FCSTD DOCUMENT  (FreeCAD 1.0R39285 (Git))
Label: SectsAndVioletsCharacterIcons
License: All rights reserved
LicenseURL: https://en.wikipedia.org/wiki/All_rights_reserved
objects: Sketcher::SketchObject×25, Part::Extrusion×25, Part::Scale×25, Spreadsheet::Sheet×1
note: 100 computed .brp shape members not serialized (recipe doc carries the construction recipe); baked Part::Feature solids carry a one-line shape summary decoded from their .brp

FEATURE [Sketcher::SketchObject] Sketch026  label="Artist-Sketch"
  ArcFitTolerance = 1e-06
  FullyConstrained = false
  MakeInternals = false
  Placement = pos=(-10.0713,14.6686,0) rot=(0,0,1;0rad)
  expr: .Placement.Base.x = -(.Shape.BoundBox.XLength / 2)
  expr: .Placement.Base.y = .Shape.BoundBox.YLength / 2
  sketch-geometry (304):
    g0: BSplineCurve PolesCount=4 KnotsCount=2 Degree=3 IsPeriodic=0
    g1: BSplineCurve PolesCount=4 KnotsCount=2 Degree=3 IsPeriodic=0
    g2: BSplineCurve PolesCount=4 KnotsCount=2 Degree=3 IsPeriodic=0
    g3: BSplineCurve PolesCount=4 KnotsCount=2 Degree=3 IsPeriodic=0
    g4: BSplineCurve PolesCount=4 KnotsCount=2 Degree=3 IsPeriodic=0
    g5: BSplineCurve PolesCount=4 KnotsCount=2 Degree=3 IsPeriodic=0
    g6: BSplineCurve PolesCount=4 KnotsCount=2 Degree=3 IsPeriodic=0
    g7: BSplineCurve PolesCount=4 KnotsCount=2 Degree=3 IsPeriodic=0
    g8: BSplineCurve PolesCount=4 KnotsCount=2 Degree=3 IsPeriodic=0
    g9: BSplineCurve PolesCount=4 KnotsCount=2 Degree=3 IsPeriodic=0
    g10: BSplineCurve PolesCount=4 KnotsCount=2 Degree=3 IsPeriodic=0
    g11: BSplineCurve PolesCount=4 KnotsCount=2 Degree=3 IsPeriodic=0
    g12: BSplineCurve PolesCount=4 KnotsCount=2 Degree=3 IsPeriodic=0
    g13: BSplineCurve PolesCount=4 KnotsCount=2 Degree=3 IsPeriodic=0
    g14: BSplineCurve PolesCount=4 KnotsCount=2 Degree=3 IsPeriodic=0
    g15: BSplineCurve PolesCount=4 KnotsCount=2 Degree=3 IsPeriodic=0
    g16: BSplineCurve PolesCount=4 KnotsCount=2 Degree=3 IsPeriodic=0
    g17: BSplineCurve PolesCount=4 KnotsCount=2 Degree=3 IsPeriodic=0
    g18: BSplineCurve PolesCount=4 KnotsCount=2 Degree=3 IsPeriodic=0
    g19: BSplineCurve PolesCount=4 KnotsCount=2 Degree=3 IsPeriodic=0
    g20: BSplineCurve PolesCount=4 KnotsCount=2 Degree=3 IsPeriodic=0
    g21: BSplineCurve PolesCount=4 KnotsCount=2 Degree=3 IsPeriodic=0
    g22: BSplineCurve PolesCount=4 KnotsCount=2 Degree=3 IsPeriodic=0
    g23: BSplineCurve PolesCount=4 KnotsCount=2 Degree=3 IsPeriodic=0
    g24: BSplineCurve PolesCount=4 KnotsCount=2 Degree=3 IsPeriodic=0
    g25: BSplineCurve PolesCount=4 KnotsCount=2 Degree=3 IsPeriodic=0
    g26: BSplineCurve PolesCount=4 KnotsCount=2 Degree=3 IsPeriodic=0
    g27: BSplineCurve PolesCount=4 KnotsCount=2 Degree=3 IsPeriodic=0
    g28: BSplineCurve PolesCount=4 KnotsCount=2 Degree=3 IsPeriodic=0
    g29: BSplineCurve PolesCount=4 KnotsCount=2 Degree=3 IsPeriodic=0
    g30: BSplineCurve PolesCount=4 KnotsCount=2 Degree=3 IsPeriodic=0
    g31: BSplineCurve PolesCount=4 KnotsCount=2 Degree=3 IsPeriodic=0
    g32: BSplineCurve PolesCount=4 KnotsCount=2 Degree=3 IsPeriodic=0
    g33: BSplineCurve PolesCount=4 KnotsCount=2 Degree=3 IsPeriodic=0
    g34: BSplineCurve PolesCount=4 KnotsCount=2 Degree=3 IsPeriodic=0
    g35: BSplineCurve PolesCount=4 KnotsCount=2 Degree=3 IsPeriodic=0
    g36: BSplineCurve PolesCount=4 KnotsCount=2 Degree=3 IsPeriodic=0
    g37: BSplineCurve PolesCount=4 KnotsCount=2 Degree=3 IsPeriodic=0
    g38: BSplineCurve PolesCount=4 KnotsCount=2 Degree=3 IsPeriodic=0
    g39: BSplineCurve PolesCount=4 KnotsCount=2 Degree=3 IsPeriodic=0
    g40: BSplineCurve PolesCount=4 KnotsCount=2 Degree=3 IsPeriodic=0
    g41: BSplineCurve PolesCount=4 KnotsCount=2 Degree=3 IsPeriodic=0
    g42: BSplineCurve PolesCount=4 KnotsCount=2 Degree=3 IsPeriodic=0
    g43: BSplineCurve PolesCount=4 KnotsCount=2 Degree=3 IsPeriodic=0
    g44: BSplineCurve PolesCount=4 KnotsCount=2 Degree=3 IsPeriodic=0
    g45: BSplineCurve PolesCount=4 KnotsCount=2 Degree=3 IsPeriodic=0
    g46: BSplineCurve PolesCount=4 KnotsCount=2 Degree=3 IsPeriodic=0
    g47: BSplineCurve PolesCount=4 KnotsCount=2 Degree=3 IsPeriodic=0
    g48: BSplineCurve PolesCount=4 KnotsCount=2 Degree=3 IsPeriodic=0
    g49: BSplineCurve PolesCount=2 KnotsCount=2 Degree=1 IsPeriodic=0
    g50: BSplineCurve PolesCount=2 KnotsCount=2 Degree=1 IsPeriodic=0
    g51: BSplineCurve PolesCount=4 KnotsCount=2 Degree=3 IsPeriodic=0
    g52: BSplineCurve PolesCount=4 KnotsCount=2 Degree=3 IsPeriodic=0
    g53: BSplineCurve PolesCount=4 KnotsCount=2 Degree=3 IsPeriodic=0
    g54: BSplineCurve PolesCount=4 KnotsCount=2 Degree=3 IsPeriodic=0
    g55: BSplineCurve PolesCount=4 KnotsCount=2 Degree=3 IsPeriodic=0
    g56: BSplineCurve PolesCount=4 KnotsCount=2 Degree=3 IsPeriodic=0
    g57: BSplineCurve PolesCount=4 KnotsCount=2 Degree=3 IsPeriodic=0
    g58: BSplineCurve PolesCount=4 KnotsCount=2 Degree=3 IsPeriodic=0
    g59: BSplineCurve PolesCount=4 KnotsCount=2 Degree=3 IsPeriodic=0
    g60: BSplineCurve PolesCount=4 KnotsCount=2 Degree=3 IsPeriodic=0
    g61: BSplineCurve PolesCount=4 KnotsCount=2 Degree=3 IsPeriodic=0
    g62: BSplineCurve PolesCount=4 KnotsCount=2 Degree=3 IsPeriodic=0
    g63: BSplineCurve PolesCount=4 KnotsCount=2 Degree=3 IsPeriodic=0
    g64: BSplineCurve PolesCount=4 KnotsCount=2 Degree=3 IsPeriodic=0
    g65: BSplineCurve PolesCount=4 KnotsCount=2 Degree=3 IsPeriodic=0
    g66: BSplineCurve PolesCount=4 KnotsCount=2 Degree=3 IsPeriodic=0
    g67: BSplineCurve PolesCount=4 KnotsCount=2 Degree=3 IsPeriodic=0
    g68: BSplineCurve PolesCount=2 KnotsCount=2 Degree=1 IsPeriodic=0
    g69: BSplineCurve PolesCount=2 KnotsCount=2 Degree=1 IsPeriodic=0
    g70: BSplineCurve PolesCount=4 KnotsCount=2 Degree=3 IsPeriodic=0
    g71: BSplineCurve PolesCount=4 KnotsCount=2 Degree=3 IsPeriodic=0
    g72: BSplineCurve PolesCount=4 KnotsCount=2 Degree=3 IsPeriodic=0
    g73: BSplineCurve PolesCount=4 KnotsCount=2 Degree=3 IsPeriodic=0
    g74: BSplineCurve PolesCount=4 KnotsCount=2 Degree=3 IsPeriodic=0
    g75: BSplineCurve PolesCount=4 KnotsCount=2 Degree=3 IsPeriodic=0
    g76: BSplineCurve PolesCount=4 KnotsCount=2 Degree=3 IsPeriodic=0
    g77: BSplineCurve PolesCount=4 KnotsCount=2 Degree=3 IsPeriodic=0
    g78: BSplineCurve PolesCount=4 KnotsCount=2 Degree=3 IsPeriodic=0
    g79: BSplineCurve PolesCount=4 KnotsCount=2 Degree=3 IsPeriodic=0
    g80: BSplineCurve PolesCount=4 KnotsCount=2 Degree=3 IsPeriodic=0
    g81: BSplineCurve PolesCount=4 KnotsCount=2 Degree=3 IsPeriodic=0
    g82: BSplineCurve PolesCount=4 KnotsCount=2 Degree=3 IsPeriodic=0
    g83: BSplineCurve PolesCount=4 KnotsCount=2 Degree=3 IsPeriodic=0
    g84: BSplineCurve PolesCount=4 KnotsCount=2 Degree=3 IsPeriodic=0
    g85: BSplineCurve PolesCount=2 KnotsCount=2 Degree=1 IsPeriodic=0
    g86: BSplineCurve PolesCount=2 KnotsCount=2 Degree=1 IsPeriodic=0
    g87: BSplineCurve PolesCount=4 KnotsCount=2 Degree=3 IsPeriodic=0
    g88: BSplineCurve PolesCount=4 KnotsCount=2 Degree=3 IsPeriodic=0
    g89: BSplineCurve PolesCount=4 KnotsCount=2 Degree=3 IsPeriodic=0
    g90: BSplineCurve PolesCount=4 KnotsCount=2 Degree=3 IsPeriodic=0
    g91: BSplineCurve PolesCount=4 KnotsCount=2 Degree=3 IsPeriodic=0
    g92: BSplineCurve PolesCount=4 KnotsCount=2 Degree=3 IsPeriodic=0
    g93: BSplineCurve PolesCount=4 KnotsCount=2 Degree=3 IsPeriodic=0
    g94: BSplineCurve PolesCount=4 KnotsCount=2 Degree=3 IsPeriodic=0
    g95: BSplineCurve PolesCount=2 KnotsCount=2 Degree=1 IsPeriodic=0
    g96: BSplineCurve PolesCount=2 KnotsCount=2 Degree=1 IsPeriodic=0
    g97: BSplineCurve PolesCount=4 KnotsCount=2 Degree=3 IsPeriodic=0
    g98: BSplineCurve PolesCount=4 KnotsCount=2 Degree=3 IsPeriodic=0
    g99: BSplineCurve PolesCount=4 KnotsCount=2 Degree=3 IsPeriodic=0
    g100: BSplineCurve PolesCount=4 KnotsCount=2 Degree=3 IsPeriodic=0
    g101: BSplineCurve PolesCount=4 KnotsCount=2 Degree=3 IsPeriodic=0
    g102: BSplineCurve PolesCount=4 KnotsCount=2 Degree=3 IsPeriodic=0
    g103: BSplineCurve PolesCount=4 KnotsCount=2 Degree=3 IsPeriodic=0
    g104: BSplineCurve PolesCount=4 KnotsCount=2 Degree=3 IsPeriodic=0
    g105: BSplineCurve PolesCount=4 KnotsCount=2 Degree=3 IsPeriodic=0
    g106: BSplineCurve PolesCount=4 KnotsCount=2 Degree=3 IsPeriodic=0
    g107: BSplineCurve PolesCount=4 KnotsCount=2 Degree=3 IsPeriodic=0
    g108: BSplineCurve PolesCount=4 KnotsCount=2 Degree=3 IsPeriodic=0
    g109: BSplineCurve PolesCount=4 KnotsCount=2 Degree=3 IsPeriodic=0
    g110: BSplineCurve PolesCount=4 KnotsCount=2 Degree=3 IsPeriodic=0
    g111: BSplineCurve PolesCount=4 KnotsCount=2 Degree=3 IsPeriodic=0
    g112: BSplineCurve PolesCount=4 KnotsCount=2 Degree=3 IsPeriodic=0
    g113: BSplineCurve PolesCount=4 KnotsCount=2 Degree=3 IsPeriodic=0
    g114: BSplineCurve PolesCount=4 KnotsCount=2 Degree=3 IsPeriodic=0
    g115: BSplineCurve PolesCount=4 KnotsCount=2 Degree=3 IsPeriodic=0
    g116: BSplineCurve PolesCount=4 KnotsCount=2 Degree=3 IsPeriodic=0
    g117: BSplineCurve PolesCount=4 KnotsCount=2 Degree=3 IsPeriodic=0
    g118: BSplineCurve PolesCount=4 KnotsCount=2 Degree=3 IsPeriodic=0
    g119: BSplineCurve PolesCount=4 KnotsCount=2 Degree=3 IsPeriodic=0
    g120: BSplineCurve PolesCount=4 KnotsCount=2 Degree=3 IsPeriodic=0
    g121: BSplineCurve PolesCount=4 KnotsCount=2 Degree=3 IsPeriodic=0
    g122: BSplineCurve PolesCount=4 KnotsCount=2 Degree=3 IsPeriodic=0
    g123: BSplineCurve PolesCount=4 KnotsCount=2 Degree=3 IsPeriodic=0
    g124: BSplineCurve PolesCount=4 KnotsCount=2 Degree=3 IsPeriodic=0
    g125: BSplineCurve PolesCount=4 KnotsCount=2 Degree=3 IsPeriodic=0
    g126: BSplineCurve PolesCount=4 KnotsCount=2 Degree=3 IsPeriodic=0
    g127: BSplineCurve PolesCount=4 KnotsCount=2 Degree=3 IsPeriodic=0
    g128: BSplineCurve PolesCount=4 KnotsCount=2 Degree=3 IsPeriodic=0
    g129: BSplineCurve PolesCount=4 KnotsCount=2 Degree=3 IsPeriodic=0
    g130: BSplineCurve PolesCount=4 KnotsCount=2 Degree=3 IsPeriodic=0
    g131: BSplineCurve PolesCount=4 KnotsCount=2 Degree=3 IsPeriodic=0
    g132: BSplineCurve PolesCount=4 KnotsCount=2 Degree=3 IsPeriodic=0
    g133: BSplineCurve PolesCount=4 KnotsCount=2 Degree=3 IsPeriodic=0
    g134: BSplineCurve PolesCount=2 KnotsCount=2 Degree=1 IsPeriodic=0
    g135: BSplineCurve PolesCount=2 KnotsCount=2 Degree=1 IsPeriodic=0
    g136: BSplineCurve PolesCount=4 KnotsCount=2 Degree=3 IsPeriodic=0
    g137: BSplineCurve PolesCount=4 KnotsCount=2 Degree=3 IsPeriodic=0
    g138: BSplineCurve PolesCount=4 KnotsCount=2 Degree=3 IsPeriodic=0
    g139: BSplineCurve PolesCount=4 KnotsCount=2 Degree=3 IsPeriodic=0
    g140: BSplineCurve PolesCount=4 KnotsCount=2 Degree=3 IsPeriodic=0
    g141: BSplineCurve PolesCount=4 KnotsCount=2 Degree=3 IsPeriodic=0
    g142: BSplineCurve PolesCount=4 KnotsCount=2 Degree=3 IsPeriodic=0
    g143: BSplineCurve PolesCount=4 KnotsCount=2 Degree=3 IsPeriodic=0
    g144: BSplineCurve PolesCount=2 KnotsCount=2 Degree=1 IsPeriodic=0
    g145: BSplineCurve PolesCount=2 KnotsCount=2 Degree=1 IsPeriodic=0
    g146: BSplineCurve PolesCount=4 KnotsCount=2 Degree=3 IsPeriodic=0
    g147: BSplineCurve PolesCount=4 KnotsCount=2 Degree=3 IsPeriodic=0
    g148: BSplineCurve PolesCount=4 KnotsCount=2 Degree=3 IsPeriodic=0
    g149: BSplineCurve PolesCount=4 KnotsCount=2 Degree=3 IsPeriodic=0
    g150: BSplineCurve PolesCount=4 KnotsCount=2 Degree=3 IsPeriodic=0
    g151: BSplineCurve PolesCount=4 KnotsCount=2 Degree=3 IsPeriodic=0
    g152: BSplineCurve PolesCount=4 KnotsCount=2 Degree=3 IsPeriodic=0
    g153: BSplineCurve PolesCount=4 KnotsCount=2 Degree=3 IsPeriodic=0
    g154: BSplineCurve PolesCount=4 KnotsCount=2 Degree=3 IsPeriodic=0
    g155: BSplineCurve PolesCount=4 KnotsCount=2 Degree=3 IsPeriodic=0
    g156: BSplineCurve PolesCount=4 KnotsCount=2 Degree=3 IsPeriodic=0
    g157: BSplineCurve PolesCount=4 KnotsCount=2 Degree=3 IsPeriodic=0
    g158: BSplineCurve PolesCount=4 KnotsCount=2 Degree=3 IsPeriodic=0
    g159: BSplineCurve PolesCount=4 KnotsCount=2 Degree=3 IsPeriodic=0
    g160: BSplineCurve PolesCount=4 KnotsCount=2 Degree=3 IsPeriodic=0
    g161: BSplineCurve PolesCount=4 KnotsCount=2 Degree=3 IsPeriodic=0
    g162: BSplineCurve PolesCount=4 KnotsCount=2 Degree=3 IsPeriodic=0
    g163: BSplineCurve PolesCount=4 KnotsCount=2 Degree=3 IsPeriodic=0
    g164: BSplineCurve PolesCount=4 KnotsCount=2 Degree=3 IsPeriodic=0
    g165: BSplineCurve PolesCount=4 KnotsCount=2 Degree=3 IsPeriodic=0
    g166: BSplineCurve PolesCount=4 KnotsCount=2 Degree=3 IsPeriodic=0
    g167: BSplineCurve PolesCount=4 KnotsCount=2 Degree=3 IsPeriodic=0
    g168: BSplineCurve PolesCount=4 KnotsCount=2 Degree=3 IsPeriodic=0
    g169: BSplineCurve PolesCount=4 KnotsCount=2 Degree=3 IsPeriodic=0
    g170: BSplineCurve PolesCount=4 KnotsCount=2 Degree=3 IsPeriodic=0
    g171: BSplineCurve PolesCount=4 KnotsCount=2 Degree=3 IsPeriodic=0
    g172: BSplineCurve PolesCount=4 KnotsCount=2 Degree=3 IsPeriodic=0
    g173: BSplineCurve PolesCount=4 KnotsCount=2 Degree=3 IsPeriodic=0
    g174: BSplineCurve PolesCount=4 KnotsCount=2 Degree=3 IsPeriodic=0
    g175: BSplineCurve PolesCount=4 KnotsCount=2 Degree=3 IsPeriodic=0
    g176: BSplineCurve PolesCount=4 KnotsCount=2 Degree=3 IsPeriodic=0
    g177: BSplineCurve PolesCount=4 KnotsCount=2 Degree=3 IsPeriodic=0
    g178: BSplineCurve PolesCount=4 KnotsCount=2 Degree=3 IsPeriodic=0
    g179: BSplineCurve PolesCount=4 KnotsCount=2 Degree=3 IsPeriodic=0
    g180: BSplineCurve PolesCount=4 KnotsCount=2 Degree=3 IsPeriodic=0
    g181: BSplineCurve PolesCount=4 KnotsCount=2 Degree=3 IsPeriodic=0
    g182: BSplineCurve PolesCount=4 KnotsCount=2 Degree=3 IsPeriodic=0
    g183: BSplineCurve PolesCount=4 KnotsCount=2 Degree=3 IsPeriodic=0
    g184: BSplineCurve PolesCount=4 KnotsCount=2 Degree=3 IsPeriodic=0
    g185: BSplineCurve PolesCount=4 KnotsCount=2 Degree=3 IsPeriodic=0
    g186: BSplineCurve PolesCount=4 KnotsCount=2 Degree=3 IsPeriodic=0
    g187: BSplineCurve PolesCount=4 KnotsCount=2 Degree=3 IsPeriodic=0
    g188: BSplineCurve PolesCount=4 KnotsCount=2 Degree=3 IsPeriodic=0
    g189: BSplineCurve PolesCount=4 KnotsCount=2 Degree=3 IsPeriodic=0
    g190: BSplineCurve PolesCount=4 KnotsCount=2 Degree=3 IsPeriodic=0
    g191: BSplineCurve PolesCount=4 KnotsCount=2 Degree=3 IsPeriodic=0
    g192: BSplineCurve PolesCount=4 KnotsCount=2 Degree=3 IsPeriodic=0
    g193: BSplineCurve PolesCount=4 KnotsCount=2 Degree=3 IsPeriodic=0
    g194: BSplineCurve PolesCount=4 KnotsCount=2 Degree=3 IsPeriodic=0
    g195: BSplineCurve PolesCount=4 KnotsCount=2 Degree=3 IsPeriodic=0
    g196: BSplineCurve PolesCount=4 KnotsCount=2 Degree=3 IsPeriodic=0
    g197: BSplineCurve PolesCount=4 KnotsCount=2 Degree=3 IsPeriodic=0
    g198: BSplineCurve PolesCount=4 KnotsCount=2 Degree=3 IsPeriodic=0
    g199: BSplineCurve PolesCount=4 KnotsCount=2 Degree=3 IsPeriodic=0
    g200: BSplineCurve PolesCount=4 KnotsCount=2 Degree=3 IsPeriodic=0
    g201: BSplineCurve PolesCount=4 KnotsCount=2 Degree=3 IsPeriodic=0
    g202: BSplineCurve PolesCount=2 KnotsCount=2 Degree=1 IsPeriodic=0
    g203: BSplineCurve PolesCount=2 KnotsCount=2 Degree=1 IsPeriodic=0
    g204: BSplineCurve PolesCount=4 KnotsCount=2 Degree=3 IsPeriodic=0
    g205: BSplineCurve PolesCount=4 KnotsCount=2 Degree=3 IsPeriodic=0
    g206: BSplineCurve PolesCount=4 KnotsCount=2 Degree=3 IsPeriodic=0
    g207: BSplineCurve PolesCount=4 KnotsCount=2 Degree=3 IsPeriodic=0
    g208: BSplineCurve PolesCount=4 KnotsCount=2 Degree=3 IsPeriodic=0
    g209: BSplineCurve PolesCount=4 KnotsCount=2 Degree=3 IsPeriodic=0
    g210: BSplineCurve PolesCount=4 KnotsCount=2 Degree=3 IsPeriodic=0
    g211: BSplineCurve PolesCount=2 KnotsCount=2 Degree=1 IsPeriodic=0
    g212: BSplineCurve PolesCount=2 KnotsCount=2 Degree=1 IsPeriodic=0
    g213: BSplineCurve PolesCount=4 KnotsCount=2 Degree=3 IsPeriodic=0
    g214: BSplineCurve PolesCount=4 KnotsCount=2 Degree=3 IsPeriodic=0
    g215: BSplineCurve PolesCount=4 KnotsCount=2 Degree=3 IsPeriodic=0
    g216: BSplineCurve PolesCount=4 KnotsCount=2 Degree=3 IsPeriodic=0
    g217: BSplineCurve PolesCount=4 KnotsCount=2 Degree=3 IsPeriodic=0
    g218: BSplineCurve PolesCount=4 KnotsCount=2 Degree=3 IsPeriodic=0
    g219: BSplineCurve PolesCount=4 KnotsCount=2 Degree=3 IsPeriodic=0
    g220: BSplineCurve PolesCount=4 KnotsCount=2 Degree=3 IsPeriodic=0
    g221: BSplineCurve PolesCount=4 KnotsCount=2 Degree=3 IsPeriodic=0
    g222: BSplineCurve PolesCount=4 KnotsCount=2 Degree=3 IsPeriodic=0
    g223: BSplineCurve PolesCount=4 KnotsCount=2 Degree=3 IsPeriodic=0
    g224: BSplineCurve PolesCount=4 KnotsCount=2 Degree=3 IsPeriodic=0
    g225: BSplineCurve PolesCount=4 KnotsCount=2 Degree=3 IsPeriodic=0
    g226: BSplineCurve PolesCount=4 KnotsCount=2 Degree=3 IsPeriodic=0
    g227: BSplineCurve PolesCount=4 KnotsCount=2 Degree=3 IsPeriodic=0
    g228: BSplineCurve PolesCount=4 KnotsCount=2 Degree=3 IsPeriodic=0
    g229: BSplineCurve PolesCount=4 KnotsCount=2 Degree=3 IsPeriodic=0
    g230: BSplineCurve PolesCount=4 KnotsCount=2 Degree=3 IsPeriodic=0
    g231: BSplineCurve PolesCount=4 KnotsCount=2 Degree=3 IsPeriodic=0
    g232: BSplineCurve PolesCount=4 KnotsCount=2 Degree=3 IsPeriodic=0
    g233: BSplineCurve PolesCount=4 KnotsCount=2 Degree=3 IsPeriodic=0
    g234: BSplineCurve PolesCount=4 KnotsCount=2 Degree=3 IsPeriodic=0
    g235: BSplineCurve PolesCount=4 KnotsCount=2 Degree=3 IsPeriodic=0
    g236: BSplineCurve PolesCount=4 KnotsCount=2 Degree=3 IsPeriodic=0
    g237: BSplineCurve PolesCount=4 KnotsCount=2 Degree=3 IsPeriodic=0
    g238: BSplineCurve PolesCount=4 KnotsCount=2 Degree=3 IsPeriodic=0
    g239: BSplineCurve PolesCount=4 KnotsCount=2 Degree=3 IsPeriodic=0
    g240: BSplineCurve PolesCount=4 KnotsCount=2 Degree=3 IsPeriodic=0
    g241: BSplineCurve PolesCount=4 KnotsCount=2 Degree=3 IsPeriodic=0
    g242: BSplineCurve PolesCount=4 KnotsCount=2 Degree=3 IsPeriodic=0
    g243: BSplineCurve PolesCount=4 KnotsCount=2 Degree=3 IsPeriodic=0
    g244: BSplineCurve PolesCount=4 KnotsCount=2 Degree=3 IsPeriodic=0
    g245: BSplineCurve PolesCount=4 KnotsCount=2 Degree=3 IsPeriodic=0
    g246: BSplineCurve PolesCount=4 KnotsCount=2 Degree=3 IsPeriodic=0
    g247: BSplineCurve PolesCount=4 KnotsCount=2 Degree=3 IsPeriodic=0
    g248: BSplineCurve PolesCount=4 KnotsCount=2 Degree=3 IsPeriodic=0
    g249: BSplineCurve PolesCount=4 KnotsCount=2 Degree=3 IsPeriodic=0
    g250: BSplineCurve PolesCount=4 KnotsCount=2 Degree=3 IsPeriodic=0
    g251: BSplineCurve PolesCount=4 KnotsCount=2 Degree=3 IsPeriodic=0
    g252: BSplineCurve PolesCount=4 KnotsCount=2 Degree=3 IsPeriodic=0
    g253: BSplineCurve PolesCount=4 KnotsCount=2 Degree=3 IsPeriodic=0
    g254: BSplineCurve PolesCount=4 KnotsCount=2 Degree=3 IsPeriodic=0
    g255: BSplineCurve PolesCount=4 KnotsCount=2 Degree=3 IsPeriodic=0
    g256: BSplineCurve PolesCount=4 KnotsCount=2 Degree=3 IsPeriodic=0
    g257: BSplineCurve PolesCount=4 KnotsCount=2 Degree=3 IsPeriodic=0
    g258: BSplineCurve PolesCount=4 KnotsCount=2 Degree=3 IsPeriodic=0
    g259: BSplineCurve PolesCount=4 KnotsCount=2 Degree=3 IsPeriodic=0
    g260: BSplineCurve PolesCount=4 KnotsCount=2 Degree=3 IsPeriodic=0
    g261: BSplineCurve PolesCount=4 KnotsCount=2 Degree=3 IsPeriodic=0
    g262: BSplineCurve PolesCount=4 KnotsCount=2 Degree=3 IsPeriodic=0
    g263: BSplineCurve PolesCount=4 KnotsCount=2 Degree=3 IsPeriodic=0
    g264: BSplineCurve PolesCount=4 KnotsCount=2 Degree=3 IsPeriodic=0
    g265: BSplineCurve PolesCount=4 KnotsCount=2 Degree=3 IsPeriodic=0
    g266: BSplineCurve PolesCount=4 KnotsCount=2 Degree=3 IsPeriodic=0
    g267: BSplineCurve PolesCount=4 KnotsCount=2 Degree=3 IsPeriodic=0
    g268: BSplineCurve PolesCount=4 KnotsCount=2 Degree=3 IsPeriodic=0
    g269: BSplineCurve PolesCount=4 KnotsCount=2 Degree=3 IsPeriodic=0
    g270: BSplineCurve PolesCount=4 KnotsCount=2 Degree=3 IsPeriodic=0
    g271: BSplineCurve PolesCount=4 KnotsCount=2 Degree=3 IsPeriodic=0
    g272: BSplineCurve PolesCount=4 KnotsCount=2 Degree=3 IsPeriodic=0
    g273: BSplineCurve PolesCount=4 KnotsCount=2 Degree=3 IsPeriodic=0
    g274: BSplineCurve PolesCount=4 KnotsCount=2 Degree=3 IsPeriodic=0
    g275: BSplineCurve PolesCount=4 KnotsCount=2 Degree=3 IsPeriodic=0
    g276: BSplineCurve PolesCount=4 KnotsCount=2 Degree=3 IsPeriodic=0
    g277: BSplineCurve PolesCount=4 KnotsCount=2 Degree=3 IsPeriodic=0
    g278: BSplineCurve PolesCount=4 KnotsCount=2 Degree=3 IsPeriodic=0
    g279: BSplineCurve PolesCount=2 KnotsCount=2 Degree=1 IsPeriodic=0
    g280: BSplineCurve PolesCount=2 KnotsCount=2 Degree=1 IsPeriodic=0
    g281: BSplineCurve PolesCount=4 KnotsCount=2 Degree=3 IsPeriodic=0
    g282: BSplineCurve PolesCount=4 KnotsCount=2 Degree=3 IsPeriodic=0
    g283: BSplineCurve PolesCount=4 KnotsCount=2 Degree=3 IsPeriodic=0
    g284: BSplineCurve PolesCount=4 KnotsCount=2 Degree=3 IsPeriodic=0
    g285: BSplineCurve PolesCount=4 KnotsCount=2 Degree=3 IsPeriodic=0
    g286: BSplineCurve PolesCount=4 KnotsCount=2 Degree=3 IsPeriodic=0
    g287: BSplineCurve PolesCount=4 KnotsCount=2 Degree=3 IsPeriodic=0
    g288: BSplineCurve PolesCount=4 KnotsCount=2 Degree=3 IsPeriodic=0
    g289: BSplineCurve PolesCount=4 KnotsCount=2 Degree=3 IsPeriodic=0
    g290: BSplineCurve PolesCount=4 KnotsCount=2 Degree=3 IsPeriodic=0
    g291: BSplineCurve PolesCount=4 KnotsCount=2 Degree=3 IsPeriodic=0
    g292: BSplineCurve PolesCount=4 KnotsCount=2 Degree=3 IsPeriodic=0
    g293: BSplineCurve PolesCount=4 KnotsCount=2 Degree=3 IsPeriodic=0
    g294: BSplineCurve PolesCount=4 KnotsCount=2 Degree=3 IsPeriodic=0
    g295: BSplineCurve PolesCount=4 KnotsCount=2 Degree=3 IsPeriodic=0
    g296: BSplineCurve PolesCount=4 KnotsCount=2 Degree=3 IsPeriodic=0
    g297: BSplineCurve PolesCount=2 KnotsCount=2 Degree=1 IsPeriodic=0
    g298: BSplineCurve PolesCount=4 KnotsCount=2 Degree=3 IsPeriodic=0
    g299: BSplineCurve PolesCount=4 KnotsCount=2 Degree=3 IsPeriodic=0
    g300: BSplineCurve PolesCount=4 KnotsCount=2 Degree=3 IsPeriodic=0
    g301: BSplineCurve PolesCount=4 KnotsCount=2 Degree=3 IsPeriodic=0
    g302: BSplineCurve PolesCount=4 KnotsCount=2 Degree=3 IsPeriodic=0
    g303: BSplineCurve PolesCount=2 KnotsCount=2 Degree=1 IsPeriodic=0
  constraints (304):
    c: Coincident(g0,g1)
    c: Coincident(g1,g2)
    c: Coincident(g2,g3)
    c: Coincident(g3,g4)
    c: Coincident(g4,g5)
    c: Coincident(g5,g6)
    c: Coincident(g6,g7)
    c: Coincident(g7,g8)
    c: Coincident(g8,g9)
    c: Coincident(g9,g10)
    c: Coincident(g10,g11)
    c: Coincident(g11,g12)
    c: Coincident(g12,g0)
    c: Coincident(g13,g14)
    c: Coincident(g14,g15)
    c: Coincident(g15,g16)
    c: Coincident(g16,g13)
    c: Coincident(g17,g18)
    c: Coincident(g18,g19)
    c: Coincident(g19,g17)
    c: Coincident(g20,g21)
    c: Coincident(g21,g22)
    c: Coincident(g22,g23)
    c: Coincident(g23,g24)
    c: Coincident(g24,g25)
    c: Coincident(g25,g26)
    c: Coincident(g26,g27)
    c: Coincident(g27,g28)
    c: Coincident(g28,g29)
    c: Coincident(g29,g30)
    c: Coincident(g30,g31)
    c: Coincident(g31,g32)
    c: Coincident(g32,g20)
    c: Coincident(g33,g34)
    c: Coincident(g34,g35)
    c: Coincident(g35,g36)
    c: Coincident(g36,g37)
    c: Coincident(g37,g38)
    c: Coincident(g38,g39)
    c: Coincident(g39,g40)
    c: Coincident(g40,g41)
    c: Coincident(g41,g42)
    c: Coincident(g42,g43)
    c: Coincident(g43,g44)
    c: Coincident(g44,g45)
    c: Coincident(g45,g46)
    c: Coincident(g46,g47)
    c: Coincident(g47,g48)
    c: Coincident(g48,g49)
    c: Coincident(g49,g50)
    c: Coincident(g50,g51)
    c: Coincident(g51,g52)
    c: Coincident(g52,g53)
    c: Coincident(g53,g54)
    c: Coincident(g54,g55)
    c: Coincident(g55,g56)
    c: Coincident(g56,g57)
    c: Coincident(g57,g58)
    c: Coincident(g58,g59)
    c: Coincident(g59,g60)
    c: Coincident(g60,g61)
    c: Coincident(g61,g62)
    c: Coincident(g62,g63)
    c: Coincident(g63,g64)
    c: Coincident(g64,g65)
    c: Coincident(g65,g66)
    c: Coincident(g66,g67)
    c: Coincident(g67,g68)
    c: Coincident(g68,g69)
    c: Coincident(g69,g70)
    c: Coincident(g70,g71)
    c: Coincident(g71,g72)
    c: Coincident(g72,g73)
    c: Coincident(g73,g74)
    c: Coincident(g74,g75)
    c: Coincident(g75,g76)
    c: Coincident(g76,g77)
    c: Coincident(g77,g78)
    c: Coincident(g78,g79)
    c: Coincident(g79,g80)
    c: Coincident(g80,g81)
    c: Coincident(g81,g82)
    c: Coincident(g82,g83)
    c: Coincident(g83,g84)
    c: Coincident(g84,g85)
    c: Coincident(g85,g86)
    c: Coincident(g86,g87)
    c: Coincident(g87,g88)
    c: Coincident(g88,g89)
    c: Coincident(g89,g90)
    c: Coincident(g90,g91)
    c: Coincident(g91,g92)
    c: Coincident(g92,g93)
    c: Coincident(g93,g94)
    c: Coincident(g94,g95)
    c: Coincident(g95,g96)
    c: Coincident(g96,g97)
    c: Coincident(g97,g98)
    c: Coincident(g98,g99)
    c: Coincident(g99,g100)
    c: Coincident(g101,g102)
    c: Coincident(g102,g103)
    c: Coincident(g104,g105)
    c: Coincident(g105,g106)
    c: Coincident(g106,g104)
    c: Coincident(g107,g108)
    c: Coincident(g108,g109)
    c: Coincident(g109,g107)
    c: Coincident(g110,g111)
    c: Coincident(g111,g112)
    c: Coincident(g112,g113)
    c: Coincident(g113,g114)
    c: Coincident(g114,g115)
    c: Coincident(g115,g116)
    c: Coincident(g116,g110)
    c: Coincident(g117,g118)
    c: Coincident(g118,g119)
    c: Coincident(g119,g120)
    c: Coincident(g120,g121)
    c: Coincident(g121,g122)
    c: Coincident(g122,g123)
    c: Coincident(g124,g125)
    c: Coincident(g125,g126)
    c: Coincident(g126,g127)
    c: Coincident(g127,g128)
    c: Coincident(g128,g129)
    c: Coincident(g129,g130)
    c: Coincident(g130,g124)
    c: Coincident(g131,g132)
    c: Coincident(g132,g133)
    c: Coincident(g133,g134)
    c: Coincident(g134,g135)
    c: Coincident(g135,g136)
    c: Coincident(g136,g137)
    c: Coincident(g137,g138)
    c: Coincident(g138,g139)
    c: Coincident(g139,g140)
    c: Coincident(g140,g141)
    c: Coincident(g141,g142)
    c: Coincident(g142,g143)
    c: Coincident(g143,g144)
    c: Coincident(g144,g145)
    c: Coincident(g145,g146)
    c: Coincident(g146,g147)
    c: Coincident(g147,g148)
    c: Coincident(g148,g149)
    c: Coincident(g149,g150)
    c: Coincident(g150,g151)
    c: Coincident(g151,g152)
    c: Coincident(g152,g153)
    c: Coincident(g153,g154)
    c: Coincident(g154,g155)
    c: Coincident(g155,g156)
    c: Coincident(g156,g157)
    c: Coincident(g157,g158)
    c: Coincident(g158,g159)
    c: Coincident(g159,g160)
    c: Coincident(g160,g161)
    c: Coincident(g161,g162)
    c: Coincident(g162,g163)
    c: Coincident(g163,g164)
    c: Coincident(g165,g166)
    c: Coincident(g166,g167)
    c: Coincident(g167,g168)
    c: Coincident(g168,g165)
    c: Coincident(g169,g170)
    c: Coincident(g170,g171)
    c: Coincident(g172,g173)
    c: Coincident(g173,g174)
    c: Coincident(g174,g172)
    c: Coincident(g175,g176)
    c: Coincident(g176,g177)
    c: Coincident(g178,g179)
    c: Coincident(g179,g180)
    c: Coincident(g180,g181)
    c: Coincident(g181,g182)
    c: Coincident(g182,g183)
    c: Coincident(g183,g184)
    c: Coincident(g184,g178)
    c: Coincident(g185,g186)
    c: Coincident(g186,g187)
    c: Coincident(g187,g188)
    c: Coincident(g188,g189)
    c: Coincident(g189,g190)
    c: Coincident(g190,g191)
    c: Coincident(g192,g193)
    c: Coincident(g193,g194)
    c: Coincident(g194,g192)
    c: Coincident(g195,g196)
    c: Coincident(g196,g197)
    c: Coincident(g197,g198)
    c: Coincident(g198,g195)
    c: Coincident(g199,g200)
    c: Coincident(g200,g201)
    c: Coincident(g201,g202)
    c: Coincident(g202,g203)
    c: Coincident(g203,g204)
    c: Coincident(g204,g205)
    c: Coincident(g205,g199)
    c: Coincident(g206,g207)
    c: Coincident(g207,g208)
    c: Coincident(g208,g209)
    c: Coincident(g209,g206)
    c: Coincident(g210,g211)
    c: Coincident(g211,g212)
    c: Coincident(g212,g213)
    c: Coincident(g213,g214)
    c: Coincident(g215,g216)
    c: Coincident(g216,g217)
    c: Coincident(g217,g218)
    c: Coincident(g218,g215)
    c: Coincident(g219,g220)
    c: Coincident(g220,g221)
    c: Coincident(g221,g219)
    c: Coincident(g222,g223)
    c: Coincident(g223,g224)
    c: Coincident(g224,g222)
    c: Coincident(g225,g226)
    c: Coincident(g226,g227)
    c: Coincident(g227,g228)
    c: Coincident(g228,g229)
    c: Coincident(g229,g230)
    c: Coincident(g230,g231)
    c: Coincident(g231,g232)
    c: Coincident(g232,g233)
    c: Coincident(g233,g234)
    c: Coincident(g234,g235)
    c: Coincident(g235,g236)
    c: Coincident(g236,g237)
    c: Coincident(g237,g238)
    c: Coincident(g238,g239)
    c: Coincident(g239,g240)
    c: Coincident(g240,g241)
    c: Coincident(g241,g242)
    c: Coincident(g242,g243)
    c: Coincident(g243,g244)
    c: Coincident(g245,g246)
    c: Coincident(g246,g247)
    c: Coincident(g247,g248)
    c: Coincident(g248,g249)
    c: Coincident(g249,g250)
    c: Coincident(g250,g245)
    c: Coincident(g251,g252)
    c: Coincident(g252,g253)
    c: Coincident(g253,g254)
    c: Coincident(g254,g255)
    c: Coincident(g255,g251)
    c: Coincident(g256,g257)
    c: Coincident(g257,g258)
    c: Coincident(g258,g259)
    c: Coincident(g259,g256)
    c: Coincident(g260,g261)
    c: Coincident(g261,g262)
    c: Coincident(g262,g263)
    c: Coincident(g263,g264)
    c: Coincident(g264,g265)
    c: Coincident(g265,g266)
    c: Coincident(g266,g267)
    c: Coincident(g267,g268)
    c: Coincident(g268,g269)
    c: Coincident(g269,g270)
    c: Coincident(g270,g271)
    c: Coincident(g271,g272)
    c: Coincident(g272,g273)
    c: Coincident(g273,g274)
    c: Coincident(g275,g276)
    c: Coincident(g276,g277)
    c: Coincident(g277,g275)
    c: Coincident(g278,g279)
    c: Coincident(g279,g280)
    c: Coincident(g280,g281)
    c: Coincident(g281,g282)
    c: Coincident(g283,g284)
    c: Coincident(g284,g285)
    c: Coincident(g285,g286)
    c: Coincident(g286,g283)
    c: Coincident(g287,g288)
    c: Coincident(g288,g289)
    c: Coincident(g290,g291)
    c: Coincident(g291,g292)
    c: Coincident(g292,g293)
    c: Coincident(g293,g294)
    c: Coincident(g294,g295)
    c: Coincident(g295,g296)
    c: Coincident(g296,g290)
    c: Coincident(g297,g298)
    c: Coincident(g298,g299)
    c: Coincident(g299,g300)
    c: Coincident(g300,g301)
    c: Coincident(g301,g302)
    c: Coincident(g302,g303)
    c: Coincident(g303,g297)
    c: Coincident(g100,g33)
    c: Coincident(g287,g289)
    c: Coincident(g260,g274)
    c: Coincident(g169,g171)
    c: Coincident(g131,g164)
    c: Coincident(g210,g214)
    c: Coincident(g225,g244)
    c: Coincident(g101,g103)
    c: Coincident(g117,g123)
    c: Coincident(g185,g191)
    c: Coincident(g278,g282)
    c: Coincident(g175,g177)
FEATURE [Sketcher::SketchObject] Sketch028  label="Barber-Sketch"
  ArcFitTolerance = 1e-06
  FullyConstrained = false
  MakeInternals = false
  Placement = pos=(-6.26557,17.2877,0) rot=(0,0,1;0rad)
  expr: .Placement.Base.x = -(.Shape.BoundBox.XLength / 2)
  expr: .Placement.Base.y = .Shape.BoundBox.YLength / 2
  sketch-geometry (177):
    g0: BSplineCurve PolesCount=4 KnotsCount=2 Degree=3 IsPeriodic=0
    g1: BSplineCurve PolesCount=4 KnotsCount=2 Degree=3 IsPeriodic=0
    g2: BSplineCurve PolesCount=4 KnotsCount=2 Degree=3 IsPeriodic=0
    g3: BSplineCurve PolesCount=4 KnotsCount=2 Degree=3 IsPeriodic=0
    g4: BSplineCurve PolesCount=2 KnotsCount=2 Degree=1 IsPeriodic=0
    g5: BSplineCurve PolesCount=2 KnotsCount=2 Degree=1 IsPeriodic=0
    g6: BSplineCurve PolesCount=4 KnotsCount=2 Degree=3 IsPeriodic=0
    g7: BSplineCurve PolesCount=4 KnotsCount=2 Degree=3 IsPeriodic=0
    g8: BSplineCurve PolesCount=4 KnotsCount=2 Degree=3 IsPeriodic=0
    g9: BSplineCurve PolesCount=4 KnotsCount=2 Degree=3 IsPeriodic=0
    g10: BSplineCurve PolesCount=4 KnotsCount=2 Degree=3 IsPeriodic=0
    g11: BSplineCurve PolesCount=4 KnotsCount=2 Degree=3 IsPeriodic=0
    g12: BSplineCurve PolesCount=2 KnotsCount=2 Degree=1 IsPeriodic=0
    g13: BSplineCurve PolesCount=2 KnotsCount=2 Degree=1 IsPeriodic=0
    g14: BSplineCurve PolesCount=4 KnotsCount=2 Degree=3 IsPeriodic=0
    g15: BSplineCurve PolesCount=4 KnotsCount=2 Degree=3 IsPeriodic=0
    g16: BSplineCurve PolesCount=4 KnotsCount=2 Degree=3 IsPeriodic=0
    g17: BSplineCurve PolesCount=4 KnotsCount=2 Degree=3 IsPeriodic=0
    g18: BSplineCurve PolesCount=4 KnotsCount=2 Degree=3 IsPeriodic=0
    g19: BSplineCurve PolesCount=4 KnotsCount=2 Degree=3 IsPeriodic=0
    g20: BSplineCurve PolesCount=4 KnotsCount=2 Degree=3 IsPeriodic=0
    g21: BSplineCurve PolesCount=4 KnotsCount=2 Degree=3 IsPeriodic=0
    g22: BSplineCurve PolesCount=4 KnotsCount=2 Degree=3 IsPeriodic=0
    g23: BSplineCurve PolesCount=4 KnotsCount=2 Degree=3 IsPeriodic=0
    g24: BSplineCurve PolesCount=4 KnotsCount=2 Degree=3 IsPeriodic=0
    g25: BSplineCurve PolesCount=4 KnotsCount=2 Degree=3 IsPeriodic=0
    g26: BSplineCurve PolesCount=4 KnotsCount=2 Degree=3 IsPeriodic=0
    g27: BSplineCurve PolesCount=4 KnotsCount=2 Degree=3 IsPeriodic=0
    g28: BSplineCurve PolesCount=4 KnotsCount=2 Degree=3 IsPeriodic=0
    g29: BSplineCurve PolesCount=4 KnotsCount=2 Degree=3 IsPeriodic=0
    g30: BSplineCurve PolesCount=4 KnotsCount=2 Degree=3 IsPeriodic=0
    g31: BSplineCurve PolesCount=4 KnotsCount=2 Degree=3 IsPeriodic=0
    g32: BSplineCurve PolesCount=4 KnotsCount=2 Degree=3 IsPeriodic=0
    g33: BSplineCurve PolesCount=4 KnotsCount=2 Degree=3 IsPeriodic=0
    g34: BSplineCurve PolesCount=2 KnotsCount=2 Degree=1 IsPeriodic=0
    g35: BSplineCurve PolesCount=2 KnotsCount=2 Degree=1 IsPeriodic=0
    g36: BSplineCurve PolesCount=4 KnotsCount=2 Degree=3 IsPeriodic=0
    g37: BSplineCurve PolesCount=4 KnotsCount=2 Degree=3 IsPeriodic=0
    g38: BSplineCurve PolesCount=4 KnotsCount=2 Degree=3 IsPeriodic=0
    g39: BSplineCurve PolesCount=4 KnotsCount=2 Degree=3 IsPeriodic=0
    g40: BSplineCurve PolesCount=4 KnotsCount=2 Degree=3 IsPeriodic=0
    g41: BSplineCurve PolesCount=4 KnotsCount=2 Degree=3 IsPeriodic=0
    g42: BSplineCurve PolesCount=4 KnotsCount=2 Degree=3 IsPeriodic=0
    g43: BSplineCurve PolesCount=4 KnotsCount=2 Degree=3 IsPeriodic=0
    g44: BSplineCurve PolesCount=2 KnotsCount=2 Degree=1 IsPeriodic=0
    g45: BSplineCurve PolesCount=2 KnotsCount=2 Degree=1 IsPeriodic=0
    g46: BSplineCurve PolesCount=4 KnotsCount=2 Degree=3 IsPeriodic=0
    g47: BSplineCurve PolesCount=4 KnotsCount=2 Degree=3 IsPeriodic=0
    g48: BSplineCurve PolesCount=4 KnotsCount=2 Degree=3 IsPeriodic=0
    g49: BSplineCurve PolesCount=4 KnotsCount=2 Degree=3 IsPeriodic=0
    g50: BSplineCurve PolesCount=4 KnotsCount=2 Degree=3 IsPeriodic=0
    g51: BSplineCurve PolesCount=4 KnotsCount=2 Degree=3 IsPeriodic=0
    g52: BSplineCurve PolesCount=4 KnotsCount=2 Degree=3 IsPeriodic=0
    g53: BSplineCurve PolesCount=4 KnotsCount=2 Degree=3 IsPeriodic=0
    g54: BSplineCurve PolesCount=4 KnotsCount=2 Degree=3 IsPeriodic=0
    g55: BSplineCurve PolesCount=4 KnotsCount=2 Degree=3 IsPeriodic=0
    g56: BSplineCurve PolesCount=4 KnotsCount=2 Degree=3 IsPeriodic=0
    g57: BSplineCurve PolesCount=4 KnotsCount=2 Degree=3 IsPeriodic=0
    g58: BSplineCurve PolesCount=4 KnotsCount=2 Degree=3 IsPeriodic=0
    g59: BSplineCurve PolesCount=4 KnotsCount=2 Degree=3 IsPeriodic=0
    g60: BSplineCurve PolesCount=4 KnotsCount=2 Degree=3 IsPeriodic=0
    g61: BSplineCurve PolesCount=4 KnotsCount=2 Degree=3 IsPeriodic=0
    g62: BSplineCurve PolesCount=2 KnotsCount=2 Degree=1 IsPeriodic=0
    g63: BSplineCurve PolesCount=2 KnotsCount=2 Degree=1 IsPeriodic=0
    g64: BSplineCurve PolesCount=4 KnotsCount=2 Degree=3 IsPeriodic=0
    g65: BSplineCurve PolesCount=4 KnotsCount=2 Degree=3 IsPeriodic=0
    g66: BSplineCurve PolesCount=4 KnotsCount=2 Degree=3 IsPeriodic=0
    g67: BSplineCurve PolesCount=2 KnotsCount=2 Degree=1 IsPeriodic=0
    g68: BSplineCurve PolesCount=2 KnotsCount=2 Degree=1 IsPeriodic=0
    g69: BSplineCurve PolesCount=4 KnotsCount=2 Degree=3 IsPeriodic=0
    g70: BSplineCurve PolesCount=4 KnotsCount=2 Degree=3 IsPeriodic=0
    g71: BSplineCurve PolesCount=4 KnotsCount=2 Degree=3 IsPeriodic=0
    g72: BSplineCurve PolesCount=2 KnotsCount=2 Degree=1 IsPeriodic=0
    g73: BSplineCurve PolesCount=2 KnotsCount=2 Degree=1 IsPeriodic=0
    g74: BSplineCurve PolesCount=4 KnotsCount=2 Degree=3 IsPeriodic=0
    g75: BSplineCurve PolesCount=4 KnotsCount=2 Degree=3 IsPeriodic=0
    g76: BSplineCurve PolesCount=4 KnotsCount=2 Degree=3 IsPeriodic=0
    g77: BSplineCurve PolesCount=2 KnotsCount=2 Degree=1 IsPeriodic=0
    g78: BSplineCurve PolesCount=2 KnotsCount=2 Degree=1 IsPeriodic=0
    g79: BSplineCurve PolesCount=4 KnotsCount=2 Degree=3 IsPeriodic=0
    g80: BSplineCurve PolesCount=4 KnotsCount=2 Degree=3 IsPeriodic=0
    g81: BSplineCurve PolesCount=2 KnotsCount=2 Degree=1 IsPeriodic=0
    g82: BSplineCurve PolesCount=2 KnotsCount=2 Degree=1 IsPeriodic=0
    g83: BSplineCurve PolesCount=2 KnotsCount=2 Degree=1 IsPeriodic=0
    g84: BSplineCurve PolesCount=2 KnotsCount=2 Degree=1 IsPeriodic=0
    g85: BSplineCurve PolesCount=4 KnotsCount=2 Degree=3 IsPeriodic=0
    g86: BSplineCurve PolesCount=4 KnotsCount=2 Degree=3 IsPeriodic=0
    g87: BSplineCurve PolesCount=4 KnotsCount=2 Degree=3 IsPeriodic=0
    g88: BSplineCurve PolesCount=4 KnotsCount=2 Degree=3 IsPeriodic=0
    g89: BSplineCurve PolesCount=4 KnotsCount=2 Degree=3 IsPeriodic=0
    g90: BSplineCurve PolesCount=4 KnotsCount=2 Degree=3 IsPeriodic=0
    g91: BSplineCurve PolesCount=4 KnotsCount=2 Degree=3 IsPeriodic=0
    g92: BSplineCurve PolesCount=4 KnotsCount=2 Degree=3 IsPeriodic=0
    g93: BSplineCurve PolesCount=4 KnotsCount=2 Degree=3 IsPeriodic=0
    g94: BSplineCurve PolesCount=4 KnotsCount=2 Degree=3 IsPeriodic=0
    g95: BSplineCurve PolesCount=4 KnotsCount=2 Degree=3 IsPeriodic=0
    g96: BSplineCurve PolesCount=4 KnotsCount=2 Degree=3 IsPeriodic=0
    g97: BSplineCurve PolesCount=4 KnotsCount=2 Degree=3 IsPeriodic=0
    g98: BSplineCurve PolesCount=4 KnotsCount=2 Degree=3 IsPeriodic=0
    g99: BSplineCurve PolesCount=4 KnotsCount=2 Degree=3 IsPeriodic=0
    g100: BSplineCurve PolesCount=4 KnotsCount=2 Degree=3 IsPeriodic=0
    g101: BSplineCurve PolesCount=4 KnotsCount=2 Degree=3 IsPeriodic=0
    g102: BSplineCurve PolesCount=4 KnotsCount=2 Degree=3 IsPeriodic=0
    g103: BSplineCurve PolesCount=4 KnotsCount=2 Degree=3 IsPeriodic=0
    g104: BSplineCurve PolesCount=4 KnotsCount=2 Degree=3 IsPeriodic=0
    g105: BSplineCurve PolesCount=4 KnotsCount=2 Degree=3 IsPeriodic=0
    g106: BSplineCurve PolesCount=4 KnotsCount=2 Degree=3 IsPeriodic=0
    g107: BSplineCurve PolesCount=4 KnotsCount=2 Degree=3 IsPeriodic=0
    g108: BSplineCurve PolesCount=4 KnotsCount=2 Degree=3 IsPeriodic=0
    g109: BSplineCurve PolesCount=4 KnotsCount=2 Degree=3 IsPeriodic=0
    g110: BSplineCurve PolesCount=4 KnotsCount=2 Degree=3 IsPeriodic=0
    g111: BSplineCurve PolesCount=4 KnotsCount=2 Degree=3 IsPeriodic=0
    g112: BSplineCurve PolesCount=4 KnotsCount=2 Degree=3 IsPeriodic=0
    g113: BSplineCurve PolesCount=4 KnotsCount=2 Degree=3 IsPeriodic=0
    g114: BSplineCurve PolesCount=4 KnotsCount=2 Degree=3 IsPeriodic=0
    g115: BSplineCurve PolesCount=4 KnotsCount=2 Degree=3 IsPeriodic=0
    g116: BSplineCurve PolesCount=4 KnotsCount=2 Degree=3 IsPeriodic=0
    g117: BSplineCurve PolesCount=4 KnotsCount=2 Degree=3 IsPeriodic=0
    g118: BSplineCurve PolesCount=4 KnotsCount=2 Degree=3 IsPeriodic=0
    g119: BSplineCurve PolesCount=4 KnotsCount=2 Degree=3 IsPeriodic=0
    g120: BSplineCurve PolesCount=4 KnotsCount=2 Degree=3 IsPeriodic=0
    g121: BSplineCurve PolesCount=4 KnotsCount=2 Degree=3 IsPeriodic=0
    g122: BSplineCurve PolesCount=4 KnotsCount=2 Degree=3 IsPeriodic=0
    g123: BSplineCurve PolesCount=4 KnotsCount=2 Degree=3 IsPeriodic=0
    g124: BSplineCurve PolesCount=4 KnotsCount=2 Degree=3 IsPeriodic=0
    g125: BSplineCurve PolesCount=4 KnotsCount=2 Degree=3 IsPeriodic=0
    g126: BSplineCurve PolesCount=4 KnotsCount=2 Degree=3 IsPeriodic=0
    g127: BSplineCurve PolesCount=4 KnotsCount=2 Degree=3 IsPeriodic=0
    g128: BSplineCurve PolesCount=4 KnotsCount=2 Degree=3 IsPeriodic=0
    g129: BSplineCurve PolesCount=4 KnotsCount=2 Degree=3 IsPeriodic=0
    g130: BSplineCurve PolesCount=4 KnotsCount=2 Degree=3 IsPeriodic=0
    g131: BSplineCurve PolesCount=4 KnotsCount=2 Degree=3 IsPeriodic=0
    g132: BSplineCurve PolesCount=4 KnotsCount=2 Degree=3 IsPeriodic=0
    g133: BSplineCurve PolesCount=4 KnotsCount=2 Degree=3 IsPeriodic=0
    g134: BSplineCurve PolesCount=2 KnotsCount=2 Degree=1 IsPeriodic=0
    g135: BSplineCurve PolesCount=2 KnotsCount=2 Degree=1 IsPeriodic=0
    g136: BSplineCurve PolesCount=4 KnotsCount=2 Degree=3 IsPeriodic=0
    g137: BSplineCurve PolesCount=4 KnotsCount=2 Degree=3 IsPeriodic=0
    g138: BSplineCurve PolesCount=4 KnotsCount=2 Degree=3 IsPeriodic=0
    g139: BSplineCurve PolesCount=4 KnotsCount=2 Degree=3 IsPeriodic=0
    g140: BSplineCurve PolesCount=4 KnotsCount=2 Degree=3 IsPeriodic=0
    g141: BSplineCurve PolesCount=4 KnotsCount=2 Degree=3 IsPeriodic=0
    g142: BSplineCurve PolesCount=4 KnotsCount=2 Degree=3 IsPeriodic=0
    g143: BSplineCurve PolesCount=4 KnotsCount=2 Degree=3 IsPeriodic=0
    g144: BSplineCurve PolesCount=4 KnotsCount=2 Degree=3 IsPeriodic=0
    g145: BSplineCurve PolesCount=4 KnotsCount=2 Degree=3 IsPeriodic=0
    g146: BSplineCurve PolesCount=4 KnotsCount=2 Degree=3 IsPeriodic=0
    g147: BSplineCurve PolesCount=4 KnotsCount=2 Degree=3 IsPeriodic=0
    g148: BSplineCurve PolesCount=4 KnotsCount=2 Degree=3 IsPeriodic=0
    g149: BSplineCurve PolesCount=4 KnotsCount=2 Degree=3 IsPeriodic=0
    g150: BSplineCurve PolesCount=4 KnotsCount=2 Degree=3 IsPeriodic=0
    g151: BSplineCurve PolesCount=4 KnotsCount=2 Degree=3 IsPeriodic=0
    g152: BSplineCurve PolesCount=4 KnotsCount=2 Degree=3 IsPeriodic=0
    g153: BSplineCurve PolesCount=4 KnotsCount=2 Degree=3 IsPeriodic=0
    g154: BSplineCurve PolesCount=4 KnotsCount=2 Degree=3 IsPeriodic=0
    g155: BSplineCurve PolesCount=4 KnotsCount=2 Degree=3 IsPeriodic=0
    g156: BSplineCurve PolesCount=4 KnotsCount=2 Degree=3 IsPeriodic=0
    g157: BSplineCurve PolesCount=4 KnotsCount=2 Degree=3 IsPeriodic=0
    g158: BSplineCurve PolesCount=4 KnotsCount=2 Degree=3 IsPeriodic=0
    g159: BSplineCurve PolesCount=4 KnotsCount=2 Degree=3 IsPeriodic=0
    g160: BSplineCurve PolesCount=2 KnotsCount=2 Degree=1 IsPeriodic=0
    g161: BSplineCurve PolesCount=2 KnotsCount=2 Degree=1 IsPeriodic=0
    g162: BSplineCurve PolesCount=4 KnotsCount=2 Degree=3 IsPeriodic=0
    g163: BSplineCurve PolesCount=4 KnotsCount=2 Degree=3 IsPeriodic=0
    g164: BSplineCurve PolesCount=4 KnotsCount=2 Degree=3 IsPeriodic=0
    g165: BSplineCurve PolesCount=4 KnotsCount=2 Degree=3 IsPeriodic=0
    g166: BSplineCurve PolesCount=4 KnotsCount=2 Degree=3 IsPeriodic=0
    g167: BSplineCurve PolesCount=4 KnotsCount=2 Degree=3 IsPeriodic=0
    g168: BSplineCurve PolesCount=4 KnotsCount=2 Degree=3 IsPeriodic=0
    g169: BSplineCurve PolesCount=4 KnotsCount=2 Degree=3 IsPeriodic=0
    g170: BSplineCurve PolesCount=2 KnotsCount=2 Degree=1 IsPeriodic=0
    g171: BSplineCurve PolesCount=4 KnotsCount=2 Degree=3 IsPeriodic=0
    g172: BSplineCurve PolesCount=4 KnotsCount=2 Degree=3 IsPeriodic=0
    g173: BSplineCurve PolesCount=4 KnotsCount=2 Degree=3 IsPeriodic=0
    g174: BSplineCurve PolesCount=2 KnotsCount=2 Degree=1 IsPeriodic=0
    g175: BSplineCurve PolesCount=2 KnotsCount=2 Degree=1 IsPeriodic=0
    g176: BSplineCurve PolesCount=2 KnotsCount=2 Degree=1 IsPeriodic=0
  constraints (177):
    c: Coincident(g0,g1)
    c: Coincident(g1,g2)
    c: Coincident(g2,g3)
    c: Coincident(g3,g4)
    c: Coincident(g4,g5)
    c: Coincident(g5,g6)
    c: Coincident(g6,g7)
    c: Coincident(g7,g8)
    c: Coincident(g8,g9)
    c: Coincident(g9,g10)
    c: Coincident(g10,g11)
    c: Coincident(g11,g12)
    c: Coincident(g12,g13)
    c: Coincident(g13,g14)
    c: Coincident(g14,g15)
    c: Coincident(g15,g16)
    c: Coincident(g16,g17)
    c: Coincident(g17,g18)
    c: Coincident(g18,g19)
    c: Coincident(g19,g20)
    c: Coincident(g20,g21)
    c: Coincident(g21,g22)
    c: Coincident(g22,g23)
    c: Coincident(g23,g24)
    c: Coincident(g24,g25)
    c: Coincident(g25,g26)
    c: Coincident(g26,g27)
    c: Coincident(g27,g28)
    c: Coincident(g28,g29)
    c: Coincident(g29,g30)
    c: Coincident(g30,g0)
    c: Coincident(g31,g32)
    c: Coincident(g32,g33)
    c: Coincident(g33,g34)
    c: Coincident(g34,g35)
    c: Coincident(g35,g36)
    c: Coincident(g37,g38)
    c: Coincident(g38,g39)
    c: Coincident(g39,g37)
    c: Coincident(g40,g41)
    c: Coincident(g41,g42)
    c: Coincident(g42,g40)
    c: Coincident(g43,g44)
    c: Coincident(g44,g45)
    c: Coincident(g45,g46)
    c: Coincident(g46,g47)
    c: Coincident(g47,g48)
    c: Coincident(g48,g49)
    c: Coincident(g49,g50)
    c: Coincident(g50,g51)
    c: Coincident(g52,g53)
    c: Coincident(g53,g54)
    c: Coincident(g54,g55)
    c: Coincident(g55,g56)
    c: Coincident(g56,g57)
    c: Coincident(g57,g58)
    c: Coincident(g58,g52)
    c: Coincident(g59,g60)
    c: Coincident(g60,g61)
    c: Coincident(g61,g62)
    c: Coincident(g62,g63)
    c: Coincident(g63,g64)
    c: Coincident(g64,g65)
    c: Coincident(g65,g59)
    c: Coincident(g66,g67)
    c: Coincident(g67,g68)
    c: Coincident(g68,g69)
    c: Coincident(g69,g70)
    c: Coincident(g70,g71)
    c: Coincident(g71,g72)
    c: Coincident(g72,g73)
    c: Coincident(g73,g74)
    c: Coincident(g74,g75)
    c: Coincident(g75,g76)
    c: Coincident(g77,g78)
    c: Coincident(g78,g79)
    c: Coincident(g79,g80)
    c: Coincident(g80,g81)
    c: Coincident(g81,g82)
    c: Coincident(g82,g83)
    c: Coincident(g83,g84)
    c: Coincident(g84,g85)
    c: Coincident(g85,g86)
    c: Coincident(g86,g87)
    c: Coincident(g87,g88)
    c: Coincident(g89,g90)
    c: Coincident(g90,g91)
    c: Coincident(g92,g93)
    c: Coincident(g93,g94)
    c: Coincident(g94,g95)
    c: Coincident(g95,g92)
    c: Coincident(g96,g97)
    c: Coincident(g97,g98)
    c: Coincident(g98,g99)
    c: Coincident(g99,g100)
    c: Coincident(g100,g101)
    c: Coincident(g101,g102)
    c: Coincident(g102,g103)
    c: Coincident(g103,g104)
    c: Coincident(g104,g105)
    c: Coincident(g105,g106)
    c: Coincident(g107,g108)
    c: Coincident(g108,g109)
    c: Coincident(g109,g110)
    c: Coincident(g110,g111)
    c: Coincident(g111,g112)
    c: Coincident(g112,g113)
    c: Coincident(g113,g114)
    c: Coincident(g114,g115)
    c: Coincident(g115,g116)
    c: Coincident(g116,g117)
    c: Coincident(g117,g118)
    c: Coincident(g118,g119)
    c: Coincident(g119,g120)
    c: Coincident(g120,g121)
    c: Coincident(g121,g122)
    c: Coincident(g122,g123)
    c: Coincident(g123,g124)
    c: Coincident(g125,g126)
    c: Coincident(g126,g127)
    c: Coincident(g127,g128)
    c: Coincident(g128,g129)
    c: Coincident(g129,g130)
    c: Coincident(g130,g131)
    c: Coincident(g131,g132)
    c: Coincident(g132,g133)
    c: Coincident(g133,g134)
    c: Coincident(g134,g135)
    c: Coincident(g135,g136)
    c: Coincident(g136,g137)
    c: Coincident(g137,g138)
    c: Coincident(g138,g139)
    c: Coincident(g139,g140)
    c: Coincident(g140,g141)
    c: Coincident(g141,g142)
    c: Coincident(g142,g143)
    c: Coincident(g143,g144)
    c: Coincident(g144,g145)
    c: Coincident(g145,g146)
    c: Coincident(g146,g147)
    c: Coincident(g147,g148)
    c: Coincident(g149,g150)
    c: Coincident(g150,g151)
    c: Coincident(g151,g152)
    c: Coincident(g152,g153)
    c: Coincident(g153,g154)
    c: Coincident(g154,g155)
    c: Coincident(g155,g156)
    c: Coincident(g156,g157)
    c: Coincident(g157,g158)
    c: Coincident(g158,g159)
    c: Coincident(g159,g160)
    c: Coincident(g160,g161)
    c: Coincident(g161,g162)
    c: Coincident(g162,g163)
    c: Coincident(g163,g149)
    c: Coincident(g164,g165)
    c: Coincident(g165,g166)
    c: Coincident(g166,g164)
    c: Coincident(g167,g168)
    c: Coincident(g168,g169)
    c: Coincident(g170,g171)
    c: Coincident(g171,g172)
    c: Coincident(g172,g173)
    c: Coincident(g173,g174)
    c: Coincident(g174,g175)
    c: Coincident(g175,g176)
    c: Coincident(g176,g170)
    c: Coincident(g167,g169)
    c: Coincident(g125,g148)
    c: Coincident(g31,g36)
    c: Coincident(g89,g91)
    c: Coincident(g107,g124)
    c: Coincident(g77,g88)
    c: Coincident(g66,g76)
    c: Coincident(g43,g51)
    c: Coincident(g96,g106)
FEATURE [Sketcher::SketchObject] Sketch029  label="Cerenovus-Sketch"
  ArcFitTolerance = 1e-06
  FullyConstrained = false
  MakeInternals = false
  Placement = pos=(-12.6291,14.3334,0) rot=(0,0,1;0rad)
  expr: .Placement.Base.x = -(.Shape.BoundBox.XLength / 2)
  expr: .Placement.Base.y = .Shape.BoundBox.YLength / 2
  sketch-geometry (455):
    g0: BSplineCurve PolesCount=4 KnotsCount=2 Degree=3 IsPeriodic=0
    g1: BSplineCurve PolesCount=4 KnotsCount=2 Degree=3 IsPeriodic=0
    g2: BSplineCurve PolesCount=4 KnotsCount=2 Degree=3 IsPeriodic=0
    g3: BSplineCurve PolesCount=4 KnotsCount=2 Degree=3 IsPeriodic=0
    g4: BSplineCurve PolesCount=4 KnotsCount=2 Degree=3 IsPeriodic=0
    g5: BSplineCurve PolesCount=2 KnotsCount=2 Degree=1 IsPeriodic=0
    g6: BSplineCurve PolesCount=2 KnotsCount=2 Degree=1 IsPeriodic=0
    g7: BSplineCurve PolesCount=4 KnotsCount=2 Degree=3 IsPeriodic=0
    g8: BSplineCurve PolesCount=4 KnotsCount=2 Degree=3 IsPeriodic=0
    g9: BSplineCurve PolesCount=2 KnotsCount=2 Degree=1 IsPeriodic=0
    g10: BSplineCurve PolesCount=2 KnotsCount=2 Degree=1 IsPeriodic=0
    g11: BSplineCurve PolesCount=4 KnotsCount=2 Degree=3 IsPeriodic=0
    g12: BSplineCurve PolesCount=4 KnotsCount=2 Degree=3 IsPeriodic=0
    g13: BSplineCurve PolesCount=4 KnotsCount=2 Degree=3 IsPeriodic=0
    g14: BSplineCurve PolesCount=4 KnotsCount=2 Degree=3 IsPeriodic=0
    g15: BSplineCurve PolesCount=4 KnotsCount=2 Degree=3 IsPeriodic=0
    g16: BSplineCurve PolesCount=4 KnotsCount=2 Degree=3 IsPeriodic=0
    g17: BSplineCurve PolesCount=4 KnotsCount=2 Degree=3 IsPeriodic=0
    g18: BSplineCurve PolesCount=4 KnotsCount=2 Degree=3 IsPeriodic=0
    g19: BSplineCurve PolesCount=4 KnotsCount=2 Degree=3 IsPeriodic=0
    g20: BSplineCurve PolesCount=4 KnotsCount=2 Degree=3 IsPeriodic=0
    g21: BSplineCurve PolesCount=4 KnotsCount=2 Degree=3 IsPeriodic=0
    g22: BSplineCurve PolesCount=4 KnotsCount=2 Degree=3 IsPeriodic=0
    g23: BSplineCurve PolesCount=4 KnotsCount=2 Degree=3 IsPeriodic=0
    g24: BSplineCurve PolesCount=4 KnotsCount=2 Degree=3 IsPeriodic=0
    g25: BSplineCurve PolesCount=4 KnotsCount=2 Degree=3 IsPeriodic=0
    g26: BSplineCurve PolesCount=4 KnotsCount=2 Degree=3 IsPeriodic=0
    g27: BSplineCurve PolesCount=4 KnotsCount=2 Degree=3 IsPeriodic=0
    g28: BSplineCurve PolesCount=4 KnotsCount=2 Degree=3 IsPeriodic=0
    g29: BSplineCurve PolesCount=4 KnotsCount=2 Degree=3 IsPeriodic=0
    g30: BSplineCurve PolesCount=4 KnotsCount=2 Degree=3 IsPeriodic=0
    g31: BSplineCurve PolesCount=2 KnotsCount=2 Degree=1 IsPeriodic=0
    g32: BSplineCurve PolesCount=2 KnotsCount=2 Degree=1 IsPeriodic=0
    g33: BSplineCurve PolesCount=4 KnotsCount=2 Degree=3 IsPeriodic=0
    g34: BSplineCurve PolesCount=4 KnotsCount=2 Degree=3 IsPeriodic=0
    g35: BSplineCurve PolesCount=2 KnotsCount=2 Degree=1 IsPeriodic=0
    g36: BSplineCurve PolesCount=2 KnotsCount=2 Degree=1 IsPeriodic=0
    g37: BSplineCurve PolesCount=4 KnotsCount=2 Degree=3 IsPeriodic=0
    g38: BSplineCurve PolesCount=4 KnotsCount=2 Degree=3 IsPeriodic=0
    g39: BSplineCurve PolesCount=4 KnotsCount=2 Degree=3 IsPeriodic=0
    g40: BSplineCurve PolesCount=4 KnotsCount=2 Degree=3 IsPeriodic=0
    g41: BSplineCurve PolesCount=4 KnotsCount=2 Degree=3 IsPeriodic=0
    g42: BSplineCurve PolesCount=4 KnotsCount=2 Degree=3 IsPeriodic=0
    g43: BSplineCurve PolesCount=4 KnotsCount=2 Degree=3 IsPeriodic=0
    g44: BSplineCurve PolesCount=4 KnotsCount=2 Degree=3 IsPeriodic=0
    g45: BSplineCurve PolesCount=4 KnotsCount=2 Degree=3 IsPeriodic=0
    g46: BSplineCurve PolesCount=4 KnotsCount=2 Degree=3 IsPeriodic=0
    g47: BSplineCurve PolesCount=4 KnotsCount=2 Degree=3 IsPeriodic=0
    g48: BSplineCurve PolesCount=4 KnotsCount=2 Degree=3 IsPeriodic=0
    g49: BSplineCurve PolesCount=4 KnotsCount=2 Degree=3 IsPeriodic=0
    g50: BSplineCurve PolesCount=4 KnotsCount=2 Degree=3 IsPeriodic=0
    g51: BSplineCurve PolesCount=4 KnotsCount=2 Degree=3 IsPeriodic=0
    g52: BSplineCurve PolesCount=4 KnotsCount=2 Degree=3 IsPeriodic=0
    g53: BSplineCurve PolesCount=4 KnotsCount=2 Degree=3 IsPeriodic=0
    g54: BSplineCurve PolesCount=2 KnotsCount=2 Degree=1 IsPeriodic=0
    g55: BSplineCurve PolesCount=2 KnotsCount=2 Degree=1 IsPeriodic=0
    g56: BSplineCurve PolesCount=4 KnotsCount=2 Degree=3 IsPeriodic=0
    g57: BSplineCurve PolesCount=4 KnotsCount=2 Degree=3 IsPeriodic=0
    g58: BSplineCurve PolesCount=4 KnotsCount=2 Degree=3 IsPeriodic=0
    g59: BSplineCurve PolesCount=4 KnotsCount=2 Degree=3 IsPeriodic=0
    g60: BSplineCurve PolesCount=4 KnotsCount=2 Degree=3 IsPeriodic=0
    g61: BSplineCurve PolesCount=4 KnotsCount=2 Degree=3 IsPeriodic=0
    g62: BSplineCurve PolesCount=4 KnotsCount=2 Degree=3 IsPeriodic=0
    g63: BSplineCurve PolesCount=2 KnotsCount=2 Degree=1 IsPeriodic=0
    g64: BSplineCurve PolesCount=2 KnotsCount=2 Degree=1 IsPeriodic=0
    g65: BSplineCurve PolesCount=4 KnotsCount=2 Degree=3 IsPeriodic=0
    g66: BSplineCurve PolesCount=4 KnotsCount=2 Degree=3 IsPeriodic=0
    g67: BSplineCurve PolesCount=4 KnotsCount=2 Degree=3 IsPeriodic=0
    g68: BSplineCurve PolesCount=4 KnotsCount=2 Degree=3 IsPeriodic=0
    g69: BSplineCurve PolesCount=4 KnotsCount=2 Degree=3 IsPeriodic=0
    g70: BSplineCurve PolesCount=4 KnotsCount=2 Degree=3 IsPeriodic=0
    g71: BSplineCurve PolesCount=4 KnotsCount=2 Degree=3 IsPeriodic=0
    g72: BSplineCurve PolesCount=4 KnotsCount=2 Degree=3 IsPeriodic=0
    g73: BSplineCurve PolesCount=4 KnotsCount=2 Degree=3 IsPeriodic=0
    g74: BSplineCurve PolesCount=4 KnotsCount=2 Degree=3 IsPeriodic=0
    g75: BSplineCurve PolesCount=4 KnotsCount=2 Degree=3 IsPeriodic=0
    g76: BSplineCurve PolesCount=4 KnotsCount=2 Degree=3 IsPeriodic=0
    g77: BSplineCurve PolesCount=4 KnotsCount=2 Degree=3 IsPeriodic=0
    g78: BSplineCurve PolesCount=4 KnotsCount=2 Degree=3 IsPeriodic=0
    g79: BSplineCurve PolesCount=4 KnotsCount=2 Degree=3 IsPeriodic=0
    g80: BSplineCurve PolesCount=4 KnotsCount=2 Degree=3 IsPeriodic=0
    g81: BSplineCurve PolesCount=4 KnotsCount=2 Degree=3 IsPeriodic=0
    g82: BSplineCurve PolesCount=4 KnotsCount=2 Degree=3 IsPeriodic=0
    g83: BSplineCurve PolesCount=4 KnotsCount=2 Degree=3 IsPeriodic=0
    g84: BSplineCurve PolesCount=4 KnotsCount=2 Degree=3 IsPeriodic=0
    g85: BSplineCurve PolesCount=4 KnotsCount=2 Degree=3 IsPeriodic=0
    g86: BSplineCurve PolesCount=4 KnotsCount=2 Degree=3 IsPeriodic=0
    g87: BSplineCurve PolesCount=4 KnotsCount=2 Degree=3 IsPeriodic=0
    g88: BSplineCurve PolesCount=4 KnotsCount=2 Degree=3 IsPeriodic=0
    g89: BSplineCurve PolesCount=4 KnotsCount=2 Degree=3 IsPeriodic=0
    g90: BSplineCurve PolesCount=4 KnotsCount=2 Degree=3 IsPeriodic=0
    g91: BSplineCurve PolesCount=4 KnotsCount=2 Degree=3 IsPeriodic=0
    g92: BSplineCurve PolesCount=4 KnotsCount=2 Degree=3 IsPeriodic=0
    g93: BSplineCurve PolesCount=4 KnotsCount=2 Degree=3 IsPeriodic=0
    g94: BSplineCurve PolesCount=4 KnotsCount=2 Degree=3 IsPeriodic=0
    g95: BSplineCurve PolesCount=4 KnotsCount=2 Degree=3 IsPeriodic=0
    g96: BSplineCurve PolesCount=4 KnotsCount=2 Degree=3 IsPeriodic=0
    g97: BSplineCurve PolesCount=4 KnotsCount=2 Degree=3 IsPeriodic=0
    g98: BSplineCurve PolesCount=4 KnotsCount=2 Degree=3 IsPeriodic=0
    g99: BSplineCurve PolesCount=4 KnotsCount=2 Degree=3 IsPeriodic=0
    g100: BSplineCurve PolesCount=4 KnotsCount=2 Degree=3 IsPeriodic=0
    g101: BSplineCurve PolesCount=4 KnotsCount=2 Degree=3 IsPeriodic=0
    g102: BSplineCurve PolesCount=4 KnotsCount=2 Degree=3 IsPeriodic=0
    g103: BSplineCurve PolesCount=4 KnotsCount=2 Degree=3 IsPeriodic=0
    g104: BSplineCurve PolesCount=4 KnotsCount=2 Degree=3 IsPeriodic=0
    g105: BSplineCurve PolesCount=4 KnotsCount=2 Degree=3 IsPeriodic=0
    g106: BSplineCurve PolesCount=2 KnotsCount=2 Degree=1 IsPeriodic=0
    g107: BSplineCurve PolesCount=2 KnotsCount=2 Degree=1 IsPeriodic=0
    g108: BSplineCurve PolesCount=4 KnotsCount=2 Degree=3 IsPeriodic=0
    g109: BSplineCurve PolesCount=2 KnotsCount=2 Degree=1 IsPeriodic=0
    g110: BSplineCurve PolesCount=2 KnotsCount=2 Degree=1 IsPeriodic=0
    g111: BSplineCurve PolesCount=4 KnotsCount=2 Degree=3 IsPeriodic=0
    g112: BSplineCurve PolesCount=2 KnotsCount=2 Degree=1 IsPeriodic=0
    g113: BSplineCurve PolesCount=2 KnotsCount=2 Degree=1 IsPeriodic=0
    g114: BSplineCurve PolesCount=4 KnotsCount=2 Degree=3 IsPeriodic=0
    g115: BSplineCurve PolesCount=4 KnotsCount=2 Degree=3 IsPeriodic=0
    g116: BSplineCurve PolesCount=4 KnotsCount=2 Degree=3 IsPeriodic=0
    g117: BSplineCurve PolesCount=4 KnotsCount=2 Degree=3 IsPeriodic=0
    g118: BSplineCurve PolesCount=2 KnotsCount=2 Degree=1 IsPeriodic=0
    g119: BSplineCurve PolesCount=2 KnotsCount=2 Degree=1 IsPeriodic=0
    g120: BSplineCurve PolesCount=4 KnotsCount=2 Degree=3 IsPeriodic=0
    g121: BSplineCurve PolesCount=4 KnotsCount=2 Degree=3 IsPeriodic=0
    g122: BSplineCurve PolesCount=4 KnotsCount=2 Degree=3 IsPeriodic=0
    g123: BSplineCurve PolesCount=4 KnotsCount=2 Degree=3 IsPeriodic=0
    g124: BSplineCurve PolesCount=4 KnotsCount=2 Degree=3 IsPeriodic=0
    g125: BSplineCurve PolesCount=4 KnotsCount=2 Degree=3 IsPeriodic=0
    g126: BSplineCurve PolesCount=2 KnotsCount=2 Degree=1 IsPeriodic=0
    g127: BSplineCurve PolesCount=2 KnotsCount=2 Degree=1 IsPeriodic=0
    g128: BSplineCurve PolesCount=4 KnotsCount=2 Degree=3 IsPeriodic=0
    g129: BSplineCurve PolesCount=4 KnotsCount=2 Degree=3 IsPeriodic=0
    g130: BSplineCurve PolesCount=4 KnotsCount=2 Degree=3 IsPeriodic=0
    g131: BSplineCurve PolesCount=4 KnotsCount=2 Degree=3 IsPeriodic=0
    g132: BSplineCurve PolesCount=2 KnotsCount=2 Degree=1 IsPeriodic=0
    g133: BSplineCurve PolesCount=2 KnotsCount=2 Degree=1 IsPeriodic=0
    g134: BSplineCurve PolesCount=4 KnotsCount=2 Degree=3 IsPeriodic=0
    g135: BSplineCurve PolesCount=4 KnotsCount=2 Degree=3 IsPeriodic=0
    g136: BSplineCurve PolesCount=4 KnotsCount=2 Degree=3 IsPeriodic=0
    g137: BSplineCurve PolesCount=4 KnotsCount=2 Degree=3 IsPeriodic=0
    g138: BSplineCurve PolesCount=2 KnotsCount=2 Degree=1 IsPeriodic=0
    g139: BSplineCurve PolesCount=2 KnotsCount=2 Degree=1 IsPeriodic=0
    g140: BSplineCurve PolesCount=4 KnotsCount=2 Degree=3 IsPeriodic=0
    g141: BSplineCurve PolesCount=4 KnotsCount=2 Degree=3 IsPeriodic=0
    g142: BSplineCurve PolesCount=2 KnotsCount=2 Degree=1 IsPeriodic=0
    g143: BSplineCurve PolesCount=2 KnotsCount=2 Degree=1 IsPeriodic=0
    g144: BSplineCurve PolesCount=4 KnotsCount=2 Degree=3 IsPeriodic=0
    g145: BSplineCurve PolesCount=4 KnotsCount=2 Degree=3 IsPeriodic=0
    g146: BSplineCurve PolesCount=4 KnotsCount=2 Degree=3 IsPeriodic=0
    g147: BSplineCurve PolesCount=4 KnotsCount=2 Degree=3 IsPeriodic=0
    g148: BSplineCurve PolesCount=4 KnotsCount=2 Degree=3 IsPeriodic=0
    g149: BSplineCurve PolesCount=4 KnotsCount=2 Degree=3 IsPeriodic=0
    g150: BSplineCurve PolesCount=4 KnotsCount=2 Degree=3 IsPeriodic=0
    g151: BSplineCurve PolesCount=2 KnotsCount=2 Degree=1 IsPeriodic=0
    g152: BSplineCurve PolesCount=2 KnotsCount=2 Degree=1 IsPeriodic=0
    g153: BSplineCurve PolesCount=2 KnotsCount=2 Degree=1 IsPeriodic=0
    g154: BSplineCurve PolesCount=2 KnotsCount=2 Degree=1 IsPeriodic=0
    g155: BSplineCurve PolesCount=4 KnotsCount=2 Degree=3 IsPeriodic=0
    g156: BSplineCurve PolesCount=4 KnotsCount=2 Degree=3 IsPeriodic=0
    g157: BSplineCurve PolesCount=4 KnotsCount=2 Degree=3 IsPeriodic=0
    g158: BSplineCurve PolesCount=4 KnotsCount=2 Degree=3 IsPeriodic=0
    g159: BSplineCurve PolesCount=4 KnotsCount=2 Degree=3 IsPeriodic=0
    g160: BSplineCurve PolesCount=4 KnotsCount=2 Degree=3 IsPeriodic=0
    g161: BSplineCurve PolesCount=4 KnotsCount=2 Degree=3 IsPeriodic=0
    g162: BSplineCurve PolesCount=4 KnotsCount=2 Degree=3 IsPeriodic=0
    g163: BSplineCurve PolesCount=4 KnotsCount=2 Degree=3 IsPeriodic=0
    g164: BSplineCurve PolesCount=4 KnotsCount=2 Degree=3 IsPeriodic=0
    g165: BSplineCurve PolesCount=4 KnotsCount=2 Degree=3 IsPeriodic=0
    g166: BSplineCurve PolesCount=4 KnotsCount=2 Degree=3 IsPeriodic=0
    g167: BSplineCurve PolesCount=4 KnotsCount=2 Degree=3 IsPeriodic=0
    g168: BSplineCurve PolesCount=4 KnotsCount=2 Degree=3 IsPeriodic=0
    g169: BSplineCurve PolesCount=4 KnotsCount=2 Degree=3 IsPeriodic=0
    g170: BSplineCurve PolesCount=4 KnotsCount=2 Degree=3 IsPeriodic=0
    g171: BSplineCurve PolesCount=4 KnotsCount=2 Degree=3 IsPeriodic=0
    g172: BSplineCurve PolesCount=4 KnotsCount=2 Degree=3 IsPeriodic=0
    g173: BSplineCurve PolesCount=4 KnotsCount=2 Degree=3 IsPeriodic=0
    g174: BSplineCurve PolesCount=4 KnotsCount=2 Degree=3 IsPeriodic=0
    g175: BSplineCurve PolesCount=4 KnotsCount=2 Degree=3 IsPeriodic=0
    g176: BSplineCurve PolesCount=4 KnotsCount=2 Degree=3 IsPeriodic=0
    g177: BSplineCurve PolesCount=4 KnotsCount=2 Degree=3 IsPeriodic=0
    g178: BSplineCurve PolesCount=4 KnotsCount=2 Degree=3 IsPeriodic=0
    g179: BSplineCurve PolesCount=4 KnotsCount=2 Degree=3 IsPeriodic=0
    g180: BSplineCurve PolesCount=2 KnotsCount=2 Degree=1 IsPeriodic=0
    g181: BSplineCurve PolesCount=4 KnotsCount=2 Degree=3 IsPeriodic=0
    g182: BSplineCurve PolesCount=4 KnotsCount=2 Degree=3 IsPeriodic=0
    g183: BSplineCurve PolesCount=4 KnotsCount=2 Degree=3 IsPeriodic=0
    g184: BSplineCurve PolesCount=4 KnotsCount=2 Degree=3 IsPeriodic=0
    g185: BSplineCurve PolesCount=4 KnotsCount=2 Degree=3 IsPeriodic=0
    g186: BSplineCurve PolesCount=4 KnotsCount=2 Degree=3 IsPeriodic=0
    g187: BSplineCurve PolesCount=4 KnotsCount=2 Degree=3 IsPeriodic=0
    g188: BSplineCurve PolesCount=4 KnotsCount=2 Degree=3 IsPeriodic=0
    g189: BSplineCurve PolesCount=4 KnotsCount=2 Degree=3 IsPeriodic=0
    g190: BSplineCurve PolesCount=2 KnotsCount=2 Degree=1 IsPeriodic=0
    g191: BSplineCurve PolesCount=4 KnotsCount=2 Degree=3 IsPeriodic=0
    g192: BSplineCurve PolesCount=4 KnotsCount=2 Degree=3 IsPeriodic=0
    g193: BSplineCurve PolesCount=4 KnotsCount=2 Degree=3 IsPeriodic=0
    g194: BSplineCurve PolesCount=2 KnotsCount=2 Degree=1 IsPeriodic=0
    g195: BSplineCurve PolesCount=4 KnotsCount=2 Degree=3 IsPeriodic=0
    g196: BSplineCurve PolesCount=4 KnotsCount=2 Degree=3 IsPeriodic=0
    g197: BSplineCurve PolesCount=2 KnotsCount=2 Degree=1 IsPeriodic=0
    g198: BSplineCurve PolesCount=2 KnotsCount=2 Degree=1 IsPeriodic=0
    g199: BSplineCurve PolesCount=4 KnotsCount=2 Degree=3 IsPeriodic=0
    g200: BSplineCurve PolesCount=4 KnotsCount=2 Degree=3 IsPeriodic=0
    g201: BSplineCurve PolesCount=2 KnotsCount=2 Degree=1 IsPeriodic=0
    g202: BSplineCurve PolesCount=2 KnotsCount=2 Degree=1 IsPeriodic=0
    g203: BSplineCurve PolesCount=4 KnotsCount=2 Degree=3 IsPeriodic=0
    g204: BSplineCurve PolesCount=4 KnotsCount=2 Degree=3 IsPeriodic=0
    g205: BSplineCurve PolesCount=4 KnotsCount=2 Degree=3 IsPeriodic=0
    g206: BSplineCurve PolesCount=4 KnotsCount=2 Degree=3 IsPeriodic=0
    g207: BSplineCurve PolesCount=4 KnotsCount=2 Degree=3 IsPeriodic=0
    g208: BSplineCurve PolesCount=4 KnotsCount=2 Degree=3 IsPeriodic=0
    g209: BSplineCurve PolesCount=4 KnotsCount=2 Degree=3 IsPeriodic=0
    g210: BSplineCurve PolesCount=4 KnotsCount=2 Degree=3 IsPeriodic=0
    g211: BSplineCurve PolesCount=4 KnotsCount=2 Degree=3 IsPeriodic=0
    g212: BSplineCurve PolesCount=2 KnotsCount=2 Degree=1 IsPeriodic=0
    g213: BSplineCurve PolesCount=2 KnotsCount=2 Degree=1 IsPeriodic=0
    g214: BSplineCurve PolesCount=4 KnotsCount=2 Degree=3 IsPeriodic=0
    g215: BSplineCurve PolesCount=4 KnotsCount=2 Degree=3 IsPeriodic=0
    g216: BSplineCurve PolesCount=4 KnotsCount=2 Degree=3 IsPeriodic=0
    g217: BSplineCurve PolesCount=4 KnotsCount=2 Degree=3 IsPeriodic=0
    g218: BSplineCurve PolesCount=4 KnotsCount=2 Degree=3 IsPeriodic=0
    g219: BSplineCurve PolesCount=2 KnotsCount=2 Degree=1 IsPeriodic=0
    g220: BSplineCurve PolesCount=2 KnotsCount=2 Degree=1 IsPeriodic=0
    g221: BSplineCurve PolesCount=4 KnotsCount=2 Degree=3 IsPeriodic=0
    g222: BSplineCurve PolesCount=4 KnotsCount=2 Degree=3 IsPeriodic=0
    g223: BSplineCurve PolesCount=4 KnotsCount=2 Degree=3 IsPeriodic=0
    g224: BSplineCurve PolesCount=4 KnotsCount=2 Degree=3 IsPeriodic=0
    g225: BSplineCurve PolesCount=4 KnotsCount=2 Degree=3 IsPeriodic=0
    g226: BSplineCurve PolesCount=4 KnotsCount=2 Degree=3 IsPeriodic=0
    g227: BSplineCurve PolesCount=4 KnotsCount=2 Degree=3 IsPeriodic=0
    g228: BSplineCurve PolesCount=4 KnotsCount=2 Degree=3 IsPeriodic=0
    g229: BSplineCurve PolesCount=4 KnotsCount=2 Degree=3 IsPeriodic=0
    g230: BSplineCurve PolesCount=2 KnotsCount=2 Degree=1 IsPeriodic=0
    g231: BSplineCurve PolesCount=2 KnotsCount=2 Degree=1 IsPeriodic=0
    g232: BSplineCurve PolesCount=4 KnotsCount=2 Degree=3 IsPeriodic=0
    g233: BSplineCurve PolesCount=4 KnotsCount=2 Degree=3 IsPeriodic=0
    g234: BSplineCurve PolesCount=4 KnotsCount=2 Degree=3 IsPeriodic=0
    g235: BSplineCurve PolesCount=4 KnotsCount=2 Degree=3 IsPeriodic=0
    g236: BSplineCurve PolesCount=4 KnotsCount=2 Degree=3 IsPeriodic=0
    g237: BSplineCurve PolesCount=4 KnotsCount=2 Degree=3 IsPeriodic=0
    g238: BSplineCurve PolesCount=4 KnotsCount=2 Degree=3 IsPeriodic=0
    g239: BSplineCurve PolesCount=4 KnotsCount=2 Degree=3 IsPeriodic=0
    g240: BSplineCurve PolesCount=4 KnotsCount=2 Degree=3 IsPeriodic=0
    g241: BSplineCurve PolesCount=4 KnotsCount=2 Degree=3 IsPeriodic=0
    g242: BSplineCurve PolesCount=4 KnotsCount=2 Degree=3 IsPeriodic=0
    g243: BSplineCurve PolesCount=4 KnotsCount=2 Degree=3 IsPeriodic=0
    g244: BSplineCurve PolesCount=4 KnotsCount=2 Degree=3 IsPeriodic=0
    g245: BSplineCurve PolesCount=4 KnotsCount=2 Degree=3 IsPeriodic=0
    g246: BSplineCurve PolesCount=2 KnotsCount=2 Degree=1 IsPeriodic=0
    g247: BSplineCurve PolesCount=2 KnotsCount=2 Degree=1 IsPeriodic=0
    g248: BSplineCurve PolesCount=4 KnotsCount=2 Degree=3 IsPeriodic=0
    g249: BSplineCurve PolesCount=4 KnotsCount=2 Degree=3 IsPeriodic=0
    g250: BSplineCurve PolesCount=4 KnotsCount=2 Degree=3 IsPeriodic=0
    g251: BSplineCurve PolesCount=4 KnotsCount=2 Degree=3 IsPeriodic=0
    g252: BSplineCurve PolesCount=4 KnotsCount=2 Degree=3 IsPeriodic=0
    g253: BSplineCurve PolesCount=4 KnotsCount=2 Degree=3 IsPeriodic=0
    g254: BSplineCurve PolesCount=4 KnotsCount=2 Degree=3 IsPeriodic=0
    g255: BSplineCurve PolesCount=4 KnotsCount=2 Degree=3 IsPeriodic=0
    g256: BSplineCurve PolesCount=4 KnotsCount=2 Degree=3 IsPeriodic=0
    g257: BSplineCurve PolesCount=4 KnotsCount=2 Degree=3 IsPeriodic=0
    g258: BSplineCurve PolesCount=4 KnotsCount=2 Degree=3 IsPeriodic=0
    g259: BSplineCurve PolesCount=4 KnotsCount=2 Degree=3 IsPeriodic=0
    g260: BSplineCurve PolesCount=4 KnotsCount=2 Degree=3 IsPeriodic=0
    g261: BSplineCurve PolesCount=2 KnotsCount=2 Degree=1 IsPeriodic=0
    g262: BSplineCurve PolesCount=2 KnotsCount=2 Degree=1 IsPeriodic=0
    g263: BSplineCurve PolesCount=2 KnotsCount=2 Degree=1 IsPeriodic=0
    g264: BSplineCurve PolesCount=2 KnotsCount=2 Degree=1 IsPeriodic=0
    g265: BSplineCurve PolesCount=4 KnotsCount=2 Degree=3 IsPeriodic=0
    g266: BSplineCurve PolesCount=4 KnotsCount=2 Degree=3 IsPeriodic=0
    g267: BSplineCurve PolesCount=4 KnotsCount=2 Degree=3 IsPeriodic=0
    g268: BSplineCurve PolesCount=4 KnotsCount=2 Degree=3 IsPeriodic=0
    g269: BSplineCurve PolesCount=2 KnotsCount=2 Degree=1 IsPeriodic=0
    g270: BSplineCurve PolesCount=2 KnotsCount=2 Degree=1 IsPeriodic=0
    g271: BSplineCurve PolesCount=2 KnotsCount=2 Degree=1 IsPeriodic=0
    g272: BSplineCurve PolesCount=2 KnotsCount=2 Degree=1 IsPeriodic=0
    g273: BSplineCurve PolesCount=2 KnotsCount=2 Degree=1 IsPeriodic=0
    g274: BSplineCurve PolesCount=2 KnotsCount=2 Degree=1 IsPeriodic=0
    g275: BSplineCurve PolesCount=4 KnotsCount=2 Degree=3 IsPeriodic=0
    g276: BSplineCurve PolesCount=4 KnotsCount=2 Degree=3 IsPeriodic=0
    g277: BSplineCurve PolesCount=4 KnotsCount=2 Degree=3 IsPeriodic=0
    g278: BSplineCurve PolesCount=4 KnotsCount=2 Degree=3 IsPeriodic=0
    g279: BSplineCurve PolesCount=4 KnotsCount=2 Degree=3 IsPeriodic=0
    g280: BSplineCurve PolesCount=4 KnotsCount=2 Degree=3 IsPeriodic=0
    g281: BSplineCurve PolesCount=2 KnotsCount=2 Degree=1 IsPeriodic=0
    g282: BSplineCurve PolesCount=2 KnotsCount=2 Degree=1 IsPeriodic=0
    g283: BSplineCurve PolesCount=4 KnotsCount=2 Degree=3 IsPeriodic=0
    g284: BSplineCurve PolesCount=4 KnotsCount=2 Degree=3 IsPeriodic=0
    g285: BSplineCurve PolesCount=4 KnotsCount=2 Degree=3 IsPeriodic=0
    g286: BSplineCurve PolesCount=4 KnotsCount=2 Degree=3 IsPeriodic=0
    g287: BSplineCurve PolesCount=4 KnotsCount=2 Degree=3 IsPeriodic=0
    g288: BSplineCurve PolesCount=4 KnotsCount=2 Degree=3 IsPeriodic=0
    g289: BSplineCurve PolesCount=4 KnotsCount=2 Degree=3 IsPeriodic=0
    g290: BSplineCurve PolesCount=4 KnotsCount=2 Degree=3 IsPeriodic=0
    g291: BSplineCurve PolesCount=4 KnotsCount=2 Degree=3 IsPeriodic=0
    g292: BSplineCurve PolesCount=4 KnotsCount=2 Degree=3 IsPeriodic=0
    g293: BSplineCurve PolesCount=4 KnotsCount=2 Degree=3 IsPeriodic=0
    g294: BSplineCurve PolesCount=4 KnotsCount=2 Degree=3 IsPeriodic=0
    g295: BSplineCurve PolesCount=2 KnotsCount=2 Degree=1 IsPeriodic=0
    g296: BSplineCurve PolesCount=2 KnotsCount=2 Degree=1 IsPeriodic=0
    g297: BSplineCurve PolesCount=4 KnotsCount=2 Degree=3 IsPeriodic=0
    g298: BSplineCurve PolesCount=4 KnotsCount=2 Degree=3 IsPeriodic=0
    g299: BSplineCurve PolesCount=4 KnotsCount=2 Degree=3 IsPeriodic=0
    g300: BSplineCurve PolesCount=4 KnotsCount=2 Degree=3 IsPeriodic=0
    g301: BSplineCurve PolesCount=4 KnotsCount=2 Degree=3 IsPeriodic=0
    g302: BSplineCurve PolesCount=4 KnotsCount=2 Degree=3 IsPeriodic=0
    g303: BSplineCurve PolesCount=4 KnotsCount=2 Degree=3 IsPeriodic=0
    g304: BSplineCurve PolesCount=2 KnotsCount=2 Degree=1 IsPeriodic=0
    g305: BSplineCurve PolesCount=2 KnotsCount=2 Degree=1 IsPeriodic=0
    g306: BSplineCurve PolesCount=2 KnotsCount=2 Degree=1 IsPeriodic=0
    g307: BSplineCurve PolesCount=2 KnotsCount=2 Degree=1 IsPeriodic=0
    g308: BSplineCurve PolesCount=4 KnotsCount=2 Degree=3 IsPeriodic=0
    g309: BSplineCurve PolesCount=4 KnotsCount=2 Degree=3 IsPeriodic=0
    g310: BSplineCurve PolesCount=4 KnotsCount=2 Degree=3 IsPeriodic=0
    g311: BSplineCurve PolesCount=4 KnotsCount=2 Degree=3 IsPeriodic=0
    g312: BSplineCurve PolesCount=4 KnotsCount=2 Degree=3 IsPeriodic=0
    g313: BSplineCurve PolesCount=4 KnotsCount=2 Degree=3 IsPeriodic=0
    g314: BSplineCurve PolesCount=2 KnotsCount=2 Degree=1 IsPeriodic=0
    g315: BSplineCurve PolesCount=2 KnotsCount=2 Degree=1 IsPeriodic=0
    g316: BSplineCurve PolesCount=4 KnotsCount=2 Degree=3 IsPeriodic=0
    g317: BSplineCurve PolesCount=4 KnotsCount=2 Degree=3 IsPeriodic=0
    g318: BSplineCurve PolesCount=4 KnotsCount=2 Degree=3 IsPeriodic=0
    g319: BSplineCurve PolesCount=4 KnotsCount=2 Degree=3 IsPeriodic=0
    g320: BSplineCurve PolesCount=4 KnotsCount=2 Degree=3 IsPeriodic=0
    g321: BSplineCurve PolesCount=2 KnotsCount=2 Degree=1 IsPeriodic=0
    g322: BSplineCurve PolesCount=2 KnotsCount=2 Degree=1 IsPeriodic=0
    g323: BSplineCurve PolesCount=2 KnotsCount=2 Degree=1 IsPeriodic=0
    g324: BSplineCurve PolesCount=2 KnotsCount=2 Degree=1 IsPeriodic=0
    g325: BSplineCurve PolesCount=4 KnotsCount=2 Degree=3 IsPeriodic=0
    g326: BSplineCurve PolesCount=2 KnotsCount=2 Degree=1 IsPeriodic=0
    g327: BSplineCurve PolesCount=2 KnotsCount=2 Degree=1 IsPeriodic=0
    g328: BSplineCurve PolesCount=2 KnotsCount=2 Degree=1 IsPeriodic=0
    g329: BSplineCurve PolesCount=2 KnotsCount=2 Degree=1 IsPeriodic=0
    g330: BSplineCurve PolesCount=4 KnotsCount=2 Degree=3 IsPeriodic=0
    g331: BSplineCurve PolesCount=4 KnotsCount=2 Degree=3 IsPeriodic=0
    g332: BSplineCurve PolesCount=2 KnotsCount=2 Degree=1 IsPeriodic=0
    g333: BSplineCurve PolesCount=2 KnotsCount=2 Degree=1 IsPeriodic=0
    g334: BSplineCurve PolesCount=4 KnotsCount=2 Degree=3 IsPeriodic=0
    g335: BSplineCurve PolesCount=4 KnotsCount=2 Degree=3 IsPeriodic=0
    g336: BSplineCurve PolesCount=4 KnotsCount=2 Degree=3 IsPeriodic=0
    g337: BSplineCurve PolesCount=4 KnotsCount=2 Degree=3 IsPeriodic=0
    g338: BSplineCurve PolesCount=4 KnotsCount=2 Degree=3 IsPeriodic=0
    g339: BSplineCurve PolesCount=4 KnotsCount=2 Degree=3 IsPeriodic=0
    g340: BSplineCurve PolesCount=2 KnotsCount=2 Degree=1 IsPeriodic=0
    g341: BSplineCurve PolesCount=2 KnotsCount=2 Degree=1 IsPeriodic=0
    g342: BSplineCurve PolesCount=2 KnotsCount=2 Degree=1 IsPeriodic=0
    g343: BSplineCurve PolesCount=2 KnotsCount=2 Degree=1 IsPeriodic=0
    g344: BSplineCurve PolesCount=2 KnotsCount=2 Degree=1 IsPeriodic=0
    g345: BSplineCurve PolesCount=2 KnotsCount=2 Degree=1 IsPeriodic=0
    g346: BSplineCurve PolesCount=4 KnotsCount=2 Degree=3 IsPeriodic=0
    g347: BSplineCurve PolesCount=4 KnotsCount=2 Degree=3 IsPeriodic=0
    g348: BSplineCurve PolesCount=4 KnotsCount=2 Degree=3 IsPeriodic=0
    g349: BSplineCurve PolesCount=4 KnotsCount=2 Degree=3 IsPeriodic=0
    g350: BSplineCurve PolesCount=4 KnotsCount=2 Degree=3 IsPeriodic=0
    g351: BSplineCurve PolesCount=4 KnotsCount=2 Degree=3 IsPeriodic=0
    g352: BSplineCurve PolesCount=4 KnotsCount=2 Degree=3 IsPeriodic=0
    g353: BSplineCurve PolesCount=4 KnotsCount=2 Degree=3 IsPeriodic=0
    g354: BSplineCurve PolesCount=4 KnotsCount=2 Degree=3 IsPeriodic=0
    g355: BSplineCurve PolesCount=4 KnotsCount=2 Degree=3 IsPeriodic=0
    g356: BSplineCurve PolesCount=4 KnotsCount=2 Degree=3 IsPeriodic=0
    g357: BSplineCurve PolesCount=4 KnotsCount=2 Degree=3 IsPeriodic=0
    g358: BSplineCurve PolesCount=2 KnotsCount=2 Degree=1 IsPeriodic=0
    g359: BSplineCurve PolesCount=2 KnotsCount=2 Degree=1 IsPeriodic=0
    g360: BSplineCurve PolesCount=4 KnotsCount=2 Degree=3 IsPeriodic=0
    g361: BSplineCurve PolesCount=4 KnotsCount=2 Degree=3 IsPeriodic=0
    g362: BSplineCurve PolesCount=4 KnotsCount=2 Degree=3 IsPeriodic=0
    g363: BSplineCurve PolesCount=4 KnotsCount=2 Degree=3 IsPeriodic=0
    g364: BSplineCurve PolesCount=4 KnotsCount=2 Degree=3 IsPeriodic=0
    g365: BSplineCurve PolesCount=4 KnotsCount=2 Degree=3 IsPeriodic=0
    g366: BSplineCurve PolesCount=4 KnotsCount=2 Degree=3 IsPeriodic=0
    g367: BSplineCurve PolesCount=4 KnotsCount=2 Degree=3 IsPeriodic=0
    g368: BSplineCurve PolesCount=2 KnotsCount=2 Degree=1 IsPeriodic=0
    g369: BSplineCurve PolesCount=2 KnotsCount=2 Degree=1 IsPeriodic=0
    g370: BSplineCurve PolesCount=4 KnotsCount=2 Degree=3 IsPeriodic=0
    g371: BSplineCurve PolesCount=4 KnotsCount=2 Degree=3 IsPeriodic=0
    g372: BSplineCurve PolesCount=4 KnotsCount=2 Degree=3 IsPeriodic=0
    g373: BSplineCurve PolesCount=4 KnotsCount=2 Degree=3 IsPeriodic=0
    g374: BSplineCurve PolesCount=4 KnotsCount=2 Degree=3 IsPeriodic=0
    g375: BSplineCurve PolesCount=4 KnotsCount=2 Degree=3 IsPeriodic=0
    g376: BSplineCurve PolesCount=4 KnotsCount=2 Degree=3 IsPeriodic=0
    g377: BSplineCurve PolesCount=4 KnotsCount=2 Degree=3 IsPeriodic=0
    g378: BSplineCurve PolesCount=4 KnotsCount=2 Degree=3 IsPeriodic=0
    g379: BSplineCurve PolesCount=4 KnotsCount=2 Degree=3 IsPeriodic=0
    g380: BSplineCurve PolesCount=4 KnotsCount=2 Degree=3 IsPeriodic=0
    g381: BSplineCurve PolesCount=4 KnotsCount=2 Degree=3 IsPeriodic=0
    g382: BSplineCurve PolesCount=4 KnotsCount=2 Degree=3 IsPeriodic=0
    g383: BSplineCurve PolesCount=4 KnotsCount=2 Degree=3 IsPeriodic=0
    g384: BSplineCurve PolesCount=4 KnotsCount=2 Degree=3 IsPeriodic=0
    g385: BSplineCurve PolesCount=4 KnotsCount=2 Degree=3 IsPeriodic=0
    g386: BSplineCurve PolesCount=4 KnotsCount=2 Degree=3 IsPeriodic=0
    g387: BSplineCurve PolesCount=4 KnotsCount=2 Degree=3 IsPeriodic=0
    g388: BSplineCurve PolesCount=4 KnotsCount=2 Degree=3 IsPeriodic=0
    g389: BSplineCurve PolesCount=4 KnotsCount=2 Degree=3 IsPeriodic=0
    g390: BSplineCurve PolesCount=4 KnotsCount=2 Degree=3 IsPeriodic=0
    g391: BSplineCurve PolesCount=4 KnotsCount=2 Degree=3 IsPeriodic=0
    g392: BSplineCurve PolesCount=4 KnotsCount=2 Degree=3 IsPeriodic=0
    g393: BSplineCurve PolesCount=4 KnotsCount=2 Degree=3 IsPeriodic=0
    g394: BSplineCurve PolesCount=4 KnotsCount=2 Degree=3 IsPeriodic=0
    g395: BSplineCurve PolesCount=4 KnotsCount=2 Degree=3 IsPeriodic=0
    g396: BSplineCurve PolesCount=4 KnotsCount=2 Degree=3 IsPeriodic=0
    g397: BSplineCurve PolesCount=4 KnotsCount=2 Degree=3 IsPeriodic=0
    g398: BSplineCurve PolesCount=4 KnotsCount=2 Degree=3 IsPeriodic=0
    g399: BSplineCurve PolesCount=4 KnotsCount=2 Degree=3 IsPeriodic=0
    ... +55 more geometry lines
  constraints (455):
    c: Coincident(g0,g1)
    c: Coincident(g1,g2)
    c: Coincident(g2,g3)
    c: Coincident(g3,g4)
    c: Coincident(g4,g5)
    c: Coincident(g5,g6)
    c: Coincident(g6,g7)
    c: Coincident(g7,g8)
    c: Coincident(g8,g9)
    c: Coincident(g9,g10)
    c: Coincident(g10,g11)
    c: Coincident(g11,g12)
    c: Coincident(g12,g13)
    c: Coincident(g13,g14)
    c: Coincident(g14,g15)
    c: Coincident(g15,g16)
    c: Coincident(g16,g17)
    c: Coincident(g17,g18)
    c: Coincident(g18,g19)
    c: Coincident(g19,g20)
    c: Coincident(g20,g21)
    c: Coincident(g21,g22)
    c: Coincident(g22,g23)
    c: Coincident(g23,g24)
    c: Coincident(g24,g25)
    c: Coincident(g25,g26)
    c: Coincident(g26,g27)
    c: Coincident(g27,g28)
    c: Coincident(g28,g29)
    c: Coincident(g29,g30)
    c: Coincident(g30,g31)
    c: Coincident(g31,g32)
    c: Coincident(g32,g33)
    c: Coincident(g33,g34)
    c: Coincident(g34,g35)
    c: Coincident(g35,g36)
    c: Coincident(g36,g37)
    c: Coincident(g37,g38)
    c: Coincident(g38,g39)
    c: Coincident(g39,g40)
    c: Coincident(g40,g41)
    c: Coincident(g41,g42)
    c: Coincident(g42,g43)
    c: Coincident(g43,g44)
    c: Coincident(g44,g45)
    c: Coincident(g45,g46)
    c: Coincident(g46,g47)
    c: Coincident(g47,g48)
    c: Coincident(g48,g49)
    c: Coincident(g49,g50)
    c: Coincident(g50,g51)
    c: Coincident(g52,g53)
    c: Coincident(g53,g54)
    c: Coincident(g54,g55)
    c: Coincident(g55,g56)
    c: Coincident(g56,g57)
    c: Coincident(g57,g58)
    c: Coincident(g58,g59)
    c: Coincident(g59,g60)
    c: Coincident(g60,g61)
    c: Coincident(g61,g62)
    c: Coincident(g62,g63)
    c: Coincident(g63,g64)
    c: Coincident(g64,g65)
    c: Coincident(g65,g66)
    c: Coincident(g66,g67)
    c: Coincident(g67,g68)
    c: Coincident(g68,g69)
    c: Coincident(g69,g70)
    c: Coincident(g70,g71)
    c: Coincident(g71,g72)
    c: Coincident(g72,g73)
    c: Coincident(g73,g74)
    c: Coincident(g74,g75)
    c: Coincident(g76,g77)
    c: Coincident(g77,g78)
    c: Coincident(g78,g79)
    c: Coincident(g79,g80)
    c: Coincident(g80,g81)
    c: Coincident(g81,g82)
    c: Coincident(g82,g83)
    c: Coincident(g83,g84)
    c: Coincident(g84,g85)
    c: Coincident(g85,g76)
    c: Coincident(g86,g87)
    c: Coincident(g87,g88)
    c: Coincident(g88,g89)
    c: Coincident(g89,g90)
    c: Coincident(g90,g91)
    c: Coincident(g91,g92)
    c: Coincident(g92,g93)
    c: Coincident(g93,g94)
    c: Coincident(g94,g95)
    c: Coincident(g95,g96)
    c: Coincident(g96,g97)
    c: Coincident(g97,g98)
    c: Coincident(g98,g99)
    c: Coincident(g99,g100)
    c: Coincident(g100,g101)
    c: Coincident(g101,g102)
    c: Coincident(g103,g104)
    c: Coincident(g104,g105)
    c: Coincident(g105,g106)
    c: Coincident(g106,g107)
    c: Coincident(g107,g108)
    c: Coincident(g108,g109)
    c: Coincident(g109,g110)
    c: Coincident(g110,g111)
    c: Coincident(g111,g112)
    c: Coincident(g112,g113)
    c: Coincident(g113,g114)
    c: Coincident(g114,g115)
    c: Coincident(g115,g116)
    c: Coincident(g116,g117)
    c: Coincident(g117,g118)
    c: Coincident(g118,g119)
    c: Coincident(g119,g120)
    c: Coincident(g120,g121)
    c: Coincident(g121,g122)
    c: Coincident(g122,g123)
    c: Coincident(g123,g124)
    c: Coincident(g124,g125)
    c: Coincident(g125,g126)
    c: Coincident(g126,g127)
    c: Coincident(g127,g128)
    c: Coincident(g128,g129)
    c: Coincident(g129,g130)
    c: Coincident(g130,g131)
    c: Coincident(g131,g132)
    c: Coincident(g132,g133)
    c: Coincident(g133,g134)
    c: Coincident(g134,g135)
    c: Coincident(g135,g136)
    c: Coincident(g136,g137)
    c: Coincident(g137,g138)
    c: Coincident(g138,g139)
    c: Coincident(g139,g140)
    c: Coincident(g140,g141)
    c: Coincident(g141,g142)
    c: Coincident(g142,g143)
    c: Coincident(g143,g144)
    c: Coincident(g144,g145)
    c: Coincident(g145,g146)
    c: Coincident(g146,g147)
    c: Coincident(g147,g148)
    c: Coincident(g149,g150)
    c: Coincident(g150,g151)
    c: Coincident(g151,g152)
    c: Coincident(g152,g153)
    c: Coincident(g153,g154)
    c: Coincident(g154,g149)
    c: Coincident(g155,g156)
    c: Coincident(g156,g157)
    c: Coincident(g157,g155)
    c: Coincident(g158,g159)
    c: Coincident(g159,g160)
    c: Coincident(g160,g158)
    c: Coincident(g161,g162)
    c: Coincident(g162,g163)
    c: Coincident(g163,g164)
    c: Coincident(g164,g161)
    c: Coincident(g165,g166)
    c: Coincident(g166,g167)
    c: Coincident(g168,g169)
    c: Coincident(g169,g170)
    c: Coincident(g170,g168)
    c: Coincident(g171,g172)
    c: Coincident(g172,g173)
    c: Coincident(g174,g175)
    c: Coincident(g175,g176)
    c: Coincident(g176,g174)
    c: Coincident(g177,g178)
    c: Coincident(g178,g179)
    c: Coincident(g179,g177)
    c: Coincident(g180,g181)
    c: Coincident(g181,g182)
    c: Coincident(g182,g183)
    c: Coincident(g183,g180)
    c: Coincident(g184,g185)
    c: Coincident(g185,g186)
    c: Coincident(g186,g184)
    c: Coincident(g187,g188)
    c: Coincident(g188,g189)
    c: Coincident(g189,g187)
    c: Coincident(g190,g191)
    c: Coincident(g191,g192)
    c: Coincident(g192,g193)
    c: Coincident(g193,g194)
    c: Coincident(g194,g190)
    c: Coincident(g195,g196)
    c: Coincident(g196,g197)
    c: Coincident(g197,g198)
    c: Coincident(g198,g199)
    c: Coincident(g199,g200)
    c: Coincident(g200,g201)
    c: Coincident(g201,g202)
    c: Coincident(g202,g195)
    c: Coincident(g203,g204)
    c: Coincident(g204,g205)
    c: Coincident(g205,g206)
    c: Coincident(g206,g207)
    c: Coincident(g207,g208)
    c: Coincident(g209,g210)
    c: Coincident(g210,g211)
    c: Coincident(g211,g212)
    c: Coincident(g212,g213)
    c: Coincident(g213,g214)
    c: Coincident(g214,g215)
    c: Coincident(g215,g216)
    c: Coincident(g216,g217)
    c: Coincident(g217,g218)
    c: Coincident(g218,g219)
    c: Coincident(g219,g220)
    c: Coincident(g220,g221)
    c: Coincident(g221,g222)
    c: Coincident(g222,g223)
    c: Coincident(g223,g224)
    c: Coincident(g224,g225)
    c: Coincident(g225,g226)
    c: Coincident(g226,g227)
    c: Coincident(g227,g228)
    c: Coincident(g228,g229)
    c: Coincident(g229,g230)
    c: Coincident(g230,g231)
    c: Coincident(g231,g232)
    c: Coincident(g232,g233)
    c: Coincident(g233,g234)
    c: Coincident(g234,g235)
    c: Coincident(g235,g236)
    c: Coincident(g236,g237)
    c: Coincident(g237,g238)
    c: Coincident(g238,g239)
    c: Coincident(g239,g240)
    c: Coincident(g240,g241)
    c: Coincident(g241,g242)
    c: Coincident(g242,g243)
    c: Coincident(g243,g244)
    c: Coincident(g244,g245)
    c: Coincident(g245,g246)
    c: Coincident(g246,g247)
    c: Coincident(g247,g248)
    c: Coincident(g248,g249)
    c: Coincident(g249,g250)
    c: Coincident(g250,g251)
    c: Coincident(g251,g252)
    c: Coincident(g252,g253)
    c: Coincident(g253,g254)
    c: Coincident(g254,g209)
    c: Coincident(g255,g256)
    c: Coincident(g256,g257)
    c: Coincident(g257,g255)
    c: Coincident(g258,g259)
    c: Coincident(g259,g260)
    c: Coincident(g260,g261)
    c: Coincident(g261,g262)
    c: Coincident(g262,g263)
    c: Coincident(g263,g264)
    c: Coincident(g264,g265)
    c: Coincident(g265,g266)
    c: Coincident(g267,g268)
    c: Coincident(g268,g269)
    c: Coincident(g269,g270)
    c: Coincident(g270,g271)
    c: Coincident(g271,g272)
    c: Coincident(g272,g273)
    c: Coincident(g273,g274)
    c: Coincident(g274,g275)
    c: Coincident(g276,g277)
    c: Coincident(g277,g278)
    c: Coincident(g278,g279)
    c: Coincident(g279,g280)
    c: Coincident(g280,g281)
    c: Coincident(g281,g282)
    c: Coincident(g282,g276)
    c: Coincident(g283,g284)
    c: Coincident(g284,g285)
    c: Coincident(g285,g286)
    c: Coincident(g286,g287)
    c: Coincident(g287,g288)
    c: Coincident(g288,g289)
    c: Coincident(g289,g283)
    c: Coincident(g290,g291)
    c: Coincident(g291,g292)
    c: Coincident(g292,g293)
    c: Coincident(g293,g294)
    c: Coincident(g294,g295)
    c: Coincident(g295,g296)
    c: Coincident(g296,g290)
    c: Coincident(g297,g298)
    c: Coincident(g298,g299)
    c: Coincident(g299,g297)
    c: Coincident(g300,g301)
    c: Coincident(g301,g302)
    c: Coincident(g302,g300)
    c: Coincident(g303,g304)
    c: Coincident(g304,g305)
    c: Coincident(g305,g306)
    c: Coincident(g306,g307)
    c: Coincident(g307,g308)
    c: Coincident(g308,g303)
    c: Coincident(g309,g310)
    c: Coincident(g310,g311)
    c: Coincident(g311,g312)
    c: Coincident(g312,g313)
    c: Coincident(g313,g314)
    c: Coincident(g314,g315)
    c: Coincident(g315,g316)
    c: Coincident(g316,g317)
    c: Coincident(g317,g318)
    c: Coincident(g318,g319)
    c: Coincident(g319,g320)
    c: Coincident(g320,g321)
    c: Coincident(g321,g322)
    c: Coincident(g322,g323)
    c: Coincident(g323,g324)
    c: Coincident(g324,g309)
    c: Coincident(g325,g326)
    c: Coincident(g326,g327)
    c: Coincident(g327,g328)
    c: Coincident(g328,g329)
    c: Coincident(g329,g330)
    c: Coincident(g330,g331)
    c: Coincident(g331,g332)
    c: Coincident(g332,g333)
    c: Coincident(g333,g334)
    c: Coincident(g335,g336)
    c: Coincident(g336,g337)
    c: Coincident(g337,g338)
    c: Coincident(g338,g335)
    c: Coincident(g339,g340)
    c: Coincident(g340,g341)
    c: Coincident(g341,g342)
    c: Coincident(g342,g343)
    c: Coincident(g343,g344)
    c: Coincident(g344,g345)
    c: Coincident(g345,g339)
    c: Coincident(g346,g347)
    c: Coincident(g347,g348)
    c: Coincident(g348,g349)
    c: Coincident(g349,g350)
    c: Coincident(g350,g351)
    c: Coincident(g351,g346)
    c: Coincident(g352,g353)
    c: Coincident(g353,g354)
    c: Coincident(g354,g352)
    c: Coincident(g355,g356)
    c: Coincident(g356,g357)
    c: Coincident(g357,g358)
    c: Coincident(g358,g359)
    c: Coincident(g359,g355)
    c: Coincident(g360,g361)
    c: Coincident(g361,g362)
    c: Coincident(g362,g360)
    c: Coincident(g363,g364)
    c: Coincident(g364,g365)
    c: Coincident(g365,g363)
    c: Coincident(g366,g367)
    c: Coincident(g367,g368)
    c: Coincident(g368,g369)
    c: Coincident(g369,g370)
    c: Coincident(g370,g371)
    c: Coincident(g371,g366)
    c: Coincident(g372,g373)
    c: Coincident(g373,g374)
    c: Coincident(g374,g375)
    c: Coincident(g375,g376)
    c: Coincident(g376,g377)
    c: Coincident(g377,g372)
    c: Coincident(g378,g379)
    c: Coincident(g379,g380)
    c: Coincident(g380,g381)
    c: Coincident(g381,g382)
    c: Coincident(g382,g378)
    c: Coincident(g383,g384)
    c: Coincident(g384,g385)
    c: Coincident(g385,g386)
    c: Coincident(g386,g383)
    c: Coincident(g387,g388)
    c: Coincident(g388,g389)
    c: Coincident(g389,g387)
    c: Coincident(g390,g391)
    c: Coincident(g391,g392)
    c: Coincident(g392,g393)
    c: Coincident(g393,g394)
    c: Coincident(g394,g395)
    c: Coincident(g395,g390)
    c: Coincident(g396,g397)
    c: Coincident(g397,g398)
    c: Coincident(g398,g396)
    c: Coincident(g400,g401)
    c: Coincident(g401,g399)
    c: Coincident(g403,g404)
    c: Coincident(g404,g402)
    c: Coincident(g406,g407)
    c: Coincident(g407,g408)
    c: Coincident(g408,g409)
    c: Coincident(g409,g410)
    c: Coincident(g410,g411)
    c: Coincident(g411,g412)
    c: Coincident(g412,g413)
    c: Coincident(g413,g414)
    c: Coincident(g414,g415)
    c: Coincident(g415,g416)
    c: Coincident(g416,g417)
    c: Coincident(g417,g418)
    c: Coincident(g418,g419)
    c: Coincident(g419,g420)
    c: Coincident(g420,g421)
    c: Coincident(g421,g422)
    c: Coincident(g422,g423)
    c: Coincident(g423,g424)
    c: Coincident(g424,g425)
    c: Coincident(g425,g426)
    c: Coincident(g426,g427)
    c: Coincident(g427,g428)
    c: Coincident(g428,g429)
    c: Coincident(g429,g430)
    c: Coincident(g430,g405)
    c: Coincident(g431,g432)
    c: Coincident(g432,g433)
    c: Coincident(g433,g434)
    c: Coincident(g434,g431)
    c: Coincident(g435,g436)
    c: Coincident(g436,g437)
    c: Coincident(g437,g435)
    c: Coincident(g438,g439)
    c: Coincident(g439,g440)
    c: Coincident(g440,g441)
    c: Coincident(g441,g442)
    c: Coincident(g442,g443)
    c: Coincident(g443,g444)
    c: Coincident(g444,g445)
    c: Coincident(g445,g438)
    c: Coincident(g447,g448)
    c: Coincident(g448,g446)
    c: Coincident(g450,g451)
    c: Coincident(g451,g449)
    c: Coincident(g452,g453)
    c: Coincident(g453,g454)
    c: Coincident(g454,g452)
    c: Coincident(g51,g0)
    c: Coincident(g148,g103)
    c: Coincident(g52,g75)
    c: Coincident(g86,g102)
    c: Coincident(g325,g334)
    c: Coincident(g267,g275)
    c: Coincident(g402,g403)
    c: Coincident(g399,g400)
    c: Coincident(g258,g266)
    c: Coincident(g203,g208)
    c: Coincident(g405,g406)
    c: Coincident(g449,g450)
    c: Coincident(g165,g167)
    c: Coincident(g446,g447)
    c: Coincident(g171,g173)
FEATURE [Sketcher::SketchObject] Sketch030  label="Clockmaker-Sketch"
  ArcFitTolerance = 1e-06
  FullyConstrained = false
  MakeInternals = false
  Placement = pos=(-14.3759,14.6472,0) rot=(0,0,1;0rad)
  expr: .Placement.Base.x = -(.Shape.BoundBox.XLength / 2)
  expr: .Placement.Base.y = .Shape.BoundBox.YLength / 2
  sketch-geometry (419):
    g0: BSplineCurve PolesCount=14 KnotsCount=2 Degree=13 IsPeriodic=0
    g1: BSplineCurve PolesCount=14 KnotsCount=2 Degree=13 IsPeriodic=0
    g2: BSplineCurve PolesCount=4 KnotsCount=2 Degree=3 IsPeriodic=0
    g3: BSplineCurve PolesCount=4 KnotsCount=2 Degree=3 IsPeriodic=0
    g4: BSplineCurve PolesCount=4 KnotsCount=2 Degree=3 IsPeriodic=0
    g5: BSplineCurve PolesCount=4 KnotsCount=2 Degree=3 IsPeriodic=0
    g6: BSplineCurve PolesCount=4 KnotsCount=2 Degree=3 IsPeriodic=0
    g7: BSplineCurve PolesCount=2 KnotsCount=2 Degree=1 IsPeriodic=0
    g8: BSplineCurve PolesCount=2 KnotsCount=2 Degree=1 IsPeriodic=0
    g9: BSplineCurve PolesCount=4 KnotsCount=2 Degree=3 IsPeriodic=0
    g10: BSplineCurve PolesCount=4 KnotsCount=2 Degree=3 IsPeriodic=0
    g11: BSplineCurve PolesCount=4 KnotsCount=2 Degree=3 IsPeriodic=0
    g12: BSplineCurve PolesCount=4 KnotsCount=2 Degree=3 IsPeriodic=0
    g13: BSplineCurve PolesCount=4 KnotsCount=2 Degree=3 IsPeriodic=0
    g14: BSplineCurve PolesCount=4 KnotsCount=2 Degree=3 IsPeriodic=0
    g15: BSplineCurve PolesCount=4 KnotsCount=2 Degree=3 IsPeriodic=0
    g16: BSplineCurve PolesCount=4 KnotsCount=2 Degree=3 IsPeriodic=0
    g17: BSplineCurve PolesCount=4 KnotsCount=2 Degree=3 IsPeriodic=0
    g18: BSplineCurve PolesCount=4 KnotsCount=2 Degree=3 IsPeriodic=0
    g19: BSplineCurve PolesCount=2 KnotsCount=2 Degree=1 IsPeriodic=0
    g20: BSplineCurve PolesCount=2 KnotsCount=2 Degree=1 IsPeriodic=0
    g21: BSplineCurve PolesCount=4 KnotsCount=2 Degree=3 IsPeriodic=0
    g22: BSplineCurve PolesCount=4 KnotsCount=2 Degree=3 IsPeriodic=0
    g23: BSplineCurve PolesCount=4 KnotsCount=2 Degree=3 IsPeriodic=0
    g24: BSplineCurve PolesCount=4 KnotsCount=2 Degree=3 IsPeriodic=0
    g25: BSplineCurve PolesCount=4 KnotsCount=2 Degree=3 IsPeriodic=0
    g26: BSplineCurve PolesCount=4 KnotsCount=2 Degree=3 IsPeriodic=0
    g27: BSplineCurve PolesCount=4 KnotsCount=2 Degree=3 IsPeriodic=0
    g28: BSplineCurve PolesCount=4 KnotsCount=2 Degree=3 IsPeriodic=0
    g29: BSplineCurve PolesCount=4 KnotsCount=2 Degree=3 IsPeriodic=0
    g30: BSplineCurve PolesCount=4 KnotsCount=2 Degree=3 IsPeriodic=0
    g31: BSplineCurve PolesCount=4 KnotsCount=2 Degree=3 IsPeriodic=0
    g32: BSplineCurve PolesCount=4 KnotsCount=2 Degree=3 IsPeriodic=0
    g33: BSplineCurve PolesCount=4 KnotsCount=2 Degree=3 IsPeriodic=0
    g34: BSplineCurve PolesCount=4 KnotsCount=2 Degree=3 IsPeriodic=0
    g35: BSplineCurve PolesCount=4 KnotsCount=2 Degree=3 IsPeriodic=0
    g36: BSplineCurve PolesCount=4 KnotsCount=2 Degree=3 IsPeriodic=0
    g37: BSplineCurve PolesCount=4 KnotsCount=2 Degree=3 IsPeriodic=0
    g38: BSplineCurve PolesCount=4 KnotsCount=2 Degree=3 IsPeriodic=0
    g39: BSplineCurve PolesCount=4 KnotsCount=2 Degree=3 IsPeriodic=0
    g40: BSplineCurve PolesCount=2 KnotsCount=2 Degree=1 IsPeriodic=0
    g41: BSplineCurve PolesCount=2 KnotsCount=2 Degree=1 IsPeriodic=0
    g42: BSplineCurve PolesCount=4 KnotsCount=2 Degree=3 IsPeriodic=0
    g43: BSplineCurve PolesCount=4 KnotsCount=2 Degree=3 IsPeriodic=0
    g44: BSplineCurve PolesCount=4 KnotsCount=2 Degree=3 IsPeriodic=0
    g45: BSplineCurve PolesCount=4 KnotsCount=2 Degree=3 IsPeriodic=0
    g46: BSplineCurve PolesCount=4 KnotsCount=2 Degree=3 IsPeriodic=0
    g47: BSplineCurve PolesCount=4 KnotsCount=2 Degree=3 IsPeriodic=0
    g48: BSplineCurve PolesCount=2 KnotsCount=2 Degree=1 IsPeriodic=0
    g49: BSplineCurve PolesCount=2 KnotsCount=2 Degree=1 IsPeriodic=0
    g50: BSplineCurve PolesCount=4 KnotsCount=2 Degree=3 IsPeriodic=0
    g51: BSplineCurve PolesCount=4 KnotsCount=2 Degree=3 IsPeriodic=0
    g52: BSplineCurve PolesCount=4 KnotsCount=2 Degree=3 IsPeriodic=0
    g53: BSplineCurve PolesCount=4 KnotsCount=2 Degree=3 IsPeriodic=0
    g54: BSplineCurve PolesCount=2 KnotsCount=2 Degree=1 IsPeriodic=0
    g55: BSplineCurve PolesCount=2 KnotsCount=2 Degree=1 IsPeriodic=0
    g56: BSplineCurve PolesCount=4 KnotsCount=2 Degree=3 IsPeriodic=0
    g57: BSplineCurve PolesCount=4 KnotsCount=2 Degree=3 IsPeriodic=0
    g58: BSplineCurve PolesCount=4 KnotsCount=2 Degree=3 IsPeriodic=0
    g59: BSplineCurve PolesCount=4 KnotsCount=2 Degree=3 IsPeriodic=0
    g60: BSplineCurve PolesCount=4 KnotsCount=2 Degree=3 IsPeriodic=0
    g61: BSplineCurve PolesCount=4 KnotsCount=2 Degree=3 IsPeriodic=0
    g62: BSplineCurve PolesCount=4 KnotsCount=2 Degree=3 IsPeriodic=0
    g63: BSplineCurve PolesCount=4 KnotsCount=2 Degree=3 IsPeriodic=0
    g64: BSplineCurve PolesCount=4 KnotsCount=2 Degree=3 IsPeriodic=0
    g65: BSplineCurve PolesCount=4 KnotsCount=2 Degree=3 IsPeriodic=0
    g66: BSplineCurve PolesCount=2 KnotsCount=2 Degree=1 IsPeriodic=0
    g67: BSplineCurve PolesCount=2 KnotsCount=2 Degree=1 IsPeriodic=0
    g68: BSplineCurve PolesCount=4 KnotsCount=2 Degree=3 IsPeriodic=0
    g69: BSplineCurve PolesCount=4 KnotsCount=2 Degree=3 IsPeriodic=0
    g70: BSplineCurve PolesCount=4 KnotsCount=2 Degree=3 IsPeriodic=0
    g71: BSplineCurve PolesCount=4 KnotsCount=2 Degree=3 IsPeriodic=0
    g72: BSplineCurve PolesCount=4 KnotsCount=2 Degree=3 IsPeriodic=0
    g73: BSplineCurve PolesCount=4 KnotsCount=2 Degree=3 IsPeriodic=0
    g74: BSplineCurve PolesCount=4 KnotsCount=2 Degree=3 IsPeriodic=0
    g75: BSplineCurve PolesCount=4 KnotsCount=2 Degree=3 IsPeriodic=0
    g76: BSplineCurve PolesCount=4 KnotsCount=2 Degree=3 IsPeriodic=0
    g77: BSplineCurve PolesCount=4 KnotsCount=2 Degree=3 IsPeriodic=0
    g78: BSplineCurve PolesCount=4 KnotsCount=2 Degree=3 IsPeriodic=0
    g79: BSplineCurve PolesCount=4 KnotsCount=2 Degree=3 IsPeriodic=0
    g80: BSplineCurve PolesCount=4 KnotsCount=2 Degree=3 IsPeriodic=0
    g81: BSplineCurve PolesCount=4 KnotsCount=2 Degree=3 IsPeriodic=0
    g82: BSplineCurve PolesCount=4 KnotsCount=2 Degree=3 IsPeriodic=0
    g83: BSplineCurve PolesCount=4 KnotsCount=2 Degree=3 IsPeriodic=0
    g84: BSplineCurve PolesCount=4 KnotsCount=2 Degree=3 IsPeriodic=0
    g85: BSplineCurve PolesCount=4 KnotsCount=2 Degree=3 IsPeriodic=0
    g86: BSplineCurve PolesCount=4 KnotsCount=2 Degree=3 IsPeriodic=0
    g87: BSplineCurve PolesCount=4 KnotsCount=2 Degree=3 IsPeriodic=0
    g88: BSplineCurve PolesCount=4 KnotsCount=2 Degree=3 IsPeriodic=0
    g89: BSplineCurve PolesCount=4 KnotsCount=2 Degree=3 IsPeriodic=0
    g90: BSplineCurve PolesCount=4 KnotsCount=2 Degree=3 IsPeriodic=0
    g91: BSplineCurve PolesCount=4 KnotsCount=2 Degree=3 IsPeriodic=0
    g92: BSplineCurve PolesCount=4 KnotsCount=2 Degree=3 IsPeriodic=0
    g93: BSplineCurve PolesCount=4 KnotsCount=2 Degree=3 IsPeriodic=0
    g94: BSplineCurve PolesCount=4 KnotsCount=2 Degree=3 IsPeriodic=0
    g95: BSplineCurve PolesCount=4 KnotsCount=2 Degree=3 IsPeriodic=0
    g96: BSplineCurve PolesCount=4 KnotsCount=2 Degree=3 IsPeriodic=0
    g97: BSplineCurve PolesCount=4 KnotsCount=2 Degree=3 IsPeriodic=0
    g98: BSplineCurve PolesCount=4 KnotsCount=2 Degree=3 IsPeriodic=0
    g99: BSplineCurve PolesCount=4 KnotsCount=2 Degree=3 IsPeriodic=0
    g100: BSplineCurve PolesCount=4 KnotsCount=2 Degree=3 IsPeriodic=0
    g101: BSplineCurve PolesCount=4 KnotsCount=2 Degree=3 IsPeriodic=0
    g102: BSplineCurve PolesCount=4 KnotsCount=2 Degree=3 IsPeriodic=0
    g103: BSplineCurve PolesCount=4 KnotsCount=2 Degree=3 IsPeriodic=0
    g104: BSplineCurve PolesCount=4 KnotsCount=2 Degree=3 IsPeriodic=0
    g105: BSplineCurve PolesCount=4 KnotsCount=2 Degree=3 IsPeriodic=0
    g106: BSplineCurve PolesCount=4 KnotsCount=2 Degree=3 IsPeriodic=0
    g107: BSplineCurve PolesCount=4 KnotsCount=2 Degree=3 IsPeriodic=0
    g108: BSplineCurve PolesCount=4 KnotsCount=2 Degree=3 IsPeriodic=0
    g109: BSplineCurve PolesCount=4 KnotsCount=2 Degree=3 IsPeriodic=0
    g110: BSplineCurve PolesCount=4 KnotsCount=2 Degree=3 IsPeriodic=0
    g111: BSplineCurve PolesCount=2 KnotsCount=2 Degree=1 IsPeriodic=0
    g112: BSplineCurve PolesCount=2 KnotsCount=2 Degree=1 IsPeriodic=0
    g113: BSplineCurve PolesCount=2 KnotsCount=2 Degree=1 IsPeriodic=0
    g114: BSplineCurve PolesCount=2 KnotsCount=2 Degree=1 IsPeriodic=0
    g115: BSplineCurve PolesCount=4 KnotsCount=2 Degree=3 IsPeriodic=0
    g116: BSplineCurve PolesCount=4 KnotsCount=2 Degree=3 IsPeriodic=0
    g117: BSplineCurve PolesCount=4 KnotsCount=2 Degree=3 IsPeriodic=0
    g118: BSplineCurve PolesCount=4 KnotsCount=2 Degree=3 IsPeriodic=0
    g119: BSplineCurve PolesCount=4 KnotsCount=2 Degree=3 IsPeriodic=0
    g120: BSplineCurve PolesCount=4 KnotsCount=2 Degree=3 IsPeriodic=0
    g121: BSplineCurve PolesCount=4 KnotsCount=2 Degree=3 IsPeriodic=0
    g122: BSplineCurve PolesCount=4 KnotsCount=2 Degree=3 IsPeriodic=0
    g123: BSplineCurve PolesCount=4 KnotsCount=2 Degree=3 IsPeriodic=0
    g124: BSplineCurve PolesCount=4 KnotsCount=2 Degree=3 IsPeriodic=0
    g125: BSplineCurve PolesCount=4 KnotsCount=2 Degree=3 IsPeriodic=0
    g126: BSplineCurve PolesCount=4 KnotsCount=2 Degree=3 IsPeriodic=0
    g127: BSplineCurve PolesCount=4 KnotsCount=2 Degree=3 IsPeriodic=0
    g128: BSplineCurve PolesCount=4 KnotsCount=2 Degree=3 IsPeriodic=0
    g129: BSplineCurve PolesCount=2 KnotsCount=2 Degree=1 IsPeriodic=0
    g130: BSplineCurve PolesCount=2 KnotsCount=2 Degree=1 IsPeriodic=0
    g131: BSplineCurve PolesCount=4 KnotsCount=2 Degree=3 IsPeriodic=0
    g132: BSplineCurve PolesCount=4 KnotsCount=2 Degree=3 IsPeriodic=0
    g133: BSplineCurve PolesCount=4 KnotsCount=2 Degree=3 IsPeriodic=0
    g134: BSplineCurve PolesCount=4 KnotsCount=2 Degree=3 IsPeriodic=0
    g135: BSplineCurve PolesCount=4 KnotsCount=2 Degree=3 IsPeriodic=0
    g136: BSplineCurve PolesCount=4 KnotsCount=2 Degree=3 IsPeriodic=0
    g137: BSplineCurve PolesCount=2 KnotsCount=2 Degree=1 IsPeriodic=0
    g138: BSplineCurve PolesCount=2 KnotsCount=2 Degree=1 IsPeriodic=0
    g139: BSplineCurve PolesCount=4 KnotsCount=2 Degree=3 IsPeriodic=0
    g140: BSplineCurve PolesCount=4 KnotsCount=2 Degree=3 IsPeriodic=0
    g141: BSplineCurve PolesCount=4 KnotsCount=2 Degree=3 IsPeriodic=0
    g142: BSplineCurve PolesCount=4 KnotsCount=2 Degree=3 IsPeriodic=0
    g143: BSplineCurve PolesCount=4 KnotsCount=2 Degree=3 IsPeriodic=0
    g144: BSplineCurve PolesCount=4 KnotsCount=2 Degree=3 IsPeriodic=0
    g145: BSplineCurve PolesCount=4 KnotsCount=2 Degree=3 IsPeriodic=0
    g146: BSplineCurve PolesCount=4 KnotsCount=2 Degree=3 IsPeriodic=0
    g147: BSplineCurve PolesCount=4 KnotsCount=2 Degree=3 IsPeriodic=0
    g148: BSplineCurve PolesCount=4 KnotsCount=2 Degree=3 IsPeriodic=0
    g149: BSplineCurve PolesCount=2 KnotsCount=2 Degree=1 IsPeriodic=0
    g150: BSplineCurve PolesCount=2 KnotsCount=2 Degree=1 IsPeriodic=0
    g151: BSplineCurve PolesCount=4 KnotsCount=2 Degree=3 IsPeriodic=0
    g152: BSplineCurve PolesCount=4 KnotsCount=2 Degree=3 IsPeriodic=0
    g153: BSplineCurve PolesCount=4 KnotsCount=2 Degree=3 IsPeriodic=0
    g154: BSplineCurve PolesCount=4 KnotsCount=2 Degree=3 IsPeriodic=0
    g155: BSplineCurve PolesCount=4 KnotsCount=2 Degree=3 IsPeriodic=0
    g156: BSplineCurve PolesCount=4 KnotsCount=2 Degree=3 IsPeriodic=0
    g157: BSplineCurve PolesCount=4 KnotsCount=2 Degree=3 IsPeriodic=0
    g158: BSplineCurve PolesCount=4 KnotsCount=2 Degree=3 IsPeriodic=0
    g159: BSplineCurve PolesCount=4 KnotsCount=2 Degree=3 IsPeriodic=0
    g160: BSplineCurve PolesCount=4 KnotsCount=2 Degree=3 IsPeriodic=0
    g161: BSplineCurve PolesCount=4 KnotsCount=2 Degree=3 IsPeriodic=0
    g162: BSplineCurve PolesCount=4 KnotsCount=2 Degree=3 IsPeriodic=0
    g163: BSplineCurve PolesCount=4 KnotsCount=2 Degree=3 IsPeriodic=0
    g164: BSplineCurve PolesCount=4 KnotsCount=2 Degree=3 IsPeriodic=0
    g165: BSplineCurve PolesCount=4 KnotsCount=2 Degree=3 IsPeriodic=0
    g166: BSplineCurve PolesCount=4 KnotsCount=2 Degree=3 IsPeriodic=0
    g167: BSplineCurve PolesCount=4 KnotsCount=2 Degree=3 IsPeriodic=0
    g168: BSplineCurve PolesCount=4 KnotsCount=2 Degree=3 IsPeriodic=0
    g169: BSplineCurve PolesCount=4 KnotsCount=2 Degree=3 IsPeriodic=0
    g170: BSplineCurve PolesCount=4 KnotsCount=2 Degree=3 IsPeriodic=0
    g171: BSplineCurve PolesCount=4 KnotsCount=2 Degree=3 IsPeriodic=0
    g172: BSplineCurve PolesCount=4 KnotsCount=2 Degree=3 IsPeriodic=0
    g173: BSplineCurve PolesCount=4 KnotsCount=2 Degree=3 IsPeriodic=0
    g174: BSplineCurve PolesCount=4 KnotsCount=2 Degree=3 IsPeriodic=0
    g175: BSplineCurve PolesCount=4 KnotsCount=2 Degree=3 IsPeriodic=0
    g176: BSplineCurve PolesCount=4 KnotsCount=2 Degree=3 IsPeriodic=0
    g177: BSplineCurve PolesCount=4 KnotsCount=2 Degree=3 IsPeriodic=0
    g178: BSplineCurve PolesCount=4 KnotsCount=2 Degree=3 IsPeriodic=0
    g179: BSplineCurve PolesCount=2 KnotsCount=2 Degree=1 IsPeriodic=0
    g180: BSplineCurve PolesCount=2 KnotsCount=2 Degree=1 IsPeriodic=0
    g181: BSplineCurve PolesCount=4 KnotsCount=2 Degree=3 IsPeriodic=0
    g182: BSplineCurve PolesCount=4 KnotsCount=2 Degree=3 IsPeriodic=0
    g183: BSplineCurve PolesCount=4 KnotsCount=2 Degree=3 IsPeriodic=0
    g184: BSplineCurve PolesCount=4 KnotsCount=2 Degree=3 IsPeriodic=0
    g185: BSplineCurve PolesCount=4 KnotsCount=2 Degree=3 IsPeriodic=0
    g186: BSplineCurve PolesCount=4 KnotsCount=2 Degree=3 IsPeriodic=0
    g187: BSplineCurve PolesCount=4 KnotsCount=2 Degree=3 IsPeriodic=0
    g188: BSplineCurve PolesCount=2 KnotsCount=2 Degree=1 IsPeriodic=0
    g189: BSplineCurve PolesCount=2 KnotsCount=2 Degree=1 IsPeriodic=0
    g190: BSplineCurve PolesCount=4 KnotsCount=2 Degree=3 IsPeriodic=0
    g191: BSplineCurve PolesCount=4 KnotsCount=2 Degree=3 IsPeriodic=0
    g192: BSplineCurve PolesCount=4 KnotsCount=2 Degree=3 IsPeriodic=0
    g193: BSplineCurve PolesCount=4 KnotsCount=2 Degree=3 IsPeriodic=0
    g194: BSplineCurve PolesCount=4 KnotsCount=2 Degree=3 IsPeriodic=0
    g195: BSplineCurve PolesCount=4 KnotsCount=2 Degree=3 IsPeriodic=0
    g196: BSplineCurve PolesCount=4 KnotsCount=2 Degree=3 IsPeriodic=0
    g197: BSplineCurve PolesCount=4 KnotsCount=2 Degree=3 IsPeriodic=0
    g198: BSplineCurve PolesCount=4 KnotsCount=2 Degree=3 IsPeriodic=0
    g199: BSplineCurve PolesCount=4 KnotsCount=2 Degree=3 IsPeriodic=0
    g200: BSplineCurve PolesCount=4 KnotsCount=2 Degree=3 IsPeriodic=0
    g201: BSplineCurve PolesCount=4 KnotsCount=2 Degree=3 IsPeriodic=0
    g202: BSplineCurve PolesCount=4 KnotsCount=2 Degree=3 IsPeriodic=0
    g203: BSplineCurve PolesCount=4 KnotsCount=2 Degree=3 IsPeriodic=0
    g204: BSplineCurve PolesCount=4 KnotsCount=2 Degree=3 IsPeriodic=0
    g205: BSplineCurve PolesCount=4 KnotsCount=2 Degree=3 IsPeriodic=0
    g206: BSplineCurve PolesCount=4 KnotsCount=2 Degree=3 IsPeriodic=0
    g207: BSplineCurve PolesCount=4 KnotsCount=2 Degree=3 IsPeriodic=0
    g208: BSplineCurve PolesCount=2 KnotsCount=2 Degree=1 IsPeriodic=0
    g209: BSplineCurve PolesCount=2 KnotsCount=2 Degree=1 IsPeriodic=0
    g210: BSplineCurve PolesCount=2 KnotsCount=2 Degree=1 IsPeriodic=0
    g211: BSplineCurve PolesCount=2 KnotsCount=2 Degree=1 IsPeriodic=0
    g212: BSplineCurve PolesCount=4 KnotsCount=2 Degree=3 IsPeriodic=0
    g213: BSplineCurve PolesCount=4 KnotsCount=2 Degree=3 IsPeriodic=0
    g214: BSplineCurve PolesCount=4 KnotsCount=2 Degree=3 IsPeriodic=0
    g215: BSplineCurve PolesCount=2 KnotsCount=2 Degree=1 IsPeriodic=0
    g216: BSplineCurve PolesCount=2 KnotsCount=2 Degree=1 IsPeriodic=0
    g217: BSplineCurve PolesCount=4 KnotsCount=2 Degree=3 IsPeriodic=0
    g218: BSplineCurve PolesCount=4 KnotsCount=2 Degree=3 IsPeriodic=0
    g219: BSplineCurve PolesCount=4 KnotsCount=2 Degree=3 IsPeriodic=0
    g220: BSplineCurve PolesCount=4 KnotsCount=2 Degree=3 IsPeriodic=0
    g221: BSplineCurve PolesCount=4 KnotsCount=2 Degree=3 IsPeriodic=0
    g222: BSplineCurve PolesCount=4 KnotsCount=2 Degree=3 IsPeriodic=0
    g223: BSplineCurve PolesCount=2 KnotsCount=2 Degree=1 IsPeriodic=0
    g224: BSplineCurve PolesCount=2 KnotsCount=2 Degree=1 IsPeriodic=0
    g225: BSplineCurve PolesCount=4 KnotsCount=2 Degree=3 IsPeriodic=0
    g226: BSplineCurve PolesCount=2 KnotsCount=2 Degree=1 IsPeriodic=0
    g227: BSplineCurve PolesCount=2 KnotsCount=2 Degree=1 IsPeriodic=0
    g228: BSplineCurve PolesCount=4 KnotsCount=2 Degree=3 IsPeriodic=0
    g229: BSplineCurve PolesCount=4 KnotsCount=2 Degree=3 IsPeriodic=0
    g230: BSplineCurve PolesCount=4 KnotsCount=2 Degree=3 IsPeriodic=0
    g231: BSplineCurve PolesCount=4 KnotsCount=2 Degree=3 IsPeriodic=0
    g232: BSplineCurve PolesCount=4 KnotsCount=2 Degree=3 IsPeriodic=0
    g233: BSplineCurve PolesCount=4 KnotsCount=2 Degree=3 IsPeriodic=0
    g234: BSplineCurve PolesCount=4 KnotsCount=2 Degree=3 IsPeriodic=0
    g235: BSplineCurve PolesCount=4 KnotsCount=2 Degree=3 IsPeriodic=0
    g236: BSplineCurve PolesCount=4 KnotsCount=2 Degree=3 IsPeriodic=0
    g237: BSplineCurve PolesCount=4 KnotsCount=2 Degree=3 IsPeriodic=0
    g238: BSplineCurve PolesCount=4 KnotsCount=2 Degree=3 IsPeriodic=0
    g239: BSplineCurve PolesCount=4 KnotsCount=2 Degree=3 IsPeriodic=0
    g240: BSplineCurve PolesCount=4 KnotsCount=2 Degree=3 IsPeriodic=0
    g241: BSplineCurve PolesCount=4 KnotsCount=2 Degree=3 IsPeriodic=0
    g242: BSplineCurve PolesCount=4 KnotsCount=2 Degree=3 IsPeriodic=0
    g243: BSplineCurve PolesCount=4 KnotsCount=2 Degree=3 IsPeriodic=0
    g244: BSplineCurve PolesCount=4 KnotsCount=2 Degree=3 IsPeriodic=0
    g245: BSplineCurve PolesCount=4 KnotsCount=2 Degree=3 IsPeriodic=0
    g246: BSplineCurve PolesCount=4 KnotsCount=2 Degree=3 IsPeriodic=0
    g247: BSplineCurve PolesCount=4 KnotsCount=2 Degree=3 IsPeriodic=0
    g248: BSplineCurve PolesCount=4 KnotsCount=2 Degree=3 IsPeriodic=0
    g249: BSplineCurve PolesCount=4 KnotsCount=2 Degree=3 IsPeriodic=0
    g250: BSplineCurve PolesCount=4 KnotsCount=2 Degree=3 IsPeriodic=0
    g251: BSplineCurve PolesCount=4 KnotsCount=2 Degree=3 IsPeriodic=0
    g252: BSplineCurve PolesCount=4 KnotsCount=2 Degree=3 IsPeriodic=0
    g253: BSplineCurve PolesCount=4 KnotsCount=2 Degree=3 IsPeriodic=0
    g254: BSplineCurve PolesCount=4 KnotsCount=2 Degree=3 IsPeriodic=0
    g255: BSplineCurve PolesCount=4 KnotsCount=2 Degree=3 IsPeriodic=0
    g256: BSplineCurve PolesCount=4 KnotsCount=2 Degree=3 IsPeriodic=0
    g257: BSplineCurve PolesCount=4 KnotsCount=2 Degree=3 IsPeriodic=0
    g258: BSplineCurve PolesCount=4 KnotsCount=2 Degree=3 IsPeriodic=0
    g259: BSplineCurve PolesCount=4 KnotsCount=2 Degree=3 IsPeriodic=0
    g260: BSplineCurve PolesCount=4 KnotsCount=2 Degree=3 IsPeriodic=0
    g261: BSplineCurve PolesCount=4 KnotsCount=2 Degree=3 IsPeriodic=0
    g262: BSplineCurve PolesCount=4 KnotsCount=2 Degree=3 IsPeriodic=0
    g263: BSplineCurve PolesCount=4 KnotsCount=2 Degree=3 IsPeriodic=0
    g264: BSplineCurve PolesCount=4 KnotsCount=2 Degree=3 IsPeriodic=0
    g265: BSplineCurve PolesCount=4 KnotsCount=2 Degree=3 IsPeriodic=0
    g266: BSplineCurve PolesCount=2 KnotsCount=2 Degree=1 IsPeriodic=0
    g267: BSplineCurve PolesCount=2 KnotsCount=2 Degree=1 IsPeriodic=0
    g268: BSplineCurve PolesCount=4 KnotsCount=2 Degree=3 IsPeriodic=0
    g269: BSplineCurve PolesCount=4 KnotsCount=2 Degree=3 IsPeriodic=0
    g270: BSplineCurve PolesCount=4 KnotsCount=2 Degree=3 IsPeriodic=0
    g271: BSplineCurve PolesCount=4 KnotsCount=2 Degree=3 IsPeriodic=0
    g272: BSplineCurve PolesCount=4 KnotsCount=2 Degree=3 IsPeriodic=0
    g273: BSplineCurve PolesCount=4 KnotsCount=2 Degree=3 IsPeriodic=0
    g274: BSplineCurve PolesCount=4 KnotsCount=2 Degree=3 IsPeriodic=0
    g275: BSplineCurve PolesCount=4 KnotsCount=2 Degree=3 IsPeriodic=0
    g276: BSplineCurve PolesCount=4 KnotsCount=2 Degree=3 IsPeriodic=0
    g277: BSplineCurve PolesCount=2 KnotsCount=2 Degree=1 IsPeriodic=0
    g278: BSplineCurve PolesCount=2 KnotsCount=2 Degree=1 IsPeriodic=0
    g279: BSplineCurve PolesCount=4 KnotsCount=2 Degree=3 IsPeriodic=0
    g280: BSplineCurve PolesCount=4 KnotsCount=2 Degree=3 IsPeriodic=0
    g281: BSplineCurve PolesCount=2 KnotsCount=2 Degree=1 IsPeriodic=0
    g282: BSplineCurve PolesCount=2 KnotsCount=2 Degree=1 IsPeriodic=0
    g283: BSplineCurve PolesCount=4 KnotsCount=2 Degree=3 IsPeriodic=0
    g284: BSplineCurve PolesCount=4 KnotsCount=2 Degree=3 IsPeriodic=0
    g285: BSplineCurve PolesCount=4 KnotsCount=2 Degree=3 IsPeriodic=0
    g286: BSplineCurve PolesCount=2 KnotsCount=2 Degree=1 IsPeriodic=0
    g287: BSplineCurve PolesCount=2 KnotsCount=2 Degree=1 IsPeriodic=0
    g288: BSplineCurve PolesCount=4 KnotsCount=2 Degree=3 IsPeriodic=0
    g289: BSplineCurve PolesCount=4 KnotsCount=2 Degree=3 IsPeriodic=0
    g290: BSplineCurve PolesCount=4 KnotsCount=2 Degree=3 IsPeriodic=0
    g291: BSplineCurve PolesCount=4 KnotsCount=2 Degree=3 IsPeriodic=0
    g292: BSplineCurve PolesCount=4 KnotsCount=2 Degree=3 IsPeriodic=0
    g293: BSplineCurve PolesCount=4 KnotsCount=2 Degree=3 IsPeriodic=0
    g294: BSplineCurve PolesCount=4 KnotsCount=2 Degree=3 IsPeriodic=0
    g295: BSplineCurve PolesCount=2 KnotsCount=2 Degree=1 IsPeriodic=0
    g296: BSplineCurve PolesCount=2 KnotsCount=2 Degree=1 IsPeriodic=0
    g297: BSplineCurve PolesCount=4 KnotsCount=2 Degree=3 IsPeriodic=0
    g298: BSplineCurve PolesCount=4 KnotsCount=2 Degree=3 IsPeriodic=0
    g299: BSplineCurve PolesCount=4 KnotsCount=2 Degree=3 IsPeriodic=0
    g300: BSplineCurve PolesCount=4 KnotsCount=2 Degree=3 IsPeriodic=0
    g301: BSplineCurve PolesCount=4 KnotsCount=2 Degree=3 IsPeriodic=0
    g302: BSplineCurve PolesCount=5 KnotsCount=2 Degree=4 IsPeriodic=0
    g303: BSplineCurve PolesCount=4 KnotsCount=2 Degree=3 IsPeriodic=0
    g304: BSplineCurve PolesCount=4 KnotsCount=2 Degree=3 IsPeriodic=0
    g305: BSplineCurve PolesCount=4 KnotsCount=2 Degree=3 IsPeriodic=0
    g306: BSplineCurve PolesCount=4 KnotsCount=2 Degree=3 IsPeriodic=0
    g307: BSplineCurve PolesCount=4 KnotsCount=2 Degree=3 IsPeriodic=0
    g308: BSplineCurve PolesCount=4 KnotsCount=2 Degree=3 IsPeriodic=0
    g309: BSplineCurve PolesCount=4 KnotsCount=2 Degree=3 IsPeriodic=0
    g310: BSplineCurve PolesCount=4 KnotsCount=2 Degree=3 IsPeriodic=0
    g311: BSplineCurve PolesCount=4 KnotsCount=2 Degree=3 IsPeriodic=0
    g312: BSplineCurve PolesCount=4 KnotsCount=2 Degree=3 IsPeriodic=0
    g313: BSplineCurve PolesCount=4 KnotsCount=2 Degree=3 IsPeriodic=0
    g314: BSplineCurve PolesCount=8 KnotsCount=2 Degree=7 IsPeriodic=0
    g315: BSplineCurve PolesCount=4 KnotsCount=2 Degree=3 IsPeriodic=0
    g316: BSplineCurve PolesCount=4 KnotsCount=2 Degree=3 IsPeriodic=0
    g317: BSplineCurve PolesCount=4 KnotsCount=2 Degree=3 IsPeriodic=0
    g318: BSplineCurve PolesCount=4 KnotsCount=2 Degree=3 IsPeriodic=0
    g319: BSplineCurve PolesCount=4 KnotsCount=2 Degree=3 IsPeriodic=0
    g320: BSplineCurve PolesCount=4 KnotsCount=2 Degree=3 IsPeriodic=0
    g321: BSplineCurve PolesCount=4 KnotsCount=2 Degree=3 IsPeriodic=0
    g322: BSplineCurve PolesCount=4 KnotsCount=2 Degree=3 IsPeriodic=0
    g323: BSplineCurve PolesCount=4 KnotsCount=2 Degree=3 IsPeriodic=0
    g324: BSplineCurve PolesCount=4 KnotsCount=2 Degree=3 IsPeriodic=0
    g325: BSplineCurve PolesCount=2 KnotsCount=2 Degree=1 IsPeriodic=0
    g326: BSplineCurve PolesCount=2 KnotsCount=2 Degree=1 IsPeriodic=0
    g327: BSplineCurve PolesCount=4 KnotsCount=2 Degree=3 IsPeriodic=0
    g328: BSplineCurve PolesCount=4 KnotsCount=2 Degree=3 IsPeriodic=0
    g329: BSplineCurve PolesCount=4 KnotsCount=2 Degree=3 IsPeriodic=0
    g330: BSplineCurve PolesCount=4 KnotsCount=2 Degree=3 IsPeriodic=0
    g331: BSplineCurve PolesCount=4 KnotsCount=2 Degree=3 IsPeriodic=0
    g332: BSplineCurve PolesCount=4 KnotsCount=2 Degree=3 IsPeriodic=0
    g333: BSplineCurve PolesCount=4 KnotsCount=2 Degree=3 IsPeriodic=0
    g334: BSplineCurve PolesCount=4 KnotsCount=2 Degree=3 IsPeriodic=0
    g335: BSplineCurve PolesCount=2 KnotsCount=2 Degree=1 IsPeriodic=0
    g336: BSplineCurve PolesCount=2 KnotsCount=2 Degree=1 IsPeriodic=0
    g337: BSplineCurve PolesCount=2 KnotsCount=2 Degree=1 IsPeriodic=0
    g338: BSplineCurve PolesCount=2 KnotsCount=2 Degree=1 IsPeriodic=0
    g339: BSplineCurve PolesCount=4 KnotsCount=2 Degree=3 IsPeriodic=0
    g340: BSplineCurve PolesCount=4 KnotsCount=2 Degree=3 IsPeriodic=0
    g341: BSplineCurve PolesCount=4 KnotsCount=2 Degree=3 IsPeriodic=0
    g342: BSplineCurve PolesCount=2 KnotsCount=2 Degree=1 IsPeriodic=0
    g343: BSplineCurve PolesCount=2 KnotsCount=2 Degree=1 IsPeriodic=0
    g344: BSplineCurve PolesCount=4 KnotsCount=2 Degree=3 IsPeriodic=0
    g345: BSplineCurve PolesCount=4 KnotsCount=2 Degree=3 IsPeriodic=0
    g346: BSplineCurve PolesCount=2 KnotsCount=2 Degree=1 IsPeriodic=0
    g347: BSplineCurve PolesCount=2 KnotsCount=2 Degree=1 IsPeriodic=0
    g348: BSplineCurve PolesCount=4 KnotsCount=2 Degree=3 IsPeriodic=0
    g349: BSplineCurve PolesCount=4 KnotsCount=2 Degree=3 IsPeriodic=0
    g350: BSplineCurve PolesCount=4 KnotsCount=2 Degree=3 IsPeriodic=0
    g351: BSplineCurve PolesCount=4 KnotsCount=2 Degree=3 IsPeriodic=0
    g352: BSplineCurve PolesCount=4 KnotsCount=2 Degree=3 IsPeriodic=0
    g353: BSplineCurve PolesCount=4 KnotsCount=2 Degree=3 IsPeriodic=0
    g354: BSplineCurve PolesCount=4 KnotsCount=2 Degree=3 IsPeriodic=0
    g355: BSplineCurve PolesCount=4 KnotsCount=2 Degree=3 IsPeriodic=0
    g356: BSplineCurve PolesCount=2 KnotsCount=2 Degree=1 IsPeriodic=0
    g357: BSplineCurve PolesCount=4 KnotsCount=2 Degree=3 IsPeriodic=0
    g358: BSplineCurve PolesCount=4 KnotsCount=2 Degree=3 IsPeriodic=0
    g359: BSplineCurve PolesCount=2 KnotsCount=2 Degree=1 IsPeriodic=0
    g360: BSplineCurve PolesCount=2 KnotsCount=2 Degree=1 IsPeriodic=0
    g361: BSplineCurve PolesCount=4 KnotsCount=2 Degree=3 IsPeriodic=0
    g362: BSplineCurve PolesCount=2 KnotsCount=2 Degree=1 IsPeriodic=0
    g363: BSplineCurve PolesCount=4 KnotsCount=2 Degree=3 IsPeriodic=0
    g364: BSplineCurve PolesCount=4 KnotsCount=2 Degree=3 IsPeriodic=0
    g365: BSplineCurve PolesCount=4 KnotsCount=2 Degree=3 IsPeriodic=0
    g366: BSplineCurve PolesCount=2 KnotsCount=2 Degree=1 IsPeriodic=0
    g367: BSplineCurve PolesCount=4 KnotsCount=2 Degree=3 IsPeriodic=0
    g368: BSplineCurve PolesCount=4 KnotsCount=2 Degree=3 IsPeriodic=0
    g369: BSplineCurve PolesCount=2 KnotsCount=2 Degree=1 IsPeriodic=0
    g370-g374: Circle [constr] x5 (B-spline internal-alignment scaffolding for g0; pole/knot coordinates omitted)
    g375: GeomPoint [constr] X=12.7866 Y=-28.842 Z=0
    g376: GeomPoint [constr] X=4.47682 Y=-3.93922 Z=0
    g377: Circle [constr] CenterX=1.75872 CenterY=-22.7039 CenterZ=0 NormalX=0 NormalY=0 NormalZ=1 AngleXU=0 Radius=1
    g378: Circle [constr] CenterX=0.563965 CenterY=-20.4689 CenterZ=0 NormalX=0 NormalY=0 NormalZ=1 AngleXU=0 Radius=1
    g379-g383: Circle [constr] x5 (B-spline internal-alignment scaffolding for g314; pole/knot coordinates omitted)
    g384: GeomPoint [constr] X=17.8292 Y=-0.834625 Z=0
    g385: GeomPoint [constr] X=0.865099 Y=-18.3774 Z=0
    g386: Circle [constr] CenterX=0.211449 CenterY=-9.27892 CenterZ=0 NormalX=0 NormalY=0 NormalZ=1 AngleXU=0 Radius=1
    g387-g391: Circle [constr] x5 (B-spline internal-alignment scaffolding for g302; pole/knot coordinates omitted)
    g392: GeomPoint [constr] X=1.06326 Y=-18.7886 Z=0
    g393: GeomPoint [constr] X=3.80839 Y=-6.1158 Z=0
    g394: Circle [constr] CenterX=-0.239203 CenterY=-18.062 CenterZ=0 NormalX=0 NormalY=0 NormalZ=1 AngleXU=0 Radius=1
    g395-g399: Circle [constr] x5 (B-spline internal-alignment scaffolding for g1; pole/knot coordinates omitted)
    g400: GeomPoint [constr] X=4.47682 Y=-3.93922 Z=0
    g401: GeomPoint [constr] X=28.2557 Y=-17.0837 Z=0
    g402: Circle [constr] CenterX=17.5128 CenterY=0.39076 CenterZ=0 NormalX=0 NormalY=0 NormalZ=1 AngleXU=0 Radius=1
    g403: Circle [constr] CenterX=20.1617 CenterY=-0.496689 CenterZ=0 NormalX=0 NormalY=0 NormalZ=1 AngleXU=0 Radius=1
    g404: Circle [constr] CenterX=-0.341149 CenterY=-13.7601 CenterZ=0 NormalX=0 NormalY=0 NormalZ=1 AngleXU=0 Radius=1
    g405-g408: Circle [constr] x4 (B-spline internal-alignment scaffolding for g1; pole/knot coordinates omitted)
    g409: Circle [constr] CenterX=-0.62736 CenterY=-15.5532 CenterZ=0 NormalX=0 NormalY=0 NormalZ=1 AngleXU=0 Radius=1
    g410: Circle [constr] CenterX=-0.577081 CenterY=-13.0129 CenterZ=0 NormalX=0 NormalY=0 NormalZ=1 AngleXU=0 Radius=1
    g411: Circle [constr] CenterX=0.865099 CenterY=-18.3774 CenterZ=0 NormalX=0 NormalY=0 NormalZ=1 AngleXU=0 Radius=1
    g412: Circle [constr] CenterX=-0.0649469 CenterY=-10.5111 CenterZ=0 NormalX=0 NormalY=0 NormalZ=1 AngleXU=0 Radius=1
    g413: Circle [constr] CenterX=28.7021 CenterY=-10.9856 CenterZ=0 NormalX=0 NormalY=0 NormalZ=1 AngleXU=0 Radius=1
    g414: Circle [constr] CenterX=28.8441 CenterY=-13.9481 CenterZ=0 NormalX=0 NormalY=0 NormalZ=1 AngleXU=0 Radius=1
    g415: Circle [constr] CenterX=28.2557 CenterY=-17.0837 CenterZ=0 NormalX=0 NormalY=0 NormalZ=1 AngleXU=0 Radius=1
    g416: Circle [constr] CenterX=0.932467 CenterY=-8.11812 CenterZ=0 NormalX=0 NormalY=0 NormalZ=1 AngleXU=0 Radius=1
    g417: Circle [constr] CenterX=2.43858 CenterY=-5.90409 CenterZ=0 NormalX=0 NormalY=0 NormalZ=1 AngleXU=0 Radius=1
    g418: Circle [constr] CenterX=4.47682 CenterY=-3.93922 CenterZ=0 NormalX=0 NormalY=0 NormalZ=1 AngleXU=0 Radius=1
  constraints (460):
    c: Coincident(g0,g1)
    c: Coincident(g1,g2)
    c: Coincident(g2,g3)
    c: Coincident(g3,g4)
    c: Coincident(g4,g0)
    c: Coincident(g5,g6)
    c: Coincident(g6,g7)
    c: Coincident(g7,g8)
    c: Coincident(g8,g9)
    c: Coincident(g9,g10)
    c: Coincident(g10,g11)
    c: Coincident(g11,g12)
    c: Coincident(g12,g13)
    c: Coincident(g13,g14)
    c: Coincident(g14,g15)
    c: Coincident(g15,g16)
    c: Coincident(g16,g17)
    c: Coincident(g17,g18)
    c: Coincident(g18,g19)
    c: Coincident(g19,g20)
    c: Coincident(g20,g5)
    c: Coincident(g21,g22)
    c: Coincident(g22,g23)
    c: Coincident(g23,g24)
    c: Coincident(g24,g25)
    c: Coincident(g25,g26)
    c: Coincident(g26,g27)
    c: Coincident(g27,g28)
    c: Coincident(g28,g29)
    c: Coincident(g29,g30)
    c: Coincident(g30,g31)
    c: Coincident(g32,g33)
    c: Coincident(g33,g34)
    c: Coincident(g34,g35)
    c: Coincident(g35,g36)
    c: Coincident(g36,g37)
    c: Coincident(g37,g38)
    c: Coincident(g38,g39)
    c: Coincident(g39,g40)
    c: Coincident(g40,g41)
    c: Coincident(g41,g42)
    c: Coincident(g42,g43)
    c: Coincident(g43,g44)
    c: Coincident(g44,g45)
    c: Coincident(g45,g46)
    c: Coincident(g46,g47)
    c: Coincident(g47,g48)
    c: Coincident(g48,g49)
    c: Coincident(g49,g50)
    c: Coincident(g50,g51)
    c: Coincident(g51,g52)
    c: Coincident(g52,g53)
    c: Coincident(g53,g54)
    c: Coincident(g54,g55)
    c: Coincident(g55,g56)
    c: Coincident(g56,g57)
    c: Coincident(g57,g58)
    c: Coincident(g58,g59)
    c: Coincident(g59,g60)
    c: Coincident(g60,g61)
    c: Coincident(g61,g62)
    c: Coincident(g62,g63)
    c: Coincident(g63,g64)
    c: Coincident(g64,g65)
    c: Coincident(g65,g66)
    c: Coincident(g66,g67)
    c: Coincident(g67,g68)
    c: Coincident(g68,g69)
    c: Coincident(g69,g70)
    c: Coincident(g70,g71)
    c: Coincident(g71,g72)
    c: Coincident(g72,g73)
    c: Coincident(g73,g74)
    c: Coincident(g74,g75)
    c: Coincident(g75,g76)
    c: Coincident(g76,g77)
    c: Coincident(g77,g78)
    c: Coincident(g78,g79)
    c: Coincident(g79,g80)
    c: Coincident(g80,g81)
    c: Coincident(g81,g82)
    c: Coincident(g82,g83)
    c: Coincident(g83,g84)
    c: Coincident(g84,g85)
    c: Coincident(g85,g86)
    c: Coincident(g86,g87)
    c: Coincident(g87,g88)
    c: Coincident(g88,g89)
    c: Coincident(g89,g90)
    c: Coincident(g90,g91)
    c: Coincident(g91,g92)
    c: Coincident(g92,g93)
    c: Coincident(g93,g94)
    c: Coincident(g94,g95)
    c: Coincident(g95,g96)
    c: Coincident(g96,g97)
    c: Coincident(g97,g98)
    c: Coincident(g98,g99)
    c: Coincident(g99,g100)
    c: Coincident(g100,g101)
    c: Coincident(g101,g102)
    c: Coincident(g102,g103)
    c: Coincident(g103,g104)
    c: Coincident(g104,g105)
    c: Coincident(g105,g106)
    c: Coincident(g106,g107)
    c: Coincident(g107,g108)
    c: Coincident(g108,g109)
    c: Coincident(g109,g110)
    c: Coincident(g110,g111)
    c: Coincident(g111,g112)
    c: Coincident(g112,g113)
    c: Coincident(g113,g114)
    c: Coincident(g114,g115)
    c: Coincident(g115,g116)
    c: Coincident(g116,g117)
    c: Coincident(g117,g118)
    c: Coincident(g118,g119)
    c: Coincident(g119,g120)
    c: Coincident(g120,g121)
    c: Coincident(g121,g122)
    c: Coincident(g122,g123)
    c: Coincident(g123,g124)
    c: Coincident(g124,g125)
    c: Coincident(g125,g126)
    c: Coincident(g126,g127)
    c: Coincident(g127,g128)
    c: Coincident(g128,g129)
    c: Coincident(g129,g130)
    c: Coincident(g130,g131)
    c: Coincident(g131,g132)
    c: Coincident(g132,g133)
    c: Coincident(g133,g134)
    c: Coincident(g134,g135)
    c: Coincident(g135,g136)
    c: Coincident(g136,g137)
    c: Coincident(g137,g138)
    c: Coincident(g138,g139)
    c: Coincident(g139,g140)
    c: Coincident(g141,g142)
    c: Coincident(g142,g143)
    c: Coincident(g143,g144)
    c: Coincident(g144,g145)
    c: Coincident(g145,g146)
    c: Coincident(g146,g147)
    c: Coincident(g147,g148)
    c: Coincident(g148,g149)
    c: Coincident(g149,g150)
    c: Coincident(g150,g151)
    c: Coincident(g151,g152)
    c: Coincident(g152,g153)
    c: Coincident(g153,g154)
    c: Coincident(g154,g155)
    c: Coincident(g155,g156)
    c: Coincident(g156,g157)
    c: Coincident(g157,g158)
    c: Coincident(g158,g159)
    c: Coincident(g159,g160)
    c: Coincident(g160,g161)
    c: Coincident(g161,g162)
    c: Coincident(g163,g164)
    c: Coincident(g164,g165)
    c: Coincident(g165,g166)
    c: Coincident(g166,g167)
    c: Coincident(g167,g168)
    c: Coincident(g168,g169)
    c: Coincident(g169,g170)
    c: Coincident(g170,g171)
    c: Coincident(g171,g172)
    c: Coincident(g172,g163)
    c: Coincident(g173,g174)
    c: Coincident(g174,g175)
    c: Coincident(g175,g176)
    c: Coincident(g176,g177)
    c: Coincident(g177,g173)
    c: Coincident(g178,g179)
    c: Coincident(g179,g180)
    c: Coincident(g180,g181)
    c: Coincident(g181,g178)
    c: Coincident(g182,g183)
    c: Coincident(g183,g184)
    c: Coincident(g184,g185)
    c: Coincident(g185,g182)
    c: Coincident(g186,g187)
    c: Coincident(g187,g188)
    c: Coincident(g188,g189)
    c: Coincident(g189,g190)
    c: Coincident(g190,g191)
    c: Coincident(g191,g192)
    c: Coincident(g192,g193)
    c: Coincident(g193,g186)
    c: Coincident(g194,g195)
    c: Coincident(g195,g196)
    c: Coincident(g196,g197)
    c: Coincident(g197,g198)
    c: Coincident(g198,g199)
    c: Coincident(g199,g200)
    c: Coincident(g200,g201)
    c: Coincident(g201,g194)
    c: Coincident(g202,g203)
    c: Coincident(g203,g204)
    c: Coincident(g204,g205)
    c: Coincident(g205,g206)
    c: Coincident(g206,g207)
    c: Coincident(g207,g208)
    c: Coincident(g208,g209)
    c: Coincident(g209,g210)
    c: Coincident(g210,g211)
    c: Coincident(g211,g212)
    c: Coincident(g212,g213)
    c: Coincident(g213,g214)
    c: Coincident(g214,g215)
    c: Coincident(g215,g216)
    c: Coincident(g216,g217)
    c: Coincident(g217,g218)
    c: Coincident(g218,g219)
    c: Coincident(g219,g220)
    c: Coincident(g220,g221)
    c: Coincident(g221,g222)
    c: Coincident(g222,g223)
    c: Coincident(g223,g224)
    c: Coincident(g224,g225)
    c: Coincident(g225,g226)
    c: Coincident(g226,g227)
    c: Coincident(g227,g228)
    c: Coincident(g228,g229)
    c: Coincident(g229,g230)
    c: Coincident(g230,g231)
    c: Coincident(g231,g232)
    c: Coincident(g232,g233)
    c: Coincident(g233,g234)
    c: Coincident(g234,g235)
    c: Coincident(g235,g236)
    c: Coincident(g236,g237)
    c: Coincident(g237,g238)
    c: Coincident(g238,g239)
    c: Coincident(g239,g240)
    c: Coincident(g240,g241)
    c: Coincident(g241,g242)
    c: Coincident(g242,g243)
    c: Coincident(g243,g244)
    c: Coincident(g244,g245)
    c: Coincident(g245,g246)
    c: Coincident(g246,g247)
    c: Coincident(g247,g248)
    c: Coincident(g248,g249)
    c: Coincident(g249,g250)
    c: Coincident(g250,g251)
    c: Coincident(g251,g252)
    c: Coincident(g252,g253)
    c: Coincident(g253,g254)
    c: Coincident(g254,g255)
    c: Coincident(g255,g256)
    c: Coincident(g256,g257)
    c: Coincident(g257,g258)
    c: Coincident(g258,g259)
    c: Coincident(g259,g260)
    c: Coincident(g260,g261)
    c: Coincident(g261,g262)
    c: Coincident(g263,g264)
    c: Coincident(g264,g265)
    c: Coincident(g265,g266)
    c: Coincident(g266,g267)
    c: Coincident(g267,g268)
    c: Coincident(g268,g269)
    c: Coincident(g269,g270)
    c: Coincident(g270,g271)
    c: Coincident(g271,g272)
    c: Coincident(g272,g273)
    c: Coincident(g273,g263)
    c: Coincident(g274,g275)
    c: Coincident(g275,g276)
    c: Coincident(g276,g277)
    c: Coincident(g277,g278)
    c: Coincident(g278,g279)
    c: Coincident(g279,g280)
    c: Coincident(g280,g281)
    c: Coincident(g281,g282)
    c: Coincident(g282,g274)
    c: Coincident(g283,g284)
    c: Coincident(g284,g285)
    c: Coincident(g285,g286)
    c: Coincident(g286,g287)
    c: Coincident(g287,g288)
    c: Coincident(g288,g289)
    c: Coincident(g290,g291)
    c: Coincident(g291,g292)
    c: Coincident(g292,g290)
    c: Coincident(g293,g294)
    c: Coincident(g294,g295)
    c: Coincident(g295,g296)
    c: Coincident(g296,g297)
    c: Coincident(g297,g298)
    c: Coincident(g298,g299)
    c: Coincident(g299,g300)
    c: Coincident(g301,g302)
    c: Coincident(g302,g303)
    c: Coincident(g303,g304)
    c: Coincident(g304,g305)
    c: Coincident(g305,g306)
    c: Coincident(g306,g307)
    c: Coincident(g307,g308)
    c: Coincident(g308,g309)
    c: Coincident(g309,g310)
    c: Coincident(g310,g311)
    c: Coincident(g311,g312)
    c: Coincident(g312,g313)
    c: Coincident(g313,g314)
    c: Coincident(g314,g315)
    c: Coincident(g315,g301)
    c: Coincident(g316,g317)
    c: Coincident(g317,g318)
    c: Coincident(g318,g319)
    c: Coincident(g319,g320)
    c: Coincident(g320,g321)
    c: Coincident(g321,g322)
    c: Coincident(g322,g316)
    c: Coincident(g323,g324)
    c: Coincident(g324,g325)
    c: Coincident(g325,g326)
    c: Coincident(g326,g327)
    c: Coincident(g327,g328)
    c: Coincident(g329,g330)
    c: Coincident(g330,g331)
    c: Coincident(g331,g329)
    c: Coincident(g332,g333)
    c: Coincident(g333,g334)
    c: Coincident(g334,g335)
    c: Coincident(g335,g336)
    c: Coincident(g336,g337)
    c: Coincident(g337,g338)
    c: Coincident(g338,g332)
    c: Coincident(g339,g340)
    c: Coincident(g340,g341)
    c: Coincident(g341,g339)
    c: Coincident(g342,g343)
    c: Coincident(g343,g344)
    c: Coincident(g344,g345)
    c: Coincident(g345,g346)
    c: Coincident(g346,g347)
    c: Coincident(g347,g348)
    c: Coincident(g348,g342)
    c: Coincident(g349,g350)
    c: Coincident(g350,g351)
    c: Coincident(g351,g352)
    c: Coincident(g352,g349)
    c: Coincident(g353,g354)
    c: Coincident(g354,g355)
    c: Coincident(g355,g353)
    c: Coincident(g356,g357)
    c: Coincident(g357,g358)
    c: Coincident(g358,g359)
    c: Coincident(g359,g360)
    c: Coincident(g360,g361)
    c: Coincident(g361,g362)
    c: Coincident(g362,g356)
    c: Coincident(g363,g364)
    c: Coincident(g364,g365)
    c: Coincident(g365,g363)
    c: Coincident(g366,g367)
    c: Coincident(g367,g368)
    c: Coincident(g368,g369)
    c: Coincident(g369,g366)
    c: Coincident(g323,g328)
    c: Coincident(g283,g289)
    c: Coincident(g293,g300)
    c: Coincident(g141,g162)
    c: Coincident(g32,g140)
    c: Coincident(g202,g262)
    c: Coincident(g21,g31)
    c: InternalAlignment(g370,g0)
    c: Weight(g370) = 1
    c: InternalAlignment(g371,g0)
    c: Equal(g371,g370)
    c: InternalAlignment(g372,g0)
    c: Equal(g372,g370)
    c: InternalAlignment(g373,g0)
    c: Equal(g373,g370)
    c: InternalAlignment(g374,g0)
    c: Equal(g374,g370)
    c: InternalAlignment(g375,g0)
    c: InternalAlignment(g376,g0)
    c: InternalAlignment(g377,g0)
    c: Equal(g377,g370)
    c: InternalAlignment(g378,g0)
    c: Equal(g378,g370)
    c: InternalAlignment(g379,g314)
    c: Weight(g379) = 1
    c: InternalAlignment(g380,g314)
    c: Equal(g380,g379)
    c: InternalAlignment(g381,g314)
    c: Equal(g381,g379)
    c: InternalAlignment(g382,g314)
    c: Equal(g382,g379)
    c: InternalAlignment(g383,g314)
    c: Equal(g383,g379)
    c: InternalAlignment(g384,g314)
    c: InternalAlignment(g385,g314)
    c: InternalAlignment(g386,g314)
    c: Equal(g386,g379)
    c: InternalAlignment(g387,g302)
    c: Weight(g387) = 1
    c: InternalAlignment(g388,g302)
    c: Equal(g388,g387)
    c: InternalAlignment(g389,g302)
    c: Equal(g389,g387)
    c: InternalAlignment(g390,g302)
    c: Equal(g390,g387)
    c: InternalAlignment(g391,g302)
    c: Equal(g391,g387)
    c: InternalAlignment(g392,g302)
    c: InternalAlignment(g393,g302)
    c: InternalAlignment(g394,g0)
    c: Equal(g394,g370)
    c: InternalAlignment(g395,g1)
    c: Weight(g395) = 1
    c: InternalAlignment(g396,g1)
    c: Equal(g396,g395)
    c: InternalAlignment(g397,g1)
    c: Equal(g397,g395)
    c: InternalAlignment(g398,g1)
    c: Equal(g398,g395)
    c: InternalAlignment(g399,g1)
    c: Equal(g399,g395)
    c: InternalAlignment(g400,g1)
    c: InternalAlignment(g401,g1)
    c: InternalAlignment(g402,g1)
    c: Equal(g402,g395)
    c: InternalAlignment(g403,g1)
    c: Equal(g403,g395)
    c: InternalAlignment(g404,g314)
    c: Equal(g404,g379)
    c: InternalAlignment(g405,g1)
    c: Equal(g405,g395)
    c: InternalAlignment(g406,g1)
    c: Equal(g406,g395)
    c: InternalAlignment(g407,g1)
    c: Equal(g407,g395)
    c: InternalAlignment(g408,g1)
    c: Equal(g408,g395)
    c: InternalAlignment(g409,g0)
    c: Equal(g409,g370)
    c: InternalAlignment(g410,g0)
    c: Equal(g410,g370)
    c: InternalAlignment(g411,g314)
    c: Equal(g411,g379)
    c: InternalAlignment(g412,g0)
    c: Equal(g412,g370)
    c: InternalAlignment(g413,g1)
    c: Equal(g413,g395)
    c: InternalAlignment(g414,g1)
    c: Equal(g414,g395)
    c: InternalAlignment(g415,g1)
    c: Equal(g415,g395)
    c: InternalAlignment(g416,g0)
    c: Equal(g416,g370)
    c: InternalAlignment(g417,g0)
    c: Equal(g417,g370)
    c: InternalAlignment(g418,g0)
    c: Equal(g418,g370)
FEATURE [Sketcher::SketchObject] Sketch031  label="Dreamer-Sketch"
  ArcFitTolerance = 1e-06
  FullyConstrained = false
  MakeInternals = false
  Placement = pos=(-15.7692,9.76413,0) rot=(0,0,1;0rad)
  expr: .Placement.Base.x = -(.Shape.BoundBox.XLength / 2)
  expr: .Placement.Base.y = .Shape.BoundBox.YLength / 2
  sketch-geometry (819):
    g0: BSplineCurve PolesCount=4 KnotsCount=2 Degree=3 IsPeriodic=0
    g1: BSplineCurve PolesCount=4 KnotsCount=2 Degree=3 IsPeriodic=0
    g2: BSplineCurve PolesCount=4 KnotsCount=2 Degree=3 IsPeriodic=0
    g3: BSplineCurve PolesCount=4 KnotsCount=2 Degree=3 IsPeriodic=0
    g4: BSplineCurve PolesCount=4 KnotsCount=2 Degree=3 IsPeriodic=0
    g5: BSplineCurve PolesCount=4 KnotsCount=2 Degree=3 IsPeriodic=0
    g6: BSplineCurve PolesCount=4 KnotsCount=2 Degree=3 IsPeriodic=0
    g7: BSplineCurve PolesCount=4 KnotsCount=2 Degree=3 IsPeriodic=0
    g8: BSplineCurve PolesCount=4 KnotsCount=2 Degree=3 IsPeriodic=0
    g9: BSplineCurve PolesCount=4 KnotsCount=2 Degree=3 IsPeriodic=0
    g10: BSplineCurve PolesCount=4 KnotsCount=2 Degree=3 IsPeriodic=0
    g11: BSplineCurve PolesCount=4 KnotsCount=2 Degree=3 IsPeriodic=0
    g12: BSplineCurve PolesCount=4 KnotsCount=2 Degree=3 IsPeriodic=0
    g13: BSplineCurve PolesCount=2 KnotsCount=2 Degree=1 IsPeriodic=0
    g14: BSplineCurve PolesCount=2 KnotsCount=2 Degree=1 IsPeriodic=0
    g15: BSplineCurve PolesCount=4 KnotsCount=2 Degree=3 IsPeriodic=0
    g16: BSplineCurve PolesCount=4 KnotsCount=2 Degree=3 IsPeriodic=0
    g17: BSplineCurve PolesCount=4 KnotsCount=2 Degree=3 IsPeriodic=0
    g18: BSplineCurve PolesCount=4 KnotsCount=2 Degree=3 IsPeriodic=0
    g19: BSplineCurve PolesCount=4 KnotsCount=2 Degree=3 IsPeriodic=0
    g20: BSplineCurve PolesCount=2 KnotsCount=2 Degree=1 IsPeriodic=0
    g21: BSplineCurve PolesCount=2 KnotsCount=2 Degree=1 IsPeriodic=0
    g22: BSplineCurve PolesCount=4 KnotsCount=2 Degree=3 IsPeriodic=0
    g23: BSplineCurve PolesCount=4 KnotsCount=2 Degree=3 IsPeriodic=0
    g24: BSplineCurve PolesCount=4 KnotsCount=2 Degree=3 IsPeriodic=0
    g25: BSplineCurve PolesCount=4 KnotsCount=2 Degree=3 IsPeriodic=0
    g26: BSplineCurve PolesCount=2 KnotsCount=2 Degree=1 IsPeriodic=0
    g27: BSplineCurve PolesCount=2 KnotsCount=2 Degree=1 IsPeriodic=0
    g28: BSplineCurve PolesCount=4 KnotsCount=2 Degree=3 IsPeriodic=0
    g29: BSplineCurve PolesCount=4 KnotsCount=2 Degree=3 IsPeriodic=0
    g30: BSplineCurve PolesCount=4 KnotsCount=2 Degree=3 IsPeriodic=0
    g31: BSplineCurve PolesCount=4 KnotsCount=2 Degree=3 IsPeriodic=0
    g32: BSplineCurve PolesCount=4 KnotsCount=2 Degree=3 IsPeriodic=0
    g33: BSplineCurve PolesCount=4 KnotsCount=2 Degree=3 IsPeriodic=0
    g34: BSplineCurve PolesCount=4 KnotsCount=2 Degree=3 IsPeriodic=0
    g35: BSplineCurve PolesCount=4 KnotsCount=2 Degree=3 IsPeriodic=0
    g36: BSplineCurve PolesCount=4 KnotsCount=2 Degree=3 IsPeriodic=0
    g37: BSplineCurve PolesCount=4 KnotsCount=2 Degree=3 IsPeriodic=0
    g38: BSplineCurve PolesCount=4 KnotsCount=2 Degree=3 IsPeriodic=0
    g39: BSplineCurve PolesCount=4 KnotsCount=2 Degree=3 IsPeriodic=0
    g40: BSplineCurve PolesCount=4 KnotsCount=2 Degree=3 IsPeriodic=0
    g41: BSplineCurve PolesCount=4 KnotsCount=2 Degree=3 IsPeriodic=0
    g42: BSplineCurve PolesCount=4 KnotsCount=2 Degree=3 IsPeriodic=0
    g43: BSplineCurve PolesCount=4 KnotsCount=2 Degree=3 IsPeriodic=0
    g44: BSplineCurve PolesCount=4 KnotsCount=2 Degree=3 IsPeriodic=0
    g45: BSplineCurve PolesCount=4 KnotsCount=2 Degree=3 IsPeriodic=0
    g46: BSplineCurve PolesCount=4 KnotsCount=2 Degree=3 IsPeriodic=0
    g47: BSplineCurve PolesCount=4 KnotsCount=2 Degree=3 IsPeriodic=0
    g48: BSplineCurve PolesCount=4 KnotsCount=2 Degree=3 IsPeriodic=0
    g49: BSplineCurve PolesCount=4 KnotsCount=2 Degree=3 IsPeriodic=0
    g50: BSplineCurve PolesCount=4 KnotsCount=2 Degree=3 IsPeriodic=0
    g51: BSplineCurve PolesCount=4 KnotsCount=2 Degree=3 IsPeriodic=0
    g52: BSplineCurve PolesCount=4 KnotsCount=2 Degree=3 IsPeriodic=0
    g53: BSplineCurve PolesCount=4 KnotsCount=2 Degree=3 IsPeriodic=0
    g54: BSplineCurve PolesCount=4 KnotsCount=2 Degree=3 IsPeriodic=0
    g55: BSplineCurve PolesCount=4 KnotsCount=2 Degree=3 IsPeriodic=0
    g56: BSplineCurve PolesCount=4 KnotsCount=2 Degree=3 IsPeriodic=0
    g57: BSplineCurve PolesCount=4 KnotsCount=2 Degree=3 IsPeriodic=0
    g58: BSplineCurve PolesCount=4 KnotsCount=2 Degree=3 IsPeriodic=0
    g59: BSplineCurve PolesCount=4 KnotsCount=2 Degree=3 IsPeriodic=0
    g60: BSplineCurve PolesCount=4 KnotsCount=2 Degree=3 IsPeriodic=0
    g61: BSplineCurve PolesCount=4 KnotsCount=2 Degree=3 IsPeriodic=0
    g62: BSplineCurve PolesCount=2 KnotsCount=2 Degree=1 IsPeriodic=0
    g63: BSplineCurve PolesCount=2 KnotsCount=2 Degree=1 IsPeriodic=0
    g64: BSplineCurve PolesCount=4 KnotsCount=2 Degree=3 IsPeriodic=0
    g65: BSplineCurve PolesCount=4 KnotsCount=2 Degree=3 IsPeriodic=0
    g66: BSplineCurve PolesCount=4 KnotsCount=2 Degree=3 IsPeriodic=0
    g67: BSplineCurve PolesCount=4 KnotsCount=2 Degree=3 IsPeriodic=0
    g68: BSplineCurve PolesCount=4 KnotsCount=2 Degree=3 IsPeriodic=0
    g69: BSplineCurve PolesCount=4 KnotsCount=2 Degree=3 IsPeriodic=0
    g70: BSplineCurve PolesCount=4 KnotsCount=2 Degree=3 IsPeriodic=0
    g71: BSplineCurve PolesCount=4 KnotsCount=2 Degree=3 IsPeriodic=0
    g72: BSplineCurve PolesCount=4 KnotsCount=2 Degree=3 IsPeriodic=0
    g73: BSplineCurve PolesCount=4 KnotsCount=2 Degree=3 IsPeriodic=0
    g74: BSplineCurve PolesCount=4 KnotsCount=2 Degree=3 IsPeriodic=0
    g75: BSplineCurve PolesCount=4 KnotsCount=2 Degree=3 IsPeriodic=0
    g76: BSplineCurve PolesCount=4 KnotsCount=2 Degree=3 IsPeriodic=0
    g77: BSplineCurve PolesCount=4 KnotsCount=2 Degree=3 IsPeriodic=0
    g78: BSplineCurve PolesCount=4 KnotsCount=2 Degree=3 IsPeriodic=0
    g79: BSplineCurve PolesCount=4 KnotsCount=2 Degree=3 IsPeriodic=0
    g80: BSplineCurve PolesCount=4 KnotsCount=2 Degree=3 IsPeriodic=0
    g81: BSplineCurve PolesCount=4 KnotsCount=2 Degree=3 IsPeriodic=0
    g82: BSplineCurve PolesCount=4 KnotsCount=2 Degree=3 IsPeriodic=0
    g83: BSplineCurve PolesCount=4 KnotsCount=2 Degree=3 IsPeriodic=0
    g84: BSplineCurve PolesCount=4 KnotsCount=2 Degree=3 IsPeriodic=0
    g85: BSplineCurve PolesCount=4 KnotsCount=2 Degree=3 IsPeriodic=0
    g86: BSplineCurve PolesCount=4 KnotsCount=2 Degree=3 IsPeriodic=0
    g87: BSplineCurve PolesCount=2 KnotsCount=2 Degree=1 IsPeriodic=0
    g88: BSplineCurve PolesCount=2 KnotsCount=2 Degree=1 IsPeriodic=0
    g89: BSplineCurve PolesCount=4 KnotsCount=2 Degree=3 IsPeriodic=0
    g90: BSplineCurve PolesCount=4 KnotsCount=2 Degree=3 IsPeriodic=0
    g91: BSplineCurve PolesCount=4 KnotsCount=2 Degree=3 IsPeriodic=0
    g92: BSplineCurve PolesCount=4 KnotsCount=2 Degree=3 IsPeriodic=0
    g93: BSplineCurve PolesCount=4 KnotsCount=2 Degree=3 IsPeriodic=0
    g94: BSplineCurve PolesCount=4 KnotsCount=2 Degree=3 IsPeriodic=0
    g95: BSplineCurve PolesCount=4 KnotsCount=2 Degree=3 IsPeriodic=0
    g96: BSplineCurve PolesCount=4 KnotsCount=2 Degree=3 IsPeriodic=0
    g97: BSplineCurve PolesCount=4 KnotsCount=2 Degree=3 IsPeriodic=0
    g98: BSplineCurve PolesCount=4 KnotsCount=2 Degree=3 IsPeriodic=0
    g99: BSplineCurve PolesCount=4 KnotsCount=2 Degree=3 IsPeriodic=0
    g100: BSplineCurve PolesCount=4 KnotsCount=2 Degree=3 IsPeriodic=0
    g101: BSplineCurve PolesCount=4 KnotsCount=2 Degree=3 IsPeriodic=0
    g102: BSplineCurve PolesCount=2 KnotsCount=2 Degree=1 IsPeriodic=0
    g103: BSplineCurve PolesCount=2 KnotsCount=2 Degree=1 IsPeriodic=0
    g104: BSplineCurve PolesCount=4 KnotsCount=2 Degree=3 IsPeriodic=0
    g105: BSplineCurve PolesCount=4 KnotsCount=2 Degree=3 IsPeriodic=0
    g106: BSplineCurve PolesCount=4 KnotsCount=2 Degree=3 IsPeriodic=0
    g107: BSplineCurve PolesCount=4 KnotsCount=2 Degree=3 IsPeriodic=0
    g108: BSplineCurve PolesCount=4 KnotsCount=2 Degree=3 IsPeriodic=0
    g109: BSplineCurve PolesCount=4 KnotsCount=2 Degree=3 IsPeriodic=0
    g110: BSplineCurve PolesCount=4 KnotsCount=2 Degree=3 IsPeriodic=0
    g111: BSplineCurve PolesCount=4 KnotsCount=2 Degree=3 IsPeriodic=0
    g112: BSplineCurve PolesCount=4 KnotsCount=2 Degree=3 IsPeriodic=0
    g113: BSplineCurve PolesCount=4 KnotsCount=2 Degree=3 IsPeriodic=0
    g114: BSplineCurve PolesCount=4 KnotsCount=2 Degree=3 IsPeriodic=0
    g115: BSplineCurve PolesCount=4 KnotsCount=2 Degree=3 IsPeriodic=0
    g116: BSplineCurve PolesCount=2 KnotsCount=2 Degree=1 IsPeriodic=0
    g117: BSplineCurve PolesCount=2 KnotsCount=2 Degree=1 IsPeriodic=0
    g118: BSplineCurve PolesCount=4 KnotsCount=2 Degree=3 IsPeriodic=0
    g119: BSplineCurve PolesCount=4 KnotsCount=2 Degree=3 IsPeriodic=0
    g120: BSplineCurve PolesCount=4 KnotsCount=2 Degree=3 IsPeriodic=0
    g121: BSplineCurve PolesCount=4 KnotsCount=2 Degree=3 IsPeriodic=0
    g122: BSplineCurve PolesCount=4 KnotsCount=2 Degree=3 IsPeriodic=0
    g123: BSplineCurve PolesCount=4 KnotsCount=2 Degree=3 IsPeriodic=0
    g124: BSplineCurve PolesCount=4 KnotsCount=2 Degree=3 IsPeriodic=0
    g125: BSplineCurve PolesCount=4 KnotsCount=2 Degree=3 IsPeriodic=0
    g126: BSplineCurve PolesCount=4 KnotsCount=2 Degree=3 IsPeriodic=0
    g127: BSplineCurve PolesCount=4 KnotsCount=2 Degree=3 IsPeriodic=0
    g128: BSplineCurve PolesCount=4 KnotsCount=2 Degree=3 IsPeriodic=0
    g129: BSplineCurve PolesCount=4 KnotsCount=2 Degree=3 IsPeriodic=0
    g130: BSplineCurve PolesCount=4 KnotsCount=2 Degree=3 IsPeriodic=0
    g131: BSplineCurve PolesCount=4 KnotsCount=2 Degree=3 IsPeriodic=0
    g132: BSplineCurve PolesCount=4 KnotsCount=2 Degree=3 IsPeriodic=0
    g133: BSplineCurve PolesCount=4 KnotsCount=2 Degree=3 IsPeriodic=0
    g134: BSplineCurve PolesCount=4 KnotsCount=2 Degree=3 IsPeriodic=0
    g135: BSplineCurve PolesCount=4 KnotsCount=2 Degree=3 IsPeriodic=0
    g136: BSplineCurve PolesCount=4 KnotsCount=2 Degree=3 IsPeriodic=0
    g137: BSplineCurve PolesCount=4 KnotsCount=2 Degree=3 IsPeriodic=0
    g138: BSplineCurve PolesCount=4 KnotsCount=2 Degree=3 IsPeriodic=0
    g139: BSplineCurve PolesCount=4 KnotsCount=2 Degree=3 IsPeriodic=0
    g140: BSplineCurve PolesCount=4 KnotsCount=2 Degree=3 IsPeriodic=0
    g141: BSplineCurve PolesCount=4 KnotsCount=2 Degree=3 IsPeriodic=0
    g142: BSplineCurve PolesCount=4 KnotsCount=2 Degree=3 IsPeriodic=0
    g143: BSplineCurve PolesCount=4 KnotsCount=2 Degree=3 IsPeriodic=0
    g144: BSplineCurve PolesCount=4 KnotsCount=2 Degree=3 IsPeriodic=0
    g145: BSplineCurve PolesCount=4 KnotsCount=2 Degree=3 IsPeriodic=0
    g146: BSplineCurve PolesCount=4 KnotsCount=2 Degree=3 IsPeriodic=0
    g147: BSplineCurve PolesCount=4 KnotsCount=2 Degree=3 IsPeriodic=0
    g148: BSplineCurve PolesCount=4 KnotsCount=2 Degree=3 IsPeriodic=0
    g149: BSplineCurve PolesCount=4 KnotsCount=2 Degree=3 IsPeriodic=0
    g150: BSplineCurve PolesCount=4 KnotsCount=2 Degree=3 IsPeriodic=0
    g151: BSplineCurve PolesCount=4 KnotsCount=2 Degree=3 IsPeriodic=0
    g152: BSplineCurve PolesCount=4 KnotsCount=2 Degree=3 IsPeriodic=0
    g153: BSplineCurve PolesCount=4 KnotsCount=2 Degree=3 IsPeriodic=0
    g154: BSplineCurve PolesCount=4 KnotsCount=2 Degree=3 IsPeriodic=0
    g155: BSplineCurve PolesCount=4 KnotsCount=2 Degree=3 IsPeriodic=0
    g156: BSplineCurve PolesCount=4 KnotsCount=2 Degree=3 IsPeriodic=0
    g157: BSplineCurve PolesCount=4 KnotsCount=2 Degree=3 IsPeriodic=0
    g158: BSplineCurve PolesCount=4 KnotsCount=2 Degree=3 IsPeriodic=0
    g159: BSplineCurve PolesCount=4 KnotsCount=2 Degree=3 IsPeriodic=0
    g160: BSplineCurve PolesCount=4 KnotsCount=2 Degree=3 IsPeriodic=0
    g161: BSplineCurve PolesCount=4 KnotsCount=2 Degree=3 IsPeriodic=0
    g162: BSplineCurve PolesCount=4 KnotsCount=2 Degree=3 IsPeriodic=0
    g163: BSplineCurve PolesCount=4 KnotsCount=2 Degree=3 IsPeriodic=0
    g164: BSplineCurve PolesCount=4 KnotsCount=2 Degree=3 IsPeriodic=0
    g165: BSplineCurve PolesCount=4 KnotsCount=2 Degree=3 IsPeriodic=0
    g166: BSplineCurve PolesCount=2 KnotsCount=2 Degree=1 IsPeriodic=0
    g167: BSplineCurve PolesCount=2 KnotsCount=2 Degree=1 IsPeriodic=0
    g168: BSplineCurve PolesCount=4 KnotsCount=2 Degree=3 IsPeriodic=0
    g169: BSplineCurve PolesCount=4 KnotsCount=2 Degree=3 IsPeriodic=0
    g170: BSplineCurve PolesCount=4 KnotsCount=2 Degree=3 IsPeriodic=0
    g171: BSplineCurve PolesCount=4 KnotsCount=2 Degree=3 IsPeriodic=0
    g172: BSplineCurve PolesCount=4 KnotsCount=2 Degree=3 IsPeriodic=0
    g173: BSplineCurve PolesCount=4 KnotsCount=2 Degree=3 IsPeriodic=0
    g174: BSplineCurve PolesCount=4 KnotsCount=2 Degree=3 IsPeriodic=0
    g175: BSplineCurve PolesCount=4 KnotsCount=2 Degree=3 IsPeriodic=0
    g176: BSplineCurve PolesCount=4 KnotsCount=2 Degree=3 IsPeriodic=0
    g177: BSplineCurve PolesCount=4 KnotsCount=2 Degree=3 IsPeriodic=0
    g178: BSplineCurve PolesCount=4 KnotsCount=2 Degree=3 IsPeriodic=0
    g179: BSplineCurve PolesCount=4 KnotsCount=2 Degree=3 IsPeriodic=0
    g180: BSplineCurve PolesCount=4 KnotsCount=2 Degree=3 IsPeriodic=0
    g181: BSplineCurve PolesCount=4 KnotsCount=2 Degree=3 IsPeriodic=0
    g182: BSplineCurve PolesCount=4 KnotsCount=2 Degree=3 IsPeriodic=0
    g183: BSplineCurve PolesCount=4 KnotsCount=2 Degree=3 IsPeriodic=0
    g184: BSplineCurve PolesCount=4 KnotsCount=2 Degree=3 IsPeriodic=0
    g185: BSplineCurve PolesCount=4 KnotsCount=2 Degree=3 IsPeriodic=0
    g186: BSplineCurve PolesCount=4 KnotsCount=2 Degree=3 IsPeriodic=0
    g187: BSplineCurve PolesCount=4 KnotsCount=2 Degree=3 IsPeriodic=0
    g188: BSplineCurve PolesCount=4 KnotsCount=2 Degree=3 IsPeriodic=0
    g189: BSplineCurve PolesCount=4 KnotsCount=2 Degree=3 IsPeriodic=0
    g190: BSplineCurve PolesCount=4 KnotsCount=2 Degree=3 IsPeriodic=0
    g191: BSplineCurve PolesCount=2 KnotsCount=2 Degree=1 IsPeriodic=0
    g192: BSplineCurve PolesCount=2 KnotsCount=2 Degree=1 IsPeriodic=0
    g193: BSplineCurve PolesCount=4 KnotsCount=2 Degree=3 IsPeriodic=0
    g194: BSplineCurve PolesCount=4 KnotsCount=2 Degree=3 IsPeriodic=0
    g195: BSplineCurve PolesCount=4 KnotsCount=2 Degree=3 IsPeriodic=0
    g196: BSplineCurve PolesCount=4 KnotsCount=2 Degree=3 IsPeriodic=0
    g197: BSplineCurve PolesCount=4 KnotsCount=2 Degree=3 IsPeriodic=0
    g198: BSplineCurve PolesCount=4 KnotsCount=2 Degree=3 IsPeriodic=0
    g199: BSplineCurve PolesCount=4 KnotsCount=2 Degree=3 IsPeriodic=0
    g200: BSplineCurve PolesCount=4 KnotsCount=2 Degree=3 IsPeriodic=0
    g201: BSplineCurve PolesCount=4 KnotsCount=2 Degree=3 IsPeriodic=0
    g202: BSplineCurve PolesCount=4 KnotsCount=2 Degree=3 IsPeriodic=0
    g203: BSplineCurve PolesCount=4 KnotsCount=2 Degree=3 IsPeriodic=0
    g204: BSplineCurve PolesCount=4 KnotsCount=2 Degree=3 IsPeriodic=0
    g205: BSplineCurve PolesCount=4 KnotsCount=2 Degree=3 IsPeriodic=0
    g206: BSplineCurve PolesCount=4 KnotsCount=2 Degree=3 IsPeriodic=0
    g207: BSplineCurve PolesCount=4 KnotsCount=2 Degree=3 IsPeriodic=0
    g208: BSplineCurve PolesCount=4 KnotsCount=2 Degree=3 IsPeriodic=0
    g209: BSplineCurve PolesCount=4 KnotsCount=2 Degree=3 IsPeriodic=0
    g210: BSplineCurve PolesCount=4 KnotsCount=2 Degree=3 IsPeriodic=0
    g211: BSplineCurve PolesCount=4 KnotsCount=2 Degree=3 IsPeriodic=0
    g212: BSplineCurve PolesCount=4 KnotsCount=2 Degree=3 IsPeriodic=0
    g213: BSplineCurve PolesCount=2 KnotsCount=2 Degree=1 IsPeriodic=0
    g214: BSplineCurve PolesCount=2 KnotsCount=2 Degree=1 IsPeriodic=0
    g215: BSplineCurve PolesCount=4 KnotsCount=2 Degree=3 IsPeriodic=0
    g216: BSplineCurve PolesCount=4 KnotsCount=2 Degree=3 IsPeriodic=0
    g217: BSplineCurve PolesCount=4 KnotsCount=2 Degree=3 IsPeriodic=0
    g218: BSplineCurve PolesCount=4 KnotsCount=2 Degree=3 IsPeriodic=0
    g219: BSplineCurve PolesCount=2 KnotsCount=2 Degree=1 IsPeriodic=0
    g220: BSplineCurve PolesCount=2 KnotsCount=2 Degree=1 IsPeriodic=0
    g221: BSplineCurve PolesCount=4 KnotsCount=2 Degree=3 IsPeriodic=0
    g222: BSplineCurve PolesCount=4 KnotsCount=2 Degree=3 IsPeriodic=0
    g223: BSplineCurve PolesCount=4 KnotsCount=2 Degree=3 IsPeriodic=0
    g224: BSplineCurve PolesCount=4 KnotsCount=2 Degree=3 IsPeriodic=0
    g225: BSplineCurve PolesCount=4 KnotsCount=2 Degree=3 IsPeriodic=0
    g226: BSplineCurve PolesCount=4 KnotsCount=2 Degree=3 IsPeriodic=0
    g227: BSplineCurve PolesCount=4 KnotsCount=2 Degree=3 IsPeriodic=0
    g228: BSplineCurve PolesCount=4 KnotsCount=2 Degree=3 IsPeriodic=0
    g229: BSplineCurve PolesCount=4 KnotsCount=2 Degree=3 IsPeriodic=0
    g230: BSplineCurve PolesCount=4 KnotsCount=2 Degree=3 IsPeriodic=0
    g231: BSplineCurve PolesCount=4 KnotsCount=2 Degree=3 IsPeriodic=0
    g232: BSplineCurve PolesCount=4 KnotsCount=2 Degree=3 IsPeriodic=0
    g233: BSplineCurve PolesCount=4 KnotsCount=2 Degree=3 IsPeriodic=0
    g234: BSplineCurve PolesCount=4 KnotsCount=2 Degree=3 IsPeriodic=0
    g235: BSplineCurve PolesCount=4 KnotsCount=2 Degree=3 IsPeriodic=0
    g236: BSplineCurve PolesCount=2 KnotsCount=2 Degree=1 IsPeriodic=0
    g237: BSplineCurve PolesCount=2 KnotsCount=2 Degree=1 IsPeriodic=0
    g238: BSplineCurve PolesCount=4 KnotsCount=2 Degree=3 IsPeriodic=0
    g239: BSplineCurve PolesCount=4 KnotsCount=2 Degree=3 IsPeriodic=0
    g240: BSplineCurve PolesCount=4 KnotsCount=2 Degree=3 IsPeriodic=0
    g241: BSplineCurve PolesCount=4 KnotsCount=2 Degree=3 IsPeriodic=0
    g242: BSplineCurve PolesCount=4 KnotsCount=2 Degree=3 IsPeriodic=0
    g243: BSplineCurve PolesCount=4 KnotsCount=2 Degree=3 IsPeriodic=0
    g244: BSplineCurve PolesCount=4 KnotsCount=2 Degree=3 IsPeriodic=0
    g245: BSplineCurve PolesCount=4 KnotsCount=2 Degree=3 IsPeriodic=0
    g246: BSplineCurve PolesCount=4 KnotsCount=2 Degree=3 IsPeriodic=0
    g247: BSplineCurve PolesCount=4 KnotsCount=2 Degree=3 IsPeriodic=0
    g248: BSplineCurve PolesCount=4 KnotsCount=2 Degree=3 IsPeriodic=0
    g249: BSplineCurve PolesCount=4 KnotsCount=2 Degree=3 IsPeriodic=0
    g250: BSplineCurve PolesCount=4 KnotsCount=2 Degree=3 IsPeriodic=0
    g251: BSplineCurve PolesCount=4 KnotsCount=2 Degree=3 IsPeriodic=0
    g252: BSplineCurve PolesCount=4 KnotsCount=2 Degree=3 IsPeriodic=0
    g253: BSplineCurve PolesCount=4 KnotsCount=2 Degree=3 IsPeriodic=0
    g254: BSplineCurve PolesCount=4 KnotsCount=2 Degree=3 IsPeriodic=0
    g255: BSplineCurve PolesCount=4 KnotsCount=2 Degree=3 IsPeriodic=0
    g256: BSplineCurve PolesCount=2 KnotsCount=2 Degree=1 IsPeriodic=0
    g257: BSplineCurve PolesCount=2 KnotsCount=2 Degree=1 IsPeriodic=0
    g258: BSplineCurve PolesCount=4 KnotsCount=2 Degree=3 IsPeriodic=0
    g259: BSplineCurve PolesCount=4 KnotsCount=2 Degree=3 IsPeriodic=0
    g260: BSplineCurve PolesCount=4 KnotsCount=2 Degree=3 IsPeriodic=0
    g261: BSplineCurve PolesCount=4 KnotsCount=2 Degree=3 IsPeriodic=0
    g262: BSplineCurve PolesCount=4 KnotsCount=2 Degree=3 IsPeriodic=0
    g263: BSplineCurve PolesCount=4 KnotsCount=2 Degree=3 IsPeriodic=0
    g264: BSplineCurve PolesCount=4 KnotsCount=2 Degree=3 IsPeriodic=0
    g265: BSplineCurve PolesCount=4 KnotsCount=2 Degree=3 IsPeriodic=0
    g266: BSplineCurve PolesCount=4 KnotsCount=2 Degree=3 IsPeriodic=0
    g267: BSplineCurve PolesCount=4 KnotsCount=2 Degree=3 IsPeriodic=0
    g268: BSplineCurve PolesCount=4 KnotsCount=2 Degree=3 IsPeriodic=0
    g269: BSplineCurve PolesCount=4 KnotsCount=2 Degree=3 IsPeriodic=0
    g270: BSplineCurve PolesCount=4 KnotsCount=2 Degree=3 IsPeriodic=0
    g271: BSplineCurve PolesCount=4 KnotsCount=2 Degree=3 IsPeriodic=0
    g272: BSplineCurve PolesCount=4 KnotsCount=2 Degree=3 IsPeriodic=0
    g273: BSplineCurve PolesCount=4 KnotsCount=2 Degree=3 IsPeriodic=0
    g274: BSplineCurve PolesCount=4 KnotsCount=2 Degree=3 IsPeriodic=0
    g275: BSplineCurve PolesCount=4 KnotsCount=2 Degree=3 IsPeriodic=0
    g276: BSplineCurve PolesCount=4 KnotsCount=2 Degree=3 IsPeriodic=0
    g277: BSplineCurve PolesCount=4 KnotsCount=2 Degree=3 IsPeriodic=0
    g278: BSplineCurve PolesCount=4 KnotsCount=2 Degree=3 IsPeriodic=0
    g279: BSplineCurve PolesCount=4 KnotsCount=2 Degree=3 IsPeriodic=0
    g280: BSplineCurve PolesCount=4 KnotsCount=2 Degree=3 IsPeriodic=0
    g281: BSplineCurve PolesCount=4 KnotsCount=2 Degree=3 IsPeriodic=0
    g282: BSplineCurve PolesCount=4 KnotsCount=2 Degree=3 IsPeriodic=0
    g283: BSplineCurve PolesCount=4 KnotsCount=2 Degree=3 IsPeriodic=0
    g284: BSplineCurve PolesCount=4 KnotsCount=2 Degree=3 IsPeriodic=0
    g285: BSplineCurve PolesCount=4 KnotsCount=2 Degree=3 IsPeriodic=0
    g286: BSplineCurve PolesCount=4 KnotsCount=2 Degree=3 IsPeriodic=0
    g287: BSplineCurve PolesCount=4 KnotsCount=2 Degree=3 IsPeriodic=0
    g288: BSplineCurve PolesCount=4 KnotsCount=2 Degree=3 IsPeriodic=0
    g289: BSplineCurve PolesCount=4 KnotsCount=2 Degree=3 IsPeriodic=0
    g290: BSplineCurve PolesCount=4 KnotsCount=2 Degree=3 IsPeriodic=0
    g291: BSplineCurve PolesCount=4 KnotsCount=2 Degree=3 IsPeriodic=0
    g292: BSplineCurve PolesCount=4 KnotsCount=2 Degree=3 IsPeriodic=0
    g293: BSplineCurve PolesCount=4 KnotsCount=2 Degree=3 IsPeriodic=0
    g294: BSplineCurve PolesCount=4 KnotsCount=2 Degree=3 IsPeriodic=0
    g295: BSplineCurve PolesCount=4 KnotsCount=2 Degree=3 IsPeriodic=0
    g296: BSplineCurve PolesCount=4 KnotsCount=2 Degree=3 IsPeriodic=0
    g297: BSplineCurve PolesCount=4 KnotsCount=2 Degree=3 IsPeriodic=0
    g298: BSplineCurve PolesCount=4 KnotsCount=2 Degree=3 IsPeriodic=0
    g299: BSplineCurve PolesCount=4 KnotsCount=2 Degree=3 IsPeriodic=0
    g300: BSplineCurve PolesCount=4 KnotsCount=2 Degree=3 IsPeriodic=0
    g301: BSplineCurve PolesCount=2 KnotsCount=2 Degree=1 IsPeriodic=0
    g302: BSplineCurve PolesCount=2 KnotsCount=2 Degree=1 IsPeriodic=0
    g303: BSplineCurve PolesCount=4 KnotsCount=2 Degree=3 IsPeriodic=0
    g304: BSplineCurve PolesCount=4 KnotsCount=2 Degree=3 IsPeriodic=0
    g305: BSplineCurve PolesCount=4 KnotsCount=2 Degree=3 IsPeriodic=0
    g306: BSplineCurve PolesCount=4 KnotsCount=2 Degree=3 IsPeriodic=0
    g307: BSplineCurve PolesCount=4 KnotsCount=2 Degree=3 IsPeriodic=0
    g308: BSplineCurve PolesCount=4 KnotsCount=2 Degree=3 IsPeriodic=0
    g309: BSplineCurve PolesCount=4 KnotsCount=2 Degree=3 IsPeriodic=0
    g310: BSplineCurve PolesCount=4 KnotsCount=2 Degree=3 IsPeriodic=0
    g311: BSplineCurve PolesCount=4 KnotsCount=2 Degree=3 IsPeriodic=0
    g312: BSplineCurve PolesCount=4 KnotsCount=2 Degree=3 IsPeriodic=0
    g313: BSplineCurve PolesCount=4 KnotsCount=2 Degree=3 IsPeriodic=0
    g314: BSplineCurve PolesCount=4 KnotsCount=2 Degree=3 IsPeriodic=0
    g315: BSplineCurve PolesCount=4 KnotsCount=2 Degree=3 IsPeriodic=0
    g316: BSplineCurve PolesCount=4 KnotsCount=2 Degree=3 IsPeriodic=0
    g317: BSplineCurve PolesCount=4 KnotsCount=2 Degree=3 IsPeriodic=0
    g318: BSplineCurve PolesCount=4 KnotsCount=2 Degree=3 IsPeriodic=0
    g319: BSplineCurve PolesCount=4 KnotsCount=2 Degree=3 IsPeriodic=0
    g320: BSplineCurve PolesCount=4 KnotsCount=2 Degree=3 IsPeriodic=0
    g321: BSplineCurve PolesCount=4 KnotsCount=2 Degree=3 IsPeriodic=0
    g322: BSplineCurve PolesCount=2 KnotsCount=2 Degree=1 IsPeriodic=0
    g323: BSplineCurve PolesCount=2 KnotsCount=2 Degree=1 IsPeriodic=0
    g324: BSplineCurve PolesCount=4 KnotsCount=2 Degree=3 IsPeriodic=0
    g325: BSplineCurve PolesCount=4 KnotsCount=2 Degree=3 IsPeriodic=0
    g326: BSplineCurve PolesCount=4 KnotsCount=2 Degree=3 IsPeriodic=0
    g327: BSplineCurve PolesCount=4 KnotsCount=2 Degree=3 IsPeriodic=0
    g328: BSplineCurve PolesCount=4 KnotsCount=2 Degree=3 IsPeriodic=0
    g329: BSplineCurve PolesCount=2 KnotsCount=2 Degree=1 IsPeriodic=0
    g330: BSplineCurve PolesCount=2 KnotsCount=2 Degree=1 IsPeriodic=0
    g331: BSplineCurve PolesCount=4 KnotsCount=2 Degree=3 IsPeriodic=0
    g332: BSplineCurve PolesCount=4 KnotsCount=2 Degree=3 IsPeriodic=0
    g333: BSplineCurve PolesCount=4 KnotsCount=2 Degree=3 IsPeriodic=0
    g334: BSplineCurve PolesCount=4 KnotsCount=2 Degree=3 IsPeriodic=0
    g335: BSplineCurve PolesCount=4 KnotsCount=2 Degree=3 IsPeriodic=0
    g336: BSplineCurve PolesCount=4 KnotsCount=2 Degree=3 IsPeriodic=0
    g337: BSplineCurve PolesCount=4 KnotsCount=2 Degree=3 IsPeriodic=0
    g338: BSplineCurve PolesCount=2 KnotsCount=2 Degree=1 IsPeriodic=0
    g339: BSplineCurve PolesCount=2 KnotsCount=2 Degree=1 IsPeriodic=0
    g340: BSplineCurve PolesCount=4 KnotsCount=2 Degree=3 IsPeriodic=0
    g341: BSplineCurve PolesCount=4 KnotsCount=2 Degree=3 IsPeriodic=0
    g342: BSplineCurve PolesCount=4 KnotsCount=2 Degree=3 IsPeriodic=0
    g343: BSplineCurve PolesCount=4 KnotsCount=2 Degree=3 IsPeriodic=0
    g344: BSplineCurve PolesCount=4 KnotsCount=2 Degree=3 IsPeriodic=0
    g345: BSplineCurve PolesCount=4 KnotsCount=2 Degree=3 IsPeriodic=0
    g346: BSplineCurve PolesCount=4 KnotsCount=2 Degree=3 IsPeriodic=0
    g347: BSplineCurve PolesCount=4 KnotsCount=2 Degree=3 IsPeriodic=0
    g348: BSplineCurve PolesCount=2 KnotsCount=2 Degree=1 IsPeriodic=0
    g349: BSplineCurve PolesCount=2 KnotsCount=2 Degree=1 IsPeriodic=0
    g350: BSplineCurve PolesCount=2 KnotsCount=2 Degree=1 IsPeriodic=0
    g351: BSplineCurve PolesCount=2 KnotsCount=2 Degree=1 IsPeriodic=0
    g352: BSplineCurve PolesCount=4 KnotsCount=2 Degree=3 IsPeriodic=0
    g353: BSplineCurve PolesCount=4 KnotsCount=2 Degree=3 IsPeriodic=0
    g354: BSplineCurve PolesCount=4 KnotsCount=2 Degree=3 IsPeriodic=0
    g355: BSplineCurve PolesCount=4 KnotsCount=2 Degree=3 IsPeriodic=0
    g356: BSplineCurve PolesCount=4 KnotsCount=2 Degree=3 IsPeriodic=0
    g357: BSplineCurve PolesCount=4 KnotsCount=2 Degree=3 IsPeriodic=0
    g358: BSplineCurve PolesCount=4 KnotsCount=2 Degree=3 IsPeriodic=0
    g359: BSplineCurve PolesCount=4 KnotsCount=2 Degree=3 IsPeriodic=0
    g360: BSplineCurve PolesCount=4 KnotsCount=2 Degree=3 IsPeriodic=0
    g361: BSplineCurve PolesCount=4 KnotsCount=2 Degree=3 IsPeriodic=0
    g362: BSplineCurve PolesCount=4 KnotsCount=2 Degree=3 IsPeriodic=0
    g363: BSplineCurve PolesCount=4 KnotsCount=2 Degree=3 IsPeriodic=0
    g364: BSplineCurve PolesCount=4 KnotsCount=2 Degree=3 IsPeriodic=0
    g365: BSplineCurve PolesCount=4 KnotsCount=2 Degree=3 IsPeriodic=0
    g366: BSplineCurve PolesCount=4 KnotsCount=2 Degree=3 IsPeriodic=0
    g367: BSplineCurve PolesCount=4 KnotsCount=2 Degree=3 IsPeriodic=0
    g368: BSplineCurve PolesCount=4 KnotsCount=2 Degree=3 IsPeriodic=0
    g369: BSplineCurve PolesCount=4 KnotsCount=2 Degree=3 IsPeriodic=0
    g370: BSplineCurve PolesCount=4 KnotsCount=2 Degree=3 IsPeriodic=0
    g371: BSplineCurve PolesCount=4 KnotsCount=2 Degree=3 IsPeriodic=0
    g372: BSplineCurve PolesCount=4 KnotsCount=2 Degree=3 IsPeriodic=0
    g373: BSplineCurve PolesCount=4 KnotsCount=2 Degree=3 IsPeriodic=0
    g374: BSplineCurve PolesCount=2 KnotsCount=2 Degree=1 IsPeriodic=0
    g375: BSplineCurve PolesCount=2 KnotsCount=2 Degree=1 IsPeriodic=0
    g376: BSplineCurve PolesCount=4 KnotsCount=2 Degree=3 IsPeriodic=0
    g377: BSplineCurve PolesCount=4 KnotsCount=2 Degree=3 IsPeriodic=0
    g378: BSplineCurve PolesCount=4 KnotsCount=2 Degree=3 IsPeriodic=0
    g379: BSplineCurve PolesCount=4 KnotsCount=2 Degree=3 IsPeriodic=0
    g380: BSplineCurve PolesCount=4 KnotsCount=2 Degree=3 IsPeriodic=0
    g381: BSplineCurve PolesCount=4 KnotsCount=2 Degree=3 IsPeriodic=0
    g382: BSplineCurve PolesCount=4 KnotsCount=2 Degree=3 IsPeriodic=0
    g383: BSplineCurve PolesCount=4 KnotsCount=2 Degree=3 IsPeriodic=0
    g384: BSplineCurve PolesCount=4 KnotsCount=2 Degree=3 IsPeriodic=0
    g385: BSplineCurve PolesCount=4 KnotsCount=2 Degree=3 IsPeriodic=0
    g386: BSplineCurve PolesCount=4 KnotsCount=2 Degree=3 IsPeriodic=0
    g387: BSplineCurve PolesCount=4 KnotsCount=2 Degree=3 IsPeriodic=0
    g388: BSplineCurve PolesCount=4 KnotsCount=2 Degree=3 IsPeriodic=0
    g389: BSplineCurve PolesCount=4 KnotsCount=2 Degree=3 IsPeriodic=0
    g390: BSplineCurve PolesCount=4 KnotsCount=2 Degree=3 IsPeriodic=0
    g391: BSplineCurve PolesCount=4 KnotsCount=2 Degree=3 IsPeriodic=0
    g392: BSplineCurve PolesCount=4 KnotsCount=2 Degree=3 IsPeriodic=0
    g393: BSplineCurve PolesCount=4 KnotsCount=2 Degree=3 IsPeriodic=0
    g394: BSplineCurve PolesCount=4 KnotsCount=2 Degree=3 IsPeriodic=0
    g395: BSplineCurve PolesCount=4 KnotsCount=2 Degree=3 IsPeriodic=0
    g396: BSplineCurve PolesCount=4 KnotsCount=2 Degree=3 IsPeriodic=0
    g397: BSplineCurve PolesCount=4 KnotsCount=2 Degree=3 IsPeriodic=0
    g398: BSplineCurve PolesCount=4 KnotsCount=2 Degree=3 IsPeriodic=0
    g399: BSplineCurve PolesCount=4 KnotsCount=2 Degree=3 IsPeriodic=0
    ... +419 more geometry lines
  constraints (819):
    c: Coincident(g0,g1)
    c: Coincident(g1,g2)
    c: Coincident(g2,g3)
    c: Coincident(g3,g4)
    c: Coincident(g4,g5)
    c: Coincident(g5,g6)
    c: Coincident(g6,g7)
    c: Coincident(g7,g8)
    c: Coincident(g8,g9)
    c: Coincident(g9,g10)
    c: Coincident(g10,g11)
    c: Coincident(g11,g12)
    c: Coincident(g12,g13)
    c: Coincident(g13,g14)
    c: Coincident(g14,g15)
    c: Coincident(g15,g16)
    c: Coincident(g16,g17)
    c: Coincident(g17,g18)
    c: Coincident(g18,g19)
    c: Coincident(g19,g20)
    c: Coincident(g20,g21)
    c: Coincident(g21,g22)
    c: Coincident(g22,g23)
    c: Coincident(g23,g24)
    c: Coincident(g24,g25)
    c: Coincident(g25,g26)
    c: Coincident(g26,g27)
    c: Coincident(g27,g28)
    c: Coincident(g28,g29)
    c: Coincident(g29,g30)
    c: Coincident(g30,g31)
    c: Coincident(g31,g32)
    c: Coincident(g32,g33)
    c: Coincident(g33,g34)
    c: Coincident(g34,g35)
    c: Coincident(g35,g36)
    c: Coincident(g36,g37)
    c: Coincident(g37,g38)
    c: Coincident(g38,g39)
    c: Coincident(g39,g40)
    c: Coincident(g40,g41)
    c: Coincident(g41,g42)
    c: Coincident(g42,g43)
    c: Coincident(g43,g44)
    c: Coincident(g44,g45)
    c: Coincident(g45,g46)
    c: Coincident(g46,g47)
    c: Coincident(g47,g48)
    c: Coincident(g48,g49)
    c: Coincident(g49,g50)
    c: Coincident(g50,g51)
    c: Coincident(g51,g52)
    c: Coincident(g52,g53)
    c: Coincident(g53,g54)
    c: Coincident(g54,g55)
    c: Coincident(g55,g56)
    c: Coincident(g56,g57)
    c: Coincident(g57,g58)
    c: Coincident(g58,g59)
    c: Coincident(g59,g60)
    c: Coincident(g60,g61)
    c: Coincident(g61,g62)
    c: Coincident(g62,g63)
    c: Coincident(g63,g64)
    c: Coincident(g64,g65)
    c: Coincident(g65,g66)
    c: Coincident(g66,g67)
    c: Coincident(g67,g68)
    c: Coincident(g68,g69)
    c: Coincident(g69,g70)
    c: Coincident(g70,g71)
    c: Coincident(g71,g72)
    c: Coincident(g72,g73)
    c: Coincident(g73,g74)
    c: Coincident(g74,g75)
    c: Coincident(g75,g76)
    c: Coincident(g76,g77)
    c: Coincident(g77,g78)
    c: Coincident(g78,g79)
    c: Coincident(g79,g80)
    c: Coincident(g80,g81)
    c: Coincident(g81,g82)
    c: Coincident(g82,g83)
    c: Coincident(g83,g84)
    c: Coincident(g84,g85)
    c: Coincident(g85,g86)
    c: Coincident(g86,g87)
    c: Coincident(g87,g88)
    c: Coincident(g88,g89)
    c: Coincident(g89,g90)
    c: Coincident(g90,g91)
    c: Coincident(g91,g92)
    c: Coincident(g92,g93)
    c: Coincident(g93,g94)
    c: Coincident(g94,g95)
    c: Coincident(g95,g96)
    c: Coincident(g96,g97)
    c: Coincident(g97,g98)
    c: Coincident(g98,g99)
    c: Coincident(g99,g100)
    c: Coincident(g100,g101)
    c: Coincident(g101,g102)
    c: Coincident(g102,g103)
    c: Coincident(g103,g104)
    c: Coincident(g104,g105)
    c: Coincident(g105,g106)
    c: Coincident(g106,g107)
    c: Coincident(g107,g108)
    c: Coincident(g108,g109)
    c: Coincident(g109,g110)
    c: Coincident(g110,g111)
    c: Coincident(g111,g112)
    c: Coincident(g112,g113)
    c: Coincident(g113,g114)
    c: Coincident(g114,g115)
    c: Coincident(g115,g116)
    c: Coincident(g116,g117)
    c: Coincident(g117,g118)
    c: Coincident(g118,g119)
    c: Coincident(g119,g120)
    c: Coincident(g120,g121)
    c: Coincident(g121,g122)
    c: Coincident(g122,g123)
    c: Coincident(g123,g124)
    c: Coincident(g124,g125)
    c: Coincident(g125,g126)
    c: Coincident(g126,g127)
    c: Coincident(g127,g128)
    c: Coincident(g128,g129)
    c: Coincident(g129,g130)
    c: Coincident(g130,g131)
    c: Coincident(g131,g132)
    c: Coincident(g132,g133)
    c: Coincident(g133,g134)
    c: Coincident(g134,g135)
    c: Coincident(g135,g136)
    c: Coincident(g136,g137)
    c: Coincident(g137,g138)
    c: Coincident(g138,g139)
    c: Coincident(g139,g140)
    c: Coincident(g140,g141)
    c: Coincident(g141,g142)
    c: Coincident(g142,g143)
    c: Coincident(g143,g144)
    c: Coincident(g144,g145)
    c: Coincident(g145,g146)
    c: Coincident(g146,g147)
    c: Coincident(g147,g148)
    c: Coincident(g148,g149)
    c: Coincident(g149,g150)
    c: Coincident(g150,g151)
    c: Coincident(g151,g152)
    c: Coincident(g152,g153)
    c: Coincident(g153,g154)
    c: Coincident(g154,g155)
    c: Coincident(g155,g156)
    c: Coincident(g156,g157)
    c: Coincident(g157,g158)
    c: Coincident(g158,g159)
    c: Coincident(g159,g160)
    c: Coincident(g160,g161)
    c: Coincident(g161,g162)
    c: Coincident(g162,g163)
    c: Coincident(g163,g164)
    c: Coincident(g164,g165)
    c: Coincident(g165,g166)
    c: Coincident(g166,g167)
    c: Coincident(g167,g168)
    c: Coincident(g168,g169)
    c: Coincident(g169,g170)
    c: Coincident(g170,g171)
    c: Coincident(g171,g172)
    c: Coincident(g172,g173)
    c: Coincident(g173,g174)
    c: Coincident(g174,g175)
    c: Coincident(g175,g176)
    c: Coincident(g176,g177)
    c: Coincident(g177,g178)
    c: Coincident(g178,g179)
    c: Coincident(g179,g180)
    c: Coincident(g180,g181)
    c: Coincident(g181,g182)
    c: Coincident(g182,g183)
    c: Coincident(g183,g184)
    c: Coincident(g184,g185)
    c: Coincident(g185,g186)
    c: Coincident(g186,g187)
    c: Coincident(g187,g188)
    c: Coincident(g188,g189)
    c: Coincident(g189,g190)
    c: Coincident(g190,g191)
    c: Coincident(g191,g192)
    c: Coincident(g192,g193)
    c: Coincident(g193,g194)
    c: Coincident(g194,g195)
    c: Coincident(g195,g196)
    c: Coincident(g196,g197)
    c: Coincident(g197,g198)
    c: Coincident(g198,g199)
    c: Coincident(g199,g200)
    c: Coincident(g200,g201)
    c: Coincident(g201,g202)
    c: Coincident(g202,g203)
    c: Coincident(g203,g204)
    c: Coincident(g204,g205)
    c: Coincident(g205,g206)
    c: Coincident(g206,g207)
    c: Coincident(g207,g208)
    c: Coincident(g208,g209)
    c: Coincident(g209,g210)
    c: Coincident(g210,g211)
    c: Coincident(g211,g212)
    c: Coincident(g212,g213)
    c: Coincident(g213,g214)
    c: Coincident(g214,g215)
    c: Coincident(g215,g216)
    c: Coincident(g216,g217)
    c: Coincident(g217,g218)
    c: Coincident(g218,g219)
    c: Coincident(g219,g220)
    c: Coincident(g220,g221)
    c: Coincident(g221,g222)
    c: Coincident(g222,g223)
    c: Coincident(g223,g224)
    c: Coincident(g224,g225)
    c: Coincident(g225,g226)
    c: Coincident(g226,g227)
    c: Coincident(g227,g228)
    c: Coincident(g228,g229)
    c: Coincident(g229,g230)
    c: Coincident(g230,g231)
    c: Coincident(g231,g232)
    c: Coincident(g232,g233)
    c: Coincident(g233,g234)
    c: Coincident(g234,g235)
    c: Coincident(g235,g236)
    c: Coincident(g236,g237)
    c: Coincident(g237,g238)
    c: Coincident(g238,g239)
    c: Coincident(g239,g240)
    c: Coincident(g240,g241)
    c: Coincident(g241,g242)
    c: Coincident(g242,g243)
    c: Coincident(g243,g244)
    c: Coincident(g244,g245)
    c: Coincident(g245,g246)
    c: Coincident(g246,g247)
    c: Coincident(g247,g248)
    c: Coincident(g248,g249)
    c: Coincident(g249,g250)
    c: Coincident(g250,g251)
    c: Coincident(g251,g252)
    c: Coincident(g252,g253)
    c: Coincident(g253,g254)
    c: Coincident(g254,g255)
    c: Coincident(g255,g256)
    c: Coincident(g256,g257)
    c: Coincident(g257,g258)
    c: Coincident(g258,g259)
    c: Coincident(g259,g260)
    c: Coincident(g260,g261)
    c: Coincident(g261,g262)
    c: Coincident(g262,g263)
    c: Coincident(g263,g264)
    c: Coincident(g264,g265)
    c: Coincident(g265,g266)
    c: Coincident(g266,g267)
    c: Coincident(g267,g268)
    c: Coincident(g268,g269)
    c: Coincident(g269,g270)
    c: Coincident(g270,g271)
    c: Coincident(g271,g272)
    c: Coincident(g272,g273)
    c: Coincident(g273,g274)
    c: Coincident(g274,g275)
    c: Coincident(g275,g276)
    c: Coincident(g276,g277)
    c: Coincident(g277,g278)
    c: Coincident(g278,g279)
    c: Coincident(g279,g280)
    c: Coincident(g280,g281)
    c: Coincident(g281,g282)
    c: Coincident(g282,g283)
    c: Coincident(g283,g284)
    c: Coincident(g284,g285)
    c: Coincident(g285,g286)
    c: Coincident(g286,g287)
    c: Coincident(g287,g288)
    c: Coincident(g288,g289)
    c: Coincident(g289,g290)
    c: Coincident(g290,g291)
    c: Coincident(g291,g292)
    c: Coincident(g292,g293)
    c: Coincident(g293,g294)
    c: Coincident(g294,g295)
    c: Coincident(g295,g296)
    c: Coincident(g296,g297)
    c: Coincident(g297,g298)
    c: Coincident(g298,g299)
    c: Coincident(g299,g300)
    c: Coincident(g300,g301)
    c: Coincident(g301,g302)
    c: Coincident(g302,g303)
    c: Coincident(g303,g304)
    c: Coincident(g304,g305)
    c: Coincident(g305,g306)
    c: Coincident(g306,g307)
    c: Coincident(g307,g308)
    c: Coincident(g308,g309)
    c: Coincident(g309,g310)
    c: Coincident(g310,g311)
    c: Coincident(g311,g312)
    c: Coincident(g312,g313)
    c: Coincident(g313,g314)
    c: Coincident(g314,g315)
    c: Coincident(g315,g316)
    c: Coincident(g316,g317)
    c: Coincident(g317,g318)
    c: Coincident(g318,g319)
    c: Coincident(g319,g320)
    c: Coincident(g320,g321)
    c: Coincident(g321,g322)
    c: Coincident(g322,g323)
    c: Coincident(g323,g324)
    c: Coincident(g324,g325)
    c: Coincident(g325,g326)
    c: Coincident(g326,g327)
    c: Coincident(g327,g328)
    c: Coincident(g328,g329)
    c: Coincident(g329,g330)
    c: Coincident(g330,g331)
    c: Coincident(g331,g332)
    c: Coincident(g332,g333)
    c: Coincident(g333,g334)
    c: Coincident(g334,g335)
    c: Coincident(g335,g336)
    c: Coincident(g336,g337)
    c: Coincident(g337,g338)
    c: Coincident(g338,g339)
    c: Coincident(g339,g340)
    c: Coincident(g340,g341)
    c: Coincident(g341,g342)
    c: Coincident(g342,g343)
    c: Coincident(g343,g344)
    c: Coincident(g344,g345)
    c: Coincident(g345,g346)
    c: Coincident(g346,g347)
    c: Coincident(g347,g348)
    c: Coincident(g348,g349)
    c: Coincident(g349,g350)
    c: Coincident(g350,g351)
    c: Coincident(g351,g352)
    c: Coincident(g352,g353)
    c: Coincident(g353,g354)
    c: Coincident(g354,g355)
    c: Coincident(g355,g356)
    c: Coincident(g356,g357)
    c: Coincident(g357,g358)
    c: Coincident(g358,g359)
    c: Coincident(g359,g360)
    c: Coincident(g360,g361)
    c: Coincident(g361,g362)
    c: Coincident(g362,g363)
    c: Coincident(g363,g364)
    c: Coincident(g364,g365)
    c: Coincident(g365,g366)
    c: Coincident(g366,g367)
    c: Coincident(g367,g368)
    c: Coincident(g368,g369)
    c: Coincident(g369,g370)
    c: Coincident(g370,g371)
    c: Coincident(g371,g372)
    c: Coincident(g372,g373)
    c: Coincident(g373,g374)
    c: Coincident(g374,g375)
    c: Coincident(g375,g376)
    c: Coincident(g376,g377)
    c: Coincident(g377,g378)
    c: Coincident(g378,g379)
    c: Coincident(g379,g380)
    c: Coincident(g380,g381)
    c: Coincident(g381,g382)
    c: Coincident(g382,g383)
    c: Coincident(g383,g384)
    c: Coincident(g384,g385)
    c: Coincident(g385,g386)
    c: Coincident(g386,g387)
    c: Coincident(g387,g388)
    c: Coincident(g388,g389)
    c: Coincident(g389,g390)
    c: Coincident(g390,g391)
    c: Coincident(g391,g392)
    c: Coincident(g392,g393)
    c: Coincident(g393,g394)
    c: Coincident(g394,g395)
    c: Coincident(g395,g396)
    c: Coincident(g396,g397)
    c: Coincident(g397,g398)
    c: Coincident(g398,g399)
    c: Coincident(g399,g400)
    c: Coincident(g400,g401)
    c: Coincident(g401,g402)
    c: Coincident(g402,g403)
    c: Coincident(g403,g404)
    c: Coincident(g404,g405)
    c: Coincident(g405,g406)
    c: Coincident(g406,g407)
    c: Coincident(g407,g408)
    c: Coincident(g408,g409)
    c: Coincident(g409,g410)
    c: Coincident(g410,g411)
    c: Coincident(g411,g412)
    c: Coincident(g412,g413)
    c: Coincident(g413,g414)
    c: Coincident(g414,g415)
    c: Coincident(g415,g416)
    c: Coincident(g416,g417)
    c: Coincident(g417,g418)
    c: Coincident(g418,g419)
    c: Coincident(g419,g420)
    c: Coincident(g420,g421)
    c: Coincident(g421,g422)
    c: Coincident(g422,g423)
    c: Coincident(g423,g424)
    c: Coincident(g424,g425)
    c: Coincident(g425,g426)
    c: Coincident(g426,g427)
    c: Coincident(g427,g428)
    c: Coincident(g428,g429)
    c: Coincident(g429,g430)
    c: Coincident(g430,g431)
    c: Coincident(g431,g432)
    c: Coincident(g432,g433)
    c: Coincident(g433,g434)
    c: Coincident(g434,g435)
    c: Coincident(g435,g436)
    c: Coincident(g436,g437)
    c: Coincident(g437,g438)
    c: Coincident(g438,g439)
    c: Coincident(g439,g440)
    c: Coincident(g440,g441)
    c: Coincident(g441,g442)
    c: Coincident(g442,g443)
    c: Coincident(g443,g444)
    c: Coincident(g444,g445)
    c: Coincident(g445,g446)
    c: Coincident(g446,g447)
    c: Coincident(g447,g448)
    c: Coincident(g448,g449)
    c: Coincident(g449,g450)
    c: Coincident(g450,g451)
    c: Coincident(g451,g452)
    c: Coincident(g452,g453)
    c: Coincident(g453,g454)
    c: Coincident(g454,g455)
    c: Coincident(g455,g456)
    c: Coincident(g456,g457)
    c: Coincident(g457,g458)
    c: Coincident(g458,g459)
    c: Coincident(g459,g460)
    c: Coincident(g460,g461)
    c: Coincident(g461,g462)
    c: Coincident(g462,g463)
    c: Coincident(g463,g464)
    c: Coincident(g464,g465)
    c: Coincident(g465,g466)
    c: Coincident(g466,g467)
    c: Coincident(g467,g468)
    c: Coincident(g468,g469)
    c: Coincident(g469,g470)
    c: Coincident(g470,g471)
    c: Coincident(g471,g0)
    c: Coincident(g472,g473)
    c: Coincident(g473,g474)
    c: Coincident(g474,g472)
    c: Coincident(g475,g476)
    c: Coincident(g476,g477)
    c: Coincident(g477,g475)
    c: Coincident(g478,g479)
    c: Coincident(g479,g480)
    c: Coincident(g480,g478)
    c: Coincident(g481,g482)
    c: Coincident(g482,g483)
    c: Coincident(g484,g485)
    c: Coincident(g485,g486)
    c: Coincident(g486,g484)
    c: Coincident(g487,g488)
    c: Coincident(g488,g489)
    c: Coincident(g489,g487)
    c: Coincident(g490,g491)
    c: Coincident(g491,g492)
    c: Coincident(g492,g493)
    c: Coincident(g493,g494)
    c: Coincident(g494,g495)
    c: Coincident(g495,g496)
    c: Coincident(g496,g497)
    c: Coincident(g497,g498)
    c: Coincident(g498,g499)
    c: Coincident(g499,g500)
    c: Coincident(g500,g490)
    c: Coincident(g501,g502)
    c: Coincident(g502,g503)
    c: Coincident(g503,g501)
    c: Coincident(g504,g505)
    c: Coincident(g505,g506)
    c: Coincident(g506,g507)
    c: Coincident(g507,g504)
    c: Coincident(g509,g510)
    c: Coincident(g510,g508)
    c: Coincident(g511,g512)
    c: Coincident(g512,g513)
    c: Coincident(g514,g515)
    c: Coincident(g515,g516)
    c: Coincident(g517,g518)
    c: Coincident(g518,g519)
    c: Coincident(g519,g517)
    c: Coincident(g520,g521)
    c: Coincident(g521,g522)
    c: Coincident(g522,g523)
    c: Coincident(g523,g524)
    c: Coincident(g524,g520)
    c: Coincident(g525,g526)
    c: Coincident(g526,g527)
    c: Coincident(g527,g525)
    c: Coincident(g528,g529)
    c: Coincident(g529,g530)
    c: Coincident(g531,g532)
    c: Coincident(g532,g533)
    c: Coincident(g533,g534)
    c: Coincident(g534,g531)
    c: Coincident(g535,g536)
    c: Coincident(g536,g537)
    c: Coincident(g537,g535)
    c: Coincident(g538,g539)
    c: Coincident(g539,g540)
    c: Coincident(g540,g538)
    c: Coincident(g541,g542)
    c: Coincident(g542,g543)
    c: Coincident(g544,g545)
    c: Coincident(g545,g546)
    c: Coincident(g546,g544)
    c: Coincident(g547,g548)
    c: Coincident(g548,g549)
    c: Coincident(g549,g547)
    c: Coincident(g550,g551)
    c: Coincident(g551,g552)
    c: Coincident(g552,g550)
    c: Coincident(g553,g554)
    c: Coincident(g554,g555)
    c: Coincident(g555,g553)
    c: Coincident(g556,g557)
    c: Coincident(g557,g558)
    c: Coincident(g558,g559)
    c: Coincident(g559,g556)
    c: Coincident(g560,g561)
    c: Coincident(g561,g562)
    c: Coincident(g562,g560)
    c: Coincident(g563,g564)
    c: Coincident(g564,g565)
    c: Coincident(g565,g566)
    c: Coincident(g566,g567)
    c: Coincident(g567,g568)
    c: Coincident(g568,g563)
    c: Coincident(g569,g570)
    c: Coincident(g570,g571)
    c: Coincident(g571,g572)
    c: Coincident(g572,g569)
    c: Coincident(g573,g574)
    c: Coincident(g574,g575)
    c: Coincident(g575,g576)
    c: Coincident(g576,g577)
    c: Coincident(g577,g578)
    c: Coincident(g578,g579)
    c: Coincident(g579,g580)
    c: Coincident(g580,g581)
    c: Coincident(g582,g583)
    c: Coincident(g583,g584)
    c: Coincident(g584,g585)
    c: Coincident(g586,g587)
    c: Coincident(g587,g588)
    c: Coincident(g588,g589)
    c: Coincident(g589,g590)
    c: Coincident(g590,g591)
    c: Coincident(g591,g592)
    c: Coincident(g593,g594)
    c: Coincident(g594,g595)
    c: Coincident(g595,g593)
    c: Coincident(g596,g597)
    c: Coincident(g597,g598)
    c: Coincident(g598,g596)
    c: Coincident(g599,g600)
    c: Coincident(g600,g601)
    c: Coincident(g601,g602)
    c: Coincident(g602,g603)
    c: Coincident(g603,g604)
    c: Coincident(g604,g605)
    c: Coincident(g605,g606)
    c: Coincident(g606,g607)
    c: Coincident(g607,g608)
    c: Coincident(g608,g609)
    c: Coincident(g609,g610)
    c: Coincident(g610,g611)
    c: Coincident(g611,g612)
    c: Coincident(g612,g599)
    c: Coincident(g613,g614)
    c: Coincident(g614,g615)
    c: Coincident(g615,g613)
    c: Coincident(g616,g617)
    c: Coincident(g617,g618)
    c: Coincident(g619,g620)
    c: Coincident(g620,g621)
    c: Coincident(g621,g619)
    c: Coincident(g622,g623)
    c: Coincident(g623,g624)
    c: Coincident(g624,g622)
    c: Coincident(g625,g626)
    c: Coincident(g626,g627)
    c: Coincident(g627,g628)
    c: Coincident(g628,g625)
    c: Coincident(g629,g630)
    c: Coincident(g630,g631)
    c: Coincident(g631,g632)
    c: Coincident(g632,g633)
    c: Coincident(g633,g629)
    c: Coincident(g634,g635)
    c: Coincident(g635,g636)
    c: Coincident(g636,g637)
    c: Coincident(g637,g638)
    c: Coincident(g638,g634)
    c: Coincident(g639,g640)
    c: Coincident(g640,g641)
    c: Coincident(g641,g639)
    c: Coincident(g642,g643)
    c: Coincident(g643,g644)
    c: Coincident(g645,g646)
    c: Coincident(g646,g647)
    c: Coincident(g648,g649)
    c: Coincident(g649,g650)
    c: Coincident(g650,g648)
    c: Coincident(g651,g652)
    c: Coincident(g652,g653)
    c: Coincident(g653,g654)
    c: Coincident(g654,g651)
    c: Coincident(g655,g656)
    c: Coincident(g656,g657)
    c: Coincident(g657,g655)
    c: Coincident(g658,g659)
    c: Coincident(g659,g660)
    c: Coincident(g660,g661)
    c: Coincident(g661,g662)
    c: Coincident(g663,g664)
    c: Coincident(g664,g665)
    c: Coincident(g666,g667)
    c: Coincident(g667,g668)
    c: Coincident(g668,g669)
    c: Coincident(g669,g666)
    c: Coincident(g670,g671)
    c: Coincident(g671,g672)
    c: Coincident(g672,g670)
    c: Coincident(g673,g674)
    c: Coincident(g674,g675)
    c: Coincident(g675,g673)
    c: Coincident(g676,g677)
    c: Coincident(g677,g678)
    c: Coincident(g678,g676)
    c: Coincident(g679,g680)
    c: Coincident(g680,g681)
    c: Coincident(g681,g679)
    c: Coincident(g682,g683)
    c: Coincident(g683,g684)
    c: Coincident(g684,g682)
    c: Coincident(g685,g686)
    c: Coincident(g686,g687)
    c: Coincident(g687,g685)
    c: Coincident(g688,g689)
    c: Coincident(g689,g690)
    c: Coincident(g691,g692)
    c: Coincident(g692,g693)
    c: Coincident(g693,g691)
    c: Coincident(g694,g695)
    c: Coincident(g695,g696)
    c: Coincident(g696,g697)
    c: Coincident(g697,g698)
    c: Coincident(g698,g694)
    c: Coincident(g699,g700)
    c: Coincident(g700,g701)
    c: Coincident(g701,g702)
    c: Coincident(g702,g703)
    c: Coincident(g703,g699)
    c: Coincident(g704,g705)
    c: Coincident(g705,g706)
    c: Coincident(g706,g707)
    c: Coincident(g707,g704)
    c: Coincident(g708,g709)
    c: Coincident(g709,g710)
    c: Coincident(g710,g708)
    c: Coincident(g711,g712)
    c: Coincident(g712,g713)
    c: Coincident(g714,g715)
    c: Coincident(g715,g716)
    c: Coincident(g716,g717)
    c: Coincident(g717,g714)
    c: Coincident(g718,g719)
    c: Coincident(g719,g720)
    c: Coincident(g720,g718)
    c: Coincident(g721,g722)
    c: Coincident(g722,g723)
    c: Coincident(g723,g721)
    c: Coincident(g724,g725)
    c: Coincident(g725,g726)
    c: Coincident(g726,g727)
    c: Coincident(g727,g728)
    c: Coincident(g728,g729)
    c: Coincident(g729,g730)
    c: Coincident(g730,g731)
    c: Coincident(g731,g732)
    c: Coincident(g732,g733)
    c: Coincident(g733,g734)
    c: Coincident(g734,g735)
    c: Coincident(g735,g736)
    c: Coincident(g736,g724)
    c: Coincident(g737,g738)
    c: Coincident(g738,g739)
    c: Coincident(g740,g741)
    c: Coincident(g741,g742)
    c: Coincident(g743,g744)
    c: Coincident(g744,g745)
    c: Coincident(g745,g743)
    c: Coincident(g746,g747)
    c: Coincident(g747,g748)
    c: Coincident(g748,g749)
    c: Coincident(g749,g746)
    c: Coincident(g750,g751)
    c: Coincident(g751,g752)
    c: Coincident(g752,g753)
    c: Coincident(g753,g754)
    c: Coincident(g755,g756)
    c: Coincident(g756,g757)
    c: Coincident(g757,g758)
    c: Coincident(g758,g755)
    c: Coincident(g759,g760)
    c: Coincident(g760,g761)
    c: Coincident(g761,g762)
    c: Coincident(g762,g759)
    c: Coincident(g763,g764)
    c: Coincident(g764,g765)
    c: Coincident(g765,g766)
    c: Coincident(g766,g763)
    c: Coincident(g767,g768)
    c: Coincident(g768,g769)
    c: Coincident(g770,g771)
    c: Coincident(g771,g772)
    c: Coincident(g772,g773)
    c: Coincident(g773,g774)
    c: Coincident(g775,g776)
    c: Coincident(g776,g777)
    c: Coincident(g777,g775)
    c: Coincident(g778,g779)
    c: Coincident(g779,g780)
    c: Coincident(g780,g778)
    c: Coincident(g781,g782)
    c: Coincident(g782,g783)
    c: Coincident(g783,g781)
    c: Coincident(g784,g785)
    c: Coincident(g785,g786)
    c: Coincident(g786,g784)
    c: Coincident(g787,g788)
    c: Coincident(g788,g789)
    c: Coincident(g790,g791)
    c: Coincident(g791,g792)
    c: Coincident(g793,g794)
    c: Coincident(g794,g795)
    c: Coincident(g795,g796)
    c: Coincident(g796,g793)
    c: Coincident(g797,g798)
    c: Coincident(g798,g799)
    c: Coincident(g799,g797)
    c: Coincident(g800,g801)
    c: Coincident(g801,g802)
    c: Coincident(g802,g803)
    c: Coincident(g803,g800)
    c: Coincident(g804,g805)
    c: Coincident(g805,g806)
    c: Coincident(g806,g807)
    c: Coincident(g808,g809)
    c: Coincident(g809,g810)
    c: Coincident(g811,g812)
    c: Coincident(g812,g813)
    c: Coincident(g813,g814)
    c: Coincident(g814,g811)
    c: Coincident(g815,g816)
    c: Coincident(g816,g817)
    c: Coincident(g817,g818)
    c: Coincident(g818,g815)
    c: Coincident(g508,g509)
    c: Coincident(g740,g742)
    c: Coincident(g750,g754)
    c: Coincident(g808,g810)
    c: Coincident(g804,g807)
    c: Coincident(g616,g618)
    c: Coincident(g790,g792)
    c: Coincident(g787,g789)
    c: Coincident(g573,g581)
    c: Coincident(g541,g543)
    c: Coincident(g737,g739)
    c: Coincident(g582,g585)
    c: Coincident(g586,g592)
    c: Coincident(g711,g713)
    c: Coincident(g767,g769)
    c: Coincident(g770,g774)
    c: Coincident(g688,g690)
    c: Coincident(g481,g483)
    c: Coincident(g528,g530)
    c: Coincident(g658,g662)
    c: Coincident(g645,g647)
    c: Coincident(g514,g516)
    c: Coincident(g642,g644)
    c: Coincident(g511,g513)
    c: Coincident(g663,g665)
FEATURE [Sketcher::SketchObject] Sketch032  label="Evil_Twin-Sketch"
  ArcFitTolerance = 1e-06
  FullyConstrained = false
  MakeInternals = false
  Placement = pos=(-15.4043,9.98976,0) rot=(0,0,1;0rad)
  expr: .Placement.Base.x = -(.Shape.BoundBox.XLength / 2)
  expr: .Placement.Base.y = .Shape.BoundBox.YLength / 2
  sketch-geometry (446):
    g0: BSplineCurve PolesCount=4 KnotsCount=2 Degree=3 IsPeriodic=0
    g1: BSplineCurve PolesCount=4 KnotsCount=2 Degree=3 IsPeriodic=0
    g2: BSplineCurve PolesCount=2 KnotsCount=2 Degree=1 IsPeriodic=0
    g3: BSplineCurve PolesCount=2 KnotsCount=2 Degree=1 IsPeriodic=0
    g4: BSplineCurve PolesCount=4 KnotsCount=2 Degree=3 IsPeriodic=0
    g5: BSplineCurve PolesCount=4 KnotsCount=2 Degree=3 IsPeriodic=0
    g6: BSplineCurve PolesCount=4 KnotsCount=2 Degree=3 IsPeriodic=0
    g7: BSplineCurve PolesCount=4 KnotsCount=2 Degree=3 IsPeriodic=0
    g8: BSplineCurve PolesCount=4 KnotsCount=2 Degree=3 IsPeriodic=0
    g9: BSplineCurve PolesCount=2 KnotsCount=2 Degree=1 IsPeriodic=0
    g10: BSplineCurve PolesCount=2 KnotsCount=2 Degree=1 IsPeriodic=0
    g11: BSplineCurve PolesCount=4 KnotsCount=2 Degree=3 IsPeriodic=0
    g12: BSplineCurve PolesCount=4 KnotsCount=2 Degree=3 IsPeriodic=0
    g13: BSplineCurve PolesCount=4 KnotsCount=2 Degree=3 IsPeriodic=0
    g14: BSplineCurve PolesCount=4 KnotsCount=2 Degree=3 IsPeriodic=0
    g15: BSplineCurve PolesCount=4 KnotsCount=2 Degree=3 IsPeriodic=0
    g16: BSplineCurve PolesCount=4 KnotsCount=2 Degree=3 IsPeriodic=0
    g17: BSplineCurve PolesCount=4 KnotsCount=2 Degree=3 IsPeriodic=0
    g18: BSplineCurve PolesCount=4 KnotsCount=2 Degree=3 IsPeriodic=0
    g19: BSplineCurve PolesCount=4 KnotsCount=2 Degree=3 IsPeriodic=0
    g20: BSplineCurve PolesCount=2 KnotsCount=2 Degree=1 IsPeriodic=0
    g21: BSplineCurve PolesCount=2 KnotsCount=2 Degree=1 IsPeriodic=0
    g22: BSplineCurve PolesCount=4 KnotsCount=2 Degree=3 IsPeriodic=0
    g23: BSplineCurve PolesCount=4 KnotsCount=2 Degree=3 IsPeriodic=0
    g24: BSplineCurve PolesCount=2 KnotsCount=2 Degree=1 IsPeriodic=0
    g25: BSplineCurve PolesCount=2 KnotsCount=2 Degree=1 IsPeriodic=0
    g26: BSplineCurve PolesCount=4 KnotsCount=2 Degree=3 IsPeriodic=0
    g27: BSplineCurve PolesCount=4 KnotsCount=2 Degree=3 IsPeriodic=0
    g28: BSplineCurve PolesCount=4 KnotsCount=2 Degree=3 IsPeriodic=0
    g29: BSplineCurve PolesCount=4 KnotsCount=2 Degree=3 IsPeriodic=0
    g30: BSplineCurve PolesCount=4 KnotsCount=2 Degree=3 IsPeriodic=0
    g31: BSplineCurve PolesCount=4 KnotsCount=2 Degree=3 IsPeriodic=0
    g32: BSplineCurve PolesCount=4 KnotsCount=2 Degree=3 IsPeriodic=0
    g33: BSplineCurve PolesCount=4 KnotsCount=2 Degree=3 IsPeriodic=0
    g34: BSplineCurve PolesCount=4 KnotsCount=2 Degree=3 IsPeriodic=0
    g35: BSplineCurve PolesCount=4 KnotsCount=2 Degree=3 IsPeriodic=0
    g36: BSplineCurve PolesCount=4 KnotsCount=2 Degree=3 IsPeriodic=0
    g37: BSplineCurve PolesCount=4 KnotsCount=2 Degree=3 IsPeriodic=0
    g38: BSplineCurve PolesCount=4 KnotsCount=2 Degree=3 IsPeriodic=0
    g39: BSplineCurve PolesCount=4 KnotsCount=2 Degree=3 IsPeriodic=0
    g40: BSplineCurve PolesCount=4 KnotsCount=2 Degree=3 IsPeriodic=0
    g41: BSplineCurve PolesCount=2 KnotsCount=2 Degree=1 IsPeriodic=0
    g42: BSplineCurve PolesCount=2 KnotsCount=2 Degree=1 IsPeriodic=0
    g43: BSplineCurve PolesCount=4 KnotsCount=2 Degree=3 IsPeriodic=0
    g44: BSplineCurve PolesCount=2 KnotsCount=2 Degree=1 IsPeriodic=0
    g45: BSplineCurve PolesCount=2 KnotsCount=2 Degree=1 IsPeriodic=0
    g46: BSplineCurve PolesCount=4 KnotsCount=2 Degree=3 IsPeriodic=0
    g47: BSplineCurve PolesCount=4 KnotsCount=2 Degree=3 IsPeriodic=0
    g48: BSplineCurve PolesCount=4 KnotsCount=2 Degree=3 IsPeriodic=0
    g49: BSplineCurve PolesCount=4 KnotsCount=2 Degree=3 IsPeriodic=0
    g50: BSplineCurve PolesCount=4 KnotsCount=2 Degree=3 IsPeriodic=0
    g51: BSplineCurve PolesCount=4 KnotsCount=2 Degree=3 IsPeriodic=0
    g52: BSplineCurve PolesCount=4 KnotsCount=2 Degree=3 IsPeriodic=0
    g53: BSplineCurve PolesCount=4 KnotsCount=2 Degree=3 IsPeriodic=0
    g54: BSplineCurve PolesCount=4 KnotsCount=2 Degree=3 IsPeriodic=0
    g55: BSplineCurve PolesCount=4 KnotsCount=2 Degree=3 IsPeriodic=0
    g56: BSplineCurve PolesCount=4 KnotsCount=2 Degree=3 IsPeriodic=0
    g57: BSplineCurve PolesCount=4 KnotsCount=2 Degree=3 IsPeriodic=0
    g58: BSplineCurve PolesCount=4 KnotsCount=2 Degree=3 IsPeriodic=0
    g59: BSplineCurve PolesCount=4 KnotsCount=2 Degree=3 IsPeriodic=0
    g60: BSplineCurve PolesCount=4 KnotsCount=2 Degree=3 IsPeriodic=0
    g61: BSplineCurve PolesCount=4 KnotsCount=2 Degree=3 IsPeriodic=0
    g62: BSplineCurve PolesCount=4 KnotsCount=2 Degree=3 IsPeriodic=0
    g63: BSplineCurve PolesCount=4 KnotsCount=2 Degree=3 IsPeriodic=0
    g64: BSplineCurve PolesCount=4 KnotsCount=2 Degree=3 IsPeriodic=0
    g65: BSplineCurve PolesCount=4 KnotsCount=2 Degree=3 IsPeriodic=0
    g66: BSplineCurve PolesCount=4 KnotsCount=2 Degree=3 IsPeriodic=0
    g67: BSplineCurve PolesCount=4 KnotsCount=2 Degree=3 IsPeriodic=0
    g68: BSplineCurve PolesCount=4 KnotsCount=2 Degree=3 IsPeriodic=0
    g69: BSplineCurve PolesCount=4 KnotsCount=2 Degree=3 IsPeriodic=0
    g70: BSplineCurve PolesCount=4 KnotsCount=2 Degree=3 IsPeriodic=0
    g71: BSplineCurve PolesCount=4 KnotsCount=2 Degree=3 IsPeriodic=0
    g72: BSplineCurve PolesCount=4 KnotsCount=2 Degree=3 IsPeriodic=0
    g73: BSplineCurve PolesCount=4 KnotsCount=2 Degree=3 IsPeriodic=0
    g74: BSplineCurve PolesCount=4 KnotsCount=2 Degree=3 IsPeriodic=0
    g75: BSplineCurve PolesCount=4 KnotsCount=2 Degree=3 IsPeriodic=0
    g76: BSplineCurve PolesCount=2 KnotsCount=2 Degree=1 IsPeriodic=0
    g77: BSplineCurve PolesCount=2 KnotsCount=2 Degree=1 IsPeriodic=0
    g78: BSplineCurve PolesCount=4 KnotsCount=2 Degree=3 IsPeriodic=0
    g79: BSplineCurve PolesCount=4 KnotsCount=2 Degree=3 IsPeriodic=0
    g80: BSplineCurve PolesCount=4 KnotsCount=2 Degree=3 IsPeriodic=0
    g81: BSplineCurve PolesCount=2 KnotsCount=2 Degree=1 IsPeriodic=0
    g82: BSplineCurve PolesCount=2 KnotsCount=2 Degree=1 IsPeriodic=0
    g83: BSplineCurve PolesCount=4 KnotsCount=2 Degree=3 IsPeriodic=0
    g84: BSplineCurve PolesCount=4 KnotsCount=2 Degree=3 IsPeriodic=0
    g85: BSplineCurve PolesCount=4 KnotsCount=2 Degree=3 IsPeriodic=0
    g86: BSplineCurve PolesCount=4 KnotsCount=2 Degree=3 IsPeriodic=0
    g87: BSplineCurve PolesCount=4 KnotsCount=2 Degree=3 IsPeriodic=0
    g88: BSplineCurve PolesCount=4 KnotsCount=2 Degree=3 IsPeriodic=0
    g89: BSplineCurve PolesCount=4 KnotsCount=2 Degree=3 IsPeriodic=0
    g90: BSplineCurve PolesCount=4 KnotsCount=2 Degree=3 IsPeriodic=0
    g91: BSplineCurve PolesCount=2 KnotsCount=2 Degree=1 IsPeriodic=0
    g92: BSplineCurve PolesCount=2 KnotsCount=2 Degree=1 IsPeriodic=0
    g93: BSplineCurve PolesCount=2 KnotsCount=2 Degree=1 IsPeriodic=0
    g94: BSplineCurve PolesCount=2 KnotsCount=2 Degree=1 IsPeriodic=0
    g95: BSplineCurve PolesCount=4 KnotsCount=2 Degree=3 IsPeriodic=0
    g96: BSplineCurve PolesCount=4 KnotsCount=2 Degree=3 IsPeriodic=0
    g97: BSplineCurve PolesCount=4 KnotsCount=2 Degree=3 IsPeriodic=0
    g98: BSplineCurve PolesCount=4 KnotsCount=2 Degree=3 IsPeriodic=0
    g99: BSplineCurve PolesCount=4 KnotsCount=2 Degree=3 IsPeriodic=0
    g100: BSplineCurve PolesCount=4 KnotsCount=2 Degree=3 IsPeriodic=0
    g101: BSplineCurve PolesCount=4 KnotsCount=2 Degree=3 IsPeriodic=0
    g102: BSplineCurve PolesCount=4 KnotsCount=2 Degree=3 IsPeriodic=0
    g103: BSplineCurve PolesCount=4 KnotsCount=2 Degree=3 IsPeriodic=0
    g104: BSplineCurve PolesCount=4 KnotsCount=2 Degree=3 IsPeriodic=0
    g105: BSplineCurve PolesCount=4 KnotsCount=2 Degree=3 IsPeriodic=0
    g106: BSplineCurve PolesCount=2 KnotsCount=2 Degree=1 IsPeriodic=0
    g107: BSplineCurve PolesCount=2 KnotsCount=2 Degree=1 IsPeriodic=0
    g108: BSplineCurve PolesCount=4 KnotsCount=2 Degree=3 IsPeriodic=0
    g109: BSplineCurve PolesCount=4 KnotsCount=2 Degree=3 IsPeriodic=0
    g110: BSplineCurve PolesCount=4 KnotsCount=2 Degree=3 IsPeriodic=0
    g111: BSplineCurve PolesCount=2 KnotsCount=2 Degree=1 IsPeriodic=0
    g112: BSplineCurve PolesCount=2 KnotsCount=2 Degree=1 IsPeriodic=0
    g113: BSplineCurve PolesCount=2 KnotsCount=2 Degree=1 IsPeriodic=0
    g114: BSplineCurve PolesCount=2 KnotsCount=2 Degree=1 IsPeriodic=0
    g115: BSplineCurve PolesCount=4 KnotsCount=2 Degree=3 IsPeriodic=0
    g116: BSplineCurve PolesCount=4 KnotsCount=2 Degree=3 IsPeriodic=0
    g117: BSplineCurve PolesCount=4 KnotsCount=2 Degree=3 IsPeriodic=0
    g118: BSplineCurve PolesCount=4 KnotsCount=2 Degree=3 IsPeriodic=0
    g119: BSplineCurve PolesCount=4 KnotsCount=2 Degree=3 IsPeriodic=0
    g120: BSplineCurve PolesCount=4 KnotsCount=2 Degree=3 IsPeriodic=0
    g121: BSplineCurve PolesCount=4 KnotsCount=2 Degree=3 IsPeriodic=0
    g122: BSplineCurve PolesCount=2 KnotsCount=2 Degree=1 IsPeriodic=0
    g123: BSplineCurve PolesCount=2 KnotsCount=2 Degree=1 IsPeriodic=0
    g124: BSplineCurve PolesCount=4 KnotsCount=2 Degree=3 IsPeriodic=0
    g125: BSplineCurve PolesCount=4 KnotsCount=2 Degree=3 IsPeriodic=0
    g126: BSplineCurve PolesCount=4 KnotsCount=2 Degree=3 IsPeriodic=0
    g127: BSplineCurve PolesCount=4 KnotsCount=2 Degree=3 IsPeriodic=0
    g128: BSplineCurve PolesCount=4 KnotsCount=2 Degree=3 IsPeriodic=0
    g129: BSplineCurve PolesCount=4 KnotsCount=2 Degree=3 IsPeriodic=0
    g130: BSplineCurve PolesCount=4 KnotsCount=2 Degree=3 IsPeriodic=0
    g131: BSplineCurve PolesCount=2 KnotsCount=2 Degree=1 IsPeriodic=0
    g132: BSplineCurve PolesCount=2 KnotsCount=2 Degree=1 IsPeriodic=0
    g133: BSplineCurve PolesCount=4 KnotsCount=2 Degree=3 IsPeriodic=0
    g134: BSplineCurve PolesCount=4 KnotsCount=2 Degree=3 IsPeriodic=0
    g135: BSplineCurve PolesCount=4 KnotsCount=2 Degree=3 IsPeriodic=0
    g136: BSplineCurve PolesCount=4 KnotsCount=2 Degree=3 IsPeriodic=0
    g137: BSplineCurve PolesCount=4 KnotsCount=2 Degree=3 IsPeriodic=0
    g138: BSplineCurve PolesCount=4 KnotsCount=2 Degree=3 IsPeriodic=0
    g139: BSplineCurve PolesCount=4 KnotsCount=2 Degree=3 IsPeriodic=0
    g140: BSplineCurve PolesCount=2 KnotsCount=2 Degree=1 IsPeriodic=0
    g141: BSplineCurve PolesCount=2 KnotsCount=2 Degree=1 IsPeriodic=0
    g142: BSplineCurve PolesCount=2 KnotsCount=2 Degree=1 IsPeriodic=0
    g143: BSplineCurve PolesCount=2 KnotsCount=2 Degree=1 IsPeriodic=0
    g144: BSplineCurve PolesCount=4 KnotsCount=2 Degree=3 IsPeriodic=0
    g145: BSplineCurve PolesCount=4 KnotsCount=2 Degree=3 IsPeriodic=0
    g146: BSplineCurve PolesCount=4 KnotsCount=2 Degree=3 IsPeriodic=0
    g147: BSplineCurve PolesCount=4 KnotsCount=2 Degree=3 IsPeriodic=0
    g148: BSplineCurve PolesCount=4 KnotsCount=2 Degree=3 IsPeriodic=0
    g149: BSplineCurve PolesCount=4 KnotsCount=2 Degree=3 IsPeriodic=0
    g150: BSplineCurve PolesCount=4 KnotsCount=2 Degree=3 IsPeriodic=0
    g151: BSplineCurve PolesCount=4 KnotsCount=2 Degree=3 IsPeriodic=0
    g152: BSplineCurve PolesCount=4 KnotsCount=2 Degree=3 IsPeriodic=0
    g153: BSplineCurve PolesCount=4 KnotsCount=2 Degree=3 IsPeriodic=0
    g154: BSplineCurve PolesCount=4 KnotsCount=2 Degree=3 IsPeriodic=0
    g155: BSplineCurve PolesCount=2 KnotsCount=2 Degree=1 IsPeriodic=0
    g156: BSplineCurve PolesCount=2 KnotsCount=2 Degree=1 IsPeriodic=0
    g157: BSplineCurve PolesCount=4 KnotsCount=2 Degree=3 IsPeriodic=0
    g158: BSplineCurve PolesCount=4 KnotsCount=2 Degree=3 IsPeriodic=0
    g159: BSplineCurve PolesCount=4 KnotsCount=2 Degree=3 IsPeriodic=0
    g160: BSplineCurve PolesCount=4 KnotsCount=2 Degree=3 IsPeriodic=0
    g161: BSplineCurve PolesCount=4 KnotsCount=2 Degree=3 IsPeriodic=0
    g162: BSplineCurve PolesCount=4 KnotsCount=2 Degree=3 IsPeriodic=0
    g163: BSplineCurve PolesCount=4 KnotsCount=2 Degree=3 IsPeriodic=0
    g164: BSplineCurve PolesCount=4 KnotsCount=2 Degree=3 IsPeriodic=0
    g165: BSplineCurve PolesCount=4 KnotsCount=2 Degree=3 IsPeriodic=0
    g166: BSplineCurve PolesCount=4 KnotsCount=2 Degree=3 IsPeriodic=0
    g167: BSplineCurve PolesCount=4 KnotsCount=2 Degree=3 IsPeriodic=0
    g168: BSplineCurve PolesCount=4 KnotsCount=2 Degree=3 IsPeriodic=0
    g169: BSplineCurve PolesCount=4 KnotsCount=2 Degree=3 IsPeriodic=0
    g170: BSplineCurve PolesCount=4 KnotsCount=2 Degree=3 IsPeriodic=0
    g171: BSplineCurve PolesCount=4 KnotsCount=2 Degree=3 IsPeriodic=0
    g172: BSplineCurve PolesCount=4 KnotsCount=2 Degree=3 IsPeriodic=0
    g173: BSplineCurve PolesCount=4 KnotsCount=2 Degree=3 IsPeriodic=0
    g174: BSplineCurve PolesCount=4 KnotsCount=2 Degree=3 IsPeriodic=0
    g175: BSplineCurve PolesCount=4 KnotsCount=2 Degree=3 IsPeriodic=0
    g176: BSplineCurve PolesCount=4 KnotsCount=2 Degree=3 IsPeriodic=0
    g177: BSplineCurve PolesCount=2 KnotsCount=2 Degree=1 IsPeriodic=0
    g178: BSplineCurve PolesCount=2 KnotsCount=2 Degree=1 IsPeriodic=0
    g179: BSplineCurve PolesCount=4 KnotsCount=2 Degree=3 IsPeriodic=0
    g180: BSplineCurve PolesCount=2 KnotsCount=2 Degree=1 IsPeriodic=0
    g181: BSplineCurve PolesCount=2 KnotsCount=2 Degree=1 IsPeriodic=0
    g182: BSplineCurve PolesCount=4 KnotsCount=2 Degree=3 IsPeriodic=0
    g183: BSplineCurve PolesCount=4 KnotsCount=2 Degree=3 IsPeriodic=0
    g184: BSplineCurve PolesCount=2 KnotsCount=2 Degree=1 IsPeriodic=0
    g185: BSplineCurve PolesCount=2 KnotsCount=2 Degree=1 IsPeriodic=0
    g186: BSplineCurve PolesCount=4 KnotsCount=2 Degree=3 IsPeriodic=0
    g187: BSplineCurve PolesCount=2 KnotsCount=2 Degree=1 IsPeriodic=0
    g188: BSplineCurve PolesCount=2 KnotsCount=2 Degree=1 IsPeriodic=0
    g189: BSplineCurve PolesCount=4 KnotsCount=2 Degree=3 IsPeriodic=0
    g190: BSplineCurve PolesCount=4 KnotsCount=2 Degree=3 IsPeriodic=0
    g191: BSplineCurve PolesCount=4 KnotsCount=2 Degree=3 IsPeriodic=0
    g192: BSplineCurve PolesCount=4 KnotsCount=2 Degree=3 IsPeriodic=0
    g193: BSplineCurve PolesCount=4 KnotsCount=2 Degree=3 IsPeriodic=0
    g194: BSplineCurve PolesCount=4 KnotsCount=2 Degree=3 IsPeriodic=0
    g195: BSplineCurve PolesCount=4 KnotsCount=2 Degree=3 IsPeriodic=0
    g196: BSplineCurve PolesCount=4 KnotsCount=2 Degree=3 IsPeriodic=0
    g197: BSplineCurve PolesCount=4 KnotsCount=2 Degree=3 IsPeriodic=0
    g198: BSplineCurve PolesCount=4 KnotsCount=2 Degree=3 IsPeriodic=0
    g199: BSplineCurve PolesCount=4 KnotsCount=2 Degree=3 IsPeriodic=0
    g200: BSplineCurve PolesCount=4 KnotsCount=2 Degree=3 IsPeriodic=0
    g201: BSplineCurve PolesCount=4 KnotsCount=2 Degree=3 IsPeriodic=0
    g202: BSplineCurve PolesCount=4 KnotsCount=2 Degree=3 IsPeriodic=0
    g203: BSplineCurve PolesCount=4 KnotsCount=2 Degree=3 IsPeriodic=0
    g204: BSplineCurve PolesCount=4 KnotsCount=2 Degree=3 IsPeriodic=0
    g205: BSplineCurve PolesCount=4 KnotsCount=2 Degree=3 IsPeriodic=0
    g206: BSplineCurve PolesCount=4 KnotsCount=2 Degree=3 IsPeriodic=0
    g207: BSplineCurve PolesCount=2 KnotsCount=2 Degree=1 IsPeriodic=0
    g208: BSplineCurve PolesCount=2 KnotsCount=2 Degree=1 IsPeriodic=0
    g209: BSplineCurve PolesCount=4 KnotsCount=2 Degree=3 IsPeriodic=0
    g210: BSplineCurve PolesCount=4 KnotsCount=2 Degree=3 IsPeriodic=0
    g211: BSplineCurve PolesCount=4 KnotsCount=2 Degree=3 IsPeriodic=0
    g212: BSplineCurve PolesCount=4 KnotsCount=2 Degree=3 IsPeriodic=0
    g213: BSplineCurve PolesCount=4 KnotsCount=2 Degree=3 IsPeriodic=0
    g214: BSplineCurve PolesCount=4 KnotsCount=2 Degree=3 IsPeriodic=0
    g215: BSplineCurve PolesCount=4 KnotsCount=2 Degree=3 IsPeriodic=0
    g216: BSplineCurve PolesCount=2 KnotsCount=2 Degree=1 IsPeriodic=0
    g217: BSplineCurve PolesCount=4 KnotsCount=2 Degree=3 IsPeriodic=0
    g218: BSplineCurve PolesCount=2 KnotsCount=2 Degree=1 IsPeriodic=0
    g219: BSplineCurve PolesCount=2 KnotsCount=2 Degree=1 IsPeriodic=0
    g220: BSplineCurve PolesCount=4 KnotsCount=2 Degree=3 IsPeriodic=0
    g221: BSplineCurve PolesCount=4 KnotsCount=2 Degree=3 IsPeriodic=0
    g222: BSplineCurve PolesCount=4 KnotsCount=2 Degree=3 IsPeriodic=0
    g223: BSplineCurve PolesCount=4 KnotsCount=2 Degree=3 IsPeriodic=0
    g224: BSplineCurve PolesCount=4 KnotsCount=2 Degree=3 IsPeriodic=0
    g225: BSplineCurve PolesCount=4 KnotsCount=2 Degree=3 IsPeriodic=0
    g226: BSplineCurve PolesCount=4 KnotsCount=2 Degree=3 IsPeriodic=0
    g227: BSplineCurve PolesCount=4 KnotsCount=2 Degree=3 IsPeriodic=0
    g228: BSplineCurve PolesCount=4 KnotsCount=2 Degree=3 IsPeriodic=0
    g229: BSplineCurve PolesCount=4 KnotsCount=2 Degree=3 IsPeriodic=0
    g230: BSplineCurve PolesCount=4 KnotsCount=2 Degree=3 IsPeriodic=0
    g231: BSplineCurve PolesCount=4 KnotsCount=2 Degree=3 IsPeriodic=0
    g232: BSplineCurve PolesCount=4 KnotsCount=2 Degree=3 IsPeriodic=0
    g233: BSplineCurve PolesCount=4 KnotsCount=2 Degree=3 IsPeriodic=0
    g234: BSplineCurve PolesCount=4 KnotsCount=2 Degree=3 IsPeriodic=0
    g235: BSplineCurve PolesCount=4 KnotsCount=2 Degree=3 IsPeriodic=0
    g236: BSplineCurve PolesCount=4 KnotsCount=2 Degree=3 IsPeriodic=0
    g237: BSplineCurve PolesCount=4 KnotsCount=2 Degree=3 IsPeriodic=0
    g238: BSplineCurve PolesCount=4 KnotsCount=2 Degree=3 IsPeriodic=0
    g239: BSplineCurve PolesCount=4 KnotsCount=2 Degree=3 IsPeriodic=0
    g240: BSplineCurve PolesCount=4 KnotsCount=2 Degree=3 IsPeriodic=0
    g241: BSplineCurve PolesCount=4 KnotsCount=2 Degree=3 IsPeriodic=0
    g242: BSplineCurve PolesCount=4 KnotsCount=2 Degree=3 IsPeriodic=0
    g243: BSplineCurve PolesCount=4 KnotsCount=2 Degree=3 IsPeriodic=0
    g244: BSplineCurve PolesCount=4 KnotsCount=2 Degree=3 IsPeriodic=0
    g245: BSplineCurve PolesCount=4 KnotsCount=2 Degree=3 IsPeriodic=0
    g246: BSplineCurve PolesCount=4 KnotsCount=2 Degree=3 IsPeriodic=0
    g247: BSplineCurve PolesCount=4 KnotsCount=2 Degree=3 IsPeriodic=0
    g248: BSplineCurve PolesCount=2 KnotsCount=2 Degree=1 IsPeriodic=0
    g249: BSplineCurve PolesCount=2 KnotsCount=2 Degree=1 IsPeriodic=0
    g250: BSplineCurve PolesCount=4 KnotsCount=2 Degree=3 IsPeriodic=0
    g251: BSplineCurve PolesCount=4 KnotsCount=2 Degree=3 IsPeriodic=0
    g252: BSplineCurve PolesCount=4 KnotsCount=2 Degree=3 IsPeriodic=0
    g253: BSplineCurve PolesCount=4 KnotsCount=2 Degree=3 IsPeriodic=0
    g254: BSplineCurve PolesCount=4 KnotsCount=2 Degree=3 IsPeriodic=0
    g255: BSplineCurve PolesCount=4 KnotsCount=2 Degree=3 IsPeriodic=0
    g256: BSplineCurve PolesCount=4 KnotsCount=2 Degree=3 IsPeriodic=0
    g257: BSplineCurve PolesCount=4 KnotsCount=2 Degree=3 IsPeriodic=0
    g258: BSplineCurve PolesCount=4 KnotsCount=2 Degree=3 IsPeriodic=0
    g259: BSplineCurve PolesCount=4 KnotsCount=2 Degree=3 IsPeriodic=0
    g260: BSplineCurve PolesCount=4 KnotsCount=2 Degree=3 IsPeriodic=0
    g261: BSplineCurve PolesCount=4 KnotsCount=2 Degree=3 IsPeriodic=0
    g262: BSplineCurve PolesCount=4 KnotsCount=2 Degree=3 IsPeriodic=0
    g263: BSplineCurve PolesCount=4 KnotsCount=2 Degree=3 IsPeriodic=0
    g264: BSplineCurve PolesCount=4 KnotsCount=2 Degree=3 IsPeriodic=0
    g265: BSplineCurve PolesCount=4 KnotsCount=2 Degree=3 IsPeriodic=0
    g266: BSplineCurve PolesCount=4 KnotsCount=2 Degree=3 IsPeriodic=0
    g267: BSplineCurve PolesCount=4 KnotsCount=2 Degree=3 IsPeriodic=0
    g268: BSplineCurve PolesCount=4 KnotsCount=2 Degree=3 IsPeriodic=0
    g269: BSplineCurve PolesCount=4 KnotsCount=2 Degree=3 IsPeriodic=0
    g270: BSplineCurve PolesCount=4 KnotsCount=2 Degree=3 IsPeriodic=0
    g271: BSplineCurve PolesCount=4 KnotsCount=2 Degree=3 IsPeriodic=0
    g272: BSplineCurve PolesCount=4 KnotsCount=2 Degree=3 IsPeriodic=0
    g273: BSplineCurve PolesCount=4 KnotsCount=2 Degree=3 IsPeriodic=0
    g274: BSplineCurve PolesCount=4 KnotsCount=2 Degree=3 IsPeriodic=0
    g275: BSplineCurve PolesCount=2 KnotsCount=2 Degree=1 IsPeriodic=0
    g276: BSplineCurve PolesCount=4 KnotsCount=2 Degree=3 IsPeriodic=0
    g277: BSplineCurve PolesCount=4 KnotsCount=2 Degree=3 IsPeriodic=0
    g278: BSplineCurve PolesCount=4 KnotsCount=2 Degree=3 IsPeriodic=0
    g279: BSplineCurve PolesCount=4 KnotsCount=2 Degree=3 IsPeriodic=0
    g280: BSplineCurve PolesCount=4 KnotsCount=2 Degree=3 IsPeriodic=0
    g281: BSplineCurve PolesCount=4 KnotsCount=2 Degree=3 IsPeriodic=0
    g282: BSplineCurve PolesCount=4 KnotsCount=2 Degree=3 IsPeriodic=0
    g283: BSplineCurve PolesCount=4 KnotsCount=2 Degree=3 IsPeriodic=0
    g284: BSplineCurve PolesCount=4 KnotsCount=2 Degree=3 IsPeriodic=0
    g285: BSplineCurve PolesCount=4 KnotsCount=2 Degree=3 IsPeriodic=0
    g286: BSplineCurve PolesCount=2 KnotsCount=2 Degree=1 IsPeriodic=0
    g287: BSplineCurve PolesCount=2 KnotsCount=2 Degree=1 IsPeriodic=0
    g288: BSplineCurve PolesCount=4 KnotsCount=2 Degree=3 IsPeriodic=0
    g289: BSplineCurve PolesCount=4 KnotsCount=2 Degree=3 IsPeriodic=0
    g290: BSplineCurve PolesCount=2 KnotsCount=2 Degree=1 IsPeriodic=0
    g291: BSplineCurve PolesCount=2 KnotsCount=2 Degree=1 IsPeriodic=0
    g292: BSplineCurve PolesCount=4 KnotsCount=2 Degree=3 IsPeriodic=0
    g293: BSplineCurve PolesCount=2 KnotsCount=2 Degree=1 IsPeriodic=0
    g294: BSplineCurve PolesCount=2 KnotsCount=2 Degree=1 IsPeriodic=0
    g295: BSplineCurve PolesCount=4 KnotsCount=2 Degree=3 IsPeriodic=0
    g296: BSplineCurve PolesCount=2 KnotsCount=2 Degree=1 IsPeriodic=0
    g297: BSplineCurve PolesCount=2 KnotsCount=2 Degree=1 IsPeriodic=0
    g298: BSplineCurve PolesCount=4 KnotsCount=2 Degree=3 IsPeriodic=0
    g299: BSplineCurve PolesCount=4 KnotsCount=2 Degree=3 IsPeriodic=0
    g300: BSplineCurve PolesCount=4 KnotsCount=2 Degree=3 IsPeriodic=0
    g301: BSplineCurve PolesCount=4 KnotsCount=2 Degree=3 IsPeriodic=0
    g302: BSplineCurve PolesCount=4 KnotsCount=2 Degree=3 IsPeriodic=0
    g303: BSplineCurve PolesCount=4 KnotsCount=2 Degree=3 IsPeriodic=0
    g304: BSplineCurve PolesCount=4 KnotsCount=2 Degree=3 IsPeriodic=0
    g305: BSplineCurve PolesCount=4 KnotsCount=2 Degree=3 IsPeriodic=0
    g306: BSplineCurve PolesCount=4 KnotsCount=2 Degree=3 IsPeriodic=0
    g307: BSplineCurve PolesCount=4 KnotsCount=2 Degree=3 IsPeriodic=0
    g308: BSplineCurve PolesCount=4 KnotsCount=2 Degree=3 IsPeriodic=0
    g309: BSplineCurve PolesCount=4 KnotsCount=2 Degree=3 IsPeriodic=0
    g310: BSplineCurve PolesCount=4 KnotsCount=2 Degree=3 IsPeriodic=0
    g311: BSplineCurve PolesCount=4 KnotsCount=2 Degree=3 IsPeriodic=0
    g312: BSplineCurve PolesCount=4 KnotsCount=2 Degree=3 IsPeriodic=0
    g313: BSplineCurve PolesCount=4 KnotsCount=2 Degree=3 IsPeriodic=0
    g314: BSplineCurve PolesCount=2 KnotsCount=2 Degree=1 IsPeriodic=0
    g315: BSplineCurve PolesCount=2 KnotsCount=2 Degree=1 IsPeriodic=0
    g316: BSplineCurve PolesCount=4 KnotsCount=2 Degree=3 IsPeriodic=0
    g317: BSplineCurve PolesCount=4 KnotsCount=2 Degree=3 IsPeriodic=0
    g318: BSplineCurve PolesCount=4 KnotsCount=2 Degree=3 IsPeriodic=0
    g319: BSplineCurve PolesCount=4 KnotsCount=2 Degree=3 IsPeriodic=0
    g320: BSplineCurve PolesCount=4 KnotsCount=2 Degree=3 IsPeriodic=0
    g321: BSplineCurve PolesCount=4 KnotsCount=2 Degree=3 IsPeriodic=0
    g322: BSplineCurve PolesCount=2 KnotsCount=2 Degree=1 IsPeriodic=0
    g323: BSplineCurve PolesCount=4 KnotsCount=2 Degree=3 IsPeriodic=0
    g324: BSplineCurve PolesCount=4 KnotsCount=2 Degree=3 IsPeriodic=0
    g325: BSplineCurve PolesCount=4 KnotsCount=2 Degree=3 IsPeriodic=0
    g326: BSplineCurve PolesCount=4 KnotsCount=2 Degree=3 IsPeriodic=0
    g327: BSplineCurve PolesCount=4 KnotsCount=2 Degree=3 IsPeriodic=0
    g328: BSplineCurve PolesCount=4 KnotsCount=2 Degree=3 IsPeriodic=0
    g329: BSplineCurve PolesCount=4 KnotsCount=2 Degree=3 IsPeriodic=0
    g330: BSplineCurve PolesCount=4 KnotsCount=2 Degree=3 IsPeriodic=0
    g331: BSplineCurve PolesCount=4 KnotsCount=2 Degree=3 IsPeriodic=0
    g332: BSplineCurve PolesCount=4 KnotsCount=2 Degree=3 IsPeriodic=0
    g333: BSplineCurve PolesCount=4 KnotsCount=2 Degree=3 IsPeriodic=0
    g334: BSplineCurve PolesCount=4 KnotsCount=2 Degree=3 IsPeriodic=0
    g335: BSplineCurve PolesCount=4 KnotsCount=2 Degree=3 IsPeriodic=0
    g336: BSplineCurve PolesCount=4 KnotsCount=2 Degree=3 IsPeriodic=0
    g337: BSplineCurve PolesCount=4 KnotsCount=2 Degree=3 IsPeriodic=0
    g338: BSplineCurve PolesCount=4 KnotsCount=2 Degree=3 IsPeriodic=0
    g339: BSplineCurve PolesCount=4 KnotsCount=2 Degree=3 IsPeriodic=0
    g340: BSplineCurve PolesCount=4 KnotsCount=2 Degree=3 IsPeriodic=0
    g341: BSplineCurve PolesCount=4 KnotsCount=2 Degree=3 IsPeriodic=0
    g342: BSplineCurve PolesCount=4 KnotsCount=2 Degree=3 IsPeriodic=0
    g343: BSplineCurve PolesCount=4 KnotsCount=2 Degree=3 IsPeriodic=0
    g344: BSplineCurve PolesCount=4 KnotsCount=2 Degree=3 IsPeriodic=0
    g345: BSplineCurve PolesCount=2 KnotsCount=2 Degree=1 IsPeriodic=0
    g346: BSplineCurve PolesCount=4 KnotsCount=2 Degree=3 IsPeriodic=0
    g347: BSplineCurve PolesCount=4 KnotsCount=2 Degree=3 IsPeriodic=0
    g348: BSplineCurve PolesCount=4 KnotsCount=2 Degree=3 IsPeriodic=0
    g349: BSplineCurve PolesCount=4 KnotsCount=2 Degree=3 IsPeriodic=0
    g350: BSplineCurve PolesCount=4 KnotsCount=2 Degree=3 IsPeriodic=0
    g351: BSplineCurve PolesCount=2 KnotsCount=2 Degree=1 IsPeriodic=0
    g352: BSplineCurve PolesCount=2 KnotsCount=2 Degree=1 IsPeriodic=0
    g353: BSplineCurve PolesCount=4 KnotsCount=2 Degree=3 IsPeriodic=0
    g354: BSplineCurve PolesCount=4 KnotsCount=2 Degree=3 IsPeriodic=0
    g355: BSplineCurve PolesCount=4 KnotsCount=2 Degree=3 IsPeriodic=0
    g356: BSplineCurve PolesCount=4 KnotsCount=2 Degree=3 IsPeriodic=0
    g357: BSplineCurve PolesCount=4 KnotsCount=2 Degree=3 IsPeriodic=0
    g358: BSplineCurve PolesCount=4 KnotsCount=2 Degree=3 IsPeriodic=0
    g359: BSplineCurve PolesCount=4 KnotsCount=2 Degree=3 IsPeriodic=0
    g360: BSplineCurve PolesCount=4 KnotsCount=2 Degree=3 IsPeriodic=0
    g361: BSplineCurve PolesCount=2 KnotsCount=2 Degree=1 IsPeriodic=0
    g362: BSplineCurve PolesCount=4 KnotsCount=2 Degree=3 IsPeriodic=0
    g363: BSplineCurve PolesCount=2 KnotsCount=2 Degree=1 IsPeriodic=0
    g364: BSplineCurve PolesCount=2 KnotsCount=2 Degree=1 IsPeriodic=0
    g365: BSplineCurve PolesCount=2 KnotsCount=2 Degree=1 IsPeriodic=0
    g366: BSplineCurve PolesCount=4 KnotsCount=2 Degree=3 IsPeriodic=0
    g367: BSplineCurve PolesCount=4 KnotsCount=2 Degree=3 IsPeriodic=0
    g368: BSplineCurve PolesCount=4 KnotsCount=2 Degree=3 IsPeriodic=0
    g369: BSplineCurve PolesCount=4 KnotsCount=2 Degree=3 IsPeriodic=0
    g370: BSplineCurve PolesCount=4 KnotsCount=2 Degree=3 IsPeriodic=0
    g371: BSplineCurve PolesCount=4 KnotsCount=2 Degree=3 IsPeriodic=0
    g372: BSplineCurve PolesCount=4 KnotsCount=2 Degree=3 IsPeriodic=0
    g373: BSplineCurve PolesCount=4 KnotsCount=2 Degree=3 IsPeriodic=0
    g374: BSplineCurve PolesCount=4 KnotsCount=2 Degree=3 IsPeriodic=0
    g375: BSplineCurve PolesCount=4 KnotsCount=2 Degree=3 IsPeriodic=0
    g376: BSplineCurve PolesCount=2 KnotsCount=2 Degree=1 IsPeriodic=0
    g377: BSplineCurve PolesCount=2 KnotsCount=2 Degree=1 IsPeriodic=0
    g378: BSplineCurve PolesCount=4 KnotsCount=2 Degree=3 IsPeriodic=0
    g379: BSplineCurve PolesCount=4 KnotsCount=2 Degree=3 IsPeriodic=0
    g380: BSplineCurve PolesCount=4 KnotsCount=2 Degree=3 IsPeriodic=0
    g381: BSplineCurve PolesCount=4 KnotsCount=2 Degree=3 IsPeriodic=0
    g382: BSplineCurve PolesCount=4 KnotsCount=2 Degree=3 IsPeriodic=0
    g383: BSplineCurve PolesCount=4 KnotsCount=2 Degree=3 IsPeriodic=0
    g384: BSplineCurve PolesCount=4 KnotsCount=2 Degree=3 IsPeriodic=0
    g385: BSplineCurve PolesCount=4 KnotsCount=2 Degree=3 IsPeriodic=0
    g386: BSplineCurve PolesCount=4 KnotsCount=2 Degree=3 IsPeriodic=0
    g387: BSplineCurve PolesCount=4 KnotsCount=2 Degree=3 IsPeriodic=0
    g388: BSplineCurve PolesCount=4 KnotsCount=2 Degree=3 IsPeriodic=0
    g389: BSplineCurve PolesCount=4 KnotsCount=2 Degree=3 IsPeriodic=0
    g390: BSplineCurve PolesCount=4 KnotsCount=2 Degree=3 IsPeriodic=0
    g391: BSplineCurve PolesCount=4 KnotsCount=2 Degree=3 IsPeriodic=0
    g392: BSplineCurve PolesCount=4 KnotsCount=2 Degree=3 IsPeriodic=0
    g393: BSplineCurve PolesCount=4 KnotsCount=2 Degree=3 IsPeriodic=0
    g394: BSplineCurve PolesCount=4 KnotsCount=2 Degree=3 IsPeriodic=0
    g395: BSplineCurve PolesCount=4 KnotsCount=2 Degree=3 IsPeriodic=0
    g396: BSplineCurve PolesCount=4 KnotsCount=2 Degree=3 IsPeriodic=0
    g397: BSplineCurve PolesCount=4 KnotsCount=2 Degree=3 IsPeriodic=0
    g398: BSplineCurve PolesCount=4 KnotsCount=2 Degree=3 IsPeriodic=0
    g399: BSplineCurve PolesCount=4 KnotsCount=2 Degree=3 IsPeriodic=0
    ... +46 more geometry lines
  constraints (453):
    c: Coincident(g0,g1)
    c: Coincident(g1,g2)
    c: Coincident(g2,g3)
    c: Coincident(g3,g4)
    c: Coincident(g4,g5)
    c: Coincident(g5,g6)
    c: Coincident(g6,g7)
    c: Coincident(g7,g8)
    c: Coincident(g8,g9)
    c: Coincident(g9,g10)
    c: Coincident(g10,g11)
    c: Coincident(g11,g12)
    c: Coincident(g12,g13)
    c: Coincident(g13,g14)
    c: Coincident(g14,g15)
    c: Coincident(g15,g16)
    c: Coincident(g16,g17)
    c: Coincident(g17,g18)
    c: Coincident(g18,g19)
    c: Coincident(g19,g20)
    c: Coincident(g20,g21)
    c: Coincident(g21,g22)
    c: Coincident(g22,g23)
    c: Coincident(g23,g24)
    c: Coincident(g24,g25)
    c: Coincident(g25,g26)
    c: Coincident(g26,g27)
    c: Coincident(g27,g28)
    c: Coincident(g28,g29)
    c: Coincident(g29,g30)
    c: Coincident(g30,g31)
    c: Coincident(g31,g32)
    c: Coincident(g32,g33)
    c: Coincident(g33,g34)
    c: Coincident(g34,g35)
    c: Coincident(g35,g36)
    c: Coincident(g36,g37)
    c: Coincident(g37,g38)
    c: Coincident(g38,g39)
    c: Coincident(g39,g40)
    c: Coincident(g40,g41)
    c: Coincident(g41,g42)
    c: Coincident(g42,g43)
    c: Coincident(g43,g44)
    c: Coincident(g44,g45)
    c: Coincident(g45,g46)
    c: Coincident(g46,g47)
    c: Coincident(g47,g48)
    c: Coincident(g48,g49)
    c: Coincident(g49,g50)
    c: Coincident(g50,g51)
    c: Coincident(g51,g52)
    c: Coincident(g52,g53)
    c: Coincident(g53,g54)
    c: Coincident(g54,g55)
    c: Coincident(g55,g56)
    c: Coincident(g56,g57)
    c: Coincident(g57,g58)
    c: Coincident(g58,g59)
    c: Coincident(g59,g60)
    c: Coincident(g60,g61)
    c: Coincident(g61,g62)
    c: Coincident(g62,g63)
    c: Coincident(g63,g64)
    c: Coincident(g64,g65)
    c: Coincident(g65,g66)
    c: Coincident(g66,g67)
    c: Coincident(g67,g68)
    c: Coincident(g68,g69)
    c: Coincident(g69,g70)
    c: Coincident(g70,g71)
    c: Coincident(g71,g72)
    c: Coincident(g72,g73)
    c: Coincident(g73,g74)
    c: Coincident(g74,g75)
    c: Coincident(g75,g76)
    c: Coincident(g76,g77)
    c: Coincident(g77,g78)
    c: Coincident(g78,g79)
    c: Coincident(g79,g80)
    c: Coincident(g80,g81)
    c: Coincident(g81,g82)
    c: Coincident(g82,g83)
    c: Coincident(g83,g84)
    c: Coincident(g84,g85)
    c: Coincident(g85,g86)
    c: Coincident(g86,g87)
    c: Coincident(g87,g88)
    c: Coincident(g88,g89)
    c: Coincident(g89,g90)
    c: Coincident(g90,g91)
    c: Coincident(g91,g92)
    c: Coincident(g92,g93)
    c: Coincident(g93,g94)
    c: Coincident(g94,g95)
    c: Coincident(g95,g96)
    c: Coincident(g96,g97)
    c: Coincident(g97,g98)
    c: Coincident(g98,g99)
    c: Coincident(g99,g100)
    c: Coincident(g100,g101)
    c: Coincident(g101,g102)
    c: Coincident(g102,g103)
    c: Coincident(g103,g104)
    c: Coincident(g104,g105)
    c: Coincident(g105,g106)
    c: Coincident(g106,g107)
    c: Coincident(g107,g108)
    c: Coincident(g108,g109)
    c: Coincident(g109,g110)
    c: Coincident(g110,g111)
    c: Coincident(g111,g112)
    c: Coincident(g112,g113)
    c: Coincident(g113,g114)
    c: Coincident(g114,g115)
    c: Coincident(g115,g116)
    c: Coincident(g116,g117)
    c: Coincident(g117,g118)
    c: Coincident(g118,g119)
    c: Coincident(g119,g120)
    c: Coincident(g120,g121)
    c: Coincident(g121,g122)
    c: Coincident(g122,g123)
    c: Coincident(g123,g124)
    c: Coincident(g124,g125)
    c: Coincident(g125,g126)
    c: Coincident(g126,g127)
    c: Coincident(g127,g128)
    c: Coincident(g128,g129)
    c: Coincident(g129,g130)
    c: Coincident(g130,g131)
    c: Coincident(g131,g132)
    c: Coincident(g132,g133)
    c: Coincident(g133,g134)
    c: Coincident(g134,g135)
    c: Coincident(g135,g136)
    c: Coincident(g136,g137)
    c: Coincident(g137,g138)
    c: Coincident(g138,g139)
    c: Coincident(g139,g140)
    c: Coincident(g140,g141)
    c: Coincident(g141,g142)
    c: Coincident(g142,g143)
    c: Coincident(g143,g144)
    c: Coincident(g144,g145)
    c: Coincident(g145,g146)
    c: Coincident(g146,g147)
    c: Coincident(g147,g148)
    c: Coincident(g148,g149)
    c: Coincident(g149,g150)
    c: Coincident(g150,g151)
    c: Coincident(g151,g152)
    c: Coincident(g152,g153)
    c: Coincident(g153,g154)
    c: Coincident(g154,g155)
    c: Coincident(g155,g156)
    c: Coincident(g156,g157)
    c: Coincident(g157,g158)
    c: Coincident(g158,g159)
    c: Coincident(g159,g160)
    c: Coincident(g160,g161)
    c: Coincident(g161,g162)
    c: Coincident(g162,g163)
    c: Coincident(g163,g164)
    c: Coincident(g164,g165)
    c: Coincident(g165,g166)
    c: Coincident(g166,g167)
    c: Coincident(g167,g168)
    c: Coincident(g168,g169)
    c: Coincident(g169,g170)
    c: Coincident(g170,g171)
    c: Coincident(g171,g172)
    c: Coincident(g172,g173)
    c: Coincident(g173,g174)
    c: Coincident(g174,g175)
    c: Coincident(g175,g176)
    c: Coincident(g176,g177)
    c: Coincident(g177,g178)
    c: Coincident(g178,g179)
    c: Coincident(g179,g180)
    c: Coincident(g180,g181)
    c: Coincident(g181,g182)
    c: Coincident(g182,g183)
    c: Coincident(g183,g184)
    c: Coincident(g184,g185)
    c: Coincident(g185,g186)
    c: Coincident(g186,g187)
    c: Coincident(g187,g188)
    c: Coincident(g188,g189)
    c: Coincident(g189,g190)
    c: Coincident(g190,g191)
    c: Coincident(g191,g192)
    c: Coincident(g192,g193)
    c: Coincident(g193,g194)
    c: Coincident(g194,g195)
    c: Coincident(g195,g196)
    c: Coincident(g196,g197)
    c: Coincident(g197,g198)
    c: Coincident(g198,g199)
    c: Coincident(g199,g200)
    c: Coincident(g200,g201)
    c: Coincident(g201,g202)
    c: Coincident(g202,g203)
    c: Coincident(g203,g204)
    c: Coincident(g204,g205)
    c: Coincident(g205,g206)
    c: Coincident(g206,g207)
    c: Coincident(g207,g208)
    c: Coincident(g208,g209)
    c: Coincident(g209,g210)
    c: Coincident(g210,g211)
    c: Coincident(g211,g212)
    c: Coincident(g212,g213)
    c: Coincident(g213,g214)
    c: Coincident(g214,g215)
    c: Coincident(g215,g216)
    c: Coincident(g216,g0)
    c: Coincident(g217,g218)
    c: Coincident(g218,g219)
    c: Coincident(g219,g220)
    c: Coincident(g220,g217)
    c: Coincident(g221,g222)
    c: Coincident(g222,g223)
    c: Coincident(g223,g224)
    c: Coincident(g224,g221)
    c: Coincident(g225,g226)
    c: Coincident(g226,g227)
    c: Coincident(g227,g228)
    c: Coincident(g228,g229)
    c: Coincident(g229,g230)
    c: Coincident(g230,g231)
    c: Coincident(g231,g232)
    c: Coincident(g232,g225)
    c: Coincident(g233,g234)
    c: Coincident(g234,g235)
    c: Coincident(g235,g236)
    c: Coincident(g236,g237)
    c: Coincident(g237,g238)
    c: Coincident(g238,g239)
    c: Coincident(g239,g240)
    c: Coincident(g240,g241)
    c: Coincident(g241,g242)
    c: Coincident(g242,g243)
    c: Coincident(g243,g233)
    c: Coincident(g244,g245)
    c: Coincident(g245,g246)
    c: Coincident(g246,g247)
    c: Coincident(g247,g248)
    c: Coincident(g248,g249)
    c: Coincident(g249,g250)
    c: Coincident(g250,g251)
    c: Coincident(g251,g244)
    c: Coincident(g252,g253)
    c: Coincident(g253,g254)
    c: Coincident(g254,g255)
    c: Coincident(g255,g256)
    c: Coincident(g256,g252)
    c: Coincident(g257,g258)
    c: Coincident(g258,g259)
    c: Coincident(g259,g260)
    c: Coincident(g260,g261)
    c: Coincident(g261,g262)
    c: Coincident(g262,g263)
    c: Coincident(g263,g264)
    c: Coincident(g264,g257)
    c: Coincident(g265,g266)
    c: Coincident(g266,g267)
    c: Coincident(g267,g268)
    c: Coincident(g268,g269)
    c: Coincident(g269,g265)
    c: Coincident(g270,g271)
    c: Coincident(g271,g272)
    c: Coincident(g272,g273)
    c: Coincident(g273,g274)
    c: Coincident(g274,g270)
    c: Coincident(g275,g276)
    c: Coincident(g276,g277)
    c: Coincident(g277,g278)
    c: Coincident(g278,g279)
    c: Coincident(g279,g280)
    c: Coincident(g280,g281)
    c: Coincident(g281,g282)
    c: Coincident(g282,g283)
    c: Coincident(g283,g284)
    c: Coincident(g284,g285)
    c: Coincident(g285,g286)
    c: Coincident(g286,g287)
    c: Coincident(g287,g288)
    c: Coincident(g288,g289)
    c: Coincident(g289,g290)
    c: Coincident(g290,g291)
    c: Coincident(g291,g292)
    c: Coincident(g292,g293)
    c: Coincident(g293,g294)
    c: Coincident(g294,g295)
    c: Coincident(g295,g296)
    c: Coincident(g296,g297)
    c: Coincident(g297,g298)
    c: Coincident(g298,g275)
    c: Coincident(g299,g300)
    c: Coincident(g300,g301)
    c: Coincident(g301,g302)
    c: Coincident(g302,g303)
    c: Coincident(g303,g304)
    c: Coincident(g304,g299)
    c: Coincident(g305,g306)
    c: Coincident(g306,g307)
    c: Coincident(g307,g308)
    c: Coincident(g308,g305)
    c: Coincident(g309,g310)
    c: Coincident(g310,g311)
    c: Coincident(g311,g309)
    c: Coincident(g312,g313)
    c: Coincident(g313,g314)
    c: Coincident(g314,g315)
    c: Coincident(g315,g316)
    c: Coincident(g316,g317)
    c: Coincident(g317,g318)
    c: Coincident(g318,g312)
    c: Coincident(g319,g320)
    c: Coincident(g320,g321)
    c: Coincident(g321,g319)
    c: Coincident(g322,g323)
    c: Coincident(g323,g324)
    c: Coincident(g324,g325)
    c: Coincident(g325,g326)
    c: Coincident(g326,g327)
    c: Coincident(g327,g328)
    c: Coincident(g328,g329)
    c: Coincident(g329,g330)
    c: Coincident(g330,g331)
    c: Coincident(g331,g332)
    c: Coincident(g332,g333)
    c: Coincident(g333,g334)
    c: Coincident(g334,g322)
    c: Coincident(g335,g336)
    c: Coincident(g336,g337)
    c: Coincident(g337,g338)
    c: Coincident(g338,g339)
    c: Coincident(g339,g340)
    c: Coincident(g340,g341)
    c: Coincident(g341,g335)
    c: Coincident(g342,g343)
    c: Coincident(g343,g344)
    c: Coincident(g344,g342)
    c: Coincident(g345,g346)
    c: Coincident(g346,g347)
    c: Coincident(g347,g348)
    c: Coincident(g348,g345)
    c: Coincident(g349,g350)
    c: Coincident(g350,g351)
    c: Coincident(g351,g352)
    c: Coincident(g352,g353)
    c: Coincident(g353,g354)
    c: Coincident(g354,g349)
    c: Coincident(g355,g356)
    c: Coincident(g356,g357)
    c: Coincident(g357,g358)
    c: Coincident(g358,g359)
    c: Coincident(g359,g360)
    c: Coincident(g360,g355)
    c: Coincident(g361,g362)
    c: Coincident(g362,g363)
    c: Coincident(g363,g364)
    c: Coincident(g364,g365)
    c: Coincident(g365,g361)
    c: Coincident(g366,g367)
    c: Coincident(g367,g368)
    c: Coincident(g368,g369)
    c: Coincident(g369,g370)
    c: Coincident(g370,g371)
    c: Coincident(g371,g372)
    c: Coincident(g372,g373)
    c: Coincident(g373,g374)
    c: Coincident(g374,g375)
    c: Coincident(g375,g376)
    c: Coincident(g376,g377)
    c: Coincident(g377,g378)
    c: Coincident(g378,g379)
    c: Coincident(g379,g380)
    c: Coincident(g380,g381)
    c: Coincident(g381,g366)
    c: Coincident(g382,g383)
    c: Coincident(g383,g384)
    c: Coincident(g384,g385)
    c: Coincident(g385,g386)
    c: Coincident(g386,g382)
    c: Coincident(g387,g388)
    c: Coincident(g388,g389)
    c: Coincident(g389,g387)
    c: Coincident(g390,g391)
    c: Coincident(g391,g392)
    c: Coincident(g392,g390)
    c: Coincident(g393,g394)
    c: Coincident(g394,g395)
    c: Coincident(g395,g396)
    c: Coincident(g396,g397)
    c: Coincident(g397,g398)
    c: Coincident(g398,g399)
    c: Coincident(g399,g400)
    c: Coincident(g400,g401)
    c: Coincident(g401,g402)
    c: Coincident(g402,g393)
    c: Coincident(g403,g404)
    c: Coincident(g404,g405)
    c: Coincident(g405,g406)
    c: Coincident(g406,g403)
    c: Coincident(g407,g408)
    c: Coincident(g408,g409)
    c: Coincident(g409,g410)
    c: Coincident(g410,g407)
    c: Coincident(g411,g412)
    c: Coincident(g412,g413)
    c: Coincident(g413,g414)
    c: Coincident(g414,g415)
    c: Coincident(g415,g416)
    c: Coincident(g416,g417)
    c: Coincident(g417,g411)
    c: Coincident(g418,g419)
    c: Coincident(g419,g420)
    c: Coincident(g420,g421)
    c: Coincident(g421,g422)
    c: Coincident(g422,g423)
    c: Coincident(g423,g424)
    c: Coincident(g424,g425)
    c: Coincident(g425,g426)
    c: Coincident(g426,g427)
    c: Coincident(g427,g428)
    c: Coincident(g428,g429)
    c: Coincident(g429,g430)
    c: Coincident(g430,g431)
    c: Coincident(g431,g432)
    c: Coincident(g432,g418)
    c: Coincident(g433,g434)
    c: Coincident(g434,g435)
    c: Coincident(g435,g433)
    c: Coincident(g436,g437)
    c: Coincident(g437,g438)
    c: Coincident(g438,g436)
    c: Coincident(g439,g440)
    c: Coincident(g440,g441)
    c: Coincident(g441,g439)
    c: Coincident(g442,g443)
    c: Coincident(g443,g444)
    c: Coincident(g444,g445)
    c: Coincident(g445,g442)
    c: Coincident(g407,g407)
    c: Coincident(g418,g418)
    c: Coincident(g215,g0)
    c: Coincident(g345,g345)
    c: Coincident(g442,g443)
    c: Coincident(g275,g275)
    c: Coincident(g322,g322)
FEATURE [Sketcher::SketchObject] Sketch033  label="Fang_Gu-Sketch"
  ArcFitTolerance = 1e-06
  FullyConstrained = false
  MakeInternals = false
  Placement = pos=(-13.1235,15.5272,0) rot=(0,0,1;0rad)
  expr: .Placement.Base.x = -(.Shape.BoundBox.XLength / 2)
  expr: .Placement.Base.y = .Shape.BoundBox.YLength / 2
  sketch-geometry (460):
    g0: BSplineCurve PolesCount=4 KnotsCount=2 Degree=3 IsPeriodic=0
    g1: BSplineCurve PolesCount=4 KnotsCount=2 Degree=3 IsPeriodic=0
    g2: BSplineCurve PolesCount=2 KnotsCount=2 Degree=1 IsPeriodic=0
    g3: BSplineCurve PolesCount=2 KnotsCount=2 Degree=1 IsPeriodic=0
    g4: BSplineCurve PolesCount=4 KnotsCount=2 Degree=3 IsPeriodic=0
    g5: BSplineCurve PolesCount=4 KnotsCount=2 Degree=3 IsPeriodic=0
    g6: BSplineCurve PolesCount=4 KnotsCount=2 Degree=3 IsPeriodic=0
    g7: BSplineCurve PolesCount=4 KnotsCount=2 Degree=3 IsPeriodic=0
    g8: BSplineCurve PolesCount=4 KnotsCount=2 Degree=3 IsPeriodic=0
    g9: BSplineCurve PolesCount=4 KnotsCount=2 Degree=3 IsPeriodic=0
    g10: BSplineCurve PolesCount=4 KnotsCount=2 Degree=3 IsPeriodic=0
    g11: BSplineCurve PolesCount=4 KnotsCount=2 Degree=3 IsPeriodic=0
    g12: BSplineCurve PolesCount=4 KnotsCount=2 Degree=3 IsPeriodic=0
    g13: BSplineCurve PolesCount=4 KnotsCount=2 Degree=3 IsPeriodic=0
    g14: BSplineCurve PolesCount=4 KnotsCount=2 Degree=3 IsPeriodic=0
    g15: BSplineCurve PolesCount=4 KnotsCount=2 Degree=3 IsPeriodic=0
    g16: BSplineCurve PolesCount=4 KnotsCount=2 Degree=3 IsPeriodic=0
    g17: BSplineCurve PolesCount=4 KnotsCount=2 Degree=3 IsPeriodic=0
    g18: BSplineCurve PolesCount=4 KnotsCount=2 Degree=3 IsPeriodic=0
    g19: BSplineCurve PolesCount=4 KnotsCount=2 Degree=3 IsPeriodic=0
    g20: BSplineCurve PolesCount=4 KnotsCount=2 Degree=3 IsPeriodic=0
    g21: BSplineCurve PolesCount=4 KnotsCount=2 Degree=3 IsPeriodic=0
    g22: BSplineCurve PolesCount=4 KnotsCount=2 Degree=3 IsPeriodic=0
    g23: BSplineCurve PolesCount=4 KnotsCount=2 Degree=3 IsPeriodic=0
    g24: BSplineCurve PolesCount=4 KnotsCount=2 Degree=3 IsPeriodic=0
    g25: BSplineCurve PolesCount=4 KnotsCount=2 Degree=3 IsPeriodic=0
    g26: BSplineCurve PolesCount=4 KnotsCount=2 Degree=3 IsPeriodic=0
    g27: BSplineCurve PolesCount=4 KnotsCount=2 Degree=3 IsPeriodic=0
    g28: BSplineCurve PolesCount=4 KnotsCount=2 Degree=3 IsPeriodic=0
    g29: BSplineCurve PolesCount=4 KnotsCount=2 Degree=3 IsPeriodic=0
    g30: BSplineCurve PolesCount=4 KnotsCount=2 Degree=3 IsPeriodic=0
    g31: BSplineCurve PolesCount=4 KnotsCount=2 Degree=3 IsPeriodic=0
    g32: BSplineCurve PolesCount=4 KnotsCount=2 Degree=3 IsPeriodic=0
    g33: BSplineCurve PolesCount=4 KnotsCount=2 Degree=3 IsPeriodic=0
    g34: BSplineCurve PolesCount=4 KnotsCount=2 Degree=3 IsPeriodic=0
    g35: BSplineCurve PolesCount=4 KnotsCount=2 Degree=3 IsPeriodic=0
    g36: BSplineCurve PolesCount=4 KnotsCount=2 Degree=3 IsPeriodic=0
    g37: BSplineCurve PolesCount=4 KnotsCount=2 Degree=3 IsPeriodic=0
    g38: BSplineCurve PolesCount=4 KnotsCount=2 Degree=3 IsPeriodic=0
    g39: BSplineCurve PolesCount=4 KnotsCount=2 Degree=3 IsPeriodic=0
    g40: BSplineCurve PolesCount=4 KnotsCount=2 Degree=3 IsPeriodic=0
    g41: BSplineCurve PolesCount=4 KnotsCount=2 Degree=3 IsPeriodic=0
    g42: BSplineCurve PolesCount=4 KnotsCount=2 Degree=3 IsPeriodic=0
    g43: BSplineCurve PolesCount=4 KnotsCount=2 Degree=3 IsPeriodic=0
    g44: BSplineCurve PolesCount=4 KnotsCount=2 Degree=3 IsPeriodic=0
    g45: BSplineCurve PolesCount=4 KnotsCount=2 Degree=3 IsPeriodic=0
    g46: BSplineCurve PolesCount=4 KnotsCount=2 Degree=3 IsPeriodic=0
    g47: BSplineCurve PolesCount=4 KnotsCount=2 Degree=3 IsPeriodic=0
    g48: BSplineCurve PolesCount=4 KnotsCount=2 Degree=3 IsPeriodic=0
    g49: BSplineCurve PolesCount=4 KnotsCount=2 Degree=3 IsPeriodic=0
    g50: BSplineCurve PolesCount=4 KnotsCount=2 Degree=3 IsPeriodic=0
    g51: BSplineCurve PolesCount=4 KnotsCount=2 Degree=3 IsPeriodic=0
    g52: BSplineCurve PolesCount=4 KnotsCount=2 Degree=3 IsPeriodic=0
    g53: BSplineCurve PolesCount=4 KnotsCount=2 Degree=3 IsPeriodic=0
    g54: BSplineCurve PolesCount=4 KnotsCount=2 Degree=3 IsPeriodic=0
    g55: BSplineCurve PolesCount=4 KnotsCount=2 Degree=3 IsPeriodic=0
    g56: BSplineCurve PolesCount=4 KnotsCount=2 Degree=3 IsPeriodic=0
    g57: BSplineCurve PolesCount=4 KnotsCount=2 Degree=3 IsPeriodic=0
    g58: BSplineCurve PolesCount=4 KnotsCount=2 Degree=3 IsPeriodic=0
    g59: BSplineCurve PolesCount=4 KnotsCount=2 Degree=3 IsPeriodic=0
    g60: BSplineCurve PolesCount=4 KnotsCount=2 Degree=3 IsPeriodic=0
    g61: BSplineCurve PolesCount=4 KnotsCount=2 Degree=3 IsPeriodic=0
    g62: BSplineCurve PolesCount=4 KnotsCount=2 Degree=3 IsPeriodic=0
    g63: BSplineCurve PolesCount=4 KnotsCount=2 Degree=3 IsPeriodic=0
    g64: BSplineCurve PolesCount=4 KnotsCount=2 Degree=3 IsPeriodic=0
    g65: BSplineCurve PolesCount=4 KnotsCount=2 Degree=3 IsPeriodic=0
    g66: BSplineCurve PolesCount=4 KnotsCount=2 Degree=3 IsPeriodic=0
    g67: BSplineCurve PolesCount=4 KnotsCount=2 Degree=3 IsPeriodic=0
    g68: BSplineCurve PolesCount=4 KnotsCount=2 Degree=3 IsPeriodic=0
    g69: BSplineCurve PolesCount=4 KnotsCount=2 Degree=3 IsPeriodic=0
    g70: BSplineCurve PolesCount=4 KnotsCount=2 Degree=3 IsPeriodic=0
    g71: BSplineCurve PolesCount=4 KnotsCount=2 Degree=3 IsPeriodic=0
    g72: BSplineCurve PolesCount=4 KnotsCount=2 Degree=3 IsPeriodic=0
    g73: BSplineCurve PolesCount=4 KnotsCount=2 Degree=3 IsPeriodic=0
    g74: BSplineCurve PolesCount=2 KnotsCount=2 Degree=1 IsPeriodic=0
    g75: BSplineCurve PolesCount=2 KnotsCount=2 Degree=1 IsPeriodic=0
    g76: BSplineCurve PolesCount=4 KnotsCount=2 Degree=3 IsPeriodic=0
    g77: BSplineCurve PolesCount=4 KnotsCount=2 Degree=3 IsPeriodic=0
    g78: BSplineCurve PolesCount=4 KnotsCount=2 Degree=3 IsPeriodic=0
    g79: BSplineCurve PolesCount=4 KnotsCount=2 Degree=3 IsPeriodic=0
    g80: BSplineCurve PolesCount=4 KnotsCount=2 Degree=3 IsPeriodic=0
    g81: BSplineCurve PolesCount=2 KnotsCount=2 Degree=1 IsPeriodic=0
    g82: BSplineCurve PolesCount=2 KnotsCount=2 Degree=1 IsPeriodic=0
    g83: BSplineCurve PolesCount=2 KnotsCount=2 Degree=1 IsPeriodic=0
    g84: BSplineCurve PolesCount=2 KnotsCount=2 Degree=1 IsPeriodic=0
    g85: BSplineCurve PolesCount=4 KnotsCount=2 Degree=3 IsPeriodic=0
    g86: BSplineCurve PolesCount=2 KnotsCount=2 Degree=1 IsPeriodic=0
    g87: BSplineCurve PolesCount=2 KnotsCount=2 Degree=1 IsPeriodic=0
    g88: BSplineCurve PolesCount=4 KnotsCount=2 Degree=3 IsPeriodic=0
    g89: BSplineCurve PolesCount=4 KnotsCount=2 Degree=3 IsPeriodic=0
    g90: BSplineCurve PolesCount=2 KnotsCount=2 Degree=1 IsPeriodic=0
    g91: BSplineCurve PolesCount=4 KnotsCount=2 Degree=3 IsPeriodic=0
    g92: BSplineCurve PolesCount=4 KnotsCount=2 Degree=3 IsPeriodic=0
    g93: BSplineCurve PolesCount=4 KnotsCount=2 Degree=3 IsPeriodic=0
    g94: BSplineCurve PolesCount=4 KnotsCount=2 Degree=3 IsPeriodic=0
    g95: BSplineCurve PolesCount=4 KnotsCount=2 Degree=3 IsPeriodic=0
    g96: BSplineCurve PolesCount=4 KnotsCount=2 Degree=3 IsPeriodic=0
    g97: BSplineCurve PolesCount=4 KnotsCount=2 Degree=3 IsPeriodic=0
    g98: BSplineCurve PolesCount=4 KnotsCount=2 Degree=3 IsPeriodic=0
    g99: BSplineCurve PolesCount=2 KnotsCount=2 Degree=1 IsPeriodic=0
    g100: BSplineCurve PolesCount=2 KnotsCount=2 Degree=1 IsPeriodic=0
    g101: BSplineCurve PolesCount=4 KnotsCount=2 Degree=3 IsPeriodic=0
    g102: BSplineCurve PolesCount=4 KnotsCount=2 Degree=3 IsPeriodic=0
    g103: BSplineCurve PolesCount=4 KnotsCount=2 Degree=3 IsPeriodic=0
    g104: BSplineCurve PolesCount=4 KnotsCount=2 Degree=3 IsPeriodic=0
    g105: BSplineCurve PolesCount=4 KnotsCount=2 Degree=3 IsPeriodic=0
    g106: BSplineCurve PolesCount=4 KnotsCount=2 Degree=3 IsPeriodic=0
    g107: BSplineCurve PolesCount=4 KnotsCount=2 Degree=3 IsPeriodic=0
    g108: BSplineCurve PolesCount=4 KnotsCount=2 Degree=3 IsPeriodic=0
    g109: BSplineCurve PolesCount=4 KnotsCount=2 Degree=3 IsPeriodic=0
    g110: BSplineCurve PolesCount=4 KnotsCount=2 Degree=3 IsPeriodic=0
    g111: BSplineCurve PolesCount=4 KnotsCount=2 Degree=3 IsPeriodic=0
    g112: BSplineCurve PolesCount=4 KnotsCount=2 Degree=3 IsPeriodic=0
    g113: BSplineCurve PolesCount=4 KnotsCount=2 Degree=3 IsPeriodic=0
    g114: BSplineCurve PolesCount=4 KnotsCount=2 Degree=3 IsPeriodic=0
    g115: BSplineCurve PolesCount=4 KnotsCount=2 Degree=3 IsPeriodic=0
    g116: BSplineCurve PolesCount=4 KnotsCount=2 Degree=3 IsPeriodic=0
    g117: BSplineCurve PolesCount=4 KnotsCount=2 Degree=3 IsPeriodic=0
    g118: BSplineCurve PolesCount=4 KnotsCount=2 Degree=3 IsPeriodic=0
    g119: BSplineCurve PolesCount=4 KnotsCount=2 Degree=3 IsPeriodic=0
    g120: BSplineCurve PolesCount=4 KnotsCount=2 Degree=3 IsPeriodic=0
    g121: BSplineCurve PolesCount=4 KnotsCount=2 Degree=3 IsPeriodic=0
    g122: BSplineCurve PolesCount=4 KnotsCount=2 Degree=3 IsPeriodic=0
    g123: BSplineCurve PolesCount=4 KnotsCount=2 Degree=3 IsPeriodic=0
    g124: BSplineCurve PolesCount=4 KnotsCount=2 Degree=3 IsPeriodic=0
    g125: BSplineCurve PolesCount=4 KnotsCount=2 Degree=3 IsPeriodic=0
    g126: BSplineCurve PolesCount=4 KnotsCount=2 Degree=3 IsPeriodic=0
    g127: BSplineCurve PolesCount=4 KnotsCount=2 Degree=3 IsPeriodic=0
    g128: BSplineCurve PolesCount=4 KnotsCount=2 Degree=3 IsPeriodic=0
    g129: BSplineCurve PolesCount=4 KnotsCount=2 Degree=3 IsPeriodic=0
    g130: BSplineCurve PolesCount=4 KnotsCount=2 Degree=3 IsPeriodic=0
    g131: BSplineCurve PolesCount=2 KnotsCount=2 Degree=1 IsPeriodic=0
    g132: BSplineCurve PolesCount=2 KnotsCount=2 Degree=1 IsPeriodic=0
    g133: BSplineCurve PolesCount=4 KnotsCount=2 Degree=3 IsPeriodic=0
    g134: BSplineCurve PolesCount=4 KnotsCount=2 Degree=3 IsPeriodic=0
    g135: BSplineCurve PolesCount=4 KnotsCount=2 Degree=3 IsPeriodic=0
    g136: BSplineCurve PolesCount=2 KnotsCount=2 Degree=1 IsPeriodic=0
    g137: BSplineCurve PolesCount=2 KnotsCount=2 Degree=1 IsPeriodic=0
    g138: BSplineCurve PolesCount=4 KnotsCount=2 Degree=3 IsPeriodic=0
    g139: BSplineCurve PolesCount=2 KnotsCount=2 Degree=1 IsPeriodic=0
    g140: BSplineCurve PolesCount=2 KnotsCount=2 Degree=1 IsPeriodic=0
    g141: BSplineCurve PolesCount=4 KnotsCount=2 Degree=3 IsPeriodic=0
    g142: BSplineCurve PolesCount=4 KnotsCount=2 Degree=3 IsPeriodic=0
    g143: BSplineCurve PolesCount=4 KnotsCount=2 Degree=3 IsPeriodic=0
    g144: BSplineCurve PolesCount=4 KnotsCount=2 Degree=3 IsPeriodic=0
    g145: BSplineCurve PolesCount=4 KnotsCount=2 Degree=3 IsPeriodic=0
    g146: BSplineCurve PolesCount=4 KnotsCount=2 Degree=3 IsPeriodic=0
    g147: BSplineCurve PolesCount=4 KnotsCount=2 Degree=3 IsPeriodic=0
    g148: BSplineCurve PolesCount=4 KnotsCount=2 Degree=3 IsPeriodic=0
    g149: BSplineCurve PolesCount=4 KnotsCount=2 Degree=3 IsPeriodic=0
    g150: BSplineCurve PolesCount=4 KnotsCount=2 Degree=3 IsPeriodic=0
    g151: BSplineCurve PolesCount=4 KnotsCount=2 Degree=3 IsPeriodic=0
    g152: BSplineCurve PolesCount=4 KnotsCount=2 Degree=3 IsPeriodic=0
    g153: BSplineCurve PolesCount=2 KnotsCount=2 Degree=1 IsPeriodic=0
    g154: BSplineCurve PolesCount=2 KnotsCount=2 Degree=1 IsPeriodic=0
    g155: BSplineCurve PolesCount=2 KnotsCount=2 Degree=1 IsPeriodic=0
    g156: BSplineCurve PolesCount=2 KnotsCount=2 Degree=1 IsPeriodic=0
    g157: BSplineCurve PolesCount=4 KnotsCount=2 Degree=3 IsPeriodic=0
    g158: BSplineCurve PolesCount=4 KnotsCount=2 Degree=3 IsPeriodic=0
    g159: BSplineCurve PolesCount=4 KnotsCount=2 Degree=3 IsPeriodic=0
    g160: BSplineCurve PolesCount=4 KnotsCount=2 Degree=3 IsPeriodic=0
    g161: BSplineCurve PolesCount=4 KnotsCount=2 Degree=3 IsPeriodic=0
    g162: BSplineCurve PolesCount=4 KnotsCount=2 Degree=3 IsPeriodic=0
    g163: BSplineCurve PolesCount=4 KnotsCount=2 Degree=3 IsPeriodic=0
    g164: BSplineCurve PolesCount=4 KnotsCount=2 Degree=3 IsPeriodic=0
    g165: BSplineCurve PolesCount=4 KnotsCount=2 Degree=3 IsPeriodic=0
    g166: BSplineCurve PolesCount=4 KnotsCount=2 Degree=3 IsPeriodic=0
    g167: BSplineCurve PolesCount=4 KnotsCount=2 Degree=3 IsPeriodic=0
    g168: BSplineCurve PolesCount=4 KnotsCount=2 Degree=3 IsPeriodic=0
    g169: BSplineCurve PolesCount=4 KnotsCount=2 Degree=3 IsPeriodic=0
    g170: BSplineCurve PolesCount=4 KnotsCount=2 Degree=3 IsPeriodic=0
    g171: BSplineCurve PolesCount=4 KnotsCount=2 Degree=3 IsPeriodic=0
    g172: BSplineCurve PolesCount=4 KnotsCount=2 Degree=3 IsPeriodic=0
    g173: BSplineCurve PolesCount=4 KnotsCount=2 Degree=3 IsPeriodic=0
    g174: BSplineCurve PolesCount=4 KnotsCount=2 Degree=3 IsPeriodic=0
    g175: BSplineCurve PolesCount=4 KnotsCount=2 Degree=3 IsPeriodic=0
    g176: BSplineCurve PolesCount=4 KnotsCount=2 Degree=3 IsPeriodic=0
    g177: BSplineCurve PolesCount=4 KnotsCount=2 Degree=3 IsPeriodic=0
    g178: BSplineCurve PolesCount=4 KnotsCount=2 Degree=3 IsPeriodic=0
    g179: BSplineCurve PolesCount=4 KnotsCount=2 Degree=3 IsPeriodic=0
    g180: BSplineCurve PolesCount=4 KnotsCount=2 Degree=3 IsPeriodic=0
    g181: BSplineCurve PolesCount=4 KnotsCount=2 Degree=3 IsPeriodic=0
    g182: BSplineCurve PolesCount=4 KnotsCount=2 Degree=3 IsPeriodic=0
    g183: BSplineCurve PolesCount=2 KnotsCount=2 Degree=1 IsPeriodic=0
    g184: BSplineCurve PolesCount=2 KnotsCount=2 Degree=1 IsPeriodic=0
    g185: BSplineCurve PolesCount=4 KnotsCount=2 Degree=3 IsPeriodic=0
    g186: BSplineCurve PolesCount=4 KnotsCount=2 Degree=3 IsPeriodic=0
    g187: BSplineCurve PolesCount=4 KnotsCount=2 Degree=3 IsPeriodic=0
    g188: BSplineCurve PolesCount=4 KnotsCount=2 Degree=3 IsPeriodic=0
    g189: BSplineCurve PolesCount=4 KnotsCount=2 Degree=3 IsPeriodic=0
    g190: BSplineCurve PolesCount=4 KnotsCount=2 Degree=3 IsPeriodic=0
    g191: BSplineCurve PolesCount=4 KnotsCount=2 Degree=3 IsPeriodic=0
    g192: BSplineCurve PolesCount=4 KnotsCount=2 Degree=3 IsPeriodic=0
    g193: BSplineCurve PolesCount=4 KnotsCount=2 Degree=3 IsPeriodic=0
    g194: BSplineCurve PolesCount=4 KnotsCount=2 Degree=3 IsPeriodic=0
    g195: BSplineCurve PolesCount=4 KnotsCount=2 Degree=3 IsPeriodic=0
    g196: BSplineCurve PolesCount=4 KnotsCount=2 Degree=3 IsPeriodic=0
    g197: BSplineCurve PolesCount=4 KnotsCount=2 Degree=3 IsPeriodic=0
    g198: BSplineCurve PolesCount=4 KnotsCount=2 Degree=3 IsPeriodic=0
    g199: BSplineCurve PolesCount=4 KnotsCount=2 Degree=3 IsPeriodic=0
    g200: BSplineCurve PolesCount=4 KnotsCount=2 Degree=3 IsPeriodic=0
    g201: BSplineCurve PolesCount=4 KnotsCount=2 Degree=3 IsPeriodic=0
    g202: BSplineCurve PolesCount=4 KnotsCount=2 Degree=3 IsPeriodic=0
    g203: BSplineCurve PolesCount=4 KnotsCount=2 Degree=3 IsPeriodic=0
    g204: BSplineCurve PolesCount=4 KnotsCount=2 Degree=3 IsPeriodic=0
    g205: BSplineCurve PolesCount=4 KnotsCount=2 Degree=3 IsPeriodic=0
    g206: BSplineCurve PolesCount=4 KnotsCount=2 Degree=3 IsPeriodic=0
    g207: BSplineCurve PolesCount=4 KnotsCount=2 Degree=3 IsPeriodic=0
    g208: BSplineCurve PolesCount=4 KnotsCount=2 Degree=3 IsPeriodic=0
    g209: BSplineCurve PolesCount=4 KnotsCount=2 Degree=3 IsPeriodic=0
    g210: BSplineCurve PolesCount=4 KnotsCount=2 Degree=3 IsPeriodic=0
    g211: BSplineCurve PolesCount=4 KnotsCount=2 Degree=3 IsPeriodic=0
    g212: BSplineCurve PolesCount=4 KnotsCount=2 Degree=3 IsPeriodic=0
    g213: BSplineCurve PolesCount=4 KnotsCount=2 Degree=3 IsPeriodic=0
    g214: BSplineCurve PolesCount=4 KnotsCount=2 Degree=3 IsPeriodic=0
    g215: BSplineCurve PolesCount=4 KnotsCount=2 Degree=3 IsPeriodic=0
    g216: BSplineCurve PolesCount=4 KnotsCount=2 Degree=3 IsPeriodic=0
    g217: BSplineCurve PolesCount=4 KnotsCount=2 Degree=3 IsPeriodic=0
    g218: BSplineCurve PolesCount=4 KnotsCount=2 Degree=3 IsPeriodic=0
    g219: BSplineCurve PolesCount=4 KnotsCount=2 Degree=3 IsPeriodic=0
    g220: BSplineCurve PolesCount=4 KnotsCount=2 Degree=3 IsPeriodic=0
    g221: BSplineCurve PolesCount=4 KnotsCount=2 Degree=3 IsPeriodic=0
    g222: BSplineCurve PolesCount=4 KnotsCount=2 Degree=3 IsPeriodic=0
    g223: BSplineCurve PolesCount=4 KnotsCount=2 Degree=3 IsPeriodic=0
    g224: BSplineCurve PolesCount=4 KnotsCount=2 Degree=3 IsPeriodic=0
    g225: BSplineCurve PolesCount=4 KnotsCount=2 Degree=3 IsPeriodic=0
    g226: BSplineCurve PolesCount=4 KnotsCount=2 Degree=3 IsPeriodic=0
    g227: BSplineCurve PolesCount=4 KnotsCount=2 Degree=3 IsPeriodic=0
    g228: BSplineCurve PolesCount=4 KnotsCount=2 Degree=3 IsPeriodic=0
    g229: BSplineCurve PolesCount=4 KnotsCount=2 Degree=3 IsPeriodic=0
    g230: BSplineCurve PolesCount=4 KnotsCount=2 Degree=3 IsPeriodic=0
    g231: BSplineCurve PolesCount=4 KnotsCount=2 Degree=3 IsPeriodic=0
    g232: BSplineCurve PolesCount=4 KnotsCount=2 Degree=3 IsPeriodic=0
    g233: BSplineCurve PolesCount=4 KnotsCount=2 Degree=3 IsPeriodic=0
    g234: BSplineCurve PolesCount=4 KnotsCount=2 Degree=3 IsPeriodic=0
    g235: BSplineCurve PolesCount=4 KnotsCount=2 Degree=3 IsPeriodic=0
    g236: BSplineCurve PolesCount=4 KnotsCount=2 Degree=3 IsPeriodic=0
    g237: BSplineCurve PolesCount=4 KnotsCount=2 Degree=3 IsPeriodic=0
    g238: BSplineCurve PolesCount=4 KnotsCount=2 Degree=3 IsPeriodic=0
    g239: BSplineCurve PolesCount=4 KnotsCount=2 Degree=3 IsPeriodic=0
    g240: BSplineCurve PolesCount=4 KnotsCount=2 Degree=3 IsPeriodic=0
    g241: BSplineCurve PolesCount=4 KnotsCount=2 Degree=3 IsPeriodic=0
    g242: BSplineCurve PolesCount=4 KnotsCount=2 Degree=3 IsPeriodic=0
    g243: BSplineCurve PolesCount=4 KnotsCount=2 Degree=3 IsPeriodic=0
    g244: BSplineCurve PolesCount=4 KnotsCount=2 Degree=3 IsPeriodic=0
    g245: BSplineCurve PolesCount=4 KnotsCount=2 Degree=3 IsPeriodic=0
    g246: BSplineCurve PolesCount=4 KnotsCount=2 Degree=3 IsPeriodic=0
    g247: BSplineCurve PolesCount=4 KnotsCount=2 Degree=3 IsPeriodic=0
    g248: BSplineCurve PolesCount=4 KnotsCount=2 Degree=3 IsPeriodic=0
    g249: BSplineCurve PolesCount=4 KnotsCount=2 Degree=3 IsPeriodic=0
    g250: BSplineCurve PolesCount=4 KnotsCount=2 Degree=3 IsPeriodic=0
    g251: BSplineCurve PolesCount=4 KnotsCount=2 Degree=3 IsPeriodic=0
    g252: BSplineCurve PolesCount=4 KnotsCount=2 Degree=3 IsPeriodic=0
    g253: BSplineCurve PolesCount=4 KnotsCount=2 Degree=3 IsPeriodic=0
    g254: BSplineCurve PolesCount=4 KnotsCount=2 Degree=3 IsPeriodic=0
    g255: BSplineCurve PolesCount=4 KnotsCount=2 Degree=3 IsPeriodic=0
    g256: BSplineCurve PolesCount=4 KnotsCount=2 Degree=3 IsPeriodic=0
    g257: BSplineCurve PolesCount=4 KnotsCount=2 Degree=3 IsPeriodic=0
    g258: BSplineCurve PolesCount=2 KnotsCount=2 Degree=1 IsPeriodic=0
    g259: BSplineCurve PolesCount=2 KnotsCount=2 Degree=1 IsPeriodic=0
    g260: BSplineCurve PolesCount=4 KnotsCount=2 Degree=3 IsPeriodic=0
    g261: BSplineCurve PolesCount=4 KnotsCount=2 Degree=3 IsPeriodic=0
    g262: BSplineCurve PolesCount=4 KnotsCount=2 Degree=3 IsPeriodic=0
    g263: BSplineCurve PolesCount=4 KnotsCount=2 Degree=3 IsPeriodic=0
    g264: BSplineCurve PolesCount=4 KnotsCount=2 Degree=3 IsPeriodic=0
    g265: BSplineCurve PolesCount=4 KnotsCount=2 Degree=3 IsPeriodic=0
    g266: BSplineCurve PolesCount=4 KnotsCount=2 Degree=3 IsPeriodic=0
    g267: BSplineCurve PolesCount=4 KnotsCount=2 Degree=3 IsPeriodic=0
    g268: BSplineCurve PolesCount=4 KnotsCount=2 Degree=3 IsPeriodic=0
    g269: BSplineCurve PolesCount=4 KnotsCount=2 Degree=3 IsPeriodic=0
    g270: BSplineCurve PolesCount=4 KnotsCount=2 Degree=3 IsPeriodic=0
    g271: BSplineCurve PolesCount=4 KnotsCount=2 Degree=3 IsPeriodic=0
    g272: BSplineCurve PolesCount=4 KnotsCount=2 Degree=3 IsPeriodic=0
    g273: BSplineCurve PolesCount=4 KnotsCount=2 Degree=3 IsPeriodic=0
    g274: BSplineCurve PolesCount=4 KnotsCount=2 Degree=3 IsPeriodic=0
    g275: BSplineCurve PolesCount=4 KnotsCount=2 Degree=3 IsPeriodic=0
    g276: BSplineCurve PolesCount=4 KnotsCount=2 Degree=3 IsPeriodic=0
    g277: BSplineCurve PolesCount=4 KnotsCount=2 Degree=3 IsPeriodic=0
    g278: BSplineCurve PolesCount=2 KnotsCount=2 Degree=1 IsPeriodic=0
    g279: BSplineCurve PolesCount=2 KnotsCount=2 Degree=1 IsPeriodic=0
    g280: BSplineCurve PolesCount=4 KnotsCount=2 Degree=3 IsPeriodic=0
    g281: BSplineCurve PolesCount=4 KnotsCount=2 Degree=3 IsPeriodic=0
    g282: BSplineCurve PolesCount=4 KnotsCount=2 Degree=3 IsPeriodic=0
    g283: BSplineCurve PolesCount=2 KnotsCount=2 Degree=1 IsPeriodic=0
    g284: BSplineCurve PolesCount=2 KnotsCount=2 Degree=1 IsPeriodic=0
    g285: BSplineCurve PolesCount=4 KnotsCount=2 Degree=3 IsPeriodic=0
    g286: BSplineCurve PolesCount=4 KnotsCount=2 Degree=3 IsPeriodic=0
    g287: BSplineCurve PolesCount=4 KnotsCount=2 Degree=3 IsPeriodic=0
    g288: BSplineCurve PolesCount=4 KnotsCount=2 Degree=3 IsPeriodic=0
    g289: BSplineCurve PolesCount=4 KnotsCount=2 Degree=3 IsPeriodic=0
    g290: BSplineCurve PolesCount=4 KnotsCount=2 Degree=3 IsPeriodic=0
    g291: BSplineCurve PolesCount=4 KnotsCount=2 Degree=3 IsPeriodic=0
    g292: BSplineCurve PolesCount=4 KnotsCount=2 Degree=3 IsPeriodic=0
    g293: BSplineCurve PolesCount=4 KnotsCount=2 Degree=3 IsPeriodic=0
    g294: BSplineCurve PolesCount=4 KnotsCount=2 Degree=3 IsPeriodic=0
    g295: BSplineCurve PolesCount=4 KnotsCount=2 Degree=3 IsPeriodic=0
    g296: BSplineCurve PolesCount=4 KnotsCount=2 Degree=3 IsPeriodic=0
    g297: BSplineCurve PolesCount=4 KnotsCount=2 Degree=3 IsPeriodic=0
    g298: BSplineCurve PolesCount=4 KnotsCount=2 Degree=3 IsPeriodic=0
    g299: BSplineCurve PolesCount=4 KnotsCount=2 Degree=3 IsPeriodic=0
    g300: BSplineCurve PolesCount=4 KnotsCount=2 Degree=3 IsPeriodic=0
    g301: BSplineCurve PolesCount=4 KnotsCount=2 Degree=3 IsPeriodic=0
    g302: BSplineCurve PolesCount=4 KnotsCount=2 Degree=3 IsPeriodic=0
    g303: BSplineCurve PolesCount=4 KnotsCount=2 Degree=3 IsPeriodic=0
    g304: BSplineCurve PolesCount=4 KnotsCount=2 Degree=3 IsPeriodic=0
    g305: BSplineCurve PolesCount=4 KnotsCount=2 Degree=3 IsPeriodic=0
    g306: BSplineCurve PolesCount=4 KnotsCount=2 Degree=3 IsPeriodic=0
    g307: BSplineCurve PolesCount=4 KnotsCount=2 Degree=3 IsPeriodic=0
    g308: BSplineCurve PolesCount=4 KnotsCount=2 Degree=3 IsPeriodic=0
    g309: BSplineCurve PolesCount=4 KnotsCount=2 Degree=3 IsPeriodic=0
    g310: BSplineCurve PolesCount=4 KnotsCount=2 Degree=3 IsPeriodic=0
    g311: BSplineCurve PolesCount=4 KnotsCount=2 Degree=3 IsPeriodic=0
    g312: BSplineCurve PolesCount=4 KnotsCount=2 Degree=3 IsPeriodic=0
    g313: BSplineCurve PolesCount=4 KnotsCount=2 Degree=3 IsPeriodic=0
    g314: BSplineCurve PolesCount=4 KnotsCount=2 Degree=3 IsPeriodic=0
    g315: BSplineCurve PolesCount=4 KnotsCount=2 Degree=3 IsPeriodic=0
    g316: BSplineCurve PolesCount=4 KnotsCount=2 Degree=3 IsPeriodic=0
    g317: BSplineCurve PolesCount=4 KnotsCount=2 Degree=3 IsPeriodic=0
    g318: BSplineCurve PolesCount=4 KnotsCount=2 Degree=3 IsPeriodic=0
    g319: BSplineCurve PolesCount=4 KnotsCount=2 Degree=3 IsPeriodic=0
    g320: BSplineCurve PolesCount=4 KnotsCount=2 Degree=3 IsPeriodic=0
    g321: BSplineCurve PolesCount=4 KnotsCount=2 Degree=3 IsPeriodic=0
    g322: BSplineCurve PolesCount=4 KnotsCount=2 Degree=3 IsPeriodic=0
    g323: BSplineCurve PolesCount=4 KnotsCount=2 Degree=3 IsPeriodic=0
    g324: BSplineCurve PolesCount=4 KnotsCount=2 Degree=3 IsPeriodic=0
    g325: BSplineCurve PolesCount=4 KnotsCount=2 Degree=3 IsPeriodic=0
    g326: BSplineCurve PolesCount=4 KnotsCount=2 Degree=3 IsPeriodic=0
    g327: BSplineCurve PolesCount=4 KnotsCount=2 Degree=3 IsPeriodic=0
    g328: BSplineCurve PolesCount=4 KnotsCount=2 Degree=3 IsPeriodic=0
    g329: BSplineCurve PolesCount=4 KnotsCount=2 Degree=3 IsPeriodic=0
    g330: BSplineCurve PolesCount=4 KnotsCount=2 Degree=3 IsPeriodic=0
    g331: BSplineCurve PolesCount=4 KnotsCount=2 Degree=3 IsPeriodic=0
    g332: BSplineCurve PolesCount=4 KnotsCount=2 Degree=3 IsPeriodic=0
    g333: BSplineCurve PolesCount=4 KnotsCount=2 Degree=3 IsPeriodic=0
    g334: BSplineCurve PolesCount=4 KnotsCount=2 Degree=3 IsPeriodic=0
    g335: BSplineCurve PolesCount=4 KnotsCount=2 Degree=3 IsPeriodic=0
    g336: BSplineCurve PolesCount=4 KnotsCount=2 Degree=3 IsPeriodic=0
    g337: BSplineCurve PolesCount=4 KnotsCount=2 Degree=3 IsPeriodic=0
    g338: BSplineCurve PolesCount=4 KnotsCount=2 Degree=3 IsPeriodic=0
    g339: BSplineCurve PolesCount=4 KnotsCount=2 Degree=3 IsPeriodic=0
    g340: BSplineCurve PolesCount=4 KnotsCount=2 Degree=3 IsPeriodic=0
    g341: BSplineCurve PolesCount=4 KnotsCount=2 Degree=3 IsPeriodic=0
    g342: BSplineCurve PolesCount=4 KnotsCount=2 Degree=3 IsPeriodic=0
    g343: BSplineCurve PolesCount=4 KnotsCount=2 Degree=3 IsPeriodic=0
    g344: BSplineCurve PolesCount=4 KnotsCount=2 Degree=3 IsPeriodic=0
    g345: BSplineCurve PolesCount=4 KnotsCount=2 Degree=3 IsPeriodic=0
    g346: BSplineCurve PolesCount=4 KnotsCount=2 Degree=3 IsPeriodic=0
    g347: BSplineCurve PolesCount=4 KnotsCount=2 Degree=3 IsPeriodic=0
    g348: BSplineCurve PolesCount=4 KnotsCount=2 Degree=3 IsPeriodic=0
    g349: BSplineCurve PolesCount=4 KnotsCount=2 Degree=3 IsPeriodic=0
    g350: BSplineCurve PolesCount=4 KnotsCount=2 Degree=3 IsPeriodic=0
    g351: BSplineCurve PolesCount=4 KnotsCount=2 Degree=3 IsPeriodic=0
    g352: BSplineCurve PolesCount=4 KnotsCount=2 Degree=3 IsPeriodic=0
    g353: BSplineCurve PolesCount=4 KnotsCount=2 Degree=3 IsPeriodic=0
    g354: BSplineCurve PolesCount=4 KnotsCount=2 Degree=3 IsPeriodic=0
    g355: BSplineCurve PolesCount=4 KnotsCount=2 Degree=3 IsPeriodic=0
    g356: BSplineCurve PolesCount=4 KnotsCount=2 Degree=3 IsPeriodic=0
    g357: BSplineCurve PolesCount=4 KnotsCount=2 Degree=3 IsPeriodic=0
    g358: BSplineCurve PolesCount=4 KnotsCount=2 Degree=3 IsPeriodic=0
    g359: BSplineCurve PolesCount=4 KnotsCount=2 Degree=3 IsPeriodic=0
    g360: BSplineCurve PolesCount=4 KnotsCount=2 Degree=3 IsPeriodic=0
    g361: BSplineCurve PolesCount=4 KnotsCount=2 Degree=3 IsPeriodic=0
    g362: BSplineCurve PolesCount=4 KnotsCount=2 Degree=3 IsPeriodic=0
    g363: BSplineCurve PolesCount=2 KnotsCount=2 Degree=1 IsPeriodic=0
    g364: BSplineCurve PolesCount=2 KnotsCount=2 Degree=1 IsPeriodic=0
    g365: BSplineCurve PolesCount=4 KnotsCount=2 Degree=3 IsPeriodic=0
    g366: BSplineCurve PolesCount=4 KnotsCount=2 Degree=3 IsPeriodic=0
    g367: BSplineCurve PolesCount=4 KnotsCount=2 Degree=3 IsPeriodic=0
    g368: BSplineCurve PolesCount=4 KnotsCount=2 Degree=3 IsPeriodic=0
    g369: BSplineCurve PolesCount=4 KnotsCount=2 Degree=3 IsPeriodic=0
    g370: BSplineCurve PolesCount=4 KnotsCount=2 Degree=3 IsPeriodic=0
    g371: BSplineCurve PolesCount=4 KnotsCount=2 Degree=3 IsPeriodic=0
    g372: BSplineCurve PolesCount=4 KnotsCount=2 Degree=3 IsPeriodic=0
    g373: BSplineCurve PolesCount=4 KnotsCount=2 Degree=3 IsPeriodic=0
    g374: BSplineCurve PolesCount=4 KnotsCount=2 Degree=3 IsPeriodic=0
    g375: BSplineCurve PolesCount=4 KnotsCount=2 Degree=3 IsPeriodic=0
    g376: BSplineCurve PolesCount=4 KnotsCount=2 Degree=3 IsPeriodic=0
    g377: BSplineCurve PolesCount=4 KnotsCount=2 Degree=3 IsPeriodic=0
    g378: BSplineCurve PolesCount=4 KnotsCount=2 Degree=3 IsPeriodic=0
    g379: BSplineCurve PolesCount=4 KnotsCount=2 Degree=3 IsPeriodic=0
    g380: BSplineCurve PolesCount=4 KnotsCount=2 Degree=3 IsPeriodic=0
    g381: BSplineCurve PolesCount=4 KnotsCount=2 Degree=3 IsPeriodic=0
    g382: BSplineCurve PolesCount=4 KnotsCount=2 Degree=3 IsPeriodic=0
    g383: BSplineCurve PolesCount=4 KnotsCount=2 Degree=3 IsPeriodic=0
    g384: BSplineCurve PolesCount=4 KnotsCount=2 Degree=3 IsPeriodic=0
    g385: BSplineCurve PolesCount=4 KnotsCount=2 Degree=3 IsPeriodic=0
    g386: BSplineCurve PolesCount=4 KnotsCount=2 Degree=3 IsPeriodic=0
    g387: BSplineCurve PolesCount=4 KnotsCount=2 Degree=3 IsPeriodic=0
    g388: BSplineCurve PolesCount=2 KnotsCount=2 Degree=1 IsPeriodic=0
    g389: BSplineCurve PolesCount=2 KnotsCount=2 Degree=1 IsPeriodic=0
    g390: BSplineCurve PolesCount=4 KnotsCount=2 Degree=3 IsPeriodic=0
    g391: BSplineCurve PolesCount=4 KnotsCount=2 Degree=3 IsPeriodic=0
    g392: BSplineCurve PolesCount=4 KnotsCount=2 Degree=3 IsPeriodic=0
    g393: BSplineCurve PolesCount=4 KnotsCount=2 Degree=3 IsPeriodic=0
    g394: BSplineCurve PolesCount=2 KnotsCount=2 Degree=1 IsPeriodic=0
    g395: BSplineCurve PolesCount=4 KnotsCount=2 Degree=3 IsPeriodic=0
    g396: BSplineCurve PolesCount=4 KnotsCount=2 Degree=3 IsPeriodic=0
    g397: BSplineCurve PolesCount=4 KnotsCount=2 Degree=3 IsPeriodic=0
    g398: BSplineCurve PolesCount=4 KnotsCount=2 Degree=3 IsPeriodic=0
    g399: BSplineCurve PolesCount=4 KnotsCount=2 Degree=3 IsPeriodic=0
    ... +60 more geometry lines
  constraints (460):
    c: Coincident(g0,g1)
    c: Coincident(g1,g2)
    c: Coincident(g2,g3)
    c: Coincident(g3,g4)
    c: Coincident(g4,g5)
    c: Coincident(g5,g6)
    c: Coincident(g6,g7)
    c: Coincident(g7,g8)
    c: Coincident(g8,g9)
    c: Coincident(g9,g10)
    c: Coincident(g10,g11)
    c: Coincident(g11,g12)
    c: Coincident(g12,g13)
    c: Coincident(g13,g14)
    c: Coincident(g14,g15)
    c: Coincident(g15,g16)
    c: Coincident(g16,g17)
    c: Coincident(g17,g18)
    c: Coincident(g18,g19)
    c: Coincident(g19,g20)
    c: Coincident(g20,g21)
    c: Coincident(g21,g22)
    c: Coincident(g22,g23)
    c: Coincident(g23,g24)
    c: Coincident(g24,g25)
    c: Coincident(g25,g26)
    c: Coincident(g26,g27)
    c: Coincident(g27,g28)
    c: Coincident(g28,g29)
    c: Coincident(g29,g30)
    c: Coincident(g30,g31)
    c: Coincident(g31,g32)
    c: Coincident(g32,g33)
    c: Coincident(g33,g34)
    c: Coincident(g34,g35)
    c: Coincident(g35,g36)
    c: Coincident(g36,g37)
    c: Coincident(g37,g38)
    c: Coincident(g38,g39)
    c: Coincident(g39,g40)
    c: Coincident(g40,g41)
    c: Coincident(g41,g42)
    c: Coincident(g42,g43)
    c: Coincident(g43,g44)
    c: Coincident(g44,g45)
    c: Coincident(g45,g46)
    c: Coincident(g46,g47)
    c: Coincident(g47,g48)
    c: Coincident(g48,g49)
    c: Coincident(g49,g0)
    c: Coincident(g50,g51)
    c: Coincident(g51,g52)
    c: Coincident(g52,g53)
    c: Coincident(g53,g54)
    c: Coincident(g54,g55)
    c: Coincident(g55,g56)
    c: Coincident(g56,g57)
    c: Coincident(g57,g58)
    c: Coincident(g58,g59)
    c: Coincident(g59,g60)
    c: Coincident(g60,g61)
    c: Coincident(g61,g62)
    c: Coincident(g62,g63)
    c: Coincident(g63,g64)
    c: Coincident(g64,g65)
    c: Coincident(g65,g66)
    c: Coincident(g66,g67)
    c: Coincident(g67,g68)
    c: Coincident(g68,g69)
    c: Coincident(g69,g70)
    c: Coincident(g70,g71)
    c: Coincident(g71,g72)
    c: Coincident(g72,g73)
    c: Coincident(g73,g74)
    c: Coincident(g74,g75)
    c: Coincident(g75,g76)
    c: Coincident(g76,g77)
    c: Coincident(g77,g78)
    c: Coincident(g78,g79)
    c: Coincident(g79,g80)
    c: Coincident(g80,g81)
    c: Coincident(g81,g82)
    c: Coincident(g82,g83)
    c: Coincident(g83,g84)
    c: Coincident(g84,g85)
    c: Coincident(g85,g86)
    c: Coincident(g86,g87)
    c: Coincident(g87,g88)
    c: Coincident(g88,g89)
    c: Coincident(g90,g91)
    c: Coincident(g91,g92)
    c: Coincident(g92,g93)
    c: Coincident(g93,g94)
    c: Coincident(g94,g95)
    c: Coincident(g95,g96)
    c: Coincident(g96,g97)
    c: Coincident(g97,g98)
    c: Coincident(g98,g99)
    c: Coincident(g99,g100)
    c: Coincident(g100,g101)
    c: Coincident(g101,g102)
    c: Coincident(g102,g103)
    c: Coincident(g103,g104)
    c: Coincident(g104,g105)
    c: Coincident(g105,g106)
    c: Coincident(g106,g107)
    c: Coincident(g107,g108)
    c: Coincident(g108,g109)
    c: Coincident(g109,g110)
    c: Coincident(g110,g111)
    c: Coincident(g111,g112)
    c: Coincident(g112,g113)
    c: Coincident(g113,g114)
    c: Coincident(g114,g115)
    c: Coincident(g115,g116)
    c: Coincident(g116,g117)
    c: Coincident(g117,g118)
    c: Coincident(g118,g119)
    c: Coincident(g119,g120)
    c: Coincident(g120,g121)
    c: Coincident(g121,g122)
    c: Coincident(g122,g123)
    c: Coincident(g123,g124)
    c: Coincident(g124,g125)
    c: Coincident(g125,g126)
    c: Coincident(g126,g127)
    c: Coincident(g127,g128)
    c: Coincident(g128,g129)
    c: Coincident(g129,g130)
    c: Coincident(g130,g131)
    c: Coincident(g131,g132)
    c: Coincident(g132,g133)
    c: Coincident(g133,g134)
    c: Coincident(g134,g135)
    c: Coincident(g135,g136)
    c: Coincident(g136,g137)
    c: Coincident(g137,g138)
    c: Coincident(g138,g90)
    c: Coincident(g139,g140)
    c: Coincident(g140,g141)
    c: Coincident(g141,g142)
    c: Coincident(g142,g143)
    c: Coincident(g144,g145)
    c: Coincident(g145,g146)
    c: Coincident(g146,g147)
    c: Coincident(g147,g148)
    c: Coincident(g148,g149)
    c: Coincident(g149,g150)
    c: Coincident(g150,g151)
    c: Coincident(g151,g152)
    c: Coincident(g152,g153)
    c: Coincident(g153,g154)
    c: Coincident(g154,g155)
    c: Coincident(g155,g156)
    c: Coincident(g156,g157)
    c: Coincident(g157,g158)
    c: Coincident(g158,g159)
    c: Coincident(g159,g160)
    c: Coincident(g160,g161)
    c: Coincident(g161,g162)
    c: Coincident(g162,g163)
    c: Coincident(g163,g164)
    c: Coincident(g164,g165)
    c: Coincident(g165,g166)
    c: Coincident(g166,g167)
    c: Coincident(g167,g144)
    c: Coincident(g168,g169)
    c: Coincident(g169,g170)
    c: Coincident(g170,g168)
    c: Coincident(g171,g172)
    c: Coincident(g172,g173)
    c: Coincident(g173,g171)
    c: Coincident(g174,g175)
    c: Coincident(g175,g176)
    c: Coincident(g176,g177)
    c: Coincident(g177,g178)
    c: Coincident(g178,g179)
    c: Coincident(g179,g180)
    c: Coincident(g180,g181)
    c: Coincident(g181,g182)
    c: Coincident(g182,g183)
    c: Coincident(g183,g184)
    c: Coincident(g184,g185)
    c: Coincident(g185,g186)
    c: Coincident(g186,g187)
    c: Coincident(g187,g174)
    c: Coincident(g189,g190)
    c: Coincident(g190,g191)
    c: Coincident(g191,g188)
    c: Coincident(g192,g193)
    c: Coincident(g193,g194)
    c: Coincident(g194,g195)
    c: Coincident(g195,g196)
    c: Coincident(g196,g197)
    c: Coincident(g197,g198)
    c: Coincident(g198,g199)
    c: Coincident(g199,g200)
    c: Coincident(g200,g201)
    c: Coincident(g201,g192)
    c: Coincident(g202,g203)
    c: Coincident(g203,g204)
    c: Coincident(g204,g202)
    c: Coincident(g205,g206)
    c: Coincident(g206,g207)
    c: Coincident(g207,g208)
    c: Coincident(g208,g209)
    c: Coincident(g209,g210)
    c: Coincident(g210,g211)
    c: Coincident(g211,g212)
    c: Coincident(g212,g213)
    c: Coincident(g213,g205)
    c: Coincident(g215,g216)
    c: Coincident(g216,g217)
    c: Coincident(g217,g218)
    c: Coincident(g218,g219)
    c: Coincident(g219,g220)
    c: Coincident(g220,g221)
    c: Coincident(g221,g214)
    c: Coincident(g223,g224)
    c: Coincident(g224,g225)
    c: Coincident(g225,g226)
    c: Coincident(g226,g227)
    c: Coincident(g227,g228)
    c: Coincident(g228,g229)
    c: Coincident(g229,g230)
    c: Coincident(g230,g231)
    c: Coincident(g231,g232)
    c: Coincident(g232,g233)
    c: Coincident(g233,g234)
    c: Coincident(g234,g235)
    c: Coincident(g235,g236)
    c: Coincident(g236,g237)
    c: Coincident(g237,g238)
    c: Coincident(g238,g239)
    c: Coincident(g239,g240)
    c: Coincident(g240,g241)
    c: Coincident(g241,g242)
    c: Coincident(g242,g243)
    c: Coincident(g243,g244)
    c: Coincident(g244,g245)
    c: Coincident(g245,g246)
    c: Coincident(g246,g247)
    c: Coincident(g247,g248)
    c: Coincident(g248,g249)
    c: Coincident(g249,g250)
    c: Coincident(g250,g251)
    c: Coincident(g251,g252)
    c: Coincident(g252,g253)
    c: Coincident(g253,g254)
    c: Coincident(g254,g255)
    c: Coincident(g255,g256)
    c: Coincident(g256,g257)
    c: Coincident(g257,g258)
    c: Coincident(g258,g259)
    c: Coincident(g259,g260)
    c: Coincident(g260,g261)
    c: Coincident(g261,g262)
    c: Coincident(g262,g263)
    c: Coincident(g263,g264)
    c: Coincident(g264,g265)
    c: Coincident(g265,g266)
    c: Coincident(g266,g267)
    c: Coincident(g267,g268)
    c: Coincident(g268,g269)
    c: Coincident(g269,g270)
    c: Coincident(g270,g271)
    c: Coincident(g271,g272)
    c: Coincident(g272,g273)
    c: Coincident(g273,g274)
    c: Coincident(g274,g275)
    c: Coincident(g275,g276)
    c: Coincident(g276,g277)
    c: Coincident(g277,g278)
    c: Coincident(g278,g279)
    c: Coincident(g279,g280)
    c: Coincident(g280,g281)
    c: Coincident(g281,g282)
    c: Coincident(g282,g283)
    c: Coincident(g283,g284)
    c: Coincident(g284,g285)
    c: Coincident(g285,g286)
    c: Coincident(g286,g287)
    c: Coincident(g287,g288)
    c: Coincident(g288,g289)
    c: Coincident(g289,g290)
    c: Coincident(g290,g291)
    c: Coincident(g291,g292)
    c: Coincident(g292,g293)
    c: Coincident(g293,g294)
    c: Coincident(g294,g295)
    c: Coincident(g295,g296)
    c: Coincident(g296,g297)
    c: Coincident(g297,g298)
    c: Coincident(g298,g299)
    c: Coincident(g299,g300)
    c: Coincident(g300,g301)
    c: Coincident(g301,g302)
    c: Coincident(g302,g303)
    c: Coincident(g303,g304)
    c: Coincident(g304,g305)
    c: Coincident(g305,g306)
    c: Coincident(g306,g307)
    c: Coincident(g307,g308)
    c: Coincident(g308,g309)
    c: Coincident(g309,g310)
    c: Coincident(g310,g311)
    c: Coincident(g311,g312)
    c: Coincident(g312,g313)
    c: Coincident(g313,g314)
    c: Coincident(g314,g315)
    c: Coincident(g315,g316)
    c: Coincident(g316,g317)
    c: Coincident(g317,g318)
    c: Coincident(g318,g319)
    c: Coincident(g319,g320)
    c: Coincident(g320,g321)
    c: Coincident(g321,g322)
    c: Coincident(g322,g323)
    c: Coincident(g323,g324)
    c: Coincident(g324,g325)
    c: Coincident(g325,g326)
    c: Coincident(g326,g327)
    c: Coincident(g327,g328)
    c: Coincident(g328,g329)
    c: Coincident(g329,g330)
    c: Coincident(g330,g331)
    c: Coincident(g331,g332)
    c: Coincident(g332,g333)
    c: Coincident(g333,g334)
    c: Coincident(g334,g335)
    c: Coincident(g335,g336)
    c: Coincident(g336,g337)
    c: Coincident(g337,g338)
    c: Coincident(g338,g339)
    c: Coincident(g339,g340)
    c: Coincident(g340,g341)
    c: Coincident(g341,g342)
    c: Coincident(g342,g343)
    c: Coincident(g343,g344)
    c: Coincident(g344,g345)
    c: Coincident(g345,g346)
    c: Coincident(g346,g347)
    c: Coincident(g347,g348)
    c: Coincident(g348,g349)
    c: Coincident(g349,g350)
    c: Coincident(g350,g351)
    c: Coincident(g351,g352)
    c: Coincident(g352,g353)
    c: Coincident(g353,g354)
    c: Coincident(g354,g355)
    c: Coincident(g355,g356)
    c: Coincident(g356,g357)
    c: Coincident(g357,g358)
    c: Coincident(g358,g359)
    c: Coincident(g359,g360)
    c: Coincident(g360,g361)
    c: Coincident(g361,g362)
    c: Coincident(g362,g363)
    c: Coincident(g363,g364)
    c: Coincident(g364,g365)
    c: Coincident(g365,g366)
    c: Coincident(g366,g367)
    c: Coincident(g367,g368)
    c: Coincident(g368,g369)
    c: Coincident(g369,g370)
    c: Coincident(g370,g371)
    c: Coincident(g371,g372)
    c: Coincident(g372,g373)
    c: Coincident(g373,g374)
    c: Coincident(g374,g375)
    c: Coincident(g375,g376)
    c: Coincident(g376,g377)
    c: Coincident(g377,g378)
    c: Coincident(g378,g379)
    c: Coincident(g379,g380)
    c: Coincident(g380,g381)
    c: Coincident(g381,g222)
    c: Coincident(g382,g383)
    c: Coincident(g384,g385)
    c: Coincident(g385,g386)
    c: Coincident(g386,g387)
    c: Coincident(g387,g388)
    c: Coincident(g388,g389)
    c: Coincident(g389,g382)
    c: Coincident(g390,g391)
    c: Coincident(g391,g392)
    c: Coincident(g392,g393)
    c: Coincident(g393,g390)
    c: Coincident(g394,g395)
    c: Coincident(g396,g397)
    c: Coincident(g397,g398)
    c: Coincident(g398,g399)
    c: Coincident(g399,g400)
    c: Coincident(g400,g401)
    c: Coincident(g401,g402)
    c: Coincident(g402,g403)
    c: Coincident(g403,g404)
    c: Coincident(g404,g405)
    c: Coincident(g405,g406)
    c: Coincident(g406,g407)
    c: Coincident(g407,g408)
    c: Coincident(g408,g409)
    c: Coincident(g409,g410)
    c: Coincident(g410,g411)
    c: Coincident(g411,g394)
    c: Coincident(g412,g413)
    c: Coincident(g413,g414)
    c: Coincident(g414,g415)
    c: Coincident(g415,g416)
    c: Coincident(g416,g412)
    c: Coincident(g417,g418)
    c: Coincident(g418,g419)
    c: Coincident(g419,g420)
    c: Coincident(g420,g417)
    c: Coincident(g421,g422)
    c: Coincident(g422,g423)
    c: Coincident(g423,g424)
    c: Coincident(g424,g425)
    c: Coincident(g425,g426)
    c: Coincident(g426,g421)
    c: Coincident(g427,g428)
    c: Coincident(g429,g427)
    c: Coincident(g430,g431)
    c: Coincident(g431,g432)
    c: Coincident(g432,g433)
    c: Coincident(g433,g434)
    c: Coincident(g434,g435)
    c: Coincident(g435,g436)
    c: Coincident(g436,g437)
    c: Coincident(g437,g430)
    c: Coincident(g439,g440)
    c: Coincident(g440,g441)
    c: Coincident(g441,g442)
    c: Coincident(g442,g443)
    c: Coincident(g443,g444)
    c: Coincident(g444,g445)
    c: Coincident(g445,g446)
    c: Coincident(g446,g447)
    c: Coincident(g447,g448)
    c: Coincident(g448,g449)
    c: Coincident(g449,g450)
    c: Coincident(g450,g451)
    c: Coincident(g451,g452)
    c: Coincident(g452,g453)
    c: Coincident(g453,g454)
    c: Coincident(g454,g455)
    c: Coincident(g455,g456)
    c: Coincident(g456,g438)
    c: Coincident(g457,g458)
    c: Coincident(g458,g459)
    c: Coincident(g459,g457)
    c: Coincident(g383,g384)
    c: Coincident(g222,g223)
    c: Coincident(g428,g429)
    c: Coincident(g214,g215)
    c: Coincident(g438,g439)
    c: Coincident(g50,g89)
    c: Coincident(g395,g396)
    c: Coincident(g139,g143)
    c: Coincident(g188,g189)
FEATURE [Sketcher::SketchObject] Sketch034  label="Flower_Girl-Sketch"
  ArcFitTolerance = 1e-06
  FullyConstrained = false
  MakeInternals = false
  Placement = pos=(-11.7649,14.6,0) rot=(0,0,1;0rad)
  expr: .Placement.Base.x = -(.Shape.BoundBox.XLength / 2)
  expr: .Placement.Base.y = .Shape.BoundBox.YLength / 2
  sketch-geometry (330):
    g0: BSplineCurve PolesCount=4 KnotsCount=2 Degree=3 IsPeriodic=0
    g1: BSplineCurve PolesCount=4 KnotsCount=2 Degree=3 IsPeriodic=0
    g2: BSplineCurve PolesCount=4 KnotsCount=2 Degree=3 IsPeriodic=0
    g3: BSplineCurve PolesCount=4 KnotsCount=2 Degree=3 IsPeriodic=0
    g4: BSplineCurve PolesCount=4 KnotsCount=2 Degree=3 IsPeriodic=0
    g5: BSplineCurve PolesCount=4 KnotsCount=2 Degree=3 IsPeriodic=0
    g6: BSplineCurve PolesCount=2 KnotsCount=2 Degree=1 IsPeriodic=0
    g7: BSplineCurve PolesCount=2 KnotsCount=2 Degree=1 IsPeriodic=0
    g8: BSplineCurve PolesCount=4 KnotsCount=2 Degree=3 IsPeriodic=0
    g9: BSplineCurve PolesCount=4 KnotsCount=2 Degree=3 IsPeriodic=0
    g10: BSplineCurve PolesCount=2 KnotsCount=2 Degree=1 IsPeriodic=0
    g11: BSplineCurve PolesCount=2 KnotsCount=2 Degree=1 IsPeriodic=0
    g12: BSplineCurve PolesCount=2 KnotsCount=2 Degree=1 IsPeriodic=0
    g13: BSplineCurve PolesCount=2 KnotsCount=2 Degree=1 IsPeriodic=0
    g14: BSplineCurve PolesCount=4 KnotsCount=2 Degree=3 IsPeriodic=0
    g15: BSplineCurve PolesCount=4 KnotsCount=2 Degree=3 IsPeriodic=0
    g16: BSplineCurve PolesCount=2 KnotsCount=2 Degree=1 IsPeriodic=0
    g17: BSplineCurve PolesCount=2 KnotsCount=2 Degree=1 IsPeriodic=0
    g18: BSplineCurve PolesCount=4 KnotsCount=2 Degree=3 IsPeriodic=0
    g19: BSplineCurve PolesCount=2 KnotsCount=2 Degree=1 IsPeriodic=0
    g20: BSplineCurve PolesCount=2 KnotsCount=2 Degree=1 IsPeriodic=0
    g21: BSplineCurve PolesCount=4 KnotsCount=2 Degree=3 IsPeriodic=0
    g22: BSplineCurve PolesCount=4 KnotsCount=2 Degree=3 IsPeriodic=0
    g23: BSplineCurve PolesCount=4 KnotsCount=2 Degree=3 IsPeriodic=0
    g24: BSplineCurve PolesCount=4 KnotsCount=2 Degree=3 IsPeriodic=0
    g25: BSplineCurve PolesCount=4 KnotsCount=2 Degree=3 IsPeriodic=0
    g26: BSplineCurve PolesCount=4 KnotsCount=2 Degree=3 IsPeriodic=0
    g27: BSplineCurve PolesCount=4 KnotsCount=2 Degree=3 IsPeriodic=0
    g28: BSplineCurve PolesCount=4 KnotsCount=2 Degree=3 IsPeriodic=0
    g29: BSplineCurve PolesCount=4 KnotsCount=2 Degree=3 IsPeriodic=0
    g30: BSplineCurve PolesCount=4 KnotsCount=2 Degree=3 IsPeriodic=0
    g31: BSplineCurve PolesCount=4 KnotsCount=2 Degree=3 IsPeriodic=0
    g32: BSplineCurve PolesCount=4 KnotsCount=2 Degree=3 IsPeriodic=0
    g33: BSplineCurve PolesCount=4 KnotsCount=2 Degree=3 IsPeriodic=0
    g34: BSplineCurve PolesCount=4 KnotsCount=2 Degree=3 IsPeriodic=0
    g35: BSplineCurve PolesCount=4 KnotsCount=2 Degree=3 IsPeriodic=0
    g36: BSplineCurve PolesCount=4 KnotsCount=2 Degree=3 IsPeriodic=0
    g37: BSplineCurve PolesCount=4 KnotsCount=2 Degree=3 IsPeriodic=0
    g38: BSplineCurve PolesCount=4 KnotsCount=2 Degree=3 IsPeriodic=0
    g39: BSplineCurve PolesCount=4 KnotsCount=2 Degree=3 IsPeriodic=0
    g40: BSplineCurve PolesCount=2 KnotsCount=2 Degree=1 IsPeriodic=0
    g41: BSplineCurve PolesCount=2 KnotsCount=2 Degree=1 IsPeriodic=0
    g42: BSplineCurve PolesCount=4 KnotsCount=2 Degree=3 IsPeriodic=0
    g43: BSplineCurve PolesCount=2 KnotsCount=2 Degree=1 IsPeriodic=0
    g44: BSplineCurve PolesCount=2 KnotsCount=2 Degree=1 IsPeriodic=0
    g45: BSplineCurve PolesCount=4 KnotsCount=2 Degree=3 IsPeriodic=0
    g46: BSplineCurve PolesCount=4 KnotsCount=2 Degree=3 IsPeriodic=0
    g47: BSplineCurve PolesCount=2 KnotsCount=2 Degree=1 IsPeriodic=0
    g48: BSplineCurve PolesCount=2 KnotsCount=2 Degree=1 IsPeriodic=0
    g49: BSplineCurve PolesCount=4 KnotsCount=2 Degree=3 IsPeriodic=0
    g50: BSplineCurve PolesCount=4 KnotsCount=2 Degree=3 IsPeriodic=0
    g51: BSplineCurve PolesCount=4 KnotsCount=2 Degree=3 IsPeriodic=0
    g52: BSplineCurve PolesCount=4 KnotsCount=2 Degree=3 IsPeriodic=0
    g53: BSplineCurve PolesCount=4 KnotsCount=2 Degree=3 IsPeriodic=0
    g54: BSplineCurve PolesCount=4 KnotsCount=2 Degree=3 IsPeriodic=0
    g55: BSplineCurve PolesCount=4 KnotsCount=2 Degree=3 IsPeriodic=0
    g56: BSplineCurve PolesCount=4 KnotsCount=2 Degree=3 IsPeriodic=0
    g57: BSplineCurve PolesCount=4 KnotsCount=2 Degree=3 IsPeriodic=0
    g58: BSplineCurve PolesCount=4 KnotsCount=2 Degree=3 IsPeriodic=0
    g59: BSplineCurve PolesCount=4 KnotsCount=2 Degree=3 IsPeriodic=0
    g60: BSplineCurve PolesCount=4 KnotsCount=2 Degree=3 IsPeriodic=0
    g61: BSplineCurve PolesCount=4 KnotsCount=2 Degree=3 IsPeriodic=0
    g62: BSplineCurve PolesCount=4 KnotsCount=2 Degree=3 IsPeriodic=0
    g63: BSplineCurve PolesCount=4 KnotsCount=2 Degree=3 IsPeriodic=0
    g64: BSplineCurve PolesCount=4 KnotsCount=2 Degree=3 IsPeriodic=0
    g65: BSplineCurve PolesCount=4 KnotsCount=2 Degree=3 IsPeriodic=0
    g66: BSplineCurve PolesCount=2 KnotsCount=2 Degree=1 IsPeriodic=0
    g67: BSplineCurve PolesCount=4 KnotsCount=2 Degree=3 IsPeriodic=0
    g68: BSplineCurve PolesCount=4 KnotsCount=2 Degree=3 IsPeriodic=0
    g69: BSplineCurve PolesCount=4 KnotsCount=2 Degree=3 IsPeriodic=0
    g70: BSplineCurve PolesCount=4 KnotsCount=2 Degree=3 IsPeriodic=0
    g71: BSplineCurve PolesCount=4 KnotsCount=2 Degree=3 IsPeriodic=0
    g72: BSplineCurve PolesCount=4 KnotsCount=2 Degree=3 IsPeriodic=0
    g73: BSplineCurve PolesCount=4 KnotsCount=2 Degree=3 IsPeriodic=0
    g74: BSplineCurve PolesCount=4 KnotsCount=2 Degree=3 IsPeriodic=0
    g75: BSplineCurve PolesCount=4 KnotsCount=2 Degree=3 IsPeriodic=0
    g76: BSplineCurve PolesCount=4 KnotsCount=2 Degree=3 IsPeriodic=0
    g77: BSplineCurve PolesCount=4 KnotsCount=2 Degree=3 IsPeriodic=0
    g78: BSplineCurve PolesCount=2 KnotsCount=2 Degree=1 IsPeriodic=0
    g79: BSplineCurve PolesCount=2 KnotsCount=2 Degree=1 IsPeriodic=0
    g80: BSplineCurve PolesCount=4 KnotsCount=2 Degree=3 IsPeriodic=0
    g81: BSplineCurve PolesCount=4 KnotsCount=2 Degree=3 IsPeriodic=0
    g82: BSplineCurve PolesCount=4 KnotsCount=2 Degree=3 IsPeriodic=0
    g83: BSplineCurve PolesCount=4 KnotsCount=2 Degree=3 IsPeriodic=0
    g84: BSplineCurve PolesCount=4 KnotsCount=2 Degree=3 IsPeriodic=0
    g85: BSplineCurve PolesCount=4 KnotsCount=2 Degree=3 IsPeriodic=0
    g86: BSplineCurve PolesCount=4 KnotsCount=2 Degree=3 IsPeriodic=0
    g87: BSplineCurve PolesCount=4 KnotsCount=2 Degree=3 IsPeriodic=0
    g88: BSplineCurve PolesCount=4 KnotsCount=2 Degree=3 IsPeriodic=0
    g89: BSplineCurve PolesCount=4 KnotsCount=2 Degree=3 IsPeriodic=0
    g90: BSplineCurve PolesCount=4 KnotsCount=2 Degree=3 IsPeriodic=0
    g91: BSplineCurve PolesCount=4 KnotsCount=2 Degree=3 IsPeriodic=0
    g92: BSplineCurve PolesCount=4 KnotsCount=2 Degree=3 IsPeriodic=0
    g93: BSplineCurve PolesCount=4 KnotsCount=2 Degree=3 IsPeriodic=0
    g94: BSplineCurve PolesCount=4 KnotsCount=2 Degree=3 IsPeriodic=0
    g95: BSplineCurve PolesCount=4 KnotsCount=2 Degree=3 IsPeriodic=0
    g96: BSplineCurve PolesCount=4 KnotsCount=2 Degree=3 IsPeriodic=0
    g97: BSplineCurve PolesCount=4 KnotsCount=2 Degree=3 IsPeriodic=0
    g98: BSplineCurve PolesCount=4 KnotsCount=2 Degree=3 IsPeriodic=0
    g99: BSplineCurve PolesCount=4 KnotsCount=2 Degree=3 IsPeriodic=0
    g100: BSplineCurve PolesCount=4 KnotsCount=2 Degree=3 IsPeriodic=0
    g101: BSplineCurve PolesCount=4 KnotsCount=2 Degree=3 IsPeriodic=0
    g102: BSplineCurve PolesCount=2 KnotsCount=2 Degree=1 IsPeriodic=0
    g103: BSplineCurve PolesCount=2 KnotsCount=2 Degree=1 IsPeriodic=0
    g104: BSplineCurve PolesCount=2 KnotsCount=2 Degree=1 IsPeriodic=0
    g105: BSplineCurve PolesCount=4 KnotsCount=2 Degree=3 IsPeriodic=0
    g106: BSplineCurve PolesCount=4 KnotsCount=2 Degree=3 IsPeriodic=0
    g107: BSplineCurve PolesCount=4 KnotsCount=2 Degree=3 IsPeriodic=0
    g108: BSplineCurve PolesCount=4 KnotsCount=2 Degree=3 IsPeriodic=0
    g109: BSplineCurve PolesCount=4 KnotsCount=2 Degree=3 IsPeriodic=0
    g110: BSplineCurve PolesCount=4 KnotsCount=2 Degree=3 IsPeriodic=0
    g111: BSplineCurve PolesCount=4 KnotsCount=2 Degree=3 IsPeriodic=0
    g112: BSplineCurve PolesCount=4 KnotsCount=2 Degree=3 IsPeriodic=0
    g113: BSplineCurve PolesCount=2 KnotsCount=2 Degree=1 IsPeriodic=0
    g114: BSplineCurve PolesCount=2 KnotsCount=2 Degree=1 IsPeriodic=0
    g115: BSplineCurve PolesCount=4 KnotsCount=2 Degree=3 IsPeriodic=0
    g116: BSplineCurve PolesCount=4 KnotsCount=2 Degree=3 IsPeriodic=0
    g117: BSplineCurve PolesCount=4 KnotsCount=2 Degree=3 IsPeriodic=0
    g118: BSplineCurve PolesCount=4 KnotsCount=2 Degree=3 IsPeriodic=0
    g119: BSplineCurve PolesCount=4 KnotsCount=2 Degree=3 IsPeriodic=0
    g120: BSplineCurve PolesCount=4 KnotsCount=2 Degree=3 IsPeriodic=0
    g121: BSplineCurve PolesCount=4 KnotsCount=2 Degree=3 IsPeriodic=0
    g122: BSplineCurve PolesCount=4 KnotsCount=2 Degree=3 IsPeriodic=0
    g123: BSplineCurve PolesCount=2 KnotsCount=2 Degree=1 IsPeriodic=0
    g124: BSplineCurve PolesCount=2 KnotsCount=2 Degree=1 IsPeriodic=0
    g125: BSplineCurve PolesCount=4 KnotsCount=2 Degree=3 IsPeriodic=0
    g126: BSplineCurve PolesCount=4 KnotsCount=2 Degree=3 IsPeriodic=0
    g127: BSplineCurve PolesCount=4 KnotsCount=2 Degree=3 IsPeriodic=0
    g128: BSplineCurve PolesCount=4 KnotsCount=2 Degree=3 IsPeriodic=0
    g129: BSplineCurve PolesCount=4 KnotsCount=2 Degree=3 IsPeriodic=0
    g130: BSplineCurve PolesCount=4 KnotsCount=2 Degree=3 IsPeriodic=0
    g131: BSplineCurve PolesCount=4 KnotsCount=2 Degree=3 IsPeriodic=0
    g132: BSplineCurve PolesCount=4 KnotsCount=2 Degree=3 IsPeriodic=0
    g133: BSplineCurve PolesCount=4 KnotsCount=2 Degree=3 IsPeriodic=0
    g134: BSplineCurve PolesCount=4 KnotsCount=2 Degree=3 IsPeriodic=0
    g135: BSplineCurve PolesCount=2 KnotsCount=2 Degree=1 IsPeriodic=0
    g136: BSplineCurve PolesCount=2 KnotsCount=2 Degree=1 IsPeriodic=0
    g137: BSplineCurve PolesCount=4 KnotsCount=2 Degree=3 IsPeriodic=0
    g138: BSplineCurve PolesCount=4 KnotsCount=2 Degree=3 IsPeriodic=0
    g139: BSplineCurve PolesCount=4 KnotsCount=2 Degree=3 IsPeriodic=0
    g140: BSplineCurve PolesCount=4 KnotsCount=2 Degree=3 IsPeriodic=0
    g141: BSplineCurve PolesCount=4 KnotsCount=2 Degree=3 IsPeriodic=0
    g142: BSplineCurve PolesCount=4 KnotsCount=2 Degree=3 IsPeriodic=0
    g143: BSplineCurve PolesCount=4 KnotsCount=2 Degree=3 IsPeriodic=0
    g144: BSplineCurve PolesCount=4 KnotsCount=2 Degree=3 IsPeriodic=0
    g145: BSplineCurve PolesCount=4 KnotsCount=2 Degree=3 IsPeriodic=0
    g146: BSplineCurve PolesCount=4 KnotsCount=2 Degree=3 IsPeriodic=0
    g147: BSplineCurve PolesCount=4 KnotsCount=2 Degree=3 IsPeriodic=0
    g148: BSplineCurve PolesCount=4 KnotsCount=2 Degree=3 IsPeriodic=0
    g149: BSplineCurve PolesCount=2 KnotsCount=2 Degree=1 IsPeriodic=0
    g150: BSplineCurve PolesCount=2 KnotsCount=2 Degree=1 IsPeriodic=0
    g151: BSplineCurve PolesCount=4 KnotsCount=2 Degree=3 IsPeriodic=0
    g152: BSplineCurve PolesCount=4 KnotsCount=2 Degree=3 IsPeriodic=0
    g153: BSplineCurve PolesCount=4 KnotsCount=2 Degree=3 IsPeriodic=0
    g154: BSplineCurve PolesCount=2 KnotsCount=2 Degree=1 IsPeriodic=0
    g155: BSplineCurve PolesCount=2 KnotsCount=2 Degree=1 IsPeriodic=0
    g156: BSplineCurve PolesCount=4 KnotsCount=2 Degree=3 IsPeriodic=0
    g157: BSplineCurve PolesCount=4 KnotsCount=2 Degree=3 IsPeriodic=0
    g158: BSplineCurve PolesCount=4 KnotsCount=2 Degree=3 IsPeriodic=0
    g159: BSplineCurve PolesCount=4 KnotsCount=2 Degree=3 IsPeriodic=0
    g160: BSplineCurve PolesCount=4 KnotsCount=2 Degree=3 IsPeriodic=0
    g161: BSplineCurve PolesCount=4 KnotsCount=2 Degree=3 IsPeriodic=0
    g162: BSplineCurve PolesCount=4 KnotsCount=2 Degree=3 IsPeriodic=0
    g163: BSplineCurve PolesCount=4 KnotsCount=2 Degree=3 IsPeriodic=0
    g164: BSplineCurve PolesCount=2 KnotsCount=2 Degree=1 IsPeriodic=0
    g165: BSplineCurve PolesCount=2 KnotsCount=2 Degree=1 IsPeriodic=0
    g166: BSplineCurve PolesCount=2 KnotsCount=2 Degree=1 IsPeriodic=0
    g167: BSplineCurve PolesCount=4 KnotsCount=2 Degree=3 IsPeriodic=0
    g168: BSplineCurve PolesCount=4 KnotsCount=2 Degree=3 IsPeriodic=0
    g169: BSplineCurve PolesCount=4 KnotsCount=2 Degree=3 IsPeriodic=0
    g170: BSplineCurve PolesCount=4 KnotsCount=2 Degree=3 IsPeriodic=0
    g171: BSplineCurve PolesCount=4 KnotsCount=2 Degree=3 IsPeriodic=0
    g172: BSplineCurve PolesCount=4 KnotsCount=2 Degree=3 IsPeriodic=0
    g173: BSplineCurve PolesCount=4 KnotsCount=2 Degree=3 IsPeriodic=0
    g174: BSplineCurve PolesCount=4 KnotsCount=2 Degree=3 IsPeriodic=0
    g175: BSplineCurve PolesCount=4 KnotsCount=2 Degree=3 IsPeriodic=0
    g176: BSplineCurve PolesCount=4 KnotsCount=2 Degree=3 IsPeriodic=0
    g177: BSplineCurve PolesCount=4 KnotsCount=2 Degree=3 IsPeriodic=0
    g178: BSplineCurve PolesCount=4 KnotsCount=2 Degree=3 IsPeriodic=0
    g179: BSplineCurve PolesCount=4 KnotsCount=2 Degree=3 IsPeriodic=0
    g180: BSplineCurve PolesCount=4 KnotsCount=2 Degree=3 IsPeriodic=0
    g181: BSplineCurve PolesCount=4 KnotsCount=2 Degree=3 IsPeriodic=0
    g182: BSplineCurve PolesCount=4 KnotsCount=2 Degree=3 IsPeriodic=0
    g183: BSplineCurve PolesCount=4 KnotsCount=2 Degree=3 IsPeriodic=0
    g184: BSplineCurve PolesCount=4 KnotsCount=2 Degree=3 IsPeriodic=0
    g185: BSplineCurve PolesCount=4 KnotsCount=2 Degree=3 IsPeriodic=0
    g186: BSplineCurve PolesCount=4 KnotsCount=2 Degree=3 IsPeriodic=0
    g187: BSplineCurve PolesCount=4 KnotsCount=2 Degree=3 IsPeriodic=0
    g188: BSplineCurve PolesCount=4 KnotsCount=2 Degree=3 IsPeriodic=0
    g189: BSplineCurve PolesCount=4 KnotsCount=2 Degree=3 IsPeriodic=0
    g190: BSplineCurve PolesCount=4 KnotsCount=2 Degree=3 IsPeriodic=0
    g191: BSplineCurve PolesCount=4 KnotsCount=2 Degree=3 IsPeriodic=0
    g192: BSplineCurve PolesCount=4 KnotsCount=2 Degree=3 IsPeriodic=0
    g193: BSplineCurve PolesCount=4 KnotsCount=2 Degree=3 IsPeriodic=0
    g194: BSplineCurve PolesCount=4 KnotsCount=2 Degree=3 IsPeriodic=0
    g195: BSplineCurve PolesCount=4 KnotsCount=2 Degree=3 IsPeriodic=0
    g196: BSplineCurve PolesCount=2 KnotsCount=2 Degree=1 IsPeriodic=0
    g197: BSplineCurve PolesCount=4 KnotsCount=2 Degree=3 IsPeriodic=0
    g198: BSplineCurve PolesCount=2 KnotsCount=2 Degree=1 IsPeriodic=0
    g199: BSplineCurve PolesCount=2 KnotsCount=2 Degree=1 IsPeriodic=0
    g200: BSplineCurve PolesCount=4 KnotsCount=2 Degree=3 IsPeriodic=0
    g201: BSplineCurve PolesCount=4 KnotsCount=2 Degree=3 IsPeriodic=0
    g202: BSplineCurve PolesCount=4 KnotsCount=2 Degree=3 IsPeriodic=0
    g203: BSplineCurve PolesCount=4 KnotsCount=2 Degree=3 IsPeriodic=0
    g204: BSplineCurve PolesCount=4 KnotsCount=2 Degree=3 IsPeriodic=0
    g205: BSplineCurve PolesCount=4 KnotsCount=2 Degree=3 IsPeriodic=0
    g206: BSplineCurve PolesCount=4 KnotsCount=2 Degree=3 IsPeriodic=0
    g207: BSplineCurve PolesCount=2 KnotsCount=2 Degree=1 IsPeriodic=0
    g208: BSplineCurve PolesCount=4 KnotsCount=2 Degree=3 IsPeriodic=0
    g209: BSplineCurve PolesCount=4 KnotsCount=2 Degree=3 IsPeriodic=0
    g210: BSplineCurve PolesCount=4 KnotsCount=2 Degree=3 IsPeriodic=0
    g211: BSplineCurve PolesCount=4 KnotsCount=2 Degree=3 IsPeriodic=0
    g212: BSplineCurve PolesCount=4 KnotsCount=2 Degree=3 IsPeriodic=0
    g213: BSplineCurve PolesCount=4 KnotsCount=2 Degree=3 IsPeriodic=0
    g214: BSplineCurve PolesCount=4 KnotsCount=2 Degree=3 IsPeriodic=0
    g215: BSplineCurve PolesCount=4 KnotsCount=2 Degree=3 IsPeriodic=0
    g216: BSplineCurve PolesCount=4 KnotsCount=2 Degree=3 IsPeriodic=0
    g217: BSplineCurve PolesCount=4 KnotsCount=2 Degree=3 IsPeriodic=0
    g218: BSplineCurve PolesCount=4 KnotsCount=2 Degree=3 IsPeriodic=0
    g219: BSplineCurve PolesCount=4 KnotsCount=2 Degree=3 IsPeriodic=0
    g220: BSplineCurve PolesCount=4 KnotsCount=2 Degree=3 IsPeriodic=0
    g221: BSplineCurve PolesCount=2 KnotsCount=2 Degree=1 IsPeriodic=0
    g222: BSplineCurve PolesCount=2 KnotsCount=2 Degree=1 IsPeriodic=0
    g223: BSplineCurve PolesCount=2 KnotsCount=2 Degree=1 IsPeriodic=0
    g224: BSplineCurve PolesCount=4 KnotsCount=2 Degree=3 IsPeriodic=0
    g225: BSplineCurve PolesCount=4 KnotsCount=2 Degree=3 IsPeriodic=0
    g226: BSplineCurve PolesCount=4 KnotsCount=2 Degree=3 IsPeriodic=0
    g227: BSplineCurve PolesCount=2 KnotsCount=2 Degree=1 IsPeriodic=0
    g228: BSplineCurve PolesCount=2 KnotsCount=2 Degree=1 IsPeriodic=0
    g229: BSplineCurve PolesCount=4 KnotsCount=2 Degree=3 IsPeriodic=0
    g230: BSplineCurve PolesCount=4 KnotsCount=2 Degree=3 IsPeriodic=0
    g231: BSplineCurve PolesCount=4 KnotsCount=2 Degree=3 IsPeriodic=0
    g232: BSplineCurve PolesCount=4 KnotsCount=2 Degree=3 IsPeriodic=0
    g233: BSplineCurve PolesCount=4 KnotsCount=2 Degree=3 IsPeriodic=0
    g234: BSplineCurve PolesCount=4 KnotsCount=2 Degree=3 IsPeriodic=0
    g235: BSplineCurve PolesCount=4 KnotsCount=2 Degree=3 IsPeriodic=0
    g236: BSplineCurve PolesCount=4 KnotsCount=2 Degree=3 IsPeriodic=0
    g237: BSplineCurve PolesCount=4 KnotsCount=2 Degree=3 IsPeriodic=0
    g238: BSplineCurve PolesCount=4 KnotsCount=2 Degree=3 IsPeriodic=0
    g239: BSplineCurve PolesCount=4 KnotsCount=2 Degree=3 IsPeriodic=0
    g240: BSplineCurve PolesCount=4 KnotsCount=2 Degree=3 IsPeriodic=0
    g241: BSplineCurve PolesCount=4 KnotsCount=2 Degree=3 IsPeriodic=0
    g242: BSplineCurve PolesCount=4 KnotsCount=2 Degree=3 IsPeriodic=0
    g243: BSplineCurve PolesCount=4 KnotsCount=2 Degree=3 IsPeriodic=0
    g244: BSplineCurve PolesCount=4 KnotsCount=2 Degree=3 IsPeriodic=0
    g245: BSplineCurve PolesCount=4 KnotsCount=2 Degree=3 IsPeriodic=0
    g246: BSplineCurve PolesCount=4 KnotsCount=2 Degree=3 IsPeriodic=0
    g247: BSplineCurve PolesCount=4 KnotsCount=2 Degree=3 IsPeriodic=0
    g248: BSplineCurve PolesCount=4 KnotsCount=2 Degree=3 IsPeriodic=0
    g249: BSplineCurve PolesCount=4 KnotsCount=2 Degree=3 IsPeriodic=0
    g250: BSplineCurve PolesCount=4 KnotsCount=2 Degree=3 IsPeriodic=0
    g251: BSplineCurve PolesCount=4 KnotsCount=2 Degree=3 IsPeriodic=0
    g252: BSplineCurve PolesCount=4 KnotsCount=2 Degree=3 IsPeriodic=0
    g253: BSplineCurve PolesCount=4 KnotsCount=2 Degree=3 IsPeriodic=0
    g254: BSplineCurve PolesCount=4 KnotsCount=2 Degree=3 IsPeriodic=0
    g255: BSplineCurve PolesCount=4 KnotsCount=2 Degree=3 IsPeriodic=0
    g256: BSplineCurve PolesCount=4 KnotsCount=2 Degree=3 IsPeriodic=0
    g257: BSplineCurve PolesCount=4 KnotsCount=2 Degree=3 IsPeriodic=0
    g258: BSplineCurve PolesCount=4 KnotsCount=2 Degree=3 IsPeriodic=0
    g259: BSplineCurve PolesCount=4 KnotsCount=2 Degree=3 IsPeriodic=0
    g260: BSplineCurve PolesCount=4 KnotsCount=2 Degree=3 IsPeriodic=0
    g261: BSplineCurve PolesCount=4 KnotsCount=2 Degree=3 IsPeriodic=0
    g262: BSplineCurve PolesCount=4 KnotsCount=2 Degree=3 IsPeriodic=0
    g263: BSplineCurve PolesCount=2 KnotsCount=2 Degree=1 IsPeriodic=0
    g264: BSplineCurve PolesCount=4 KnotsCount=2 Degree=3 IsPeriodic=0
    g265: BSplineCurve PolesCount=4 KnotsCount=2 Degree=3 IsPeriodic=0
    g266: BSplineCurve PolesCount=4 KnotsCount=2 Degree=3 IsPeriodic=0
    g267: BSplineCurve PolesCount=4 KnotsCount=2 Degree=3 IsPeriodic=0
    g268: BSplineCurve PolesCount=4 KnotsCount=2 Degree=3 IsPeriodic=0
    g269: BSplineCurve PolesCount=4 KnotsCount=2 Degree=3 IsPeriodic=0
    g270: BSplineCurve PolesCount=4 KnotsCount=2 Degree=3 IsPeriodic=0
    g271: BSplineCurve PolesCount=4 KnotsCount=2 Degree=3 IsPeriodic=0
    g272: BSplineCurve PolesCount=4 KnotsCount=2 Degree=3 IsPeriodic=0
    g273: BSplineCurve PolesCount=4 KnotsCount=2 Degree=3 IsPeriodic=0
    g274: BSplineCurve PolesCount=4 KnotsCount=2 Degree=3 IsPeriodic=0
    g275: BSplineCurve PolesCount=4 KnotsCount=2 Degree=3 IsPeriodic=0
    g276: BSplineCurve PolesCount=4 KnotsCount=2 Degree=3 IsPeriodic=0
    g277: BSplineCurve PolesCount=4 KnotsCount=2 Degree=3 IsPeriodic=0
    g278: BSplineCurve PolesCount=4 KnotsCount=2 Degree=3 IsPeriodic=0
    g279: BSplineCurve PolesCount=4 KnotsCount=2 Degree=3 IsPeriodic=0
    g280: BSplineCurve PolesCount=4 KnotsCount=2 Degree=3 IsPeriodic=0
    g281: BSplineCurve PolesCount=4 KnotsCount=2 Degree=3 IsPeriodic=0
    g282: BSplineCurve PolesCount=4 KnotsCount=2 Degree=3 IsPeriodic=0
    g283: BSplineCurve PolesCount=4 KnotsCount=2 Degree=3 IsPeriodic=0
    g284: BSplineCurve PolesCount=4 KnotsCount=2 Degree=3 IsPeriodic=0
    g285: BSplineCurve PolesCount=4 KnotsCount=2 Degree=3 IsPeriodic=0
    g286: BSplineCurve PolesCount=4 KnotsCount=2 Degree=3 IsPeriodic=0
    g287: BSplineCurve PolesCount=4 KnotsCount=2 Degree=3 IsPeriodic=0
    g288: BSplineCurve PolesCount=4 KnotsCount=2 Degree=3 IsPeriodic=0
    g289: BSplineCurve PolesCount=4 KnotsCount=2 Degree=3 IsPeriodic=0
    g290: BSplineCurve PolesCount=4 KnotsCount=2 Degree=3 IsPeriodic=0
    g291: BSplineCurve PolesCount=4 KnotsCount=2 Degree=3 IsPeriodic=0
    g292: BSplineCurve PolesCount=2 KnotsCount=2 Degree=1 IsPeriodic=0
    g293: BSplineCurve PolesCount=4 KnotsCount=2 Degree=3 IsPeriodic=0
    g294: BSplineCurve PolesCount=4 KnotsCount=2 Degree=3 IsPeriodic=0
    g295: BSplineCurve PolesCount=4 KnotsCount=2 Degree=3 IsPeriodic=0
    g296: BSplineCurve PolesCount=2 KnotsCount=2 Degree=1 IsPeriodic=0
    g297: BSplineCurve PolesCount=4 KnotsCount=2 Degree=3 IsPeriodic=0
    g298: BSplineCurve PolesCount=4 KnotsCount=2 Degree=3 IsPeriodic=0
    g299: BSplineCurve PolesCount=4 KnotsCount=2 Degree=3 IsPeriodic=0
    g300: BSplineCurve PolesCount=2 KnotsCount=2 Degree=1 IsPeriodic=0
    g301: BSplineCurve PolesCount=4 KnotsCount=2 Degree=3 IsPeriodic=0
    g302: BSplineCurve PolesCount=4 KnotsCount=2 Degree=3 IsPeriodic=0
    g303: BSplineCurve PolesCount=4 KnotsCount=2 Degree=3 IsPeriodic=0
    g304: BSplineCurve PolesCount=2 KnotsCount=2 Degree=1 IsPeriodic=0
    g305: BSplineCurve PolesCount=4 KnotsCount=2 Degree=3 IsPeriodic=0
    g306: BSplineCurve PolesCount=4 KnotsCount=2 Degree=3 IsPeriodic=0
    g307: BSplineCurve PolesCount=4 KnotsCount=2 Degree=3 IsPeriodic=0
    g308: BSplineCurve PolesCount=2 KnotsCount=2 Degree=1 IsPeriodic=0
    g309: BSplineCurve PolesCount=4 KnotsCount=2 Degree=3 IsPeriodic=0
    g310: BSplineCurve PolesCount=4 KnotsCount=2 Degree=3 IsPeriodic=0
    g311: BSplineCurve PolesCount=4 KnotsCount=2 Degree=3 IsPeriodic=0
    g312: BSplineCurve PolesCount=4 KnotsCount=2 Degree=3 IsPeriodic=0
    g313: BSplineCurve PolesCount=4 KnotsCount=2 Degree=3 IsPeriodic=0
    g314: BSplineCurve PolesCount=4 KnotsCount=2 Degree=3 IsPeriodic=0
    g315: BSplineCurve PolesCount=4 KnotsCount=2 Degree=3 IsPeriodic=0
    g316: BSplineCurve PolesCount=4 KnotsCount=2 Degree=3 IsPeriodic=0
    g317: BSplineCurve PolesCount=4 KnotsCount=2 Degree=3 IsPeriodic=0
    g318: BSplineCurve PolesCount=4 KnotsCount=2 Degree=3 IsPeriodic=0
    g319: BSplineCurve PolesCount=4 KnotsCount=2 Degree=3 IsPeriodic=0
    g320: BSplineCurve PolesCount=4 KnotsCount=2 Degree=3 IsPeriodic=0
    g321: BSplineCurve PolesCount=4 KnotsCount=2 Degree=3 IsPeriodic=0
    g322: BSplineCurve PolesCount=4 KnotsCount=2 Degree=3 IsPeriodic=0
    g323: BSplineCurve PolesCount=4 KnotsCount=2 Degree=3 IsPeriodic=0
    g324: BSplineCurve PolesCount=4 KnotsCount=2 Degree=3 IsPeriodic=0
    g325: BSplineCurve PolesCount=4 KnotsCount=2 Degree=3 IsPeriodic=0
    g326: BSplineCurve PolesCount=4 KnotsCount=2 Degree=3 IsPeriodic=0
    g327: BSplineCurve PolesCount=4 KnotsCount=2 Degree=3 IsPeriodic=0
    g328: BSplineCurve PolesCount=4 KnotsCount=2 Degree=3 IsPeriodic=0
    g329: BSplineCurve PolesCount=4 KnotsCount=2 Degree=3 IsPeriodic=0
  constraints (340):
    c: Coincident(g0,g1)
    c: Coincident(g1,g2)
    c: Coincident(g2,g3)
    c: Coincident(g3,g4)
    c: Coincident(g4,g5)
    c: Coincident(g5,g6)
    c: Coincident(g6,g7)
    c: Coincident(g7,g8)
    c: Coincident(g8,g9)
    c: Coincident(g9,g10)
    c: Coincident(g10,g11)
    c: Coincident(g11,g12)
    c: Coincident(g12,g13)
    c: Coincident(g13,g14)
    c: Coincident(g14,g15)
    c: Coincident(g15,g16)
    c: Coincident(g16,g17)
    c: Coincident(g17,g18)
    c: Coincident(g18,g19)
    c: Coincident(g19,g20)
    c: Coincident(g20,g21)
    c: Coincident(g21,g22)
    c: Coincident(g22,g23)
    c: Coincident(g23,g24)
    c: Coincident(g24,g25)
    c: Coincident(g25,g26)
    c: Coincident(g26,g27)
    c: Coincident(g27,g28)
    c: Coincident(g28,g29)
    c: Coincident(g29,g30)
    c: Coincident(g30,g31)
    c: Coincident(g31,g32)
    c: Coincident(g32,g33)
    c: Coincident(g33,g34)
    c: Coincident(g34,g35)
    c: Coincident(g35,g36)
    c: Coincident(g36,g37)
    c: Coincident(g37,g38)
    c: Coincident(g38,g39)
    c: Coincident(g39,g40)
    c: Coincident(g40,g41)
    c: Coincident(g41,g42)
    c: Coincident(g42,g43)
    c: Coincident(g43,g44)
    c: Coincident(g44,g45)
    c: Coincident(g45,g46)
    c: Coincident(g46,g47)
    c: Coincident(g47,g48)
    c: Coincident(g48,g49)
    c: Coincident(g49,g50)
    c: Coincident(g50,g51)
    c: Coincident(g51,g52)
    c: Coincident(g52,g53)
    c: Coincident(g53,g54)
    c: Coincident(g54,g55)
    c: Coincident(g55,g56)
    c: Coincident(g56,g57)
    c: Coincident(g57,g0)
    c: Coincident(g58,g59)
    c: Coincident(g59,g60)
    c: Coincident(g60,g61)
    c: Coincident(g61,g62)
    c: Coincident(g62,g63)
    c: Coincident(g63,g64)
    c: Coincident(g64,g65)
    c: Coincident(g65,g58)
    c: Coincident(g66,g67)
    c: Coincident(g67,g68)
    c: Coincident(g68,g69)
    c: Coincident(g69,g70)
    c: Coincident(g70,g71)
    c: Coincident(g71,g72)
    c: Coincident(g72,g73)
    c: Coincident(g73,g74)
    c: Coincident(g74,g75)
    c: Coincident(g75,g76)
    c: Coincident(g76,g77)
    c: Coincident(g77,g78)
    c: Coincident(g78,g79)
    c: Coincident(g79,g80)
    c: Coincident(g80,g66)
    c: Coincident(g81,g82)
    c: Coincident(g82,g83)
    c: Coincident(g83,g84)
    c: Coincident(g84,g81)
    c: Coincident(g85,g86)
    c: Coincident(g86,g87)
    c: Coincident(g87,g88)
    c: Coincident(g88,g89)
    c: Coincident(g89,g90)
    c: Coincident(g90,g85)
    c: Coincident(g91,g92)
    c: Coincident(g92,g93)
    c: Coincident(g93,g94)
    c: Coincident(g94,g95)
    c: Coincident(g95,g96)
    c: Coincident(g96,g97)
    c: Coincident(g97,g98)
    c: Coincident(g98,g91)
    c: Coincident(g99,g100)
    c: Coincident(g100,g101)
    c: Coincident(g101,g102)
    c: Coincident(g102,g103)
    c: Coincident(g103,g99)
    c: Coincident(g104,g105)
    c: Coincident(g105,g106)
    c: Coincident(g106,g107)
    c: Coincident(g107,g108)
    c: Coincident(g108,g109)
    c: Coincident(g109,g110)
    c: Coincident(g110,g111)
    c: Coincident(g111,g112)
    c: Coincident(g112,g113)
    c: Coincident(g113,g114)
    c: Coincident(g114,g115)
    c: Coincident(g115,g116)
    c: Coincident(g116,g117)
    c: Coincident(g117,g118)
    c: Coincident(g118,g119)
    c: Coincident(g119,g120)
    c: Coincident(g120,g121)
    c: Coincident(g121,g122)
    c: Coincident(g122,g123)
    c: Coincident(g123,g124)
    c: Coincident(g124,g125)
    c: Coincident(g125,g126)
    c: Coincident(g126,g127)
    c: Coincident(g127,g104)
    c: Coincident(g128,g129)
    c: Coincident(g129,g130)
    c: Coincident(g130,g131)
    c: Coincident(g131,g132)
    c: Coincident(g132,g133)
    c: Coincident(g133,g134)
    c: Coincident(g134,g135)
    c: Coincident(g135,g136)
    c: Coincident(g136,g137)
    c: Coincident(g137,g138)
    c: Coincident(g138,g139)
    c: Coincident(g139,g140)
    c: Coincident(g140,g141)
    c: Coincident(g141,g142)
    c: Coincident(g142,g143)
    c: Coincident(g143,g144)
    c: Coincident(g144,g145)
    c: Coincident(g145,g128)
    c: Coincident(g146,g147)
    c: Coincident(g147,g148)
    c: Coincident(g148,g149)
    c: Coincident(g149,g150)
    c: Coincident(g150,g151)
    c: Coincident(g151,g152)
    c: Coincident(g152,g153)
    c: Coincident(g153,g154)
    c: Coincident(g154,g155)
    c: Coincident(g155,g156)
    c: Coincident(g156,g157)
    c: Coincident(g157,g158)
    c: Coincident(g158,g159)
    c: Coincident(g159,g160)
    c: Coincident(g160,g161)
    c: Coincident(g161,g162)
    c: Coincident(g162,g163)
    c: Coincident(g163,g164)
    c: Coincident(g164,g165)
    c: Coincident(g165,g146)
    c: Coincident(g166,g167)
    c: Coincident(g167,g168)
    c: Coincident(g168,g169)
    c: Coincident(g169,g170)
    c: Coincident(g170,g171)
    c: Coincident(g171,g172)
    c: Coincident(g172,g173)
    c: Coincident(g173,g174)
    c: Coincident(g174,g175)
    c: Coincident(g175,g176)
    c: Coincident(g176,g177)
    c: Coincident(g177,g178)
    c: Coincident(g178,g179)
    c: Coincident(g179,g180)
    c: Coincident(g180,g181)
    c: Coincident(g181,g182)
    c: Coincident(g182,g183)
    c: Coincident(g183,g184)
    c: Coincident(g184,g185)
    c: Coincident(g185,g186)
    c: Coincident(g186,g187)
    c: Coincident(g187,g188)
    c: Coincident(g188,g189)
    c: Coincident(g189,g190)
    c: Coincident(g190,g191)
    c: Coincident(g191,g192)
    c: Coincident(g192,g193)
    c: Coincident(g193,g194)
    c: Coincident(g194,g195)
    c: Coincident(g195,g166)
    c: Coincident(g196,g197)
    c: Coincident(g197,g198)
    c: Coincident(g198,g199)
    c: Coincident(g199,g200)
    c: Coincident(g200,g201)
    c: Coincident(g201,g202)
    c: Coincident(g202,g203)
    c: Coincident(g203,g204)
    c: Coincident(g204,g205)
    c: Coincident(g205,g206)
    c: Coincident(g206,g207)
    c: Coincident(g207,g196)
    c: Coincident(g208,g209)
    c: Coincident(g209,g210)
    c: Coincident(g210,g211)
    c: Coincident(g211,g212)
    c: Coincident(g212,g213)
    c: Coincident(g213,g214)
    c: Coincident(g214,g215)
    c: Coincident(g215,g216)
    c: Coincident(g216,g217)
    c: Coincident(g217,g218)
    c: Coincident(g218,g219)
    c: Coincident(g219,g220)
    c: Coincident(g220,g208)
    c: Coincident(g221,g222)
    c: Coincident(g222,g223)
    c: Coincident(g223,g224)
    c: Coincident(g224,g225)
    c: Coincident(g225,g226)
    c: Coincident(g226,g227)
    c: Coincident(g227,g228)
    c: Coincident(g228,g229)
    c: Coincident(g229,g230)
    c: Coincident(g230,g231)
    c: Coincident(g231,g232)
    c: Coincident(g232,g233)
    c: Coincident(g233,g234)
    c: Coincident(g234,g235)
    c: Coincident(g235,g236)
    c: Coincident(g236,g237)
    c: Coincident(g237,g238)
    c: Coincident(g238,g239)
    c: Coincident(g239,g221)
    c: Coincident(g240,g241)
    c: Coincident(g241,g242)
    c: Coincident(g242,g243)
    c: Coincident(g243,g240)
    c: Coincident(g244,g245)
    c: Coincident(g245,g246)
    c: Coincident(g246,g244)
    c: Coincident(g247,g248)
    c: Coincident(g248,g249)
    c: Coincident(g249,g247)
    c: Coincident(g250,g251)
    c: Coincident(g251,g252)
    c: Coincident(g252,g250)
    c: Coincident(g253,g254)
    c: Coincident(g254,g255)
    c: Coincident(g255,g253)
    c: Coincident(g256,g257)
    c: Coincident(g257,g258)
    c: Coincident(g258,g256)
    c: Coincident(g259,g260)
    c: Coincident(g260,g261)
    c: Coincident(g261,g259)
    c: Coincident(g262,g263)
    c: Coincident(g263,g264)
    c: Coincident(g264,g265)
    c: Coincident(g265,g262)
    c: Coincident(g266,g267)
    c: Coincident(g267,g268)
    c: Coincident(g268,g266)
    c: Coincident(g269,g270)
    c: Coincident(g270,g271)
    c: Coincident(g271,g269)
    c: Coincident(g272,g273)
    c: Coincident(g273,g274)
    c: Coincident(g274,g275)
    c: Coincident(g275,g276)
    c: Coincident(g276,g277)
    c: Coincident(g277,g272)
    c: Coincident(g278,g279)
    c: Coincident(g279,g280)
    c: Coincident(g280,g281)
    c: Coincident(g281,g278)
    c: Coincident(g282,g283)
    c: Coincident(g283,g284)
    c: Coincident(g284,g282)
    c: Coincident(g285,g286)
    c: Coincident(g286,g287)
    c: Coincident(g287,g285)
    c: Coincident(g288,g289)
    c: Coincident(g289,g290)
    c: Coincident(g290,g288)
    c: Coincident(g291,g292)
    c: Coincident(g292,g293)
    c: Coincident(g293,g294)
    c: Coincident(g294,g291)
    c: Coincident(g295,g296)
    c: Coincident(g296,g297)
    c: Coincident(g297,g298)
    c: Coincident(g298,g295)
    c: Coincident(g299,g300)
    c: Coincident(g300,g301)
    c: Coincident(g301,g302)
    c: Coincident(g302,g299)
    c: Coincident(g303,g304)
    c: Coincident(g304,g305)
    c: Coincident(g305,g306)
    c: Coincident(g306,g303)
    c: Coincident(g307,g308)
    c: Coincident(g308,g309)
    c: Coincident(g309,g310)
    c: Coincident(g310,g307)
    c: Coincident(g311,g312)
    c: Coincident(g312,g313)
    c: Coincident(g313,g314)
    c: Coincident(g314,g311)
    c: Coincident(g315,g316)
    c: Coincident(g316,g317)
    c: Coincident(g317,g315)
    c: Coincident(g318,g319)
    c: Coincident(g319,g320)
    c: Coincident(g320,g318)
    c: Coincident(g321,g322)
    c: Coincident(g322,g323)
    c: Coincident(g323,g321)
    c: Coincident(g324,g325)
    c: Coincident(g325,g326)
    c: Coincident(g326,g324)
    c: Coincident(g327,g328)
    c: Coincident(g328,g329)
    c: Coincident(g329,g327)
    c: Coincident(g221,g221)
    c: Coincident(g291,g292)
    c: Coincident(g166,g166)
    c: Coincident(g295,g296)
    c: Coincident(g303,g304)
    c: Coincident(g262,g263)
    c: Coincident(g299,g300)
    c: Coincident(g307,g308)
    c: Coincident(g104,g104)
    c: Coincident(g66,g66)
FEATURE [Sketcher::SketchObject] Sketch035  label="Juggler-Sketch"
  ArcFitTolerance = 1e-06
  FullyConstrained = false
  MakeInternals = false
  Placement = pos=(-15.2206,11.3391,0) rot=(0,0,1;0rad)
  expr: .Placement.Base.x = -(.Shape.BoundBox.XLength / 2)
  expr: .Placement.Base.y = .Shape.BoundBox.YLength / 2
  sketch-geometry (231):
    g0: BSplineCurve PolesCount=4 KnotsCount=2 Degree=3 IsPeriodic=0
    g1: BSplineCurve PolesCount=4 KnotsCount=2 Degree=3 IsPeriodic=0
    g2: BSplineCurve PolesCount=4 KnotsCount=2 Degree=3 IsPeriodic=0
    g3: BSplineCurve PolesCount=4 KnotsCount=2 Degree=3 IsPeriodic=0
    g4: BSplineCurve PolesCount=4 KnotsCount=2 Degree=3 IsPeriodic=0
    g5: BSplineCurve PolesCount=4 KnotsCount=2 Degree=3 IsPeriodic=0
    g6: BSplineCurve PolesCount=4 KnotsCount=2 Degree=3 IsPeriodic=0
    g7: BSplineCurve PolesCount=4 KnotsCount=2 Degree=3 IsPeriodic=0
    g8: BSplineCurve PolesCount=4 KnotsCount=2 Degree=3 IsPeriodic=0
    g9: BSplineCurve PolesCount=4 KnotsCount=2 Degree=3 IsPeriodic=0
    g10: BSplineCurve PolesCount=4 KnotsCount=2 Degree=3 IsPeriodic=0
    g11: BSplineCurve PolesCount=2 KnotsCount=2 Degree=1 IsPeriodic=0
    g12: BSplineCurve PolesCount=4 KnotsCount=2 Degree=3 IsPeriodic=0
    g13: BSplineCurve PolesCount=4 KnotsCount=2 Degree=3 IsPeriodic=0
    g14: BSplineCurve PolesCount=4 KnotsCount=2 Degree=3 IsPeriodic=0
    g15: BSplineCurve PolesCount=4 KnotsCount=2 Degree=3 IsPeriodic=0
    g16: BSplineCurve PolesCount=4 KnotsCount=2 Degree=3 IsPeriodic=0
    g17: BSplineCurve PolesCount=4 KnotsCount=2 Degree=3 IsPeriodic=0
    g18: BSplineCurve PolesCount=4 KnotsCount=2 Degree=3 IsPeriodic=0
    g19: BSplineCurve PolesCount=4 KnotsCount=2 Degree=3 IsPeriodic=0
    g20: BSplineCurve PolesCount=4 KnotsCount=2 Degree=3 IsPeriodic=0
    g21: BSplineCurve PolesCount=4 KnotsCount=2 Degree=3 IsPeriodic=0
    g22: BSplineCurve PolesCount=4 KnotsCount=2 Degree=3 IsPeriodic=0
    g23: BSplineCurve PolesCount=4 KnotsCount=2 Degree=3 IsPeriodic=0
    g24: BSplineCurve PolesCount=4 KnotsCount=2 Degree=3 IsPeriodic=0
    g25: BSplineCurve PolesCount=4 KnotsCount=2 Degree=3 IsPeriodic=0
    g26: BSplineCurve PolesCount=4 KnotsCount=2 Degree=3 IsPeriodic=0
    g27: BSplineCurve PolesCount=4 KnotsCount=2 Degree=3 IsPeriodic=0
    g28: BSplineCurve PolesCount=4 KnotsCount=2 Degree=3 IsPeriodic=0
    g29: BSplineCurve PolesCount=4 KnotsCount=2 Degree=3 IsPeriodic=0
    g30: BSplineCurve PolesCount=4 KnotsCount=2 Degree=3 IsPeriodic=0
    g31: BSplineCurve PolesCount=4 KnotsCount=2 Degree=3 IsPeriodic=0
    g32: BSplineCurve PolesCount=4 KnotsCount=2 Degree=3 IsPeriodic=0
    g33: BSplineCurve PolesCount=4 KnotsCount=2 Degree=3 IsPeriodic=0
    g34: BSplineCurve PolesCount=4 KnotsCount=2 Degree=3 IsPeriodic=0
    g35: BSplineCurve PolesCount=4 KnotsCount=2 Degree=3 IsPeriodic=0
    g36: BSplineCurve PolesCount=4 KnotsCount=2 Degree=3 IsPeriodic=0
    g37: BSplineCurve PolesCount=4 KnotsCount=2 Degree=3 IsPeriodic=0
    g38: BSplineCurve PolesCount=4 KnotsCount=2 Degree=3 IsPeriodic=0
    g39: BSplineCurve PolesCount=2 KnotsCount=2 Degree=1 IsPeriodic=0
    g40: BSplineCurve PolesCount=4 KnotsCount=2 Degree=3 IsPeriodic=0
    g41: BSplineCurve PolesCount=4 KnotsCount=2 Degree=3 IsPeriodic=0
    g42: BSplineCurve PolesCount=4 KnotsCount=2 Degree=3 IsPeriodic=0
    g43: BSplineCurve PolesCount=4 KnotsCount=2 Degree=3 IsPeriodic=0
    g44: BSplineCurve PolesCount=4 KnotsCount=2 Degree=3 IsPeriodic=0
    g45: BSplineCurve PolesCount=4 KnotsCount=2 Degree=3 IsPeriodic=0
    g46: BSplineCurve PolesCount=4 KnotsCount=2 Degree=3 IsPeriodic=0
    g47: BSplineCurve PolesCount=4 KnotsCount=2 Degree=3 IsPeriodic=0
    g48: BSplineCurve PolesCount=4 KnotsCount=2 Degree=3 IsPeriodic=0
    g49: BSplineCurve PolesCount=4 KnotsCount=2 Degree=3 IsPeriodic=0
    g50: BSplineCurve PolesCount=4 KnotsCount=2 Degree=3 IsPeriodic=0
    g51: BSplineCurve PolesCount=4 KnotsCount=2 Degree=3 IsPeriodic=0
    g52: BSplineCurve PolesCount=4 KnotsCount=2 Degree=3 IsPeriodic=0
    g53: BSplineCurve PolesCount=2 KnotsCount=2 Degree=1 IsPeriodic=0
    g54: BSplineCurve PolesCount=2 KnotsCount=2 Degree=1 IsPeriodic=0
    g55: BSplineCurve PolesCount=4 KnotsCount=2 Degree=3 IsPeriodic=0
    g56: BSplineCurve PolesCount=4 KnotsCount=2 Degree=3 IsPeriodic=0
    g57: BSplineCurve PolesCount=4 KnotsCount=2 Degree=3 IsPeriodic=0
    g58: BSplineCurve PolesCount=4 KnotsCount=2 Degree=3 IsPeriodic=0
    g59: BSplineCurve PolesCount=4 KnotsCount=2 Degree=3 IsPeriodic=0
    g60: BSplineCurve PolesCount=4 KnotsCount=2 Degree=3 IsPeriodic=0
    g61: BSplineCurve PolesCount=4 KnotsCount=2 Degree=3 IsPeriodic=0
    g62: BSplineCurve PolesCount=4 KnotsCount=2 Degree=3 IsPeriodic=0
    g63: BSplineCurve PolesCount=4 KnotsCount=2 Degree=3 IsPeriodic=0
    g64: BSplineCurve PolesCount=4 KnotsCount=2 Degree=3 IsPeriodic=0
    g65: BSplineCurve PolesCount=2 KnotsCount=2 Degree=1 IsPeriodic=0
    g66: BSplineCurve PolesCount=4 KnotsCount=2 Degree=3 IsPeriodic=0
    g67: BSplineCurve PolesCount=4 KnotsCount=2 Degree=3 IsPeriodic=0
    g68: BSplineCurve PolesCount=4 KnotsCount=2 Degree=3 IsPeriodic=0
    g69: BSplineCurve PolesCount=4 KnotsCount=2 Degree=3 IsPeriodic=0
    g70: BSplineCurve PolesCount=4 KnotsCount=2 Degree=3 IsPeriodic=0
    g71: BSplineCurve PolesCount=4 KnotsCount=2 Degree=3 IsPeriodic=0
    g72: BSplineCurve PolesCount=4 KnotsCount=2 Degree=3 IsPeriodic=0
    g73: BSplineCurve PolesCount=2 KnotsCount=2 Degree=1 IsPeriodic=0
    g74: BSplineCurve PolesCount=2 KnotsCount=2 Degree=1 IsPeriodic=0
    g75: BSplineCurve PolesCount=4 KnotsCount=2 Degree=3 IsPeriodic=0
    g76: BSplineCurve PolesCount=4 KnotsCount=2 Degree=3 IsPeriodic=0
    g77: BSplineCurve PolesCount=4 KnotsCount=2 Degree=3 IsPeriodic=0
    g78: BSplineCurve PolesCount=4 KnotsCount=2 Degree=3 IsPeriodic=0
    g79: BSplineCurve PolesCount=4 KnotsCount=2 Degree=3 IsPeriodic=0
    g80: BSplineCurve PolesCount=4 KnotsCount=2 Degree=3 IsPeriodic=0
    g81: BSplineCurve PolesCount=4 KnotsCount=2 Degree=3 IsPeriodic=0
    g82: BSplineCurve PolesCount=4 KnotsCount=2 Degree=3 IsPeriodic=0
    g83: BSplineCurve PolesCount=4 KnotsCount=2 Degree=3 IsPeriodic=0
    g84: BSplineCurve PolesCount=4 KnotsCount=2 Degree=3 IsPeriodic=0
    g85: BSplineCurve PolesCount=4 KnotsCount=2 Degree=3 IsPeriodic=0
    g86: BSplineCurve PolesCount=2 KnotsCount=2 Degree=1 IsPeriodic=0
    g87: BSplineCurve PolesCount=4 KnotsCount=2 Degree=3 IsPeriodic=0
    g88: BSplineCurve PolesCount=2 KnotsCount=2 Degree=1 IsPeriodic=0
    g89: BSplineCurve PolesCount=2 KnotsCount=2 Degree=1 IsPeriodic=0
    g90: BSplineCurve PolesCount=4 KnotsCount=2 Degree=3 IsPeriodic=0
    g91: BSplineCurve PolesCount=4 KnotsCount=2 Degree=3 IsPeriodic=0
    g92: BSplineCurve PolesCount=4 KnotsCount=2 Degree=3 IsPeriodic=0
    g93: BSplineCurve PolesCount=4 KnotsCount=2 Degree=3 IsPeriodic=0
    g94: BSplineCurve PolesCount=4 KnotsCount=2 Degree=3 IsPeriodic=0
    g95: BSplineCurve PolesCount=4 KnotsCount=2 Degree=3 IsPeriodic=0
    g96: BSplineCurve PolesCount=4 KnotsCount=2 Degree=3 IsPeriodic=0
    g97: BSplineCurve PolesCount=4 KnotsCount=2 Degree=3 IsPeriodic=0
    g98: BSplineCurve PolesCount=4 KnotsCount=2 Degree=3 IsPeriodic=0
    g99: BSplineCurve PolesCount=4 KnotsCount=2 Degree=3 IsPeriodic=0
    g100: BSplineCurve PolesCount=4 KnotsCount=2 Degree=3 IsPeriodic=0
    g101: BSplineCurve PolesCount=4 KnotsCount=2 Degree=3 IsPeriodic=0
    g102: BSplineCurve PolesCount=4 KnotsCount=2 Degree=3 IsPeriodic=0
    g103: BSplineCurve PolesCount=2 KnotsCount=2 Degree=1 IsPeriodic=0
    g104: BSplineCurve PolesCount=4 KnotsCount=2 Degree=3 IsPeriodic=0
    g105: BSplineCurve PolesCount=4 KnotsCount=2 Degree=3 IsPeriodic=0
    g106: BSplineCurve PolesCount=4 KnotsCount=2 Degree=3 IsPeriodic=0
    g107: BSplineCurve PolesCount=2 KnotsCount=2 Degree=1 IsPeriodic=0
    g108: BSplineCurve PolesCount=2 KnotsCount=2 Degree=1 IsPeriodic=0
    g109: BSplineCurve PolesCount=4 KnotsCount=2 Degree=3 IsPeriodic=0
    g110: BSplineCurve PolesCount=4 KnotsCount=2 Degree=3 IsPeriodic=0
    g111: BSplineCurve PolesCount=4 KnotsCount=2 Degree=3 IsPeriodic=0
    g112: BSplineCurve PolesCount=4 KnotsCount=2 Degree=3 IsPeriodic=0
    g113: BSplineCurve PolesCount=4 KnotsCount=2 Degree=3 IsPeriodic=0
    g114: BSplineCurve PolesCount=4 KnotsCount=2 Degree=3 IsPeriodic=0
    g115: BSplineCurve PolesCount=4 KnotsCount=2 Degree=3 IsPeriodic=0
    g116: BSplineCurve PolesCount=2 KnotsCount=2 Degree=1 IsPeriodic=0
    g117: BSplineCurve PolesCount=4 KnotsCount=2 Degree=3 IsPeriodic=0
    g118: BSplineCurve PolesCount=4 KnotsCount=2 Degree=3 IsPeriodic=0
    g119: BSplineCurve PolesCount=2 KnotsCount=2 Degree=1 IsPeriodic=0
    g120: BSplineCurve PolesCount=2 KnotsCount=2 Degree=1 IsPeriodic=0
    g121: BSplineCurve PolesCount=4 KnotsCount=2 Degree=3 IsPeriodic=0
    g122: BSplineCurve PolesCount=4 KnotsCount=2 Degree=3 IsPeriodic=0
    g123: BSplineCurve PolesCount=4 KnotsCount=2 Degree=3 IsPeriodic=0
    g124: BSplineCurve PolesCount=4 KnotsCount=2 Degree=3 IsPeriodic=0
    g125: BSplineCurve PolesCount=4 KnotsCount=2 Degree=3 IsPeriodic=0
    g126: BSplineCurve PolesCount=2 KnotsCount=2 Degree=1 IsPeriodic=0
    g127: BSplineCurve PolesCount=2 KnotsCount=2 Degree=1 IsPeriodic=0
    g128: BSplineCurve PolesCount=4 KnotsCount=2 Degree=3 IsPeriodic=0
    g129: BSplineCurve PolesCount=4 KnotsCount=2 Degree=3 IsPeriodic=0
    g130: BSplineCurve PolesCount=2 KnotsCount=2 Degree=1 IsPeriodic=0
    g131: BSplineCurve PolesCount=4 KnotsCount=2 Degree=3 IsPeriodic=0
    g132: BSplineCurve PolesCount=2 KnotsCount=2 Degree=1 IsPeriodic=0
    g133: BSplineCurve PolesCount=2 KnotsCount=2 Degree=1 IsPeriodic=0
    g134: BSplineCurve PolesCount=4 KnotsCount=2 Degree=3 IsPeriodic=0
    g135: BSplineCurve PolesCount=4 KnotsCount=2 Degree=3 IsPeriodic=0
    g136: BSplineCurve PolesCount=4 KnotsCount=2 Degree=3 IsPeriodic=0
    g137: BSplineCurve PolesCount=4 KnotsCount=2 Degree=3 IsPeriodic=0
    g138: BSplineCurve PolesCount=4 KnotsCount=2 Degree=3 IsPeriodic=0
    g139: BSplineCurve PolesCount=4 KnotsCount=2 Degree=3 IsPeriodic=0
    g140: BSplineCurve PolesCount=4 KnotsCount=2 Degree=3 IsPeriodic=0
    g141: BSplineCurve PolesCount=4 KnotsCount=2 Degree=3 IsPeriodic=0
    g142: BSplineCurve PolesCount=4 KnotsCount=2 Degree=3 IsPeriodic=0
    g143: BSplineCurve PolesCount=4 KnotsCount=2 Degree=3 IsPeriodic=0
    g144: BSplineCurve PolesCount=4 KnotsCount=2 Degree=3 IsPeriodic=0
    g145: BSplineCurve PolesCount=4 KnotsCount=2 Degree=3 IsPeriodic=0
    g146: BSplineCurve PolesCount=4 KnotsCount=2 Degree=3 IsPeriodic=0
    g147: BSplineCurve PolesCount=4 KnotsCount=2 Degree=3 IsPeriodic=0
    g148: BSplineCurve PolesCount=4 KnotsCount=2 Degree=3 IsPeriodic=0
    g149: BSplineCurve PolesCount=4 KnotsCount=2 Degree=3 IsPeriodic=0
    g150: BSplineCurve PolesCount=2 KnotsCount=2 Degree=1 IsPeriodic=0
    g151: BSplineCurve PolesCount=2 KnotsCount=2 Degree=1 IsPeriodic=0
    g152: BSplineCurve PolesCount=4 KnotsCount=2 Degree=3 IsPeriodic=0
    g153: BSplineCurve PolesCount=2 KnotsCount=2 Degree=1 IsPeriodic=0
    g154: BSplineCurve PolesCount=4 KnotsCount=2 Degree=3 IsPeriodic=0
    g155: BSplineCurve PolesCount=4 KnotsCount=2 Degree=3 IsPeriodic=0
    g156: BSplineCurve PolesCount=4 KnotsCount=2 Degree=3 IsPeriodic=0
    g157: BSplineCurve PolesCount=4 KnotsCount=2 Degree=3 IsPeriodic=0
    g158: BSplineCurve PolesCount=4 KnotsCount=2 Degree=3 IsPeriodic=0
    g159: BSplineCurve PolesCount=4 KnotsCount=2 Degree=3 IsPeriodic=0
    g160: BSplineCurve PolesCount=4 KnotsCount=2 Degree=3 IsPeriodic=0
    g161: BSplineCurve PolesCount=4 KnotsCount=2 Degree=3 IsPeriodic=0
    g162: BSplineCurve PolesCount=2 KnotsCount=2 Degree=1 IsPeriodic=0
    g163: BSplineCurve PolesCount=2 KnotsCount=2 Degree=1 IsPeriodic=0
    g164: BSplineCurve PolesCount=4 KnotsCount=2 Degree=3 IsPeriodic=0
    g165: BSplineCurve PolesCount=4 KnotsCount=2 Degree=3 IsPeriodic=0
    g166: BSplineCurve PolesCount=2 KnotsCount=2 Degree=1 IsPeriodic=0
    g167: BSplineCurve PolesCount=2 KnotsCount=2 Degree=1 IsPeriodic=0
    g168: BSplineCurve PolesCount=4 KnotsCount=2 Degree=3 IsPeriodic=0
    g169: BSplineCurve PolesCount=4 KnotsCount=2 Degree=3 IsPeriodic=0
    g170: BSplineCurve PolesCount=4 KnotsCount=2 Degree=3 IsPeriodic=0
    g171: BSplineCurve PolesCount=2 KnotsCount=2 Degree=1 IsPeriodic=0
    g172: BSplineCurve PolesCount=2 KnotsCount=2 Degree=1 IsPeriodic=0
    g173: BSplineCurve PolesCount=4 KnotsCount=2 Degree=3 IsPeriodic=0
    g174: BSplineCurve PolesCount=4 KnotsCount=2 Degree=3 IsPeriodic=0
    g175: BSplineCurve PolesCount=4 KnotsCount=2 Degree=3 IsPeriodic=0
    g176: BSplineCurve PolesCount=4 KnotsCount=2 Degree=3 IsPeriodic=0
    g177: BSplineCurve PolesCount=2 KnotsCount=2 Degree=1 IsPeriodic=0
    g178: BSplineCurve PolesCount=2 KnotsCount=2 Degree=1 IsPeriodic=0
    g179: BSplineCurve PolesCount=4 KnotsCount=2 Degree=3 IsPeriodic=0
    g180: BSplineCurve PolesCount=4 KnotsCount=2 Degree=3 IsPeriodic=0
    g181: BSplineCurve PolesCount=4 KnotsCount=2 Degree=3 IsPeriodic=0
    g182: BSplineCurve PolesCount=4 KnotsCount=2 Degree=3 IsPeriodic=0
    g183: BSplineCurve PolesCount=4 KnotsCount=2 Degree=3 IsPeriodic=0
    g184: BSplineCurve PolesCount=4 KnotsCount=2 Degree=3 IsPeriodic=0
    g185: BSplineCurve PolesCount=4 KnotsCount=2 Degree=3 IsPeriodic=0
    g186: BSplineCurve PolesCount=4 KnotsCount=2 Degree=3 IsPeriodic=0
    g187: BSplineCurve PolesCount=4 KnotsCount=2 Degree=3 IsPeriodic=0
    g188: BSplineCurve PolesCount=4 KnotsCount=2 Degree=3 IsPeriodic=0
    g189: BSplineCurve PolesCount=4 KnotsCount=2 Degree=3 IsPeriodic=0
    g190: BSplineCurve PolesCount=4 KnotsCount=2 Degree=3 IsPeriodic=0
    g191: BSplineCurve PolesCount=4 KnotsCount=2 Degree=3 IsPeriodic=0
    g192: BSplineCurve PolesCount=4 KnotsCount=2 Degree=3 IsPeriodic=0
    g193: BSplineCurve PolesCount=4 KnotsCount=2 Degree=3 IsPeriodic=0
    g194: BSplineCurve PolesCount=4 KnotsCount=2 Degree=3 IsPeriodic=0
    g195: BSplineCurve PolesCount=4 KnotsCount=2 Degree=3 IsPeriodic=0
    g196: BSplineCurve PolesCount=4 KnotsCount=2 Degree=3 IsPeriodic=0
    g197: BSplineCurve PolesCount=2 KnotsCount=2 Degree=1 IsPeriodic=0
    g198: BSplineCurve PolesCount=4 KnotsCount=2 Degree=3 IsPeriodic=0
    g199: BSplineCurve PolesCount=4 KnotsCount=2 Degree=3 IsPeriodic=0
    g200: BSplineCurve PolesCount=4 KnotsCount=2 Degree=3 IsPeriodic=0
    g201: BSplineCurve PolesCount=4 KnotsCount=2 Degree=3 IsPeriodic=0
    g202: BSplineCurve PolesCount=4 KnotsCount=2 Degree=3 IsPeriodic=0
    g203: BSplineCurve PolesCount=2 KnotsCount=2 Degree=1 IsPeriodic=0
    g204: BSplineCurve PolesCount=2 KnotsCount=2 Degree=1 IsPeriodic=0
    g205: BSplineCurve PolesCount=4 KnotsCount=2 Degree=3 IsPeriodic=0
    g206: BSplineCurve PolesCount=4 KnotsCount=2 Degree=3 IsPeriodic=0
    g207: BSplineCurve PolesCount=4 KnotsCount=2 Degree=3 IsPeriodic=0
    g208: BSplineCurve PolesCount=4 KnotsCount=2 Degree=3 IsPeriodic=0
    g209: BSplineCurve PolesCount=4 KnotsCount=2 Degree=3 IsPeriodic=0
    g210: BSplineCurve PolesCount=4 KnotsCount=2 Degree=3 IsPeriodic=0
    g211: BSplineCurve PolesCount=4 KnotsCount=2 Degree=3 IsPeriodic=0
    g212: BSplineCurve PolesCount=2 KnotsCount=2 Degree=1 IsPeriodic=0
    g213: BSplineCurve PolesCount=4 KnotsCount=2 Degree=3 IsPeriodic=0
    g214: BSplineCurve PolesCount=2 KnotsCount=2 Degree=1 IsPeriodic=0
    g215: BSplineCurve PolesCount=2 KnotsCount=2 Degree=1 IsPeriodic=0
    g216: BSplineCurve PolesCount=4 KnotsCount=2 Degree=3 IsPeriodic=0
    g217: BSplineCurve PolesCount=4 KnotsCount=2 Degree=3 IsPeriodic=0
    g218: BSplineCurve PolesCount=4 KnotsCount=2 Degree=3 IsPeriodic=0
    g219: BSplineCurve PolesCount=4 KnotsCount=2 Degree=3 IsPeriodic=0
    g220: BSplineCurve PolesCount=4 KnotsCount=2 Degree=3 IsPeriodic=0
    g221: BSplineCurve PolesCount=4 KnotsCount=2 Degree=3 IsPeriodic=0
    g222: BSplineCurve PolesCount=4 KnotsCount=2 Degree=3 IsPeriodic=0
    g223: BSplineCurve PolesCount=4 KnotsCount=2 Degree=3 IsPeriodic=0
    g224: BSplineCurve PolesCount=4 KnotsCount=2 Degree=3 IsPeriodic=0
    g225: BSplineCurve PolesCount=4 KnotsCount=2 Degree=3 IsPeriodic=0
    g226: BSplineCurve PolesCount=4 KnotsCount=2 Degree=3 IsPeriodic=0
    g227: BSplineCurve PolesCount=4 KnotsCount=2 Degree=3 IsPeriodic=0
    g228: BSplineCurve PolesCount=2 KnotsCount=2 Degree=1 IsPeriodic=0
    g229: BSplineCurve PolesCount=2 KnotsCount=2 Degree=1 IsPeriodic=0
    g230: BSplineCurve PolesCount=4 KnotsCount=2 Degree=3 IsPeriodic=0
  constraints (241):
    c: Coincident(g0,g1)
    c: Coincident(g1,g2)
    c: Coincident(g2,g3)
    c: Coincident(g3,g4)
    c: Coincident(g4,g5)
    c: Coincident(g5,g6)
    c: Coincident(g6,g7)
    c: Coincident(g7,g8)
    c: Coincident(g8,g9)
    c: Coincident(g9,g10)
    c: Coincident(g10,g0)
    c: Coincident(g11,g12)
    c: Coincident(g12,g13)
    c: Coincident(g13,g14)
    c: Coincident(g14,g15)
    c: Coincident(g15,g16)
    c: Coincident(g16,g17)
    c: Coincident(g17,g18)
    c: Coincident(g18,g11)
    c: Coincident(g19,g20)
    c: Coincident(g20,g21)
    c: Coincident(g21,g22)
    c: Coincident(g22,g23)
    c: Coincident(g23,g24)
    c: Coincident(g24,g25)
    c: Coincident(g25,g26)
    c: Coincident(g26,g27)
    c: Coincident(g27,g28)
    c: Coincident(g28,g29)
    c: Coincident(g29,g30)
    c: Coincident(g30,g31)
    c: Coincident(g31,g32)
    c: Coincident(g32,g33)
    c: Coincident(g33,g34)
    c: Coincident(g34,g35)
    c: Coincident(g35,g36)
    c: Coincident(g36,g37)
    c: Coincident(g37,g38)
    c: Coincident(g38,g19)
    c: Coincident(g39,g40)
    c: Coincident(g40,g41)
    c: Coincident(g41,g42)
    c: Coincident(g42,g39)
    c: Coincident(g43,g44)
    c: Coincident(g44,g45)
    c: Coincident(g45,g43)
    c: Coincident(g46,g47)
    c: Coincident(g47,g48)
    c: Coincident(g48,g46)
    c: Coincident(g49,g50)
    c: Coincident(g50,g51)
    c: Coincident(g51,g52)
    c: Coincident(g52,g53)
    c: Coincident(g53,g54)
    c: Coincident(g54,g55)
    c: Coincident(g55,g56)
    c: Coincident(g56,g57)
    c: Coincident(g57,g49)
    c: Coincident(g58,g59)
    c: Coincident(g59,g60)
    c: Coincident(g60,g61)
    c: Coincident(g61,g62)
    c: Coincident(g62,g63)
    c: Coincident(g63,g64)
    c: Coincident(g64,g58)
    c: Coincident(g65,g66)
    c: Coincident(g66,g67)
    c: Coincident(g67,g68)
    c: Coincident(g68,g69)
    c: Coincident(g69,g70)
    c: Coincident(g70,g71)
    c: Coincident(g71,g65)
    c: Coincident(g72,g73)
    c: Coincident(g73,g74)
    c: Coincident(g74,g75)
    c: Coincident(g75,g72)
    c: Coincident(g76,g77)
    c: Coincident(g77,g78)
    c: Coincident(g78,g79)
    c: Coincident(g79,g80)
    c: Coincident(g80,g76)
    c: Coincident(g81,g82)
    c: Coincident(g82,g83)
    c: Coincident(g83,g84)
    c: Coincident(g84,g85)
    c: Coincident(g85,g81)
    c: Coincident(g86,g87)
    c: Coincident(g87,g88)
    c: Coincident(g88,g89)
    c: Coincident(g89,g90)
    c: Coincident(g90,g91)
    c: Coincident(g91,g86)
    c: Coincident(g92,g93)
    c: Coincident(g93,g94)
    c: Coincident(g94,g95)
    c: Coincident(g95,g96)
    c: Coincident(g96,g97)
    c: Coincident(g97,g98)
    c: Coincident(g98,g99)
    c: Coincident(g99,g100)
    c: Coincident(g100,g101)
    c: Coincident(g101,g102)
    c: Coincident(g102,g92)
    c: Coincident(g103,g104)
    c: Coincident(g104,g105)
    c: Coincident(g105,g106)
    c: Coincident(g106,g107)
    c: Coincident(g107,g108)
    c: Coincident(g108,g109)
    c: Coincident(g109,g110)
    c: Coincident(g110,g111)
    c: Coincident(g111,g103)
    c: Coincident(g112,g113)
    c: Coincident(g113,g114)
    c: Coincident(g114,g115)
    c: Coincident(g115,g112)
    c: Coincident(g116,g117)
    c: Coincident(g117,g118)
    c: Coincident(g118,g119)
    c: Coincident(g119,g120)
    c: Coincident(g120,g121)
    c: Coincident(g121,g122)
    c: Coincident(g122,g123)
    c: Coincident(g123,g124)
    c: Coincident(g124,g125)
    c: Coincident(g125,g126)
    c: Coincident(g126,g127)
    c: Coincident(g127,g128)
    c: Coincident(g128,g129)
    c: Coincident(g129,g116)
    c: Coincident(g130,g131)
    c: Coincident(g131,g132)
    c: Coincident(g132,g133)
    c: Coincident(g133,g134)
    c: Coincident(g134,g135)
    c: Coincident(g135,g136)
    c: Coincident(g136,g137)
    c: Coincident(g137,g138)
    c: Coincident(g138,g139)
    c: Coincident(g139,g140)
    c: Coincident(g140,g141)
    c: Coincident(g141,g142)
    c: Coincident(g142,g143)
    c: Coincident(g143,g144)
    c: Coincident(g144,g145)
    c: Coincident(g145,g146)
    c: Coincident(g146,g147)
    c: Coincident(g147,g148)
    c: Coincident(g148,g149)
    c: Coincident(g149,g150)
    c: Coincident(g150,g151)
    c: Coincident(g151,g152)
    c: Coincident(g152,g130)
    c: Coincident(g153,g154)
    c: Coincident(g154,g155)
    c: Coincident(g155,g156)
    c: Coincident(g156,g157)
    c: Coincident(g157,g158)
    c: Coincident(g158,g159)
    c: Coincident(g159,g160)
    c: Coincident(g160,g161)
    c: Coincident(g161,g162)
    c: Coincident(g162,g163)
    c: Coincident(g163,g164)
    c: Coincident(g164,g153)
    c: Coincident(g165,g166)
    c: Coincident(g166,g167)
    c: Coincident(g167,g168)
    c: Coincident(g168,g169)
    c: Coincident(g169,g170)
    c: Coincident(g170,g171)
    c: Coincident(g171,g172)
    c: Coincident(g172,g173)
    c: Coincident(g173,g174)
    c: Coincident(g174,g175)
    c: Coincident(g175,g176)
    c: Coincident(g176,g177)
    c: Coincident(g177,g178)
    c: Coincident(g178,g179)
    c: Coincident(g179,g180)
    c: Coincident(g180,g165)
    c: Coincident(g181,g182)
    c: Coincident(g182,g183)
    c: Coincident(g183,g184)
    c: Coincident(g184,g185)
    c: Coincident(g185,g181)
    c: Coincident(g186,g187)
    c: Coincident(g187,g188)
    c: Coincident(g188,g186)
    c: Coincident(g189,g190)
    c: Coincident(g190,g191)
    c: Coincident(g191,g192)
    c: Coincident(g192,g193)
    c: Coincident(g193,g194)
    c: Coincident(g194,g195)
    c: Coincident(g195,g196)
    c: Coincident(g196,g189)
    c: Coincident(g197,g198)
    c: Coincident(g198,g199)
    c: Coincident(g199,g200)
    c: Coincident(g200,g201)
    c: Coincident(g201,g202)
    c: Coincident(g202,g203)
    c: Coincident(g203,g204)
    c: Coincident(g204,g205)
    c: Coincident(g205,g206)
    c: Coincident(g206,g197)
    c: Coincident(g207,g208)
    c: Coincident(g208,g209)
    c: Coincident(g209,g210)
    c: Coincident(g210,g211)
    c: Coincident(g211,g207)
    c: Coincident(g212,g213)
    c: Coincident(g213,g214)
    c: Coincident(g214,g215)
    c: Coincident(g215,g216)
    c: Coincident(g216,g217)
    c: Coincident(g217,g218)
    c: Coincident(g218,g219)
    c: Coincident(g219,g220)
    c: Coincident(g220,g221)
    c: Coincident(g221,g222)
    c: Coincident(g222,g223)
    c: Coincident(g223,g224)
    c: Coincident(g224,g225)
    c: Coincident(g225,g226)
    c: Coincident(g226,g227)
    c: Coincident(g227,g228)
    c: Coincident(g228,g229)
    c: Coincident(g229,g230)
    c: Coincident(g230,g212)
    c: Coincident(g103,g103)
    c: Coincident(g212,g212)
    c: Coincident(g116,g116)
    c: Coincident(g197,g197)
    c: Coincident(g65,g65)
    c: Coincident(g86,g86)
    c: Coincident(g130,g130)
    c: Coincident(g153,g153)
    c: Coincident(g39,g39)
    c: Coincident(g11,g11)
FEATURE [Sketcher::SketchObject] Sketch036  label="Klutz-Sketch"
  ArcFitTolerance = 1e-06
  FullyConstrained = false
  MakeInternals = false
  Placement = pos=(-15.0131,13.2623,0) rot=(0,0,1;0rad)
  expr: .Placement.Base.x = -(.Shape.BoundBox.XLength / 2)
  expr: .Placement.Base.y = .Shape.BoundBox.YLength / 2
  sketch-geometry (182):
    g0: BSplineCurve PolesCount=4 KnotsCount=2 Degree=3 IsPeriodic=0
    g1: BSplineCurve PolesCount=4 KnotsCount=2 Degree=3 IsPeriodic=0
    g2: BSplineCurve PolesCount=4 KnotsCount=2 Degree=3 IsPeriodic=0
    g3: BSplineCurve PolesCount=4 KnotsCount=2 Degree=3 IsPeriodic=0
    g4: BSplineCurve PolesCount=4 KnotsCount=2 Degree=3 IsPeriodic=0
    g5: BSplineCurve PolesCount=4 KnotsCount=2 Degree=3 IsPeriodic=0
    g6: BSplineCurve PolesCount=4 KnotsCount=2 Degree=3 IsPeriodic=0
    g7: BSplineCurve PolesCount=4 KnotsCount=2 Degree=3 IsPeriodic=0
    g8: BSplineCurve PolesCount=4 KnotsCount=2 Degree=3 IsPeriodic=0
    g9: BSplineCurve PolesCount=4 KnotsCount=2 Degree=3 IsPeriodic=0
    g10: BSplineCurve PolesCount=4 KnotsCount=2 Degree=3 IsPeriodic=0
    g11: BSplineCurve PolesCount=4 KnotsCount=2 Degree=3 IsPeriodic=0
    g12: BSplineCurve PolesCount=4 KnotsCount=2 Degree=3 IsPeriodic=0
    g13: BSplineCurve PolesCount=4 KnotsCount=2 Degree=3 IsPeriodic=0
    g14: BSplineCurve PolesCount=4 KnotsCount=2 Degree=3 IsPeriodic=0
    g15: BSplineCurve PolesCount=4 KnotsCount=2 Degree=3 IsPeriodic=0
    g16: BSplineCurve PolesCount=4 KnotsCount=2 Degree=3 IsPeriodic=0
    g17: BSplineCurve PolesCount=4 KnotsCount=2 Degree=3 IsPeriodic=0
    g18: BSplineCurve PolesCount=4 KnotsCount=2 Degree=3 IsPeriodic=0
    g19: BSplineCurve PolesCount=4 KnotsCount=2 Degree=3 IsPeriodic=0
    g20: BSplineCurve PolesCount=4 KnotsCount=2 Degree=3 IsPeriodic=0
    g21: BSplineCurve PolesCount=4 KnotsCount=2 Degree=3 IsPeriodic=0
    g22: BSplineCurve PolesCount=4 KnotsCount=2 Degree=3 IsPeriodic=0
    g23: BSplineCurve PolesCount=4 KnotsCount=2 Degree=3 IsPeriodic=0
    g24: BSplineCurve PolesCount=4 KnotsCount=2 Degree=3 IsPeriodic=0
    g25: BSplineCurve PolesCount=4 KnotsCount=2 Degree=3 IsPeriodic=0
    g26: BSplineCurve PolesCount=4 KnotsCount=2 Degree=3 IsPeriodic=0
    g27: BSplineCurve PolesCount=4 KnotsCount=2 Degree=3 IsPeriodic=0
    g28: BSplineCurve PolesCount=4 KnotsCount=2 Degree=3 IsPeriodic=0
    g29: BSplineCurve PolesCount=4 KnotsCount=2 Degree=3 IsPeriodic=0
    g30: BSplineCurve PolesCount=4 KnotsCount=2 Degree=3 IsPeriodic=0
    g31: BSplineCurve PolesCount=2 KnotsCount=2 Degree=1 IsPeriodic=0
    g32: BSplineCurve PolesCount=2 KnotsCount=2 Degree=1 IsPeriodic=0
    g33: BSplineCurve PolesCount=4 KnotsCount=2 Degree=3 IsPeriodic=0
    g34: BSplineCurve PolesCount=4 KnotsCount=2 Degree=3 IsPeriodic=0
    g35: BSplineCurve PolesCount=4 KnotsCount=2 Degree=3 IsPeriodic=0
    g36: BSplineCurve PolesCount=4 KnotsCount=2 Degree=3 IsPeriodic=0
    g37: BSplineCurve PolesCount=4 KnotsCount=2 Degree=3 IsPeriodic=0
    g38: BSplineCurve PolesCount=4 KnotsCount=2 Degree=3 IsPeriodic=0
    g39: BSplineCurve PolesCount=4 KnotsCount=2 Degree=3 IsPeriodic=0
    g40: BSplineCurve PolesCount=4 KnotsCount=2 Degree=3 IsPeriodic=0
    g41: BSplineCurve PolesCount=4 KnotsCount=2 Degree=3 IsPeriodic=0
    g42: BSplineCurve PolesCount=4 KnotsCount=2 Degree=3 IsPeriodic=0
    g43: BSplineCurve PolesCount=4 KnotsCount=2 Degree=3 IsPeriodic=0
    g44: BSplineCurve PolesCount=4 KnotsCount=2 Degree=3 IsPeriodic=0
    g45: BSplineCurve PolesCount=4 KnotsCount=2 Degree=3 IsPeriodic=0
    g46: BSplineCurve PolesCount=4 KnotsCount=2 Degree=3 IsPeriodic=0
    g47: BSplineCurve PolesCount=4 KnotsCount=2 Degree=3 IsPeriodic=0
    g48: BSplineCurve PolesCount=4 KnotsCount=2 Degree=3 IsPeriodic=0
    g49: BSplineCurve PolesCount=4 KnotsCount=2 Degree=3 IsPeriodic=0
    g50: BSplineCurve PolesCount=4 KnotsCount=2 Degree=3 IsPeriodic=0
    g51: BSplineCurve PolesCount=4 KnotsCount=2 Degree=3 IsPeriodic=0
    g52: BSplineCurve PolesCount=4 KnotsCount=2 Degree=3 IsPeriodic=0
    g53: BSplineCurve PolesCount=2 KnotsCount=2 Degree=1 IsPeriodic=0
    g54: BSplineCurve PolesCount=2 KnotsCount=2 Degree=1 IsPeriodic=0
    g55: BSplineCurve PolesCount=4 KnotsCount=2 Degree=3 IsPeriodic=0
    g56: BSplineCurve PolesCount=4 KnotsCount=2 Degree=3 IsPeriodic=0
    g57: BSplineCurve PolesCount=4 KnotsCount=2 Degree=3 IsPeriodic=0
    g58: BSplineCurve PolesCount=4 KnotsCount=2 Degree=3 IsPeriodic=0
    g59: BSplineCurve PolesCount=4 KnotsCount=2 Degree=3 IsPeriodic=0
    g60: BSplineCurve PolesCount=4 KnotsCount=2 Degree=3 IsPeriodic=0
    g61: BSplineCurve PolesCount=4 KnotsCount=2 Degree=3 IsPeriodic=0
    g62: BSplineCurve PolesCount=4 KnotsCount=2 Degree=3 IsPeriodic=0
    g63: BSplineCurve PolesCount=4 KnotsCount=2 Degree=3 IsPeriodic=0
    g64: BSplineCurve PolesCount=4 KnotsCount=2 Degree=3 IsPeriodic=0
    g65: BSplineCurve PolesCount=2 KnotsCount=2 Degree=1 IsPeriodic=0
    g66: BSplineCurve PolesCount=2 KnotsCount=2 Degree=1 IsPeriodic=0
    g67: BSplineCurve PolesCount=4 KnotsCount=2 Degree=3 IsPeriodic=0
    g68: BSplineCurve PolesCount=4 KnotsCount=2 Degree=3 IsPeriodic=0
    g69: BSplineCurve PolesCount=4 KnotsCount=2 Degree=3 IsPeriodic=0
    g70: BSplineCurve PolesCount=4 KnotsCount=2 Degree=3 IsPeriodic=0
    g71: BSplineCurve PolesCount=4 KnotsCount=2 Degree=3 IsPeriodic=0
    g72: BSplineCurve PolesCount=4 KnotsCount=2 Degree=3 IsPeriodic=0
    g73: BSplineCurve PolesCount=4 KnotsCount=2 Degree=3 IsPeriodic=0
    g74: BSplineCurve PolesCount=4 KnotsCount=2 Degree=3 IsPeriodic=0
    g75: BSplineCurve PolesCount=4 KnotsCount=2 Degree=3 IsPeriodic=0
    g76: BSplineCurve PolesCount=4 KnotsCount=2 Degree=3 IsPeriodic=0
    g77: BSplineCurve PolesCount=4 KnotsCount=2 Degree=3 IsPeriodic=0
    g78: BSplineCurve PolesCount=4 KnotsCount=2 Degree=3 IsPeriodic=0
    g79: BSplineCurve PolesCount=4 KnotsCount=2 Degree=3 IsPeriodic=0
    g80: BSplineCurve PolesCount=4 KnotsCount=2 Degree=3 IsPeriodic=0
    g81: BSplineCurve PolesCount=4 KnotsCount=2 Degree=3 IsPeriodic=0
    g82: BSplineCurve PolesCount=4 KnotsCount=2 Degree=3 IsPeriodic=0
    g83: BSplineCurve PolesCount=4 KnotsCount=2 Degree=3 IsPeriodic=0
    g84: BSplineCurve PolesCount=4 KnotsCount=2 Degree=3 IsPeriodic=0
    g85: BSplineCurve PolesCount=4 KnotsCount=2 Degree=3 IsPeriodic=0
    g86: BSplineCurve PolesCount=4 KnotsCount=2 Degree=3 IsPeriodic=0
    g87: BSplineCurve PolesCount=4 KnotsCount=2 Degree=3 IsPeriodic=0
    g88: BSplineCurve PolesCount=4 KnotsCount=2 Degree=3 IsPeriodic=0
    g89: BSplineCurve PolesCount=4 KnotsCount=2 Degree=3 IsPeriodic=0
    g90: BSplineCurve PolesCount=4 KnotsCount=2 Degree=3 IsPeriodic=0
    g91: BSplineCurve PolesCount=4 KnotsCount=2 Degree=3 IsPeriodic=0
    g92: BSplineCurve PolesCount=2 KnotsCount=2 Degree=1 IsPeriodic=0
    g93: BSplineCurve PolesCount=4 KnotsCount=2 Degree=3 IsPeriodic=0
    g94: BSplineCurve PolesCount=4 KnotsCount=2 Degree=3 IsPeriodic=0
    g95: BSplineCurve PolesCount=4 KnotsCount=2 Degree=3 IsPeriodic=0
    g96: BSplineCurve PolesCount=4 KnotsCount=2 Degree=3 IsPeriodic=0
    g97: BSplineCurve PolesCount=4 KnotsCount=2 Degree=3 IsPeriodic=0
    g98: BSplineCurve PolesCount=4 KnotsCount=2 Degree=3 IsPeriodic=0
    g99: BSplineCurve PolesCount=4 KnotsCount=2 Degree=3 IsPeriodic=0
    g100: BSplineCurve PolesCount=4 KnotsCount=2 Degree=3 IsPeriodic=0
    g101: BSplineCurve PolesCount=4 KnotsCount=2 Degree=3 IsPeriodic=0
    g102: BSplineCurve PolesCount=2 KnotsCount=2 Degree=1 IsPeriodic=0
    g103: BSplineCurve PolesCount=2 KnotsCount=2 Degree=1 IsPeriodic=0
    g104: BSplineCurve PolesCount=4 KnotsCount=2 Degree=3 IsPeriodic=0
    g105: BSplineCurve PolesCount=4 KnotsCount=2 Degree=3 IsPeriodic=0
    g106: BSplineCurve PolesCount=4 KnotsCount=2 Degree=3 IsPeriodic=0
    g107: BSplineCurve PolesCount=4 KnotsCount=2 Degree=3 IsPeriodic=0
    g108: BSplineCurve PolesCount=4 KnotsCount=2 Degree=3 IsPeriodic=0
    g109: BSplineCurve PolesCount=4 KnotsCount=2 Degree=3 IsPeriodic=0
    g110: BSplineCurve PolesCount=4 KnotsCount=2 Degree=3 IsPeriodic=0
    g111: BSplineCurve PolesCount=4 KnotsCount=2 Degree=3 IsPeriodic=0
    g112: BSplineCurve PolesCount=4 KnotsCount=2 Degree=3 IsPeriodic=0
    g113: BSplineCurve PolesCount=4 KnotsCount=2 Degree=3 IsPeriodic=0
    g114: BSplineCurve PolesCount=4 KnotsCount=2 Degree=3 IsPeriodic=0
    g115: BSplineCurve PolesCount=4 KnotsCount=2 Degree=3 IsPeriodic=0
    g116: BSplineCurve PolesCount=4 KnotsCount=2 Degree=3 IsPeriodic=0
    g117: BSplineCurve PolesCount=4 KnotsCount=2 Degree=3 IsPeriodic=0
    g118: BSplineCurve PolesCount=4 KnotsCount=2 Degree=3 IsPeriodic=0
    g119: BSplineCurve PolesCount=4 KnotsCount=2 Degree=3 IsPeriodic=0
    g120: BSplineCurve PolesCount=4 KnotsCount=2 Degree=3 IsPeriodic=0
    g121: BSplineCurve PolesCount=4 KnotsCount=2 Degree=3 IsPeriodic=0
    g122: BSplineCurve PolesCount=4 KnotsCount=2 Degree=3 IsPeriodic=0
    g123: BSplineCurve PolesCount=4 KnotsCount=2 Degree=3 IsPeriodic=0
    g124: BSplineCurve PolesCount=4 KnotsCount=2 Degree=3 IsPeriodic=0
    g125: BSplineCurve PolesCount=4 KnotsCount=2 Degree=3 IsPeriodic=0
    g126: BSplineCurve PolesCount=4 KnotsCount=2 Degree=3 IsPeriodic=0
    g127: BSplineCurve PolesCount=4 KnotsCount=2 Degree=3 IsPeriodic=0
    g128: BSplineCurve PolesCount=4 KnotsCount=2 Degree=3 IsPeriodic=0
    g129: BSplineCurve PolesCount=4 KnotsCount=2 Degree=3 IsPeriodic=0
    g130: BSplineCurve PolesCount=4 KnotsCount=2 Degree=3 IsPeriodic=0
    g131: BSplineCurve PolesCount=4 KnotsCount=2 Degree=3 IsPeriodic=0
    g132: BSplineCurve PolesCount=4 KnotsCount=2 Degree=3 IsPeriodic=0
    g133: BSplineCurve PolesCount=2 KnotsCount=2 Degree=1 IsPeriodic=0
    g134: BSplineCurve PolesCount=2 KnotsCount=2 Degree=1 IsPeriodic=0
    g135: BSplineCurve PolesCount=4 KnotsCount=2 Degree=3 IsPeriodic=0
    g136: BSplineCurve PolesCount=4 KnotsCount=2 Degree=3 IsPeriodic=0
    g137: BSplineCurve PolesCount=4 KnotsCount=2 Degree=3 IsPeriodic=0
    g138: BSplineCurve PolesCount=4 KnotsCount=2 Degree=3 IsPeriodic=0
    g139: BSplineCurve PolesCount=4 KnotsCount=2 Degree=3 IsPeriodic=0
    g140: BSplineCurve PolesCount=4 KnotsCount=2 Degree=3 IsPeriodic=0
    g141: BSplineCurve PolesCount=2 KnotsCount=2 Degree=1 IsPeriodic=0
    g142: BSplineCurve PolesCount=2 KnotsCount=2 Degree=1 IsPeriodic=0
    g143: BSplineCurve PolesCount=4 KnotsCount=2 Degree=3 IsPeriodic=0
    g144: BSplineCurve PolesCount=4 KnotsCount=2 Degree=3 IsPeriodic=0
    g145: BSplineCurve PolesCount=4 KnotsCount=2 Degree=3 IsPeriodic=0
    g146: BSplineCurve PolesCount=4 KnotsCount=2 Degree=3 IsPeriodic=0
    g147: BSplineCurve PolesCount=4 KnotsCount=2 Degree=3 IsPeriodic=0
    g148: BSplineCurve PolesCount=4 KnotsCount=2 Degree=3 IsPeriodic=0
    g149: BSplineCurve PolesCount=4 KnotsCount=2 Degree=3 IsPeriodic=0
    g150: BSplineCurve PolesCount=4 KnotsCount=2 Degree=3 IsPeriodic=0
    g151: BSplineCurve PolesCount=4 KnotsCount=2 Degree=3 IsPeriodic=0
    g152: BSplineCurve PolesCount=4 KnotsCount=2 Degree=3 IsPeriodic=0
    g153: BSplineCurve PolesCount=2 KnotsCount=2 Degree=1 IsPeriodic=0
    g154: BSplineCurve PolesCount=4 KnotsCount=2 Degree=3 IsPeriodic=0
    g155: BSplineCurve PolesCount=2 KnotsCount=2 Degree=1 IsPeriodic=0
    g156: BSplineCurve PolesCount=4 KnotsCount=2 Degree=3 IsPeriodic=0
    g157: BSplineCurve PolesCount=4 KnotsCount=2 Degree=3 IsPeriodic=0
    g158: BSplineCurve PolesCount=4 KnotsCount=2 Degree=3 IsPeriodic=0
    g159: BSplineCurve PolesCount=4 KnotsCount=2 Degree=3 IsPeriodic=0
    g160: BSplineCurve PolesCount=4 KnotsCount=2 Degree=3 IsPeriodic=0
    g161: BSplineCurve PolesCount=4 KnotsCount=2 Degree=3 IsPeriodic=0
    g162: BSplineCurve PolesCount=4 KnotsCount=2 Degree=3 IsPeriodic=0
    g163: BSplineCurve PolesCount=4 KnotsCount=2 Degree=3 IsPeriodic=0
    g164: BSplineCurve PolesCount=4 KnotsCount=2 Degree=3 IsPeriodic=0
    g165: BSplineCurve PolesCount=4 KnotsCount=2 Degree=3 IsPeriodic=0
    g166: BSplineCurve PolesCount=4 KnotsCount=2 Degree=3 IsPeriodic=0
    g167: BSplineCurve PolesCount=4 KnotsCount=2 Degree=3 IsPeriodic=0
    g168: BSplineCurve PolesCount=4 KnotsCount=2 Degree=3 IsPeriodic=0
    g169: BSplineCurve PolesCount=4 KnotsCount=2 Degree=3 IsPeriodic=0
    g170: BSplineCurve PolesCount=4 KnotsCount=2 Degree=3 IsPeriodic=0
    g171: BSplineCurve PolesCount=4 KnotsCount=2 Degree=3 IsPeriodic=0
    g172: BSplineCurve PolesCount=4 KnotsCount=2 Degree=3 IsPeriodic=0
    g173: BSplineCurve PolesCount=4 KnotsCount=2 Degree=3 IsPeriodic=0
    g174: BSplineCurve PolesCount=4 KnotsCount=2 Degree=3 IsPeriodic=0
    g175: BSplineCurve PolesCount=4 KnotsCount=2 Degree=3 IsPeriodic=0
    g176: BSplineCurve PolesCount=4 KnotsCount=2 Degree=3 IsPeriodic=0
    g177: BSplineCurve PolesCount=4 KnotsCount=2 Degree=3 IsPeriodic=0
    g178: BSplineCurve PolesCount=4 KnotsCount=2 Degree=3 IsPeriodic=0
    g179: BSplineCurve PolesCount=4 KnotsCount=2 Degree=3 IsPeriodic=0
    g180: BSplineCurve PolesCount=4 KnotsCount=2 Degree=3 IsPeriodic=0
    g181: BSplineCurve PolesCount=4 KnotsCount=2 Degree=3 IsPeriodic=0
  constraints (183):
    c: Coincident(g0,g1)
    c: Coincident(g1,g2)
    c: Coincident(g2,g3)
    c: Coincident(g3,g4)
    c: Coincident(g4,g5)
    c: Coincident(g5,g6)
    c: Coincident(g6,g7)
    c: Coincident(g7,g8)
    c: Coincident(g8,g9)
    c: Coincident(g9,g10)
    c: Coincident(g10,g11)
    c: Coincident(g11,g12)
    c: Coincident(g12,g13)
    c: Coincident(g13,g14)
    c: Coincident(g14,g15)
    c: Coincident(g15,g16)
    c: Coincident(g16,g17)
    c: Coincident(g17,g18)
    c: Coincident(g18,g19)
    c: Coincident(g19,g20)
    c: Coincident(g20,g21)
    c: Coincident(g21,g22)
    c: Coincident(g22,g23)
    c: Coincident(g23,g24)
    c: Coincident(g24,g25)
    c: Coincident(g25,g26)
    c: Coincident(g26,g27)
    c: Coincident(g27,g28)
    c: Coincident(g28,g29)
    c: Coincident(g29,g30)
    c: Coincident(g30,g31)
    c: Coincident(g31,g32)
    c: Coincident(g32,g33)
    c: Coincident(g33,g34)
    c: Coincident(g34,g35)
    c: Coincident(g35,g36)
    c: Coincident(g36,g37)
    c: Coincident(g37,g38)
    c: Coincident(g38,g0)
    c: Coincident(g39,g40)
    c: Coincident(g40,g41)
    c: Coincident(g41,g42)
    c: Coincident(g42,g43)
    c: Coincident(g43,g44)
    c: Coincident(g44,g45)
    c: Coincident(g45,g46)
    c: Coincident(g46,g47)
    c: Coincident(g47,g48)
    c: Coincident(g48,g49)
    c: Coincident(g49,g50)
    c: Coincident(g50,g51)
    c: Coincident(g51,g52)
    c: Coincident(g52,g53)
    c: Coincident(g53,g54)
    c: Coincident(g54,g55)
    c: Coincident(g55,g56)
    c: Coincident(g56,g57)
    c: Coincident(g57,g58)
    c: Coincident(g58,g59)
    c: Coincident(g59,g60)
    c: Coincident(g60,g61)
    c: Coincident(g61,g62)
    c: Coincident(g62,g63)
    c: Coincident(g63,g64)
    c: Coincident(g64,g65)
    c: Coincident(g65,g66)
    c: Coincident(g66,g39)
    c: Coincident(g67,g68)
    c: Coincident(g68,g69)
    c: Coincident(g69,g67)
    c: Coincident(g70,g71)
    c: Coincident(g71,g72)
    c: Coincident(g72,g73)
    c: Coincident(g73,g74)
    c: Coincident(g74,g75)
    c: Coincident(g75,g76)
    c: Coincident(g76,g77)
    c: Coincident(g77,g78)
    c: Coincident(g78,g79)
    c: Coincident(g79,g80)
    c: Coincident(g80,g81)
    c: Coincident(g81,g82)
    c: Coincident(g82,g70)
    c: Coincident(g83,g84)
    c: Coincident(g84,g85)
    c: Coincident(g85,g83)
    c: Coincident(g86,g87)
    c: Coincident(g87,g88)
    c: Coincident(g88,g89)
    c: Coincident(g89,g90)
    c: Coincident(g90,g91)
    c: Coincident(g91,g86)
    c: Coincident(g92,g93)
    c: Coincident(g93,g94)
    c: Coincident(g94,g95)
    c: Coincident(g95,g96)
    c: Coincident(g96,g97)
    c: Coincident(g97,g98)
    c: Coincident(g98,g99)
    c: Coincident(g99,g100)
    c: Coincident(g100,g101)
    c: Coincident(g101,g102)
    c: Coincident(g102,g103)
    c: Coincident(g103,g104)
    c: Coincident(g104,g105)
    c: Coincident(g105,g106)
    c: Coincident(g106,g107)
    c: Coincident(g107,g108)
    c: Coincident(g108,g109)
    c: Coincident(g109,g110)
    c: Coincident(g110,g111)
    c: Coincident(g111,g112)
    c: Coincident(g112,g113)
    c: Coincident(g113,g114)
    c: Coincident(g114,g115)
    c: Coincident(g115,g116)
    c: Coincident(g116,g117)
    c: Coincident(g117,g118)
    c: Coincident(g118,g119)
    c: Coincident(g119,g120)
    c: Coincident(g120,g121)
    c: Coincident(g121,g122)
    c: Coincident(g122,g123)
    c: Coincident(g123,g124)
    c: Coincident(g124,g125)
    c: Coincident(g125,g126)
    c: Coincident(g126,g127)
    c: Coincident(g127,g128)
    c: Coincident(g128,g129)
    c: Coincident(g129,g130)
    c: Coincident(g130,g131)
    c: Coincident(g131,g132)
    c: Coincident(g132,g133)
    c: Coincident(g133,g134)
    c: Coincident(g134,g135)
    c: Coincident(g135,g136)
    c: Coincident(g136,g137)
    c: Coincident(g137,g138)
    c: Coincident(g138,g139)
    c: Coincident(g139,g140)
    c: Coincident(g140,g141)
    c: Coincident(g141,g142)
    c: Coincident(g142,g143)
    c: Coincident(g143,g144)
    c: Coincident(g144,g145)
    c: Coincident(g145,g146)
    c: Coincident(g146,g147)
    c: Coincident(g147,g148)
    c: Coincident(g148,g149)
    c: Coincident(g149,g150)
    c: Coincident(g150,g151)
    c: Coincident(g151,g152)
    c: Coincident(g152,g153)
    c: Coincident(g153,g92)
    c: Coincident(g154,g155)
    c: Coincident(g155,g156)
    c: Coincident(g156,g157)
    c: Coincident(g157,g158)
    c: Coincident(g158,g159)
    c: Coincident(g159,g160)
    c: Coincident(g160,g161)
    c: Coincident(g161,g162)
    c: Coincident(g162,g163)
    c: Coincident(g163,g164)
    c: Coincident(g164,g154)
    c: Coincident(g165,g166)
    c: Coincident(g166,g167)
    c: Coincident(g167,g168)
    c: Coincident(g168,g169)
    c: Coincident(g169,g170)
    c: Coincident(g170,g171)
    c: Coincident(g171,g172)
    c: Coincident(g172,g173)
    c: Coincident(g173,g174)
    c: Coincident(g174,g175)
    c: Coincident(g175,g176)
    c: Coincident(g176,g177)
    c: Coincident(g177,g178)
    c: Coincident(g178,g179)
    c: Coincident(g179,g180)
    c: Coincident(g180,g181)
    c: Coincident(g181,g165)
    c: Coincident(g154,g155)
FEATURE [Sketcher::SketchObject] Sketch037  label="Mathematician-Sketch"
  ArcFitTolerance = 1e-06
  FullyConstrained = false
  MakeInternals = false
  Placement = pos=(-13.7888,12.2038,0) rot=(0,0,1;0rad)
  expr: .Placement.Base.x = -(.Shape.BoundBox.XLength / 2)
  expr: .Placement.Base.y = .Shape.BoundBox.YLength / 2
  sketch-geometry (331):
    g0: BSplineCurve PolesCount=4 KnotsCount=2 Degree=3 IsPeriodic=0
    g1: BSplineCurve PolesCount=4 KnotsCount=2 Degree=3 IsPeriodic=0
    g2: BSplineCurve PolesCount=4 KnotsCount=2 Degree=3 IsPeriodic=0
    g3: BSplineCurve PolesCount=4 KnotsCount=2 Degree=3 IsPeriodic=0
    g4: BSplineCurve PolesCount=4 KnotsCount=2 Degree=3 IsPeriodic=0
    g5: BSplineCurve PolesCount=4 KnotsCount=2 Degree=3 IsPeriodic=0
    g6: BSplineCurve PolesCount=4 KnotsCount=2 Degree=3 IsPeriodic=0
    g7: BSplineCurve PolesCount=4 KnotsCount=2 Degree=3 IsPeriodic=0
    g8: BSplineCurve PolesCount=4 KnotsCount=2 Degree=3 IsPeriodic=0
    g9: BSplineCurve PolesCount=4 KnotsCount=2 Degree=3 IsPeriodic=0
    g10: BSplineCurve PolesCount=4 KnotsCount=2 Degree=3 IsPeriodic=0
    g11: BSplineCurve PolesCount=4 KnotsCount=2 Degree=3 IsPeriodic=0
    g12: BSplineCurve PolesCount=4 KnotsCount=2 Degree=3 IsPeriodic=0
    g13: BSplineCurve PolesCount=4 KnotsCount=2 Degree=3 IsPeriodic=0
    g14: BSplineCurve PolesCount=4 KnotsCount=2 Degree=3 IsPeriodic=0
    g15: BSplineCurve PolesCount=4 KnotsCount=2 Degree=3 IsPeriodic=0
    g16: BSplineCurve PolesCount=4 KnotsCount=2 Degree=3 IsPeriodic=0
    g17: BSplineCurve PolesCount=4 KnotsCount=2 Degree=3 IsPeriodic=0
    g18: BSplineCurve PolesCount=4 KnotsCount=2 Degree=3 IsPeriodic=0
    g19: BSplineCurve PolesCount=4 KnotsCount=2 Degree=3 IsPeriodic=0
    g20: BSplineCurve PolesCount=4 KnotsCount=2 Degree=3 IsPeriodic=0
    g21: BSplineCurve PolesCount=4 KnotsCount=2 Degree=3 IsPeriodic=0
    g22: BSplineCurve PolesCount=4 KnotsCount=2 Degree=3 IsPeriodic=0
    g23: BSplineCurve PolesCount=4 KnotsCount=2 Degree=3 IsPeriodic=0
    g24: BSplineCurve PolesCount=4 KnotsCount=2 Degree=3 IsPeriodic=0
    g25: BSplineCurve PolesCount=4 KnotsCount=2 Degree=3 IsPeriodic=0
    g26: BSplineCurve PolesCount=4 KnotsCount=2 Degree=3 IsPeriodic=0
    g27: BSplineCurve PolesCount=4 KnotsCount=2 Degree=3 IsPeriodic=0
    g28: BSplineCurve PolesCount=4 KnotsCount=2 Degree=3 IsPeriodic=0
    g29: BSplineCurve PolesCount=4 KnotsCount=2 Degree=3 IsPeriodic=0
    g30: BSplineCurve PolesCount=4 KnotsCount=2 Degree=3 IsPeriodic=0
    g31: BSplineCurve PolesCount=4 KnotsCount=2 Degree=3 IsPeriodic=0
    g32: BSplineCurve PolesCount=4 KnotsCount=2 Degree=3 IsPeriodic=0
    g33: BSplineCurve PolesCount=4 KnotsCount=2 Degree=3 IsPeriodic=0
    g34: BSplineCurve PolesCount=4 KnotsCount=2 Degree=3 IsPeriodic=0
    g35: BSplineCurve PolesCount=4 KnotsCount=2 Degree=3 IsPeriodic=0
    g36: BSplineCurve PolesCount=4 KnotsCount=2 Degree=3 IsPeriodic=0
    g37: BSplineCurve PolesCount=4 KnotsCount=2 Degree=3 IsPeriodic=0
    g38: BSplineCurve PolesCount=4 KnotsCount=2 Degree=3 IsPeriodic=0
    g39: BSplineCurve PolesCount=4 KnotsCount=2 Degree=3 IsPeriodic=0
    g40: BSplineCurve PolesCount=4 KnotsCount=2 Degree=3 IsPeriodic=0
    g41: BSplineCurve PolesCount=4 KnotsCount=2 Degree=3 IsPeriodic=0
    g42: BSplineCurve PolesCount=4 KnotsCount=2 Degree=3 IsPeriodic=0
    g43: BSplineCurve PolesCount=4 KnotsCount=2 Degree=3 IsPeriodic=0
    g44: BSplineCurve PolesCount=4 KnotsCount=2 Degree=3 IsPeriodic=0
    g45: BSplineCurve PolesCount=4 KnotsCount=2 Degree=3 IsPeriodic=0
    g46: BSplineCurve PolesCount=4 KnotsCount=2 Degree=3 IsPeriodic=0
    g47: BSplineCurve PolesCount=4 KnotsCount=2 Degree=3 IsPeriodic=0
    g48: BSplineCurve PolesCount=4 KnotsCount=2 Degree=3 IsPeriodic=0
    g49: BSplineCurve PolesCount=4 KnotsCount=2 Degree=3 IsPeriodic=0
    g50: BSplineCurve PolesCount=4 KnotsCount=2 Degree=3 IsPeriodic=0
    g51: BSplineCurve PolesCount=4 KnotsCount=2 Degree=3 IsPeriodic=0
    g52: BSplineCurve PolesCount=4 KnotsCount=2 Degree=3 IsPeriodic=0
    g53: BSplineCurve PolesCount=4 KnotsCount=2 Degree=3 IsPeriodic=0
    g54: BSplineCurve PolesCount=4 KnotsCount=2 Degree=3 IsPeriodic=0
    g55: BSplineCurve PolesCount=4 KnotsCount=2 Degree=3 IsPeriodic=0
    g56: BSplineCurve PolesCount=4 KnotsCount=2 Degree=3 IsPeriodic=0
    g57: BSplineCurve PolesCount=4 KnotsCount=2 Degree=3 IsPeriodic=0
    g58: BSplineCurve PolesCount=4 KnotsCount=2 Degree=3 IsPeriodic=0
    g59: BSplineCurve PolesCount=4 KnotsCount=2 Degree=3 IsPeriodic=0
    g60: BSplineCurve PolesCount=4 KnotsCount=2 Degree=3 IsPeriodic=0
    g61: BSplineCurve PolesCount=4 KnotsCount=2 Degree=3 IsPeriodic=0
    g62: BSplineCurve PolesCount=4 KnotsCount=2 Degree=3 IsPeriodic=0
    g63: BSplineCurve PolesCount=4 KnotsCount=2 Degree=3 IsPeriodic=0
    g64: BSplineCurve PolesCount=4 KnotsCount=2 Degree=3 IsPeriodic=0
    g65: BSplineCurve PolesCount=4 KnotsCount=2 Degree=3 IsPeriodic=0
    g66: BSplineCurve PolesCount=4 KnotsCount=2 Degree=3 IsPeriodic=0
    g67: BSplineCurve PolesCount=4 KnotsCount=2 Degree=3 IsPeriodic=0
    g68: BSplineCurve PolesCount=4 KnotsCount=2 Degree=3 IsPeriodic=0
    g69: BSplineCurve PolesCount=4 KnotsCount=2 Degree=3 IsPeriodic=0
    g70: BSplineCurve PolesCount=4 KnotsCount=2 Degree=3 IsPeriodic=0
    g71: BSplineCurve PolesCount=4 KnotsCount=2 Degree=3 IsPeriodic=0
    g72: BSplineCurve PolesCount=4 KnotsCount=2 Degree=3 IsPeriodic=0
    g73: BSplineCurve PolesCount=4 KnotsCount=2 Degree=3 IsPeriodic=0
    g74: BSplineCurve PolesCount=4 KnotsCount=2 Degree=3 IsPeriodic=0
    g75: BSplineCurve PolesCount=4 KnotsCount=2 Degree=3 IsPeriodic=0
    g76: BSplineCurve PolesCount=4 KnotsCount=2 Degree=3 IsPeriodic=0
    g77: BSplineCurve PolesCount=4 KnotsCount=2 Degree=3 IsPeriodic=0
    g78: BSplineCurve PolesCount=4 KnotsCount=2 Degree=3 IsPeriodic=0
    g79: BSplineCurve PolesCount=4 KnotsCount=2 Degree=3 IsPeriodic=0
    g80: BSplineCurve PolesCount=4 KnotsCount=2 Degree=3 IsPeriodic=0
    g81: BSplineCurve PolesCount=4 KnotsCount=2 Degree=3 IsPeriodic=0
    g82: BSplineCurve PolesCount=4 KnotsCount=2 Degree=3 IsPeriodic=0
    g83: BSplineCurve PolesCount=4 KnotsCount=2 Degree=3 IsPeriodic=0
    g84: BSplineCurve PolesCount=4 KnotsCount=2 Degree=3 IsPeriodic=0
    g85: BSplineCurve PolesCount=4 KnotsCount=2 Degree=3 IsPeriodic=0
    g86: BSplineCurve PolesCount=4 KnotsCount=2 Degree=3 IsPeriodic=0
    g87: BSplineCurve PolesCount=4 KnotsCount=2 Degree=3 IsPeriodic=0
    g88: BSplineCurve PolesCount=4 KnotsCount=2 Degree=3 IsPeriodic=0
    g89: BSplineCurve PolesCount=4 KnotsCount=2 Degree=3 IsPeriodic=0
    g90: BSplineCurve PolesCount=4 KnotsCount=2 Degree=3 IsPeriodic=0
    g91: BSplineCurve PolesCount=4 KnotsCount=2 Degree=3 IsPeriodic=0
    g92: BSplineCurve PolesCount=4 KnotsCount=2 Degree=3 IsPeriodic=0
    g93: BSplineCurve PolesCount=4 KnotsCount=2 Degree=3 IsPeriodic=0
    g94: BSplineCurve PolesCount=4 KnotsCount=2 Degree=3 IsPeriodic=0
    g95: BSplineCurve PolesCount=4 KnotsCount=2 Degree=3 IsPeriodic=0
    g96: BSplineCurve PolesCount=4 KnotsCount=2 Degree=3 IsPeriodic=0
    g97: BSplineCurve PolesCount=4 KnotsCount=2 Degree=3 IsPeriodic=0
    g98: BSplineCurve PolesCount=2 KnotsCount=2 Degree=1 IsPeriodic=0
    g99: BSplineCurve PolesCount=2 KnotsCount=2 Degree=1 IsPeriodic=0
    g100: BSplineCurve PolesCount=4 KnotsCount=2 Degree=3 IsPeriodic=0
    g101: BSplineCurve PolesCount=4 KnotsCount=2 Degree=3 IsPeriodic=0
    g102: BSplineCurve PolesCount=4 KnotsCount=2 Degree=3 IsPeriodic=0
    g103: BSplineCurve PolesCount=4 KnotsCount=2 Degree=3 IsPeriodic=0
    g104: BSplineCurve PolesCount=4 KnotsCount=2 Degree=3 IsPeriodic=0
    g105: BSplineCurve PolesCount=4 KnotsCount=2 Degree=3 IsPeriodic=0
    g106: BSplineCurve PolesCount=4 KnotsCount=2 Degree=3 IsPeriodic=0
    g107: BSplineCurve PolesCount=4 KnotsCount=2 Degree=3 IsPeriodic=0
    g108: BSplineCurve PolesCount=4 KnotsCount=2 Degree=3 IsPeriodic=0
    g109: BSplineCurve PolesCount=4 KnotsCount=2 Degree=3 IsPeriodic=0
    g110: BSplineCurve PolesCount=4 KnotsCount=2 Degree=3 IsPeriodic=0
    g111: BSplineCurve PolesCount=4 KnotsCount=2 Degree=3 IsPeriodic=0
    g112: BSplineCurve PolesCount=4 KnotsCount=2 Degree=3 IsPeriodic=0
    g113: BSplineCurve PolesCount=4 KnotsCount=2 Degree=3 IsPeriodic=0
    g114: BSplineCurve PolesCount=4 KnotsCount=2 Degree=3 IsPeriodic=0
    g115: BSplineCurve PolesCount=4 KnotsCount=2 Degree=3 IsPeriodic=0
    g116: BSplineCurve PolesCount=4 KnotsCount=2 Degree=3 IsPeriodic=0
    g117: BSplineCurve PolesCount=4 KnotsCount=2 Degree=3 IsPeriodic=0
    g118: BSplineCurve PolesCount=4 KnotsCount=2 Degree=3 IsPeriodic=0
    g119: BSplineCurve PolesCount=2 KnotsCount=2 Degree=1 IsPeriodic=0
    g120: BSplineCurve PolesCount=2 KnotsCount=2 Degree=1 IsPeriodic=0
    g121: BSplineCurve PolesCount=4 KnotsCount=2 Degree=3 IsPeriodic=0
    g122: BSplineCurve PolesCount=4 KnotsCount=2 Degree=3 IsPeriodic=0
    g123: BSplineCurve PolesCount=4 KnotsCount=2 Degree=3 IsPeriodic=0
    g124: BSplineCurve PolesCount=4 KnotsCount=2 Degree=3 IsPeriodic=0
    g125: BSplineCurve PolesCount=4 KnotsCount=2 Degree=3 IsPeriodic=0
    g126: BSplineCurve PolesCount=4 KnotsCount=2 Degree=3 IsPeriodic=0
    g127: BSplineCurve PolesCount=4 KnotsCount=2 Degree=3 IsPeriodic=0
    g128: BSplineCurve PolesCount=4 KnotsCount=2 Degree=3 IsPeriodic=0
    g129: BSplineCurve PolesCount=4 KnotsCount=2 Degree=3 IsPeriodic=0
    g130: BSplineCurve PolesCount=4 KnotsCount=2 Degree=3 IsPeriodic=0
    g131: BSplineCurve PolesCount=4 KnotsCount=2 Degree=3 IsPeriodic=0
    g132: BSplineCurve PolesCount=4 KnotsCount=2 Degree=3 IsPeriodic=0
    g133: BSplineCurve PolesCount=4 KnotsCount=2 Degree=3 IsPeriodic=0
    g134: BSplineCurve PolesCount=4 KnotsCount=2 Degree=3 IsPeriodic=0
    g135: BSplineCurve PolesCount=4 KnotsCount=2 Degree=3 IsPeriodic=0
    g136: BSplineCurve PolesCount=4 KnotsCount=2 Degree=3 IsPeriodic=0
    g137: BSplineCurve PolesCount=4 KnotsCount=2 Degree=3 IsPeriodic=0
    g138: BSplineCurve PolesCount=4 KnotsCount=2 Degree=3 IsPeriodic=0
    g139: BSplineCurve PolesCount=2 KnotsCount=2 Degree=1 IsPeriodic=0
    g140: BSplineCurve PolesCount=2 KnotsCount=2 Degree=1 IsPeriodic=0
    g141: BSplineCurve PolesCount=4 KnotsCount=2 Degree=3 IsPeriodic=0
    g142: BSplineCurve PolesCount=4 KnotsCount=2 Degree=3 IsPeriodic=0
    g143: BSplineCurve PolesCount=4 KnotsCount=2 Degree=3 IsPeriodic=0
    g144: BSplineCurve PolesCount=4 KnotsCount=2 Degree=3 IsPeriodic=0
    g145: BSplineCurve PolesCount=4 KnotsCount=2 Degree=3 IsPeriodic=0
    g146: BSplineCurve PolesCount=4 KnotsCount=2 Degree=3 IsPeriodic=0
    g147: BSplineCurve PolesCount=4 KnotsCount=2 Degree=3 IsPeriodic=0
    g148: BSplineCurve PolesCount=4 KnotsCount=2 Degree=3 IsPeriodic=0
    g149: BSplineCurve PolesCount=4 KnotsCount=2 Degree=3 IsPeriodic=0
    g150: BSplineCurve PolesCount=4 KnotsCount=2 Degree=3 IsPeriodic=0
    g151: BSplineCurve PolesCount=4 KnotsCount=2 Degree=3 IsPeriodic=0
    g152: BSplineCurve PolesCount=2 KnotsCount=2 Degree=1 IsPeriodic=0
    g153: BSplineCurve PolesCount=2 KnotsCount=2 Degree=1 IsPeriodic=0
    g154: BSplineCurve PolesCount=4 KnotsCount=2 Degree=3 IsPeriodic=0
    g155: BSplineCurve PolesCount=4 KnotsCount=2 Degree=3 IsPeriodic=0
    g156: BSplineCurve PolesCount=2 KnotsCount=2 Degree=1 IsPeriodic=0
    g157: BSplineCurve PolesCount=2 KnotsCount=2 Degree=1 IsPeriodic=0
    g158: BSplineCurve PolesCount=4 KnotsCount=2 Degree=3 IsPeriodic=0
    g159: BSplineCurve PolesCount=4 KnotsCount=2 Degree=3 IsPeriodic=0
    g160: BSplineCurve PolesCount=4 KnotsCount=2 Degree=3 IsPeriodic=0
    g161: BSplineCurve PolesCount=4 KnotsCount=2 Degree=3 IsPeriodic=0
    g162: BSplineCurve PolesCount=4 KnotsCount=2 Degree=3 IsPeriodic=0
    g163: BSplineCurve PolesCount=4 KnotsCount=2 Degree=3 IsPeriodic=0
    g164: BSplineCurve PolesCount=4 KnotsCount=2 Degree=3 IsPeriodic=0
    g165: BSplineCurve PolesCount=2 KnotsCount=2 Degree=1 IsPeriodic=0
    g166: BSplineCurve PolesCount=2 KnotsCount=2 Degree=1 IsPeriodic=0
    g167: BSplineCurve PolesCount=4 KnotsCount=2 Degree=3 IsPeriodic=0
    g168: BSplineCurve PolesCount=4 KnotsCount=2 Degree=3 IsPeriodic=0
    g169: BSplineCurve PolesCount=4 KnotsCount=2 Degree=3 IsPeriodic=0
    g170: BSplineCurve PolesCount=4 KnotsCount=2 Degree=3 IsPeriodic=0
    g171: BSplineCurve PolesCount=2 KnotsCount=2 Degree=1 IsPeriodic=0
    g172: BSplineCurve PolesCount=2 KnotsCount=2 Degree=1 IsPeriodic=0
    g173: BSplineCurve PolesCount=4 KnotsCount=2 Degree=3 IsPeriodic=0
    g174: BSplineCurve PolesCount=4 KnotsCount=2 Degree=3 IsPeriodic=0
    g175: BSplineCurve PolesCount=4 KnotsCount=2 Degree=3 IsPeriodic=0
    g176: BSplineCurve PolesCount=4 KnotsCount=2 Degree=3 IsPeriodic=0
    g177: BSplineCurve PolesCount=4 KnotsCount=2 Degree=3 IsPeriodic=0
    g178: BSplineCurve PolesCount=4 KnotsCount=2 Degree=3 IsPeriodic=0
    g179: BSplineCurve PolesCount=4 KnotsCount=2 Degree=3 IsPeriodic=0
    g180: BSplineCurve PolesCount=4 KnotsCount=2 Degree=3 IsPeriodic=0
    g181: BSplineCurve PolesCount=2 KnotsCount=2 Degree=1 IsPeriodic=0
    g182: BSplineCurve PolesCount=2 KnotsCount=2 Degree=1 IsPeriodic=0
    g183: BSplineCurve PolesCount=4 KnotsCount=2 Degree=3 IsPeriodic=0
    g184: BSplineCurve PolesCount=4 KnotsCount=2 Degree=3 IsPeriodic=0
    g185: BSplineCurve PolesCount=4 KnotsCount=2 Degree=3 IsPeriodic=0
    g186: BSplineCurve PolesCount=2 KnotsCount=2 Degree=1 IsPeriodic=0
    g187: BSplineCurve PolesCount=2 KnotsCount=2 Degree=1 IsPeriodic=0
    g188: BSplineCurve PolesCount=4 KnotsCount=2 Degree=3 IsPeriodic=0
    g189: BSplineCurve PolesCount=4 KnotsCount=2 Degree=3 IsPeriodic=0
    g190: BSplineCurve PolesCount=4 KnotsCount=2 Degree=3 IsPeriodic=0
    g191: BSplineCurve PolesCount=4 KnotsCount=2 Degree=3 IsPeriodic=0
    g192: BSplineCurve PolesCount=4 KnotsCount=2 Degree=3 IsPeriodic=0
    g193: BSplineCurve PolesCount=4 KnotsCount=2 Degree=3 IsPeriodic=0
    g194: BSplineCurve PolesCount=4 KnotsCount=2 Degree=3 IsPeriodic=0
    g195: BSplineCurve PolesCount=4 KnotsCount=2 Degree=3 IsPeriodic=0
    g196: BSplineCurve PolesCount=4 KnotsCount=2 Degree=3 IsPeriodic=0
    g197: BSplineCurve PolesCount=4 KnotsCount=2 Degree=3 IsPeriodic=0
    g198: BSplineCurve PolesCount=4 KnotsCount=2 Degree=3 IsPeriodic=0
    g199: BSplineCurve PolesCount=4 KnotsCount=2 Degree=3 IsPeriodic=0
    g200: BSplineCurve PolesCount=4 KnotsCount=2 Degree=3 IsPeriodic=0
    g201: BSplineCurve PolesCount=4 KnotsCount=2 Degree=3 IsPeriodic=0
    g202: BSplineCurve PolesCount=4 KnotsCount=2 Degree=3 IsPeriodic=0
    g203: BSplineCurve PolesCount=4 KnotsCount=2 Degree=3 IsPeriodic=0
    g204: BSplineCurve PolesCount=4 KnotsCount=2 Degree=3 IsPeriodic=0
    g205: BSplineCurve PolesCount=4 KnotsCount=2 Degree=3 IsPeriodic=0
    g206: BSplineCurve PolesCount=4 KnotsCount=2 Degree=3 IsPeriodic=0
    g207: BSplineCurve PolesCount=4 KnotsCount=2 Degree=3 IsPeriodic=0
    g208: BSplineCurve PolesCount=4 KnotsCount=2 Degree=3 IsPeriodic=0
    g209: BSplineCurve PolesCount=4 KnotsCount=2 Degree=3 IsPeriodic=0
    g210: BSplineCurve PolesCount=4 KnotsCount=2 Degree=3 IsPeriodic=0
    g211: BSplineCurve PolesCount=4 KnotsCount=2 Degree=3 IsPeriodic=0
    g212: BSplineCurve PolesCount=4 KnotsCount=2 Degree=3 IsPeriodic=0
    g213: BSplineCurve PolesCount=4 KnotsCount=2 Degree=3 IsPeriodic=0
    g214: BSplineCurve PolesCount=4 KnotsCount=2 Degree=3 IsPeriodic=0
    g215: BSplineCurve PolesCount=4 KnotsCount=2 Degree=3 IsPeriodic=0
    g216: BSplineCurve PolesCount=4 KnotsCount=2 Degree=3 IsPeriodic=0
    g217: BSplineCurve PolesCount=4 KnotsCount=2 Degree=3 IsPeriodic=0
    g218: BSplineCurve PolesCount=4 KnotsCount=2 Degree=3 IsPeriodic=0
    g219: BSplineCurve PolesCount=4 KnotsCount=2 Degree=3 IsPeriodic=0
    g220: BSplineCurve PolesCount=4 KnotsCount=2 Degree=3 IsPeriodic=0
    g221: BSplineCurve PolesCount=4 KnotsCount=2 Degree=3 IsPeriodic=0
    g222: BSplineCurve PolesCount=4 KnotsCount=2 Degree=3 IsPeriodic=0
    g223: BSplineCurve PolesCount=2 KnotsCount=2 Degree=1 IsPeriodic=0
    g224: BSplineCurve PolesCount=2 KnotsCount=2 Degree=1 IsPeriodic=0
    g225: BSplineCurve PolesCount=4 KnotsCount=2 Degree=3 IsPeriodic=0
    g226: BSplineCurve PolesCount=4 KnotsCount=2 Degree=3 IsPeriodic=0
    g227: BSplineCurve PolesCount=4 KnotsCount=2 Degree=3 IsPeriodic=0
    g228: BSplineCurve PolesCount=4 KnotsCount=2 Degree=3 IsPeriodic=0
    g229: BSplineCurve PolesCount=4 KnotsCount=2 Degree=3 IsPeriodic=0
    g230: BSplineCurve PolesCount=4 KnotsCount=2 Degree=3 IsPeriodic=0
    g231: BSplineCurve PolesCount=4 KnotsCount=2 Degree=3 IsPeriodic=0
    g232: BSplineCurve PolesCount=4 KnotsCount=2 Degree=3 IsPeriodic=0
    g233: BSplineCurve PolesCount=4 KnotsCount=2 Degree=3 IsPeriodic=0
    g234: BSplineCurve PolesCount=4 KnotsCount=2 Degree=3 IsPeriodic=0
    g235: BSplineCurve PolesCount=4 KnotsCount=2 Degree=3 IsPeriodic=0
    g236: BSplineCurve PolesCount=4 KnotsCount=2 Degree=3 IsPeriodic=0
    g237: BSplineCurve PolesCount=4 KnotsCount=2 Degree=3 IsPeriodic=0
    g238: BSplineCurve PolesCount=4 KnotsCount=2 Degree=3 IsPeriodic=0
    g239: BSplineCurve PolesCount=4 KnotsCount=2 Degree=3 IsPeriodic=0
    g240: BSplineCurve PolesCount=4 KnotsCount=2 Degree=3 IsPeriodic=0
    g241: BSplineCurve PolesCount=4 KnotsCount=2 Degree=3 IsPeriodic=0
    g242: BSplineCurve PolesCount=4 KnotsCount=2 Degree=3 IsPeriodic=0
    g243: BSplineCurve PolesCount=4 KnotsCount=2 Degree=3 IsPeriodic=0
    g244: BSplineCurve PolesCount=4 KnotsCount=2 Degree=3 IsPeriodic=0
    g245: BSplineCurve PolesCount=4 KnotsCount=2 Degree=3 IsPeriodic=0
    g246: BSplineCurve PolesCount=4 KnotsCount=2 Degree=3 IsPeriodic=0
    g247: BSplineCurve PolesCount=4 KnotsCount=2 Degree=3 IsPeriodic=0
    g248: BSplineCurve PolesCount=4 KnotsCount=2 Degree=3 IsPeriodic=0
    g249: BSplineCurve PolesCount=4 KnotsCount=2 Degree=3 IsPeriodic=0
    g250: BSplineCurve PolesCount=4 KnotsCount=2 Degree=3 IsPeriodic=0
    g251: BSplineCurve PolesCount=4 KnotsCount=2 Degree=3 IsPeriodic=0
    g252: BSplineCurve PolesCount=4 KnotsCount=2 Degree=3 IsPeriodic=0
    g253: BSplineCurve PolesCount=4 KnotsCount=2 Degree=3 IsPeriodic=0
    g254: BSplineCurve PolesCount=4 KnotsCount=2 Degree=3 IsPeriodic=0
    g255: BSplineCurve PolesCount=4 KnotsCount=2 Degree=3 IsPeriodic=0
    g256: BSplineCurve PolesCount=2 KnotsCount=2 Degree=1 IsPeriodic=0
    g257: BSplineCurve PolesCount=2 KnotsCount=2 Degree=1 IsPeriodic=0
    g258: BSplineCurve PolesCount=4 KnotsCount=2 Degree=3 IsPeriodic=0
    g259: BSplineCurve PolesCount=4 KnotsCount=2 Degree=3 IsPeriodic=0
    g260: BSplineCurve PolesCount=4 KnotsCount=2 Degree=3 IsPeriodic=0
    g261: BSplineCurve PolesCount=4 KnotsCount=2 Degree=3 IsPeriodic=0
    g262: BSplineCurve PolesCount=4 KnotsCount=2 Degree=3 IsPeriodic=0
    g263: BSplineCurve PolesCount=4 KnotsCount=2 Degree=3 IsPeriodic=0
    g264: BSplineCurve PolesCount=4 KnotsCount=2 Degree=3 IsPeriodic=0
    g265: BSplineCurve PolesCount=4 KnotsCount=2 Degree=3 IsPeriodic=0
    g266: BSplineCurve PolesCount=4 KnotsCount=2 Degree=3 IsPeriodic=0
    g267: BSplineCurve PolesCount=4 KnotsCount=2 Degree=3 IsPeriodic=0
    g268: BSplineCurve PolesCount=4 KnotsCount=2 Degree=3 IsPeriodic=0
    g269: BSplineCurve PolesCount=4 KnotsCount=2 Degree=3 IsPeriodic=0
    g270: BSplineCurve PolesCount=4 KnotsCount=2 Degree=3 IsPeriodic=0
    g271: BSplineCurve PolesCount=4 KnotsCount=2 Degree=3 IsPeriodic=0
    g272: BSplineCurve PolesCount=4 KnotsCount=2 Degree=3 IsPeriodic=0
    g273: BSplineCurve PolesCount=2 KnotsCount=2 Degree=1 IsPeriodic=0
    g274: BSplineCurve PolesCount=2 KnotsCount=2 Degree=1 IsPeriodic=0
    g275: BSplineCurve PolesCount=2 KnotsCount=2 Degree=1 IsPeriodic=0
    g276: BSplineCurve PolesCount=2 KnotsCount=2 Degree=1 IsPeriodic=0
    g277: BSplineCurve PolesCount=4 KnotsCount=2 Degree=3 IsPeriodic=0
    g278: BSplineCurve PolesCount=4 KnotsCount=2 Degree=3 IsPeriodic=0
    g279: BSplineCurve PolesCount=4 KnotsCount=2 Degree=3 IsPeriodic=0
    g280: BSplineCurve PolesCount=4 KnotsCount=2 Degree=3 IsPeriodic=0
    g281: BSplineCurve PolesCount=4 KnotsCount=2 Degree=3 IsPeriodic=0
    g282: BSplineCurve PolesCount=4 KnotsCount=2 Degree=3 IsPeriodic=0
    g283: BSplineCurve PolesCount=4 KnotsCount=2 Degree=3 IsPeriodic=0
    g284: BSplineCurve PolesCount=4 KnotsCount=2 Degree=3 IsPeriodic=0
    g285: BSplineCurve PolesCount=4 KnotsCount=2 Degree=3 IsPeriodic=0
    g286: BSplineCurve PolesCount=4 KnotsCount=2 Degree=3 IsPeriodic=0
    g287: BSplineCurve PolesCount=4 KnotsCount=2 Degree=3 IsPeriodic=0
    g288: BSplineCurve PolesCount=4 KnotsCount=2 Degree=3 IsPeriodic=0
    g289: BSplineCurve PolesCount=4 KnotsCount=2 Degree=3 IsPeriodic=0
    g290: BSplineCurve PolesCount=4 KnotsCount=2 Degree=3 IsPeriodic=0
    g291: BSplineCurve PolesCount=4 KnotsCount=2 Degree=3 IsPeriodic=0
    g292: BSplineCurve PolesCount=4 KnotsCount=2 Degree=3 IsPeriodic=0
    g293: BSplineCurve PolesCount=2 KnotsCount=2 Degree=1 IsPeriodic=0
    g294: BSplineCurve PolesCount=2 KnotsCount=2 Degree=1 IsPeriodic=0
    g295: BSplineCurve PolesCount=4 KnotsCount=2 Degree=3 IsPeriodic=0
    g296: BSplineCurve PolesCount=4 KnotsCount=2 Degree=3 IsPeriodic=0
    g297: BSplineCurve PolesCount=4 KnotsCount=2 Degree=3 IsPeriodic=0
    g298: BSplineCurve PolesCount=4 KnotsCount=2 Degree=3 IsPeriodic=0
    g299: BSplineCurve PolesCount=4 KnotsCount=2 Degree=3 IsPeriodic=0
    g300: BSplineCurve PolesCount=2 KnotsCount=2 Degree=1 IsPeriodic=0
    g301: BSplineCurve PolesCount=2 KnotsCount=2 Degree=1 IsPeriodic=0
    g302: BSplineCurve PolesCount=4 KnotsCount=2 Degree=3 IsPeriodic=0
    g303: BSplineCurve PolesCount=4 KnotsCount=2 Degree=3 IsPeriodic=0
    g304: BSplineCurve PolesCount=4 KnotsCount=2 Degree=3 IsPeriodic=0
    g305: BSplineCurve PolesCount=4 KnotsCount=2 Degree=3 IsPeriodic=0
    g306: BSplineCurve PolesCount=4 KnotsCount=2 Degree=3 IsPeriodic=0
    g307: BSplineCurve PolesCount=4 KnotsCount=2 Degree=3 IsPeriodic=0
    g308: BSplineCurve PolesCount=4 KnotsCount=2 Degree=3 IsPeriodic=0
    g309: BSplineCurve PolesCount=4 KnotsCount=2 Degree=3 IsPeriodic=0
    g310: BSplineCurve PolesCount=4 KnotsCount=2 Degree=3 IsPeriodic=0
    g311: BSplineCurve PolesCount=4 KnotsCount=2 Degree=3 IsPeriodic=0
    g312: BSplineCurve PolesCount=4 KnotsCount=2 Degree=3 IsPeriodic=0
    g313: BSplineCurve PolesCount=4 KnotsCount=2 Degree=3 IsPeriodic=0
    g314: BSplineCurve PolesCount=4 KnotsCount=2 Degree=3 IsPeriodic=0
    g315: BSplineCurve PolesCount=4 KnotsCount=2 Degree=3 IsPeriodic=0
    g316: BSplineCurve PolesCount=4 KnotsCount=2 Degree=3 IsPeriodic=0
    g317: BSplineCurve PolesCount=4 KnotsCount=2 Degree=3 IsPeriodic=0
    g318: BSplineCurve PolesCount=4 KnotsCount=2 Degree=3 IsPeriodic=0
    g319: BSplineCurve PolesCount=4 KnotsCount=2 Degree=3 IsPeriodic=0
    g320: BSplineCurve PolesCount=4 KnotsCount=2 Degree=3 IsPeriodic=0
    g321: BSplineCurve PolesCount=4 KnotsCount=2 Degree=3 IsPeriodic=0
    g322: BSplineCurve PolesCount=4 KnotsCount=2 Degree=3 IsPeriodic=0
    g323: BSplineCurve PolesCount=4 KnotsCount=2 Degree=3 IsPeriodic=0
    g324: BSplineCurve PolesCount=4 KnotsCount=2 Degree=3 IsPeriodic=0
    g325: BSplineCurve PolesCount=4 KnotsCount=2 Degree=3 IsPeriodic=0
    g326: BSplineCurve PolesCount=4 KnotsCount=2 Degree=3 IsPeriodic=0
    g327: BSplineCurve PolesCount=4 KnotsCount=2 Degree=3 IsPeriodic=0
    g328: BSplineCurve PolesCount=4 KnotsCount=2 Degree=3 IsPeriodic=0
    g329: BSplineCurve PolesCount=4 KnotsCount=2 Degree=3 IsPeriodic=0
    g330: BSplineCurve PolesCount=4 KnotsCount=2 Degree=3 IsPeriodic=0
  constraints (331):
    c: Coincident(g0,g1)
    c: Coincident(g1,g2)
    c: Coincident(g2,g3)
    c: Coincident(g3,g4)
    c: Coincident(g4,g5)
    c: Coincident(g5,g6)
    c: Coincident(g6,g7)
    c: Coincident(g7,g8)
    c: Coincident(g8,g9)
    c: Coincident(g9,g10)
    c: Coincident(g10,g11)
    c: Coincident(g11,g12)
    c: Coincident(g12,g13)
    c: Coincident(g13,g14)
    c: Coincident(g14,g15)
    c: Coincident(g15,g16)
    c: Coincident(g16,g17)
    c: Coincident(g17,g18)
    c: Coincident(g18,g19)
    c: Coincident(g19,g20)
    c: Coincident(g20,g21)
    c: Coincident(g21,g22)
    c: Coincident(g22,g23)
    c: Coincident(g23,g24)
    c: Coincident(g24,g25)
    c: Coincident(g25,g26)
    c: Coincident(g26,g27)
    c: Coincident(g27,g28)
    c: Coincident(g28,g29)
    c: Coincident(g29,g30)
    c: Coincident(g30,g31)
    c: Coincident(g31,g32)
    c: Coincident(g32,g33)
    c: Coincident(g33,g34)
    c: Coincident(g34,g35)
    c: Coincident(g35,g36)
    c: Coincident(g36,g37)
    c: Coincident(g37,g38)
    c: Coincident(g38,g39)
    c: Coincident(g39,g40)
    c: Coincident(g40,g41)
    c: Coincident(g41,g42)
    c: Coincident(g42,g43)
    c: Coincident(g43,g44)
    c: Coincident(g44,g45)
    c: Coincident(g45,g46)
    c: Coincident(g46,g47)
    c: Coincident(g47,g48)
    c: Coincident(g48,g49)
    c: Coincident(g49,g50)
    c: Coincident(g50,g51)
    c: Coincident(g51,g52)
    c: Coincident(g52,g53)
    c: Coincident(g53,g54)
    c: Coincident(g54,g55)
    c: Coincident(g55,g56)
    c: Coincident(g56,g57)
    c: Coincident(g57,g58)
    c: Coincident(g58,g59)
    c: Coincident(g59,g60)
    c: Coincident(g60,g61)
    c: Coincident(g61,g62)
    c: Coincident(g62,g63)
    c: Coincident(g63,g64)
    c: Coincident(g64,g65)
    c: Coincident(g65,g66)
    c: Coincident(g66,g67)
    c: Coincident(g67,g68)
    c: Coincident(g68,g69)
    c: Coincident(g69,g70)
    c: Coincident(g70,g71)
    c: Coincident(g71,g72)
    c: Coincident(g72,g73)
    c: Coincident(g73,g74)
    c: Coincident(g74,g75)
    c: Coincident(g76,g77)
    c: Coincident(g77,g78)
    c: Coincident(g78,g79)
    c: Coincident(g79,g80)
    c: Coincident(g80,g81)
    c: Coincident(g81,g82)
    c: Coincident(g82,g83)
    c: Coincident(g83,g84)
    c: Coincident(g84,g85)
    c: Coincident(g85,g86)
    c: Coincident(g86,g87)
    c: Coincident(g87,g88)
    c: Coincident(g88,g89)
    c: Coincident(g89,g90)
    c: Coincident(g90,g91)
    c: Coincident(g91,g92)
    c: Coincident(g92,g93)
    c: Coincident(g93,g94)
    c: Coincident(g94,g95)
    c: Coincident(g95,g96)
    c: Coincident(g96,g97)
    c: Coincident(g97,g98)
    c: Coincident(g98,g99)
    c: Coincident(g99,g100)
    c: Coincident(g100,g101)
    c: Coincident(g101,g102)
    c: Coincident(g102,g103)
    c: Coincident(g103,g104)
    c: Coincident(g104,g105)
    c: Coincident(g105,g106)
    c: Coincident(g106,g107)
    c: Coincident(g107,g108)
    c: Coincident(g108,g109)
    c: Coincident(g110,g111)
    c: Coincident(g111,g112)
    c: Coincident(g112,g113)
    c: Coincident(g113,g114)
    c: Coincident(g114,g115)
    c: Coincident(g115,g116)
    c: Coincident(g116,g117)
    c: Coincident(g117,g118)
    c: Coincident(g118,g119)
    c: Coincident(g119,g120)
    c: Coincident(g120,g121)
    c: Coincident(g121,g122)
    c: Coincident(g122,g123)
    c: Coincident(g123,g124)
    c: Coincident(g124,g125)
    c: Coincident(g125,g126)
    c: Coincident(g126,g127)
    c: Coincident(g127,g128)
    c: Coincident(g128,g129)
    c: Coincident(g129,g130)
    c: Coincident(g130,g131)
    c: Coincident(g132,g133)
    c: Coincident(g133,g134)
    c: Coincident(g134,g135)
    c: Coincident(g135,g136)
    c: Coincident(g136,g137)
    c: Coincident(g137,g138)
    c: Coincident(g138,g139)
    c: Coincident(g139,g140)
    c: Coincident(g140,g141)
    c: Coincident(g141,g142)
    c: Coincident(g142,g143)
    c: Coincident(g143,g144)
    c: Coincident(g144,g145)
    c: Coincident(g145,g146)
    c: Coincident(g146,g147)
    c: Coincident(g147,g132)
    c: Coincident(g148,g149)
    c: Coincident(g149,g150)
    c: Coincident(g150,g151)
    c: Coincident(g151,g152)
    c: Coincident(g152,g153)
    c: Coincident(g153,g154)
    c: Coincident(g154,g155)
    c: Coincident(g155,g156)
    c: Coincident(g156,g157)
    c: Coincident(g157,g148)
    c: Coincident(g158,g159)
    c: Coincident(g159,g160)
    c: Coincident(g160,g161)
    c: Coincident(g161,g162)
    c: Coincident(g162,g163)
    c: Coincident(g163,g164)
    c: Coincident(g164,g165)
    c: Coincident(g165,g166)
    c: Coincident(g166,g167)
    c: Coincident(g167,g168)
    c: Coincident(g168,g169)
    c: Coincident(g169,g170)
    c: Coincident(g170,g171)
    c: Coincident(g171,g172)
    c: Coincident(g172,g173)
    c: Coincident(g173,g174)
    c: Coincident(g174,g175)
    c: Coincident(g175,g176)
    c: Coincident(g176,g177)
    c: Coincident(g177,g178)
    c: Coincident(g178,g179)
    c: Coincident(g179,g158)
    c: Coincident(g180,g181)
    c: Coincident(g181,g182)
    c: Coincident(g182,g183)
    c: Coincident(g183,g184)
    c: Coincident(g184,g180)
    c: Coincident(g185,g186)
    c: Coincident(g186,g187)
    c: Coincident(g187,g188)
    c: Coincident(g188,g189)
    c: Coincident(g189,g190)
    c: Coincident(g190,g191)
    c: Coincident(g191,g192)
    c: Coincident(g192,g193)
    c: Coincident(g193,g194)
    c: Coincident(g194,g195)
    c: Coincident(g195,g196)
    c: Coincident(g196,g197)
    c: Coincident(g197,g198)
    c: Coincident(g198,g199)
    c: Coincident(g199,g185)
    c: Coincident(g200,g201)
    c: Coincident(g201,g202)
    c: Coincident(g202,g203)
    c: Coincident(g203,g204)
    c: Coincident(g204,g205)
    c: Coincident(g205,g206)
    c: Coincident(g206,g207)
    c: Coincident(g207,g200)
    c: Coincident(g208,g209)
    c: Coincident(g209,g210)
    c: Coincident(g210,g211)
    c: Coincident(g211,g212)
    c: Coincident(g212,g213)
    c: Coincident(g213,g208)
    c: Coincident(g214,g215)
    c: Coincident(g215,g216)
    c: Coincident(g216,g217)
    c: Coincident(g217,g218)
    c: Coincident(g218,g219)
    c: Coincident(g219,g220)
    c: Coincident(g220,g221)
    c: Coincident(g221,g222)
    c: Coincident(g222,g223)
    c: Coincident(g223,g224)
    c: Coincident(g224,g225)
    c: Coincident(g226,g227)
    c: Coincident(g227,g228)
    c: Coincident(g228,g226)
    c: Coincident(g229,g230)
    c: Coincident(g230,g231)
    c: Coincident(g231,g232)
    c: Coincident(g232,g233)
    c: Coincident(g233,g234)
    c: Coincident(g234,g235)
    c: Coincident(g235,g236)
    c: Coincident(g236,g237)
    c: Coincident(g237,g238)
    c: Coincident(g238,g239)
    c: Coincident(g239,g240)
    c: Coincident(g240,g241)
    c: Coincident(g241,g242)
    c: Coincident(g242,g243)
    c: Coincident(g243,g244)
    c: Coincident(g244,g245)
    c: Coincident(g245,g246)
    c: Coincident(g246,g247)
    c: Coincident(g247,g248)
    c: Coincident(g248,g249)
    c: Coincident(g249,g250)
    c: Coincident(g250,g251)
    c: Coincident(g251,g252)
    c: Coincident(g252,g253)
    c: Coincident(g253,g254)
    c: Coincident(g254,g255)
    c: Coincident(g255,g256)
    c: Coincident(g256,g257)
    c: Coincident(g257,g258)
    c: Coincident(g259,g260)
    c: Coincident(g260,g261)
    c: Coincident(g261,g262)
    c: Coincident(g262,g263)
    c: Coincident(g263,g264)
    c: Coincident(g264,g265)
    c: Coincident(g265,g266)
    c: Coincident(g266,g267)
    c: Coincident(g267,g268)
    c: Coincident(g268,g269)
    c: Coincident(g269,g259)
    c: Coincident(g270,g271)
    c: Coincident(g271,g272)
    c: Coincident(g272,g273)
    c: Coincident(g273,g274)
    c: Coincident(g274,g275)
    c: Coincident(g275,g276)
    c: Coincident(g276,g277)
    c: Coincident(g277,g278)
    c: Coincident(g278,g279)
    c: Coincident(g279,g280)
    c: Coincident(g280,g281)
    c: Coincident(g281,g282)
    c: Coincident(g282,g283)
    c: Coincident(g283,g284)
    c: Coincident(g284,g285)
    c: Coincident(g285,g286)
    c: Coincident(g286,g287)
    c: Coincident(g287,g288)
    c: Coincident(g288,g289)
    c: Coincident(g289,g290)
    c: Coincident(g290,g291)
    c: Coincident(g291,g292)
    c: Coincident(g292,g293)
    c: Coincident(g293,g294)
    c: Coincident(g294,g295)
    c: Coincident(g295,g296)
    c: Coincident(g296,g297)
    c: Coincident(g297,g298)
    c: Coincident(g298,g299)
    c: Coincident(g299,g300)
    c: Coincident(g300,g301)
    c: Coincident(g301,g302)
    c: Coincident(g302,g303)
    c: Coincident(g303,g304)
    c: Coincident(g304,g305)
    c: Coincident(g305,g306)
    c: Coincident(g306,g307)
    c: Coincident(g307,g308)
    c: Coincident(g308,g309)
    c: Coincident(g309,g270)
    c: Coincident(g310,g311)
    c: Coincident(g311,g312)
    c: Coincident(g312,g313)
    c: Coincident(g313,g314)
    c: Coincident(g314,g315)
    c: Coincident(g315,g316)
    c: Coincident(g316,g317)
    c: Coincident(g317,g318)
    c: Coincident(g318,g319)
    c: Coincident(g320,g321)
    c: Coincident(g321,g322)
    c: Coincident(g322,g323)
    c: Coincident(g323,g324)
    c: Coincident(g324,g325)
    c: Coincident(g325,g326)
    c: Coincident(g326,g327)
    c: Coincident(g327,g320)
    c: Coincident(g328,g329)
    c: Coincident(g329,g330)
    c: Coincident(g75,g0)
    c: Coincident(g229,g258)
    c: Coincident(g214,g225)
    c: Coincident(g328,g330)
    c: Coincident(g110,g131)
    c: Coincident(g310,g319)
    c: Coincident(g76,g109)
FEATURE [Sketcher::SketchObject] Sketch038  label="Mutant-Sketch"
  ArcFitTolerance = 1e-06
  FullyConstrained = false
  MakeInternals = false
  Placement = pos=(-11.9753,14.2872,0) rot=(0,0,1;0rad)
  expr: .Placement.Base.x = -(.Shape.BoundBox.XLength / 2)
  expr: .Placement.Base.y = .Shape.BoundBox.YLength / 2
  sketch-geometry (428):
    g0: BSplineCurve PolesCount=4 KnotsCount=2 Degree=3 IsPeriodic=0
    g1: BSplineCurve PolesCount=4 KnotsCount=2 Degree=3 IsPeriodic=0
    g2: BSplineCurve PolesCount=4 KnotsCount=2 Degree=3 IsPeriodic=0
    g3: BSplineCurve PolesCount=4 KnotsCount=2 Degree=3 IsPeriodic=0
    g4: BSplineCurve PolesCount=4 KnotsCount=2 Degree=3 IsPeriodic=0
    g5: BSplineCurve PolesCount=4 KnotsCount=2 Degree=3 IsPeriodic=0
    g6: BSplineCurve PolesCount=4 KnotsCount=2 Degree=3 IsPeriodic=0
    g7: BSplineCurve PolesCount=4 KnotsCount=2 Degree=3 IsPeriodic=0
    g8: BSplineCurve PolesCount=4 KnotsCount=2 Degree=3 IsPeriodic=0
    g9: BSplineCurve PolesCount=4 KnotsCount=2 Degree=3 IsPeriodic=0
    g10: BSplineCurve PolesCount=4 KnotsCount=2 Degree=3 IsPeriodic=0
    g11: BSplineCurve PolesCount=4 KnotsCount=2 Degree=3 IsPeriodic=0
    g12: BSplineCurve PolesCount=4 KnotsCount=2 Degree=3 IsPeriodic=0
    g13: BSplineCurve PolesCount=4 KnotsCount=2 Degree=3 IsPeriodic=0
    g14: BSplineCurve PolesCount=4 KnotsCount=2 Degree=3 IsPeriodic=0
    g15: BSplineCurve PolesCount=4 KnotsCount=2 Degree=3 IsPeriodic=0
    g16: BSplineCurve PolesCount=2 KnotsCount=2 Degree=1 IsPeriodic=0
    g17: BSplineCurve PolesCount=2 KnotsCount=2 Degree=1 IsPeriodic=0
    g18: BSplineCurve PolesCount=4 KnotsCount=2 Degree=3 IsPeriodic=0
    g19: BSplineCurve PolesCount=4 KnotsCount=2 Degree=3 IsPeriodic=0
    g20: BSplineCurve PolesCount=4 KnotsCount=2 Degree=3 IsPeriodic=0
    g21: BSplineCurve PolesCount=4 KnotsCount=2 Degree=3 IsPeriodic=0
    g22: BSplineCurve PolesCount=4 KnotsCount=2 Degree=3 IsPeriodic=0
    g23: BSplineCurve PolesCount=4 KnotsCount=2 Degree=3 IsPeriodic=0
    g24: BSplineCurve PolesCount=4 KnotsCount=2 Degree=3 IsPeriodic=0
    g25: BSplineCurve PolesCount=4 KnotsCount=2 Degree=3 IsPeriodic=0
    g26: BSplineCurve PolesCount=4 KnotsCount=2 Degree=3 IsPeriodic=0
    g27: BSplineCurve PolesCount=4 KnotsCount=2 Degree=3 IsPeriodic=0
    g28: BSplineCurve PolesCount=4 KnotsCount=2 Degree=3 IsPeriodic=0
    g29: BSplineCurve PolesCount=4 KnotsCount=2 Degree=3 IsPeriodic=0
    g30: BSplineCurve PolesCount=4 KnotsCount=2 Degree=3 IsPeriodic=0
    g31: BSplineCurve PolesCount=4 KnotsCount=2 Degree=3 IsPeriodic=0
    g32: BSplineCurve PolesCount=4 KnotsCount=2 Degree=3 IsPeriodic=0
    g33: BSplineCurve PolesCount=4 KnotsCount=2 Degree=3 IsPeriodic=0
    g34: BSplineCurve PolesCount=4 KnotsCount=2 Degree=3 IsPeriodic=0
    g35: BSplineCurve PolesCount=4 KnotsCount=2 Degree=3 IsPeriodic=0
    g36: BSplineCurve PolesCount=4 KnotsCount=2 Degree=3 IsPeriodic=0
    g37: BSplineCurve PolesCount=4 KnotsCount=2 Degree=3 IsPeriodic=0
    g38: BSplineCurve PolesCount=4 KnotsCount=2 Degree=3 IsPeriodic=0
    g39: BSplineCurve PolesCount=2 KnotsCount=2 Degree=1 IsPeriodic=0
    g40: BSplineCurve PolesCount=2 KnotsCount=2 Degree=1 IsPeriodic=0
    g41: BSplineCurve PolesCount=4 KnotsCount=2 Degree=3 IsPeriodic=0
    g42: BSplineCurve PolesCount=4 KnotsCount=2 Degree=3 IsPeriodic=0
    g43: BSplineCurve PolesCount=4 KnotsCount=2 Degree=3 IsPeriodic=0
    g44: BSplineCurve PolesCount=4 KnotsCount=2 Degree=3 IsPeriodic=0
    g45: BSplineCurve PolesCount=4 KnotsCount=2 Degree=3 IsPeriodic=0
    g46: BSplineCurve PolesCount=4 KnotsCount=2 Degree=3 IsPeriodic=0
    g47: BSplineCurve PolesCount=4 KnotsCount=2 Degree=3 IsPeriodic=0
    g48: BSplineCurve PolesCount=4 KnotsCount=2 Degree=3 IsPeriodic=0
    g49: BSplineCurve PolesCount=4 KnotsCount=2 Degree=3 IsPeriodic=0
    g50: BSplineCurve PolesCount=4 KnotsCount=2 Degree=3 IsPeriodic=0
    g51: BSplineCurve PolesCount=4 KnotsCount=2 Degree=3 IsPeriodic=0
    g52: BSplineCurve PolesCount=4 KnotsCount=2 Degree=3 IsPeriodic=0
    g53: BSplineCurve PolesCount=4 KnotsCount=2 Degree=3 IsPeriodic=0
    g54: BSplineCurve PolesCount=4 KnotsCount=2 Degree=3 IsPeriodic=0
    g55: BSplineCurve PolesCount=4 KnotsCount=2 Degree=3 IsPeriodic=0
    g56: BSplineCurve PolesCount=4 KnotsCount=2 Degree=3 IsPeriodic=0
    g57: BSplineCurve PolesCount=4 KnotsCount=2 Degree=3 IsPeriodic=0
    g58: BSplineCurve PolesCount=4 KnotsCount=2 Degree=3 IsPeriodic=0
    g59: BSplineCurve PolesCount=4 KnotsCount=2 Degree=3 IsPeriodic=0
    g60: BSplineCurve PolesCount=4 KnotsCount=2 Degree=3 IsPeriodic=0
    g61: BSplineCurve PolesCount=4 KnotsCount=2 Degree=3 IsPeriodic=0
    g62: BSplineCurve PolesCount=4 KnotsCount=2 Degree=3 IsPeriodic=0
    g63: BSplineCurve PolesCount=4 KnotsCount=2 Degree=3 IsPeriodic=0
    g64: BSplineCurve PolesCount=4 KnotsCount=2 Degree=3 IsPeriodic=0
    g65: BSplineCurve PolesCount=4 KnotsCount=2 Degree=3 IsPeriodic=0
    g66: BSplineCurve PolesCount=4 KnotsCount=2 Degree=3 IsPeriodic=0
    g67: BSplineCurve PolesCount=4 KnotsCount=2 Degree=3 IsPeriodic=0
    g68: BSplineCurve PolesCount=4 KnotsCount=2 Degree=3 IsPeriodic=0
    g69: BSplineCurve PolesCount=4 KnotsCount=2 Degree=3 IsPeriodic=0
    g70: BSplineCurve PolesCount=4 KnotsCount=2 Degree=3 IsPeriodic=0
    g71: BSplineCurve PolesCount=4 KnotsCount=2 Degree=3 IsPeriodic=0
    g72: BSplineCurve PolesCount=4 KnotsCount=2 Degree=3 IsPeriodic=0
    g73: BSplineCurve PolesCount=4 KnotsCount=2 Degree=3 IsPeriodic=0
    g74: BSplineCurve PolesCount=4 KnotsCount=2 Degree=3 IsPeriodic=0
    g75: BSplineCurve PolesCount=4 KnotsCount=2 Degree=3 IsPeriodic=0
    g76: BSplineCurve PolesCount=4 KnotsCount=2 Degree=3 IsPeriodic=0
    g77: BSplineCurve PolesCount=4 KnotsCount=2 Degree=3 IsPeriodic=0
    g78: BSplineCurve PolesCount=4 KnotsCount=2 Degree=3 IsPeriodic=0
    g79: BSplineCurve PolesCount=4 KnotsCount=2 Degree=3 IsPeriodic=0
    g80: BSplineCurve PolesCount=4 KnotsCount=2 Degree=3 IsPeriodic=0
    g81: BSplineCurve PolesCount=4 KnotsCount=2 Degree=3 IsPeriodic=0
    g82: BSplineCurve PolesCount=4 KnotsCount=2 Degree=3 IsPeriodic=0
    g83: BSplineCurve PolesCount=4 KnotsCount=2 Degree=3 IsPeriodic=0
    g84: BSplineCurve PolesCount=4 KnotsCount=2 Degree=3 IsPeriodic=0
    g85: BSplineCurve PolesCount=4 KnotsCount=2 Degree=3 IsPeriodic=0
    g86: BSplineCurve PolesCount=4 KnotsCount=2 Degree=3 IsPeriodic=0
    g87: BSplineCurve PolesCount=4 KnotsCount=2 Degree=3 IsPeriodic=0
    g88: BSplineCurve PolesCount=4 KnotsCount=2 Degree=3 IsPeriodic=0
    g89: BSplineCurve PolesCount=4 KnotsCount=2 Degree=3 IsPeriodic=0
    g90: BSplineCurve PolesCount=4 KnotsCount=2 Degree=3 IsPeriodic=0
    g91: BSplineCurve PolesCount=4 KnotsCount=2 Degree=3 IsPeriodic=0
    g92: BSplineCurve PolesCount=4 KnotsCount=2 Degree=3 IsPeriodic=0
    g93: BSplineCurve PolesCount=4 KnotsCount=2 Degree=3 IsPeriodic=0
    g94: BSplineCurve PolesCount=4 KnotsCount=2 Degree=3 IsPeriodic=0
    g95: BSplineCurve PolesCount=4 KnotsCount=2 Degree=3 IsPeriodic=0
    g96: BSplineCurve PolesCount=4 KnotsCount=2 Degree=3 IsPeriodic=0
    g97: BSplineCurve PolesCount=4 KnotsCount=2 Degree=3 IsPeriodic=0
    g98: BSplineCurve PolesCount=4 KnotsCount=2 Degree=3 IsPeriodic=0
    g99: BSplineCurve PolesCount=4 KnotsCount=2 Degree=3 IsPeriodic=0
    g100: BSplineCurve PolesCount=4 KnotsCount=2 Degree=3 IsPeriodic=0
    g101: BSplineCurve PolesCount=4 KnotsCount=2 Degree=3 IsPeriodic=0
    g102: BSplineCurve PolesCount=4 KnotsCount=2 Degree=3 IsPeriodic=0
    g103: BSplineCurve PolesCount=4 KnotsCount=2 Degree=3 IsPeriodic=0
    g104: BSplineCurve PolesCount=4 KnotsCount=2 Degree=3 IsPeriodic=0
    g105: BSplineCurve PolesCount=4 KnotsCount=2 Degree=3 IsPeriodic=0
    g106: BSplineCurve PolesCount=4 KnotsCount=2 Degree=3 IsPeriodic=0
    g107: BSplineCurve PolesCount=4 KnotsCount=2 Degree=3 IsPeriodic=0
    g108: BSplineCurve PolesCount=4 KnotsCount=2 Degree=3 IsPeriodic=0
    g109: BSplineCurve PolesCount=4 KnotsCount=2 Degree=3 IsPeriodic=0
    g110: BSplineCurve PolesCount=2 KnotsCount=2 Degree=1 IsPeriodic=0
    g111: BSplineCurve PolesCount=2 KnotsCount=2 Degree=1 IsPeriodic=0
    g112: BSplineCurve PolesCount=4 KnotsCount=2 Degree=3 IsPeriodic=0
    g113: BSplineCurve PolesCount=4 KnotsCount=2 Degree=3 IsPeriodic=0
    g114: BSplineCurve PolesCount=4 KnotsCount=2 Degree=3 IsPeriodic=0
    g115: BSplineCurve PolesCount=4 KnotsCount=2 Degree=3 IsPeriodic=0
    g116: BSplineCurve PolesCount=4 KnotsCount=2 Degree=3 IsPeriodic=0
    g117: BSplineCurve PolesCount=4 KnotsCount=2 Degree=3 IsPeriodic=0
    g118: BSplineCurve PolesCount=4 KnotsCount=2 Degree=3 IsPeriodic=0
    g119: BSplineCurve PolesCount=4 KnotsCount=2 Degree=3 IsPeriodic=0
    g120: BSplineCurve PolesCount=4 KnotsCount=2 Degree=3 IsPeriodic=0
    g121: BSplineCurve PolesCount=4 KnotsCount=2 Degree=3 IsPeriodic=0
    g122: BSplineCurve PolesCount=4 KnotsCount=2 Degree=3 IsPeriodic=0
    g123: BSplineCurve PolesCount=4 KnotsCount=2 Degree=3 IsPeriodic=0
    g124: BSplineCurve PolesCount=4 KnotsCount=2 Degree=3 IsPeriodic=0
    g125: BSplineCurve PolesCount=4 KnotsCount=2 Degree=3 IsPeriodic=0
    g126: BSplineCurve PolesCount=4 KnotsCount=2 Degree=3 IsPeriodic=0
    g127: BSplineCurve PolesCount=2 KnotsCount=2 Degree=1 IsPeriodic=0
    g128: BSplineCurve PolesCount=2 KnotsCount=2 Degree=1 IsPeriodic=0
    g129: BSplineCurve PolesCount=4 KnotsCount=2 Degree=3 IsPeriodic=0
    g130: BSplineCurve PolesCount=4 KnotsCount=2 Degree=3 IsPeriodic=0
    g131: BSplineCurve PolesCount=4 KnotsCount=2 Degree=3 IsPeriodic=0
    g132: BSplineCurve PolesCount=4 KnotsCount=2 Degree=3 IsPeriodic=0
    g133: BSplineCurve PolesCount=4 KnotsCount=2 Degree=3 IsPeriodic=0
    g134: BSplineCurve PolesCount=4 KnotsCount=2 Degree=3 IsPeriodic=0
    g135: BSplineCurve PolesCount=4 KnotsCount=2 Degree=3 IsPeriodic=0
    g136: BSplineCurve PolesCount=4 KnotsCount=2 Degree=3 IsPeriodic=0
    g137: BSplineCurve PolesCount=2 KnotsCount=2 Degree=1 IsPeriodic=0
    g138: BSplineCurve PolesCount=2 KnotsCount=2 Degree=1 IsPeriodic=0
    g139: BSplineCurve PolesCount=4 KnotsCount=2 Degree=3 IsPeriodic=0
    g140: BSplineCurve PolesCount=4 KnotsCount=2 Degree=3 IsPeriodic=0
    g141: BSplineCurve PolesCount=4 KnotsCount=2 Degree=3 IsPeriodic=0
    g142: BSplineCurve PolesCount=4 KnotsCount=2 Degree=3 IsPeriodic=0
    g143: BSplineCurve PolesCount=4 KnotsCount=2 Degree=3 IsPeriodic=0
    g144: BSplineCurve PolesCount=4 KnotsCount=2 Degree=3 IsPeriodic=0
    g145: BSplineCurve PolesCount=4 KnotsCount=2 Degree=3 IsPeriodic=0
    g146: BSplineCurve PolesCount=4 KnotsCount=2 Degree=3 IsPeriodic=0
    g147: BSplineCurve PolesCount=4 KnotsCount=2 Degree=3 IsPeriodic=0
    g148: BSplineCurve PolesCount=4 KnotsCount=2 Degree=3 IsPeriodic=0
    g149: BSplineCurve PolesCount=4 KnotsCount=2 Degree=3 IsPeriodic=0
    g150: BSplineCurve PolesCount=4 KnotsCount=2 Degree=3 IsPeriodic=0
    g151: BSplineCurve PolesCount=4 KnotsCount=2 Degree=3 IsPeriodic=0
    g152: BSplineCurve PolesCount=4 KnotsCount=2 Degree=3 IsPeriodic=0
    g153: BSplineCurve PolesCount=4 KnotsCount=2 Degree=3 IsPeriodic=0
    g154: BSplineCurve PolesCount=4 KnotsCount=2 Degree=3 IsPeriodic=0
    g155: BSplineCurve PolesCount=4 KnotsCount=2 Degree=3 IsPeriodic=0
    g156: BSplineCurve PolesCount=4 KnotsCount=2 Degree=3 IsPeriodic=0
    g157: BSplineCurve PolesCount=4 KnotsCount=2 Degree=3 IsPeriodic=0
    g158: BSplineCurve PolesCount=4 KnotsCount=2 Degree=3 IsPeriodic=0
    g159: BSplineCurve PolesCount=4 KnotsCount=2 Degree=3 IsPeriodic=0
    g160: BSplineCurve PolesCount=4 KnotsCount=2 Degree=3 IsPeriodic=0
    g161: BSplineCurve PolesCount=4 KnotsCount=2 Degree=3 IsPeriodic=0
    g162: BSplineCurve PolesCount=4 KnotsCount=2 Degree=3 IsPeriodic=0
    g163: BSplineCurve PolesCount=4 KnotsCount=2 Degree=3 IsPeriodic=0
    g164: BSplineCurve PolesCount=4 KnotsCount=2 Degree=3 IsPeriodic=0
    g165: BSplineCurve PolesCount=4 KnotsCount=2 Degree=3 IsPeriodic=0
    g166: BSplineCurve PolesCount=4 KnotsCount=2 Degree=3 IsPeriodic=0
    g167: BSplineCurve PolesCount=4 KnotsCount=2 Degree=3 IsPeriodic=0
    g168: BSplineCurve PolesCount=4 KnotsCount=2 Degree=3 IsPeriodic=0
    g169: BSplineCurve PolesCount=4 KnotsCount=2 Degree=3 IsPeriodic=0
    g170: BSplineCurve PolesCount=4 KnotsCount=2 Degree=3 IsPeriodic=0
    g171: BSplineCurve PolesCount=4 KnotsCount=2 Degree=3 IsPeriodic=0
    g172: BSplineCurve PolesCount=4 KnotsCount=2 Degree=3 IsPeriodic=0
    g173: BSplineCurve PolesCount=4 KnotsCount=2 Degree=3 IsPeriodic=0
    g174: BSplineCurve PolesCount=4 KnotsCount=2 Degree=3 IsPeriodic=0
    g175: BSplineCurve PolesCount=4 KnotsCount=2 Degree=3 IsPeriodic=0
    g176: BSplineCurve PolesCount=4 KnotsCount=2 Degree=3 IsPeriodic=0
    g177: BSplineCurve PolesCount=4 KnotsCount=2 Degree=3 IsPeriodic=0
    g178: BSplineCurve PolesCount=4 KnotsCount=2 Degree=3 IsPeriodic=0
    g179: BSplineCurve PolesCount=4 KnotsCount=2 Degree=3 IsPeriodic=0
    g180: BSplineCurve PolesCount=4 KnotsCount=2 Degree=3 IsPeriodic=0
    g181: BSplineCurve PolesCount=4 KnotsCount=2 Degree=3 IsPeriodic=0
    g182: BSplineCurve PolesCount=4 KnotsCount=2 Degree=3 IsPeriodic=0
    g183: BSplineCurve PolesCount=4 KnotsCount=2 Degree=3 IsPeriodic=0
    g184: BSplineCurve PolesCount=4 KnotsCount=2 Degree=3 IsPeriodic=0
    g185: BSplineCurve PolesCount=4 KnotsCount=2 Degree=3 IsPeriodic=0
    g186: BSplineCurve PolesCount=4 KnotsCount=2 Degree=3 IsPeriodic=0
    g187: BSplineCurve PolesCount=4 KnotsCount=2 Degree=3 IsPeriodic=0
    g188: BSplineCurve PolesCount=4 KnotsCount=2 Degree=3 IsPeriodic=0
    g189: BSplineCurve PolesCount=4 KnotsCount=2 Degree=3 IsPeriodic=0
    g190: BSplineCurve PolesCount=4 KnotsCount=2 Degree=3 IsPeriodic=0
    g191: BSplineCurve PolesCount=4 KnotsCount=2 Degree=3 IsPeriodic=0
    g192: BSplineCurve PolesCount=4 KnotsCount=2 Degree=3 IsPeriodic=0
    g193: BSplineCurve PolesCount=4 KnotsCount=2 Degree=3 IsPeriodic=0
    g194: BSplineCurve PolesCount=4 KnotsCount=2 Degree=3 IsPeriodic=0
    g195: BSplineCurve PolesCount=4 KnotsCount=2 Degree=3 IsPeriodic=0
    g196: BSplineCurve PolesCount=4 KnotsCount=2 Degree=3 IsPeriodic=0
    g197: BSplineCurve PolesCount=4 KnotsCount=2 Degree=3 IsPeriodic=0
    g198: BSplineCurve PolesCount=4 KnotsCount=2 Degree=3 IsPeriodic=0
    g199: BSplineCurve PolesCount=4 KnotsCount=2 Degree=3 IsPeriodic=0
    g200: BSplineCurve PolesCount=4 KnotsCount=2 Degree=3 IsPeriodic=0
    g201: BSplineCurve PolesCount=4 KnotsCount=2 Degree=3 IsPeriodic=0
    g202: BSplineCurve PolesCount=4 KnotsCount=2 Degree=3 IsPeriodic=0
    g203: BSplineCurve PolesCount=4 KnotsCount=2 Degree=3 IsPeriodic=0
    g204: BSplineCurve PolesCount=4 KnotsCount=2 Degree=3 IsPeriodic=0
    g205: BSplineCurve PolesCount=4 KnotsCount=2 Degree=3 IsPeriodic=0
    g206: BSplineCurve PolesCount=4 KnotsCount=2 Degree=3 IsPeriodic=0
    g207: BSplineCurve PolesCount=4 KnotsCount=2 Degree=3 IsPeriodic=0
    g208: BSplineCurve PolesCount=4 KnotsCount=2 Degree=3 IsPeriodic=0
    g209: BSplineCurve PolesCount=4 KnotsCount=2 Degree=3 IsPeriodic=0
    g210: BSplineCurve PolesCount=4 KnotsCount=2 Degree=3 IsPeriodic=0
    g211: BSplineCurve PolesCount=4 KnotsCount=2 Degree=3 IsPeriodic=0
    g212: BSplineCurve PolesCount=4 KnotsCount=2 Degree=3 IsPeriodic=0
    g213: BSplineCurve PolesCount=4 KnotsCount=2 Degree=3 IsPeriodic=0
    g214: BSplineCurve PolesCount=4 KnotsCount=2 Degree=3 IsPeriodic=0
    g215: BSplineCurve PolesCount=4 KnotsCount=2 Degree=3 IsPeriodic=0
    g216: BSplineCurve PolesCount=4 KnotsCount=2 Degree=3 IsPeriodic=0
    g217: BSplineCurve PolesCount=4 KnotsCount=2 Degree=3 IsPeriodic=0
    g218: BSplineCurve PolesCount=4 KnotsCount=2 Degree=3 IsPeriodic=0
    g219: BSplineCurve PolesCount=4 KnotsCount=2 Degree=3 IsPeriodic=0
    g220: BSplineCurve PolesCount=4 KnotsCount=2 Degree=3 IsPeriodic=0
    g221: BSplineCurve PolesCount=4 KnotsCount=2 Degree=3 IsPeriodic=0
    g222: BSplineCurve PolesCount=4 KnotsCount=2 Degree=3 IsPeriodic=0
    g223: BSplineCurve PolesCount=4 KnotsCount=2 Degree=3 IsPeriodic=0
    g224: BSplineCurve PolesCount=4 KnotsCount=2 Degree=3 IsPeriodic=0
    g225: BSplineCurve PolesCount=4 KnotsCount=2 Degree=3 IsPeriodic=0
    g226: BSplineCurve PolesCount=4 KnotsCount=2 Degree=3 IsPeriodic=0
    g227: BSplineCurve PolesCount=4 KnotsCount=2 Degree=3 IsPeriodic=0
    g228: BSplineCurve PolesCount=4 KnotsCount=2 Degree=3 IsPeriodic=0
    g229: BSplineCurve PolesCount=4 KnotsCount=2 Degree=3 IsPeriodic=0
    g230: BSplineCurve PolesCount=2 KnotsCount=2 Degree=1 IsPeriodic=0
    g231: BSplineCurve PolesCount=4 KnotsCount=2 Degree=3 IsPeriodic=0
    g232: BSplineCurve PolesCount=4 KnotsCount=2 Degree=3 IsPeriodic=0
    g233: BSplineCurve PolesCount=4 KnotsCount=2 Degree=3 IsPeriodic=0
    g234: BSplineCurve PolesCount=4 KnotsCount=2 Degree=3 IsPeriodic=0
    g235: BSplineCurve PolesCount=4 KnotsCount=2 Degree=3 IsPeriodic=0
    g236: BSplineCurve PolesCount=2 KnotsCount=2 Degree=1 IsPeriodic=0
    g237: BSplineCurve PolesCount=2 KnotsCount=2 Degree=1 IsPeriodic=0
    g238: BSplineCurve PolesCount=2 KnotsCount=2 Degree=1 IsPeriodic=0
    g239: BSplineCurve PolesCount=4 KnotsCount=2 Degree=3 IsPeriodic=0
    g240: BSplineCurve PolesCount=2 KnotsCount=2 Degree=1 IsPeriodic=0
    g241: BSplineCurve PolesCount=2 KnotsCount=2 Degree=1 IsPeriodic=0
    g242: BSplineCurve PolesCount=2 KnotsCount=2 Degree=1 IsPeriodic=0
    g243: BSplineCurve PolesCount=2 KnotsCount=2 Degree=1 IsPeriodic=0
    g244: BSplineCurve PolesCount=2 KnotsCount=2 Degree=1 IsPeriodic=0
    g245: BSplineCurve PolesCount=2 KnotsCount=2 Degree=1 IsPeriodic=0
    g246: BSplineCurve PolesCount=4 KnotsCount=2 Degree=3 IsPeriodic=0
    g247: BSplineCurve PolesCount=4 KnotsCount=2 Degree=3 IsPeriodic=0
    g248: BSplineCurve PolesCount=4 KnotsCount=2 Degree=3 IsPeriodic=0
    g249: BSplineCurve PolesCount=4 KnotsCount=2 Degree=3 IsPeriodic=0
    g250: BSplineCurve PolesCount=4 KnotsCount=2 Degree=3 IsPeriodic=0
    g251: BSplineCurve PolesCount=4 KnotsCount=2 Degree=3 IsPeriodic=0
    g252: BSplineCurve PolesCount=4 KnotsCount=2 Degree=3 IsPeriodic=0
    g253: BSplineCurve PolesCount=4 KnotsCount=2 Degree=3 IsPeriodic=0
    g254: BSplineCurve PolesCount=4 KnotsCount=2 Degree=3 IsPeriodic=0
    g255: BSplineCurve PolesCount=4 KnotsCount=2 Degree=3 IsPeriodic=0
    g256: BSplineCurve PolesCount=4 KnotsCount=2 Degree=3 IsPeriodic=0
    g257: BSplineCurve PolesCount=4 KnotsCount=2 Degree=3 IsPeriodic=0
    g258: BSplineCurve PolesCount=4 KnotsCount=2 Degree=3 IsPeriodic=0
    g259: BSplineCurve PolesCount=4 KnotsCount=2 Degree=3 IsPeriodic=0
    g260: BSplineCurve PolesCount=2 KnotsCount=2 Degree=1 IsPeriodic=0
    g261: BSplineCurve PolesCount=2 KnotsCount=2 Degree=1 IsPeriodic=0
    g262: BSplineCurve PolesCount=2 KnotsCount=2 Degree=1 IsPeriodic=0
    g263: BSplineCurve PolesCount=2 KnotsCount=2 Degree=1 IsPeriodic=0
    g264: BSplineCurve PolesCount=2 KnotsCount=2 Degree=1 IsPeriodic=0
    g265: BSplineCurve PolesCount=2 KnotsCount=2 Degree=1 IsPeriodic=0
    g266: BSplineCurve PolesCount=2 KnotsCount=2 Degree=1 IsPeriodic=0
    g267: BSplineCurve PolesCount=2 KnotsCount=2 Degree=1 IsPeriodic=0
    g268: BSplineCurve PolesCount=4 KnotsCount=2 Degree=3 IsPeriodic=0
    g269: BSplineCurve PolesCount=4 KnotsCount=2 Degree=3 IsPeriodic=0
    g270: BSplineCurve PolesCount=4 KnotsCount=2 Degree=3 IsPeriodic=0
    g271: BSplineCurve PolesCount=4 KnotsCount=2 Degree=3 IsPeriodic=0
    g272: BSplineCurve PolesCount=4 KnotsCount=2 Degree=3 IsPeriodic=0
    g273: BSplineCurve PolesCount=4 KnotsCount=2 Degree=3 IsPeriodic=0
    g274: BSplineCurve PolesCount=4 KnotsCount=2 Degree=3 IsPeriodic=0
    g275: BSplineCurve PolesCount=4 KnotsCount=2 Degree=3 IsPeriodic=0
    g276: BSplineCurve PolesCount=4 KnotsCount=2 Degree=3 IsPeriodic=0
    g277: BSplineCurve PolesCount=4 KnotsCount=2 Degree=3 IsPeriodic=0
    g278: BSplineCurve PolesCount=4 KnotsCount=2 Degree=3 IsPeriodic=0
    g279: BSplineCurve PolesCount=4 KnotsCount=2 Degree=3 IsPeriodic=0
    g280: BSplineCurve PolesCount=4 KnotsCount=2 Degree=3 IsPeriodic=0
    g281: BSplineCurve PolesCount=4 KnotsCount=2 Degree=3 IsPeriodic=0
    g282: BSplineCurve PolesCount=4 KnotsCount=2 Degree=3 IsPeriodic=0
    g283: BSplineCurve PolesCount=4 KnotsCount=2 Degree=3 IsPeriodic=0
    g284: BSplineCurve PolesCount=4 KnotsCount=2 Degree=3 IsPeriodic=0
    g285: BSplineCurve PolesCount=2 KnotsCount=2 Degree=1 IsPeriodic=0
    g286: BSplineCurve PolesCount=4 KnotsCount=2 Degree=3 IsPeriodic=0
    g287: BSplineCurve PolesCount=4 KnotsCount=2 Degree=3 IsPeriodic=0
    g288: BSplineCurve PolesCount=4 KnotsCount=2 Degree=3 IsPeriodic=0
    g289: BSplineCurve PolesCount=4 KnotsCount=2 Degree=3 IsPeriodic=0
    g290: BSplineCurve PolesCount=2 KnotsCount=2 Degree=1 IsPeriodic=0
    g291: BSplineCurve PolesCount=2 KnotsCount=2 Degree=1 IsPeriodic=0
    g292: BSplineCurve PolesCount=2 KnotsCount=2 Degree=1 IsPeriodic=0
    g293: BSplineCurve PolesCount=4 KnotsCount=2 Degree=3 IsPeriodic=0
    g294: BSplineCurve PolesCount=4 KnotsCount=2 Degree=3 IsPeriodic=0
    g295: BSplineCurve PolesCount=4 KnotsCount=2 Degree=3 IsPeriodic=0
    g296: BSplineCurve PolesCount=4 KnotsCount=2 Degree=3 IsPeriodic=0
    g297: BSplineCurve PolesCount=4 KnotsCount=2 Degree=3 IsPeriodic=0
    g298: BSplineCurve PolesCount=4 KnotsCount=2 Degree=3 IsPeriodic=0
    g299: BSplineCurve PolesCount=4 KnotsCount=2 Degree=3 IsPeriodic=0
    g300: BSplineCurve PolesCount=4 KnotsCount=2 Degree=3 IsPeriodic=0
    g301: BSplineCurve PolesCount=4 KnotsCount=2 Degree=3 IsPeriodic=0
    g302: BSplineCurve PolesCount=4 KnotsCount=2 Degree=3 IsPeriodic=0
    g303: BSplineCurve PolesCount=4 KnotsCount=2 Degree=3 IsPeriodic=0
    g304: BSplineCurve PolesCount=4 KnotsCount=2 Degree=3 IsPeriodic=0
    g305: BSplineCurve PolesCount=4 KnotsCount=2 Degree=3 IsPeriodic=0
    g306: BSplineCurve PolesCount=4 KnotsCount=2 Degree=3 IsPeriodic=0
    g307: BSplineCurve PolesCount=4 KnotsCount=2 Degree=3 IsPeriodic=0
    g308: BSplineCurve PolesCount=4 KnotsCount=2 Degree=3 IsPeriodic=0
    g309: BSplineCurve PolesCount=4 KnotsCount=2 Degree=3 IsPeriodic=0
    g310: BSplineCurve PolesCount=4 KnotsCount=2 Degree=3 IsPeriodic=0
    g311: BSplineCurve PolesCount=4 KnotsCount=2 Degree=3 IsPeriodic=0
    g312: BSplineCurve PolesCount=4 KnotsCount=2 Degree=3 IsPeriodic=0
    g313: BSplineCurve PolesCount=4 KnotsCount=2 Degree=3 IsPeriodic=0
    g314: BSplineCurve PolesCount=4 KnotsCount=2 Degree=3 IsPeriodic=0
    g315: BSplineCurve PolesCount=4 KnotsCount=2 Degree=3 IsPeriodic=0
    g316: BSplineCurve PolesCount=4 KnotsCount=2 Degree=3 IsPeriodic=0
    g317: BSplineCurve PolesCount=4 KnotsCount=2 Degree=3 IsPeriodic=0
    g318: BSplineCurve PolesCount=4 KnotsCount=2 Degree=3 IsPeriodic=0
    g319: BSplineCurve PolesCount=4 KnotsCount=2 Degree=3 IsPeriodic=0
    g320: BSplineCurve PolesCount=2 KnotsCount=2 Degree=1 IsPeriodic=0
    g321: BSplineCurve PolesCount=2 KnotsCount=2 Degree=1 IsPeriodic=0
    g322: BSplineCurve PolesCount=4 KnotsCount=2 Degree=3 IsPeriodic=0
    g323: BSplineCurve PolesCount=4 KnotsCount=2 Degree=3 IsPeriodic=0
    g324: BSplineCurve PolesCount=4 KnotsCount=2 Degree=3 IsPeriodic=0
    g325: BSplineCurve PolesCount=4 KnotsCount=2 Degree=3 IsPeriodic=0
    g326: BSplineCurve PolesCount=4 KnotsCount=2 Degree=3 IsPeriodic=0
    g327: BSplineCurve PolesCount=4 KnotsCount=2 Degree=3 IsPeriodic=0
    g328: BSplineCurve PolesCount=4 KnotsCount=2 Degree=3 IsPeriodic=0
    g329: BSplineCurve PolesCount=4 KnotsCount=2 Degree=3 IsPeriodic=0
    g330: BSplineCurve PolesCount=4 KnotsCount=2 Degree=3 IsPeriodic=0
    g331: BSplineCurve PolesCount=2 KnotsCount=2 Degree=1 IsPeriodic=0
    g332: BSplineCurve PolesCount=2 KnotsCount=2 Degree=1 IsPeriodic=0
    g333: BSplineCurve PolesCount=2 KnotsCount=2 Degree=1 IsPeriodic=0
    g334: BSplineCurve PolesCount=2 KnotsCount=2 Degree=1 IsPeriodic=0
    g335: BSplineCurve PolesCount=4 KnotsCount=2 Degree=3 IsPeriodic=0
    g336: BSplineCurve PolesCount=4 KnotsCount=2 Degree=3 IsPeriodic=0
    g337: BSplineCurve PolesCount=4 KnotsCount=2 Degree=3 IsPeriodic=0
    g338: BSplineCurve PolesCount=4 KnotsCount=2 Degree=3 IsPeriodic=0
    g339: BSplineCurve PolesCount=4 KnotsCount=2 Degree=3 IsPeriodic=0
    g340: BSplineCurve PolesCount=4 KnotsCount=2 Degree=3 IsPeriodic=0
    g341: BSplineCurve PolesCount=4 KnotsCount=2 Degree=3 IsPeriodic=0
    g342: BSplineCurve PolesCount=4 KnotsCount=2 Degree=3 IsPeriodic=0
    g343: BSplineCurve PolesCount=2 KnotsCount=2 Degree=1 IsPeriodic=0
    g344: BSplineCurve PolesCount=2 KnotsCount=2 Degree=1 IsPeriodic=0
    g345: BSplineCurve PolesCount=4 KnotsCount=2 Degree=3 IsPeriodic=0
    g346: BSplineCurve PolesCount=4 KnotsCount=2 Degree=3 IsPeriodic=0
    g347: BSplineCurve PolesCount=4 KnotsCount=2 Degree=3 IsPeriodic=0
    g348: BSplineCurve PolesCount=4 KnotsCount=2 Degree=3 IsPeriodic=0
    g349: BSplineCurve PolesCount=4 KnotsCount=2 Degree=3 IsPeriodic=0
    g350: BSplineCurve PolesCount=4 KnotsCount=2 Degree=3 IsPeriodic=0
    g351: BSplineCurve PolesCount=4 KnotsCount=2 Degree=3 IsPeriodic=0
    g352: BSplineCurve PolesCount=4 KnotsCount=2 Degree=3 IsPeriodic=0
    g353: BSplineCurve PolesCount=4 KnotsCount=2 Degree=3 IsPeriodic=0
    g354: BSplineCurve PolesCount=2 KnotsCount=2 Degree=1 IsPeriodic=0
    g355: BSplineCurve PolesCount=2 KnotsCount=2 Degree=1 IsPeriodic=0
    g356: BSplineCurve PolesCount=4 KnotsCount=2 Degree=3 IsPeriodic=0
    g357: BSplineCurve PolesCount=4 KnotsCount=2 Degree=3 IsPeriodic=0
    g358: BSplineCurve PolesCount=4 KnotsCount=2 Degree=3 IsPeriodic=0
    g359: BSplineCurve PolesCount=4 KnotsCount=2 Degree=3 IsPeriodic=0
    g360: BSplineCurve PolesCount=4 KnotsCount=2 Degree=3 IsPeriodic=0
    g361: BSplineCurve PolesCount=4 KnotsCount=2 Degree=3 IsPeriodic=0
    g362: BSplineCurve PolesCount=4 KnotsCount=2 Degree=3 IsPeriodic=0
    g363: BSplineCurve PolesCount=4 KnotsCount=2 Degree=3 IsPeriodic=0
    g364: BSplineCurve PolesCount=4 KnotsCount=2 Degree=3 IsPeriodic=0
    g365: BSplineCurve PolesCount=4 KnotsCount=2 Degree=3 IsPeriodic=0
    g366: BSplineCurve PolesCount=4 KnotsCount=2 Degree=3 IsPeriodic=0
    g367: BSplineCurve PolesCount=4 KnotsCount=2 Degree=3 IsPeriodic=0
    g368: BSplineCurve PolesCount=2 KnotsCount=2 Degree=1 IsPeriodic=0
    g369: BSplineCurve PolesCount=2 KnotsCount=2 Degree=1 IsPeriodic=0
    g370: BSplineCurve PolesCount=4 KnotsCount=2 Degree=3 IsPeriodic=0
    g371: BSplineCurve PolesCount=4 KnotsCount=2 Degree=3 IsPeriodic=0
    g372: BSplineCurve PolesCount=4 KnotsCount=2 Degree=3 IsPeriodic=0
    g373: BSplineCurve PolesCount=4 KnotsCount=2 Degree=3 IsPeriodic=0
    g374: BSplineCurve PolesCount=4 KnotsCount=2 Degree=3 IsPeriodic=0
    g375: BSplineCurve PolesCount=4 KnotsCount=2 Degree=3 IsPeriodic=0
    g376: BSplineCurve PolesCount=4 KnotsCount=2 Degree=3 IsPeriodic=0
    g377: BSplineCurve PolesCount=4 KnotsCount=2 Degree=3 IsPeriodic=0
    g378: BSplineCurve PolesCount=4 KnotsCount=2 Degree=3 IsPeriodic=0
    g379: BSplineCurve PolesCount=4 KnotsCount=2 Degree=3 IsPeriodic=0
    g380: BSplineCurve PolesCount=2 KnotsCount=2 Degree=1 IsPeriodic=0
    g381: BSplineCurve PolesCount=2 KnotsCount=2 Degree=1 IsPeriodic=0
    g382: BSplineCurve PolesCount=4 KnotsCount=2 Degree=3 IsPeriodic=0
    g383: BSplineCurve PolesCount=4 KnotsCount=2 Degree=3 IsPeriodic=0
    g384: BSplineCurve PolesCount=4 KnotsCount=2 Degree=3 IsPeriodic=0
    g385: BSplineCurve PolesCount=4 KnotsCount=2 Degree=3 IsPeriodic=0
    g386: BSplineCurve PolesCount=4 KnotsCount=2 Degree=3 IsPeriodic=0
    g387: BSplineCurve PolesCount=4 KnotsCount=2 Degree=3 IsPeriodic=0
    g388: BSplineCurve PolesCount=4 KnotsCount=2 Degree=3 IsPeriodic=0
    g389: BSplineCurve PolesCount=4 KnotsCount=2 Degree=3 IsPeriodic=0
    g390: BSplineCurve PolesCount=2 KnotsCount=2 Degree=1 IsPeriodic=0
    g391: BSplineCurve PolesCount=2 KnotsCount=2 Degree=1 IsPeriodic=0
    g392: BSplineCurve PolesCount=4 KnotsCount=2 Degree=3 IsPeriodic=0
    g393: BSplineCurve PolesCount=4 KnotsCount=2 Degree=3 IsPeriodic=0
    g394: BSplineCurve PolesCount=4 KnotsCount=2 Degree=3 IsPeriodic=0
    g395: BSplineCurve PolesCount=4 KnotsCount=2 Degree=3 IsPeriodic=0
    g396: BSplineCurve PolesCount=4 KnotsCount=2 Degree=3 IsPeriodic=0
    g397: BSplineCurve PolesCount=4 KnotsCount=2 Degree=3 IsPeriodic=0
    g398: BSplineCurve PolesCount=4 KnotsCount=2 Degree=3 IsPeriodic=0
    g399: BSplineCurve PolesCount=4 KnotsCount=2 Degree=3 IsPeriodic=0
    ... +22 more geometry lines
  constraints (438):
    c: Coincident(g0,g1)
    c: Coincident(g1,g2)
    c: Coincident(g2,g3)
    c: Coincident(g3,g4)
    c: Coincident(g4,g5)
    c: Coincident(g5,g6)
    c: Coincident(g6,g7)
    c: Coincident(g7,g8)
    c: Coincident(g8,g9)
    c: Coincident(g9,g10)
    c: Coincident(g10,g11)
    c: Coincident(g11,g12)
    c: Coincident(g12,g13)
    c: Coincident(g13,g14)
    c: Coincident(g14,g15)
    c: Coincident(g15,g16)
    c: Coincident(g16,g17)
    c: Coincident(g17,g18)
    c: Coincident(g18,g19)
    c: Coincident(g19,g20)
    c: Coincident(g20,g21)
    c: Coincident(g21,g22)
    c: Coincident(g22,g23)
    c: Coincident(g23,g24)
    c: Coincident(g24,g25)
    c: Coincident(g25,g26)
    c: Coincident(g26,g27)
    c: Coincident(g27,g28)
    c: Coincident(g28,g29)
    c: Coincident(g29,g30)
    c: Coincident(g30,g31)
    c: Coincident(g31,g32)
    c: Coincident(g32,g33)
    c: Coincident(g33,g34)
    c: Coincident(g34,g35)
    c: Coincident(g35,g36)
    c: Coincident(g36,g37)
    c: Coincident(g37,g38)
    c: Coincident(g38,g39)
    c: Coincident(g39,g40)
    c: Coincident(g40,g41)
    c: Coincident(g41,g42)
    c: Coincident(g42,g43)
    c: Coincident(g43,g44)
    c: Coincident(g44,g45)
    c: Coincident(g45,g46)
    c: Coincident(g46,g47)
    c: Coincident(g47,g48)
    c: Coincident(g48,g49)
    c: Coincident(g49,g50)
    c: Coincident(g50,g51)
    c: Coincident(g51,g52)
    c: Coincident(g52,g53)
    c: Coincident(g53,g54)
    c: Coincident(g54,g55)
    c: Coincident(g56,g57)
    c: Coincident(g57,g58)
    c: Coincident(g58,g59)
    c: Coincident(g59,g56)
    c: Coincident(g60,g61)
    c: Coincident(g61,g62)
    c: Coincident(g62,g63)
    c: Coincident(g63,g64)
    c: Coincident(g64,g65)
    c: Coincident(g65,g66)
    c: Coincident(g66,g67)
    c: Coincident(g67,g68)
    c: Coincident(g68,g69)
    c: Coincident(g69,g70)
    c: Coincident(g70,g71)
    c: Coincident(g71,g72)
    c: Coincident(g72,g73)
    c: Coincident(g73,g74)
    c: Coincident(g74,g75)
    c: Coincident(g75,g60)
    c: Coincident(g76,g77)
    c: Coincident(g77,g78)
    c: Coincident(g78,g79)
    c: Coincident(g79,g80)
    c: Coincident(g80,g81)
    c: Coincident(g81,g82)
    c: Coincident(g82,g83)
    c: Coincident(g83,g84)
    c: Coincident(g84,g85)
    c: Coincident(g85,g86)
    c: Coincident(g86,g87)
    c: Coincident(g87,g88)
    c: Coincident(g88,g89)
    c: Coincident(g89,g90)
    c: Coincident(g90,g91)
    c: Coincident(g91,g92)
    c: Coincident(g92,g93)
    c: Coincident(g93,g94)
    c: Coincident(g94,g95)
    c: Coincident(g95,g76)
    c: Coincident(g96,g97)
    c: Coincident(g97,g98)
    c: Coincident(g98,g99)
    c: Coincident(g99,g100)
    c: Coincident(g100,g101)
    c: Coincident(g101,g102)
    c: Coincident(g102,g103)
    c: Coincident(g103,g104)
    c: Coincident(g104,g105)
    c: Coincident(g105,g106)
    c: Coincident(g106,g107)
    c: Coincident(g107,g96)
    c: Coincident(g108,g109)
    c: Coincident(g109,g110)
    c: Coincident(g110,g111)
    c: Coincident(g111,g108)
    c: Coincident(g112,g113)
    c: Coincident(g113,g114)
    c: Coincident(g114,g115)
    c: Coincident(g115,g112)
    c: Coincident(g116,g117)
    c: Coincident(g117,g118)
    c: Coincident(g118,g119)
    c: Coincident(g119,g120)
    c: Coincident(g120,g121)
    c: Coincident(g121,g122)
    c: Coincident(g122,g123)
    c: Coincident(g123,g116)
    c: Coincident(g124,g125)
    c: Coincident(g125,g126)
    c: Coincident(g126,g127)
    c: Coincident(g127,g128)
    c: Coincident(g128,g129)
    c: Coincident(g129,g124)
    c: Coincident(g130,g131)
    c: Coincident(g131,g132)
    c: Coincident(g132,g133)
    c: Coincident(g133,g134)
    c: Coincident(g134,g135)
    c: Coincident(g136,g137)
    c: Coincident(g137,g138)
    c: Coincident(g138,g139)
    c: Coincident(g139,g140)
    c: Coincident(g140,g136)
    c: Coincident(g141,g142)
    c: Coincident(g142,g143)
    c: Coincident(g143,g144)
    c: Coincident(g144,g145)
    c: Coincident(g145,g146)
    c: Coincident(g146,g147)
    c: Coincident(g147,g148)
    c: Coincident(g148,g149)
    c: Coincident(g149,g150)
    c: Coincident(g150,g151)
    c: Coincident(g151,g152)
    c: Coincident(g152,g153)
    c: Coincident(g153,g154)
    c: Coincident(g154,g155)
    c: Coincident(g155,g141)
    c: Coincident(g156,g157)
    c: Coincident(g157,g158)
    c: Coincident(g158,g156)
    c: Coincident(g159,g160)
    c: Coincident(g160,g161)
    c: Coincident(g161,g159)
    c: Coincident(g162,g163)
    c: Coincident(g163,g164)
    c: Coincident(g164,g165)
    c: Coincident(g165,g166)
    c: Coincident(g166,g167)
    c: Coincident(g167,g168)
    c: Coincident(g168,g169)
    c: Coincident(g169,g170)
    c: Coincident(g170,g162)
    c: Coincident(g171,g172)
    c: Coincident(g172,g173)
    c: Coincident(g173,g171)
    c: Coincident(g174,g175)
    c: Coincident(g175,g176)
    c: Coincident(g176,g177)
    c: Coincident(g177,g178)
    c: Coincident(g178,g179)
    c: Coincident(g179,g180)
    c: Coincident(g180,g181)
    c: Coincident(g181,g182)
    c: Coincident(g182,g183)
    c: Coincident(g183,g184)
    c: Coincident(g184,g185)
    c: Coincident(g185,g186)
    c: Coincident(g186,g187)
    c: Coincident(g187,g188)
    c: Coincident(g188,g174)
    c: Coincident(g189,g190)
    c: Coincident(g190,g191)
    c: Coincident(g191,g192)
    c: Coincident(g192,g193)
    c: Coincident(g193,g194)
    c: Coincident(g194,g195)
    c: Coincident(g195,g196)
    c: Coincident(g196,g197)
    c: Coincident(g197,g198)
    c: Coincident(g198,g199)
    c: Coincident(g199,g200)
    c: Coincident(g200,g201)
    c: Coincident(g201,g189)
    c: Coincident(g202,g203)
    c: Coincident(g203,g204)
    c: Coincident(g204,g202)
    c: Coincident(g206,g207)
    c: Coincident(g207,g208)
    c: Coincident(g208,g209)
    c: Coincident(g209,g210)
    c: Coincident(g210,g211)
    c: Coincident(g211,g212)
    c: Coincident(g212,g213)
    c: Coincident(g213,g205)
    c: Coincident(g214,g215)
    c: Coincident(g215,g216)
    c: Coincident(g216,g217)
    c: Coincident(g218,g219)
    c: Coincident(g219,g220)
    c: Coincident(g220,g218)
    c: Coincident(g221,g222)
    c: Coincident(g222,g223)
    c: Coincident(g223,g221)
    c: Coincident(g224,g225)
    c: Coincident(g225,g226)
    c: Coincident(g226,g224)
    c: Coincident(g227,g228)
    c: Coincident(g228,g229)
    c: Coincident(g229,g227)
    c: Coincident(g230,g231)
    c: Coincident(g231,g232)
    c: Coincident(g232,g233)
    c: Coincident(g233,g230)
    c: Coincident(g234,g235)
    c: Coincident(g235,g236)
    c: Coincident(g236,g237)
    c: Coincident(g237,g234)
    c: Coincident(g238,g239)
    c: Coincident(g239,g240)
    c: Coincident(g240,g241)
    c: Coincident(g241,g242)
    c: Coincident(g242,g243)
    c: Coincident(g243,g244)
    c: Coincident(g244,g238)
    c: Coincident(g245,g246)
    c: Coincident(g246,g247)
    c: Coincident(g247,g248)
    c: Coincident(g248,g245)
    c: Coincident(g249,g250)
    c: Coincident(g250,g251)
    c: Coincident(g252,g253)
    c: Coincident(g253,g254)
    c: Coincident(g254,g255)
    c: Coincident(g255,g252)
    c: Coincident(g256,g257)
    c: Coincident(g257,g258)
    c: Coincident(g258,g259)
    c: Coincident(g259,g256)
    c: Coincident(g260,g261)
    c: Coincident(g261,g262)
    c: Coincident(g262,g263)
    c: Coincident(g263,g264)
    c: Coincident(g264,g265)
    c: Coincident(g265,g266)
    c: Coincident(g266,g267)
    c: Coincident(g267,g260)
    c: Coincident(g268,g269)
    c: Coincident(g269,g270)
    c: Coincident(g271,g272)
    c: Coincident(g272,g273)
    c: Coincident(g273,g274)
    c: Coincident(g274,g271)
    c: Coincident(g275,g276)
    c: Coincident(g276,g277)
    c: Coincident(g277,g278)
    c: Coincident(g278,g279)
    c: Coincident(g279,g280)
    c: Coincident(g280,g281)
    c: Coincident(g281,g275)
    c: Coincident(g282,g283)
    c: Coincident(g283,g284)
    c: Coincident(g285,g286)
    c: Coincident(g286,g287)
    c: Coincident(g287,g288)
    c: Coincident(g288,g289)
    c: Coincident(g289,g290)
    c: Coincident(g290,g291)
    c: Coincident(g291,g292)
    c: Coincident(g292,g285)
    c: Coincident(g293,g294)
    c: Coincident(g294,g295)
    c: Coincident(g295,g296)
    c: Coincident(g296,g297)
    c: Coincident(g297,g293)
    c: Coincident(g298,g299)
    c: Coincident(g299,g300)
    c: Coincident(g300,g301)
    c: Coincident(g301,g302)
    c: Coincident(g302,g303)
    c: Coincident(g303,g298)
    c: Coincident(g304,g305)
    c: Coincident(g305,g306)
    c: Coincident(g306,g307)
    c: Coincident(g307,g308)
    c: Coincident(g308,g309)
    c: Coincident(g309,g304)
    c: Coincident(g310,g311)
    c: Coincident(g311,g312)
    c: Coincident(g312,g313)
    c: Coincident(g314,g315)
    c: Coincident(g315,g316)
    c: Coincident(g317,g318)
    c: Coincident(g318,g319)
    c: Coincident(g319,g320)
    c: Coincident(g320,g321)
    c: Coincident(g321,g317)
    c: Coincident(g322,g323)
    c: Coincident(g323,g324)
    c: Coincident(g324,g325)
    c: Coincident(g325,g322)
    c: Coincident(g326,g327)
    c: Coincident(g327,g328)
    c: Coincident(g328,g326)
    c: Coincident(g329,g330)
    c: Coincident(g330,g331)
    c: Coincident(g331,g332)
    c: Coincident(g332,g333)
    c: Coincident(g333,g334)
    c: Coincident(g334,g335)
    c: Coincident(g335,g329)
    c: Coincident(g336,g337)
    c: Coincident(g337,g338)
    c: Coincident(g338,g339)
    c: Coincident(g339,g336)
    c: Coincident(g340,g341)
    c: Coincident(g341,g342)
    c: Coincident(g342,g343)
    c: Coincident(g343,g344)
    c: Coincident(g344,g340)
    c: Coincident(g345,g346)
    c: Coincident(g346,g347)
    c: Coincident(g347,g348)
    c: Coincident(g348,g349)
    c: Coincident(g349,g350)
    c: Coincident(g350,g351)
    c: Coincident(g351,g352)
    c: Coincident(g352,g345)
    c: Coincident(g353,g354)
    c: Coincident(g354,g355)
    c: Coincident(g355,g356)
    c: Coincident(g356,g357)
    c: Coincident(g357,g358)
    c: Coincident(g358,g359)
    c: Coincident(g359,g353)
    c: Coincident(g360,g361)
    c: Coincident(g361,g362)
    c: Coincident(g362,g363)
    c: Coincident(g363,g364)
    c: Coincident(g364,g360)
    c: Coincident(g365,g366)
    c: Coincident(g366,g367)
    c: Coincident(g367,g368)
    c: Coincident(g368,g369)
    c: Coincident(g369,g370)
    c: Coincident(g370,g371)
    c: Coincident(g371,g372)
    c: Coincident(g372,g373)
    c: Coincident(g373,g374)
    c: Coincident(g374,g375)
    c: Coincident(g375,g376)
    c: Coincident(g376,g377)
    c: Coincident(g378,g379)
    c: Coincident(g379,g380)
    c: Coincident(g380,g381)
    c: Coincident(g381,g382)
    c: Coincident(g420,g384)
    c: Coincident(g384,g385)
    c: Coincident(g385,g386)
    c: Coincident(g386,g387)
    c: Coincident(g387,g388)
    c: Coincident(g388,g389)
    c: Coincident(g389,g390)
    c: Coincident(g390,g391)
    c: Coincident(g391,g383)
    c: Coincident(g392,g393)
    c: Coincident(g393,g394)
    c: Coincident(g394,g395)
    c: Coincident(g395,g392)
    c: Coincident(g396,g397)
    c: Coincident(g397,g398)
    c: Coincident(g398,g399)
    c: Coincident(g399,g396)
    c: Coincident(g400,g401)
    c: Coincident(g401,g402)
    c: Coincident(g402,g403)
    c: Coincident(g403,g400)
    c: Coincident(g404,g405)
    c: Coincident(g405,g406)
    c: Coincident(g406,g407)
    c: Coincident(g407,g404)
    c: Coincident(g55,g0)
    c: Coincident(g214,g217)
    c: Coincident(g365,g377)
    c: Coincident(g378,g382)
    c: Coincident(g268,g270)
    c: Coincident(g314,g316)
    c: Coincident(g310,g313)
    c: Coincident(g249,g251)
    c: Coincident(g282,g284)
    c: Coincident(g130,g135)
    c: Weight(g409) = 1
    c: Equal(g409,g410)
    c: InternalAlignment(g409,g411)
    c: InternalAlignment(g410,g411)
    c: InternalAlignment(g412,g411)
    c: InternalAlignment(g413,g411)
    c: Coincident(g409,g206)
    c: Weight(g414) = 1
    c: Equal(g414,g415)
    c: InternalAlignment(g414,g416)
    c: InternalAlignment(g415,g416)
    c: InternalAlignment(g417,g416)
    c: InternalAlignment(g418,g416)
    c: Coincident(g414,g411)
    c: Coincident(g415,g205)
    c: InternalAlignment(g419,g411)
    c: Equal(g419,g409)
    c: InternalAlignment(g421,g420)
    c: Weight(g421) = 1
    c: InternalAlignment(g422,g420)
    c: Equal(g422,g421)
    c: InternalAlignment(g423,g420)
    c: Equal(g423,g421)
    c: InternalAlignment(g424,g420)
    c: Equal(g424,g421)
    c: InternalAlignment(g425,g420)
    c: Equal(g425,g421)
    c: InternalAlignment(g426,g420)
    c: Equal(g426,g421)
    c: InternalAlignment(g427,g420)
    c: Equal(g427,g421)
FEATURE [Sketcher::SketchObject] Sketch039  label="No_Dashii-Sketch"
  ArcFitTolerance = 1e-06
  FullyConstrained = false
  MakeInternals = false
  Placement = pos=(-15.1967,13.0933,0) rot=(0,0,1;0rad)
  expr: .Placement.Base.x = -(.Shape.BoundBox.XLength / 2)
  expr: .Placement.Base.y = .Shape.BoundBox.YLength / 2
  sketch-geometry (213):
    g0: BSplineCurve PolesCount=4 KnotsCount=2 Degree=3 IsPeriodic=0
    g1: BSplineCurve PolesCount=4 KnotsCount=2 Degree=3 IsPeriodic=0
    g2: BSplineCurve PolesCount=4 KnotsCount=2 Degree=3 IsPeriodic=0
    g3: BSplineCurve PolesCount=4 KnotsCount=2 Degree=3 IsPeriodic=0
    g4: BSplineCurve PolesCount=4 KnotsCount=2 Degree=3 IsPeriodic=0
    g5: BSplineCurve PolesCount=4 KnotsCount=2 Degree=3 IsPeriodic=0
    g6: BSplineCurve PolesCount=4 KnotsCount=2 Degree=3 IsPeriodic=0
    g7: BSplineCurve PolesCount=4 KnotsCount=2 Degree=3 IsPeriodic=0
    g8: BSplineCurve PolesCount=2 KnotsCount=2 Degree=1 IsPeriodic=0
    g9: BSplineCurve PolesCount=2 KnotsCount=2 Degree=1 IsPeriodic=0
    g10: BSplineCurve PolesCount=4 KnotsCount=2 Degree=3 IsPeriodic=0
    g11: BSplineCurve PolesCount=4 KnotsCount=2 Degree=3 IsPeriodic=0
    g12: BSplineCurve PolesCount=4 KnotsCount=2 Degree=3 IsPeriodic=0
    g13: BSplineCurve PolesCount=4 KnotsCount=2 Degree=3 IsPeriodic=0
    g14: BSplineCurve PolesCount=2 KnotsCount=2 Degree=1 IsPeriodic=0
    g15: BSplineCurve PolesCount=2 KnotsCount=2 Degree=1 IsPeriodic=0
    g16: BSplineCurve PolesCount=4 KnotsCount=2 Degree=3 IsPeriodic=0
    g17: BSplineCurve PolesCount=4 KnotsCount=2 Degree=3 IsPeriodic=0
    g18: BSplineCurve PolesCount=4 KnotsCount=2 Degree=3 IsPeriodic=0
    g19: BSplineCurve PolesCount=2 KnotsCount=2 Degree=1 IsPeriodic=0
    g20: BSplineCurve PolesCount=4 KnotsCount=2 Degree=3 IsPeriodic=0
    g21: BSplineCurve PolesCount=4 KnotsCount=2 Degree=3 IsPeriodic=0
    g22: BSplineCurve PolesCount=4 KnotsCount=2 Degree=3 IsPeriodic=0
    g23: BSplineCurve PolesCount=4 KnotsCount=2 Degree=3 IsPeriodic=0
    g24: BSplineCurve PolesCount=4 KnotsCount=2 Degree=3 IsPeriodic=0
    g25: BSplineCurve PolesCount=2 KnotsCount=2 Degree=1 IsPeriodic=0
    g26: BSplineCurve PolesCount=2 KnotsCount=2 Degree=1 IsPeriodic=0
    g27: BSplineCurve PolesCount=4 KnotsCount=2 Degree=3 IsPeriodic=0
    g28: BSplineCurve PolesCount=4 KnotsCount=2 Degree=3 IsPeriodic=0
    g29: BSplineCurve PolesCount=4 KnotsCount=2 Degree=3 IsPeriodic=0
    g30: BSplineCurve PolesCount=4 KnotsCount=2 Degree=3 IsPeriodic=0
    g31: BSplineCurve PolesCount=4 KnotsCount=2 Degree=3 IsPeriodic=0
    g32: BSplineCurve PolesCount=4 KnotsCount=2 Degree=3 IsPeriodic=0
    g33: BSplineCurve PolesCount=4 KnotsCount=2 Degree=3 IsPeriodic=0
    g34: BSplineCurve PolesCount=4 KnotsCount=2 Degree=3 IsPeriodic=0
    g35: BSplineCurve PolesCount=4 KnotsCount=2 Degree=3 IsPeriodic=0
    g36: BSplineCurve PolesCount=2 KnotsCount=2 Degree=1 IsPeriodic=0
    g37: BSplineCurve PolesCount=2 KnotsCount=2 Degree=1 IsPeriodic=0
    g38: BSplineCurve PolesCount=4 KnotsCount=2 Degree=3 IsPeriodic=0
    g39: BSplineCurve PolesCount=4 KnotsCount=2 Degree=3 IsPeriodic=0
    g40: BSplineCurve PolesCount=4 KnotsCount=2 Degree=3 IsPeriodic=0
    g41: BSplineCurve PolesCount=4 KnotsCount=2 Degree=3 IsPeriodic=0
    g42: BSplineCurve PolesCount=4 KnotsCount=2 Degree=3 IsPeriodic=0
    g43: BSplineCurve PolesCount=4 KnotsCount=2 Degree=3 IsPeriodic=0
    g44: BSplineCurve PolesCount=4 KnotsCount=2 Degree=3 IsPeriodic=0
    g45: BSplineCurve PolesCount=4 KnotsCount=2 Degree=3 IsPeriodic=0
    g46: BSplineCurve PolesCount=4 KnotsCount=2 Degree=3 IsPeriodic=0
    g47: BSplineCurve PolesCount=2 KnotsCount=2 Degree=1 IsPeriodic=0
    g48: BSplineCurve PolesCount=2 KnotsCount=2 Degree=1 IsPeriodic=0
    g49: BSplineCurve PolesCount=4 KnotsCount=2 Degree=3 IsPeriodic=0
    g50: BSplineCurve PolesCount=4 KnotsCount=2 Degree=3 IsPeriodic=0
    g51: BSplineCurve PolesCount=4 KnotsCount=2 Degree=3 IsPeriodic=0
    g52: BSplineCurve PolesCount=4 KnotsCount=2 Degree=3 IsPeriodic=0
    g53: BSplineCurve PolesCount=4 KnotsCount=2 Degree=3 IsPeriodic=0
    g54: BSplineCurve PolesCount=4 KnotsCount=2 Degree=3 IsPeriodic=0
    g55: BSplineCurve PolesCount=4 KnotsCount=2 Degree=3 IsPeriodic=0
    g56: BSplineCurve PolesCount=4 KnotsCount=2 Degree=3 IsPeriodic=0
    g57: BSplineCurve PolesCount=4 KnotsCount=2 Degree=3 IsPeriodic=0
    g58: BSplineCurve PolesCount=4 KnotsCount=2 Degree=3 IsPeriodic=0
    g59: BSplineCurve PolesCount=4 KnotsCount=2 Degree=3 IsPeriodic=0
    g60: BSplineCurve PolesCount=4 KnotsCount=2 Degree=3 IsPeriodic=0
    g61: BSplineCurve PolesCount=4 KnotsCount=2 Degree=3 IsPeriodic=0
    g62: BSplineCurve PolesCount=4 KnotsCount=2 Degree=3 IsPeriodic=0
    g63: BSplineCurve PolesCount=4 KnotsCount=2 Degree=3 IsPeriodic=0
    g64: BSplineCurve PolesCount=4 KnotsCount=2 Degree=3 IsPeriodic=0
    g65: BSplineCurve PolesCount=4 KnotsCount=2 Degree=3 IsPeriodic=0
    g66: BSplineCurve PolesCount=4 KnotsCount=2 Degree=3 IsPeriodic=0
    g67: BSplineCurve PolesCount=4 KnotsCount=2 Degree=3 IsPeriodic=0
    g68: BSplineCurve PolesCount=4 KnotsCount=2 Degree=3 IsPeriodic=0
    g69: BSplineCurve PolesCount=4 KnotsCount=2 Degree=3 IsPeriodic=0
    g70: BSplineCurve PolesCount=4 KnotsCount=2 Degree=3 IsPeriodic=0
    g71: BSplineCurve PolesCount=2 KnotsCount=2 Degree=1 IsPeriodic=0
    g72: BSplineCurve PolesCount=2 KnotsCount=2 Degree=1 IsPeriodic=0
    g73: BSplineCurve PolesCount=4 KnotsCount=2 Degree=3 IsPeriodic=0
    g74: BSplineCurve PolesCount=7 KnotsCount=2 Degree=6 IsPeriodic=0
    g75: BSplineCurve PolesCount=4 KnotsCount=2 Degree=3 IsPeriodic=0
    g76: BSplineCurve PolesCount=2 KnotsCount=2 Degree=1 IsPeriodic=0
    g77: BSplineCurve PolesCount=2 KnotsCount=2 Degree=1 IsPeriodic=0
    g78: BSplineCurve PolesCount=4 KnotsCount=2 Degree=3 IsPeriodic=0
    g79: BSplineCurve PolesCount=2 KnotsCount=2 Degree=1 IsPeriodic=0
    g80: BSplineCurve PolesCount=2 KnotsCount=2 Degree=1 IsPeriodic=0
    g81: BSplineCurve PolesCount=4 KnotsCount=2 Degree=3 IsPeriodic=0
    g82: BSplineCurve PolesCount=4 KnotsCount=2 Degree=3 IsPeriodic=0
    g83: BSplineCurve PolesCount=11 KnotsCount=2 Degree=10 IsPeriodic=0
    g84: BSplineCurve PolesCount=4 KnotsCount=2 Degree=3 IsPeriodic=0
    g85: BSplineCurve PolesCount=4 KnotsCount=2 Degree=3 IsPeriodic=0
    g86: BSplineCurve PolesCount=4 KnotsCount=2 Degree=3 IsPeriodic=0
    g87: BSplineCurve PolesCount=4 KnotsCount=2 Degree=3 IsPeriodic=0
    g88: BSplineCurve PolesCount=4 KnotsCount=2 Degree=3 IsPeriodic=0
    g89: BSplineCurve PolesCount=4 KnotsCount=2 Degree=3 IsPeriodic=0
    g90: BSplineCurve PolesCount=6 KnotsCount=2 Degree=5 IsPeriodic=0
    g91: BSplineCurve PolesCount=4 KnotsCount=2 Degree=3 IsPeriodic=0
    g92: BSplineCurve PolesCount=4 KnotsCount=2 Degree=3 IsPeriodic=0
    g93: BSplineCurve PolesCount=4 KnotsCount=2 Degree=3 IsPeriodic=0
    g94: BSplineCurve PolesCount=4 KnotsCount=2 Degree=3 IsPeriodic=0
    g95: BSplineCurve PolesCount=4 KnotsCount=2 Degree=3 IsPeriodic=0
    g96: BSplineCurve PolesCount=2 KnotsCount=2 Degree=1 IsPeriodic=0
    g97: BSplineCurve PolesCount=2 KnotsCount=2 Degree=1 IsPeriodic=0
    g98: BSplineCurve PolesCount=4 KnotsCount=2 Degree=3 IsPeriodic=0
    g99: BSplineCurve PolesCount=4 KnotsCount=2 Degree=3 IsPeriodic=0
    g100: BSplineCurve PolesCount=4 KnotsCount=2 Degree=3 IsPeriodic=0
    g101: BSplineCurve PolesCount=4 KnotsCount=2 Degree=3 IsPeriodic=0
    g102: BSplineCurve PolesCount=4 KnotsCount=2 Degree=3 IsPeriodic=0
    g103: BSplineCurve PolesCount=4 KnotsCount=2 Degree=3 IsPeriodic=0
    g104: BSplineCurve PolesCount=4 KnotsCount=2 Degree=3 IsPeriodic=0
    g105: BSplineCurve PolesCount=4 KnotsCount=2 Degree=3 IsPeriodic=0
    g106: BSplineCurve PolesCount=4 KnotsCount=2 Degree=3 IsPeriodic=0
    g107: BSplineCurve PolesCount=4 KnotsCount=2 Degree=3 IsPeriodic=0
    g108: BSplineCurve PolesCount=4 KnotsCount=2 Degree=3 IsPeriodic=0
    g109: BSplineCurve PolesCount=4 KnotsCount=2 Degree=3 IsPeriodic=0
    g110: BSplineCurve PolesCount=4 KnotsCount=2 Degree=3 IsPeriodic=0
    g111: BSplineCurve PolesCount=4 KnotsCount=2 Degree=3 IsPeriodic=0
    g112: BSplineCurve PolesCount=4 KnotsCount=2 Degree=3 IsPeriodic=0
    g113: BSplineCurve PolesCount=4 KnotsCount=2 Degree=3 IsPeriodic=0
    g114: BSplineCurve PolesCount=4 KnotsCount=2 Degree=3 IsPeriodic=0
    g115: BSplineCurve PolesCount=4 KnotsCount=2 Degree=3 IsPeriodic=0
    g116: BSplineCurve PolesCount=4 KnotsCount=2 Degree=3 IsPeriodic=0
    g117: BSplineCurve PolesCount=4 KnotsCount=2 Degree=3 IsPeriodic=0
    g118: BSplineCurve PolesCount=4 KnotsCount=2 Degree=3 IsPeriodic=0
    g119: BSplineCurve PolesCount=4 KnotsCount=2 Degree=3 IsPeriodic=0
    g120: BSplineCurve PolesCount=4 KnotsCount=2 Degree=3 IsPeriodic=0
    g121: BSplineCurve PolesCount=4 KnotsCount=2 Degree=3 IsPeriodic=0
    g122: BSplineCurve PolesCount=6 KnotsCount=2 Degree=5 IsPeriodic=0
    g123: BSplineCurve PolesCount=2 KnotsCount=2 Degree=1 IsPeriodic=0
    g124: BSplineCurve PolesCount=4 KnotsCount=2 Degree=3 IsPeriodic=0
    g125: BSplineCurve PolesCount=2 KnotsCount=2 Degree=1 IsPeriodic=0
    g126: BSplineCurve PolesCount=2 KnotsCount=2 Degree=1 IsPeriodic=0
    g127: BSplineCurve PolesCount=4 KnotsCount=2 Degree=3 IsPeriodic=0
    g128: BSplineCurve PolesCount=4 KnotsCount=2 Degree=3 IsPeriodic=0
    g129: BSplineCurve PolesCount=4 KnotsCount=2 Degree=3 IsPeriodic=0
    g130: BSplineCurve PolesCount=2 KnotsCount=2 Degree=1 IsPeriodic=0
    g131: BSplineCurve PolesCount=2 KnotsCount=2 Degree=1 IsPeriodic=0
    g132: BSplineCurve PolesCount=4 KnotsCount=2 Degree=3 IsPeriodic=0
    g133: BSplineCurve PolesCount=4 KnotsCount=2 Degree=3 IsPeriodic=0
    g134: BSplineCurve PolesCount=4 KnotsCount=2 Degree=3 IsPeriodic=0
    g135: BSplineCurve PolesCount=4 KnotsCount=2 Degree=3 IsPeriodic=0
    g136: BSplineCurve PolesCount=4 KnotsCount=2 Degree=3 IsPeriodic=0
    g137: BSplineCurve PolesCount=4 KnotsCount=2 Degree=3 IsPeriodic=0
    g138: BSplineCurve PolesCount=4 KnotsCount=2 Degree=3 IsPeriodic=0
    g139: BSplineCurve PolesCount=4 KnotsCount=2 Degree=3 IsPeriodic=0
    g140: BSplineCurve PolesCount=4 KnotsCount=2 Degree=3 IsPeriodic=0
    g141: BSplineCurve PolesCount=4 KnotsCount=2 Degree=3 IsPeriodic=0
    g142: BSplineCurve PolesCount=4 KnotsCount=2 Degree=3 IsPeriodic=0
    g143: BSplineCurve PolesCount=4 KnotsCount=2 Degree=3 IsPeriodic=0
    g144: BSplineCurve PolesCount=4 KnotsCount=2 Degree=3 IsPeriodic=0
    g145: BSplineCurve PolesCount=2 KnotsCount=2 Degree=1 IsPeriodic=0
    g146: BSplineCurve PolesCount=2 KnotsCount=2 Degree=1 IsPeriodic=0
    g147: BSplineCurve PolesCount=4 KnotsCount=2 Degree=3 IsPeriodic=0
    g148: BSplineCurve PolesCount=4 KnotsCount=2 Degree=3 IsPeriodic=0
    g149: BSplineCurve PolesCount=4 KnotsCount=2 Degree=3 IsPeriodic=0
    g150: BSplineCurve PolesCount=4 KnotsCount=2 Degree=3 IsPeriodic=0
    g151: BSplineCurve PolesCount=4 KnotsCount=2 Degree=3 IsPeriodic=0
    g152: BSplineCurve PolesCount=4 KnotsCount=2 Degree=3 IsPeriodic=0
    g153: BSplineCurve PolesCount=4 KnotsCount=2 Degree=3 IsPeriodic=0
    g154: BSplineCurve PolesCount=4 KnotsCount=2 Degree=3 IsPeriodic=0
    g155: BSplineCurve PolesCount=4 KnotsCount=2 Degree=3 IsPeriodic=0
    g156: BSplineCurve PolesCount=4 KnotsCount=2 Degree=3 IsPeriodic=0
    g157: BSplineCurve PolesCount=4 KnotsCount=2 Degree=3 IsPeriodic=0
    g158: BSplineCurve PolesCount=4 KnotsCount=2 Degree=3 IsPeriodic=0
    g159: BSplineCurve PolesCount=4 KnotsCount=2 Degree=3 IsPeriodic=0
    g160: BSplineCurve PolesCount=4 KnotsCount=2 Degree=3 IsPeriodic=0
    g161: BSplineCurve PolesCount=4 KnotsCount=2 Degree=3 IsPeriodic=0
    g162: BSplineCurve PolesCount=4 KnotsCount=2 Degree=3 IsPeriodic=0
    g163: BSplineCurve PolesCount=4 KnotsCount=2 Degree=3 IsPeriodic=0
    g164: BSplineCurve PolesCount=4 KnotsCount=2 Degree=3 IsPeriodic=0
    g165: BSplineCurve PolesCount=4 KnotsCount=2 Degree=3 IsPeriodic=0
    g166: BSplineCurve PolesCount=4 KnotsCount=2 Degree=3 IsPeriodic=0
    g167: BSplineCurve PolesCount=4 KnotsCount=2 Degree=3 IsPeriodic=0
    g168: BSplineCurve PolesCount=4 KnotsCount=2 Degree=3 IsPeriodic=0
    g169: BSplineCurve PolesCount=4 KnotsCount=2 Degree=3 IsPeriodic=0
    g170: BSplineCurve PolesCount=4 KnotsCount=2 Degree=3 IsPeriodic=0
    g171: BSplineCurve PolesCount=4 KnotsCount=2 Degree=3 IsPeriodic=0
    g172: BSplineCurve PolesCount=4 KnotsCount=2 Degree=3 IsPeriodic=0
    g173: BSplineCurve PolesCount=4 KnotsCount=2 Degree=3 IsPeriodic=0
    g174: BSplineCurve PolesCount=4 KnotsCount=2 Degree=3 IsPeriodic=0
    g175-g179: Circle [constr] x5 (B-spline internal-alignment scaffolding for g83; pole/knot coordinates omitted)
    g180: GeomPoint [constr] X=29.5661 Y=-17.132 Z=0
    g181: GeomPoint [constr] X=25.3471 Y=-22.4687 Z=0
    g182-g187: Circle [constr] x6 (B-spline internal-alignment scaffolding for g83; pole/knot coordinates omitted)
    g188-g192: Circle [constr] x5 (B-spline internal-alignment scaffolding for g74; pole/knot coordinates omitted)
    g193: GeomPoint [constr] X=10.2745 Y=-6.53217 Z=0
    g194: GeomPoint [constr] X=17.1384 Y=-0.441922 Z=0
    g195: Circle [constr] CenterX=15.4873 CenterY=0.384084 CenterZ=0 NormalX=0 NormalY=0 NormalZ=1 AngleXU=0 Radius=1
    g196: Circle [constr] CenterX=17.1384 CenterY=-0.441922 CenterZ=0 NormalX=0 NormalY=0 NormalZ=1 AngleXU=0 Radius=1
    g197-g201: Circle [constr] x5 (B-spline internal-alignment scaffolding for g122; pole/knot coordinates omitted)
    g202: GeomPoint [constr] X=11.4536 Y=-22.664 Z=0
    g203: GeomPoint [constr] X=9.08189 Y=-26.0807 Z=0
    g204-g208: Circle [constr] x5 (B-spline internal-alignment scaffolding for g90; pole/knot coordinates omitted)
    g209: GeomPoint [constr] X=22.6272 Y=-24.7948 Z=0
    g210: GeomPoint [constr] X=18.3299 Y=-24.8281 Z=0
    g211: Circle [constr] CenterX=18.3299 CenterY=-24.8281 CenterZ=0 NormalX=0 NormalY=0 NormalZ=1 AngleXU=0 Radius=1
    g212: Circle [constr] CenterX=9.08189 CenterY=-26.0807 CenterZ=0 NormalX=0 NormalY=0 NormalZ=1 AngleXU=0 Radius=1
  constraints (245):
    c: Coincident(g0,g1)
    c: Coincident(g1,g2)
    c: Coincident(g2,g3)
    c: Coincident(g3,g4)
    c: Coincident(g4,g5)
    c: Coincident(g5,g6)
    c: Coincident(g6,g7)
    c: Coincident(g7,g0)
    c: Coincident(g8,g9)
    c: Coincident(g9,g10)
    c: Coincident(g10,g11)
    c: Coincident(g11,g12)
    c: Coincident(g12,g13)
    c: Coincident(g13,g14)
    c: Coincident(g14,g15)
    c: Coincident(g15,g16)
    c: Coincident(g16,g17)
    c: Coincident(g17,g18)
    c: Coincident(g18,g8)
    c: Coincident(g19,g20)
    c: Coincident(g20,g21)
    c: Coincident(g21,g22)
    c: Coincident(g22,g23)
    c: Coincident(g23,g24)
    c: Coincident(g24,g25)
    c: Coincident(g25,g26)
    c: Coincident(g26,g27)
    c: Coincident(g27,g28)
    c: Coincident(g28,g19)
    c: Coincident(g29,g30)
    c: Coincident(g30,g31)
    c: Coincident(g31,g32)
    c: Coincident(g32,g33)
    c: Coincident(g33,g34)
    c: Coincident(g34,g35)
    c: Coincident(g35,g36)
    c: Coincident(g36,g37)
    c: Coincident(g37,g38)
    c: Coincident(g38,g29)
    c: Coincident(g39,g40)
    c: Coincident(g40,g41)
    c: Coincident(g41,g42)
    c: Coincident(g42,g39)
    c: Coincident(g43,g44)
    c: Coincident(g44,g45)
    c: Coincident(g45,g46)
    c: Coincident(g46,g47)
    c: Coincident(g47,g48)
    c: Coincident(g48,g49)
    c: Coincident(g49,g50)
    c: Coincident(g50,g51)
    c: Coincident(g51,g43)
    c: Coincident(g52,g53)
    c: Coincident(g53,g54)
    c: Coincident(g54,g55)
    c: Coincident(g55,g56)
    c: Coincident(g56,g57)
    c: Coincident(g57,g52)
    c: Coincident(g58,g59)
    c: Coincident(g59,g60)
    c: Coincident(g60,g61)
    c: Coincident(g61,g62)
    c: Coincident(g62,g63)
    c: Coincident(g63,g64)
    c: Coincident(g64,g65)
    c: Coincident(g65,g66)
    c: Coincident(g66,g67)
    c: Coincident(g67,g68)
    c: Coincident(g68,g69)
    c: Coincident(g69,g70)
    c: Coincident(g70,g71)
    c: Coincident(g71,g72)
    c: Coincident(g72,g73)
    c: Coincident(g73,g74)
    c: Coincident(g74,g75)
    c: Coincident(g75,g76)
    c: Coincident(g76,g77)
    c: Coincident(g77,g78)
    c: Coincident(g78,g79)
    c: Coincident(g79,g80)
    c: Coincident(g80,g81)
    c: Coincident(g81,g82)
    c: Coincident(g82,g83)
    c: Coincident(g83,g84)
    c: Coincident(g84,g85)
    c: Coincident(g85,g86)
    c: Coincident(g86,g87)
    c: Coincident(g87,g88)
    c: Coincident(g88,g89)
    c: Coincident(g89,g90)
    c: Coincident(g90,g91)
    c: Coincident(g91,g92)
    c: Coincident(g92,g93)
    c: Coincident(g93,g94)
    c: Coincident(g94,g95)
    c: Coincident(g95,g96)
    c: Coincident(g96,g97)
    c: Coincident(g97,g98)
    c: Coincident(g98,g99)
    c: Coincident(g99,g100)
    c: Coincident(g100,g101)
    c: Coincident(g101,g102)
    c: Coincident(g102,g103)
    c: Coincident(g103,g104)
    c: Coincident(g104,g105)
    c: Coincident(g105,g106)
    c: Coincident(g106,g107)
    c: Coincident(g107,g108)
    c: Coincident(g108,g109)
    c: Coincident(g109,g110)
    c: Coincident(g110,g111)
    c: Coincident(g111,g112)
    c: Coincident(g112,g113)
    c: Coincident(g113,g114)
    c: Coincident(g114,g115)
    c: Coincident(g115,g116)
    c: Coincident(g116,g117)
    c: Coincident(g117,g118)
    c: Coincident(g118,g119)
    c: Coincident(g119,g120)
    c: Coincident(g120,g121)
    c: Coincident(g121,g122)
    c: Coincident(g122,g58)
    c: Coincident(g123,g124)
    c: Coincident(g124,g125)
    c: Coincident(g125,g126)
    c: Coincident(g126,g127)
    c: Coincident(g127,g128)
    c: Coincident(g128,g129)
    c: Coincident(g129,g130)
    c: Coincident(g130,g131)
    c: Coincident(g131,g132)
    c: Coincident(g132,g133)
    c: Coincident(g133,g123)
    c: Coincident(g134,g135)
    c: Coincident(g135,g136)
    c: Coincident(g136,g137)
    c: Coincident(g137,g138)
    c: Coincident(g138,g134)
    c: Coincident(g139,g140)
    c: Coincident(g140,g141)
    c: Coincident(g141,g142)
    c: Coincident(g142,g139)
    c: Coincident(g143,g144)
    c: Coincident(g144,g145)
    c: Coincident(g145,g146)
    c: Coincident(g146,g147)
    c: Coincident(g147,g148)
    c: Coincident(g148,g143)
    c: Coincident(g149,g150)
    c: Coincident(g150,g151)
    c: Coincident(g151,g152)
    c: Coincident(g152,g149)
    c: Coincident(g153,g154)
    c: Coincident(g154,g155)
    c: Coincident(g155,g156)
    c: Coincident(g156,g157)
    c: Coincident(g157,g158)
    c: Coincident(g158,g159)
    c: Coincident(g159,g160)
    c: Coincident(g160,g161)
    c: Coincident(g161,g153)
    c: Coincident(g162,g163)
    c: Coincident(g163,g164)
    c: Coincident(g164,g165)
    c: Coincident(g165,g166)
    c: Coincident(g166,g167)
    c: Coincident(g167,g168)
    c: Coincident(g168,g169)
    c: Coincident(g169,g170)
    c: Coincident(g170,g171)
    c: Coincident(g171,g172)
    c: Coincident(g172,g173)
    c: Coincident(g173,g174)
    c: Coincident(g174,g162)
    c: Coincident(g123,g123)
    c: Coincident(g19,g19)
    c: InternalAlignment(g175,g83)
    c: Weight(g175) = 1
    c: InternalAlignment(g176,g83)
    c: Equal(g176,g175)
    c: InternalAlignment(g177,g83)
    c: Equal(g177,g175)
    c: InternalAlignment(g178,g83)
    c: Equal(g178,g175)
    c: InternalAlignment(g179,g83)
    c: Equal(g179,g175)
    c: InternalAlignment(g180,g83)
    c: InternalAlignment(g181,g83)
    c: InternalAlignment(g182,g83)
    c: Equal(g182,g175)
    c: InternalAlignment(g183,g83)
    c: Equal(g183,g175)
    c: InternalAlignment(g184,g83)
    c: Equal(g184,g175)
    c: InternalAlignment(g185,g83)
    c: Equal(g185,g175)
    c: InternalAlignment(g186,g83)
    c: Equal(g186,g175)
    c: InternalAlignment(g187,g83)
    c: Equal(g187,g175)
    c: InternalAlignment(g188,g74)
    c: Weight(g188) = 1
    c: InternalAlignment(g189,g74)
    c: Equal(g189,g188)
    c: InternalAlignment(g190,g74)
    c: Equal(g190,g188)
    c: InternalAlignment(g191,g74)
    c: Equal(g191,g188)
    c: InternalAlignment(g192,g74)
    c: Equal(g192,g188)
    c: InternalAlignment(g193,g74)
    c: InternalAlignment(g194,g74)
    c: InternalAlignment(g195,g74)
    c: Equal(g195,g188)
    c: InternalAlignment(g196,g74)
    c: Equal(g196,g188)
    c: InternalAlignment(g197,g122)
    c: Weight(g197) = 1
    c: InternalAlignment(g198,g122)
    c: Equal(g198,g197)
    c: InternalAlignment(g199,g122)
    c: Equal(g199,g197)
    c: InternalAlignment(g200,g122)
    c: Equal(g200,g197)
    c: InternalAlignment(g201,g122)
    c: Equal(g201,g197)
    c: InternalAlignment(g202,g122)
    c: InternalAlignment(g203,g122)
    c: InternalAlignment(g204,g90)
    c: Weight(g204) = 1
    c: InternalAlignment(g205,g90)
    c: Equal(g205,g204)
    c: InternalAlignment(g206,g90)
    c: Equal(g206,g204)
    c: InternalAlignment(g207,g90)
    c: Equal(g207,g204)
    c: InternalAlignment(g208,g90)
    c: Equal(g208,g204)
    c: InternalAlignment(g209,g90)
    c: InternalAlignment(g210,g90)
    c: InternalAlignment(g211,g90)
    c: Equal(g211,g204)
    c: InternalAlignment(g212,g122)
    c: Equal(g212,g197)
FEATURE [Sketcher::SketchObject] Sketch040  label="Oracle-Sketch"
  ArcFitTolerance = 1e-06
  FullyConstrained = false
  MakeInternals = false
  Placement = pos=(-15.1786,10.386,0) rot=(0,0,1;0rad)
  expr: .Placement.Base.x = -(.Shape.BoundBox.XLength / 2)
  expr: .Placement.Base.y = .Shape.BoundBox.YLength / 2
  sketch-geometry (210):
    g0: BSplineCurve PolesCount=4 KnotsCount=2 Degree=3 IsPeriodic=0
    g1: BSplineCurve PolesCount=4 KnotsCount=2 Degree=3 IsPeriodic=0
    g2: BSplineCurve PolesCount=4 KnotsCount=2 Degree=3 IsPeriodic=0
    g3: BSplineCurve PolesCount=4 KnotsCount=2 Degree=3 IsPeriodic=0
    g4: BSplineCurve PolesCount=4 KnotsCount=2 Degree=3 IsPeriodic=0
    g5: BSplineCurve PolesCount=4 KnotsCount=2 Degree=3 IsPeriodic=0
    g6: BSplineCurve PolesCount=4 KnotsCount=2 Degree=3 IsPeriodic=0
    g7: BSplineCurve PolesCount=4 KnotsCount=2 Degree=3 IsPeriodic=0
    g8: BSplineCurve PolesCount=2 KnotsCount=2 Degree=1 IsPeriodic=0
    g9: BSplineCurve PolesCount=4 KnotsCount=2 Degree=3 IsPeriodic=0
    g10: BSplineCurve PolesCount=4 KnotsCount=2 Degree=3 IsPeriodic=0
    g11: BSplineCurve PolesCount=4 KnotsCount=2 Degree=3 IsPeriodic=0
    g12: BSplineCurve PolesCount=4 KnotsCount=2 Degree=3 IsPeriodic=0
    g13: BSplineCurve PolesCount=4 KnotsCount=2 Degree=3 IsPeriodic=0
    g14: BSplineCurve PolesCount=4 KnotsCount=2 Degree=3 IsPeriodic=0
    g15: BSplineCurve PolesCount=4 KnotsCount=2 Degree=3 IsPeriodic=0
    g16: BSplineCurve PolesCount=4 KnotsCount=2 Degree=3 IsPeriodic=0
    g17: BSplineCurve PolesCount=4 KnotsCount=2 Degree=3 IsPeriodic=0
    g18: BSplineCurve PolesCount=4 KnotsCount=2 Degree=3 IsPeriodic=0
    g19: BSplineCurve PolesCount=4 KnotsCount=2 Degree=3 IsPeriodic=0
    g20: BSplineCurve PolesCount=4 KnotsCount=2 Degree=3 IsPeriodic=0
    g21: BSplineCurve PolesCount=4 KnotsCount=2 Degree=3 IsPeriodic=0
    g22: BSplineCurve PolesCount=4 KnotsCount=2 Degree=3 IsPeriodic=0
    g23: BSplineCurve PolesCount=4 KnotsCount=2 Degree=3 IsPeriodic=0
    g24: BSplineCurve PolesCount=4 KnotsCount=2 Degree=3 IsPeriodic=0
    g25: BSplineCurve PolesCount=4 KnotsCount=2 Degree=3 IsPeriodic=0
    g26: BSplineCurve PolesCount=4 KnotsCount=2 Degree=3 IsPeriodic=0
    g27: BSplineCurve PolesCount=4 KnotsCount=2 Degree=3 IsPeriodic=0
    g28: BSplineCurve PolesCount=4 KnotsCount=2 Degree=3 IsPeriodic=0
    g29: BSplineCurve PolesCount=4 KnotsCount=2 Degree=3 IsPeriodic=0
    g30: BSplineCurve PolesCount=4 KnotsCount=2 Degree=3 IsPeriodic=0
    g31: BSplineCurve PolesCount=4 KnotsCount=2 Degree=3 IsPeriodic=0
    g32: BSplineCurve PolesCount=4 KnotsCount=2 Degree=3 IsPeriodic=0
    g33: BSplineCurve PolesCount=4 KnotsCount=2 Degree=3 IsPeriodic=0
    g34: BSplineCurve PolesCount=4 KnotsCount=2 Degree=3 IsPeriodic=0
    g35: BSplineCurve PolesCount=4 KnotsCount=2 Degree=3 IsPeriodic=0
    g36: BSplineCurve PolesCount=4 KnotsCount=2 Degree=3 IsPeriodic=0
    g37: BSplineCurve PolesCount=4 KnotsCount=2 Degree=3 IsPeriodic=0
    g38: BSplineCurve PolesCount=4 KnotsCount=2 Degree=3 IsPeriodic=0
    g39: BSplineCurve PolesCount=4 KnotsCount=2 Degree=3 IsPeriodic=0
    g40: BSplineCurve PolesCount=4 KnotsCount=2 Degree=3 IsPeriodic=0
    g41: BSplineCurve PolesCount=4 KnotsCount=2 Degree=3 IsPeriodic=0
    g42: BSplineCurve PolesCount=2 KnotsCount=2 Degree=1 IsPeriodic=0
    g43: BSplineCurve PolesCount=4 KnotsCount=2 Degree=3 IsPeriodic=0
    g44: BSplineCurve PolesCount=4 KnotsCount=2 Degree=3 IsPeriodic=0
    g45: BSplineCurve PolesCount=4 KnotsCount=2 Degree=3 IsPeriodic=0
    g46: BSplineCurve PolesCount=4 KnotsCount=2 Degree=3 IsPeriodic=0
    g47: BSplineCurve PolesCount=4 KnotsCount=2 Degree=3 IsPeriodic=0
    g48: BSplineCurve PolesCount=4 KnotsCount=2 Degree=3 IsPeriodic=0
    g49: BSplineCurve PolesCount=4 KnotsCount=2 Degree=3 IsPeriodic=0
    g50: BSplineCurve PolesCount=4 KnotsCount=2 Degree=3 IsPeriodic=0
    g51: BSplineCurve PolesCount=4 KnotsCount=2 Degree=3 IsPeriodic=0
    g52: BSplineCurve PolesCount=4 KnotsCount=2 Degree=3 IsPeriodic=0
    g53: BSplineCurve PolesCount=4 KnotsCount=2 Degree=3 IsPeriodic=0
    g54: BSplineCurve PolesCount=4 KnotsCount=2 Degree=3 IsPeriodic=0
    g55: BSplineCurve PolesCount=4 KnotsCount=2 Degree=3 IsPeriodic=0
    g56: BSplineCurve PolesCount=4 KnotsCount=2 Degree=3 IsPeriodic=0
    g57: BSplineCurve PolesCount=4 KnotsCount=2 Degree=3 IsPeriodic=0
    g58: BSplineCurve PolesCount=4 KnotsCount=2 Degree=3 IsPeriodic=0
    g59: BSplineCurve PolesCount=4 KnotsCount=2 Degree=3 IsPeriodic=0
    g60: BSplineCurve PolesCount=4 KnotsCount=2 Degree=3 IsPeriodic=0
    g61: BSplineCurve PolesCount=4 KnotsCount=2 Degree=3 IsPeriodic=0
    g62: BSplineCurve PolesCount=4 KnotsCount=2 Degree=3 IsPeriodic=0
    g63: BSplineCurve PolesCount=4 KnotsCount=2 Degree=3 IsPeriodic=0
    g64: BSplineCurve PolesCount=4 KnotsCount=2 Degree=3 IsPeriodic=0
    g65: BSplineCurve PolesCount=4 KnotsCount=2 Degree=3 IsPeriodic=0
    g66: BSplineCurve PolesCount=4 KnotsCount=2 Degree=3 IsPeriodic=0
    g67: BSplineCurve PolesCount=4 KnotsCount=2 Degree=3 IsPeriodic=0
    g68: BSplineCurve PolesCount=4 KnotsCount=2 Degree=3 IsPeriodic=0
    g69: BSplineCurve PolesCount=4 KnotsCount=2 Degree=3 IsPeriodic=0
    g70: BSplineCurve PolesCount=4 KnotsCount=2 Degree=3 IsPeriodic=0
    g71: BSplineCurve PolesCount=4 KnotsCount=2 Degree=3 IsPeriodic=0
    g72: BSplineCurve PolesCount=4 KnotsCount=2 Degree=3 IsPeriodic=0
    g73: BSplineCurve PolesCount=4 KnotsCount=2 Degree=3 IsPeriodic=0
    g74: BSplineCurve PolesCount=2 KnotsCount=2 Degree=1 IsPeriodic=0
    g75: BSplineCurve PolesCount=2 KnotsCount=2 Degree=1 IsPeriodic=0
    g76: BSplineCurve PolesCount=4 KnotsCount=2 Degree=3 IsPeriodic=0
    g77: BSplineCurve PolesCount=4 KnotsCount=2 Degree=3 IsPeriodic=0
    g78: BSplineCurve PolesCount=2 KnotsCount=2 Degree=1 IsPeriodic=0
    g79: BSplineCurve PolesCount=2 KnotsCount=2 Degree=1 IsPeriodic=0
    g80: BSplineCurve PolesCount=4 KnotsCount=2 Degree=3 IsPeriodic=0
    g81: BSplineCurve PolesCount=4 KnotsCount=2 Degree=3 IsPeriodic=0
    g82: BSplineCurve PolesCount=4 KnotsCount=2 Degree=3 IsPeriodic=0
    g83: BSplineCurve PolesCount=4 KnotsCount=2 Degree=3 IsPeriodic=0
    g84: BSplineCurve PolesCount=4 KnotsCount=2 Degree=3 IsPeriodic=0
    g85: BSplineCurve PolesCount=4 KnotsCount=2 Degree=3 IsPeriodic=0
    g86: BSplineCurve PolesCount=4 KnotsCount=2 Degree=3 IsPeriodic=0
    g87: BSplineCurve PolesCount=4 KnotsCount=2 Degree=3 IsPeriodic=0
    g88: BSplineCurve PolesCount=4 KnotsCount=2 Degree=3 IsPeriodic=0
    g89: BSplineCurve PolesCount=4 KnotsCount=2 Degree=3 IsPeriodic=0
    g90: BSplineCurve PolesCount=4 KnotsCount=2 Degree=3 IsPeriodic=0
    g91: BSplineCurve PolesCount=4 KnotsCount=2 Degree=3 IsPeriodic=0
    g92: BSplineCurve PolesCount=4 KnotsCount=2 Degree=3 IsPeriodic=0
    g93: BSplineCurve PolesCount=4 KnotsCount=2 Degree=3 IsPeriodic=0
    g94: BSplineCurve PolesCount=4 KnotsCount=2 Degree=3 IsPeriodic=0
    g95: BSplineCurve PolesCount=4 KnotsCount=2 Degree=3 IsPeriodic=0
    g96: BSplineCurve PolesCount=4 KnotsCount=2 Degree=3 IsPeriodic=0
    g97: BSplineCurve PolesCount=4 KnotsCount=2 Degree=3 IsPeriodic=0
    g98: BSplineCurve PolesCount=4 KnotsCount=2 Degree=3 IsPeriodic=0
    g99: BSplineCurve PolesCount=4 KnotsCount=2 Degree=3 IsPeriodic=0
    g100: BSplineCurve PolesCount=4 KnotsCount=2 Degree=3 IsPeriodic=0
    g101: BSplineCurve PolesCount=4 KnotsCount=2 Degree=3 IsPeriodic=0
    g102: BSplineCurve PolesCount=4 KnotsCount=2 Degree=3 IsPeriodic=0
    g103: BSplineCurve PolesCount=4 KnotsCount=2 Degree=3 IsPeriodic=0
    g104: BSplineCurve PolesCount=4 KnotsCount=2 Degree=3 IsPeriodic=0
    g105: BSplineCurve PolesCount=4 KnotsCount=2 Degree=3 IsPeriodic=0
    g106: BSplineCurve PolesCount=4 KnotsCount=2 Degree=3 IsPeriodic=0
    g107: BSplineCurve PolesCount=4 KnotsCount=2 Degree=3 IsPeriodic=0
    g108: BSplineCurve PolesCount=4 KnotsCount=2 Degree=3 IsPeriodic=0
    g109: BSplineCurve PolesCount=4 KnotsCount=2 Degree=3 IsPeriodic=0
    g110: BSplineCurve PolesCount=4 KnotsCount=2 Degree=3 IsPeriodic=0
    g111: BSplineCurve PolesCount=4 KnotsCount=2 Degree=3 IsPeriodic=0
    g112: BSplineCurve PolesCount=4 KnotsCount=2 Degree=3 IsPeriodic=0
    g113: BSplineCurve PolesCount=2 KnotsCount=2 Degree=1 IsPeriodic=0
    g114: BSplineCurve PolesCount=2 KnotsCount=2 Degree=1 IsPeriodic=0
    g115: BSplineCurve PolesCount=4 KnotsCount=2 Degree=3 IsPeriodic=0
    g116: BSplineCurve PolesCount=4 KnotsCount=2 Degree=3 IsPeriodic=0
    g117: BSplineCurve PolesCount=4 KnotsCount=2 Degree=3 IsPeriodic=0
    g118: BSplineCurve PolesCount=4 KnotsCount=2 Degree=3 IsPeriodic=0
    g119: BSplineCurve PolesCount=4 KnotsCount=2 Degree=3 IsPeriodic=0
    g120: BSplineCurve PolesCount=4 KnotsCount=2 Degree=3 IsPeriodic=0
    g121: BSplineCurve PolesCount=4 KnotsCount=2 Degree=3 IsPeriodic=0
    g122: BSplineCurve PolesCount=4 KnotsCount=2 Degree=3 IsPeriodic=0
    g123: BSplineCurve PolesCount=4 KnotsCount=2 Degree=3 IsPeriodic=0
    g124: BSplineCurve PolesCount=4 KnotsCount=2 Degree=3 IsPeriodic=0
    g125: BSplineCurve PolesCount=4 KnotsCount=2 Degree=3 IsPeriodic=0
    g126: BSplineCurve PolesCount=4 KnotsCount=2 Degree=3 IsPeriodic=0
    g127: BSplineCurve PolesCount=4 KnotsCount=2 Degree=3 IsPeriodic=0
    g128: BSplineCurve PolesCount=4 KnotsCount=2 Degree=3 IsPeriodic=0
    g129: BSplineCurve PolesCount=4 KnotsCount=2 Degree=3 IsPeriodic=0
    g130: BSplineCurve PolesCount=4 KnotsCount=2 Degree=3 IsPeriodic=0
    g131: BSplineCurve PolesCount=4 KnotsCount=2 Degree=3 IsPeriodic=0
    g132: BSplineCurve PolesCount=4 KnotsCount=2 Degree=3 IsPeriodic=0
    g133: BSplineCurve PolesCount=4 KnotsCount=2 Degree=3 IsPeriodic=0
    g134: BSplineCurve PolesCount=4 KnotsCount=2 Degree=3 IsPeriodic=0
    g135: BSplineCurve PolesCount=2 KnotsCount=2 Degree=1 IsPeriodic=0
    g136: BSplineCurve PolesCount=2 KnotsCount=2 Degree=1 IsPeriodic=0
    g137: BSplineCurve PolesCount=4 KnotsCount=2 Degree=3 IsPeriodic=0
    g138: BSplineCurve PolesCount=4 KnotsCount=2 Degree=3 IsPeriodic=0
    g139: BSplineCurve PolesCount=4 KnotsCount=2 Degree=3 IsPeriodic=0
    g140: BSplineCurve PolesCount=4 KnotsCount=2 Degree=3 IsPeriodic=0
    g141: BSplineCurve PolesCount=4 KnotsCount=2 Degree=3 IsPeriodic=0
    g142: BSplineCurve PolesCount=4 KnotsCount=2 Degree=3 IsPeriodic=0
    g143: BSplineCurve PolesCount=4 KnotsCount=2 Degree=3 IsPeriodic=0
    g144: BSplineCurve PolesCount=4 KnotsCount=2 Degree=3 IsPeriodic=0
    g145: BSplineCurve PolesCount=4 KnotsCount=2 Degree=3 IsPeriodic=0
    g146: BSplineCurve PolesCount=4 KnotsCount=2 Degree=3 IsPeriodic=0
    g147: BSplineCurve PolesCount=4 KnotsCount=2 Degree=3 IsPeriodic=0
    g148: BSplineCurve PolesCount=4 KnotsCount=2 Degree=3 IsPeriodic=0
    g149: BSplineCurve PolesCount=4 KnotsCount=2 Degree=3 IsPeriodic=0
    g150: BSplineCurve PolesCount=4 KnotsCount=2 Degree=3 IsPeriodic=0
    g151: BSplineCurve PolesCount=4 KnotsCount=2 Degree=3 IsPeriodic=0
    g152: BSplineCurve PolesCount=4 KnotsCount=2 Degree=3 IsPeriodic=0
    g153: BSplineCurve PolesCount=4 KnotsCount=2 Degree=3 IsPeriodic=0
    g154: BSplineCurve PolesCount=4 KnotsCount=2 Degree=3 IsPeriodic=0
    g155: BSplineCurve PolesCount=4 KnotsCount=2 Degree=3 IsPeriodic=0
    g156: BSplineCurve PolesCount=4 KnotsCount=2 Degree=3 IsPeriodic=0
    g157: BSplineCurve PolesCount=4 KnotsCount=2 Degree=3 IsPeriodic=0
    g158: BSplineCurve PolesCount=4 KnotsCount=2 Degree=3 IsPeriodic=0
    g159: BSplineCurve PolesCount=4 KnotsCount=2 Degree=3 IsPeriodic=0
    g160: BSplineCurve PolesCount=4 KnotsCount=2 Degree=3 IsPeriodic=0
    g161: BSplineCurve PolesCount=4 KnotsCount=2 Degree=3 IsPeriodic=0
    g162: BSplineCurve PolesCount=4 KnotsCount=2 Degree=3 IsPeriodic=0
    g163: BSplineCurve PolesCount=4 KnotsCount=2 Degree=3 IsPeriodic=0
    g164: BSplineCurve PolesCount=4 KnotsCount=2 Degree=3 IsPeriodic=0
    g165: BSplineCurve PolesCount=4 KnotsCount=2 Degree=3 IsPeriodic=0
    g166: BSplineCurve PolesCount=4 KnotsCount=2 Degree=3 IsPeriodic=0
    g167: BSplineCurve PolesCount=4 KnotsCount=2 Degree=3 IsPeriodic=0
    g168: BSplineCurve PolesCount=4 KnotsCount=2 Degree=3 IsPeriodic=0
    g169: BSplineCurve PolesCount=4 KnotsCount=2 Degree=3 IsPeriodic=0
    g170: BSplineCurve PolesCount=4 KnotsCount=2 Degree=3 IsPeriodic=0
    g171: BSplineCurve PolesCount=4 KnotsCount=2 Degree=3 IsPeriodic=0
    g172: BSplineCurve PolesCount=4 KnotsCount=2 Degree=3 IsPeriodic=0
    g173: BSplineCurve PolesCount=4 KnotsCount=2 Degree=3 IsPeriodic=0
    g174: BSplineCurve PolesCount=4 KnotsCount=2 Degree=3 IsPeriodic=0
    g175: BSplineCurve PolesCount=4 KnotsCount=2 Degree=3 IsPeriodic=0
    g176: BSplineCurve PolesCount=4 KnotsCount=2 Degree=3 IsPeriodic=0
    g177: BSplineCurve PolesCount=4 KnotsCount=2 Degree=3 IsPeriodic=0
    g178: BSplineCurve PolesCount=4 KnotsCount=2 Degree=3 IsPeriodic=0
    g179: BSplineCurve PolesCount=4 KnotsCount=2 Degree=3 IsPeriodic=0
    g180: BSplineCurve PolesCount=4 KnotsCount=2 Degree=3 IsPeriodic=0
    g181: BSplineCurve PolesCount=4 KnotsCount=2 Degree=3 IsPeriodic=0
    g182: BSplineCurve PolesCount=4 KnotsCount=2 Degree=3 IsPeriodic=0
    g183: BSplineCurve PolesCount=2 KnotsCount=2 Degree=1 IsPeriodic=0
    g184: BSplineCurve PolesCount=4 KnotsCount=2 Degree=3 IsPeriodic=0
    g185: BSplineCurve PolesCount=4 KnotsCount=2 Degree=3 IsPeriodic=0
    g186: BSplineCurve PolesCount=4 KnotsCount=2 Degree=3 IsPeriodic=0
    g187: BSplineCurve PolesCount=4 KnotsCount=2 Degree=3 IsPeriodic=0
    g188: BSplineCurve PolesCount=4 KnotsCount=2 Degree=3 IsPeriodic=0
    g189: BSplineCurve PolesCount=4 KnotsCount=2 Degree=3 IsPeriodic=0
    g190: BSplineCurve PolesCount=4 KnotsCount=2 Degree=3 IsPeriodic=0
    g191: BSplineCurve PolesCount=4 KnotsCount=2 Degree=3 IsPeriodic=0
    g192: BSplineCurve PolesCount=4 KnotsCount=2 Degree=3 IsPeriodic=0
    g193: BSplineCurve PolesCount=4 KnotsCount=2 Degree=3 IsPeriodic=0
    g194: BSplineCurve PolesCount=4 KnotsCount=2 Degree=3 IsPeriodic=0
    g195: BSplineCurve PolesCount=4 KnotsCount=2 Degree=3 IsPeriodic=0
    g196: BSplineCurve PolesCount=4 KnotsCount=2 Degree=3 IsPeriodic=0
    g197: BSplineCurve PolesCount=4 KnotsCount=2 Degree=3 IsPeriodic=0
    g198: BSplineCurve PolesCount=4 KnotsCount=2 Degree=3 IsPeriodic=0
    g199: BSplineCurve PolesCount=4 KnotsCount=2 Degree=3 IsPeriodic=0
    g200: BSplineCurve PolesCount=4 KnotsCount=2 Degree=3 IsPeriodic=0
    g201: BSplineCurve PolesCount=4 KnotsCount=2 Degree=3 IsPeriodic=0
    g202: BSplineCurve PolesCount=4 KnotsCount=2 Degree=3 IsPeriodic=0
    g203: BSplineCurve PolesCount=4 KnotsCount=2 Degree=3 IsPeriodic=0
    g204: BSplineCurve PolesCount=4 KnotsCount=2 Degree=3 IsPeriodic=0
    g205: BSplineCurve PolesCount=4 KnotsCount=2 Degree=3 IsPeriodic=0
    g206: BSplineCurve PolesCount=4 KnotsCount=2 Degree=3 IsPeriodic=0
    g207: BSplineCurve PolesCount=4 KnotsCount=2 Degree=3 IsPeriodic=0
    g208: BSplineCurve PolesCount=4 KnotsCount=2 Degree=3 IsPeriodic=0
    g209: BSplineCurve PolesCount=4 KnotsCount=2 Degree=3 IsPeriodic=0
  constraints (213):
    c: Coincident(g0,g1)
    c: Coincident(g1,g2)
    c: Coincident(g2,g3)
    c: Coincident(g3,g4)
    c: Coincident(g4,g0)
    c: Coincident(g5,g6)
    c: Coincident(g6,g7)
    c: Coincident(g7,g8)
    c: Coincident(g8,g5)
    c: Coincident(g9,g10)
    c: Coincident(g10,g11)
    c: Coincident(g11,g12)
    c: Coincident(g12,g13)
    c: Coincident(g13,g14)
    c: Coincident(g14,g15)
    c: Coincident(g15,g16)
    c: Coincident(g16,g17)
    c: Coincident(g17,g18)
    c: Coincident(g18,g19)
    c: Coincident(g19,g20)
    c: Coincident(g20,g21)
    c: Coincident(g21,g22)
    c: Coincident(g22,g23)
    c: Coincident(g23,g24)
    c: Coincident(g24,g25)
    c: Coincident(g25,g26)
    c: Coincident(g26,g27)
    c: Coincident(g27,g28)
    c: Coincident(g28,g29)
    c: Coincident(g29,g30)
    c: Coincident(g30,g31)
    c: Coincident(g31,g32)
    c: Coincident(g32,g33)
    c: Coincident(g33,g34)
    c: Coincident(g34,g35)
    c: Coincident(g35,g36)
    c: Coincident(g36,g37)
    c: Coincident(g37,g38)
    c: Coincident(g38,g39)
    c: Coincident(g39,g40)
    c: Coincident(g40,g41)
    c: Coincident(g41,g42)
    c: Coincident(g42,g9)
    c: Coincident(g43,g44)
    c: Coincident(g44,g45)
    c: Coincident(g45,g46)
    c: Coincident(g46,g47)
    c: Coincident(g47,g48)
    c: Coincident(g48,g49)
    c: Coincident(g49,g50)
    c: Coincident(g50,g51)
    c: Coincident(g51,g52)
    c: Coincident(g52,g53)
    c: Coincident(g53,g54)
    c: Coincident(g54,g55)
    c: Coincident(g55,g56)
    c: Coincident(g56,g57)
    c: Coincident(g57,g58)
    c: Coincident(g58,g59)
    c: Coincident(g59,g43)
    c: Coincident(g60,g61)
    c: Coincident(g61,g62)
    c: Coincident(g62,g63)
    c: Coincident(g63,g64)
    c: Coincident(g64,g65)
    c: Coincident(g65,g66)
    c: Coincident(g66,g67)
    c: Coincident(g67,g68)
    c: Coincident(g68,g69)
    c: Coincident(g69,g70)
    c: Coincident(g70,g71)
    c: Coincident(g71,g72)
    c: Coincident(g72,g73)
    c: Coincident(g73,g74)
    c: Coincident(g74,g75)
    c: Coincident(g75,g76)
    c: Coincident(g76,g77)
    c: Coincident(g77,g78)
    c: Coincident(g78,g79)
    c: Coincident(g79,g80)
    c: Coincident(g80,g81)
    c: Coincident(g81,g82)
    c: Coincident(g82,g83)
    c: Coincident(g83,g84)
    c: Coincident(g84,g85)
    c: Coincident(g85,g86)
    c: Coincident(g86,g87)
    c: Coincident(g87,g88)
    c: Coincident(g88,g89)
    c: Coincident(g89,g90)
    c: Coincident(g90,g91)
    c: Coincident(g91,g92)
    c: Coincident(g92,g93)
    c: Coincident(g93,g94)
    c: Coincident(g94,g95)
    c: Coincident(g95,g96)
    c: Coincident(g96,g97)
    c: Coincident(g97,g98)
    c: Coincident(g98,g99)
    c: Coincident(g99,g100)
    c: Coincident(g100,g101)
    c: Coincident(g101,g102)
    c: Coincident(g102,g103)
    c: Coincident(g103,g104)
    c: Coincident(g104,g105)
    c: Coincident(g105,g106)
    c: Coincident(g106,g107)
    c: Coincident(g107,g108)
    c: Coincident(g108,g109)
    c: Coincident(g109,g110)
    c: Coincident(g110,g111)
    c: Coincident(g111,g112)
    c: Coincident(g112,g113)
    c: Coincident(g113,g114)
    c: Coincident(g114,g115)
    c: Coincident(g115,g116)
    c: Coincident(g116,g117)
    c: Coincident(g117,g118)
    c: Coincident(g118,g119)
    c: Coincident(g119,g120)
    c: Coincident(g120,g121)
    c: Coincident(g121,g122)
    c: Coincident(g122,g123)
    c: Coincident(g123,g124)
    c: Coincident(g124,g125)
    c: Coincident(g125,g126)
    c: Coincident(g126,g127)
    c: Coincident(g127,g128)
    c: Coincident(g128,g129)
    c: Coincident(g129,g130)
    c: Coincident(g130,g131)
    c: Coincident(g131,g132)
    c: Coincident(g132,g133)
    c: Coincident(g133,g134)
    c: Coincident(g134,g135)
    c: Coincident(g135,g136)
    c: Coincident(g136,g137)
    c: Coincident(g137,g138)
    c: Coincident(g138,g139)
    c: Coincident(g139,g140)
    c: Coincident(g140,g141)
    c: Coincident(g141,g142)
    c: Coincident(g142,g143)
    c: Coincident(g143,g144)
    c: Coincident(g144,g145)
    c: Coincident(g145,g146)
    c: Coincident(g146,g147)
    c: Coincident(g147,g148)
    c: Coincident(g148,g149)
    c: Coincident(g149,g150)
    c: Coincident(g150,g151)
    c: Coincident(g151,g152)
    c: Coincident(g152,g153)
    c: Coincident(g153,g154)
    c: Coincident(g154,g155)
    c: Coincident(g155,g156)
    c: Coincident(g156,g157)
    c: Coincident(g157,g158)
    c: Coincident(g158,g159)
    c: Coincident(g159,g160)
    c: Coincident(g160,g161)
    c: Coincident(g161,g162)
    c: Coincident(g162,g163)
    c: Coincident(g163,g164)
    c: Coincident(g164,g165)
    c: Coincident(g165,g166)
    c: Coincident(g166,g167)
    c: Coincident(g167,g168)
    c: Coincident(g168,g169)
    c: Coincident(g169,g170)
    c: Coincident(g170,g171)
    c: Coincident(g171,g172)
    c: Coincident(g172,g173)
    c: Coincident(g173,g174)
    c: Coincident(g174,g175)
    c: Coincident(g175,g176)
    c: Coincident(g176,g177)
    c: Coincident(g177,g178)
    c: Coincident(g178,g179)
    c: Coincident(g179,g180)
    c: Coincident(g180,g181)
    c: Coincident(g181,g182)
    c: Coincident(g182,g183)
    c: Coincident(g183,g60)
    c: Coincident(g184,g185)
    c: Coincident(g185,g186)
    c: Coincident(g186,g187)
    c: Coincident(g187,g188)
    c: Coincident(g188,g189)
    c: Coincident(g189,g190)
    c: Coincident(g190,g191)
    c: Coincident(g191,g192)
    c: Coincident(g192,g193)
    c: Coincident(g193,g194)
    c: Coincident(g194,g195)
    c: Coincident(g195,g196)
    c: Coincident(g196,g197)
    c: Coincident(g197,g198)
    c: Coincident(g198,g184)
    c: Coincident(g199,g200)
    c: Coincident(g200,g201)
    c: Coincident(g201,g202)
    c: Coincident(g202,g203)
    c: Coincident(g203,g199)
    c: Coincident(g204,g205)
    c: Coincident(g205,g206)
    c: Coincident(g206,g204)
    c: Coincident(g207,g208)
    c: Coincident(g208,g209)
    c: Coincident(g209,g207)
    c: Coincident(g41,g9)
    c: Coincident(g182,g60)
    c: Coincident(g7,g5)
FEATURE [Sketcher::SketchObject] Sketch041  label="Philosopher-Sketch"
  ArcFitTolerance = 1e-06
  FullyConstrained = false
  MakeInternals = false
  Placement = pos=(-11.6116,15.5029,0) rot=(0,0,1;0rad)
  expr: .Placement.Base.x = -(.Shape.BoundBox.XLength / 2)
  expr: .Placement.Base.y = .Shape.BoundBox.YLength / 2
  sketch-geometry (155):
    g0: BSplineCurve PolesCount=4 KnotsCount=2 Degree=3 IsPeriodic=0
    g1: BSplineCurve PolesCount=4 KnotsCount=2 Degree=3 IsPeriodic=0
    g2: BSplineCurve PolesCount=4 KnotsCount=2 Degree=3 IsPeriodic=0
    g3: BSplineCurve PolesCount=4 KnotsCount=2 Degree=3 IsPeriodic=0
    g4: BSplineCurve PolesCount=4 KnotsCount=2 Degree=3 IsPeriodic=0
    g5: BSplineCurve PolesCount=4 KnotsCount=2 Degree=3 IsPeriodic=0
    g6: BSplineCurve PolesCount=4 KnotsCount=2 Degree=3 IsPeriodic=0
    g7: BSplineCurve PolesCount=4 KnotsCount=2 Degree=3 IsPeriodic=0
    g8: BSplineCurve PolesCount=4 KnotsCount=2 Degree=3 IsPeriodic=0
    g9: BSplineCurve PolesCount=4 KnotsCount=2 Degree=3 IsPeriodic=0
    g10: BSplineCurve PolesCount=4 KnotsCount=2 Degree=3 IsPeriodic=0
    g11: BSplineCurve PolesCount=4 KnotsCount=2 Degree=3 IsPeriodic=0
    g12: BSplineCurve PolesCount=4 KnotsCount=2 Degree=3 IsPeriodic=0
    g13: BSplineCurve PolesCount=4 KnotsCount=2 Degree=3 IsPeriodic=0
    g14: BSplineCurve PolesCount=4 KnotsCount=2 Degree=3 IsPeriodic=0
    g15: BSplineCurve PolesCount=4 KnotsCount=2 Degree=3 IsPeriodic=0
    g16: BSplineCurve PolesCount=4 KnotsCount=2 Degree=3 IsPeriodic=0
    g17: BSplineCurve PolesCount=4 KnotsCount=2 Degree=3 IsPeriodic=0
    g18: BSplineCurve PolesCount=4 KnotsCount=2 Degree=3 IsPeriodic=0
    g19: BSplineCurve PolesCount=4 KnotsCount=2 Degree=3 IsPeriodic=0
    g20: BSplineCurve PolesCount=4 KnotsCount=2 Degree=3 IsPeriodic=0
    g21: BSplineCurve PolesCount=4 KnotsCount=2 Degree=3 IsPeriodic=0
    g22: BSplineCurve PolesCount=4 KnotsCount=2 Degree=3 IsPeriodic=0
    g23: BSplineCurve PolesCount=4 KnotsCount=2 Degree=3 IsPeriodic=0
    g24: BSplineCurve PolesCount=4 KnotsCount=2 Degree=3 IsPeriodic=0
    g25: BSplineCurve PolesCount=4 KnotsCount=2 Degree=3 IsPeriodic=0
    g26: BSplineCurve PolesCount=4 KnotsCount=2 Degree=3 IsPeriodic=0
    g27: BSplineCurve PolesCount=4 KnotsCount=2 Degree=3 IsPeriodic=0
    g28: BSplineCurve PolesCount=4 KnotsCount=2 Degree=3 IsPeriodic=0
    g29: BSplineCurve PolesCount=4 KnotsCount=2 Degree=3 IsPeriodic=0
    g30: BSplineCurve PolesCount=4 KnotsCount=2 Degree=3 IsPeriodic=0
    g31: BSplineCurve PolesCount=4 KnotsCount=2 Degree=3 IsPeriodic=0
    g32: BSplineCurve PolesCount=4 KnotsCount=2 Degree=3 IsPeriodic=0
    g33: BSplineCurve PolesCount=4 KnotsCount=2 Degree=3 IsPeriodic=0
    g34: BSplineCurve PolesCount=4 KnotsCount=2 Degree=3 IsPeriodic=0
    g35: BSplineCurve PolesCount=4 KnotsCount=2 Degree=3 IsPeriodic=0
    g36: BSplineCurve PolesCount=4 KnotsCount=2 Degree=3 IsPeriodic=0
    g37: BSplineCurve PolesCount=4 KnotsCount=2 Degree=3 IsPeriodic=0
    g38: BSplineCurve PolesCount=4 KnotsCount=2 Degree=3 IsPeriodic=0
    g39: BSplineCurve PolesCount=4 KnotsCount=2 Degree=3 IsPeriodic=0
    g40: BSplineCurve PolesCount=4 KnotsCount=2 Degree=3 IsPeriodic=0
    g41: BSplineCurve PolesCount=4 KnotsCount=2 Degree=3 IsPeriodic=0
    g42: BSplineCurve PolesCount=4 KnotsCount=2 Degree=3 IsPeriodic=0
    g43: BSplineCurve PolesCount=4 KnotsCount=2 Degree=3 IsPeriodic=0
    g44: BSplineCurve PolesCount=4 KnotsCount=2 Degree=3 IsPeriodic=0
    g45: BSplineCurve PolesCount=4 KnotsCount=2 Degree=3 IsPeriodic=0
    g46: BSplineCurve PolesCount=4 KnotsCount=2 Degree=3 IsPeriodic=0
    g47: BSplineCurve PolesCount=4 KnotsCount=2 Degree=3 IsPeriodic=0
    g48: BSplineCurve PolesCount=4 KnotsCount=2 Degree=3 IsPeriodic=0
    g49: BSplineCurve PolesCount=4 KnotsCount=2 Degree=3 IsPeriodic=0
    g50: BSplineCurve PolesCount=4 KnotsCount=2 Degree=3 IsPeriodic=0
    g51: BSplineCurve PolesCount=2 KnotsCount=2 Degree=1 IsPeriodic=0
    g52: BSplineCurve PolesCount=2 KnotsCount=2 Degree=1 IsPeriodic=0
    g53: BSplineCurve PolesCount=4 KnotsCount=2 Degree=3 IsPeriodic=0
    g54: BSplineCurve PolesCount=4 KnotsCount=2 Degree=3 IsPeriodic=0
    g55: BSplineCurve PolesCount=4 KnotsCount=2 Degree=3 IsPeriodic=0
    g56: BSplineCurve PolesCount=4 KnotsCount=2 Degree=3 IsPeriodic=0
    g57: BSplineCurve PolesCount=4 KnotsCount=2 Degree=3 IsPeriodic=0
    g58: BSplineCurve PolesCount=4 KnotsCount=2 Degree=3 IsPeriodic=0
    g59: BSplineCurve PolesCount=4 KnotsCount=2 Degree=3 IsPeriodic=0
    g60: BSplineCurve PolesCount=4 KnotsCount=2 Degree=3 IsPeriodic=0
    g61: BSplineCurve PolesCount=4 KnotsCount=2 Degree=3 IsPeriodic=0
    g62: BSplineCurve PolesCount=4 KnotsCount=2 Degree=3 IsPeriodic=0
    g63: BSplineCurve PolesCount=4 KnotsCount=2 Degree=3 IsPeriodic=0
    g64: BSplineCurve PolesCount=4 KnotsCount=2 Degree=3 IsPeriodic=0
    g65: BSplineCurve PolesCount=2 KnotsCount=2 Degree=1 IsPeriodic=0
    g66: BSplineCurve PolesCount=2 KnotsCount=2 Degree=1 IsPeriodic=0
    g67: BSplineCurve PolesCount=4 KnotsCount=2 Degree=3 IsPeriodic=0
    g68: BSplineCurve PolesCount=4 KnotsCount=2 Degree=3 IsPeriodic=0
    g69: BSplineCurve PolesCount=4 KnotsCount=2 Degree=3 IsPeriodic=0
    g70: BSplineCurve PolesCount=4 KnotsCount=2 Degree=3 IsPeriodic=0
    g71: BSplineCurve PolesCount=4 KnotsCount=2 Degree=3 IsPeriodic=0
    g72: BSplineCurve PolesCount=4 KnotsCount=2 Degree=3 IsPeriodic=0
    g73: BSplineCurve PolesCount=4 KnotsCount=2 Degree=3 IsPeriodic=0
    g74: BSplineCurve PolesCount=4 KnotsCount=2 Degree=3 IsPeriodic=0
    g75: BSplineCurve PolesCount=4 KnotsCount=2 Degree=3 IsPeriodic=0
    g76: BSplineCurve PolesCount=4 KnotsCount=2 Degree=3 IsPeriodic=0
    g77: BSplineCurve PolesCount=4 KnotsCount=2 Degree=3 IsPeriodic=0
    g78: BSplineCurve PolesCount=4 KnotsCount=2 Degree=3 IsPeriodic=0
    g79: BSplineCurve PolesCount=4 KnotsCount=2 Degree=3 IsPeriodic=0
    g80: BSplineCurve PolesCount=4 KnotsCount=2 Degree=3 IsPeriodic=0
    g81: BSplineCurve PolesCount=4 KnotsCount=2 Degree=3 IsPeriodic=0
    g82: BSplineCurve PolesCount=4 KnotsCount=2 Degree=3 IsPeriodic=0
    g83: BSplineCurve PolesCount=4 KnotsCount=2 Degree=3 IsPeriodic=0
    g84: BSplineCurve PolesCount=4 KnotsCount=2 Degree=3 IsPeriodic=0
    g85: BSplineCurve PolesCount=4 KnotsCount=2 Degree=3 IsPeriodic=0
    g86: BSplineCurve PolesCount=4 KnotsCount=2 Degree=3 IsPeriodic=0
    g87: BSplineCurve PolesCount=4 KnotsCount=2 Degree=3 IsPeriodic=0
    g88: BSplineCurve PolesCount=4 KnotsCount=2 Degree=3 IsPeriodic=0
    g89: BSplineCurve PolesCount=4 KnotsCount=2 Degree=3 IsPeriodic=0
    g90: BSplineCurve PolesCount=4 KnotsCount=2 Degree=3 IsPeriodic=0
    g91: BSplineCurve PolesCount=4 KnotsCount=2 Degree=3 IsPeriodic=0
    g92: BSplineCurve PolesCount=4 KnotsCount=2 Degree=3 IsPeriodic=0
    g93: BSplineCurve PolesCount=4 KnotsCount=2 Degree=3 IsPeriodic=0
    g94: BSplineCurve PolesCount=4 KnotsCount=2 Degree=3 IsPeriodic=0
    g95: BSplineCurve PolesCount=4 KnotsCount=2 Degree=3 IsPeriodic=0
    g96: BSplineCurve PolesCount=4 KnotsCount=2 Degree=3 IsPeriodic=0
    g97: BSplineCurve PolesCount=4 KnotsCount=2 Degree=3 IsPeriodic=0
    g98: BSplineCurve PolesCount=4 KnotsCount=2 Degree=3 IsPeriodic=0
    g99: BSplineCurve PolesCount=4 KnotsCount=2 Degree=3 IsPeriodic=0
    g100: BSplineCurve PolesCount=4 KnotsCount=2 Degree=3 IsPeriodic=0
    g101: BSplineCurve PolesCount=4 KnotsCount=2 Degree=3 IsPeriodic=0
    g102: BSplineCurve PolesCount=4 KnotsCount=2 Degree=3 IsPeriodic=0
    g103: BSplineCurve PolesCount=4 KnotsCount=2 Degree=3 IsPeriodic=0
    g104: BSplineCurve PolesCount=4 KnotsCount=2 Degree=3 IsPeriodic=0
    g105: BSplineCurve PolesCount=4 KnotsCount=2 Degree=3 IsPeriodic=0
    g106: BSplineCurve PolesCount=4 KnotsCount=2 Degree=3 IsPeriodic=0
    g107: BSplineCurve PolesCount=4 KnotsCount=2 Degree=3 IsPeriodic=0
    g108: BSplineCurve PolesCount=4 KnotsCount=2 Degree=3 IsPeriodic=0
    g109: BSplineCurve PolesCount=4 KnotsCount=2 Degree=3 IsPeriodic=0
    g110: BSplineCurve PolesCount=4 KnotsCount=2 Degree=3 IsPeriodic=0
    g111: BSplineCurve PolesCount=4 KnotsCount=2 Degree=3 IsPeriodic=0
    g112: BSplineCurve PolesCount=4 KnotsCount=2 Degree=3 IsPeriodic=0
    g113: BSplineCurve PolesCount=4 KnotsCount=2 Degree=3 IsPeriodic=0
    g114: BSplineCurve PolesCount=4 KnotsCount=2 Degree=3 IsPeriodic=0
    g115: BSplineCurve PolesCount=4 KnotsCount=2 Degree=3 IsPeriodic=0
    g116: BSplineCurve PolesCount=4 KnotsCount=2 Degree=3 IsPeriodic=0
    g117: BSplineCurve PolesCount=4 KnotsCount=2 Degree=3 IsPeriodic=0
    g118: BSplineCurve PolesCount=4 KnotsCount=2 Degree=3 IsPeriodic=0
    g119: BSplineCurve PolesCount=4 KnotsCount=2 Degree=3 IsPeriodic=0
    g120: BSplineCurve PolesCount=4 KnotsCount=2 Degree=3 IsPeriodic=0
    g121: BSplineCurve PolesCount=4 KnotsCount=2 Degree=3 IsPeriodic=0
    g122: BSplineCurve PolesCount=4 KnotsCount=2 Degree=3 IsPeriodic=0
    g123: BSplineCurve PolesCount=4 KnotsCount=2 Degree=3 IsPeriodic=0
    g124: BSplineCurve PolesCount=4 KnotsCount=2 Degree=3 IsPeriodic=0
    g125: BSplineCurve PolesCount=4 KnotsCount=2 Degree=3 IsPeriodic=0
    g126: BSplineCurve PolesCount=4 KnotsCount=2 Degree=3 IsPeriodic=0
    g127: BSplineCurve PolesCount=4 KnotsCount=2 Degree=3 IsPeriodic=0
    g128: BSplineCurve PolesCount=2 KnotsCount=2 Degree=1 IsPeriodic=0
    g129: BSplineCurve PolesCount=2 KnotsCount=2 Degree=1 IsPeriodic=0
    g130: BSplineCurve PolesCount=4 KnotsCount=2 Degree=3 IsPeriodic=0
    g131: BSplineCurve PolesCount=4 KnotsCount=2 Degree=3 IsPeriodic=0
    g132: BSplineCurve PolesCount=4 KnotsCount=2 Degree=3 IsPeriodic=0
    g133: BSplineCurve PolesCount=4 KnotsCount=2 Degree=3 IsPeriodic=0
    g134: BSplineCurve PolesCount=4 KnotsCount=2 Degree=3 IsPeriodic=0
    g135: BSplineCurve PolesCount=4 KnotsCount=2 Degree=3 IsPeriodic=0
    g136: BSplineCurve PolesCount=4 KnotsCount=2 Degree=3 IsPeriodic=0
    g137: BSplineCurve PolesCount=4 KnotsCount=2 Degree=3 IsPeriodic=0
    g138: BSplineCurve PolesCount=4 KnotsCount=2 Degree=3 IsPeriodic=0
    g139: BSplineCurve PolesCount=4 KnotsCount=2 Degree=3 IsPeriodic=0
    g140: BSplineCurve PolesCount=4 KnotsCount=2 Degree=3 IsPeriodic=0
    g141: BSplineCurve PolesCount=4 KnotsCount=2 Degree=3 IsPeriodic=0
    g142: BSplineCurve PolesCount=4 KnotsCount=2 Degree=3 IsPeriodic=0
    g143: BSplineCurve PolesCount=2 KnotsCount=2 Degree=1 IsPeriodic=0
    g144: BSplineCurve PolesCount=2 KnotsCount=2 Degree=1 IsPeriodic=0
    g145: BSplineCurve PolesCount=4 KnotsCount=2 Degree=3 IsPeriodic=0
    g146: BSplineCurve PolesCount=4 KnotsCount=2 Degree=3 IsPeriodic=0
    g147: BSplineCurve PolesCount=4 KnotsCount=2 Degree=3 IsPeriodic=0
    g148: BSplineCurve PolesCount=4 KnotsCount=2 Degree=3 IsPeriodic=0
    g149: BSplineCurve PolesCount=4 KnotsCount=2 Degree=3 IsPeriodic=0
    g150: BSplineCurve PolesCount=4 KnotsCount=2 Degree=3 IsPeriodic=0
    g151: BSplineCurve PolesCount=4 KnotsCount=2 Degree=3 IsPeriodic=0
    g152: BSplineCurve PolesCount=4 KnotsCount=2 Degree=3 IsPeriodic=0
    g153: BSplineCurve PolesCount=4 KnotsCount=2 Degree=3 IsPeriodic=0
    g154: BSplineCurve PolesCount=4 KnotsCount=2 Degree=3 IsPeriodic=0
  constraints (155):
    c: Coincident(g0,g1)
    c: Coincident(g1,g2)
    c: Coincident(g2,g3)
    c: Coincident(g3,g4)
    c: Coincident(g4,g5)
    c: Coincident(g5,g6)
    c: Coincident(g6,g7)
    c: Coincident(g7,g8)
    c: Coincident(g8,g9)
    c: Coincident(g9,g0)
    c: Coincident(g10,g11)
    c: Coincident(g11,g12)
    c: Coincident(g13,g14)
    c: Coincident(g14,g15)
    c: Coincident(g16,g17)
    c: Coincident(g17,g18)
    c: Coincident(g19,g20)
    c: Coincident(g20,g21)
    c: Coincident(g21,g19)
    c: Coincident(g22,g23)
    c: Coincident(g23,g24)
    c: Coincident(g24,g25)
    c: Coincident(g25,g26)
    c: Coincident(g26,g27)
    c: Coincident(g27,g28)
    c: Coincident(g28,g29)
    c: Coincident(g29,g30)
    c: Coincident(g30,g31)
    c: Coincident(g31,g32)
    c: Coincident(g32,g33)
    c: Coincident(g33,g34)
    c: Coincident(g34,g35)
    c: Coincident(g35,g36)
    c: Coincident(g36,g37)
    c: Coincident(g37,g38)
    c: Coincident(g38,g39)
    c: Coincident(g39,g40)
    c: Coincident(g40,g41)
    c: Coincident(g41,g42)
    c: Coincident(g42,g43)
    c: Coincident(g43,g44)
    c: Coincident(g44,g45)
    c: Coincident(g45,g46)
    c: Coincident(g46,g47)
    c: Coincident(g47,g48)
    c: Coincident(g48,g49)
    c: Coincident(g49,g50)
    c: Coincident(g50,g51)
    c: Coincident(g51,g52)
    c: Coincident(g52,g53)
    c: Coincident(g53,g54)
    c: Coincident(g54,g55)
    c: Coincident(g55,g56)
    c: Coincident(g56,g57)
    c: Coincident(g57,g58)
    c: Coincident(g58,g59)
    c: Coincident(g59,g60)
    c: Coincident(g60,g61)
    c: Coincident(g61,g62)
    c: Coincident(g62,g63)
    c: Coincident(g63,g64)
    c: Coincident(g64,g65)
    c: Coincident(g65,g66)
    c: Coincident(g66,g67)
    c: Coincident(g67,g68)
    c: Coincident(g68,g69)
    c: Coincident(g69,g70)
    c: Coincident(g70,g71)
    c: Coincident(g71,g72)
    c: Coincident(g72,g73)
    c: Coincident(g73,g74)
    c: Coincident(g74,g75)
    c: Coincident(g75,g76)
    c: Coincident(g76,g77)
    c: Coincident(g77,g78)
    c: Coincident(g78,g79)
    c: Coincident(g79,g80)
    c: Coincident(g80,g81)
    c: Coincident(g81,g82)
    c: Coincident(g82,g83)
    c: Coincident(g83,g84)
    c: Coincident(g84,g85)
    c: Coincident(g86,g87)
    c: Coincident(g87,g88)
    c: Coincident(g88,g89)
    c: Coincident(g89,g86)
    c: Coincident(g90,g91)
    c: Coincident(g91,g92)
    c: Coincident(g92,g90)
    c: Coincident(g93,g94)
    c: Coincident(g94,g95)
    c: Coincident(g95,g96)
    c: Coincident(g96,g97)
    c: Coincident(g97,g98)
    c: Coincident(g98,g99)
    c: Coincident(g99,g100)
    c: Coincident(g100,g101)
    c: Coincident(g101,g102)
    c: Coincident(g102,g103)
    c: Coincident(g103,g104)
    c: Coincident(g104,g105)
    c: Coincident(g105,g106)
    c: Coincident(g106,g107)
    c: Coincident(g107,g108)
    c: Coincident(g108,g109)
    c: Coincident(g109,g110)
    c: Coincident(g111,g112)
    c: Coincident(g112,g113)
    c: Coincident(g113,g114)
    c: Coincident(g114,g115)
    c: Coincident(g115,g116)
    c: Coincident(g116,g111)
    c: Coincident(g117,g118)
    c: Coincident(g118,g119)
    c: Coincident(g119,g120)
    c: Coincident(g120,g117)
    c: Coincident(g121,g122)
    c: Coincident(g122,g123)
    c: Coincident(g123,g121)
    c: Coincident(g124,g125)
    c: Coincident(g125,g126)
    c: Coincident(g126,g127)
    c: Coincident(g127,g128)
    c: Coincident(g128,g129)
    c: Coincident(g129,g124)
    c: Coincident(g130,g131)
    c: Coincident(g131,g132)
    c: Coincident(g132,g133)
    c: Coincident(g133,g134)
    c: Coincident(g134,g135)
    c: Coincident(g135,g136)
    c: Coincident(g136,g137)
    c: Coincident(g137,g138)
    c: Coincident(g138,g139)
    c: Coincident(g139,g140)
    c: Coincident(g140,g141)
    c: Coincident(g141,g142)
    c: Coincident(g142,g143)
    c: Coincident(g143,g144)
    c: Coincident(g144,g145)
    c: Coincident(g145,g146)
    c: Coincident(g146,g147)
    c: Coincident(g147,g148)
    c: Coincident(g148,g149)
    c: Coincident(g149,g150)
    c: Coincident(g150,g151)
    c: Coincident(g151,g152)
    c: Coincident(g152,g153)
    c: Coincident(g153,g154)
    c: Coincident(g154,g130)
    c: Coincident(g16,g18)
    c: Coincident(g93,g110)
    c: Coincident(g22,g85)
    c: Coincident(g13,g15)
    c: Coincident(g10,g12)
FEATURE [Sketcher::SketchObject] Sketch042  label="Pit_Hag-Sketch"
  ArcFitTolerance = 1e-06
  FullyConstrained = false
  MakeInternals = false
  Placement = pos=(-15.0581,15.8632,0) rot=(0,0,1;0rad)
  expr: .Placement.Base.x = -(.Shape.BoundBox.XLength / 2)
  expr: .Placement.Base.y = .Shape.BoundBox.YLength / 2
  sketch-geometry (233):
    g0: BSplineCurve PolesCount=4 KnotsCount=2 Degree=3 IsPeriodic=0
    g1: BSplineCurve PolesCount=4 KnotsCount=2 Degree=3 IsPeriodic=0
    g2: BSplineCurve PolesCount=4 KnotsCount=2 Degree=3 IsPeriodic=0
    g3: BSplineCurve PolesCount=4 KnotsCount=2 Degree=3 IsPeriodic=0
    g4: BSplineCurve PolesCount=4 KnotsCount=2 Degree=3 IsPeriodic=0
    g5: BSplineCurve PolesCount=4 KnotsCount=2 Degree=3 IsPeriodic=0
    g6: BSplineCurve PolesCount=4 KnotsCount=2 Degree=3 IsPeriodic=0
    g7: BSplineCurve PolesCount=4 KnotsCount=2 Degree=3 IsPeriodic=0
    g8: BSplineCurve PolesCount=4 KnotsCount=2 Degree=3 IsPeriodic=0
    g9: BSplineCurve PolesCount=4 KnotsCount=2 Degree=3 IsPeriodic=0
    g10: BSplineCurve PolesCount=4 KnotsCount=2 Degree=3 IsPeriodic=0
    g11: BSplineCurve PolesCount=4 KnotsCount=2 Degree=3 IsPeriodic=0
    g12: BSplineCurve PolesCount=4 KnotsCount=2 Degree=3 IsPeriodic=0
    g13: BSplineCurve PolesCount=4 KnotsCount=2 Degree=3 IsPeriodic=0
    g14: BSplineCurve PolesCount=4 KnotsCount=2 Degree=3 IsPeriodic=0
    g15: BSplineCurve PolesCount=4 KnotsCount=2 Degree=3 IsPeriodic=0
    g16: BSplineCurve PolesCount=4 KnotsCount=2 Degree=3 IsPeriodic=0
    g17: BSplineCurve PolesCount=4 KnotsCount=2 Degree=3 IsPeriodic=0
    g18: BSplineCurve PolesCount=4 KnotsCount=2 Degree=3 IsPeriodic=0
    g19: BSplineCurve PolesCount=4 KnotsCount=2 Degree=3 IsPeriodic=0
    g20: BSplineCurve PolesCount=4 KnotsCount=2 Degree=3 IsPeriodic=0
    g21: BSplineCurve PolesCount=4 KnotsCount=2 Degree=3 IsPeriodic=0
    g22: BSplineCurve PolesCount=4 KnotsCount=2 Degree=3 IsPeriodic=0
    g23: BSplineCurve PolesCount=4 KnotsCount=2 Degree=3 IsPeriodic=0
    g24: BSplineCurve PolesCount=4 KnotsCount=2 Degree=3 IsPeriodic=0
    g25: BSplineCurve PolesCount=4 KnotsCount=2 Degree=3 IsPeriodic=0
    g26: BSplineCurve PolesCount=4 KnotsCount=2 Degree=3 IsPeriodic=0
    g27: BSplineCurve PolesCount=4 KnotsCount=2 Degree=3 IsPeriodic=0
    g28: BSplineCurve PolesCount=4 KnotsCount=2 Degree=3 IsPeriodic=0
    g29: BSplineCurve PolesCount=4 KnotsCount=2 Degree=3 IsPeriodic=0
    g30: BSplineCurve PolesCount=4 KnotsCount=2 Degree=3 IsPeriodic=0
    g31: BSplineCurve PolesCount=4 KnotsCount=2 Degree=3 IsPeriodic=0
    g32: BSplineCurve PolesCount=4 KnotsCount=2 Degree=3 IsPeriodic=0
    g33: BSplineCurve PolesCount=4 KnotsCount=2 Degree=3 IsPeriodic=0
    g34: BSplineCurve PolesCount=2 KnotsCount=2 Degree=1 IsPeriodic=0
    g35: BSplineCurve PolesCount=2 KnotsCount=2 Degree=1 IsPeriodic=0
    g36: BSplineCurve PolesCount=4 KnotsCount=2 Degree=3 IsPeriodic=0
    g37: BSplineCurve PolesCount=2 KnotsCount=2 Degree=1 IsPeriodic=0
    g38: BSplineCurve PolesCount=2 KnotsCount=2 Degree=1 IsPeriodic=0
    g39: BSplineCurve PolesCount=4 KnotsCount=2 Degree=3 IsPeriodic=0
    g40: BSplineCurve PolesCount=4 KnotsCount=2 Degree=3 IsPeriodic=0
    g41: BSplineCurve PolesCount=4 KnotsCount=2 Degree=3 IsPeriodic=0
    g42: BSplineCurve PolesCount=4 KnotsCount=2 Degree=3 IsPeriodic=0
    g43: BSplineCurve PolesCount=4 KnotsCount=2 Degree=3 IsPeriodic=0
    g44: BSplineCurve PolesCount=4 KnotsCount=2 Degree=3 IsPeriodic=0
    g45: BSplineCurve PolesCount=4 KnotsCount=2 Degree=3 IsPeriodic=0
    g46: BSplineCurve PolesCount=4 KnotsCount=2 Degree=3 IsPeriodic=0
    g47: BSplineCurve PolesCount=4 KnotsCount=2 Degree=3 IsPeriodic=0
    g48: BSplineCurve PolesCount=4 KnotsCount=2 Degree=3 IsPeriodic=0
    g49: BSplineCurve PolesCount=4 KnotsCount=2 Degree=3 IsPeriodic=0
    g50: BSplineCurve PolesCount=2 KnotsCount=2 Degree=1 IsPeriodic=0
    g51: BSplineCurve PolesCount=2 KnotsCount=2 Degree=1 IsPeriodic=0
    g52: BSplineCurve PolesCount=4 KnotsCount=2 Degree=3 IsPeriodic=0
    g53: BSplineCurve PolesCount=4 KnotsCount=2 Degree=3 IsPeriodic=0
    g54: BSplineCurve PolesCount=4 KnotsCount=2 Degree=3 IsPeriodic=0
    g55: BSplineCurve PolesCount=4 KnotsCount=2 Degree=3 IsPeriodic=0
    g56: BSplineCurve PolesCount=4 KnotsCount=2 Degree=3 IsPeriodic=0
    g57: BSplineCurve PolesCount=4 KnotsCount=2 Degree=3 IsPeriodic=0
    g58: BSplineCurve PolesCount=4 KnotsCount=2 Degree=3 IsPeriodic=0
    g59: BSplineCurve PolesCount=4 KnotsCount=2 Degree=3 IsPeriodic=0
    g60: BSplineCurve PolesCount=4 KnotsCount=2 Degree=3 IsPeriodic=0
    g61: BSplineCurve PolesCount=2 KnotsCount=2 Degree=1 IsPeriodic=0
    g62: BSplineCurve PolesCount=4 KnotsCount=2 Degree=3 IsPeriodic=0
    g63: BSplineCurve PolesCount=4 KnotsCount=2 Degree=3 IsPeriodic=0
    g64: BSplineCurve PolesCount=4 KnotsCount=2 Degree=3 IsPeriodic=0
    g65: BSplineCurve PolesCount=2 KnotsCount=2 Degree=1 IsPeriodic=0
    g66: BSplineCurve PolesCount=2 KnotsCount=2 Degree=1 IsPeriodic=0
    g67: BSplineCurve PolesCount=4 KnotsCount=2 Degree=3 IsPeriodic=0
    g68: BSplineCurve PolesCount=4 KnotsCount=2 Degree=3 IsPeriodic=0
    g69: BSplineCurve PolesCount=2 KnotsCount=2 Degree=1 IsPeriodic=0
    g70: BSplineCurve PolesCount=2 KnotsCount=2 Degree=1 IsPeriodic=0
    g71: BSplineCurve PolesCount=4 KnotsCount=2 Degree=3 IsPeriodic=0
    g72: BSplineCurve PolesCount=4 KnotsCount=2 Degree=3 IsPeriodic=0
    g73: BSplineCurve PolesCount=4 KnotsCount=2 Degree=3 IsPeriodic=0
    g74: BSplineCurve PolesCount=4 KnotsCount=2 Degree=3 IsPeriodic=0
    g75: BSplineCurve PolesCount=4 KnotsCount=2 Degree=3 IsPeriodic=0
    g76: BSplineCurve PolesCount=2 KnotsCount=2 Degree=1 IsPeriodic=0
    g77: BSplineCurve PolesCount=2 KnotsCount=2 Degree=1 IsPeriodic=0
    g78: BSplineCurve PolesCount=4 KnotsCount=2 Degree=3 IsPeriodic=0
    g79: BSplineCurve PolesCount=4 KnotsCount=2 Degree=3 IsPeriodic=0
    g80: BSplineCurve PolesCount=4 KnotsCount=2 Degree=3 IsPeriodic=0
    g81: BSplineCurve PolesCount=4 KnotsCount=2 Degree=3 IsPeriodic=0
    g82: BSplineCurve PolesCount=4 KnotsCount=2 Degree=3 IsPeriodic=0
    g83: BSplineCurve PolesCount=4 KnotsCount=2 Degree=3 IsPeriodic=0
    g84: BSplineCurve PolesCount=4 KnotsCount=2 Degree=3 IsPeriodic=0
    g85: BSplineCurve PolesCount=4 KnotsCount=2 Degree=3 IsPeriodic=0
    g86: BSplineCurve PolesCount=4 KnotsCount=2 Degree=3 IsPeriodic=0
    g87: BSplineCurve PolesCount=4 KnotsCount=2 Degree=3 IsPeriodic=0
    g88: BSplineCurve PolesCount=2 KnotsCount=2 Degree=1 IsPeriodic=0
    g89: BSplineCurve PolesCount=2 KnotsCount=2 Degree=1 IsPeriodic=0
    g90: BSplineCurve PolesCount=4 KnotsCount=2 Degree=3 IsPeriodic=0
    g91: BSplineCurve PolesCount=4 KnotsCount=2 Degree=3 IsPeriodic=0
    g92: BSplineCurve PolesCount=4 KnotsCount=2 Degree=3 IsPeriodic=0
    g93: BSplineCurve PolesCount=4 KnotsCount=2 Degree=3 IsPeriodic=0
    g94: BSplineCurve PolesCount=4 KnotsCount=2 Degree=3 IsPeriodic=0
    g95: BSplineCurve PolesCount=4 KnotsCount=2 Degree=3 IsPeriodic=0
    g96: BSplineCurve PolesCount=4 KnotsCount=2 Degree=3 IsPeriodic=0
    g97: BSplineCurve PolesCount=4 KnotsCount=2 Degree=3 IsPeriodic=0
    g98: BSplineCurve PolesCount=2 KnotsCount=2 Degree=1 IsPeriodic=0
    g99: BSplineCurve PolesCount=2 KnotsCount=2 Degree=1 IsPeriodic=0
    g100: BSplineCurve PolesCount=4 KnotsCount=2 Degree=3 IsPeriodic=0
    g101: BSplineCurve PolesCount=4 KnotsCount=2 Degree=3 IsPeriodic=0
    g102: BSplineCurve PolesCount=4 KnotsCount=2 Degree=3 IsPeriodic=0
    g103: BSplineCurve PolesCount=4 KnotsCount=2 Degree=3 IsPeriodic=0
    g104: BSplineCurve PolesCount=4 KnotsCount=2 Degree=3 IsPeriodic=0
    g105: BSplineCurve PolesCount=4 KnotsCount=2 Degree=3 IsPeriodic=0
    g106: BSplineCurve PolesCount=4 KnotsCount=2 Degree=3 IsPeriodic=0
    g107: BSplineCurve PolesCount=4 KnotsCount=2 Degree=3 IsPeriodic=0
    g108: BSplineCurve PolesCount=4 KnotsCount=2 Degree=3 IsPeriodic=0
    g109: BSplineCurve PolesCount=4 KnotsCount=2 Degree=3 IsPeriodic=0
    g110: BSplineCurve PolesCount=4 KnotsCount=2 Degree=3 IsPeriodic=0
    g111: BSplineCurve PolesCount=4 KnotsCount=2 Degree=3 IsPeriodic=0
    g112: BSplineCurve PolesCount=4 KnotsCount=2 Degree=3 IsPeriodic=0
    g113: BSplineCurve PolesCount=4 KnotsCount=2 Degree=3 IsPeriodic=0
    g114: BSplineCurve PolesCount=4 KnotsCount=2 Degree=3 IsPeriodic=0
    g115: BSplineCurve PolesCount=4 KnotsCount=2 Degree=3 IsPeriodic=0
    g116: BSplineCurve PolesCount=2 KnotsCount=2 Degree=1 IsPeriodic=0
    g117: BSplineCurve PolesCount=2 KnotsCount=2 Degree=1 IsPeriodic=0
    g118: BSplineCurve PolesCount=4 KnotsCount=2 Degree=3 IsPeriodic=0
    g119: BSplineCurve PolesCount=2 KnotsCount=2 Degree=1 IsPeriodic=0
    g120: BSplineCurve PolesCount=2 KnotsCount=2 Degree=1 IsPeriodic=0
    g121: BSplineCurve PolesCount=4 KnotsCount=2 Degree=3 IsPeriodic=0
    g122: BSplineCurve PolesCount=4 KnotsCount=2 Degree=3 IsPeriodic=0
    g123: BSplineCurve PolesCount=4 KnotsCount=2 Degree=3 IsPeriodic=0
    g124: BSplineCurve PolesCount=4 KnotsCount=2 Degree=3 IsPeriodic=0
    g125: BSplineCurve PolesCount=4 KnotsCount=2 Degree=3 IsPeriodic=0
    g126: BSplineCurve PolesCount=4 KnotsCount=2 Degree=3 IsPeriodic=0
    g127: BSplineCurve PolesCount=4 KnotsCount=2 Degree=3 IsPeriodic=0
    g128: BSplineCurve PolesCount=4 KnotsCount=2 Degree=3 IsPeriodic=0
    g129: BSplineCurve PolesCount=4 KnotsCount=2 Degree=3 IsPeriodic=0
    g130: BSplineCurve PolesCount=4 KnotsCount=2 Degree=3 IsPeriodic=0
    g131: BSplineCurve PolesCount=4 KnotsCount=2 Degree=3 IsPeriodic=0
    g132: BSplineCurve PolesCount=2 KnotsCount=2 Degree=1 IsPeriodic=0
    g133: BSplineCurve PolesCount=2 KnotsCount=2 Degree=1 IsPeriodic=0
    g134: BSplineCurve PolesCount=4 KnotsCount=2 Degree=3 IsPeriodic=0
    g135: BSplineCurve PolesCount=4 KnotsCount=2 Degree=3 IsPeriodic=0
    g136: BSplineCurve PolesCount=2 KnotsCount=2 Degree=1 IsPeriodic=0
    g137: BSplineCurve PolesCount=2 KnotsCount=2 Degree=1 IsPeriodic=0
    g138: BSplineCurve PolesCount=4 KnotsCount=2 Degree=3 IsPeriodic=0
    g139: BSplineCurve PolesCount=4 KnotsCount=2 Degree=3 IsPeriodic=0
    g140: BSplineCurve PolesCount=4 KnotsCount=2 Degree=3 IsPeriodic=0
    g141: BSplineCurve PolesCount=4 KnotsCount=2 Degree=3 IsPeriodic=0
    g142: BSplineCurve PolesCount=4 KnotsCount=2 Degree=3 IsPeriodic=0
    g143: BSplineCurve PolesCount=4 KnotsCount=2 Degree=3 IsPeriodic=0
    g144: BSplineCurve PolesCount=4 KnotsCount=2 Degree=3 IsPeriodic=0
    g145: BSplineCurve PolesCount=4 KnotsCount=2 Degree=3 IsPeriodic=0
    g146: BSplineCurve PolesCount=4 KnotsCount=2 Degree=3 IsPeriodic=0
    g147: BSplineCurve PolesCount=4 KnotsCount=2 Degree=3 IsPeriodic=0
    g148: BSplineCurve PolesCount=4 KnotsCount=2 Degree=3 IsPeriodic=0
    g149: BSplineCurve PolesCount=2 KnotsCount=2 Degree=1 IsPeriodic=0
    g150: BSplineCurve PolesCount=2 KnotsCount=2 Degree=1 IsPeriodic=0
    g151: BSplineCurve PolesCount=4 KnotsCount=2 Degree=3 IsPeriodic=0
    g152: BSplineCurve PolesCount=2 KnotsCount=2 Degree=1 IsPeriodic=0
    g153: BSplineCurve PolesCount=2 KnotsCount=2 Degree=1 IsPeriodic=0
    g154: BSplineCurve PolesCount=4 KnotsCount=2 Degree=3 IsPeriodic=0
    g155: BSplineCurve PolesCount=4 KnotsCount=2 Degree=3 IsPeriodic=0
    g156: BSplineCurve PolesCount=4 KnotsCount=2 Degree=3 IsPeriodic=0
    g157: BSplineCurve PolesCount=4 KnotsCount=2 Degree=3 IsPeriodic=0
    g158: BSplineCurve PolesCount=4 KnotsCount=2 Degree=3 IsPeriodic=0
    g159: BSplineCurve PolesCount=2 KnotsCount=2 Degree=1 IsPeriodic=0
    g160: BSplineCurve PolesCount=4 KnotsCount=2 Degree=3 IsPeriodic=0
    g161: BSplineCurve PolesCount=4 KnotsCount=2 Degree=3 IsPeriodic=0
    g162: BSplineCurve PolesCount=4 KnotsCount=2 Degree=3 IsPeriodic=0
    g163: BSplineCurve PolesCount=4 KnotsCount=2 Degree=3 IsPeriodic=0
    g164: BSplineCurve PolesCount=4 KnotsCount=2 Degree=3 IsPeriodic=0
    g165: BSplineCurve PolesCount=4 KnotsCount=2 Degree=3 IsPeriodic=0
    g166: BSplineCurve PolesCount=4 KnotsCount=2 Degree=3 IsPeriodic=0
    g167: BSplineCurve PolesCount=4 KnotsCount=2 Degree=3 IsPeriodic=0
    g168: BSplineCurve PolesCount=4 KnotsCount=2 Degree=3 IsPeriodic=0
    g169: BSplineCurve PolesCount=4 KnotsCount=2 Degree=3 IsPeriodic=0
    g170: BSplineCurve PolesCount=2 KnotsCount=2 Degree=1 IsPeriodic=0
    g171: BSplineCurve PolesCount=2 KnotsCount=2 Degree=1 IsPeriodic=0
    g172: BSplineCurve PolesCount=4 KnotsCount=2 Degree=3 IsPeriodic=0
    g173: BSplineCurve PolesCount=4 KnotsCount=2 Degree=3 IsPeriodic=0
    g174: BSplineCurve PolesCount=4 KnotsCount=2 Degree=3 IsPeriodic=0
    g175: BSplineCurve PolesCount=4 KnotsCount=2 Degree=3 IsPeriodic=0
    g176: BSplineCurve PolesCount=4 KnotsCount=2 Degree=3 IsPeriodic=0
    g177: BSplineCurve PolesCount=4 KnotsCount=2 Degree=3 IsPeriodic=0
    g178: BSplineCurve PolesCount=2 KnotsCount=2 Degree=1 IsPeriodic=0
    g179: BSplineCurve PolesCount=2 KnotsCount=2 Degree=1 IsPeriodic=0
    g180: BSplineCurve PolesCount=4 KnotsCount=2 Degree=3 IsPeriodic=0
    g181: BSplineCurve PolesCount=4 KnotsCount=2 Degree=3 IsPeriodic=0
    g182: BSplineCurve PolesCount=4 KnotsCount=2 Degree=3 IsPeriodic=0
    g183: BSplineCurve PolesCount=4 KnotsCount=2 Degree=3 IsPeriodic=0
    g184: BSplineCurve PolesCount=4 KnotsCount=2 Degree=3 IsPeriodic=0
    g185: BSplineCurve PolesCount=4 KnotsCount=2 Degree=3 IsPeriodic=0
    g186: BSplineCurve PolesCount=4 KnotsCount=2 Degree=3 IsPeriodic=0
    g187: BSplineCurve PolesCount=4 KnotsCount=2 Degree=3 IsPeriodic=0
    g188: BSplineCurve PolesCount=4 KnotsCount=2 Degree=3 IsPeriodic=0
    g189: BSplineCurve PolesCount=4 KnotsCount=2 Degree=3 IsPeriodic=0
    g190: BSplineCurve PolesCount=4 KnotsCount=2 Degree=3 IsPeriodic=0
    g191: BSplineCurve PolesCount=4 KnotsCount=2 Degree=3 IsPeriodic=0
    g192: BSplineCurve PolesCount=4 KnotsCount=2 Degree=3 IsPeriodic=0
    g193: BSplineCurve PolesCount=4 KnotsCount=2 Degree=3 IsPeriodic=0
    g194: BSplineCurve PolesCount=4 KnotsCount=2 Degree=3 IsPeriodic=0
    g195: BSplineCurve PolesCount=4 KnotsCount=2 Degree=3 IsPeriodic=0
    g196: BSplineCurve PolesCount=4 KnotsCount=2 Degree=3 IsPeriodic=0
    g197: BSplineCurve PolesCount=4 KnotsCount=2 Degree=3 IsPeriodic=0
    g198: BSplineCurve PolesCount=4 KnotsCount=2 Degree=3 IsPeriodic=0
    g199: BSplineCurve PolesCount=4 KnotsCount=2 Degree=3 IsPeriodic=0
    g200: BSplineCurve PolesCount=2 KnotsCount=2 Degree=1 IsPeriodic=0
    g201: BSplineCurve PolesCount=2 KnotsCount=2 Degree=1 IsPeriodic=0
    g202: BSplineCurve PolesCount=4 KnotsCount=2 Degree=3 IsPeriodic=0
    g203: BSplineCurve PolesCount=4 KnotsCount=2 Degree=3 IsPeriodic=0
    g204: BSplineCurve PolesCount=4 KnotsCount=2 Degree=3 IsPeriodic=0
    g205: BSplineCurve PolesCount=4 KnotsCount=2 Degree=3 IsPeriodic=0
    g206: BSplineCurve PolesCount=4 KnotsCount=2 Degree=3 IsPeriodic=0
    g207: BSplineCurve PolesCount=4 KnotsCount=2 Degree=3 IsPeriodic=0
    g208: BSplineCurve PolesCount=4 KnotsCount=2 Degree=3 IsPeriodic=0
    g209: BSplineCurve PolesCount=4 KnotsCount=2 Degree=3 IsPeriodic=0
    g210: BSplineCurve PolesCount=4 KnotsCount=2 Degree=3 IsPeriodic=0
    g211: BSplineCurve PolesCount=4 KnotsCount=2 Degree=3 IsPeriodic=0
    g212: BSplineCurve PolesCount=4 KnotsCount=2 Degree=3 IsPeriodic=0
    g213: BSplineCurve PolesCount=4 KnotsCount=2 Degree=3 IsPeriodic=0
    g214: BSplineCurve PolesCount=4 KnotsCount=2 Degree=3 IsPeriodic=0
    g215: BSplineCurve PolesCount=4 KnotsCount=2 Degree=3 IsPeriodic=0
    g216: BSplineCurve PolesCount=4 KnotsCount=2 Degree=3 IsPeriodic=0
    g217: BSplineCurve PolesCount=4 KnotsCount=2 Degree=3 IsPeriodic=0
    g218: BSplineCurve PolesCount=4 KnotsCount=2 Degree=3 IsPeriodic=0
    g219: BSplineCurve PolesCount=4 KnotsCount=2 Degree=3 IsPeriodic=0
    g220: BSplineCurve PolesCount=4 KnotsCount=2 Degree=3 IsPeriodic=0
    g221: BSplineCurve PolesCount=2 KnotsCount=2 Degree=1 IsPeriodic=0
    g222: BSplineCurve PolesCount=2 KnotsCount=2 Degree=1 IsPeriodic=0
    g223: BSplineCurve PolesCount=4 KnotsCount=2 Degree=3 IsPeriodic=0
    g224: BSplineCurve PolesCount=4 KnotsCount=2 Degree=3 IsPeriodic=0
    g225: BSplineCurve PolesCount=4 KnotsCount=2 Degree=3 IsPeriodic=0
    g226: BSplineCurve PolesCount=4 KnotsCount=2 Degree=3 IsPeriodic=0
    g227: BSplineCurve PolesCount=4 KnotsCount=2 Degree=3 IsPeriodic=0
    g228: BSplineCurve PolesCount=4 KnotsCount=2 Degree=3 IsPeriodic=0
    g229: BSplineCurve PolesCount=4 KnotsCount=2 Degree=3 IsPeriodic=0
    g230: BSplineCurve PolesCount=4 KnotsCount=2 Degree=3 IsPeriodic=0
    g231: BSplineCurve PolesCount=4 KnotsCount=2 Degree=3 IsPeriodic=0
    g232: BSplineCurve PolesCount=4 KnotsCount=2 Degree=3 IsPeriodic=0
  constraints (235):
    c: Coincident(g0,g1)
    c: Coincident(g1,g2)
    c: Coincident(g2,g0)
    c: Coincident(g3,g4)
    c: Coincident(g4,g5)
    c: Coincident(g5,g6)
    c: Coincident(g6,g7)
    c: Coincident(g7,g8)
    c: Coincident(g8,g3)
    c: Coincident(g9,g10)
    c: Coincident(g10,g11)
    c: Coincident(g11,g12)
    c: Coincident(g12,g13)
    c: Coincident(g13,g9)
    c: Coincident(g14,g15)
    c: Coincident(g15,g16)
    c: Coincident(g16,g17)
    c: Coincident(g17,g18)
    c: Coincident(g18,g19)
    c: Coincident(g19,g20)
    c: Coincident(g20,g21)
    c: Coincident(g21,g22)
    c: Coincident(g22,g14)
    c: Coincident(g23,g24)
    c: Coincident(g24,g25)
    c: Coincident(g25,g23)
    c: Coincident(g26,g27)
    c: Coincident(g27,g28)
    c: Coincident(g28,g26)
    c: Coincident(g29,g30)
    c: Coincident(g30,g31)
    c: Coincident(g31,g32)
    c: Coincident(g32,g33)
    c: Coincident(g33,g34)
    c: Coincident(g34,g35)
    c: Coincident(g35,g36)
    c: Coincident(g36,g37)
    c: Coincident(g37,g38)
    c: Coincident(g38,g39)
    c: Coincident(g39,g40)
    c: Coincident(g40,g41)
    c: Coincident(g41,g42)
    c: Coincident(g42,g43)
    c: Coincident(g43,g44)
    c: Coincident(g44,g45)
    c: Coincident(g45,g46)
    c: Coincident(g46,g47)
    c: Coincident(g47,g48)
    c: Coincident(g48,g49)
    c: Coincident(g49,g50)
    c: Coincident(g50,g51)
    c: Coincident(g51,g52)
    c: Coincident(g52,g53)
    c: Coincident(g53,g54)
    c: Coincident(g54,g55)
    c: Coincident(g55,g56)
    c: Coincident(g56,g57)
    c: Coincident(g57,g58)
    c: Coincident(g58,g59)
    c: Coincident(g59,g60)
    c: Coincident(g60,g61)
    c: Coincident(g61,g29)
    c: Coincident(g62,g63)
    c: Coincident(g63,g64)
    c: Coincident(g64,g65)
    c: Coincident(g65,g66)
    c: Coincident(g66,g67)
    c: Coincident(g67,g68)
    c: Coincident(g68,g69)
    c: Coincident(g69,g70)
    c: Coincident(g70,g71)
    c: Coincident(g71,g72)
    c: Coincident(g72,g73)
    c: Coincident(g73,g74)
    c: Coincident(g74,g75)
    c: Coincident(g75,g76)
    c: Coincident(g76,g77)
    c: Coincident(g77,g78)
    c: Coincident(g78,g79)
    c: Coincident(g79,g80)
    c: Coincident(g80,g81)
    c: Coincident(g81,g82)
    c: Coincident(g82,g83)
    c: Coincident(g83,g84)
    c: Coincident(g84,g85)
    c: Coincident(g85,g86)
    c: Coincident(g86,g87)
    c: Coincident(g87,g88)
    c: Coincident(g88,g89)
    c: Coincident(g89,g90)
    c: Coincident(g90,g91)
    c: Coincident(g91,g92)
    c: Coincident(g92,g93)
    c: Coincident(g93,g94)
    c: Coincident(g94,g95)
    c: Coincident(g95,g96)
    c: Coincident(g96,g97)
    c: Coincident(g97,g98)
    c: Coincident(g98,g99)
    c: Coincident(g99,g100)
    c: Coincident(g100,g101)
    c: Coincident(g101,g102)
    c: Coincident(g102,g103)
    c: Coincident(g103,g104)
    c: Coincident(g104,g105)
    c: Coincident(g105,g106)
    c: Coincident(g106,g107)
    c: Coincident(g107,g108)
    c: Coincident(g108,g109)
    c: Coincident(g109,g110)
    c: Coincident(g110,g111)
    c: Coincident(g111,g112)
    c: Coincident(g112,g113)
    c: Coincident(g113,g114)
    c: Coincident(g114,g115)
    c: Coincident(g115,g116)
    c: Coincident(g116,g117)
    c: Coincident(g117,g118)
    c: Coincident(g118,g119)
    c: Coincident(g119,g120)
    c: Coincident(g120,g121)
    c: Coincident(g121,g122)
    c: Coincident(g122,g123)
    c: Coincident(g123,g124)
    c: Coincident(g124,g125)
    c: Coincident(g125,g126)
    c: Coincident(g126,g127)
    c: Coincident(g127,g128)
    c: Coincident(g128,g129)
    c: Coincident(g129,g130)
    c: Coincident(g130,g131)
    c: Coincident(g131,g132)
    c: Coincident(g132,g133)
    c: Coincident(g133,g134)
    c: Coincident(g134,g135)
    c: Coincident(g135,g136)
    c: Coincident(g136,g137)
    c: Coincident(g137,g138)
    c: Coincident(g138,g139)
    c: Coincident(g139,g140)
    c: Coincident(g140,g141)
    c: Coincident(g141,g142)
    c: Coincident(g142,g143)
    c: Coincident(g143,g144)
    c: Coincident(g144,g145)
    c: Coincident(g145,g146)
    c: Coincident(g146,g147)
    c: Coincident(g147,g148)
    c: Coincident(g148,g149)
    c: Coincident(g149,g150)
    c: Coincident(g150,g151)
    c: Coincident(g151,g152)
    c: Coincident(g152,g153)
    c: Coincident(g153,g154)
    c: Coincident(g154,g155)
    c: Coincident(g155,g156)
    c: Coincident(g156,g157)
    c: Coincident(g157,g158)
    c: Coincident(g158,g159)
    c: Coincident(g159,g62)
    c: Coincident(g160,g161)
    c: Coincident(g161,g162)
    c: Coincident(g162,g163)
    c: Coincident(g163,g160)
    c: Coincident(g164,g165)
    c: Coincident(g165,g166)
    c: Coincident(g166,g167)
    c: Coincident(g167,g168)
    c: Coincident(g168,g169)
    c: Coincident(g169,g170)
    c: Coincident(g170,g171)
    c: Coincident(g171,g172)
    c: Coincident(g172,g173)
    c: Coincident(g173,g174)
    c: Coincident(g174,g175)
    c: Coincident(g175,g176)
    c: Coincident(g176,g177)
    c: Coincident(g177,g178)
    c: Coincident(g178,g179)
    c: Coincident(g179,g180)
    c: Coincident(g180,g181)
    c: Coincident(g181,g182)
    c: Coincident(g182,g183)
    c: Coincident(g183,g184)
    c: Coincident(g184,g185)
    c: Coincident(g185,g186)
    c: Coincident(g186,g187)
    c: Coincident(g187,g188)
    c: Coincident(g188,g164)
    c: Coincident(g189,g190)
    c: Coincident(g190,g191)
    c: Coincident(g191,g192)
    c: Coincident(g192,g193)
    c: Coincident(g193,g189)
    c: Coincident(g194,g195)
    c: Coincident(g195,g196)
    c: Coincident(g196,g197)
    c: Coincident(g197,g198)
    c: Coincident(g198,g199)
    c: Coincident(g199,g200)
    c: Coincident(g200,g201)
    c: Coincident(g201,g202)
    c: Coincident(g202,g203)
    c: Coincident(g203,g204)
    c: Coincident(g204,g205)
    c: Coincident(g205,g206)
    c: Coincident(g206,g207)
    c: Coincident(g207,g208)
    c: Coincident(g208,g209)
    c: Coincident(g209,g210)
    c: Coincident(g210,g211)
    c: Coincident(g211,g212)
    c: Coincident(g212,g194)
    c: Coincident(g213,g214)
    c: Coincident(g214,g215)
    c: Coincident(g215,g216)
    c: Coincident(g216,g217)
    c: Coincident(g217,g218)
    c: Coincident(g218,g213)
    c: Coincident(g219,g220)
    c: Coincident(g220,g221)
    c: Coincident(g221,g222)
    c: Coincident(g222,g223)
    c: Coincident(g223,g219)
    c: Coincident(g224,g225)
    c: Coincident(g225,g226)
    c: Coincident(g226,g224)
    c: Coincident(g227,g228)
    c: Coincident(g228,g229)
    c: Coincident(g229,g230)
    c: Coincident(g230,g231)
    c: Coincident(g231,g232)
    c: Coincident(g232,g227)
    c: Coincident(g158,g62)
    c: Coincident(g60,g29)
FEATURE [Sketcher::SketchObject] Sketch043  label="Sage-Sketch"
  ArcFitTolerance = 1e-06
  FullyConstrained = false
  MakeInternals = false
  Placement = pos=(-8.90838,16.2612,0) rot=(0,0,1;0rad)
  expr: .Placement.Base.x = -(.Shape.BoundBox.XLength / 2)
  expr: .Placement.Base.y = .Shape.BoundBox.YLength / 2
  sketch-geometry (299):
    g0: BSplineCurve PolesCount=4 KnotsCount=2 Degree=3 IsPeriodic=0
    g1: BSplineCurve PolesCount=4 KnotsCount=2 Degree=3 IsPeriodic=0
    g2: BSplineCurve PolesCount=4 KnotsCount=2 Degree=3 IsPeriodic=0
    g3: BSplineCurve PolesCount=4 KnotsCount=2 Degree=3 IsPeriodic=0
    g4: BSplineCurve PolesCount=4 KnotsCount=2 Degree=3 IsPeriodic=0
    g5: BSplineCurve PolesCount=4 KnotsCount=2 Degree=3 IsPeriodic=0
    g6: BSplineCurve PolesCount=4 KnotsCount=2 Degree=3 IsPeriodic=0
    g7: BSplineCurve PolesCount=4 KnotsCount=2 Degree=3 IsPeriodic=0
    g8: BSplineCurve PolesCount=2 KnotsCount=2 Degree=1 IsPeriodic=0
    g9: BSplineCurve PolesCount=2 KnotsCount=2 Degree=1 IsPeriodic=0
    g10: BSplineCurve PolesCount=4 KnotsCount=2 Degree=3 IsPeriodic=0
    g11: BSplineCurve PolesCount=4 KnotsCount=2 Degree=3 IsPeriodic=0
    g12: BSplineCurve PolesCount=4 KnotsCount=2 Degree=3 IsPeriodic=0
    g13: BSplineCurve PolesCount=4 KnotsCount=2 Degree=3 IsPeriodic=0
    g14: BSplineCurve PolesCount=4 KnotsCount=2 Degree=3 IsPeriodic=0
    g15: BSplineCurve PolesCount=4 KnotsCount=2 Degree=3 IsPeriodic=0
    g16: BSplineCurve PolesCount=4 KnotsCount=2 Degree=3 IsPeriodic=0
    g17: BSplineCurve PolesCount=4 KnotsCount=2 Degree=3 IsPeriodic=0
    g18: BSplineCurve PolesCount=4 KnotsCount=2 Degree=3 IsPeriodic=0
    g19: BSplineCurve PolesCount=4 KnotsCount=2 Degree=3 IsPeriodic=0
    g20: BSplineCurve PolesCount=4 KnotsCount=2 Degree=3 IsPeriodic=0
    g21: BSplineCurve PolesCount=4 KnotsCount=2 Degree=3 IsPeriodic=0
    g22: BSplineCurve PolesCount=4 KnotsCount=2 Degree=3 IsPeriodic=0
    g23: BSplineCurve PolesCount=4 KnotsCount=2 Degree=3 IsPeriodic=0
    g24: BSplineCurve PolesCount=4 KnotsCount=2 Degree=3 IsPeriodic=0
    g25: BSplineCurve PolesCount=4 KnotsCount=2 Degree=3 IsPeriodic=0
    g26: BSplineCurve PolesCount=4 KnotsCount=2 Degree=3 IsPeriodic=0
    g27: BSplineCurve PolesCount=4 KnotsCount=2 Degree=3 IsPeriodic=0
    g28: BSplineCurve PolesCount=4 KnotsCount=2 Degree=3 IsPeriodic=0
    g29: BSplineCurve PolesCount=2 KnotsCount=2 Degree=1 IsPeriodic=0
    g30: BSplineCurve PolesCount=2 KnotsCount=2 Degree=1 IsPeriodic=0
    g31: BSplineCurve PolesCount=4 KnotsCount=2 Degree=3 IsPeriodic=0
    g32: BSplineCurve PolesCount=4 KnotsCount=2 Degree=3 IsPeriodic=0
    g33: BSplineCurve PolesCount=2 KnotsCount=2 Degree=1 IsPeriodic=0
    g34: BSplineCurve PolesCount=2 KnotsCount=2 Degree=1 IsPeriodic=0
    g35: BSplineCurve PolesCount=4 KnotsCount=2 Degree=3 IsPeriodic=0
    g36: BSplineCurve PolesCount=4 KnotsCount=2 Degree=3 IsPeriodic=0
    g37: BSplineCurve PolesCount=4 KnotsCount=2 Degree=3 IsPeriodic=0
    g38: BSplineCurve PolesCount=4 KnotsCount=2 Degree=3 IsPeriodic=0
    g39: BSplineCurve PolesCount=4 KnotsCount=2 Degree=3 IsPeriodic=0
    g40: BSplineCurve PolesCount=4 KnotsCount=2 Degree=3 IsPeriodic=0
    g41: BSplineCurve PolesCount=4 KnotsCount=2 Degree=3 IsPeriodic=0
    g42: BSplineCurve PolesCount=4 KnotsCount=2 Degree=3 IsPeriodic=0
    g43: BSplineCurve PolesCount=4 KnotsCount=2 Degree=3 IsPeriodic=0
    g44: BSplineCurve PolesCount=4 KnotsCount=2 Degree=3 IsPeriodic=0
    g45: BSplineCurve PolesCount=4 KnotsCount=2 Degree=3 IsPeriodic=0
    g46: BSplineCurve PolesCount=4 KnotsCount=2 Degree=3 IsPeriodic=0
    g47: BSplineCurve PolesCount=2 KnotsCount=2 Degree=1 IsPeriodic=0
    g48: BSplineCurve PolesCount=2 KnotsCount=2 Degree=1 IsPeriodic=0
    g49: BSplineCurve PolesCount=4 KnotsCount=2 Degree=3 IsPeriodic=0
    g50: BSplineCurve PolesCount=4 KnotsCount=2 Degree=3 IsPeriodic=0
    g51: BSplineCurve PolesCount=4 KnotsCount=2 Degree=3 IsPeriodic=0
    g52: BSplineCurve PolesCount=2 KnotsCount=2 Degree=1 IsPeriodic=0
    g53: BSplineCurve PolesCount=2 KnotsCount=2 Degree=1 IsPeriodic=0
    g54: BSplineCurve PolesCount=4 KnotsCount=2 Degree=3 IsPeriodic=0
    g55: BSplineCurve PolesCount=4 KnotsCount=2 Degree=3 IsPeriodic=0
    g56: BSplineCurve PolesCount=4 KnotsCount=2 Degree=3 IsPeriodic=0
    g57: BSplineCurve PolesCount=4 KnotsCount=2 Degree=3 IsPeriodic=0
    g58: BSplineCurve PolesCount=4 KnotsCount=2 Degree=3 IsPeriodic=0
    g59: BSplineCurve PolesCount=4 KnotsCount=2 Degree=3 IsPeriodic=0
    g60: BSplineCurve PolesCount=4 KnotsCount=2 Degree=3 IsPeriodic=0
    g61: BSplineCurve PolesCount=4 KnotsCount=2 Degree=3 IsPeriodic=0
    g62: BSplineCurve PolesCount=4 KnotsCount=2 Degree=3 IsPeriodic=0
    g63: BSplineCurve PolesCount=4 KnotsCount=2 Degree=3 IsPeriodic=0
    g64: BSplineCurve PolesCount=4 KnotsCount=2 Degree=3 IsPeriodic=0
    g65: BSplineCurve PolesCount=4 KnotsCount=2 Degree=3 IsPeriodic=0
    g66: BSplineCurve PolesCount=4 KnotsCount=2 Degree=3 IsPeriodic=0
    g67: BSplineCurve PolesCount=2 KnotsCount=2 Degree=1 IsPeriodic=0
    g68: BSplineCurve PolesCount=2 KnotsCount=2 Degree=1 IsPeriodic=0
    g69: BSplineCurve PolesCount=4 KnotsCount=2 Degree=3 IsPeriodic=0
    g70: BSplineCurve PolesCount=4 KnotsCount=2 Degree=3 IsPeriodic=0
    g71: BSplineCurve PolesCount=4 KnotsCount=2 Degree=3 IsPeriodic=0
    g72: BSplineCurve PolesCount=4 KnotsCount=2 Degree=3 IsPeriodic=0
    g73: BSplineCurve PolesCount=4 KnotsCount=2 Degree=3 IsPeriodic=0
    g74: BSplineCurve PolesCount=4 KnotsCount=2 Degree=3 IsPeriodic=0
    g75: BSplineCurve PolesCount=4 KnotsCount=2 Degree=3 IsPeriodic=0
    g76: BSplineCurve PolesCount=4 KnotsCount=2 Degree=3 IsPeriodic=0
    g77: BSplineCurve PolesCount=4 KnotsCount=2 Degree=3 IsPeriodic=0
    g78: BSplineCurve PolesCount=4 KnotsCount=2 Degree=3 IsPeriodic=0
    g79: BSplineCurve PolesCount=4 KnotsCount=2 Degree=3 IsPeriodic=0
    g80: BSplineCurve PolesCount=2 KnotsCount=2 Degree=1 IsPeriodic=0
    g81: BSplineCurve PolesCount=2 KnotsCount=2 Degree=1 IsPeriodic=0
    g82: BSplineCurve PolesCount=4 KnotsCount=2 Degree=3 IsPeriodic=0
    g83: BSplineCurve PolesCount=4 KnotsCount=2 Degree=3 IsPeriodic=0
    g84: BSplineCurve PolesCount=4 KnotsCount=2 Degree=3 IsPeriodic=0
    g85: BSplineCurve PolesCount=2 KnotsCount=2 Degree=1 IsPeriodic=0
    g86: BSplineCurve PolesCount=2 KnotsCount=2 Degree=1 IsPeriodic=0
    g87: BSplineCurve PolesCount=4 KnotsCount=2 Degree=3 IsPeriodic=0
    g88: BSplineCurve PolesCount=4 KnotsCount=2 Degree=3 IsPeriodic=0
    g89: BSplineCurve PolesCount=4 KnotsCount=2 Degree=3 IsPeriodic=0
    g90: BSplineCurve PolesCount=4 KnotsCount=2 Degree=3 IsPeriodic=0
    g91: BSplineCurve PolesCount=4 KnotsCount=2 Degree=3 IsPeriodic=0
    g92: BSplineCurve PolesCount=4 KnotsCount=2 Degree=3 IsPeriodic=0
    g93: BSplineCurve PolesCount=4 KnotsCount=2 Degree=3 IsPeriodic=0
    g94: BSplineCurve PolesCount=4 KnotsCount=2 Degree=3 IsPeriodic=0
    g95: BSplineCurve PolesCount=4 KnotsCount=2 Degree=3 IsPeriodic=0
    g96: BSplineCurve PolesCount=4 KnotsCount=2 Degree=3 IsPeriodic=0
    g97: BSplineCurve PolesCount=4 KnotsCount=2 Degree=3 IsPeriodic=0
    g98: BSplineCurve PolesCount=4 KnotsCount=2 Degree=3 IsPeriodic=0
    g99: BSplineCurve PolesCount=4 KnotsCount=2 Degree=3 IsPeriodic=0
    g100: BSplineCurve PolesCount=4 KnotsCount=2 Degree=3 IsPeriodic=0
    g101: BSplineCurve PolesCount=4 KnotsCount=2 Degree=3 IsPeriodic=0
    g102: BSplineCurve PolesCount=4 KnotsCount=2 Degree=3 IsPeriodic=0
    g103: BSplineCurve PolesCount=4 KnotsCount=2 Degree=3 IsPeriodic=0
    g104: BSplineCurve PolesCount=4 KnotsCount=2 Degree=3 IsPeriodic=0
    g105: BSplineCurve PolesCount=4 KnotsCount=2 Degree=3 IsPeriodic=0
    g106: BSplineCurve PolesCount=4 KnotsCount=2 Degree=3 IsPeriodic=0
    g107: BSplineCurve PolesCount=4 KnotsCount=2 Degree=3 IsPeriodic=0
    g108: BSplineCurve PolesCount=4 KnotsCount=2 Degree=3 IsPeriodic=0
    g109: BSplineCurve PolesCount=4 KnotsCount=2 Degree=3 IsPeriodic=0
    g110: BSplineCurve PolesCount=4 KnotsCount=2 Degree=3 IsPeriodic=0
    g111: BSplineCurve PolesCount=4 KnotsCount=2 Degree=3 IsPeriodic=0
    g112: BSplineCurve PolesCount=4 KnotsCount=2 Degree=3 IsPeriodic=0
    g113: BSplineCurve PolesCount=4 KnotsCount=2 Degree=3 IsPeriodic=0
    g114: BSplineCurve PolesCount=4 KnotsCount=2 Degree=3 IsPeriodic=0
    g115: BSplineCurve PolesCount=4 KnotsCount=2 Degree=3 IsPeriodic=0
    g116: BSplineCurve PolesCount=4 KnotsCount=2 Degree=3 IsPeriodic=0
    g117: BSplineCurve PolesCount=4 KnotsCount=2 Degree=3 IsPeriodic=0
    g118: BSplineCurve PolesCount=4 KnotsCount=2 Degree=3 IsPeriodic=0
    g119: BSplineCurve PolesCount=4 KnotsCount=2 Degree=3 IsPeriodic=0
    g120: BSplineCurve PolesCount=4 KnotsCount=2 Degree=3 IsPeriodic=0
    g121: BSplineCurve PolesCount=4 KnotsCount=2 Degree=3 IsPeriodic=0
    g122: BSplineCurve PolesCount=4 KnotsCount=2 Degree=3 IsPeriodic=0
    g123: BSplineCurve PolesCount=4 KnotsCount=2 Degree=3 IsPeriodic=0
    g124: BSplineCurve PolesCount=4 KnotsCount=2 Degree=3 IsPeriodic=0
    g125: BSplineCurve PolesCount=4 KnotsCount=2 Degree=3 IsPeriodic=0
    g126: BSplineCurve PolesCount=4 KnotsCount=2 Degree=3 IsPeriodic=0
    g127: BSplineCurve PolesCount=4 KnotsCount=2 Degree=3 IsPeriodic=0
    g128: BSplineCurve PolesCount=4 KnotsCount=2 Degree=3 IsPeriodic=0
    g129: BSplineCurve PolesCount=4 KnotsCount=2 Degree=3 IsPeriodic=0
    g130: BSplineCurve PolesCount=4 KnotsCount=2 Degree=3 IsPeriodic=0
    g131: BSplineCurve PolesCount=4 KnotsCount=2 Degree=3 IsPeriodic=0
    g132: BSplineCurve PolesCount=4 KnotsCount=2 Degree=3 IsPeriodic=0
    g133: BSplineCurve PolesCount=4 KnotsCount=2 Degree=3 IsPeriodic=0
    g134: BSplineCurve PolesCount=4 KnotsCount=2 Degree=3 IsPeriodic=0
    g135: BSplineCurve PolesCount=4 KnotsCount=2 Degree=3 IsPeriodic=0
    g136: BSplineCurve PolesCount=4 KnotsCount=2 Degree=3 IsPeriodic=0
    g137: BSplineCurve PolesCount=4 KnotsCount=2 Degree=3 IsPeriodic=0
    g138: BSplineCurve PolesCount=4 KnotsCount=2 Degree=3 IsPeriodic=0
    g139: BSplineCurve PolesCount=4 KnotsCount=2 Degree=3 IsPeriodic=0
    g140: BSplineCurve PolesCount=4 KnotsCount=2 Degree=3 IsPeriodic=0
    g141: BSplineCurve PolesCount=4 KnotsCount=2 Degree=3 IsPeriodic=0
    g142: BSplineCurve PolesCount=4 KnotsCount=2 Degree=3 IsPeriodic=0
    g143: BSplineCurve PolesCount=4 KnotsCount=2 Degree=3 IsPeriodic=0
    g144: BSplineCurve PolesCount=4 KnotsCount=2 Degree=3 IsPeriodic=0
    g145: BSplineCurve PolesCount=4 KnotsCount=2 Degree=3 IsPeriodic=0
    g146: BSplineCurve PolesCount=4 KnotsCount=2 Degree=3 IsPeriodic=0
    g147: BSplineCurve PolesCount=4 KnotsCount=2 Degree=3 IsPeriodic=0
    g148: BSplineCurve PolesCount=4 KnotsCount=2 Degree=3 IsPeriodic=0
    g149: BSplineCurve PolesCount=4 KnotsCount=2 Degree=3 IsPeriodic=0
    g150: BSplineCurve PolesCount=4 KnotsCount=2 Degree=3 IsPeriodic=0
    g151: BSplineCurve PolesCount=4 KnotsCount=2 Degree=3 IsPeriodic=0
    g152: BSplineCurve PolesCount=4 KnotsCount=2 Degree=3 IsPeriodic=0
    g153: BSplineCurve PolesCount=4 KnotsCount=2 Degree=3 IsPeriodic=0
    g154: BSplineCurve PolesCount=4 KnotsCount=2 Degree=3 IsPeriodic=0
    g155: BSplineCurve PolesCount=4 KnotsCount=2 Degree=3 IsPeriodic=0
    g156: BSplineCurve PolesCount=4 KnotsCount=2 Degree=3 IsPeriodic=0
    g157: BSplineCurve PolesCount=4 KnotsCount=2 Degree=3 IsPeriodic=0
    g158: BSplineCurve PolesCount=4 KnotsCount=2 Degree=3 IsPeriodic=0
    g159: BSplineCurve PolesCount=4 KnotsCount=2 Degree=3 IsPeriodic=0
    g160: BSplineCurve PolesCount=4 KnotsCount=2 Degree=3 IsPeriodic=0
    g161: BSplineCurve PolesCount=4 KnotsCount=2 Degree=3 IsPeriodic=0
    g162: BSplineCurve PolesCount=2 KnotsCount=2 Degree=1 IsPeriodic=0
    g163: BSplineCurve PolesCount=2 KnotsCount=2 Degree=1 IsPeriodic=0
    g164: BSplineCurve PolesCount=4 KnotsCount=2 Degree=3 IsPeriodic=0
    g165: BSplineCurve PolesCount=4 KnotsCount=2 Degree=3 IsPeriodic=0
    g166: BSplineCurve PolesCount=4 KnotsCount=2 Degree=3 IsPeriodic=0
    g167: BSplineCurve PolesCount=4 KnotsCount=2 Degree=3 IsPeriodic=0
    g168: BSplineCurve PolesCount=4 KnotsCount=2 Degree=3 IsPeriodic=0
    g169: BSplineCurve PolesCount=4 KnotsCount=2 Degree=3 IsPeriodic=0
    g170: BSplineCurve PolesCount=4 KnotsCount=2 Degree=3 IsPeriodic=0
    g171: BSplineCurve PolesCount=4 KnotsCount=2 Degree=3 IsPeriodic=0
    g172: BSplineCurve PolesCount=4 KnotsCount=2 Degree=3 IsPeriodic=0
    g173: BSplineCurve PolesCount=2 KnotsCount=2 Degree=1 IsPeriodic=0
    g174: BSplineCurve PolesCount=2 KnotsCount=2 Degree=1 IsPeriodic=0
    g175: BSplineCurve PolesCount=4 KnotsCount=2 Degree=3 IsPeriodic=0
    g176: BSplineCurve PolesCount=4 KnotsCount=2 Degree=3 IsPeriodic=0
    g177: BSplineCurve PolesCount=4 KnotsCount=2 Degree=3 IsPeriodic=0
    g178: BSplineCurve PolesCount=4 KnotsCount=2 Degree=3 IsPeriodic=0
    g179: BSplineCurve PolesCount=4 KnotsCount=2 Degree=3 IsPeriodic=0
    g180: BSplineCurve PolesCount=4 KnotsCount=2 Degree=3 IsPeriodic=0
    g181: BSplineCurve PolesCount=4 KnotsCount=2 Degree=3 IsPeriodic=0
    g182: BSplineCurve PolesCount=4 KnotsCount=2 Degree=3 IsPeriodic=0
    g183: BSplineCurve PolesCount=4 KnotsCount=2 Degree=3 IsPeriodic=0
    g184: BSplineCurve PolesCount=4 KnotsCount=2 Degree=3 IsPeriodic=0
    g185: BSplineCurve PolesCount=4 KnotsCount=2 Degree=3 IsPeriodic=0
    g186: BSplineCurve PolesCount=4 KnotsCount=2 Degree=3 IsPeriodic=0
    g187: BSplineCurve PolesCount=4 KnotsCount=2 Degree=3 IsPeriodic=0
    g188: BSplineCurve PolesCount=4 KnotsCount=2 Degree=3 IsPeriodic=0
    g189: BSplineCurve PolesCount=2 KnotsCount=2 Degree=1 IsPeriodic=0
    g190: BSplineCurve PolesCount=2 KnotsCount=2 Degree=1 IsPeriodic=0
    g191: BSplineCurve PolesCount=4 KnotsCount=2 Degree=3 IsPeriodic=0
    g192: BSplineCurve PolesCount=4 KnotsCount=2 Degree=3 IsPeriodic=0
    g193: BSplineCurve PolesCount=4 KnotsCount=2 Degree=3 IsPeriodic=0
    g194: BSplineCurve PolesCount=4 KnotsCount=2 Degree=3 IsPeriodic=0
    g195: BSplineCurve PolesCount=4 KnotsCount=2 Degree=3 IsPeriodic=0
    g196: BSplineCurve PolesCount=4 KnotsCount=2 Degree=3 IsPeriodic=0
    g197: BSplineCurve PolesCount=4 KnotsCount=2 Degree=3 IsPeriodic=0
    g198: BSplineCurve PolesCount=4 KnotsCount=2 Degree=3 IsPeriodic=0
    g199: BSplineCurve PolesCount=4 KnotsCount=2 Degree=3 IsPeriodic=0
    g200: BSplineCurve PolesCount=4 KnotsCount=2 Degree=3 IsPeriodic=0
    g201: BSplineCurve PolesCount=4 KnotsCount=2 Degree=3 IsPeriodic=0
    g202: BSplineCurve PolesCount=4 KnotsCount=2 Degree=3 IsPeriodic=0
    g203: BSplineCurve PolesCount=4 KnotsCount=2 Degree=3 IsPeriodic=0
    g204: BSplineCurve PolesCount=2 KnotsCount=2 Degree=1 IsPeriodic=0
    g205: BSplineCurve PolesCount=2 KnotsCount=2 Degree=1 IsPeriodic=0
    g206: BSplineCurve PolesCount=4 KnotsCount=2 Degree=3 IsPeriodic=0
    g207: BSplineCurve PolesCount=4 KnotsCount=2 Degree=3 IsPeriodic=0
    g208: BSplineCurve PolesCount=4 KnotsCount=2 Degree=3 IsPeriodic=0
    g209: BSplineCurve PolesCount=4 KnotsCount=2 Degree=3 IsPeriodic=0
    g210: BSplineCurve PolesCount=4 KnotsCount=2 Degree=3 IsPeriodic=0
    g211: BSplineCurve PolesCount=4 KnotsCount=2 Degree=3 IsPeriodic=0
    g212: BSplineCurve PolesCount=4 KnotsCount=2 Degree=3 IsPeriodic=0
    g213: BSplineCurve PolesCount=4 KnotsCount=2 Degree=3 IsPeriodic=0
    g214: BSplineCurve PolesCount=4 KnotsCount=2 Degree=3 IsPeriodic=0
    g215: BSplineCurve PolesCount=4 KnotsCount=2 Degree=3 IsPeriodic=0
    g216: BSplineCurve PolesCount=4 KnotsCount=2 Degree=3 IsPeriodic=0
    g217: BSplineCurve PolesCount=4 KnotsCount=2 Degree=3 IsPeriodic=0
    g218: BSplineCurve PolesCount=4 KnotsCount=2 Degree=3 IsPeriodic=0
    g219: BSplineCurve PolesCount=4 KnotsCount=2 Degree=3 IsPeriodic=0
    g220: BSplineCurve PolesCount=4 KnotsCount=2 Degree=3 IsPeriodic=0
    g221: BSplineCurve PolesCount=4 KnotsCount=2 Degree=3 IsPeriodic=0
    g222: BSplineCurve PolesCount=4 KnotsCount=2 Degree=3 IsPeriodic=0
    g223: BSplineCurve PolesCount=4 KnotsCount=2 Degree=3 IsPeriodic=0
    g224: BSplineCurve PolesCount=4 KnotsCount=2 Degree=3 IsPeriodic=0
    g225: BSplineCurve PolesCount=4 KnotsCount=2 Degree=3 IsPeriodic=0
    g226: BSplineCurve PolesCount=4 KnotsCount=2 Degree=3 IsPeriodic=0
    g227: BSplineCurve PolesCount=4 KnotsCount=2 Degree=3 IsPeriodic=0
    g228: BSplineCurve PolesCount=4 KnotsCount=2 Degree=3 IsPeriodic=0
    g229: BSplineCurve PolesCount=4 KnotsCount=2 Degree=3 IsPeriodic=0
    g230: BSplineCurve PolesCount=4 KnotsCount=2 Degree=3 IsPeriodic=0
    g231: BSplineCurve PolesCount=2 KnotsCount=2 Degree=1 IsPeriodic=0
    g232: BSplineCurve PolesCount=2 KnotsCount=2 Degree=1 IsPeriodic=0
    g233: BSplineCurve PolesCount=4 KnotsCount=2 Degree=3 IsPeriodic=0
    g234: BSplineCurve PolesCount=4 KnotsCount=2 Degree=3 IsPeriodic=0
    g235: BSplineCurve PolesCount=2 KnotsCount=2 Degree=1 IsPeriodic=0
    g236: BSplineCurve PolesCount=2 KnotsCount=2 Degree=1 IsPeriodic=0
    g237: BSplineCurve PolesCount=4 KnotsCount=2 Degree=3 IsPeriodic=0
    g238: BSplineCurve PolesCount=4 KnotsCount=2 Degree=3 IsPeriodic=0
    g239: BSplineCurve PolesCount=4 KnotsCount=2 Degree=3 IsPeriodic=0
    g240: BSplineCurve PolesCount=4 KnotsCount=2 Degree=3 IsPeriodic=0
    g241: BSplineCurve PolesCount=4 KnotsCount=2 Degree=3 IsPeriodic=0
    g242: BSplineCurve PolesCount=4 KnotsCount=2 Degree=3 IsPeriodic=0
    g243: BSplineCurve PolesCount=4 KnotsCount=2 Degree=3 IsPeriodic=0
    g244: BSplineCurve PolesCount=4 KnotsCount=2 Degree=3 IsPeriodic=0
    g245: BSplineCurve PolesCount=4 KnotsCount=2 Degree=3 IsPeriodic=0
    g246: BSplineCurve PolesCount=4 KnotsCount=2 Degree=3 IsPeriodic=0
    g247: BSplineCurve PolesCount=4 KnotsCount=2 Degree=3 IsPeriodic=0
    g248: BSplineCurve PolesCount=4 KnotsCount=2 Degree=3 IsPeriodic=0
    g249: BSplineCurve PolesCount=4 KnotsCount=2 Degree=3 IsPeriodic=0
    g250: BSplineCurve PolesCount=4 KnotsCount=2 Degree=3 IsPeriodic=0
    g251: BSplineCurve PolesCount=4 KnotsCount=2 Degree=3 IsPeriodic=0
    g252: BSplineCurve PolesCount=4 KnotsCount=2 Degree=3 IsPeriodic=0
    g253: BSplineCurve PolesCount=4 KnotsCount=2 Degree=3 IsPeriodic=0
    g254: BSplineCurve PolesCount=4 KnotsCount=2 Degree=3 IsPeriodic=0
    g255: BSplineCurve PolesCount=4 KnotsCount=2 Degree=3 IsPeriodic=0
    g256: BSplineCurve PolesCount=4 KnotsCount=2 Degree=3 IsPeriodic=0
    g257: BSplineCurve PolesCount=4 KnotsCount=2 Degree=3 IsPeriodic=0
    g258: BSplineCurve PolesCount=4 KnotsCount=2 Degree=3 IsPeriodic=0
    g259: BSplineCurve PolesCount=2 KnotsCount=2 Degree=1 IsPeriodic=0
    g260: BSplineCurve PolesCount=2 KnotsCount=2 Degree=1 IsPeriodic=0
    g261: BSplineCurve PolesCount=4 KnotsCount=2 Degree=3 IsPeriodic=0
    g262: BSplineCurve PolesCount=4 KnotsCount=2 Degree=3 IsPeriodic=0
    g263: BSplineCurve PolesCount=4 KnotsCount=2 Degree=3 IsPeriodic=0
    g264: BSplineCurve PolesCount=2 KnotsCount=2 Degree=1 IsPeriodic=0
    g265: BSplineCurve PolesCount=2 KnotsCount=2 Degree=1 IsPeriodic=0
    g266: BSplineCurve PolesCount=2 KnotsCount=2 Degree=1 IsPeriodic=0
    g267: BSplineCurve PolesCount=2 KnotsCount=2 Degree=1 IsPeriodic=0
    g268: BSplineCurve PolesCount=4 KnotsCount=2 Degree=3 IsPeriodic=0
    g269: BSplineCurve PolesCount=4 KnotsCount=2 Degree=3 IsPeriodic=0
    g270: BSplineCurve PolesCount=4 KnotsCount=2 Degree=3 IsPeriodic=0
    g271: BSplineCurve PolesCount=2 KnotsCount=2 Degree=1 IsPeriodic=0
    g272: BSplineCurve PolesCount=2 KnotsCount=2 Degree=1 IsPeriodic=0
    g273: BSplineCurve PolesCount=4 KnotsCount=2 Degree=3 IsPeriodic=0
    g274: BSplineCurve PolesCount=4 KnotsCount=2 Degree=3 IsPeriodic=0
    g275: BSplineCurve PolesCount=4 KnotsCount=2 Degree=3 IsPeriodic=0
    g276: BSplineCurve PolesCount=4 KnotsCount=2 Degree=3 IsPeriodic=0
    g277: BSplineCurve PolesCount=4 KnotsCount=2 Degree=3 IsPeriodic=0
    g278: BSplineCurve PolesCount=4 KnotsCount=2 Degree=3 IsPeriodic=0
    g279: BSplineCurve PolesCount=4 KnotsCount=2 Degree=3 IsPeriodic=0
    g280: BSplineCurve PolesCount=4 KnotsCount=2 Degree=3 IsPeriodic=0
    g281: BSplineCurve PolesCount=4 KnotsCount=2 Degree=3 IsPeriodic=0
    g282: BSplineCurve PolesCount=4 KnotsCount=2 Degree=3 IsPeriodic=0
    g283: BSplineCurve PolesCount=2 KnotsCount=2 Degree=1 IsPeriodic=0
    g284: BSplineCurve PolesCount=2 KnotsCount=2 Degree=1 IsPeriodic=0
    g285: BSplineCurve PolesCount=4 KnotsCount=2 Degree=3 IsPeriodic=0
    g286: BSplineCurve PolesCount=4 KnotsCount=2 Degree=3 IsPeriodic=0
    g287: BSplineCurve PolesCount=4 KnotsCount=2 Degree=3 IsPeriodic=0
    g288: BSplineCurve PolesCount=4 KnotsCount=2 Degree=3 IsPeriodic=0
    g289: BSplineCurve PolesCount=4 KnotsCount=2 Degree=3 IsPeriodic=0
    g290: BSplineCurve PolesCount=4 KnotsCount=2 Degree=3 IsPeriodic=0
    g291: BSplineCurve PolesCount=4 KnotsCount=2 Degree=3 IsPeriodic=0
    g292: BSplineCurve PolesCount=4 KnotsCount=2 Degree=3 IsPeriodic=0
    g293: BSplineCurve PolesCount=4 KnotsCount=2 Degree=3 IsPeriodic=0
    g294: BSplineCurve PolesCount=4 KnotsCount=2 Degree=3 IsPeriodic=0
    g295: BSplineCurve PolesCount=4 KnotsCount=2 Degree=3 IsPeriodic=0
    g296: BSplineCurve PolesCount=2 KnotsCount=2 Degree=1 IsPeriodic=0
    g297: BSplineCurve PolesCount=2 KnotsCount=2 Degree=1 IsPeriodic=0
    g298: BSplineCurve PolesCount=4 KnotsCount=2 Degree=3 IsPeriodic=0
  constraints (299):
    c: Coincident(g0,g1)
    c: Coincident(g1,g2)
    c: Coincident(g2,g3)
    c: Coincident(g3,g4)
    c: Coincident(g4,g5)
    c: Coincident(g5,g6)
    c: Coincident(g6,g7)
    c: Coincident(g7,g8)
    c: Coincident(g8,g9)
    c: Coincident(g9,g10)
    c: Coincident(g10,g11)
    c: Coincident(g11,g12)
    c: Coincident(g12,g13)
    c: Coincident(g13,g14)
    c: Coincident(g14,g15)
    c: Coincident(g15,g16)
    c: Coincident(g16,g17)
    c: Coincident(g18,g19)
    c: Coincident(g19,g20)
    c: Coincident(g20,g21)
    c: Coincident(g21,g22)
    c: Coincident(g22,g23)
    c: Coincident(g23,g24)
    c: Coincident(g24,g25)
    c: Coincident(g25,g26)
    c: Coincident(g26,g27)
    c: Coincident(g27,g28)
    c: Coincident(g28,g29)
    c: Coincident(g29,g30)
    c: Coincident(g30,g31)
    c: Coincident(g31,g32)
    c: Coincident(g32,g33)
    c: Coincident(g33,g34)
    c: Coincident(g34,g35)
    c: Coincident(g35,g36)
    c: Coincident(g36,g37)
    c: Coincident(g37,g38)
    c: Coincident(g38,g39)
    c: Coincident(g39,g40)
    c: Coincident(g40,g41)
    c: Coincident(g41,g42)
    c: Coincident(g42,g43)
    c: Coincident(g43,g44)
    c: Coincident(g44,g45)
    c: Coincident(g45,g46)
    c: Coincident(g46,g47)
    c: Coincident(g47,g48)
    c: Coincident(g48,g49)
    c: Coincident(g49,g50)
    c: Coincident(g50,g51)
    c: Coincident(g51,g52)
    c: Coincident(g52,g53)
    c: Coincident(g53,g54)
    c: Coincident(g54,g55)
    c: Coincident(g55,g56)
    c: Coincident(g56,g57)
    c: Coincident(g57,g58)
    c: Coincident(g58,g59)
    c: Coincident(g59,g60)
    c: Coincident(g60,g61)
    c: Coincident(g61,g62)
    c: Coincident(g62,g63)
    c: Coincident(g63,g64)
    c: Coincident(g64,g65)
    c: Coincident(g65,g66)
    c: Coincident(g66,g67)
    c: Coincident(g67,g68)
    c: Coincident(g68,g69)
    c: Coincident(g69,g70)
    c: Coincident(g70,g71)
    c: Coincident(g71,g72)
    c: Coincident(g72,g73)
    c: Coincident(g73,g74)
    c: Coincident(g74,g75)
    c: Coincident(g75,g76)
    c: Coincident(g76,g77)
    c: Coincident(g77,g78)
    c: Coincident(g78,g79)
    c: Coincident(g79,g80)
    c: Coincident(g80,g81)
    c: Coincident(g81,g82)
    c: Coincident(g82,g83)
    c: Coincident(g83,g84)
    c: Coincident(g84,g85)
    c: Coincident(g85,g86)
    c: Coincident(g86,g18)
    c: Coincident(g87,g88)
    c: Coincident(g88,g89)
    c: Coincident(g89,g90)
    c: Coincident(g90,g91)
    c: Coincident(g91,g92)
    c: Coincident(g92,g93)
    c: Coincident(g93,g94)
    c: Coincident(g94,g95)
    c: Coincident(g95,g96)
    c: Coincident(g96,g97)
    c: Coincident(g97,g98)
    c: Coincident(g98,g99)
    c: Coincident(g99,g100)
    c: Coincident(g100,g101)
    c: Coincident(g101,g102)
    c: Coincident(g102,g103)
    c: Coincident(g103,g87)
    c: Coincident(g104,g105)
    c: Coincident(g105,g106)
    c: Coincident(g107,g108)
    c: Coincident(g108,g109)
    c: Coincident(g109,g110)
    c: Coincident(g110,g111)
    c: Coincident(g111,g112)
    c: Coincident(g112,g113)
    c: Coincident(g113,g114)
    c: Coincident(g114,g115)
    c: Coincident(g115,g116)
    c: Coincident(g116,g107)
    c: Coincident(g117,g118)
    c: Coincident(g118,g119)
    c: Coincident(g120,g121)
    c: Coincident(g121,g122)
    c: Coincident(g122,g123)
    c: Coincident(g123,g124)
    c: Coincident(g124,g125)
    c: Coincident(g125,g126)
    c: Coincident(g126,g127)
    c: Coincident(g127,g128)
    c: Coincident(g128,g129)
    c: Coincident(g129,g130)
    c: Coincident(g130,g131)
    c: Coincident(g131,g132)
    c: Coincident(g132,g133)
    c: Coincident(g133,g134)
    c: Coincident(g134,g135)
    c: Coincident(g135,g136)
    c: Coincident(g136,g137)
    c: Coincident(g137,g138)
    c: Coincident(g139,g140)
    c: Coincident(g140,g141)
    c: Coincident(g141,g142)
    c: Coincident(g142,g143)
    c: Coincident(g143,g144)
    c: Coincident(g144,g145)
    c: Coincident(g145,g146)
    c: Coincident(g147,g148)
    c: Coincident(g148,g149)
    c: Coincident(g151,g152)
    c: Coincident(g152,g153)
    c: Coincident(g153,g150)
    c: Coincident(g154,g155)
    c: Coincident(g155,g156)
    c: Coincident(g156,g157)
    c: Coincident(g157,g158)
    c: Coincident(g158,g159)
    c: Coincident(g159,g160)
    c: Coincident(g160,g161)
    c: Coincident(g161,g162)
    c: Coincident(g162,g163)
    c: Coincident(g163,g164)
    c: Coincident(g164,g165)
    c: Coincident(g165,g166)
    c: Coincident(g166,g167)
    c: Coincident(g167,g168)
    c: Coincident(g168,g169)
    c: Coincident(g169,g170)
    c: Coincident(g170,g171)
    c: Coincident(g171,g172)
    c: Coincident(g172,g173)
    c: Coincident(g173,g174)
    c: Coincident(g174,g175)
    c: Coincident(g175,g176)
    c: Coincident(g176,g177)
    c: Coincident(g177,g178)
    c: Coincident(g178,g179)
    c: Coincident(g179,g180)
    c: Coincident(g180,g181)
    c: Coincident(g181,g182)
    c: Coincident(g182,g183)
    c: Coincident(g183,g184)
    c: Coincident(g184,g185)
    c: Coincident(g185,g186)
    c: Coincident(g186,g187)
    c: Coincident(g187,g188)
    c: Coincident(g188,g189)
    c: Coincident(g189,g190)
    c: Coincident(g190,g191)
    c: Coincident(g191,g192)
    c: Coincident(g192,g193)
    c: Coincident(g193,g194)
    c: Coincident(g194,g195)
    c: Coincident(g195,g196)
    c: Coincident(g196,g197)
    c: Coincident(g197,g198)
    c: Coincident(g198,g199)
    c: Coincident(g199,g200)
    c: Coincident(g200,g201)
    c: Coincident(g201,g202)
    c: Coincident(g202,g203)
    c: Coincident(g203,g204)
    c: Coincident(g204,g205)
    c: Coincident(g205,g206)
    c: Coincident(g206,g207)
    c: Coincident(g207,g208)
    c: Coincident(g208,g209)
    c: Coincident(g210,g211)
    c: Coincident(g211,g212)
    c: Coincident(g212,g213)
    c: Coincident(g213,g214)
    c: Coincident(g214,g215)
    c: Coincident(g215,g216)
    c: Coincident(g216,g217)
    c: Coincident(g217,g218)
    c: Coincident(g218,g219)
    c: Coincident(g219,g220)
    c: Coincident(g220,g221)
    c: Coincident(g221,g222)
    c: Coincident(g222,g223)
    c: Coincident(g223,g224)
    c: Coincident(g224,g225)
    c: Coincident(g225,g226)
    c: Coincident(g226,g227)
    c: Coincident(g227,g228)
    c: Coincident(g228,g229)
    c: Coincident(g229,g230)
    c: Coincident(g230,g231)
    c: Coincident(g231,g232)
    c: Coincident(g232,g233)
    c: Coincident(g233,g234)
    c: Coincident(g234,g235)
    c: Coincident(g235,g236)
    c: Coincident(g236,g237)
    c: Coincident(g237,g238)
    c: Coincident(g238,g239)
    c: Coincident(g239,g240)
    c: Coincident(g240,g241)
    c: Coincident(g241,g242)
    c: Coincident(g242,g243)
    c: Coincident(g243,g244)
    c: Coincident(g244,g245)
    c: Coincident(g245,g246)
    c: Coincident(g246,g247)
    c: Coincident(g247,g248)
    c: Coincident(g248,g249)
    c: Coincident(g249,g250)
    c: Coincident(g250,g251)
    c: Coincident(g251,g252)
    c: Coincident(g252,g253)
    c: Coincident(g253,g254)
    c: Coincident(g254,g255)
    c: Coincident(g255,g256)
    c: Coincident(g256,g257)
    c: Coincident(g257,g258)
    c: Coincident(g258,g259)
    c: Coincident(g259,g260)
    c: Coincident(g260,g261)
    c: Coincident(g261,g262)
    c: Coincident(g263,g264)
    c: Coincident(g264,g265)
    c: Coincident(g265,g266)
    c: Coincident(g266,g267)
    c: Coincident(g267,g268)
    c: Coincident(g268,g269)
    c: Coincident(g269,g270)
    c: Coincident(g270,g271)
    c: Coincident(g271,g272)
    c: Coincident(g272,g273)
    c: Coincident(g273,g274)
    c: Coincident(g274,g275)
    c: Coincident(g275,g276)
    c: Coincident(g276,g277)
    c: Coincident(g277,g278)
    c: Coincident(g278,g279)
    c: Coincident(g279,g280)
    c: Coincident(g280,g281)
    c: Coincident(g281,g282)
    c: Coincident(g282,g283)
    c: Coincident(g283,g284)
    c: Coincident(g284,g285)
    c: Coincident(g285,g286)
    c: Coincident(g286,g287)
    c: Coincident(g287,g288)
    c: Coincident(g289,g290)
    c: Coincident(g290,g291)
    c: Coincident(g291,g292)
    c: Coincident(g292,g289)
    c: Coincident(g293,g294)
    c: Coincident(g294,g295)
    c: Coincident(g295,g296)
    c: Coincident(g296,g297)
    c: Coincident(g297,g298)
    c: Coincident(g298,g293)
    c: Coincident(g150,g151)
    c: Coincident(g17,g0)
    c: Coincident(g139,g146)
    c: Coincident(g120,g138)
    c: Coincident(g263,g288)
    c: Coincident(g210,g262)
    c: Coincident(g147,g149)
    c: Coincident(g117,g119)
    c: Coincident(g104,g106)
    c: Coincident(g154,g209)
FEATURE [Sketcher::SketchObject] Sketch044  label="Savant-Sketch"
  ArcFitTolerance = 1e-06
  FullyConstrained = false
  MakeInternals = false
  Placement = pos=(-13.1411,14.3766,0) rot=(0,0,1;0rad)
  expr: .Placement.Base.x = -(.Shape.BoundBox.XLength / 2)
  expr: .Placement.Base.y = .Shape.BoundBox.YLength / 2
  sketch-geometry (317):
    g0: BSplineCurve PolesCount=4 KnotsCount=2 Degree=3 IsPeriodic=0
    g1: BSplineCurve PolesCount=2 KnotsCount=2 Degree=1 IsPeriodic=0
    g2: BSplineCurve PolesCount=2 KnotsCount=2 Degree=1 IsPeriodic=0
    g3: BSplineCurve PolesCount=4 KnotsCount=2 Degree=3 IsPeriodic=0
    g4: BSplineCurve PolesCount=4 KnotsCount=2 Degree=3 IsPeriodic=0
    g5: BSplineCurve PolesCount=4 KnotsCount=2 Degree=3 IsPeriodic=0
    g6: BSplineCurve PolesCount=4 KnotsCount=2 Degree=3 IsPeriodic=0
    g7: BSplineCurve PolesCount=4 KnotsCount=2 Degree=3 IsPeriodic=0
    g8: BSplineCurve PolesCount=4 KnotsCount=2 Degree=3 IsPeriodic=0
    g9: BSplineCurve PolesCount=4 KnotsCount=2 Degree=3 IsPeriodic=0
    g10: BSplineCurve PolesCount=4 KnotsCount=2 Degree=3 IsPeriodic=0
    g11: BSplineCurve PolesCount=4 KnotsCount=2 Degree=3 IsPeriodic=0
    g12: BSplineCurve PolesCount=4 KnotsCount=2 Degree=3 IsPeriodic=0
    g13: BSplineCurve PolesCount=4 KnotsCount=2 Degree=3 IsPeriodic=0
    g14: BSplineCurve PolesCount=4 KnotsCount=2 Degree=3 IsPeriodic=0
    g15: BSplineCurve PolesCount=4 KnotsCount=2 Degree=3 IsPeriodic=0
    g16: BSplineCurve PolesCount=2 KnotsCount=2 Degree=1 IsPeriodic=0
    g17: BSplineCurve PolesCount=2 KnotsCount=2 Degree=1 IsPeriodic=0
    g18: BSplineCurve PolesCount=4 KnotsCount=2 Degree=3 IsPeriodic=0
    g19: BSplineCurve PolesCount=4 KnotsCount=2 Degree=3 IsPeriodic=0
    g20: BSplineCurve PolesCount=4 KnotsCount=2 Degree=3 IsPeriodic=0
    g21: BSplineCurve PolesCount=2 KnotsCount=2 Degree=1 IsPeriodic=0
    g22: BSplineCurve PolesCount=2 KnotsCount=2 Degree=1 IsPeriodic=0
    g23: BSplineCurve PolesCount=4 KnotsCount=2 Degree=3 IsPeriodic=0
    g24: BSplineCurve PolesCount=4 KnotsCount=2 Degree=3 IsPeriodic=0
    g25: BSplineCurve PolesCount=4 KnotsCount=2 Degree=3 IsPeriodic=0
    g26: BSplineCurve PolesCount=2 KnotsCount=2 Degree=1 IsPeriodic=0
    g27: BSplineCurve PolesCount=2 KnotsCount=2 Degree=1 IsPeriodic=0
    g28: BSplineCurve PolesCount=4 KnotsCount=2 Degree=3 IsPeriodic=0
    g29: BSplineCurve PolesCount=4 KnotsCount=2 Degree=3 IsPeriodic=0
    g30: BSplineCurve PolesCount=4 KnotsCount=2 Degree=3 IsPeriodic=0
    g31: BSplineCurve PolesCount=4 KnotsCount=2 Degree=3 IsPeriodic=0
    g32: BSplineCurve PolesCount=4 KnotsCount=2 Degree=3 IsPeriodic=0
    g33: BSplineCurve PolesCount=2 KnotsCount=2 Degree=1 IsPeriodic=0
    g34: BSplineCurve PolesCount=4 KnotsCount=2 Degree=3 IsPeriodic=0
    g35: BSplineCurve PolesCount=4 KnotsCount=2 Degree=3 IsPeriodic=0
    g36: BSplineCurve PolesCount=2 KnotsCount=2 Degree=1 IsPeriodic=0
    g37: BSplineCurve PolesCount=4 KnotsCount=2 Degree=3 IsPeriodic=0
    g38: BSplineCurve PolesCount=4 KnotsCount=2 Degree=3 IsPeriodic=0
    g39: BSplineCurve PolesCount=4 KnotsCount=2 Degree=3 IsPeriodic=0
    g40: BSplineCurve PolesCount=4 KnotsCount=2 Degree=3 IsPeriodic=0
    g41: BSplineCurve PolesCount=4 KnotsCount=2 Degree=3 IsPeriodic=0
    g42: BSplineCurve PolesCount=4 KnotsCount=2 Degree=3 IsPeriodic=0
    g43: BSplineCurve PolesCount=4 KnotsCount=2 Degree=3 IsPeriodic=0
    g44: BSplineCurve PolesCount=4 KnotsCount=2 Degree=3 IsPeriodic=0
    g45: BSplineCurve PolesCount=4 KnotsCount=2 Degree=3 IsPeriodic=0
    g46: BSplineCurve PolesCount=4 KnotsCount=2 Degree=3 IsPeriodic=0
    g47: BSplineCurve PolesCount=4 KnotsCount=2 Degree=3 IsPeriodic=0
    g48: BSplineCurve PolesCount=4 KnotsCount=2 Degree=3 IsPeriodic=0
    g49: BSplineCurve PolesCount=4 KnotsCount=2 Degree=3 IsPeriodic=0
    g50: BSplineCurve PolesCount=4 KnotsCount=2 Degree=3 IsPeriodic=0
    g51: BSplineCurve PolesCount=4 KnotsCount=2 Degree=3 IsPeriodic=0
    g52: BSplineCurve PolesCount=4 KnotsCount=2 Degree=3 IsPeriodic=0
    g53: BSplineCurve PolesCount=4 KnotsCount=2 Degree=3 IsPeriodic=0
    g54: BSplineCurve PolesCount=4 KnotsCount=2 Degree=3 IsPeriodic=0
    g55: BSplineCurve PolesCount=4 KnotsCount=2 Degree=3 IsPeriodic=0
    g56: BSplineCurve PolesCount=4 KnotsCount=2 Degree=3 IsPeriodic=0
    g57: BSplineCurve PolesCount=4 KnotsCount=2 Degree=3 IsPeriodic=0
    g58: BSplineCurve PolesCount=4 KnotsCount=2 Degree=3 IsPeriodic=0
    g59: BSplineCurve PolesCount=4 KnotsCount=2 Degree=3 IsPeriodic=0
    g60: BSplineCurve PolesCount=4 KnotsCount=2 Degree=3 IsPeriodic=0
    g61: BSplineCurve PolesCount=4 KnotsCount=2 Degree=3 IsPeriodic=0
    g62: BSplineCurve PolesCount=4 KnotsCount=2 Degree=3 IsPeriodic=0
    g63: BSplineCurve PolesCount=4 KnotsCount=2 Degree=3 IsPeriodic=0
    g64: BSplineCurve PolesCount=4 KnotsCount=2 Degree=3 IsPeriodic=0
    g65: BSplineCurve PolesCount=4 KnotsCount=2 Degree=3 IsPeriodic=0
    g66: BSplineCurve PolesCount=4 KnotsCount=2 Degree=3 IsPeriodic=0
    g67: BSplineCurve PolesCount=4 KnotsCount=2 Degree=3 IsPeriodic=0
    g68: BSplineCurve PolesCount=4 KnotsCount=2 Degree=3 IsPeriodic=0
    g69: BSplineCurve PolesCount=4 KnotsCount=2 Degree=3 IsPeriodic=0
    g70: BSplineCurve PolesCount=4 KnotsCount=2 Degree=3 IsPeriodic=0
    g71: BSplineCurve PolesCount=4 KnotsCount=2 Degree=3 IsPeriodic=0
    g72: BSplineCurve PolesCount=4 KnotsCount=2 Degree=3 IsPeriodic=0
    g73: BSplineCurve PolesCount=4 KnotsCount=2 Degree=3 IsPeriodic=0
    g74: BSplineCurve PolesCount=4 KnotsCount=2 Degree=3 IsPeriodic=0
    g75: BSplineCurve PolesCount=4 KnotsCount=2 Degree=3 IsPeriodic=0
    g76: BSplineCurve PolesCount=4 KnotsCount=2 Degree=3 IsPeriodic=0
    g77: BSplineCurve PolesCount=4 KnotsCount=2 Degree=3 IsPeriodic=0
    g78: BSplineCurve PolesCount=4 KnotsCount=2 Degree=3 IsPeriodic=0
    g79: BSplineCurve PolesCount=4 KnotsCount=2 Degree=3 IsPeriodic=0
    g80: BSplineCurve PolesCount=4 KnotsCount=2 Degree=3 IsPeriodic=0
    g81: BSplineCurve PolesCount=4 KnotsCount=2 Degree=3 IsPeriodic=0
    g82: BSplineCurve PolesCount=4 KnotsCount=2 Degree=3 IsPeriodic=0
    g83: BSplineCurve PolesCount=4 KnotsCount=2 Degree=3 IsPeriodic=0
    g84: BSplineCurve PolesCount=4 KnotsCount=2 Degree=3 IsPeriodic=0
    g85: BSplineCurve PolesCount=4 KnotsCount=2 Degree=3 IsPeriodic=0
    g86: BSplineCurve PolesCount=4 KnotsCount=2 Degree=3 IsPeriodic=0
    g87: BSplineCurve PolesCount=4 KnotsCount=2 Degree=3 IsPeriodic=0
    g88: BSplineCurve PolesCount=4 KnotsCount=2 Degree=3 IsPeriodic=0
    g89: BSplineCurve PolesCount=4 KnotsCount=2 Degree=3 IsPeriodic=0
    g90: BSplineCurve PolesCount=4 KnotsCount=2 Degree=3 IsPeriodic=0
    g91: BSplineCurve PolesCount=4 KnotsCount=2 Degree=3 IsPeriodic=0
    g92: BSplineCurve PolesCount=4 KnotsCount=2 Degree=3 IsPeriodic=0
    g93: BSplineCurve PolesCount=4 KnotsCount=2 Degree=3 IsPeriodic=0
    g94: BSplineCurve PolesCount=4 KnotsCount=2 Degree=3 IsPeriodic=0
    g95: BSplineCurve PolesCount=4 KnotsCount=2 Degree=3 IsPeriodic=0
    g96: BSplineCurve PolesCount=4 KnotsCount=2 Degree=3 IsPeriodic=0
    g97: BSplineCurve PolesCount=4 KnotsCount=2 Degree=3 IsPeriodic=0
    g98: BSplineCurve PolesCount=4 KnotsCount=2 Degree=3 IsPeriodic=0
    g99: BSplineCurve PolesCount=4 KnotsCount=2 Degree=3 IsPeriodic=0
    g100: BSplineCurve PolesCount=4 KnotsCount=2 Degree=3 IsPeriodic=0
    g101: BSplineCurve PolesCount=4 KnotsCount=2 Degree=3 IsPeriodic=0
    g102: BSplineCurve PolesCount=4 KnotsCount=2 Degree=3 IsPeriodic=0
    g103: BSplineCurve PolesCount=4 KnotsCount=2 Degree=3 IsPeriodic=0
    g104: BSplineCurve PolesCount=4 KnotsCount=2 Degree=3 IsPeriodic=0
    g105: BSplineCurve PolesCount=4 KnotsCount=2 Degree=3 IsPeriodic=0
    g106: BSplineCurve PolesCount=4 KnotsCount=2 Degree=3 IsPeriodic=0
    g107: BSplineCurve PolesCount=4 KnotsCount=2 Degree=3 IsPeriodic=0
    g108: BSplineCurve PolesCount=4 KnotsCount=2 Degree=3 IsPeriodic=0
    g109: BSplineCurve PolesCount=4 KnotsCount=2 Degree=3 IsPeriodic=0
    g110: BSplineCurve PolesCount=4 KnotsCount=2 Degree=3 IsPeriodic=0
    g111: BSplineCurve PolesCount=4 KnotsCount=2 Degree=3 IsPeriodic=0
    g112: BSplineCurve PolesCount=2 KnotsCount=2 Degree=1 IsPeriodic=0
    g113: BSplineCurve PolesCount=2 KnotsCount=2 Degree=1 IsPeriodic=0
    g114: BSplineCurve PolesCount=4 KnotsCount=2 Degree=3 IsPeriodic=0
    g115: BSplineCurve PolesCount=4 KnotsCount=2 Degree=3 IsPeriodic=0
    g116: BSplineCurve PolesCount=4 KnotsCount=2 Degree=3 IsPeriodic=0
    g117: BSplineCurve PolesCount=4 KnotsCount=2 Degree=3 IsPeriodic=0
    g118: BSplineCurve PolesCount=4 KnotsCount=2 Degree=3 IsPeriodic=0
    g119: BSplineCurve PolesCount=2 KnotsCount=2 Degree=1 IsPeriodic=0
    g120: BSplineCurve PolesCount=4 KnotsCount=2 Degree=3 IsPeriodic=0
    g121: BSplineCurve PolesCount=4 KnotsCount=2 Degree=3 IsPeriodic=0
    g122: BSplineCurve PolesCount=4 KnotsCount=2 Degree=3 IsPeriodic=0
    g123: BSplineCurve PolesCount=4 KnotsCount=2 Degree=3 IsPeriodic=0
    g124: BSplineCurve PolesCount=4 KnotsCount=2 Degree=3 IsPeriodic=0
    g125: BSplineCurve PolesCount=4 KnotsCount=2 Degree=3 IsPeriodic=0
    g126: BSplineCurve PolesCount=2 KnotsCount=2 Degree=1 IsPeriodic=0
    g127: BSplineCurve PolesCount=4 KnotsCount=2 Degree=3 IsPeriodic=0
    g128: BSplineCurve PolesCount=4 KnotsCount=2 Degree=3 IsPeriodic=0
    g129: BSplineCurve PolesCount=4 KnotsCount=2 Degree=3 IsPeriodic=0
    g130: BSplineCurve PolesCount=2 KnotsCount=2 Degree=1 IsPeriodic=0
    g131: BSplineCurve PolesCount=2 KnotsCount=2 Degree=1 IsPeriodic=0
    g132: BSplineCurve PolesCount=4 KnotsCount=2 Degree=3 IsPeriodic=0
    g133: BSplineCurve PolesCount=4 KnotsCount=2 Degree=3 IsPeriodic=0
    g134: BSplineCurve PolesCount=4 KnotsCount=2 Degree=3 IsPeriodic=0
    g135: BSplineCurve PolesCount=4 KnotsCount=2 Degree=3 IsPeriodic=0
    g136: BSplineCurve PolesCount=4 KnotsCount=2 Degree=3 IsPeriodic=0
    g137: BSplineCurve PolesCount=4 KnotsCount=2 Degree=3 IsPeriodic=0
    g138: BSplineCurve PolesCount=4 KnotsCount=2 Degree=3 IsPeriodic=0
    g139: BSplineCurve PolesCount=4 KnotsCount=2 Degree=3 IsPeriodic=0
    g140: BSplineCurve PolesCount=4 KnotsCount=2 Degree=3 IsPeriodic=0
    g141: BSplineCurve PolesCount=4 KnotsCount=2 Degree=3 IsPeriodic=0
    g142: BSplineCurve PolesCount=4 KnotsCount=2 Degree=3 IsPeriodic=0
    g143: BSplineCurve PolesCount=4 KnotsCount=2 Degree=3 IsPeriodic=0
    g144: BSplineCurve PolesCount=4 KnotsCount=2 Degree=3 IsPeriodic=0
    g145: BSplineCurve PolesCount=4 KnotsCount=2 Degree=3 IsPeriodic=0
    g146: BSplineCurve PolesCount=2 KnotsCount=2 Degree=1 IsPeriodic=0
    g147: BSplineCurve PolesCount=2 KnotsCount=2 Degree=1 IsPeriodic=0
    g148: BSplineCurve PolesCount=4 KnotsCount=2 Degree=3 IsPeriodic=0
    g149: BSplineCurve PolesCount=4 KnotsCount=2 Degree=3 IsPeriodic=0
    g150: BSplineCurve PolesCount=4 KnotsCount=2 Degree=3 IsPeriodic=0
    g151: BSplineCurve PolesCount=4 KnotsCount=2 Degree=3 IsPeriodic=0
    g152: BSplineCurve PolesCount=4 KnotsCount=2 Degree=3 IsPeriodic=0
    g153: BSplineCurve PolesCount=2 KnotsCount=2 Degree=1 IsPeriodic=0
    g154: BSplineCurve PolesCount=2 KnotsCount=2 Degree=1 IsPeriodic=0
    g155: BSplineCurve PolesCount=4 KnotsCount=2 Degree=3 IsPeriodic=0
    g156: BSplineCurve PolesCount=4 KnotsCount=2 Degree=3 IsPeriodic=0
    g157: BSplineCurve PolesCount=4 KnotsCount=2 Degree=3 IsPeriodic=0
    g158: BSplineCurve PolesCount=2 KnotsCount=2 Degree=1 IsPeriodic=0
    g159: BSplineCurve PolesCount=2 KnotsCount=2 Degree=1 IsPeriodic=0
    g160: BSplineCurve PolesCount=4 KnotsCount=2 Degree=3 IsPeriodic=0
    g161: BSplineCurve PolesCount=4 KnotsCount=2 Degree=3 IsPeriodic=0
    g162: BSplineCurve PolesCount=4 KnotsCount=2 Degree=3 IsPeriodic=0
    g163: BSplineCurve PolesCount=4 KnotsCount=2 Degree=3 IsPeriodic=0
    g164: BSplineCurve PolesCount=4 KnotsCount=2 Degree=3 IsPeriodic=0
    g165: BSplineCurve PolesCount=4 KnotsCount=2 Degree=3 IsPeriodic=0
    g166: BSplineCurve PolesCount=4 KnotsCount=2 Degree=3 IsPeriodic=0
    g167: BSplineCurve PolesCount=4 KnotsCount=2 Degree=3 IsPeriodic=0
    g168: BSplineCurve PolesCount=2 KnotsCount=2 Degree=1 IsPeriodic=0
    g169: BSplineCurve PolesCount=2 KnotsCount=2 Degree=1 IsPeriodic=0
    g170: BSplineCurve PolesCount=4 KnotsCount=2 Degree=3 IsPeriodic=0
    g171: BSplineCurve PolesCount=4 KnotsCount=2 Degree=3 IsPeriodic=0
    g172: BSplineCurve PolesCount=4 KnotsCount=2 Degree=3 IsPeriodic=0
    g173: BSplineCurve PolesCount=4 KnotsCount=2 Degree=3 IsPeriodic=0
    g174: BSplineCurve PolesCount=4 KnotsCount=2 Degree=3 IsPeriodic=0
    g175: BSplineCurve PolesCount=4 KnotsCount=2 Degree=3 IsPeriodic=0
    g176: BSplineCurve PolesCount=4 KnotsCount=2 Degree=3 IsPeriodic=0
    g177: BSplineCurve PolesCount=4 KnotsCount=2 Degree=3 IsPeriodic=0
    g178: BSplineCurve PolesCount=4 KnotsCount=2 Degree=3 IsPeriodic=0
    g179: BSplineCurve PolesCount=4 KnotsCount=2 Degree=3 IsPeriodic=0
    g180: BSplineCurve PolesCount=4 KnotsCount=2 Degree=3 IsPeriodic=0
    g181: BSplineCurve PolesCount=4 KnotsCount=2 Degree=3 IsPeriodic=0
    g182: BSplineCurve PolesCount=4 KnotsCount=2 Degree=3 IsPeriodic=0
    g183: BSplineCurve PolesCount=4 KnotsCount=2 Degree=3 IsPeriodic=0
    g184: BSplineCurve PolesCount=4 KnotsCount=2 Degree=3 IsPeriodic=0
    g185: BSplineCurve PolesCount=4 KnotsCount=2 Degree=3 IsPeriodic=0
    g186: BSplineCurve PolesCount=4 KnotsCount=2 Degree=3 IsPeriodic=0
    g187: BSplineCurve PolesCount=4 KnotsCount=2 Degree=3 IsPeriodic=0
    g188: BSplineCurve PolesCount=4 KnotsCount=2 Degree=3 IsPeriodic=0
    g189: BSplineCurve PolesCount=4 KnotsCount=2 Degree=3 IsPeriodic=0
    g190: BSplineCurve PolesCount=4 KnotsCount=2 Degree=3 IsPeriodic=0
    g191: BSplineCurve PolesCount=4 KnotsCount=2 Degree=3 IsPeriodic=0
    g192: BSplineCurve PolesCount=4 KnotsCount=2 Degree=3 IsPeriodic=0
    g193: BSplineCurve PolesCount=4 KnotsCount=2 Degree=3 IsPeriodic=0
    g194: BSplineCurve PolesCount=4 KnotsCount=2 Degree=3 IsPeriodic=0
    g195: BSplineCurve PolesCount=4 KnotsCount=2 Degree=3 IsPeriodic=0
    g196: BSplineCurve PolesCount=4 KnotsCount=2 Degree=3 IsPeriodic=0
    g197: BSplineCurve PolesCount=4 KnotsCount=2 Degree=3 IsPeriodic=0
    g198: BSplineCurve PolesCount=4 KnotsCount=2 Degree=3 IsPeriodic=0
    g199: BSplineCurve PolesCount=4 KnotsCount=2 Degree=3 IsPeriodic=0
    g200: BSplineCurve PolesCount=4 KnotsCount=2 Degree=3 IsPeriodic=0
    g201: BSplineCurve PolesCount=4 KnotsCount=2 Degree=3 IsPeriodic=0
    g202: BSplineCurve PolesCount=4 KnotsCount=2 Degree=3 IsPeriodic=0
    g203: BSplineCurve PolesCount=4 KnotsCount=2 Degree=3 IsPeriodic=0
    g204: BSplineCurve PolesCount=4 KnotsCount=2 Degree=3 IsPeriodic=0
    g205: BSplineCurve PolesCount=4 KnotsCount=2 Degree=3 IsPeriodic=0
    g206: BSplineCurve PolesCount=4 KnotsCount=2 Degree=3 IsPeriodic=0
    g207: BSplineCurve PolesCount=4 KnotsCount=2 Degree=3 IsPeriodic=0
    g208: BSplineCurve PolesCount=4 KnotsCount=2 Degree=3 IsPeriodic=0
    g209: BSplineCurve PolesCount=4 KnotsCount=2 Degree=3 IsPeriodic=0
    g210: BSplineCurve PolesCount=4 KnotsCount=2 Degree=3 IsPeriodic=0
    g211: BSplineCurve PolesCount=2 KnotsCount=2 Degree=1 IsPeriodic=0
    g212: BSplineCurve PolesCount=2 KnotsCount=2 Degree=1 IsPeriodic=0
    g213: BSplineCurve PolesCount=4 KnotsCount=2 Degree=3 IsPeriodic=0
    g214: BSplineCurve PolesCount=4 KnotsCount=2 Degree=3 IsPeriodic=0
    g215: BSplineCurve PolesCount=4 KnotsCount=2 Degree=3 IsPeriodic=0
    g216: BSplineCurve PolesCount=4 KnotsCount=2 Degree=3 IsPeriodic=0
    g217: BSplineCurve PolesCount=4 KnotsCount=2 Degree=3 IsPeriodic=0
    g218: BSplineCurve PolesCount=4 KnotsCount=2 Degree=3 IsPeriodic=0
    g219: BSplineCurve PolesCount=4 KnotsCount=2 Degree=3 IsPeriodic=0
    g220: BSplineCurve PolesCount=2 KnotsCount=2 Degree=1 IsPeriodic=0
    g221: BSplineCurve PolesCount=2 KnotsCount=2 Degree=1 IsPeriodic=0
    g222: BSplineCurve PolesCount=4 KnotsCount=2 Degree=3 IsPeriodic=0
    g223: BSplineCurve PolesCount=4 KnotsCount=2 Degree=3 IsPeriodic=0
    g224: BSplineCurve PolesCount=4 KnotsCount=2 Degree=3 IsPeriodic=0
    g225: BSplineCurve PolesCount=4 KnotsCount=2 Degree=3 IsPeriodic=0
    g226: BSplineCurve PolesCount=4 KnotsCount=2 Degree=3 IsPeriodic=0
    g227: BSplineCurve PolesCount=4 KnotsCount=2 Degree=3 IsPeriodic=0
    g228: BSplineCurve PolesCount=2 KnotsCount=2 Degree=1 IsPeriodic=0
    g229: BSplineCurve PolesCount=2 KnotsCount=2 Degree=1 IsPeriodic=0
    g230: BSplineCurve PolesCount=4 KnotsCount=2 Degree=3 IsPeriodic=0
    g231: BSplineCurve PolesCount=4 KnotsCount=2 Degree=3 IsPeriodic=0
    g232: BSplineCurve PolesCount=4 KnotsCount=2 Degree=3 IsPeriodic=0
    g233: BSplineCurve PolesCount=4 KnotsCount=2 Degree=3 IsPeriodic=0
    g234: BSplineCurve PolesCount=4 KnotsCount=2 Degree=3 IsPeriodic=0
    g235: BSplineCurve PolesCount=4 KnotsCount=2 Degree=3 IsPeriodic=0
    g236: BSplineCurve PolesCount=4 KnotsCount=2 Degree=3 IsPeriodic=0
    g237: BSplineCurve PolesCount=4 KnotsCount=2 Degree=3 IsPeriodic=0
    g238: BSplineCurve PolesCount=4 KnotsCount=2 Degree=3 IsPeriodic=0
    g239: BSplineCurve PolesCount=4 KnotsCount=2 Degree=3 IsPeriodic=0
    g240: BSplineCurve PolesCount=2 KnotsCount=2 Degree=1 IsPeriodic=0
    g241: BSplineCurve PolesCount=2 KnotsCount=2 Degree=1 IsPeriodic=0
    g242: BSplineCurve PolesCount=4 KnotsCount=2 Degree=3 IsPeriodic=0
    g243: BSplineCurve PolesCount=4 KnotsCount=2 Degree=3 IsPeriodic=0
    g244: BSplineCurve PolesCount=4 KnotsCount=2 Degree=3 IsPeriodic=0
    g245: BSplineCurve PolesCount=4 KnotsCount=2 Degree=3 IsPeriodic=0
    g246: BSplineCurve PolesCount=4 KnotsCount=2 Degree=3 IsPeriodic=0
    g247: BSplineCurve PolesCount=4 KnotsCount=2 Degree=3 IsPeriodic=0
    g248: BSplineCurve PolesCount=4 KnotsCount=2 Degree=3 IsPeriodic=0
    g249: BSplineCurve PolesCount=4 KnotsCount=2 Degree=3 IsPeriodic=0
    g250: BSplineCurve PolesCount=4 KnotsCount=2 Degree=3 IsPeriodic=0
    g251: BSplineCurve PolesCount=4 KnotsCount=2 Degree=3 IsPeriodic=0
    g252: BSplineCurve PolesCount=2 KnotsCount=2 Degree=1 IsPeriodic=0
    g253: BSplineCurve PolesCount=2 KnotsCount=2 Degree=1 IsPeriodic=0
    g254: BSplineCurve PolesCount=4 KnotsCount=2 Degree=3 IsPeriodic=0
    g255: BSplineCurve PolesCount=4 KnotsCount=2 Degree=3 IsPeriodic=0
    g256: BSplineCurve PolesCount=4 KnotsCount=2 Degree=3 IsPeriodic=0
    g257: BSplineCurve PolesCount=4 KnotsCount=2 Degree=3 IsPeriodic=0
    g258: BSplineCurve PolesCount=4 KnotsCount=2 Degree=3 IsPeriodic=0
    g259: BSplineCurve PolesCount=4 KnotsCount=2 Degree=3 IsPeriodic=0
    g260: BSplineCurve PolesCount=4 KnotsCount=2 Degree=3 IsPeriodic=0
    g261: BSplineCurve PolesCount=4 KnotsCount=2 Degree=3 IsPeriodic=0
    g262: BSplineCurve PolesCount=4 KnotsCount=2 Degree=3 IsPeriodic=0
    g263: BSplineCurve PolesCount=2 KnotsCount=2 Degree=1 IsPeriodic=0
    g264: BSplineCurve PolesCount=2 KnotsCount=2 Degree=1 IsPeriodic=0
    g265: BSplineCurve PolesCount=4 KnotsCount=2 Degree=3 IsPeriodic=0
    g266: BSplineCurve PolesCount=4 KnotsCount=2 Degree=3 IsPeriodic=0
    g267: BSplineCurve PolesCount=4 KnotsCount=2 Degree=3 IsPeriodic=0
    g268: BSplineCurve PolesCount=4 KnotsCount=2 Degree=3 IsPeriodic=0
    g269: BSplineCurve PolesCount=4 KnotsCount=2 Degree=3 IsPeriodic=0
    g270: BSplineCurve PolesCount=4 KnotsCount=2 Degree=3 IsPeriodic=0
    g271: BSplineCurve PolesCount=4 KnotsCount=2 Degree=3 IsPeriodic=0
    g272: BSplineCurve PolesCount=4 KnotsCount=2 Degree=3 IsPeriodic=0
    g273: BSplineCurve PolesCount=4 KnotsCount=2 Degree=3 IsPeriodic=0
    g274: BSplineCurve PolesCount=4 KnotsCount=2 Degree=3 IsPeriodic=0
    g275: BSplineCurve PolesCount=4 KnotsCount=2 Degree=3 IsPeriodic=0
    g276: BSplineCurve PolesCount=4 KnotsCount=2 Degree=3 IsPeriodic=0
    g277: BSplineCurve PolesCount=4 KnotsCount=2 Degree=3 IsPeriodic=0
    g278: BSplineCurve PolesCount=4 KnotsCount=2 Degree=3 IsPeriodic=0
    g279: BSplineCurve PolesCount=4 KnotsCount=2 Degree=3 IsPeriodic=0
    g280: BSplineCurve PolesCount=4 KnotsCount=2 Degree=3 IsPeriodic=0
    g281: BSplineCurve PolesCount=4 KnotsCount=2 Degree=3 IsPeriodic=0
    g282: BSplineCurve PolesCount=4 KnotsCount=2 Degree=3 IsPeriodic=0
    g283: BSplineCurve PolesCount=4 KnotsCount=2 Degree=3 IsPeriodic=0
    g284: BSplineCurve PolesCount=4 KnotsCount=2 Degree=3 IsPeriodic=0
    g285: BSplineCurve PolesCount=4 KnotsCount=2 Degree=3 IsPeriodic=0
    g286: BSplineCurve PolesCount=4 KnotsCount=2 Degree=3 IsPeriodic=0
    g287: BSplineCurve PolesCount=4 KnotsCount=2 Degree=3 IsPeriodic=0
    g288: BSplineCurve PolesCount=4 KnotsCount=2 Degree=3 IsPeriodic=0
    g289: BSplineCurve PolesCount=4 KnotsCount=2 Degree=3 IsPeriodic=0
    g290: BSplineCurve PolesCount=4 KnotsCount=2 Degree=3 IsPeriodic=0
    g291: BSplineCurve PolesCount=4 KnotsCount=2 Degree=3 IsPeriodic=0
    g292: BSplineCurve PolesCount=4 KnotsCount=2 Degree=3 IsPeriodic=0
    g293: BSplineCurve PolesCount=4 KnotsCount=2 Degree=3 IsPeriodic=0
    g294: BSplineCurve PolesCount=4 KnotsCount=2 Degree=3 IsPeriodic=0
    g295: BSplineCurve PolesCount=4 KnotsCount=2 Degree=3 IsPeriodic=0
    g296: BSplineCurve PolesCount=4 KnotsCount=2 Degree=3 IsPeriodic=0
    g297: BSplineCurve PolesCount=4 KnotsCount=2 Degree=3 IsPeriodic=0
    g298: BSplineCurve PolesCount=4 KnotsCount=2 Degree=3 IsPeriodic=0
    g299: BSplineCurve PolesCount=4 KnotsCount=2 Degree=3 IsPeriodic=0
    g300: BSplineCurve PolesCount=4 KnotsCount=2 Degree=3 IsPeriodic=0
    g301: BSplineCurve PolesCount=4 KnotsCount=2 Degree=3 IsPeriodic=0
    g302: BSplineCurve PolesCount=4 KnotsCount=2 Degree=3 IsPeriodic=0
    g303: BSplineCurve PolesCount=4 KnotsCount=2 Degree=3 IsPeriodic=0
    g304: BSplineCurve PolesCount=4 KnotsCount=2 Degree=3 IsPeriodic=0
    g305: BSplineCurve PolesCount=4 KnotsCount=2 Degree=3 IsPeriodic=0
    g306: BSplineCurve PolesCount=4 KnotsCount=2 Degree=3 IsPeriodic=0
    g307: BSplineCurve PolesCount=4 KnotsCount=2 Degree=3 IsPeriodic=0
    g308: BSplineCurve PolesCount=4 KnotsCount=2 Degree=3 IsPeriodic=0
    g309: BSplineCurve PolesCount=4 KnotsCount=2 Degree=3 IsPeriodic=0
    g310: BSplineCurve PolesCount=4 KnotsCount=2 Degree=3 IsPeriodic=0
    g311: BSplineCurve PolesCount=4 KnotsCount=2 Degree=3 IsPeriodic=0
    g312: BSplineCurve PolesCount=4 KnotsCount=2 Degree=3 IsPeriodic=0
    g313: BSplineCurve PolesCount=4 KnotsCount=2 Degree=3 IsPeriodic=0
    g314: BSplineCurve PolesCount=4 KnotsCount=2 Degree=3 IsPeriodic=0
    g315: BSplineCurve PolesCount=4 KnotsCount=2 Degree=3 IsPeriodic=0
    g316: BSplineCurve PolesCount=4 KnotsCount=2 Degree=3 IsPeriodic=0
  constraints (317):
    c: Coincident(g0,g1)
    c: Coincident(g1,g2)
    c: Coincident(g2,g3)
    c: Coincident(g3,g4)
    c: Coincident(g4,g5)
    c: Coincident(g5,g6)
    c: Coincident(g6,g7)
    c: Coincident(g7,g8)
    c: Coincident(g8,g9)
    c: Coincident(g9,g10)
    c: Coincident(g10,g11)
    c: Coincident(g11,g12)
    c: Coincident(g12,g13)
    c: Coincident(g13,g14)
    c: Coincident(g14,g15)
    c: Coincident(g15,g16)
    c: Coincident(g16,g17)
    c: Coincident(g17,g18)
    c: Coincident(g18,g19)
    c: Coincident(g19,g20)
    c: Coincident(g20,g21)
    c: Coincident(g21,g22)
    c: Coincident(g22,g23)
    c: Coincident(g23,g24)
    c: Coincident(g24,g25)
    c: Coincident(g25,g26)
    c: Coincident(g26,g27)
    c: Coincident(g27,g28)
    c: Coincident(g28,g29)
    c: Coincident(g30,g31)
    c: Coincident(g31,g32)
    c: Coincident(g33,g34)
    c: Coincident(g34,g35)
    c: Coincident(g35,g36)
    c: Coincident(g36,g33)
    c: Coincident(g37,g38)
    c: Coincident(g38,g39)
    c: Coincident(g39,g40)
    c: Coincident(g40,g37)
    c: Coincident(g41,g42)
    c: Coincident(g42,g43)
    c: Coincident(g43,g44)
    c: Coincident(g44,g41)
    c: Coincident(g45,g46)
    c: Coincident(g46,g47)
    c: Coincident(g47,g48)
    c: Coincident(g48,g49)
    c: Coincident(g49,g45)
    c: Coincident(g50,g51)
    c: Coincident(g51,g52)
    c: Coincident(g52,g50)
    c: Coincident(g53,g54)
    c: Coincident(g54,g55)
    c: Coincident(g55,g53)
    c: Coincident(g56,g57)
    c: Coincident(g57,g58)
    c: Coincident(g58,g56)
    c: Coincident(g59,g60)
    c: Coincident(g60,g61)
    c: Coincident(g61,g59)
    c: Coincident(g63,g64)
    c: Coincident(g64,g65)
    c: Coincident(g65,g66)
    c: Coincident(g66,g62)
    c: Coincident(g67,g68)
    c: Coincident(g68,g69)
    c: Coincident(g69,g67)
    c: Coincident(g70,g71)
    c: Coincident(g71,g72)
    c: Coincident(g72,g70)
    c: Coincident(g73,g74)
    c: Coincident(g74,g75)
    c: Coincident(g75,g73)
    c: Coincident(g76,g77)
    c: Coincident(g77,g78)
    c: Coincident(g78,g76)
    c: Coincident(g79,g80)
    c: Coincident(g80,g81)
    c: Coincident(g81,g82)
    c: Coincident(g82,g83)
    c: Coincident(g83,g84)
    c: Coincident(g84,g85)
    c: Coincident(g85,g86)
    c: Coincident(g86,g87)
    c: Coincident(g87,g88)
    c: Coincident(g88,g89)
    c: Coincident(g89,g90)
    c: Coincident(g90,g79)
    c: Coincident(g91,g92)
    c: Coincident(g92,g93)
    c: Coincident(g93,g94)
    c: Coincident(g94,g95)
    c: Coincident(g95,g96)
    c: Coincident(g96,g97)
    c: Coincident(g97,g91)
    c: Coincident(g98,g99)
    c: Coincident(g99,g100)
    c: Coincident(g100,g98)
    c: Coincident(g101,g102)
    c: Coincident(g102,g103)
    c: Coincident(g103,g104)
    c: Coincident(g105,g106)
    c: Coincident(g106,g107)
    c: Coincident(g107,g108)
    c: Coincident(g108,g105)
    c: Coincident(g109,g110)
    c: Coincident(g110,g111)
    c: Coincident(g111,g112)
    c: Coincident(g112,g113)
    c: Coincident(g113,g109)
    c: Coincident(g114,g115)
    c: Coincident(g115,g116)
    c: Coincident(g116,g117)
    c: Coincident(g117,g118)
    c: Coincident(g118,g114)
    c: Coincident(g119,g120)
    c: Coincident(g120,g121)
    c: Coincident(g121,g122)
    c: Coincident(g122,g123)
    c: Coincident(g123,g124)
    c: Coincident(g124,g125)
    c: Coincident(g125,g126)
    c: Coincident(g126,g119)
    c: Coincident(g127,g128)
    c: Coincident(g128,g129)
    c: Coincident(g129,g130)
    c: Coincident(g130,g131)
    c: Coincident(g131,g132)
    c: Coincident(g132,g133)
    c: Coincident(g133,g134)
    c: Coincident(g134,g127)
    c: Coincident(g135,g136)
    c: Coincident(g136,g137)
    c: Coincident(g137,g138)
    c: Coincident(g139,g140)
    c: Coincident(g140,g141)
    c: Coincident(g141,g142)
    c: Coincident(g142,g143)
    c: Coincident(g143,g139)
    c: Coincident(g144,g145)
    c: Coincident(g145,g146)
    c: Coincident(g146,g147)
    c: Coincident(g147,g148)
    c: Coincident(g148,g149)
    c: Coincident(g150,g151)
    c: Coincident(g151,g152)
    c: Coincident(g152,g153)
    c: Coincident(g153,g154)
    c: Coincident(g154,g155)
    c: Coincident(g155,g156)
    c: Coincident(g156,g157)
    c: Coincident(g157,g158)
    c: Coincident(g158,g159)
    c: Coincident(g159,g150)
    c: Coincident(g160,g161)
    c: Coincident(g161,g162)
    c: Coincident(g162,g160)
    c: Coincident(g163,g164)
    c: Coincident(g164,g165)
    c: Coincident(g165,g166)
    c: Coincident(g166,g167)
    c: Coincident(g167,g168)
    c: Coincident(g168,g169)
    c: Coincident(g169,g170)
    c: Coincident(g170,g163)
    c: Coincident(g171,g172)
    c: Coincident(g172,g173)
    c: Coincident(g173,g174)
    c: Coincident(g174,g175)
    c: Coincident(g175,g176)
    c: Coincident(g176,g177)
    c: Coincident(g177,g171)
    c: Coincident(g178,g179)
    c: Coincident(g179,g180)
    c: Coincident(g180,g181)
    c: Coincident(g181,g182)
    c: Coincident(g183,g184)
    c: Coincident(g184,g185)
    c: Coincident(g185,g186)
    c: Coincident(g186,g183)
    c: Coincident(g187,g188)
    c: Coincident(g188,g189)
    c: Coincident(g189,g190)
    c: Coincident(g190,g191)
    c: Coincident(g191,g192)
    c: Coincident(g192,g193)
    c: Coincident(g193,g194)
    c: Coincident(g194,g195)
    c: Coincident(g196,g197)
    c: Coincident(g197,g198)
    c: Coincident(g198,g196)
    c: Coincident(g199,g200)
    c: Coincident(g200,g201)
    c: Coincident(g201,g202)
    c: Coincident(g202,g203)
    c: Coincident(g203,g204)
    c: Coincident(g204,g205)
    c: Coincident(g205,g206)
    c: Coincident(g206,g199)
    c: Coincident(g207,g208)
    c: Coincident(g208,g209)
    c: Coincident(g209,g210)
    c: Coincident(g210,g211)
    c: Coincident(g211,g212)
    c: Coincident(g212,g213)
    c: Coincident(g213,g214)
    c: Coincident(g215,g216)
    c: Coincident(g216,g217)
    c: Coincident(g217,g218)
    c: Coincident(g218,g215)
    c: Coincident(g219,g220)
    c: Coincident(g220,g221)
    c: Coincident(g221,g222)
    c: Coincident(g222,g223)
    c: Coincident(g223,g224)
    c: Coincident(g224,g225)
    c: Coincident(g225,g226)
    c: Coincident(g227,g228)
    c: Coincident(g228,g229)
    c: Coincident(g229,g230)
    c: Coincident(g230,g231)
    c: Coincident(g231,g232)
    c: Coincident(g232,g233)
    c: Coincident(g233,g227)
    c: Coincident(g234,g235)
    c: Coincident(g235,g236)
    c: Coincident(g236,g237)
    c: Coincident(g237,g238)
    c: Coincident(g238,g239)
    c: Coincident(g239,g240)
    c: Coincident(g240,g241)
    c: Coincident(g241,g242)
    c: Coincident(g242,g234)
    c: Coincident(g243,g244)
    c: Coincident(g244,g245)
    c: Coincident(g245,g246)
    c: Coincident(g246,g247)
    c: Coincident(g247,g248)
    c: Coincident(g248,g249)
    c: Coincident(g249,g250)
    c: Coincident(g250,g251)
    c: Coincident(g251,g252)
    c: Coincident(g252,g253)
    c: Coincident(g253,g254)
    c: Coincident(g254,g243)
    c: Coincident(g255,g256)
    c: Coincident(g256,g257)
    c: Coincident(g258,g259)
    c: Coincident(g259,g260)
    c: Coincident(g261,g262)
    c: Coincident(g262,g263)
    c: Coincident(g263,g264)
    c: Coincident(g264,g265)
    c: Coincident(g266,g267)
    c: Coincident(g267,g268)
    c: Coincident(g268,g269)
    c: Coincident(g269,g270)
    c: Coincident(g270,g271)
    c: Coincident(g272,g273)
    c: Coincident(g273,g274)
    c: Coincident(g274,g275)
    c: Coincident(g275,g276)
    c: Coincident(g276,g277)
    c: Coincident(g277,g278)
    c: Coincident(g278,g279)
    c: Coincident(g279,g272)
    c: Coincident(g280,g281)
    c: Coincident(g281,g282)
    c: Coincident(g282,g283)
    c: Coincident(g283,g284)
    c: Coincident(g284,g285)
    c: Coincident(g285,g286)
    c: Coincident(g286,g287)
    c: Coincident(g287,g288)
    c: Coincident(g288,g289)
    c: Coincident(g289,g290)
    c: Coincident(g290,g291)
    c: Coincident(g291,g292)
    c: Coincident(g292,g293)
    c: Coincident(g293,g294)
    c: Coincident(g294,g295)
    c: Coincident(g295,g280)
    c: Coincident(g296,g297)
    c: Coincident(g297,g298)
    c: Coincident(g298,g299)
    c: Coincident(g299,g300)
    c: Coincident(g300,g301)
    c: Coincident(g301,g302)
    c: Coincident(g302,g303)
    c: Coincident(g304,g305)
    c: Coincident(g305,g306)
    c: Coincident(g306,g307)
    c: Coincident(g307,g308)
    c: Coincident(g308,g309)
    c: Coincident(g309,g310)
    c: Coincident(g310,g311)
    c: Coincident(g311,g304)
    c: Coincident(g312,g313)
    c: Coincident(g313,g314)
    c: Coincident(g314,g315)
    c: Coincident(g315,g316)
    c: Coincident(g316,g312)
    c: Coincident(g29,g0)
    c: Coincident(g62,g63)
    c: Coincident(g261,g265)
    c: Coincident(g178,g182)
    c: Coincident(g296,g303)
    c: Coincident(g258,g260)
    c: Coincident(g255,g257)
    c: Coincident(g219,g226)
    c: Coincident(g187,g195)
    c: Coincident(g144,g149)
    c: Coincident(g207,g214)
    c: Coincident(g135,g138)
    c: Coincident(g266,g271)
    c: Coincident(g30,g32)
    c: Coincident(g101,g104)
FEATURE [Sketcher::SketchObject] Sketch045  label="Seamstress-Sketch"
  ArcFitTolerance = 1e-06
  FullyConstrained = false
  MakeInternals = false
  Placement = pos=(-15.6569,14.6863,0) rot=(0,0,1;0rad)
  expr: .Placement.Base.x = -(.Shape.BoundBox.XLength / 2)
  expr: .Placement.Base.y = .Shape.BoundBox.YLength / 2
  sketch-geometry (213):
    g0: BSplineCurve PolesCount=4 KnotsCount=2 Degree=3 IsPeriodic=0
    g1: BSplineCurve PolesCount=4 KnotsCount=2 Degree=3 IsPeriodic=0
    g2: BSplineCurve PolesCount=4 KnotsCount=2 Degree=3 IsPeriodic=0
    g3: BSplineCurve PolesCount=4 KnotsCount=2 Degree=3 IsPeriodic=0
    g4: BSplineCurve PolesCount=4 KnotsCount=2 Degree=3 IsPeriodic=0
    g5: BSplineCurve PolesCount=4 KnotsCount=2 Degree=3 IsPeriodic=0
    g6: BSplineCurve PolesCount=4 KnotsCount=2 Degree=3 IsPeriodic=0
    g7: BSplineCurve PolesCount=4 KnotsCount=2 Degree=3 IsPeriodic=0
    g8: BSplineCurve PolesCount=4 KnotsCount=2 Degree=3 IsPeriodic=0
    g9: BSplineCurve PolesCount=4 KnotsCount=2 Degree=3 IsPeriodic=0
    g10: BSplineCurve PolesCount=4 KnotsCount=2 Degree=3 IsPeriodic=0
    g11: BSplineCurve PolesCount=4 KnotsCount=2 Degree=3 IsPeriodic=0
    g12: BSplineCurve PolesCount=4 KnotsCount=2 Degree=3 IsPeriodic=0
    g13: BSplineCurve PolesCount=4 KnotsCount=2 Degree=3 IsPeriodic=0
    g14: BSplineCurve PolesCount=4 KnotsCount=2 Degree=3 IsPeriodic=0
    g15: BSplineCurve PolesCount=4 KnotsCount=2 Degree=3 IsPeriodic=0
    g16: BSplineCurve PolesCount=4 KnotsCount=2 Degree=3 IsPeriodic=0
    g17: BSplineCurve PolesCount=4 KnotsCount=2 Degree=3 IsPeriodic=0
    g18: BSplineCurve PolesCount=4 KnotsCount=2 Degree=3 IsPeriodic=0
    g19: BSplineCurve PolesCount=4 KnotsCount=2 Degree=3 IsPeriodic=0
    g20: BSplineCurve PolesCount=4 KnotsCount=2 Degree=3 IsPeriodic=0
    g21: BSplineCurve PolesCount=4 KnotsCount=2 Degree=3 IsPeriodic=0
    g22: BSplineCurve PolesCount=2 KnotsCount=2 Degree=1 IsPeriodic=0
    g23: BSplineCurve PolesCount=2 KnotsCount=2 Degree=1 IsPeriodic=0
    g24: BSplineCurve PolesCount=4 KnotsCount=2 Degree=3 IsPeriodic=0
    g25: BSplineCurve PolesCount=4 KnotsCount=2 Degree=3 IsPeriodic=0
    g26: BSplineCurve PolesCount=4 KnotsCount=2 Degree=3 IsPeriodic=0
    g27: BSplineCurve PolesCount=4 KnotsCount=2 Degree=3 IsPeriodic=0
    g28: BSplineCurve PolesCount=4 KnotsCount=2 Degree=3 IsPeriodic=0
    g29: BSplineCurve PolesCount=4 KnotsCount=2 Degree=3 IsPeriodic=0
    g30: BSplineCurve PolesCount=4 KnotsCount=2 Degree=3 IsPeriodic=0
    g31: BSplineCurve PolesCount=4 KnotsCount=2 Degree=3 IsPeriodic=0
    g32: BSplineCurve PolesCount=4 KnotsCount=2 Degree=3 IsPeriodic=0
    g33: BSplineCurve PolesCount=2 KnotsCount=2 Degree=1 IsPeriodic=0
    g34: BSplineCurve PolesCount=2 KnotsCount=2 Degree=1 IsPeriodic=0
    g35: BSplineCurve PolesCount=4 KnotsCount=2 Degree=3 IsPeriodic=0
    g36: BSplineCurve PolesCount=4 KnotsCount=2 Degree=3 IsPeriodic=0
    g37: BSplineCurve PolesCount=4 KnotsCount=2 Degree=3 IsPeriodic=0
    g38: BSplineCurve PolesCount=4 KnotsCount=2 Degree=3 IsPeriodic=0
    g39: BSplineCurve PolesCount=4 KnotsCount=2 Degree=3 IsPeriodic=0
    g40: BSplineCurve PolesCount=4 KnotsCount=2 Degree=3 IsPeriodic=0
    g41: BSplineCurve PolesCount=4 KnotsCount=2 Degree=3 IsPeriodic=0
    g42: BSplineCurve PolesCount=4 KnotsCount=2 Degree=3 IsPeriodic=0
    g43: BSplineCurve PolesCount=4 KnotsCount=2 Degree=3 IsPeriodic=0
    g44: BSplineCurve PolesCount=4 KnotsCount=2 Degree=3 IsPeriodic=0
    g45: BSplineCurve PolesCount=4 KnotsCount=2 Degree=3 IsPeriodic=0
    g46: BSplineCurve PolesCount=4 KnotsCount=2 Degree=3 IsPeriodic=0
    g47: BSplineCurve PolesCount=4 KnotsCount=2 Degree=3 IsPeriodic=0
    g48: BSplineCurve PolesCount=4 KnotsCount=2 Degree=3 IsPeriodic=0
    g49: BSplineCurve PolesCount=4 KnotsCount=2 Degree=3 IsPeriodic=0
    g50: BSplineCurve PolesCount=4 KnotsCount=2 Degree=3 IsPeriodic=0
    g51: BSplineCurve PolesCount=4 KnotsCount=2 Degree=3 IsPeriodic=0
    g52: BSplineCurve PolesCount=4 KnotsCount=2 Degree=3 IsPeriodic=0
    g53: BSplineCurve PolesCount=4 KnotsCount=2 Degree=3 IsPeriodic=0
    g54: BSplineCurve PolesCount=4 KnotsCount=2 Degree=3 IsPeriodic=0
    g55: BSplineCurve PolesCount=4 KnotsCount=2 Degree=3 IsPeriodic=0
    g56: BSplineCurve PolesCount=4 KnotsCount=2 Degree=3 IsPeriodic=0
    g57: BSplineCurve PolesCount=4 KnotsCount=2 Degree=3 IsPeriodic=0
    g58: BSplineCurve PolesCount=4 KnotsCount=2 Degree=3 IsPeriodic=0
    g59: BSplineCurve PolesCount=2 KnotsCount=2 Degree=1 IsPeriodic=0
    g60: BSplineCurve PolesCount=2 KnotsCount=2 Degree=1 IsPeriodic=0
    g61: BSplineCurve PolesCount=4 KnotsCount=2 Degree=3 IsPeriodic=0
    g62: BSplineCurve PolesCount=4 KnotsCount=2 Degree=3 IsPeriodic=0
    g63: BSplineCurve PolesCount=2 KnotsCount=2 Degree=1 IsPeriodic=0
    g64: BSplineCurve PolesCount=2 KnotsCount=2 Degree=1 IsPeriodic=0
    g65: BSplineCurve PolesCount=4 KnotsCount=2 Degree=3 IsPeriodic=0
    g66: BSplineCurve PolesCount=2 KnotsCount=2 Degree=1 IsPeriodic=0
    g67: BSplineCurve PolesCount=2 KnotsCount=2 Degree=1 IsPeriodic=0
    g68: BSplineCurve PolesCount=4 KnotsCount=2 Degree=3 IsPeriodic=0
    g69: BSplineCurve PolesCount=4 KnotsCount=2 Degree=3 IsPeriodic=0
    g70: BSplineCurve PolesCount=4 KnotsCount=2 Degree=3 IsPeriodic=0
    g71: BSplineCurve PolesCount=4 KnotsCount=2 Degree=3 IsPeriodic=0
    g72: BSplineCurve PolesCount=4 KnotsCount=2 Degree=3 IsPeriodic=0
    g73: BSplineCurve PolesCount=4 KnotsCount=2 Degree=3 IsPeriodic=0
    g74: BSplineCurve PolesCount=4 KnotsCount=2 Degree=3 IsPeriodic=0
    g75: BSplineCurve PolesCount=4 KnotsCount=2 Degree=3 IsPeriodic=0
    g76: BSplineCurve PolesCount=4 KnotsCount=2 Degree=3 IsPeriodic=0
    g77: BSplineCurve PolesCount=4 KnotsCount=2 Degree=3 IsPeriodic=0
    g78: BSplineCurve PolesCount=4 KnotsCount=2 Degree=3 IsPeriodic=0
    g79: BSplineCurve PolesCount=4 KnotsCount=2 Degree=3 IsPeriodic=0
    g80: BSplineCurve PolesCount=4 KnotsCount=2 Degree=3 IsPeriodic=0
    g81: BSplineCurve PolesCount=4 KnotsCount=2 Degree=3 IsPeriodic=0
    g82: BSplineCurve PolesCount=4 KnotsCount=2 Degree=3 IsPeriodic=0
    g83: BSplineCurve PolesCount=4 KnotsCount=2 Degree=3 IsPeriodic=0
    g84: BSplineCurve PolesCount=4 KnotsCount=2 Degree=3 IsPeriodic=0
    g85: BSplineCurve PolesCount=4 KnotsCount=2 Degree=3 IsPeriodic=0
    g86: BSplineCurve PolesCount=4 KnotsCount=2 Degree=3 IsPeriodic=0
    g87: BSplineCurve PolesCount=4 KnotsCount=2 Degree=3 IsPeriodic=0
    g88: BSplineCurve PolesCount=4 KnotsCount=2 Degree=3 IsPeriodic=0
    g89: BSplineCurve PolesCount=4 KnotsCount=2 Degree=3 IsPeriodic=0
    g90: BSplineCurve PolesCount=4 KnotsCount=2 Degree=3 IsPeriodic=0
    g91: BSplineCurve PolesCount=4 KnotsCount=2 Degree=3 IsPeriodic=0
    g92: BSplineCurve PolesCount=4 KnotsCount=2 Degree=3 IsPeriodic=0
    g93: BSplineCurve PolesCount=4 KnotsCount=2 Degree=3 IsPeriodic=0
    g94: BSplineCurve PolesCount=4 KnotsCount=2 Degree=3 IsPeriodic=0
    g95: BSplineCurve PolesCount=4 KnotsCount=2 Degree=3 IsPeriodic=0
    g96: BSplineCurve PolesCount=4 KnotsCount=2 Degree=3 IsPeriodic=0
    g97: BSplineCurve PolesCount=4 KnotsCount=2 Degree=3 IsPeriodic=0
    g98: BSplineCurve PolesCount=4 KnotsCount=2 Degree=3 IsPeriodic=0
    g99: BSplineCurve PolesCount=4 KnotsCount=2 Degree=3 IsPeriodic=0
    g100: BSplineCurve PolesCount=4 KnotsCount=2 Degree=3 IsPeriodic=0
    g101: BSplineCurve PolesCount=4 KnotsCount=2 Degree=3 IsPeriodic=0
    g102: BSplineCurve PolesCount=4 KnotsCount=2 Degree=3 IsPeriodic=0
    g103: BSplineCurve PolesCount=4 KnotsCount=2 Degree=3 IsPeriodic=0
    g104: BSplineCurve PolesCount=4 KnotsCount=2 Degree=3 IsPeriodic=0
    g105: BSplineCurve PolesCount=4 KnotsCount=2 Degree=3 IsPeriodic=0
    g106: BSplineCurve PolesCount=4 KnotsCount=2 Degree=3 IsPeriodic=0
    g107: BSplineCurve PolesCount=4 KnotsCount=2 Degree=3 IsPeriodic=0
    g108: BSplineCurve PolesCount=4 KnotsCount=2 Degree=3 IsPeriodic=0
    g109: BSplineCurve PolesCount=4 KnotsCount=2 Degree=3 IsPeriodic=0
    g110: BSplineCurve PolesCount=4 KnotsCount=2 Degree=3 IsPeriodic=0
    g111: BSplineCurve PolesCount=4 KnotsCount=2 Degree=3 IsPeriodic=0
    g112: BSplineCurve PolesCount=4 KnotsCount=2 Degree=3 IsPeriodic=0
    g113: BSplineCurve PolesCount=4 KnotsCount=2 Degree=3 IsPeriodic=0
    g114: BSplineCurve PolesCount=4 KnotsCount=2 Degree=3 IsPeriodic=0
    g115: BSplineCurve PolesCount=4 KnotsCount=2 Degree=3 IsPeriodic=0
    g116: BSplineCurve PolesCount=4 KnotsCount=2 Degree=3 IsPeriodic=0
    g117: BSplineCurve PolesCount=4 KnotsCount=2 Degree=3 IsPeriodic=0
    g118: BSplineCurve PolesCount=4 KnotsCount=2 Degree=3 IsPeriodic=0
    g119: BSplineCurve PolesCount=4 KnotsCount=2 Degree=3 IsPeriodic=0
    g120: BSplineCurve PolesCount=4 KnotsCount=2 Degree=3 IsPeriodic=0
    g121: BSplineCurve PolesCount=4 KnotsCount=2 Degree=3 IsPeriodic=0
    g122: BSplineCurve PolesCount=4 KnotsCount=2 Degree=3 IsPeriodic=0
    g123: BSplineCurve PolesCount=4 KnotsCount=2 Degree=3 IsPeriodic=0
    g124: BSplineCurve PolesCount=4 KnotsCount=2 Degree=3 IsPeriodic=0
    g125: BSplineCurve PolesCount=4 KnotsCount=2 Degree=3 IsPeriodic=0
    g126: BSplineCurve PolesCount=4 KnotsCount=2 Degree=3 IsPeriodic=0
    g127: BSplineCurve PolesCount=4 KnotsCount=2 Degree=3 IsPeriodic=0
    g128: BSplineCurve PolesCount=4 KnotsCount=2 Degree=3 IsPeriodic=0
    g129: BSplineCurve PolesCount=4 KnotsCount=2 Degree=3 IsPeriodic=0
    g130: BSplineCurve PolesCount=4 KnotsCount=2 Degree=3 IsPeriodic=0
    g131: BSplineCurve PolesCount=4 KnotsCount=2 Degree=3 IsPeriodic=0
    g132: BSplineCurve PolesCount=4 KnotsCount=2 Degree=3 IsPeriodic=0
    g133: BSplineCurve PolesCount=4 KnotsCount=2 Degree=3 IsPeriodic=0
    g134: BSplineCurve PolesCount=4 KnotsCount=2 Degree=3 IsPeriodic=0
    g135: BSplineCurve PolesCount=4 KnotsCount=2 Degree=3 IsPeriodic=0
    g136: BSplineCurve PolesCount=4 KnotsCount=2 Degree=3 IsPeriodic=0
    g137: BSplineCurve PolesCount=4 KnotsCount=2 Degree=3 IsPeriodic=0
    g138: BSplineCurve PolesCount=4 KnotsCount=2 Degree=3 IsPeriodic=0
    g139: BSplineCurve PolesCount=4 KnotsCount=2 Degree=3 IsPeriodic=0
    g140: BSplineCurve PolesCount=4 KnotsCount=2 Degree=3 IsPeriodic=0
    g141: BSplineCurve PolesCount=2 KnotsCount=2 Degree=1 IsPeriodic=0
    g142: BSplineCurve PolesCount=2 KnotsCount=2 Degree=1 IsPeriodic=0
    g143: BSplineCurve PolesCount=4 KnotsCount=2 Degree=3 IsPeriodic=0
    g144: BSplineCurve PolesCount=4 KnotsCount=2 Degree=3 IsPeriodic=0
    g145: BSplineCurve PolesCount=4 KnotsCount=2 Degree=3 IsPeriodic=0
    g146: BSplineCurve PolesCount=4 KnotsCount=2 Degree=3 IsPeriodic=0
    g147: BSplineCurve PolesCount=4 KnotsCount=2 Degree=3 IsPeriodic=0
    g148: BSplineCurve PolesCount=4 KnotsCount=2 Degree=3 IsPeriodic=0
    g149: BSplineCurve PolesCount=4 KnotsCount=2 Degree=3 IsPeriodic=0
    g150: BSplineCurve PolesCount=4 KnotsCount=2 Degree=3 IsPeriodic=0
    g151: BSplineCurve PolesCount=4 KnotsCount=2 Degree=3 IsPeriodic=0
    g152: BSplineCurve PolesCount=4 KnotsCount=2 Degree=3 IsPeriodic=0
    g153: BSplineCurve PolesCount=4 KnotsCount=2 Degree=3 IsPeriodic=0
    g154: BSplineCurve PolesCount=4 KnotsCount=2 Degree=3 IsPeriodic=0
    g155: BSplineCurve PolesCount=4 KnotsCount=2 Degree=3 IsPeriodic=0
    g156: BSplineCurve PolesCount=4 KnotsCount=2 Degree=3 IsPeriodic=0
    g157: BSplineCurve PolesCount=4 KnotsCount=2 Degree=3 IsPeriodic=0
    g158: BSplineCurve PolesCount=4 KnotsCount=2 Degree=3 IsPeriodic=0
    g159: BSplineCurve PolesCount=4 KnotsCount=2 Degree=3 IsPeriodic=0
    g160: BSplineCurve PolesCount=4 KnotsCount=2 Degree=3 IsPeriodic=0
    g161: BSplineCurve PolesCount=4 KnotsCount=2 Degree=3 IsPeriodic=0
    g162: BSplineCurve PolesCount=4 KnotsCount=2 Degree=3 IsPeriodic=0
    g163: BSplineCurve PolesCount=4 KnotsCount=2 Degree=3 IsPeriodic=0
    g164: BSplineCurve PolesCount=4 KnotsCount=2 Degree=3 IsPeriodic=0
    g165: BSplineCurve PolesCount=4 KnotsCount=2 Degree=3 IsPeriodic=0
    g166: BSplineCurve PolesCount=4 KnotsCount=2 Degree=3 IsPeriodic=0
    g167: BSplineCurve PolesCount=4 KnotsCount=2 Degree=3 IsPeriodic=0
    g168: BSplineCurve PolesCount=4 KnotsCount=2 Degree=3 IsPeriodic=0
    g169: BSplineCurve PolesCount=4 KnotsCount=2 Degree=3 IsPeriodic=0
    g170: BSplineCurve PolesCount=4 KnotsCount=2 Degree=3 IsPeriodic=0
    g171: BSplineCurve PolesCount=4 KnotsCount=2 Degree=3 IsPeriodic=0
    g172: BSplineCurve PolesCount=4 KnotsCount=2 Degree=3 IsPeriodic=0
    g173: BSplineCurve PolesCount=4 KnotsCount=2 Degree=3 IsPeriodic=0
    g174: BSplineCurve PolesCount=4 KnotsCount=2 Degree=3 IsPeriodic=0
    g175: BSplineCurve PolesCount=4 KnotsCount=2 Degree=3 IsPeriodic=0
    g176: BSplineCurve PolesCount=4 KnotsCount=2 Degree=3 IsPeriodic=0
    g177: BSplineCurve PolesCount=4 KnotsCount=2 Degree=3 IsPeriodic=0
    g178: BSplineCurve PolesCount=4 KnotsCount=2 Degree=3 IsPeriodic=0
    g179: BSplineCurve PolesCount=4 KnotsCount=2 Degree=3 IsPeriodic=0
    g180: BSplineCurve PolesCount=4 KnotsCount=2 Degree=3 IsPeriodic=0
    g181: BSplineCurve PolesCount=4 KnotsCount=2 Degree=3 IsPeriodic=0
    g182: BSplineCurve PolesCount=4 KnotsCount=2 Degree=3 IsPeriodic=0
    g183: BSplineCurve PolesCount=4 KnotsCount=2 Degree=3 IsPeriodic=0
    g184: BSplineCurve PolesCount=4 KnotsCount=2 Degree=3 IsPeriodic=0
    g185: BSplineCurve PolesCount=4 KnotsCount=2 Degree=3 IsPeriodic=0
    g186: BSplineCurve PolesCount=4 KnotsCount=2 Degree=3 IsPeriodic=0
    g187: BSplineCurve PolesCount=4 KnotsCount=2 Degree=3 IsPeriodic=0
    g188: BSplineCurve PolesCount=4 KnotsCount=2 Degree=3 IsPeriodic=0
    g189: BSplineCurve PolesCount=4 KnotsCount=2 Degree=3 IsPeriodic=0
    g190: BSplineCurve PolesCount=4 KnotsCount=2 Degree=3 IsPeriodic=0
    g191: BSplineCurve PolesCount=4 KnotsCount=2 Degree=3 IsPeriodic=0
    g192: BSplineCurve PolesCount=4 KnotsCount=2 Degree=3 IsPeriodic=0
    g193: BSplineCurve PolesCount=4 KnotsCount=2 Degree=3 IsPeriodic=0
    g194: BSplineCurve PolesCount=4 KnotsCount=2 Degree=3 IsPeriodic=0
    g195: BSplineCurve PolesCount=4 KnotsCount=2 Degree=3 IsPeriodic=0
    g196: BSplineCurve PolesCount=4 KnotsCount=2 Degree=3 IsPeriodic=0
    g197: BSplineCurve PolesCount=4 KnotsCount=2 Degree=3 IsPeriodic=0
    g198: BSplineCurve PolesCount=4 KnotsCount=2 Degree=3 IsPeriodic=0
    g199: BSplineCurve PolesCount=4 KnotsCount=2 Degree=3 IsPeriodic=0
    g200: BSplineCurve PolesCount=4 KnotsCount=2 Degree=3 IsPeriodic=0
    g201: BSplineCurve PolesCount=2 KnotsCount=2 Degree=1 IsPeriodic=0
    g202: BSplineCurve PolesCount=2 KnotsCount=2 Degree=1 IsPeriodic=0
    g203: BSplineCurve PolesCount=4 KnotsCount=2 Degree=3 IsPeriodic=0
    g204: BSplineCurve PolesCount=4 KnotsCount=2 Degree=3 IsPeriodic=0
    g205: BSplineCurve PolesCount=4 KnotsCount=2 Degree=3 IsPeriodic=0
    g206: BSplineCurve PolesCount=4 KnotsCount=2 Degree=3 IsPeriodic=0
    g207: BSplineCurve PolesCount=4 KnotsCount=2 Degree=3 IsPeriodic=0
    g208: BSplineCurve PolesCount=4 KnotsCount=2 Degree=3 IsPeriodic=0
    g209: BSplineCurve PolesCount=4 KnotsCount=2 Degree=3 IsPeriodic=0
    g210: BSplineCurve PolesCount=4 KnotsCount=2 Degree=3 IsPeriodic=0
    g211: BSplineCurve PolesCount=4 KnotsCount=2 Degree=3 IsPeriodic=0
    g212: BSplineCurve PolesCount=4 KnotsCount=2 Degree=3 IsPeriodic=0
  constraints (213):
    c: Coincident(g0,g1)
    c: Coincident(g1,g2)
    c: Coincident(g2,g3)
    c: Coincident(g3,g4)
    c: Coincident(g4,g5)
    c: Coincident(g5,g6)
    c: Coincident(g6,g7)
    c: Coincident(g7,g8)
    c: Coincident(g8,g9)
    c: Coincident(g9,g10)
    c: Coincident(g10,g0)
    c: Coincident(g11,g12)
    c: Coincident(g12,g13)
    c: Coincident(g13,g11)
    c: Coincident(g14,g15)
    c: Coincident(g15,g16)
    c: Coincident(g16,g14)
    c: Coincident(g17,g18)
    c: Coincident(g18,g19)
    c: Coincident(g19,g17)
    c: Coincident(g20,g21)
    c: Coincident(g21,g22)
    c: Coincident(g22,g23)
    c: Coincident(g23,g20)
    c: Coincident(g24,g25)
    c: Coincident(g25,g26)
    c: Coincident(g26,g27)
    c: Coincident(g27,g28)
    c: Coincident(g28,g29)
    c: Coincident(g29,g30)
    c: Coincident(g30,g31)
    c: Coincident(g31,g32)
    c: Coincident(g32,g33)
    c: Coincident(g33,g34)
    c: Coincident(g34,g35)
    c: Coincident(g35,g36)
    c: Coincident(g36,g37)
    c: Coincident(g37,g38)
    c: Coincident(g38,g39)
    c: Coincident(g39,g40)
    c: Coincident(g40,g41)
    c: Coincident(g41,g42)
    c: Coincident(g42,g43)
    c: Coincident(g43,g44)
    c: Coincident(g44,g45)
    c: Coincident(g45,g46)
    c: Coincident(g46,g47)
    c: Coincident(g47,g48)
    c: Coincident(g48,g49)
    c: Coincident(g49,g50)
    c: Coincident(g50,g51)
    c: Coincident(g51,g52)
    c: Coincident(g52,g53)
    c: Coincident(g53,g54)
    c: Coincident(g54,g55)
    c: Coincident(g55,g56)
    c: Coincident(g56,g57)
    c: Coincident(g57,g58)
    c: Coincident(g58,g59)
    c: Coincident(g59,g60)
    c: Coincident(g60,g61)
    c: Coincident(g61,g62)
    c: Coincident(g62,g63)
    c: Coincident(g63,g64)
    c: Coincident(g64,g65)
    c: Coincident(g65,g66)
    c: Coincident(g66,g67)
    c: Coincident(g67,g68)
    c: Coincident(g68,g69)
    c: Coincident(g69,g70)
    c: Coincident(g70,g71)
    c: Coincident(g71,g72)
    c: Coincident(g72,g73)
    c: Coincident(g73,g74)
    c: Coincident(g74,g75)
    c: Coincident(g75,g76)
    c: Coincident(g76,g77)
    c: Coincident(g77,g78)
    c: Coincident(g78,g79)
    c: Coincident(g79,g80)
    c: Coincident(g80,g24)
    c: Coincident(g81,g82)
    c: Coincident(g82,g83)
    c: Coincident(g83,g84)
    c: Coincident(g84,g85)
    c: Coincident(g85,g86)
    c: Coincident(g87,g88)
    c: Coincident(g88,g89)
    c: Coincident(g89,g90)
    c: Coincident(g90,g91)
    c: Coincident(g91,g92)
    c: Coincident(g92,g93)
    c: Coincident(g93,g94)
    c: Coincident(g94,g95)
    c: Coincident(g96,g97)
    c: Coincident(g97,g98)
    c: Coincident(g98,g99)
    c: Coincident(g99,g96)
    c: Coincident(g100,g101)
    c: Coincident(g101,g102)
    c: Coincident(g102,g103)
    c: Coincident(g103,g100)
    c: Coincident(g104,g105)
    c: Coincident(g105,g106)
    c: Coincident(g106,g107)
    c: Coincident(g108,g109)
    c: Coincident(g109,g110)
    c: Coincident(g110,g111)
    c: Coincident(g111,g108)
    c: Coincident(g112,g113)
    c: Coincident(g113,g114)
    c: Coincident(g114,g115)
    c: Coincident(g116,g117)
    c: Coincident(g117,g118)
    c: Coincident(g118,g116)
    c: Coincident(g119,g120)
    c: Coincident(g120,g121)
    c: Coincident(g121,g122)
    c: Coincident(g122,g123)
    c: Coincident(g123,g124)
    c: Coincident(g124,g125)
    c: Coincident(g125,g126)
    c: Coincident(g126,g127)
    c: Coincident(g127,g119)
    c: Coincident(g128,g129)
    c: Coincident(g129,g130)
    c: Coincident(g130,g128)
    c: Coincident(g131,g132)
    c: Coincident(g132,g133)
    c: Coincident(g133,g134)
    c: Coincident(g135,g136)
    c: Coincident(g136,g137)
    c: Coincident(g137,g135)
    c: Coincident(g138,g139)
    c: Coincident(g139,g140)
    c: Coincident(g140,g141)
    c: Coincident(g141,g142)
    c: Coincident(g142,g143)
    c: Coincident(g143,g144)
    c: Coincident(g144,g145)
    c: Coincident(g145,g146)
    c: Coincident(g146,g147)
    c: Coincident(g147,g148)
    c: Coincident(g148,g149)
    c: Coincident(g149,g150)
    c: Coincident(g150,g151)
    c: Coincident(g151,g152)
    c: Coincident(g152,g153)
    c: Coincident(g153,g154)
    c: Coincident(g154,g155)
    c: Coincident(g155,g156)
    c: Coincident(g156,g157)
    c: Coincident(g158,g159)
    c: Coincident(g159,g160)
    c: Coincident(g160,g161)
    c: Coincident(g161,g162)
    c: Coincident(g162,g163)
    c: Coincident(g163,g164)
    c: Coincident(g164,g165)
    c: Coincident(g165,g166)
    c: Coincident(g166,g167)
    c: Coincident(g167,g168)
    c: Coincident(g168,g169)
    c: Coincident(g169,g158)
    c: Coincident(g170,g171)
    c: Coincident(g171,g172)
    c: Coincident(g173,g174)
    c: Coincident(g174,g175)
    c: Coincident(g175,g176)
    c: Coincident(g176,g177)
    c: Coincident(g177,g178)
    c: Coincident(g178,g179)
    c: Coincident(g179,g173)
    c: Coincident(g180,g181)
    c: Coincident(g181,g182)
    c: Coincident(g183,g184)
    c: Coincident(g184,g185)
    c: Coincident(g185,g186)
    c: Coincident(g186,g183)
    c: Coincident(g187,g188)
    c: Coincident(g188,g189)
    c: Coincident(g190,g191)
    c: Coincident(g191,g192)
    c: Coincident(g193,g194)
    c: Coincident(g194,g195)
    c: Coincident(g196,g197)
    c: Coincident(g197,g198)
    c: Coincident(g198,g196)
    c: Coincident(g199,g200)
    c: Coincident(g200,g201)
    c: Coincident(g201,g202)
    c: Coincident(g202,g203)
    c: Coincident(g203,g204)
    c: Coincident(g204,g205)
    c: Coincident(g205,g199)
    c: Coincident(g206,g207)
    c: Coincident(g207,g208)
    c: Coincident(g208,g206)
    c: Coincident(g209,g210)
    c: Coincident(g210,g211)
    c: Coincident(g211,g212)
    c: Coincident(g212,g209)
    c: Coincident(g112,g115)
    c: Coincident(g87,g95)
    c: Coincident(g81,g86)
    c: Coincident(g104,g107)
    c: Coincident(g193,g195)
    c: Coincident(g187,g189)
    c: Coincident(g190,g192)
    c: Coincident(g180,g182)
    c: Coincident(g170,g172)
    c: Coincident(g138,g157)
    c: Coincident(g131,g134)
FEATURE [Sketcher::SketchObject] Sketch046  label="Snake_Charmer-Sketch"
  ArcFitTolerance = 1e-06
  FullyConstrained = false
  MakeInternals = false
  Placement = pos=(-11.4902,14.7802,0) rot=(0,0,1;0rad)
  expr: .Placement.Base.x = -(.Shape.BoundBox.XLength / 2)
  expr: .Placement.Base.y = .Shape.BoundBox.YLength / 2
  sketch-geometry (313):
    g0: BSplineCurve PolesCount=4 KnotsCount=2 Degree=3 IsPeriodic=0
    g1: BSplineCurve PolesCount=2 KnotsCount=2 Degree=1 IsPeriodic=0
    g2: BSplineCurve PolesCount=2 KnotsCount=2 Degree=1 IsPeriodic=0
    g3: BSplineCurve PolesCount=4 KnotsCount=2 Degree=3 IsPeriodic=0
    g4: BSplineCurve PolesCount=4 KnotsCount=2 Degree=3 IsPeriodic=0
    g5: BSplineCurve PolesCount=4 KnotsCount=2 Degree=3 IsPeriodic=0
    g6: BSplineCurve PolesCount=4 KnotsCount=2 Degree=3 IsPeriodic=0
    g7: BSplineCurve PolesCount=4 KnotsCount=2 Degree=3 IsPeriodic=0
    g8: BSplineCurve PolesCount=4 KnotsCount=2 Degree=3 IsPeriodic=0
    g9: BSplineCurve PolesCount=4 KnotsCount=2 Degree=3 IsPeriodic=0
    g10: BSplineCurve PolesCount=4 KnotsCount=2 Degree=3 IsPeriodic=0
    g11: BSplineCurve PolesCount=4 KnotsCount=2 Degree=3 IsPeriodic=0
    g12: BSplineCurve PolesCount=4 KnotsCount=2 Degree=3 IsPeriodic=0
    g13: BSplineCurve PolesCount=4 KnotsCount=2 Degree=3 IsPeriodic=0
    g14: BSplineCurve PolesCount=4 KnotsCount=2 Degree=3 IsPeriodic=0
    g15: BSplineCurve PolesCount=4 KnotsCount=2 Degree=3 IsPeriodic=0
    g16: BSplineCurve PolesCount=4 KnotsCount=2 Degree=3 IsPeriodic=0
    g17: BSplineCurve PolesCount=4 KnotsCount=2 Degree=3 IsPeriodic=0
    g18: BSplineCurve PolesCount=4 KnotsCount=2 Degree=3 IsPeriodic=0
    g19: BSplineCurve PolesCount=4 KnotsCount=2 Degree=3 IsPeriodic=0
    g20: BSplineCurve PolesCount=4 KnotsCount=2 Degree=3 IsPeriodic=0
    g21: BSplineCurve PolesCount=4 KnotsCount=2 Degree=3 IsPeriodic=0
    g22: BSplineCurve PolesCount=4 KnotsCount=2 Degree=3 IsPeriodic=0
    g23: BSplineCurve PolesCount=4 KnotsCount=2 Degree=3 IsPeriodic=0
    g24: BSplineCurve PolesCount=4 KnotsCount=2 Degree=3 IsPeriodic=0
    g25: BSplineCurve PolesCount=4 KnotsCount=2 Degree=3 IsPeriodic=0
    g26: BSplineCurve PolesCount=2 KnotsCount=2 Degree=1 IsPeriodic=0
    g27: BSplineCurve PolesCount=2 KnotsCount=2 Degree=1 IsPeriodic=0
    g28: BSplineCurve PolesCount=4 KnotsCount=2 Degree=3 IsPeriodic=0
    g29: BSplineCurve PolesCount=4 KnotsCount=2 Degree=3 IsPeriodic=0
    g30: BSplineCurve PolesCount=4 KnotsCount=2 Degree=3 IsPeriodic=0
    g31: BSplineCurve PolesCount=4 KnotsCount=2 Degree=3 IsPeriodic=0
    g32: BSplineCurve PolesCount=4 KnotsCount=2 Degree=3 IsPeriodic=0
    g33: BSplineCurve PolesCount=4 KnotsCount=2 Degree=3 IsPeriodic=0
    g34: BSplineCurve PolesCount=4 KnotsCount=2 Degree=3 IsPeriodic=0
    g35: BSplineCurve PolesCount=4 KnotsCount=2 Degree=3 IsPeriodic=0
    g36: BSplineCurve PolesCount=4 KnotsCount=2 Degree=3 IsPeriodic=0
    g37: BSplineCurve PolesCount=4 KnotsCount=2 Degree=3 IsPeriodic=0
    g38: BSplineCurve PolesCount=4 KnotsCount=2 Degree=3 IsPeriodic=0
    g39: BSplineCurve PolesCount=4 KnotsCount=2 Degree=3 IsPeriodic=0
    g40: BSplineCurve PolesCount=4 KnotsCount=2 Degree=3 IsPeriodic=0
    g41: BSplineCurve PolesCount=4 KnotsCount=2 Degree=3 IsPeriodic=0
    g42: BSplineCurve PolesCount=4 KnotsCount=2 Degree=3 IsPeriodic=0
    g43: BSplineCurve PolesCount=4 KnotsCount=2 Degree=3 IsPeriodic=0
    g44: BSplineCurve PolesCount=4 KnotsCount=2 Degree=3 IsPeriodic=0
    g45: BSplineCurve PolesCount=4 KnotsCount=2 Degree=3 IsPeriodic=0
    g46: BSplineCurve PolesCount=4 KnotsCount=2 Degree=3 IsPeriodic=0
    g47: BSplineCurve PolesCount=4 KnotsCount=2 Degree=3 IsPeriodic=0
    g48: BSplineCurve PolesCount=4 KnotsCount=2 Degree=3 IsPeriodic=0
    g49: BSplineCurve PolesCount=4 KnotsCount=2 Degree=3 IsPeriodic=0
    g50: BSplineCurve PolesCount=4 KnotsCount=2 Degree=3 IsPeriodic=0
    g51: BSplineCurve PolesCount=4 KnotsCount=2 Degree=3 IsPeriodic=0
    g52: BSplineCurve PolesCount=4 KnotsCount=2 Degree=3 IsPeriodic=0
    g53: BSplineCurve PolesCount=4 KnotsCount=2 Degree=3 IsPeriodic=0
    g54: BSplineCurve PolesCount=4 KnotsCount=2 Degree=3 IsPeriodic=0
    g55: BSplineCurve PolesCount=4 KnotsCount=2 Degree=3 IsPeriodic=0
    g56: BSplineCurve PolesCount=4 KnotsCount=2 Degree=3 IsPeriodic=0
    g57: BSplineCurve PolesCount=2 KnotsCount=2 Degree=1 IsPeriodic=0
    g58: BSplineCurve PolesCount=2 KnotsCount=2 Degree=1 IsPeriodic=0
    g59: BSplineCurve PolesCount=4 KnotsCount=2 Degree=3 IsPeriodic=0
    g60: BSplineCurve PolesCount=4 KnotsCount=2 Degree=3 IsPeriodic=0
    g61: BSplineCurve PolesCount=4 KnotsCount=2 Degree=3 IsPeriodic=0
    g62: BSplineCurve PolesCount=4 KnotsCount=2 Degree=3 IsPeriodic=0
    g63: BSplineCurve PolesCount=4 KnotsCount=2 Degree=3 IsPeriodic=0
    g64: BSplineCurve PolesCount=4 KnotsCount=2 Degree=3 IsPeriodic=0
    g65: BSplineCurve PolesCount=4 KnotsCount=2 Degree=3 IsPeriodic=0
    g66: BSplineCurve PolesCount=4 KnotsCount=2 Degree=3 IsPeriodic=0
    g67: BSplineCurve PolesCount=4 KnotsCount=2 Degree=3 IsPeriodic=0
    g68: BSplineCurve PolesCount=4 KnotsCount=2 Degree=3 IsPeriodic=0
    g69: BSplineCurve PolesCount=4 KnotsCount=2 Degree=3 IsPeriodic=0
    g70: BSplineCurve PolesCount=4 KnotsCount=2 Degree=3 IsPeriodic=0
    g71: BSplineCurve PolesCount=4 KnotsCount=2 Degree=3 IsPeriodic=0
    g72: BSplineCurve PolesCount=4 KnotsCount=2 Degree=3 IsPeriodic=0
    g73: BSplineCurve PolesCount=4 KnotsCount=2 Degree=3 IsPeriodic=0
    g74: BSplineCurve PolesCount=4 KnotsCount=2 Degree=3 IsPeriodic=0
    g75: BSplineCurve PolesCount=2 KnotsCount=2 Degree=1 IsPeriodic=0
    g76: BSplineCurve PolesCount=2 KnotsCount=2 Degree=1 IsPeriodic=0
    g77: BSplineCurve PolesCount=4 KnotsCount=2 Degree=3 IsPeriodic=0
    g78: BSplineCurve PolesCount=4 KnotsCount=2 Degree=3 IsPeriodic=0
    g79: BSplineCurve PolesCount=4 KnotsCount=2 Degree=3 IsPeriodic=0
    g80: BSplineCurve PolesCount=4 KnotsCount=2 Degree=3 IsPeriodic=0
    g81: BSplineCurve PolesCount=4 KnotsCount=2 Degree=3 IsPeriodic=0
    g82: BSplineCurve PolesCount=4 KnotsCount=2 Degree=3 IsPeriodic=0
    g83: BSplineCurve PolesCount=4 KnotsCount=2 Degree=3 IsPeriodic=0
    g84: BSplineCurve PolesCount=4 KnotsCount=2 Degree=3 IsPeriodic=0
    g85: BSplineCurve PolesCount=4 KnotsCount=2 Degree=3 IsPeriodic=0
    g86: BSplineCurve PolesCount=2 KnotsCount=2 Degree=1 IsPeriodic=0
    g87: BSplineCurve PolesCount=2 KnotsCount=2 Degree=1 IsPeriodic=0
    g88: BSplineCurve PolesCount=4 KnotsCount=2 Degree=3 IsPeriodic=0
    g89: BSplineCurve PolesCount=4 KnotsCount=2 Degree=3 IsPeriodic=0
    g90: BSplineCurve PolesCount=4 KnotsCount=2 Degree=3 IsPeriodic=0
    g91: BSplineCurve PolesCount=4 KnotsCount=2 Degree=3 IsPeriodic=0
    g92: BSplineCurve PolesCount=4 KnotsCount=2 Degree=3 IsPeriodic=0
    g93: BSplineCurve PolesCount=4 KnotsCount=2 Degree=3 IsPeriodic=0
    g94: BSplineCurve PolesCount=4 KnotsCount=2 Degree=3 IsPeriodic=0
    g95: BSplineCurve PolesCount=4 KnotsCount=2 Degree=3 IsPeriodic=0
    g96: BSplineCurve PolesCount=4 KnotsCount=2 Degree=3 IsPeriodic=0
    g97: BSplineCurve PolesCount=4 KnotsCount=2 Degree=3 IsPeriodic=0
    g98: BSplineCurve PolesCount=4 KnotsCount=2 Degree=3 IsPeriodic=0
    g99: BSplineCurve PolesCount=4 KnotsCount=2 Degree=3 IsPeriodic=0
    g100: BSplineCurve PolesCount=4 KnotsCount=2 Degree=3 IsPeriodic=0
    g101: BSplineCurve PolesCount=4 KnotsCount=2 Degree=3 IsPeriodic=0
    g102: BSplineCurve PolesCount=4 KnotsCount=2 Degree=3 IsPeriodic=0
    g103: BSplineCurve PolesCount=4 KnotsCount=2 Degree=3 IsPeriodic=0
    g104: BSplineCurve PolesCount=4 KnotsCount=2 Degree=3 IsPeriodic=0
    g105: BSplineCurve PolesCount=4 KnotsCount=2 Degree=3 IsPeriodic=0
    g106: BSplineCurve PolesCount=4 KnotsCount=2 Degree=3 IsPeriodic=0
    g107: BSplineCurve PolesCount=4 KnotsCount=2 Degree=3 IsPeriodic=0
    g108: BSplineCurve PolesCount=4 KnotsCount=2 Degree=3 IsPeriodic=0
    g109: BSplineCurve PolesCount=4 KnotsCount=2 Degree=3 IsPeriodic=0
    g110: BSplineCurve PolesCount=4 KnotsCount=2 Degree=3 IsPeriodic=0
    g111: BSplineCurve PolesCount=4 KnotsCount=2 Degree=3 IsPeriodic=0
    g112: BSplineCurve PolesCount=4 KnotsCount=2 Degree=3 IsPeriodic=0
    g113: BSplineCurve PolesCount=4 KnotsCount=2 Degree=3 IsPeriodic=0
    g114: BSplineCurve PolesCount=4 KnotsCount=2 Degree=3 IsPeriodic=0
    g115: BSplineCurve PolesCount=4 KnotsCount=2 Degree=3 IsPeriodic=0
    g116: BSplineCurve PolesCount=4 KnotsCount=2 Degree=3 IsPeriodic=0
    g117: BSplineCurve PolesCount=4 KnotsCount=2 Degree=3 IsPeriodic=0
    g118: BSplineCurve PolesCount=4 KnotsCount=2 Degree=3 IsPeriodic=0
    g119: BSplineCurve PolesCount=4 KnotsCount=2 Degree=3 IsPeriodic=0
    g120: BSplineCurve PolesCount=4 KnotsCount=2 Degree=3 IsPeriodic=0
    g121: BSplineCurve PolesCount=4 KnotsCount=2 Degree=3 IsPeriodic=0
    g122: BSplineCurve PolesCount=2 KnotsCount=2 Degree=1 IsPeriodic=0
    g123: BSplineCurve PolesCount=2 KnotsCount=2 Degree=1 IsPeriodic=0
    g124: BSplineCurve PolesCount=4 KnotsCount=2 Degree=3 IsPeriodic=0
    g125: BSplineCurve PolesCount=2 KnotsCount=2 Degree=1 IsPeriodic=0
    g126: BSplineCurve PolesCount=2 KnotsCount=2 Degree=1 IsPeriodic=0
    g127: BSplineCurve PolesCount=4 KnotsCount=2 Degree=3 IsPeriodic=0
    g128: BSplineCurve PolesCount=4 KnotsCount=2 Degree=3 IsPeriodic=0
    g129: BSplineCurve PolesCount=4 KnotsCount=2 Degree=3 IsPeriodic=0
    g130: BSplineCurve PolesCount=4 KnotsCount=2 Degree=3 IsPeriodic=0
    g131: BSplineCurve PolesCount=4 KnotsCount=2 Degree=3 IsPeriodic=0
    g132: BSplineCurve PolesCount=4 KnotsCount=2 Degree=3 IsPeriodic=0
    g133: BSplineCurve PolesCount=4 KnotsCount=2 Degree=3 IsPeriodic=0
    g134: BSplineCurve PolesCount=4 KnotsCount=2 Degree=3 IsPeriodic=0
    g135: BSplineCurve PolesCount=4 KnotsCount=2 Degree=3 IsPeriodic=0
    g136: BSplineCurve PolesCount=4 KnotsCount=2 Degree=3 IsPeriodic=0
    g137: BSplineCurve PolesCount=4 KnotsCount=2 Degree=3 IsPeriodic=0
    g138: BSplineCurve PolesCount=2 KnotsCount=2 Degree=1 IsPeriodic=0
    g139: BSplineCurve PolesCount=2 KnotsCount=2 Degree=1 IsPeriodic=0
    g140: BSplineCurve PolesCount=2 KnotsCount=2 Degree=1 IsPeriodic=0
    g141: BSplineCurve PolesCount=2 KnotsCount=2 Degree=1 IsPeriodic=0
    g142: BSplineCurve PolesCount=4 KnotsCount=2 Degree=3 IsPeriodic=0
    g143: BSplineCurve PolesCount=4 KnotsCount=2 Degree=3 IsPeriodic=0
    g144: BSplineCurve PolesCount=2 KnotsCount=2 Degree=1 IsPeriodic=0
    g145: BSplineCurve PolesCount=2 KnotsCount=2 Degree=1 IsPeriodic=0
    g146: BSplineCurve PolesCount=4 KnotsCount=2 Degree=3 IsPeriodic=0
    g147: BSplineCurve PolesCount=4 KnotsCount=2 Degree=3 IsPeriodic=0
    g148: BSplineCurve PolesCount=4 KnotsCount=2 Degree=3 IsPeriodic=0
    g149: BSplineCurve PolesCount=4 KnotsCount=2 Degree=3 IsPeriodic=0
    g150: BSplineCurve PolesCount=4 KnotsCount=2 Degree=3 IsPeriodic=0
    g151: BSplineCurve PolesCount=2 KnotsCount=2 Degree=1 IsPeriodic=0
    g152: BSplineCurve PolesCount=2 KnotsCount=2 Degree=1 IsPeriodic=0
    g153: BSplineCurve PolesCount=4 KnotsCount=2 Degree=3 IsPeriodic=0
    g154: BSplineCurve PolesCount=4 KnotsCount=2 Degree=3 IsPeriodic=0
    g155: BSplineCurve PolesCount=4 KnotsCount=2 Degree=3 IsPeriodic=0
    g156: BSplineCurve PolesCount=4 KnotsCount=2 Degree=3 IsPeriodic=0
    g157: BSplineCurve PolesCount=4 KnotsCount=2 Degree=3 IsPeriodic=0
    g158: BSplineCurve PolesCount=4 KnotsCount=2 Degree=3 IsPeriodic=0
    g159: BSplineCurve PolesCount=4 KnotsCount=2 Degree=3 IsPeriodic=0
    g160: BSplineCurve PolesCount=2 KnotsCount=2 Degree=1 IsPeriodic=0
    g161: BSplineCurve PolesCount=2 KnotsCount=2 Degree=1 IsPeriodic=0
    g162: BSplineCurve PolesCount=4 KnotsCount=2 Degree=3 IsPeriodic=0
    g163: BSplineCurve PolesCount=4 KnotsCount=2 Degree=3 IsPeriodic=0
    g164: BSplineCurve PolesCount=4 KnotsCount=2 Degree=3 IsPeriodic=0
    g165: BSplineCurve PolesCount=4 KnotsCount=2 Degree=3 IsPeriodic=0
    g166: BSplineCurve PolesCount=2 KnotsCount=2 Degree=1 IsPeriodic=0
    g167: BSplineCurve PolesCount=4 KnotsCount=2 Degree=3 IsPeriodic=0
    g168: BSplineCurve PolesCount=4 KnotsCount=2 Degree=3 IsPeriodic=0
    g169: BSplineCurve PolesCount=4 KnotsCount=2 Degree=3 IsPeriodic=0
    g170: BSplineCurve PolesCount=4 KnotsCount=2 Degree=3 IsPeriodic=0
    g171: BSplineCurve PolesCount=4 KnotsCount=2 Degree=3 IsPeriodic=0
    g172: BSplineCurve PolesCount=4 KnotsCount=2 Degree=3 IsPeriodic=0
    g173: BSplineCurve PolesCount=2 KnotsCount=2 Degree=1 IsPeriodic=0
    g174: BSplineCurve PolesCount=4 KnotsCount=2 Degree=3 IsPeriodic=0
    g175: BSplineCurve PolesCount=4 KnotsCount=2 Degree=3 IsPeriodic=0
    g176: BSplineCurve PolesCount=4 KnotsCount=2 Degree=3 IsPeriodic=0
    g177: BSplineCurve PolesCount=4 KnotsCount=2 Degree=3 IsPeriodic=0
    g178: BSplineCurve PolesCount=4 KnotsCount=2 Degree=3 IsPeriodic=0
    g179: BSplineCurve PolesCount=4 KnotsCount=2 Degree=3 IsPeriodic=0
    g180: BSplineCurve PolesCount=2 KnotsCount=2 Degree=1 IsPeriodic=0
    g181: BSplineCurve PolesCount=2 KnotsCount=2 Degree=1 IsPeriodic=0
    g182: BSplineCurve PolesCount=4 KnotsCount=2 Degree=3 IsPeriodic=0
    g183: BSplineCurve PolesCount=4 KnotsCount=2 Degree=3 IsPeriodic=0
    g184: BSplineCurve PolesCount=4 KnotsCount=2 Degree=3 IsPeriodic=0
    g185: BSplineCurve PolesCount=4 KnotsCount=2 Degree=3 IsPeriodic=0
    g186: BSplineCurve PolesCount=4 KnotsCount=2 Degree=3 IsPeriodic=0
    g187: BSplineCurve PolesCount=4 KnotsCount=2 Degree=3 IsPeriodic=0
    g188: BSplineCurve PolesCount=4 KnotsCount=2 Degree=3 IsPeriodic=0
    g189: BSplineCurve PolesCount=4 KnotsCount=2 Degree=3 IsPeriodic=0
    g190: BSplineCurve PolesCount=4 KnotsCount=2 Degree=3 IsPeriodic=0
    g191: BSplineCurve PolesCount=4 KnotsCount=2 Degree=3 IsPeriodic=0
    g192: BSplineCurve PolesCount=4 KnotsCount=2 Degree=3 IsPeriodic=0
    g193: BSplineCurve PolesCount=4 KnotsCount=2 Degree=3 IsPeriodic=0
    g194: BSplineCurve PolesCount=4 KnotsCount=2 Degree=3 IsPeriodic=0
    g195: BSplineCurve PolesCount=4 KnotsCount=2 Degree=3 IsPeriodic=0
    g196: BSplineCurve PolesCount=4 KnotsCount=2 Degree=3 IsPeriodic=0
    g197: BSplineCurve PolesCount=4 KnotsCount=2 Degree=3 IsPeriodic=0
    g198: BSplineCurve PolesCount=4 KnotsCount=2 Degree=3 IsPeriodic=0
    g199: BSplineCurve PolesCount=4 KnotsCount=2 Degree=3 IsPeriodic=0
    g200: BSplineCurve PolesCount=4 KnotsCount=2 Degree=3 IsPeriodic=0
    g201: BSplineCurve PolesCount=4 KnotsCount=2 Degree=3 IsPeriodic=0
    g202: BSplineCurve PolesCount=4 KnotsCount=2 Degree=3 IsPeriodic=0
    g203: BSplineCurve PolesCount=2 KnotsCount=2 Degree=1 IsPeriodic=0
    g204: BSplineCurve PolesCount=2 KnotsCount=2 Degree=1 IsPeriodic=0
    g205: BSplineCurve PolesCount=4 KnotsCount=2 Degree=3 IsPeriodic=0
    g206: BSplineCurve PolesCount=4 KnotsCount=2 Degree=3 IsPeriodic=0
    g207: BSplineCurve PolesCount=4 KnotsCount=2 Degree=3 IsPeriodic=0
    g208: BSplineCurve PolesCount=4 KnotsCount=2 Degree=3 IsPeriodic=0
    g209: BSplineCurve PolesCount=2 KnotsCount=2 Degree=1 IsPeriodic=0
    g210: BSplineCurve PolesCount=2 KnotsCount=2 Degree=1 IsPeriodic=0
    g211: BSplineCurve PolesCount=4 KnotsCount=2 Degree=3 IsPeriodic=0
    g212: BSplineCurve PolesCount=4 KnotsCount=2 Degree=3 IsPeriodic=0
    g213: BSplineCurve PolesCount=4 KnotsCount=2 Degree=3 IsPeriodic=0
    g214: BSplineCurve PolesCount=4 KnotsCount=2 Degree=3 IsPeriodic=0
    g215: BSplineCurve PolesCount=4 KnotsCount=2 Degree=3 IsPeriodic=0
    g216: BSplineCurve PolesCount=4 KnotsCount=2 Degree=3 IsPeriodic=0
    g217: BSplineCurve PolesCount=2 KnotsCount=2 Degree=1 IsPeriodic=0
    g218: BSplineCurve PolesCount=2 KnotsCount=2 Degree=1 IsPeriodic=0
    g219: BSplineCurve PolesCount=4 KnotsCount=2 Degree=3 IsPeriodic=0
    g220: BSplineCurve PolesCount=4 KnotsCount=2 Degree=3 IsPeriodic=0
    g221: BSplineCurve PolesCount=4 KnotsCount=2 Degree=3 IsPeriodic=0
    g222: BSplineCurve PolesCount=4 KnotsCount=2 Degree=3 IsPeriodic=0
    g223: BSplineCurve PolesCount=2 KnotsCount=2 Degree=1 IsPeriodic=0
    g224: BSplineCurve PolesCount=2 KnotsCount=2 Degree=1 IsPeriodic=0
    g225: BSplineCurve PolesCount=4 KnotsCount=2 Degree=3 IsPeriodic=0
    g226: BSplineCurve PolesCount=4 KnotsCount=2 Degree=3 IsPeriodic=0
    g227: BSplineCurve PolesCount=4 KnotsCount=2 Degree=3 IsPeriodic=0
    g228: BSplineCurve PolesCount=4 KnotsCount=2 Degree=3 IsPeriodic=0
    g229: BSplineCurve PolesCount=4 KnotsCount=2 Degree=3 IsPeriodic=0
    g230: BSplineCurve PolesCount=4 KnotsCount=2 Degree=3 IsPeriodic=0
    g231: BSplineCurve PolesCount=4 KnotsCount=2 Degree=3 IsPeriodic=0
    g232: BSplineCurve PolesCount=4 KnotsCount=2 Degree=3 IsPeriodic=0
    g233: BSplineCurve PolesCount=2 KnotsCount=2 Degree=1 IsPeriodic=0
    g234: BSplineCurve PolesCount=2 KnotsCount=2 Degree=1 IsPeriodic=0
    g235: BSplineCurve PolesCount=4 KnotsCount=2 Degree=3 IsPeriodic=0
    g236: BSplineCurve PolesCount=4 KnotsCount=2 Degree=3 IsPeriodic=0
    g237: BSplineCurve PolesCount=2 KnotsCount=2 Degree=1 IsPeriodic=0
    g238: BSplineCurve PolesCount=2 KnotsCount=2 Degree=1 IsPeriodic=0
    g239: BSplineCurve PolesCount=4 KnotsCount=2 Degree=3 IsPeriodic=0
    g240: BSplineCurve PolesCount=4 KnotsCount=2 Degree=3 IsPeriodic=0
    g241: BSplineCurve PolesCount=4 KnotsCount=2 Degree=3 IsPeriodic=0
    g242: BSplineCurve PolesCount=2 KnotsCount=2 Degree=1 IsPeriodic=0
    g243: BSplineCurve PolesCount=2 KnotsCount=2 Degree=1 IsPeriodic=0
    g244: BSplineCurve PolesCount=4 KnotsCount=2 Degree=3 IsPeriodic=0
    g245: BSplineCurve PolesCount=4 KnotsCount=2 Degree=3 IsPeriodic=0
    g246: BSplineCurve PolesCount=4 KnotsCount=2 Degree=3 IsPeriodic=0
    g247: BSplineCurve PolesCount=2 KnotsCount=2 Degree=1 IsPeriodic=0
    g248: BSplineCurve PolesCount=2 KnotsCount=2 Degree=1 IsPeriodic=0
    g249: BSplineCurve PolesCount=4 KnotsCount=2 Degree=3 IsPeriodic=0
    g250: BSplineCurve PolesCount=4 KnotsCount=2 Degree=3 IsPeriodic=0
    g251: BSplineCurve PolesCount=4 KnotsCount=2 Degree=3 IsPeriodic=0
    g252: BSplineCurve PolesCount=4 KnotsCount=2 Degree=3 IsPeriodic=0
    g253: BSplineCurve PolesCount=4 KnotsCount=2 Degree=3 IsPeriodic=0
    g254: BSplineCurve PolesCount=4 KnotsCount=2 Degree=3 IsPeriodic=0
    g255: BSplineCurve PolesCount=4 KnotsCount=2 Degree=3 IsPeriodic=0
    g256: BSplineCurve PolesCount=4 KnotsCount=2 Degree=3 IsPeriodic=0
    g257: BSplineCurve PolesCount=4 KnotsCount=2 Degree=3 IsPeriodic=0
    g258: BSplineCurve PolesCount=4 KnotsCount=2 Degree=3 IsPeriodic=0
    g259: BSplineCurve PolesCount=4 KnotsCount=2 Degree=3 IsPeriodic=0
    g260: BSplineCurve PolesCount=2 KnotsCount=2 Degree=1 IsPeriodic=0
    g261: BSplineCurve PolesCount=2 KnotsCount=2 Degree=1 IsPeriodic=0
    g262: BSplineCurve PolesCount=4 KnotsCount=2 Degree=3 IsPeriodic=0
    g263: BSplineCurve PolesCount=2 KnotsCount=2 Degree=1 IsPeriodic=0
    g264: BSplineCurve PolesCount=2 KnotsCount=2 Degree=1 IsPeriodic=0
    g265: BSplineCurve PolesCount=4 KnotsCount=2 Degree=3 IsPeriodic=0
    g266: BSplineCurve PolesCount=4 KnotsCount=2 Degree=3 IsPeriodic=0
    g267: BSplineCurve PolesCount=4 KnotsCount=2 Degree=3 IsPeriodic=0
    g268: BSplineCurve PolesCount=4 KnotsCount=2 Degree=3 IsPeriodic=0
    g269: BSplineCurve PolesCount=4 KnotsCount=2 Degree=3 IsPeriodic=0
    g270: BSplineCurve PolesCount=4 KnotsCount=2 Degree=3 IsPeriodic=0
    g271: BSplineCurve PolesCount=4 KnotsCount=2 Degree=3 IsPeriodic=0
    g272: BSplineCurve PolesCount=4 KnotsCount=2 Degree=3 IsPeriodic=0
    g273: BSplineCurve PolesCount=4 KnotsCount=2 Degree=3 IsPeriodic=0
    g274: BSplineCurve PolesCount=4 KnotsCount=2 Degree=3 IsPeriodic=0
    g275: BSplineCurve PolesCount=2 KnotsCount=2 Degree=1 IsPeriodic=0
    g276: BSplineCurve PolesCount=2 KnotsCount=2 Degree=1 IsPeriodic=0
    g277: BSplineCurve PolesCount=4 KnotsCount=2 Degree=3 IsPeriodic=0
    g278: BSplineCurve PolesCount=4 KnotsCount=2 Degree=3 IsPeriodic=0
    g279: BSplineCurve PolesCount=4 KnotsCount=2 Degree=3 IsPeriodic=0
    g280: BSplineCurve PolesCount=2 KnotsCount=2 Degree=1 IsPeriodic=0
    g281: BSplineCurve PolesCount=2 KnotsCount=2 Degree=1 IsPeriodic=0
    g282: BSplineCurve PolesCount=4 KnotsCount=2 Degree=3 IsPeriodic=0
    g283: BSplineCurve PolesCount=4 KnotsCount=2 Degree=3 IsPeriodic=0
    g284: BSplineCurve PolesCount=4 KnotsCount=2 Degree=3 IsPeriodic=0
    g285: BSplineCurve PolesCount=4 KnotsCount=2 Degree=3 IsPeriodic=0
    g286: BSplineCurve PolesCount=4 KnotsCount=2 Degree=3 IsPeriodic=0
    g287: BSplineCurve PolesCount=4 KnotsCount=2 Degree=3 IsPeriodic=0
    g288: BSplineCurve PolesCount=4 KnotsCount=2 Degree=3 IsPeriodic=0
    g289: BSplineCurve PolesCount=4 KnotsCount=2 Degree=3 IsPeriodic=0
    g290: BSplineCurve PolesCount=4 KnotsCount=2 Degree=3 IsPeriodic=0
    g291: BSplineCurve PolesCount=4 KnotsCount=2 Degree=3 IsPeriodic=0
    g292: BSplineCurve PolesCount=4 KnotsCount=2 Degree=3 IsPeriodic=0
    g293: BSplineCurve PolesCount=4 KnotsCount=2 Degree=3 IsPeriodic=0
    g294: BSplineCurve PolesCount=4 KnotsCount=2 Degree=3 IsPeriodic=0
    g295: BSplineCurve PolesCount=4 KnotsCount=2 Degree=3 IsPeriodic=0
    g296: BSplineCurve PolesCount=4 KnotsCount=2 Degree=3 IsPeriodic=0
    g297: BSplineCurve PolesCount=4 KnotsCount=2 Degree=3 IsPeriodic=0
    g298: BSplineCurve PolesCount=2 KnotsCount=2 Degree=1 IsPeriodic=0
    g299: BSplineCurve PolesCount=2 KnotsCount=2 Degree=1 IsPeriodic=0
    g300: BSplineCurve PolesCount=4 KnotsCount=2 Degree=3 IsPeriodic=0
    g301: BSplineCurve PolesCount=2 KnotsCount=2 Degree=1 IsPeriodic=0
    g302: BSplineCurve PolesCount=2 KnotsCount=2 Degree=1 IsPeriodic=0
    g303: BSplineCurve PolesCount=4 KnotsCount=2 Degree=3 IsPeriodic=0
    g304: BSplineCurve PolesCount=4 KnotsCount=2 Degree=3 IsPeriodic=0
    g305: BSplineCurve PolesCount=4 KnotsCount=2 Degree=3 IsPeriodic=0
    g306: BSplineCurve PolesCount=4 KnotsCount=2 Degree=3 IsPeriodic=0
    g307: BSplineCurve PolesCount=4 KnotsCount=2 Degree=3 IsPeriodic=0
    g308: BSplineCurve PolesCount=4 KnotsCount=2 Degree=3 IsPeriodic=0
    g309: BSplineCurve PolesCount=4 KnotsCount=2 Degree=3 IsPeriodic=0
    g310: BSplineCurve PolesCount=4 KnotsCount=2 Degree=3 IsPeriodic=0
    g311: BSplineCurve PolesCount=4 KnotsCount=2 Degree=3 IsPeriodic=0
    g312: BSplineCurve PolesCount=4 KnotsCount=2 Degree=3 IsPeriodic=0
  constraints (313):
    c: Coincident(g0,g1)
    c: Coincident(g1,g2)
    c: Coincident(g2,g3)
    c: Coincident(g3,g4)
    c: Coincident(g4,g5)
    c: Coincident(g5,g6)
    c: Coincident(g6,g7)
    c: Coincident(g7,g8)
    c: Coincident(g8,g9)
    c: Coincident(g9,g10)
    c: Coincident(g10,g11)
    c: Coincident(g11,g12)
    c: Coincident(g12,g13)
    c: Coincident(g13,g14)
    c: Coincident(g14,g15)
    c: Coincident(g15,g16)
    c: Coincident(g16,g17)
    c: Coincident(g17,g18)
    c: Coincident(g18,g19)
    c: Coincident(g19,g20)
    c: Coincident(g20,g21)
    c: Coincident(g21,g22)
    c: Coincident(g22,g23)
    c: Coincident(g23,g24)
    c: Coincident(g24,g25)
    c: Coincident(g25,g26)
    c: Coincident(g26,g27)
    c: Coincident(g27,g28)
    c: Coincident(g28,g29)
    c: Coincident(g29,g30)
    c: Coincident(g30,g31)
    c: Coincident(g31,g32)
    c: Coincident(g32,g33)
    c: Coincident(g33,g34)
    c: Coincident(g34,g35)
    c: Coincident(g35,g36)
    c: Coincident(g36,g37)
    c: Coincident(g37,g38)
    c: Coincident(g38,g39)
    c: Coincident(g39,g40)
    c: Coincident(g40,g41)
    c: Coincident(g41,g42)
    c: Coincident(g42,g43)
    c: Coincident(g43,g44)
    c: Coincident(g44,g45)
    c: Coincident(g45,g46)
    c: Coincident(g46,g47)
    c: Coincident(g47,g48)
    c: Coincident(g48,g49)
    c: Coincident(g49,g50)
    c: Coincident(g50,g51)
    c: Coincident(g51,g52)
    c: Coincident(g52,g53)
    c: Coincident(g53,g54)
    c: Coincident(g54,g55)
    c: Coincident(g55,g56)
    c: Coincident(g56,g57)
    c: Coincident(g57,g58)
    c: Coincident(g58,g59)
    c: Coincident(g59,g60)
    c: Coincident(g60,g61)
    c: Coincident(g61,g62)
    c: Coincident(g62,g63)
    c: Coincident(g63,g64)
    c: Coincident(g64,g65)
    c: Coincident(g65,g66)
    c: Coincident(g67,g68)
    c: Coincident(g68,g69)
    c: Coincident(g69,g70)
    c: Coincident(g70,g71)
    c: Coincident(g71,g67)
    c: Coincident(g72,g73)
    c: Coincident(g73,g74)
    c: Coincident(g74,g75)
    c: Coincident(g75,g76)
    c: Coincident(g76,g77)
    c: Coincident(g77,g72)
    c: Coincident(g78,g79)
    c: Coincident(g79,g80)
    c: Coincident(g80,g81)
    c: Coincident(g81,g82)
    c: Coincident(g82,g83)
    c: Coincident(g83,g78)
    c: Coincident(g84,g85)
    c: Coincident(g85,g86)
    c: Coincident(g86,g87)
    c: Coincident(g87,g88)
    c: Coincident(g88,g89)
    c: Coincident(g90,g91)
    c: Coincident(g91,g92)
    c: Coincident(g92,g93)
    c: Coincident(g93,g94)
    c: Coincident(g94,g95)
    c: Coincident(g95,g90)
    c: Coincident(g96,g97)
    c: Coincident(g97,g98)
    c: Coincident(g98,g99)
    c: Coincident(g99,g100)
    c: Coincident(g100,g101)
    c: Coincident(g101,g96)
    c: Coincident(g102,g103)
    c: Coincident(g103,g104)
    c: Coincident(g104,g105)
    c: Coincident(g105,g106)
    c: Coincident(g107,g108)
    c: Coincident(g108,g109)
    c: Coincident(g109,g110)
    c: Coincident(g110,g111)
    c: Coincident(g111,g112)
    c: Coincident(g112,g113)
    c: Coincident(g113,g114)
    c: Coincident(g114,g115)
    c: Coincident(g115,g107)
    c: Coincident(g116,g117)
    c: Coincident(g117,g118)
    c: Coincident(g118,g119)
    c: Coincident(g119,g120)
    c: Coincident(g120,g121)
    c: Coincident(g121,g122)
    c: Coincident(g122,g123)
    c: Coincident(g123,g124)
    c: Coincident(g124,g125)
    c: Coincident(g125,g126)
    c: Coincident(g126,g127)
    c: Coincident(g127,g128)
    c: Coincident(g128,g129)
    c: Coincident(g129,g130)
    c: Coincident(g131,g132)
    c: Coincident(g132,g133)
    c: Coincident(g133,g134)
    c: Coincident(g134,g135)
    c: Coincident(g136,g137)
    c: Coincident(g137,g138)
    c: Coincident(g138,g139)
    c: Coincident(g139,g140)
    c: Coincident(g140,g141)
    c: Coincident(g141,g142)
    c: Coincident(g142,g143)
    c: Coincident(g143,g144)
    c: Coincident(g144,g145)
    c: Coincident(g145,g136)
    c: Coincident(g146,g147)
    c: Coincident(g147,g148)
    c: Coincident(g148,g149)
    c: Coincident(g149,g150)
    c: Coincident(g150,g151)
    c: Coincident(g151,g152)
    c: Coincident(g152,g153)
    c: Coincident(g153,g146)
    c: Coincident(g154,g155)
    c: Coincident(g155,g156)
    c: Coincident(g157,g158)
    c: Coincident(g158,g159)
    c: Coincident(g159,g160)
    c: Coincident(g160,g161)
    c: Coincident(g161,g157)
    c: Coincident(g162,g163)
    c: Coincident(g163,g164)
    c: Coincident(g164,g165)
    c: Coincident(g165,g162)
    c: Coincident(g166,g167)
    c: Coincident(g167,g168)
    c: Coincident(g168,g169)
    c: Coincident(g169,g170)
    c: Coincident(g170,g171)
    c: Coincident(g171,g172)
    c: Coincident(g172,g173)
    c: Coincident(g173,g166)
    c: Coincident(g174,g175)
    c: Coincident(g175,g176)
    c: Coincident(g176,g177)
    c: Coincident(g177,g178)
    c: Coincident(g178,g179)
    c: Coincident(g179,g180)
    c: Coincident(g180,g181)
    c: Coincident(g181,g174)
    c: Coincident(g182,g183)
    c: Coincident(g183,g184)
    c: Coincident(g184,g185)
    c: Coincident(g185,g186)
    c: Coincident(g186,g187)
    c: Coincident(g187,g188)
    c: Coincident(g188,g182)
    c: Coincident(g189,g190)
    c: Coincident(g190,g191)
    c: Coincident(g191,g192)
    c: Coincident(g192,g193)
    c: Coincident(g193,g194)
    c: Coincident(g194,g195)
    c: Coincident(g195,g196)
    c: Coincident(g196,g189)
    c: Coincident(g197,g198)
    c: Coincident(g198,g199)
    c: Coincident(g199,g200)
    c: Coincident(g200,g201)
    c: Coincident(g201,g202)
    c: Coincident(g202,g203)
    c: Coincident(g203,g204)
    c: Coincident(g204,g197)
    c: Coincident(g205,g206)
    c: Coincident(g206,g207)
    c: Coincident(g207,g205)
    c: Coincident(g208,g209)
    c: Coincident(g209,g210)
    c: Coincident(g210,g211)
    c: Coincident(g211,g212)
    c: Coincident(g212,g208)
    c: Coincident(g213,g214)
    c: Coincident(g214,g215)
    c: Coincident(g215,g216)
    c: Coincident(g216,g217)
    c: Coincident(g217,g218)
    c: Coincident(g218,g219)
    c: Coincident(g219,g213)
    c: Coincident(g220,g221)
    c: Coincident(g221,g222)
    c: Coincident(g222,g223)
    c: Coincident(g223,g224)
    c: Coincident(g224,g220)
    c: Coincident(g225,g226)
    c: Coincident(g226,g227)
    c: Coincident(g227,g225)
    c: Coincident(g228,g229)
    c: Coincident(g229,g230)
    c: Coincident(g230,g231)
    c: Coincident(g231,g232)
    c: Coincident(g232,g233)
    c: Coincident(g233,g234)
    c: Coincident(g234,g228)
    c: Coincident(g235,g236)
    c: Coincident(g236,g237)
    c: Coincident(g237,g238)
    c: Coincident(g238,g239)
    c: Coincident(g239,g235)
    c: Coincident(g240,g241)
    c: Coincident(g241,g242)
    c: Coincident(g242,g243)
    c: Coincident(g243,g244)
    c: Coincident(g245,g246)
    c: Coincident(g246,g247)
    c: Coincident(g247,g248)
    c: Coincident(g248,g249)
    c: Coincident(g249,g245)
    c: Coincident(g250,g251)
    c: Coincident(g251,g252)
    c: Coincident(g252,g250)
    c: Coincident(g253,g254)
    c: Coincident(g254,g255)
    c: Coincident(g255,g256)
    c: Coincident(g256,g257)
    c: Coincident(g257,g258)
    c: Coincident(g258,g253)
    c: Coincident(g259,g260)
    c: Coincident(g260,g261)
    c: Coincident(g261,g262)
    c: Coincident(g262,g263)
    c: Coincident(g263,g264)
    c: Coincident(g264,g259)
    c: Coincident(g265,g266)
    c: Coincident(g266,g267)
    c: Coincident(g267,g268)
    c: Coincident(g268,g265)
    c: Coincident(g269,g270)
    c: Coincident(g270,g271)
    c: Coincident(g271,g272)
    c: Coincident(g272,g273)
    c: Coincident(g273,g274)
    c: Coincident(g274,g275)
    c: Coincident(g275,g276)
    c: Coincident(g276,g277)
    c: Coincident(g277,g278)
    c: Coincident(g278,g269)
    c: Coincident(g279,g280)
    c: Coincident(g280,g281)
    c: Coincident(g281,g282)
    c: Coincident(g282,g283)
    c: Coincident(g283,g279)
    c: Coincident(g285,g286)
    c: Coincident(g286,g287)
    c: Coincident(g287,g284)
    c: Coincident(g288,g289)
    c: Coincident(g289,g290)
    c: Coincident(g290,g288)
    c: Coincident(g291,g292)
    c: Coincident(g292,g293)
    c: Coincident(g293,g294)
    c: Coincident(g294,g291)
    c: Coincident(g295,g296)
    c: Coincident(g296,g297)
    c: Coincident(g297,g295)
    c: Coincident(g298,g299)
    c: Coincident(g299,g300)
    c: Coincident(g300,g301)
    c: Coincident(g301,g302)
    c: Coincident(g302,g303)
    c: Coincident(g303,g304)
    c: Coincident(g304,g305)
    c: Coincident(g306,g307)
    c: Coincident(g307,g308)
    c: Coincident(g308,g309)
    c: Coincident(g309,g310)
    c: Coincident(g310,g311)
    c: Coincident(g311,g312)
    c: Coincident(g66,g0)
    c: Coincident(g284,g285)
    c: Coincident(g154,g156)
    c: Coincident(g306,g312)
    c: Coincident(g116,g130)
    c: Coincident(g298,g305)
    c: Coincident(g131,g135)
    c: Coincident(g84,g89)
    c: Coincident(g240,g244)
    c: Coincident(g102,g106)
FEATURE [Sketcher::SketchObject] Sketch047  label="Sweetheart-Sketch"
  ArcFitTolerance = 1e-06
  FullyConstrained = false
  MakeInternals = false
  Placement = pos=(-15.2224,12.9671,0) rot=(0,0,1;0rad)
  expr: .Placement.Base.x = -(.Shape.BoundBox.XLength / 2)
  expr: .Placement.Base.y = .Shape.BoundBox.YLength / 2
  sketch-geometry (138):
    g0: BSplineCurve PolesCount=4 KnotsCount=2 Degree=3 IsPeriodic=0
    g1: BSplineCurve PolesCount=4 KnotsCount=2 Degree=3 IsPeriodic=0
    g2: BSplineCurve PolesCount=4 KnotsCount=2 Degree=3 IsPeriodic=0
    g3: BSplineCurve PolesCount=4 KnotsCount=2 Degree=3 IsPeriodic=0
    g4: BSplineCurve PolesCount=4 KnotsCount=2 Degree=3 IsPeriodic=0
    g5: BSplineCurve PolesCount=4 KnotsCount=2 Degree=3 IsPeriodic=0
    g6: BSplineCurve PolesCount=4 KnotsCount=2 Degree=3 IsPeriodic=0
    g7: BSplineCurve PolesCount=4 KnotsCount=2 Degree=3 IsPeriodic=0
    g8: BSplineCurve PolesCount=4 KnotsCount=2 Degree=3 IsPeriodic=0
    g9: BSplineCurve PolesCount=4 KnotsCount=2 Degree=3 IsPeriodic=0
    g10: BSplineCurve PolesCount=4 KnotsCount=2 Degree=3 IsPeriodic=0
    g11: BSplineCurve PolesCount=4 KnotsCount=2 Degree=3 IsPeriodic=0
    g12: BSplineCurve PolesCount=4 KnotsCount=2 Degree=3 IsPeriodic=0
    g13: BSplineCurve PolesCount=4 KnotsCount=2 Degree=3 IsPeriodic=0
    g14: BSplineCurve PolesCount=4 KnotsCount=2 Degree=3 IsPeriodic=0
    g15: BSplineCurve PolesCount=4 KnotsCount=2 Degree=3 IsPeriodic=0
    g16: BSplineCurve PolesCount=4 KnotsCount=2 Degree=3 IsPeriodic=0
    g17: BSplineCurve PolesCount=2 KnotsCount=2 Degree=1 IsPeriodic=0
    g18: BSplineCurve PolesCount=4 KnotsCount=2 Degree=3 IsPeriodic=0
    g19: BSplineCurve PolesCount=4 KnotsCount=2 Degree=3 IsPeriodic=0
    g20: BSplineCurve PolesCount=4 KnotsCount=2 Degree=3 IsPeriodic=0
    g21: BSplineCurve PolesCount=4 KnotsCount=2 Degree=3 IsPeriodic=0
    g22: BSplineCurve PolesCount=4 KnotsCount=2 Degree=3 IsPeriodic=0
    g23: BSplineCurve PolesCount=4 KnotsCount=2 Degree=3 IsPeriodic=0
    g24: BSplineCurve PolesCount=4 KnotsCount=2 Degree=3 IsPeriodic=0
    g25: BSplineCurve PolesCount=4 KnotsCount=2 Degree=3 IsPeriodic=0
    g26: BSplineCurve PolesCount=4 KnotsCount=2 Degree=3 IsPeriodic=0
    g27: BSplineCurve PolesCount=4 KnotsCount=2 Degree=3 IsPeriodic=0
    g28: BSplineCurve PolesCount=4 KnotsCount=2 Degree=3 IsPeriodic=0
    g29: BSplineCurve PolesCount=4 KnotsCount=2 Degree=3 IsPeriodic=0
    g30: BSplineCurve PolesCount=4 KnotsCount=2 Degree=3 IsPeriodic=0
    g31: BSplineCurve PolesCount=2 KnotsCount=2 Degree=1 IsPeriodic=0
    g32: BSplineCurve PolesCount=2 KnotsCount=2 Degree=1 IsPeriodic=0
    g33: BSplineCurve PolesCount=4 KnotsCount=2 Degree=3 IsPeriodic=0
    g34: BSplineCurve PolesCount=2 KnotsCount=2 Degree=1 IsPeriodic=0
    g35: BSplineCurve PolesCount=4 KnotsCount=2 Degree=3 IsPeriodic=0
    g36: BSplineCurve PolesCount=4 KnotsCount=2 Degree=3 IsPeriodic=0
    g37: BSplineCurve PolesCount=2 KnotsCount=2 Degree=1 IsPeriodic=0
    g38: BSplineCurve PolesCount=2 KnotsCount=2 Degree=1 IsPeriodic=0
    g39: BSplineCurve PolesCount=4 KnotsCount=2 Degree=3 IsPeriodic=0
    g40: BSplineCurve PolesCount=4 KnotsCount=2 Degree=3 IsPeriodic=0
    g41: BSplineCurve PolesCount=4 KnotsCount=2 Degree=3 IsPeriodic=0
    g42: BSplineCurve PolesCount=4 KnotsCount=2 Degree=3 IsPeriodic=0
    g43: BSplineCurve PolesCount=4 KnotsCount=2 Degree=3 IsPeriodic=0
    g44: BSplineCurve PolesCount=4 KnotsCount=2 Degree=3 IsPeriodic=0
    g45: BSplineCurve PolesCount=2 KnotsCount=2 Degree=1 IsPeriodic=0
    g46: BSplineCurve PolesCount=2 KnotsCount=2 Degree=1 IsPeriodic=0
    g47: BSplineCurve PolesCount=4 KnotsCount=2 Degree=3 IsPeriodic=0
    g48: BSplineCurve PolesCount=4 KnotsCount=2 Degree=3 IsPeriodic=0
    g49: BSplineCurve PolesCount=2 KnotsCount=2 Degree=1 IsPeriodic=0
    g50: BSplineCurve PolesCount=2 KnotsCount=2 Degree=1 IsPeriodic=0
    g51: BSplineCurve PolesCount=4 KnotsCount=2 Degree=3 IsPeriodic=0
    g52: BSplineCurve PolesCount=4 KnotsCount=2 Degree=3 IsPeriodic=0
    g53: BSplineCurve PolesCount=4 KnotsCount=2 Degree=3 IsPeriodic=0
    g54: BSplineCurve PolesCount=4 KnotsCount=2 Degree=3 IsPeriodic=0
    g55: BSplineCurve PolesCount=4 KnotsCount=2 Degree=3 IsPeriodic=0
    g56: BSplineCurve PolesCount=4 KnotsCount=2 Degree=3 IsPeriodic=0
    g57: BSplineCurve PolesCount=4 KnotsCount=2 Degree=3 IsPeriodic=0
    g58: BSplineCurve PolesCount=4 KnotsCount=2 Degree=3 IsPeriodic=0
    g59: BSplineCurve PolesCount=4 KnotsCount=2 Degree=3 IsPeriodic=0
    g60: BSplineCurve PolesCount=4 KnotsCount=2 Degree=3 IsPeriodic=0
    g61: BSplineCurve PolesCount=4 KnotsCount=2 Degree=3 IsPeriodic=0
    g62: BSplineCurve PolesCount=4 KnotsCount=2 Degree=3 IsPeriodic=0
    g63: BSplineCurve PolesCount=4 KnotsCount=2 Degree=3 IsPeriodic=0
    g64: BSplineCurve PolesCount=4 KnotsCount=2 Degree=3 IsPeriodic=0
    g65: BSplineCurve PolesCount=4 KnotsCount=2 Degree=3 IsPeriodic=0
    g66: BSplineCurve PolesCount=4 KnotsCount=2 Degree=3 IsPeriodic=0
    g67: BSplineCurve PolesCount=4 KnotsCount=2 Degree=3 IsPeriodic=0
    g68: BSplineCurve PolesCount=4 KnotsCount=2 Degree=3 IsPeriodic=0
    g69: BSplineCurve PolesCount=4 KnotsCount=2 Degree=3 IsPeriodic=0
    g70: BSplineCurve PolesCount=4 KnotsCount=2 Degree=3 IsPeriodic=0
    g71: BSplineCurve PolesCount=4 KnotsCount=2 Degree=3 IsPeriodic=0
    g72: BSplineCurve PolesCount=4 KnotsCount=2 Degree=3 IsPeriodic=0
    g73: BSplineCurve PolesCount=4 KnotsCount=2 Degree=3 IsPeriodic=0
    g74: BSplineCurve PolesCount=4 KnotsCount=2 Degree=3 IsPeriodic=0
    g75: BSplineCurve PolesCount=4 KnotsCount=2 Degree=3 IsPeriodic=0
    g76: BSplineCurve PolesCount=4 KnotsCount=2 Degree=3 IsPeriodic=0
    g77: BSplineCurve PolesCount=4 KnotsCount=2 Degree=3 IsPeriodic=0
    g78: BSplineCurve PolesCount=4 KnotsCount=2 Degree=3 IsPeriodic=0
    g79: BSplineCurve PolesCount=4 KnotsCount=2 Degree=3 IsPeriodic=0
    g80: BSplineCurve PolesCount=4 KnotsCount=2 Degree=3 IsPeriodic=0
    g81: BSplineCurve PolesCount=4 KnotsCount=2 Degree=3 IsPeriodic=0
    g82: BSplineCurve PolesCount=2 KnotsCount=2 Degree=1 IsPeriodic=0
    g83: BSplineCurve PolesCount=2 KnotsCount=2 Degree=1 IsPeriodic=0
    g84: BSplineCurve PolesCount=4 KnotsCount=2 Degree=3 IsPeriodic=0
    g85: BSplineCurve PolesCount=4 KnotsCount=2 Degree=3 IsPeriodic=0
    g86: BSplineCurve PolesCount=4 KnotsCount=2 Degree=3 IsPeriodic=0
    g87: BSplineCurve PolesCount=4 KnotsCount=2 Degree=3 IsPeriodic=0
    g88: BSplineCurve PolesCount=4 KnotsCount=2 Degree=3 IsPeriodic=0
    g89: BSplineCurve PolesCount=4 KnotsCount=2 Degree=3 IsPeriodic=0
    g90: BSplineCurve PolesCount=4 KnotsCount=2 Degree=3 IsPeriodic=0
    g91: BSplineCurve PolesCount=4 KnotsCount=2 Degree=3 IsPeriodic=0
    g92: BSplineCurve PolesCount=4 KnotsCount=2 Degree=3 IsPeriodic=0
    g93: BSplineCurve PolesCount=4 KnotsCount=2 Degree=3 IsPeriodic=0
    g94: BSplineCurve PolesCount=4 KnotsCount=2 Degree=3 IsPeriodic=0
    g95: BSplineCurve PolesCount=4 KnotsCount=2 Degree=3 IsPeriodic=0
    g96: BSplineCurve PolesCount=4 KnotsCount=2 Degree=3 IsPeriodic=0
    g97: BSplineCurve PolesCount=4 KnotsCount=2 Degree=3 IsPeriodic=0
    g98: BSplineCurve PolesCount=4 KnotsCount=2 Degree=3 IsPeriodic=0
    g99: BSplineCurve PolesCount=4 KnotsCount=2 Degree=3 IsPeriodic=0
    g100: BSplineCurve PolesCount=4 KnotsCount=2 Degree=3 IsPeriodic=0
    g101: BSplineCurve PolesCount=4 KnotsCount=2 Degree=3 IsPeriodic=0
    g102: BSplineCurve PolesCount=4 KnotsCount=2 Degree=3 IsPeriodic=0
    g103: BSplineCurve PolesCount=4 KnotsCount=2 Degree=3 IsPeriodic=0
    g104: BSplineCurve PolesCount=4 KnotsCount=2 Degree=3 IsPeriodic=0
    g105: BSplineCurve PolesCount=2 KnotsCount=2 Degree=1 IsPeriodic=0
    g106: BSplineCurve PolesCount=2 KnotsCount=2 Degree=1 IsPeriodic=0
    g107: BSplineCurve PolesCount=4 KnotsCount=2 Degree=3 IsPeriodic=0
    g108: BSplineCurve PolesCount=4 KnotsCount=2 Degree=3 IsPeriodic=0
    g109: BSplineCurve PolesCount=4 KnotsCount=2 Degree=3 IsPeriodic=0
    g110: BSplineCurve PolesCount=4 KnotsCount=2 Degree=3 IsPeriodic=0
    g111: BSplineCurve PolesCount=4 KnotsCount=2 Degree=3 IsPeriodic=0
    g112: BSplineCurve PolesCount=4 KnotsCount=2 Degree=3 IsPeriodic=0
    g113: BSplineCurve PolesCount=2 KnotsCount=2 Degree=1 IsPeriodic=0
    g114: BSplineCurve PolesCount=2 KnotsCount=2 Degree=1 IsPeriodic=0
    g115: BSplineCurve PolesCount=4 KnotsCount=2 Degree=3 IsPeriodic=0
    g116: BSplineCurve PolesCount=4 KnotsCount=2 Degree=3 IsPeriodic=0
    g117: BSplineCurve PolesCount=4 KnotsCount=2 Degree=3 IsPeriodic=0
    g118: BSplineCurve PolesCount=4 KnotsCount=2 Degree=3 IsPeriodic=0
    g119: BSplineCurve PolesCount=4 KnotsCount=2 Degree=3 IsPeriodic=0
    g120: BSplineCurve PolesCount=4 KnotsCount=2 Degree=3 IsPeriodic=0
    g121: BSplineCurve PolesCount=4 KnotsCount=2 Degree=3 IsPeriodic=0
    g122: BSplineCurve PolesCount=4 KnotsCount=2 Degree=3 IsPeriodic=0
    g123: BSplineCurve PolesCount=2 KnotsCount=2 Degree=1 IsPeriodic=0
    g124: BSplineCurve PolesCount=2 KnotsCount=2 Degree=1 IsPeriodic=0
    g125: BSplineCurve PolesCount=4 KnotsCount=2 Degree=3 IsPeriodic=0
    g126: BSplineCurve PolesCount=4 KnotsCount=2 Degree=3 IsPeriodic=0
    g127: BSplineCurve PolesCount=4 KnotsCount=2 Degree=3 IsPeriodic=0
    g128: BSplineCurve PolesCount=4 KnotsCount=2 Degree=3 IsPeriodic=0
    g129: BSplineCurve PolesCount=4 KnotsCount=2 Degree=3 IsPeriodic=0
    g130: BSplineCurve PolesCount=4 KnotsCount=2 Degree=3 IsPeriodic=0
    g131: BSplineCurve PolesCount=4 KnotsCount=2 Degree=3 IsPeriodic=0
    g132: BSplineCurve PolesCount=4 KnotsCount=2 Degree=3 IsPeriodic=0
    g133: BSplineCurve PolesCount=4 KnotsCount=2 Degree=3 IsPeriodic=0
    g134: BSplineCurve PolesCount=4 KnotsCount=2 Degree=3 IsPeriodic=0
    g135: BSplineCurve PolesCount=4 KnotsCount=2 Degree=3 IsPeriodic=0
    g136: BSplineCurve PolesCount=4 KnotsCount=2 Degree=3 IsPeriodic=0
    g137: BSplineCurve PolesCount=4 KnotsCount=2 Degree=3 IsPeriodic=0
  constraints (140):
    c: Coincident(g0,g1)
    c: Coincident(g1,g2)
    c: Coincident(g2,g3)
    c: Coincident(g3,g4)
    c: Coincident(g4,g5)
    c: Coincident(g5,g6)
    c: Coincident(g6,g7)
    c: Coincident(g7,g8)
    c: Coincident(g8,g9)
    c: Coincident(g9,g10)
    c: Coincident(g10,g11)
    c: Coincident(g11,g12)
    c: Coincident(g12,g13)
    c: Coincident(g13,g14)
    c: Coincident(g14,g15)
    c: Coincident(g15,g16)
    c: Coincident(g16,g17)
    c: Coincident(g17,g0)
    c: Coincident(g18,g19)
    c: Coincident(g19,g20)
    c: Coincident(g20,g21)
    c: Coincident(g21,g22)
    c: Coincident(g22,g23)
    c: Coincident(g23,g24)
    c: Coincident(g24,g25)
    c: Coincident(g25,g26)
    c: Coincident(g26,g18)
    c: Coincident(g27,g28)
    c: Coincident(g28,g29)
    c: Coincident(g29,g30)
    c: Coincident(g30,g31)
    c: Coincident(g31,g32)
    c: Coincident(g32,g33)
    c: Coincident(g33,g27)
    c: Coincident(g34,g35)
    c: Coincident(g35,g36)
    c: Coincident(g36,g37)
    c: Coincident(g37,g38)
    c: Coincident(g38,g39)
    c: Coincident(g39,g40)
    c: Coincident(g40,g41)
    c: Coincident(g41,g42)
    c: Coincident(g42,g34)
    c: Coincident(g43,g44)
    c: Coincident(g44,g45)
    c: Coincident(g45,g46)
    c: Coincident(g46,g47)
    c: Coincident(g47,g48)
    c: Coincident(g48,g49)
    c: Coincident(g49,g50)
    c: Coincident(g50,g51)
    c: Coincident(g51,g52)
    c: Coincident(g52,g53)
    c: Coincident(g53,g54)
    c: Coincident(g54,g55)
    c: Coincident(g55,g56)
    c: Coincident(g56,g57)
    c: Coincident(g57,g58)
    c: Coincident(g58,g59)
    c: Coincident(g59,g60)
    c: Coincident(g60,g61)
    c: Coincident(g61,g62)
    c: Coincident(g62,g63)
    c: Coincident(g63,g64)
    c: Coincident(g64,g65)
    c: Coincident(g65,g66)
    c: Coincident(g66,g67)
    c: Coincident(g67,g68)
    c: Coincident(g68,g69)
    c: Coincident(g69,g43)
    c: Coincident(g70,g71)
    c: Coincident(g71,g72)
    c: Coincident(g72,g73)
    c: Coincident(g73,g74)
    c: Coincident(g74,g75)
    c: Coincident(g75,g76)
    c: Coincident(g76,g77)
    c: Coincident(g77,g70)
    c: Coincident(g78,g79)
    c: Coincident(g79,g80)
    c: Coincident(g80,g81)
    c: Coincident(g81,g82)
    c: Coincident(g82,g83)
    c: Coincident(g83,g84)
    c: Coincident(g84,g78)
    c: Coincident(g85,g86)
    c: Coincident(g86,g87)
    c: Coincident(g87,g88)
    c: Coincident(g88,g85)
    c: Coincident(g89,g90)
    c: Coincident(g90,g91)
    c: Coincident(g91,g92)
    c: Coincident(g92,g93)
    c: Coincident(g93,g94)
    c: Coincident(g94,g95)
    c: Coincident(g95,g96)
    c: Coincident(g96,g97)
    c: Coincident(g97,g98)
    c: Coincident(g98,g89)
    c: Coincident(g99,g100)
    c: Coincident(g100,g101)
    c: Coincident(g101,g102)
    c: Coincident(g102,g103)
    c: Coincident(g103,g104)
    c: Coincident(g104,g105)
    c: Coincident(g105,g106)
    c: Coincident(g106,g107)
    c: Coincident(g107,g108)
    c: Coincident(g108,g109)
    c: Coincident(g109,g110)
    c: Coincident(g110,g111)
    c: Coincident(g111,g112)
    c: Coincident(g112,g113)
    c: Coincident(g113,g114)
    c: Coincident(g114,g115)
    c: Coincident(g115,g116)
    c: Coincident(g116,g117)
    c: Coincident(g117,g118)
    c: Coincident(g118,g119)
    c: Coincident(g119,g99)
    c: Coincident(g120,g121)
    c: Coincident(g121,g122)
    c: Coincident(g122,g123)
    c: Coincident(g123,g124)
    c: Coincident(g124,g125)
    c: Coincident(g125,g126)
    c: Coincident(g126,g127)
    c: Coincident(g127,g128)
    c: Coincident(g128,g129)
    c: Coincident(g129,g130)
    c: Coincident(g130,g131)
    c: Coincident(g131,g132)
    c: Coincident(g132,g133)
    c: Coincident(g133,g134)
    c: Coincident(g134,g135)
    c: Coincident(g135,g136)
    c: Coincident(g136,g137)
    c: Coincident(g137,g120)
    c: Coincident(g16,g0)
    c: Coincident(g34,g34)
FEATURE [Sketcher::SketchObject] Sketch048  label="Town_Crier-Sketch"
  ArcFitTolerance = 1e-06
  FullyConstrained = false
  MakeInternals = false
  Placement = pos=(-12.9648,12.7922,0) rot=(0,0,1;0rad)
  expr: .Placement.Base.x = -(.Shape.BoundBox.XLength / 2)
  expr: .Placement.Base.y = .Shape.BoundBox.YLength / 2
  sketch-geometry (234):
    g0: BSplineCurve PolesCount=4 KnotsCount=2 Degree=3 IsPeriodic=0
    g1: BSplineCurve PolesCount=4 KnotsCount=2 Degree=3 IsPeriodic=0
    g2: BSplineCurve PolesCount=4 KnotsCount=2 Degree=3 IsPeriodic=0
    g3: BSplineCurve PolesCount=4 KnotsCount=2 Degree=3 IsPeriodic=0
    g4: BSplineCurve PolesCount=4 KnotsCount=2 Degree=3 IsPeriodic=0
    g5: BSplineCurve PolesCount=4 KnotsCount=2 Degree=3 IsPeriodic=0
    g6: BSplineCurve PolesCount=2 KnotsCount=2 Degree=1 IsPeriodic=0
    g7: BSplineCurve PolesCount=2 KnotsCount=2 Degree=1 IsPeriodic=0
    g8: BSplineCurve PolesCount=4 KnotsCount=2 Degree=3 IsPeriodic=0
    g9: BSplineCurve PolesCount=4 KnotsCount=2 Degree=3 IsPeriodic=0
    g10: BSplineCurve PolesCount=4 KnotsCount=2 Degree=3 IsPeriodic=0
    g11: BSplineCurve PolesCount=4 KnotsCount=2 Degree=3 IsPeriodic=0
    g12: BSplineCurve PolesCount=4 KnotsCount=2 Degree=3 IsPeriodic=0
    g13: BSplineCurve PolesCount=4 KnotsCount=2 Degree=3 IsPeriodic=0
    g14: BSplineCurve PolesCount=2 KnotsCount=2 Degree=1 IsPeriodic=0
    g15: BSplineCurve PolesCount=2 KnotsCount=2 Degree=1 IsPeriodic=0
    g16: BSplineCurve PolesCount=4 KnotsCount=2 Degree=3 IsPeriodic=0
    g17: BSplineCurve PolesCount=4 KnotsCount=2 Degree=3 IsPeriodic=0
    g18: BSplineCurve PolesCount=4 KnotsCount=2 Degree=3 IsPeriodic=0
    g19: BSplineCurve PolesCount=4 KnotsCount=2 Degree=3 IsPeriodic=0
    g20: BSplineCurve PolesCount=4 KnotsCount=2 Degree=3 IsPeriodic=0
    g21: BSplineCurve PolesCount=4 KnotsCount=2 Degree=3 IsPeriodic=0
    g22: BSplineCurve PolesCount=2 KnotsCount=2 Degree=1 IsPeriodic=0
    g23: BSplineCurve PolesCount=2 KnotsCount=2 Degree=1 IsPeriodic=0
    g24: BSplineCurve PolesCount=2 KnotsCount=2 Degree=1 IsPeriodic=0
    g25: BSplineCurve PolesCount=2 KnotsCount=2 Degree=1 IsPeriodic=0
    g26: BSplineCurve PolesCount=4 KnotsCount=2 Degree=3 IsPeriodic=0
    g27: BSplineCurve PolesCount=2 KnotsCount=2 Degree=1 IsPeriodic=0
    g28: BSplineCurve PolesCount=2 KnotsCount=2 Degree=1 IsPeriodic=0
    g29: BSplineCurve PolesCount=4 KnotsCount=2 Degree=3 IsPeriodic=0
    g30: BSplineCurve PolesCount=4 KnotsCount=2 Degree=3 IsPeriodic=0
    g31: BSplineCurve PolesCount=4 KnotsCount=2 Degree=3 IsPeriodic=0
    g32: BSplineCurve PolesCount=4 KnotsCount=2 Degree=3 IsPeriodic=0
    g33: BSplineCurve PolesCount=4 KnotsCount=2 Degree=3 IsPeriodic=0
    g34: BSplineCurve PolesCount=4 KnotsCount=2 Degree=3 IsPeriodic=0
    g35: BSplineCurve PolesCount=4 KnotsCount=2 Degree=3 IsPeriodic=0
    g36: BSplineCurve PolesCount=4 KnotsCount=2 Degree=3 IsPeriodic=0
    g37: BSplineCurve PolesCount=4 KnotsCount=2 Degree=3 IsPeriodic=0
    g38: BSplineCurve PolesCount=4 KnotsCount=2 Degree=3 IsPeriodic=0
    g39: BSplineCurve PolesCount=4 KnotsCount=2 Degree=3 IsPeriodic=0
    g40: BSplineCurve PolesCount=4 KnotsCount=2 Degree=3 IsPeriodic=0
    g41: BSplineCurve PolesCount=4 KnotsCount=2 Degree=3 IsPeriodic=0
    g42: BSplineCurve PolesCount=4 KnotsCount=2 Degree=3 IsPeriodic=0
    g43: BSplineCurve PolesCount=4 KnotsCount=2 Degree=3 IsPeriodic=0
    g44: BSplineCurve PolesCount=4 KnotsCount=2 Degree=3 IsPeriodic=0
    g45: BSplineCurve PolesCount=2 KnotsCount=2 Degree=1 IsPeriodic=0
    g46: BSplineCurve PolesCount=2 KnotsCount=2 Degree=1 IsPeriodic=0
    g47: BSplineCurve PolesCount=2 KnotsCount=2 Degree=1 IsPeriodic=0
    g48: BSplineCurve PolesCount=2 KnotsCount=2 Degree=1 IsPeriodic=0
    g49: BSplineCurve PolesCount=4 KnotsCount=2 Degree=3 IsPeriodic=0
    g50: BSplineCurve PolesCount=4 KnotsCount=2 Degree=3 IsPeriodic=0
    g51: BSplineCurve PolesCount=4 KnotsCount=2 Degree=3 IsPeriodic=0
    g52: BSplineCurve PolesCount=4 KnotsCount=2 Degree=3 IsPeriodic=0
    g53: BSplineCurve PolesCount=4 KnotsCount=2 Degree=3 IsPeriodic=0
    g54: BSplineCurve PolesCount=4 KnotsCount=2 Degree=3 IsPeriodic=0
    g55: BSplineCurve PolesCount=4 KnotsCount=2 Degree=3 IsPeriodic=0
    g56: BSplineCurve PolesCount=4 KnotsCount=2 Degree=3 IsPeriodic=0
    g57: BSplineCurve PolesCount=4 KnotsCount=2 Degree=3 IsPeriodic=0
    g58: BSplineCurve PolesCount=4 KnotsCount=2 Degree=3 IsPeriodic=0
    g59: BSplineCurve PolesCount=4 KnotsCount=2 Degree=3 IsPeriodic=0
    g60: BSplineCurve PolesCount=4 KnotsCount=2 Degree=3 IsPeriodic=0
    g61: BSplineCurve PolesCount=2 KnotsCount=2 Degree=1 IsPeriodic=0
    g62: BSplineCurve PolesCount=2 KnotsCount=2 Degree=1 IsPeriodic=0
    g63: BSplineCurve PolesCount=4 KnotsCount=2 Degree=3 IsPeriodic=0
    g64: BSplineCurve PolesCount=4 KnotsCount=2 Degree=3 IsPeriodic=0
    g65: BSplineCurve PolesCount=4 KnotsCount=2 Degree=3 IsPeriodic=0
    g66: BSplineCurve PolesCount=2 KnotsCount=2 Degree=1 IsPeriodic=0
    g67: BSplineCurve PolesCount=4 KnotsCount=2 Degree=3 IsPeriodic=0
    g68: BSplineCurve PolesCount=4 KnotsCount=2 Degree=3 IsPeriodic=0
    g69: BSplineCurve PolesCount=4 KnotsCount=2 Degree=3 IsPeriodic=0
    g70: BSplineCurve PolesCount=4 KnotsCount=2 Degree=3 IsPeriodic=0
    g71: BSplineCurve PolesCount=2 KnotsCount=2 Degree=1 IsPeriodic=0
    g72: BSplineCurve PolesCount=4 KnotsCount=2 Degree=3 IsPeriodic=0
    g73: BSplineCurve PolesCount=4 KnotsCount=2 Degree=3 IsPeriodic=0
    g74: BSplineCurve PolesCount=4 KnotsCount=2 Degree=3 IsPeriodic=0
    g75: BSplineCurve PolesCount=4 KnotsCount=2 Degree=3 IsPeriodic=0
    g76: BSplineCurve PolesCount=4 KnotsCount=2 Degree=3 IsPeriodic=0
    g77: BSplineCurve PolesCount=4 KnotsCount=2 Degree=3 IsPeriodic=0
    g78: BSplineCurve PolesCount=4 KnotsCount=2 Degree=3 IsPeriodic=0
    g79: BSplineCurve PolesCount=4 KnotsCount=2 Degree=3 IsPeriodic=0
    g80: BSplineCurve PolesCount=4 KnotsCount=2 Degree=3 IsPeriodic=0
    g81: BSplineCurve PolesCount=4 KnotsCount=2 Degree=3 IsPeriodic=0
    g82: BSplineCurve PolesCount=4 KnotsCount=2 Degree=3 IsPeriodic=0
    g83: BSplineCurve PolesCount=4 KnotsCount=2 Degree=3 IsPeriodic=0
    g84: BSplineCurve PolesCount=4 KnotsCount=2 Degree=3 IsPeriodic=0
    g85: BSplineCurve PolesCount=4 KnotsCount=2 Degree=3 IsPeriodic=0
    g86: BSplineCurve PolesCount=4 KnotsCount=2 Degree=3 IsPeriodic=0
    g87: BSplineCurve PolesCount=4 KnotsCount=2 Degree=3 IsPeriodic=0
    g88: BSplineCurve PolesCount=4 KnotsCount=2 Degree=3 IsPeriodic=0
    g89: BSplineCurve PolesCount=4 KnotsCount=2 Degree=3 IsPeriodic=0
    g90: BSplineCurve PolesCount=4 KnotsCount=2 Degree=3 IsPeriodic=0
    g91: BSplineCurve PolesCount=4 KnotsCount=2 Degree=3 IsPeriodic=0
    g92: BSplineCurve PolesCount=4 KnotsCount=2 Degree=3 IsPeriodic=0
    g93: BSplineCurve PolesCount=4 KnotsCount=2 Degree=3 IsPeriodic=0
    g94: BSplineCurve PolesCount=4 KnotsCount=2 Degree=3 IsPeriodic=0
    g95: BSplineCurve PolesCount=4 KnotsCount=2 Degree=3 IsPeriodic=0
    g96: BSplineCurve PolesCount=4 KnotsCount=2 Degree=3 IsPeriodic=0
    g97: BSplineCurve PolesCount=4 KnotsCount=2 Degree=3 IsPeriodic=0
    g98: BSplineCurve PolesCount=4 KnotsCount=2 Degree=3 IsPeriodic=0
    g99: BSplineCurve PolesCount=4 KnotsCount=2 Degree=3 IsPeriodic=0
    g100: BSplineCurve PolesCount=4 KnotsCount=2 Degree=3 IsPeriodic=0
    g101: BSplineCurve PolesCount=4 KnotsCount=2 Degree=3 IsPeriodic=0
    g102: BSplineCurve PolesCount=4 KnotsCount=2 Degree=3 IsPeriodic=0
    g103: BSplineCurve PolesCount=4 KnotsCount=2 Degree=3 IsPeriodic=0
    g104: BSplineCurve PolesCount=4 KnotsCount=2 Degree=3 IsPeriodic=0
    g105: BSplineCurve PolesCount=4 KnotsCount=2 Degree=3 IsPeriodic=0
    g106: BSplineCurve PolesCount=4 KnotsCount=2 Degree=3 IsPeriodic=0
    g107: BSplineCurve PolesCount=4 KnotsCount=2 Degree=3 IsPeriodic=0
    g108: BSplineCurve PolesCount=4 KnotsCount=2 Degree=3 IsPeriodic=0
    g109: BSplineCurve PolesCount=4 KnotsCount=2 Degree=3 IsPeriodic=0
    g110: BSplineCurve PolesCount=4 KnotsCount=2 Degree=3 IsPeriodic=0
    g111: BSplineCurve PolesCount=2 KnotsCount=2 Degree=1 IsPeriodic=0
    g112: BSplineCurve PolesCount=2 KnotsCount=2 Degree=1 IsPeriodic=0
    g113: BSplineCurve PolesCount=2 KnotsCount=2 Degree=1 IsPeriodic=0
    g114: BSplineCurve PolesCount=2 KnotsCount=2 Degree=1 IsPeriodic=0
    g115: BSplineCurve PolesCount=4 KnotsCount=2 Degree=3 IsPeriodic=0
    g116: BSplineCurve PolesCount=4 KnotsCount=2 Degree=3 IsPeriodic=0
    g117: BSplineCurve PolesCount=4 KnotsCount=2 Degree=3 IsPeriodic=0
    g118: BSplineCurve PolesCount=2 KnotsCount=2 Degree=1 IsPeriodic=0
    g119: BSplineCurve PolesCount=2 KnotsCount=2 Degree=1 IsPeriodic=0
    g120: BSplineCurve PolesCount=4 KnotsCount=2 Degree=3 IsPeriodic=0
    g121: BSplineCurve PolesCount=4 KnotsCount=2 Degree=3 IsPeriodic=0
    g122: BSplineCurve PolesCount=4 KnotsCount=2 Degree=3 IsPeriodic=0
    g123: BSplineCurve PolesCount=4 KnotsCount=2 Degree=3 IsPeriodic=0
    g124: BSplineCurve PolesCount=4 KnotsCount=2 Degree=3 IsPeriodic=0
    g125: BSplineCurve PolesCount=4 KnotsCount=2 Degree=3 IsPeriodic=0
    g126: BSplineCurve PolesCount=4 KnotsCount=2 Degree=3 IsPeriodic=0
    g127: BSplineCurve PolesCount=2 KnotsCount=2 Degree=1 IsPeriodic=0
    g128: BSplineCurve PolesCount=4 KnotsCount=2 Degree=3 IsPeriodic=0
    g129: BSplineCurve PolesCount=2 KnotsCount=2 Degree=1 IsPeriodic=0
    g130: BSplineCurve PolesCount=2 KnotsCount=2 Degree=1 IsPeriodic=0
    g131: BSplineCurve PolesCount=4 KnotsCount=2 Degree=3 IsPeriodic=0
    g132: BSplineCurve PolesCount=4 KnotsCount=2 Degree=3 IsPeriodic=0
    g133: BSplineCurve PolesCount=4 KnotsCount=2 Degree=3 IsPeriodic=0
    g134: BSplineCurve PolesCount=4 KnotsCount=2 Degree=3 IsPeriodic=0
    g135: BSplineCurve PolesCount=4 KnotsCount=2 Degree=3 IsPeriodic=0
    g136: BSplineCurve PolesCount=4 KnotsCount=2 Degree=3 IsPeriodic=0
    g137: BSplineCurve PolesCount=4 KnotsCount=2 Degree=3 IsPeriodic=0
    g138: BSplineCurve PolesCount=4 KnotsCount=2 Degree=3 IsPeriodic=0
    g139: BSplineCurve PolesCount=4 KnotsCount=2 Degree=3 IsPeriodic=0
    g140: BSplineCurve PolesCount=4 KnotsCount=2 Degree=3 IsPeriodic=0
    g141: BSplineCurve PolesCount=4 KnotsCount=2 Degree=3 IsPeriodic=0
    g142: BSplineCurve PolesCount=4 KnotsCount=2 Degree=3 IsPeriodic=0
    g143: BSplineCurve PolesCount=4 KnotsCount=2 Degree=3 IsPeriodic=0
    g144: BSplineCurve PolesCount=4 KnotsCount=2 Degree=3 IsPeriodic=0
    g145: BSplineCurve PolesCount=4 KnotsCount=2 Degree=3 IsPeriodic=0
    g146: BSplineCurve PolesCount=4 KnotsCount=2 Degree=3 IsPeriodic=0
    g147: BSplineCurve PolesCount=4 KnotsCount=2 Degree=3 IsPeriodic=0
    g148: BSplineCurve PolesCount=4 KnotsCount=2 Degree=3 IsPeriodic=0
    g149: BSplineCurve PolesCount=4 KnotsCount=2 Degree=3 IsPeriodic=0
    g150: BSplineCurve PolesCount=4 KnotsCount=2 Degree=3 IsPeriodic=0
    g151: BSplineCurve PolesCount=4 KnotsCount=2 Degree=3 IsPeriodic=0
    g152: BSplineCurve PolesCount=4 KnotsCount=2 Degree=3 IsPeriodic=0
    g153: BSplineCurve PolesCount=4 KnotsCount=2 Degree=3 IsPeriodic=0
    g154: BSplineCurve PolesCount=4 KnotsCount=2 Degree=3 IsPeriodic=0
    g155: BSplineCurve PolesCount=4 KnotsCount=2 Degree=3 IsPeriodic=0
    g156: BSplineCurve PolesCount=4 KnotsCount=2 Degree=3 IsPeriodic=0
    g157: BSplineCurve PolesCount=4 KnotsCount=2 Degree=3 IsPeriodic=0
    g158: BSplineCurve PolesCount=4 KnotsCount=2 Degree=3 IsPeriodic=0
    g159: BSplineCurve PolesCount=4 KnotsCount=2 Degree=3 IsPeriodic=0
    g160: BSplineCurve PolesCount=4 KnotsCount=2 Degree=3 IsPeriodic=0
    g161: BSplineCurve PolesCount=4 KnotsCount=2 Degree=3 IsPeriodic=0
    g162: BSplineCurve PolesCount=4 KnotsCount=2 Degree=3 IsPeriodic=0
    g163: BSplineCurve PolesCount=2 KnotsCount=2 Degree=1 IsPeriodic=0
    g164: BSplineCurve PolesCount=2 KnotsCount=2 Degree=1 IsPeriodic=0
    g165: BSplineCurve PolesCount=4 KnotsCount=2 Degree=3 IsPeriodic=0
    g166: BSplineCurve PolesCount=4 KnotsCount=2 Degree=3 IsPeriodic=0
    g167: BSplineCurve PolesCount=2 KnotsCount=2 Degree=1 IsPeriodic=0
    g168: BSplineCurve PolesCount=2 KnotsCount=2 Degree=1 IsPeriodic=0
    g169: BSplineCurve PolesCount=2 KnotsCount=2 Degree=1 IsPeriodic=0
    g170: BSplineCurve PolesCount=2 KnotsCount=2 Degree=1 IsPeriodic=0
    g171: BSplineCurve PolesCount=4 KnotsCount=2 Degree=3 IsPeriodic=0
    g172: BSplineCurve PolesCount=4 KnotsCount=2 Degree=3 IsPeriodic=0
    g173: BSplineCurve PolesCount=4 KnotsCount=2 Degree=3 IsPeriodic=0
    g174: BSplineCurve PolesCount=4 KnotsCount=2 Degree=3 IsPeriodic=0
    g175: BSplineCurve PolesCount=4 KnotsCount=2 Degree=3 IsPeriodic=0
    g176: BSplineCurve PolesCount=4 KnotsCount=2 Degree=3 IsPeriodic=0
    g177: BSplineCurve PolesCount=4 KnotsCount=2 Degree=3 IsPeriodic=0
    g178: BSplineCurve PolesCount=4 KnotsCount=2 Degree=3 IsPeriodic=0
    g179: BSplineCurve PolesCount=4 KnotsCount=2 Degree=3 IsPeriodic=0
    g180: BSplineCurve PolesCount=4 KnotsCount=2 Degree=3 IsPeriodic=0
    g181: BSplineCurve PolesCount=4 KnotsCount=2 Degree=3 IsPeriodic=0
    g182: BSplineCurve PolesCount=4 KnotsCount=2 Degree=3 IsPeriodic=0
    g183: BSplineCurve PolesCount=4 KnotsCount=2 Degree=3 IsPeriodic=0
    g184: BSplineCurve PolesCount=4 KnotsCount=2 Degree=3 IsPeriodic=0
    g185: BSplineCurve PolesCount=2 KnotsCount=2 Degree=1 IsPeriodic=0
    g186: BSplineCurve PolesCount=2 KnotsCount=2 Degree=1 IsPeriodic=0
    g187: BSplineCurve PolesCount=2 KnotsCount=2 Degree=1 IsPeriodic=0
    g188: BSplineCurve PolesCount=2 KnotsCount=2 Degree=1 IsPeriodic=0
    g189: BSplineCurve PolesCount=2 KnotsCount=2 Degree=1 IsPeriodic=0
    g190: BSplineCurve PolesCount=2 KnotsCount=2 Degree=1 IsPeriodic=0
    g191: BSplineCurve PolesCount=4 KnotsCount=2 Degree=3 IsPeriodic=0
    g192: BSplineCurve PolesCount=4 KnotsCount=2 Degree=3 IsPeriodic=0
    g193: BSplineCurve PolesCount=2 KnotsCount=2 Degree=1 IsPeriodic=0
    g194: BSplineCurve PolesCount=2 KnotsCount=2 Degree=1 IsPeriodic=0
    g195: BSplineCurve PolesCount=4 KnotsCount=2 Degree=3 IsPeriodic=0
    g196: BSplineCurve PolesCount=4 KnotsCount=2 Degree=3 IsPeriodic=0
    g197: BSplineCurve PolesCount=4 KnotsCount=2 Degree=3 IsPeriodic=0
    g198: BSplineCurve PolesCount=4 KnotsCount=2 Degree=3 IsPeriodic=0
    g199: BSplineCurve PolesCount=4 KnotsCount=2 Degree=3 IsPeriodic=0
    g200: BSplineCurve PolesCount=2 KnotsCount=2 Degree=1 IsPeriodic=0
    g201: BSplineCurve PolesCount=4 KnotsCount=2 Degree=3 IsPeriodic=0
    g202: BSplineCurve PolesCount=4 KnotsCount=2 Degree=3 IsPeriodic=0
    g203: BSplineCurve PolesCount=4 KnotsCount=2 Degree=3 IsPeriodic=0
    g204: BSplineCurve PolesCount=4 KnotsCount=2 Degree=3 IsPeriodic=0
    g205: BSplineCurve PolesCount=4 KnotsCount=2 Degree=3 IsPeriodic=0
    g206: BSplineCurve PolesCount=4 KnotsCount=2 Degree=3 IsPeriodic=0
    g207: BSplineCurve PolesCount=4 KnotsCount=2 Degree=3 IsPeriodic=0
    g208: BSplineCurve PolesCount=4 KnotsCount=2 Degree=3 IsPeriodic=0
    g209: BSplineCurve PolesCount=4 KnotsCount=2 Degree=3 IsPeriodic=0
    g210: BSplineCurve PolesCount=4 KnotsCount=2 Degree=3 IsPeriodic=0
    g211: BSplineCurve PolesCount=4 KnotsCount=2 Degree=3 IsPeriodic=0
    g212: BSplineCurve PolesCount=4 KnotsCount=2 Degree=3 IsPeriodic=0
    g213: BSplineCurve PolesCount=4 KnotsCount=2 Degree=3 IsPeriodic=0
    g214: BSplineCurve PolesCount=4 KnotsCount=2 Degree=3 IsPeriodic=0
    g215: BSplineCurve PolesCount=4 KnotsCount=2 Degree=3 IsPeriodic=0
    g216: BSplineCurve PolesCount=4 KnotsCount=2 Degree=3 IsPeriodic=0
    g217: BSplineCurve PolesCount=4 KnotsCount=2 Degree=3 IsPeriodic=0
    g218: BSplineCurve PolesCount=4 KnotsCount=2 Degree=3 IsPeriodic=0
    g219: BSplineCurve PolesCount=4 KnotsCount=2 Degree=3 IsPeriodic=0
    g220: BSplineCurve PolesCount=4 KnotsCount=2 Degree=3 IsPeriodic=0
    g221: BSplineCurve PolesCount=4 KnotsCount=2 Degree=3 IsPeriodic=0
    g222: BSplineCurve PolesCount=4 KnotsCount=2 Degree=3 IsPeriodic=0
    g223: BSplineCurve PolesCount=4 KnotsCount=2 Degree=3 IsPeriodic=0
    g224: BSplineCurve PolesCount=4 KnotsCount=2 Degree=3 IsPeriodic=0
    g225: BSplineCurve PolesCount=4 KnotsCount=2 Degree=3 IsPeriodic=0
    g226: BSplineCurve PolesCount=4 KnotsCount=2 Degree=3 IsPeriodic=0
    g227: BSplineCurve PolesCount=4 KnotsCount=2 Degree=3 IsPeriodic=0
    g228: BSplineCurve PolesCount=4 KnotsCount=2 Degree=3 IsPeriodic=0
    g229: BSplineCurve PolesCount=4 KnotsCount=2 Degree=3 IsPeriodic=0
    g230: BSplineCurve PolesCount=4 KnotsCount=2 Degree=3 IsPeriodic=0
    g231: BSplineCurve PolesCount=4 KnotsCount=2 Degree=3 IsPeriodic=0
    g232: BSplineCurve PolesCount=4 KnotsCount=2 Degree=3 IsPeriodic=0
    g233: BSplineCurve PolesCount=4 KnotsCount=2 Degree=3 IsPeriodic=0
  constraints (240):
    c: Coincident(g0,g1)
    c: Coincident(g1,g2)
    c: Coincident(g2,g3)
    c: Coincident(g3,g4)
    c: Coincident(g4,g5)
    c: Coincident(g5,g6)
    c: Coincident(g6,g7)
    c: Coincident(g7,g8)
    c: Coincident(g8,g9)
    c: Coincident(g9,g10)
    c: Coincident(g10,g11)
    c: Coincident(g11,g12)
    c: Coincident(g12,g13)
    c: Coincident(g13,g14)
    c: Coincident(g14,g15)
    c: Coincident(g15,g16)
    c: Coincident(g16,g17)
    c: Coincident(g17,g18)
    c: Coincident(g18,g19)
    c: Coincident(g19,g20)
    c: Coincident(g20,g21)
    c: Coincident(g21,g22)
    c: Coincident(g22,g23)
    c: Coincident(g23,g24)
    c: Coincident(g24,g25)
    c: Coincident(g25,g26)
    c: Coincident(g26,g27)
    c: Coincident(g27,g28)
    c: Coincident(g28,g29)
    c: Coincident(g29,g30)
    c: Coincident(g30,g31)
    c: Coincident(g31,g32)
    c: Coincident(g32,g33)
    c: Coincident(g33,g34)
    c: Coincident(g34,g35)
    c: Coincident(g35,g36)
    c: Coincident(g36,g37)
    c: Coincident(g37,g38)
    c: Coincident(g38,g39)
    c: Coincident(g39,g40)
    c: Coincident(g40,g41)
    c: Coincident(g41,g42)
    c: Coincident(g42,g43)
    c: Coincident(g43,g44)
    c: Coincident(g44,g45)
    c: Coincident(g45,g46)
    c: Coincident(g46,g47)
    c: Coincident(g47,g48)
    c: Coincident(g48,g49)
    c: Coincident(g49,g50)
    c: Coincident(g50,g51)
    c: Coincident(g51,g52)
    c: Coincident(g52,g53)
    c: Coincident(g53,g54)
    c: Coincident(g54,g55)
    c: Coincident(g55,g56)
    c: Coincident(g56,g57)
    c: Coincident(g57,g58)
    c: Coincident(g58,g59)
    c: Coincident(g59,g60)
    c: Coincident(g60,g61)
    c: Coincident(g61,g0)
    c: Coincident(g62,g63)
    c: Coincident(g63,g64)
    c: Coincident(g64,g65)
    c: Coincident(g65,g62)
    c: Coincident(g66,g67)
    c: Coincident(g67,g68)
    c: Coincident(g68,g69)
    c: Coincident(g69,g70)
    c: Coincident(g70,g66)
    c: Coincident(g71,g72)
    c: Coincident(g72,g73)
    c: Coincident(g73,g74)
    c: Coincident(g74,g75)
    c: Coincident(g75,g76)
    c: Coincident(g76,g77)
    c: Coincident(g77,g78)
    c: Coincident(g78,g79)
    c: Coincident(g79,g80)
    c: Coincident(g80,g81)
    c: Coincident(g81,g82)
    c: Coincident(g82,g83)
    c: Coincident(g83,g84)
    c: Coincident(g84,g85)
    c: Coincident(g85,g86)
    c: Coincident(g86,g87)
    c: Coincident(g87,g88)
    c: Coincident(g88,g89)
    c: Coincident(g89,g90)
    c: Coincident(g90,g91)
    c: Coincident(g91,g92)
    c: Coincident(g92,g93)
    c: Coincident(g93,g94)
    c: Coincident(g94,g95)
    c: Coincident(g95,g96)
    c: Coincident(g96,g97)
    c: Coincident(g97,g98)
    c: Coincident(g98,g99)
    c: Coincident(g99,g100)
    c: Coincident(g100,g101)
    c: Coincident(g101,g102)
    c: Coincident(g102,g103)
    c: Coincident(g103,g104)
    c: Coincident(g104,g105)
    c: Coincident(g105,g106)
    c: Coincident(g106,g107)
    c: Coincident(g107,g108)
    c: Coincident(g108,g109)
    c: Coincident(g109,g110)
    c: Coincident(g110,g111)
    c: Coincident(g111,g112)
    c: Coincident(g112,g113)
    c: Coincident(g113,g114)
    c: Coincident(g114,g115)
    c: Coincident(g115,g116)
    c: Coincident(g116,g117)
    c: Coincident(g117,g118)
    c: Coincident(g118,g119)
    c: Coincident(g119,g120)
    c: Coincident(g120,g71)
    c: Coincident(g121,g122)
    c: Coincident(g122,g123)
    c: Coincident(g123,g124)
    c: Coincident(g124,g125)
    c: Coincident(g125,g126)
    c: Coincident(g126,g121)
    c: Coincident(g127,g128)
    c: Coincident(g128,g129)
    c: Coincident(g129,g130)
    c: Coincident(g130,g131)
    c: Coincident(g131,g132)
    c: Coincident(g132,g127)
    c: Coincident(g133,g134)
    c: Coincident(g134,g135)
    c: Coincident(g135,g136)
    c: Coincident(g136,g137)
    c: Coincident(g137,g138)
    c: Coincident(g138,g139)
    c: Coincident(g139,g140)
    c: Coincident(g140,g141)
    c: Coincident(g141,g142)
    c: Coincident(g142,g143)
    c: Coincident(g143,g144)
    c: Coincident(g144,g145)
    c: Coincident(g145,g146)
    c: Coincident(g146,g147)
    c: Coincident(g147,g148)
    c: Coincident(g148,g149)
    c: Coincident(g149,g150)
    c: Coincident(g150,g151)
    c: Coincident(g151,g152)
    c: Coincident(g152,g153)
    c: Coincident(g153,g154)
    c: Coincident(g154,g155)
    c: Coincident(g155,g156)
    c: Coincident(g156,g157)
    c: Coincident(g157,g158)
    c: Coincident(g158,g159)
    c: Coincident(g159,g160)
    c: Coincident(g160,g161)
    c: Coincident(g161,g162)
    c: Coincident(g162,g163)
    c: Coincident(g163,g164)
    c: Coincident(g164,g165)
    c: Coincident(g165,g166)
    c: Coincident(g166,g167)
    c: Coincident(g167,g168)
    c: Coincident(g168,g169)
    c: Coincident(g169,g170)
    c: Coincident(g170,g171)
    c: Coincident(g171,g172)
    c: Coincident(g172,g173)
    c: Coincident(g173,g174)
    c: Coincident(g174,g175)
    c: Coincident(g175,g133)
    c: Coincident(g176,g177)
    c: Coincident(g177,g178)
    c: Coincident(g178,g179)
    c: Coincident(g179,g180)
    c: Coincident(g180,g181)
    c: Coincident(g181,g182)
    c: Coincident(g182,g183)
    c: Coincident(g183,g184)
    c: Coincident(g184,g185)
    c: Coincident(g185,g186)
    c: Coincident(g186,g187)
    c: Coincident(g187,g188)
    c: Coincident(g188,g189)
    c: Coincident(g189,g190)
    c: Coincident(g190,g191)
    c: Coincident(g191,g192)
    c: Coincident(g192,g193)
    c: Coincident(g193,g194)
    c: Coincident(g194,g195)
    c: Coincident(g195,g196)
    c: Coincident(g196,g197)
    c: Coincident(g197,g198)
    c: Coincident(g198,g199)
    c: Coincident(g199,g176)
    c: Coincident(g200,g201)
    c: Coincident(g201,g202)
    c: Coincident(g202,g203)
    c: Coincident(g203,g204)
    c: Coincident(g204,g205)
    c: Coincident(g205,g206)
    c: Coincident(g206,g200)
    c: Coincident(g207,g208)
    c: Coincident(g208,g209)
    c: Coincident(g209,g210)
    c: Coincident(g210,g211)
    c: Coincident(g211,g212)
    c: Coincident(g212,g213)
    c: Coincident(g213,g214)
    c: Coincident(g214,g215)
    c: Coincident(g215,g216)
    c: Coincident(g216,g207)
    c: Coincident(g217,g218)
    c: Coincident(g218,g219)
    c: Coincident(g219,g220)
    c: Coincident(g220,g221)
    c: Coincident(g221,g217)
    c: Coincident(g222,g223)
    c: Coincident(g223,g224)
    c: Coincident(g224,g225)
    c: Coincident(g225,g226)
    c: Coincident(g226,g227)
    c: Coincident(g227,g228)
    c: Coincident(g228,g229)
    c: Coincident(g229,g230)
    c: Coincident(g230,g231)
    c: Coincident(g231,g232)
    c: Coincident(g232,g233)
    c: Coincident(g233,g222)
    c: Coincident(g200,g200)
    c: Coincident(g127,g127)
    c: Coincident(g66,g66)
    c: Coincident(g60,g0)
    c: Coincident(g62,g62)
    c: Coincident(g71,g71)
FEATURE [Sketcher::SketchObject] Sketch049  label="Vigormortis-Sketch"
  ArcFitTolerance = 1e-06
  FullyConstrained = false
  MakeInternals = false
  Placement = pos=(-14.3814,12.8344,0) rot=(0,0,1;0rad)
  expr: .Placement.Base.x = -(.Shape.BoundBox.XLength / 2)
  expr: .Placement.Base.y = .Shape.BoundBox.YLength / 2
  sketch-geometry (209):
    g0: BSplineCurve PolesCount=4 KnotsCount=2 Degree=3 IsPeriodic=0
    g1: BSplineCurve PolesCount=4 KnotsCount=2 Degree=3 IsPeriodic=0
    g2: BSplineCurve PolesCount=4 KnotsCount=2 Degree=3 IsPeriodic=0
    g3: BSplineCurve PolesCount=4 KnotsCount=2 Degree=3 IsPeriodic=0
    g4: BSplineCurve PolesCount=4 KnotsCount=2 Degree=3 IsPeriodic=0
    g5: BSplineCurve PolesCount=4 KnotsCount=2 Degree=3 IsPeriodic=0
    g6: BSplineCurve PolesCount=4 KnotsCount=2 Degree=3 IsPeriodic=0
    g7: BSplineCurve PolesCount=4 KnotsCount=2 Degree=3 IsPeriodic=0
    g8: BSplineCurve PolesCount=4 KnotsCount=2 Degree=3 IsPeriodic=0
    g9: BSplineCurve PolesCount=2 KnotsCount=2 Degree=1 IsPeriodic=0
    g10: BSplineCurve PolesCount=4 KnotsCount=2 Degree=3 IsPeriodic=0
    g11: BSplineCurve PolesCount=4 KnotsCount=2 Degree=3 IsPeriodic=0
    g12: BSplineCurve PolesCount=4 KnotsCount=2 Degree=3 IsPeriodic=0
    g13: BSplineCurve PolesCount=4 KnotsCount=2 Degree=3 IsPeriodic=0
    g14: BSplineCurve PolesCount=4 KnotsCount=2 Degree=3 IsPeriodic=0
    g15: BSplineCurve PolesCount=4 KnotsCount=2 Degree=3 IsPeriodic=0
    g16: BSplineCurve PolesCount=4 KnotsCount=2 Degree=3 IsPeriodic=0
    g17: BSplineCurve PolesCount=4 KnotsCount=2 Degree=3 IsPeriodic=0
    g18: BSplineCurve PolesCount=4 KnotsCount=2 Degree=3 IsPeriodic=0
    g19: BSplineCurve PolesCount=4 KnotsCount=2 Degree=3 IsPeriodic=0
    g20: BSplineCurve PolesCount=4 KnotsCount=2 Degree=3 IsPeriodic=0
    g21: BSplineCurve PolesCount=4 KnotsCount=2 Degree=3 IsPeriodic=0
    g22: BSplineCurve PolesCount=4 KnotsCount=2 Degree=3 IsPeriodic=0
    g23: BSplineCurve PolesCount=2 KnotsCount=2 Degree=1 IsPeriodic=0
    g24: BSplineCurve PolesCount=4 KnotsCount=2 Degree=3 IsPeriodic=0
    g25: BSplineCurve PolesCount=2 KnotsCount=2 Degree=1 IsPeriodic=0
    g26: BSplineCurve PolesCount=2 KnotsCount=2 Degree=1 IsPeriodic=0
    g27: BSplineCurve PolesCount=2 KnotsCount=2 Degree=1 IsPeriodic=0
    g28: BSplineCurve PolesCount=2 KnotsCount=2 Degree=1 IsPeriodic=0
    g29: BSplineCurve PolesCount=4 KnotsCount=2 Degree=3 IsPeriodic=0
    g30: BSplineCurve PolesCount=4 KnotsCount=2 Degree=3 IsPeriodic=0
    g31: BSplineCurve PolesCount=4 KnotsCount=2 Degree=3 IsPeriodic=0
    g32: BSplineCurve PolesCount=4 KnotsCount=2 Degree=3 IsPeriodic=0
    g33: BSplineCurve PolesCount=4 KnotsCount=2 Degree=3 IsPeriodic=0
    g34: BSplineCurve PolesCount=4 KnotsCount=2 Degree=3 IsPeriodic=0
    g35: BSplineCurve PolesCount=4 KnotsCount=2 Degree=3 IsPeriodic=0
    g36: BSplineCurve PolesCount=4 KnotsCount=2 Degree=3 IsPeriodic=0
    g37: BSplineCurve PolesCount=4 KnotsCount=2 Degree=3 IsPeriodic=0
    g38: BSplineCurve PolesCount=4 KnotsCount=2 Degree=3 IsPeriodic=0
    g39: BSplineCurve PolesCount=4 KnotsCount=2 Degree=3 IsPeriodic=0
    g40: BSplineCurve PolesCount=4 KnotsCount=2 Degree=3 IsPeriodic=0
    g41: BSplineCurve PolesCount=4 KnotsCount=2 Degree=3 IsPeriodic=0
    g42: BSplineCurve PolesCount=4 KnotsCount=2 Degree=3 IsPeriodic=0
    g43: BSplineCurve PolesCount=4 KnotsCount=2 Degree=3 IsPeriodic=0
    g44: BSplineCurve PolesCount=4 KnotsCount=2 Degree=3 IsPeriodic=0
    g45: BSplineCurve PolesCount=4 KnotsCount=2 Degree=3 IsPeriodic=0
    g46: BSplineCurve PolesCount=4 KnotsCount=2 Degree=3 IsPeriodic=0
    g47: BSplineCurve PolesCount=4 KnotsCount=2 Degree=3 IsPeriodic=0
    g48: BSplineCurve PolesCount=4 KnotsCount=2 Degree=3 IsPeriodic=0
    g49: BSplineCurve PolesCount=4 KnotsCount=2 Degree=3 IsPeriodic=0
    g50: BSplineCurve PolesCount=4 KnotsCount=2 Degree=3 IsPeriodic=0
    g51: BSplineCurve PolesCount=4 KnotsCount=2 Degree=3 IsPeriodic=0
    g52: BSplineCurve PolesCount=4 KnotsCount=2 Degree=3 IsPeriodic=0
    g53: BSplineCurve PolesCount=4 KnotsCount=2 Degree=3 IsPeriodic=0
    g54: BSplineCurve PolesCount=4 KnotsCount=2 Degree=3 IsPeriodic=0
    g55: BSplineCurve PolesCount=4 KnotsCount=2 Degree=3 IsPeriodic=0
    g56: BSplineCurve PolesCount=4 KnotsCount=2 Degree=3 IsPeriodic=0
    g57: BSplineCurve PolesCount=4 KnotsCount=2 Degree=3 IsPeriodic=0
    g58: BSplineCurve PolesCount=4 KnotsCount=2 Degree=3 IsPeriodic=0
    g59: BSplineCurve PolesCount=4 KnotsCount=2 Degree=3 IsPeriodic=0
    g60: BSplineCurve PolesCount=4 KnotsCount=2 Degree=3 IsPeriodic=0
    g61: BSplineCurve PolesCount=4 KnotsCount=2 Degree=3 IsPeriodic=0
    g62: BSplineCurve PolesCount=4 KnotsCount=2 Degree=3 IsPeriodic=0
    g63: BSplineCurve PolesCount=4 KnotsCount=2 Degree=3 IsPeriodic=0
    g64: BSplineCurve PolesCount=4 KnotsCount=2 Degree=3 IsPeriodic=0
    g65: BSplineCurve PolesCount=4 KnotsCount=2 Degree=3 IsPeriodic=0
    g66: BSplineCurve PolesCount=4 KnotsCount=2 Degree=3 IsPeriodic=0
    g67: BSplineCurve PolesCount=4 KnotsCount=2 Degree=3 IsPeriodic=0
    g68: BSplineCurve PolesCount=4 KnotsCount=2 Degree=3 IsPeriodic=0
    g69: BSplineCurve PolesCount=4 KnotsCount=2 Degree=3 IsPeriodic=0
    g70: BSplineCurve PolesCount=4 KnotsCount=2 Degree=3 IsPeriodic=0
    g71: BSplineCurve PolesCount=4 KnotsCount=2 Degree=3 IsPeriodic=0
    g72: BSplineCurve PolesCount=4 KnotsCount=2 Degree=3 IsPeriodic=0
    g73: BSplineCurve PolesCount=4 KnotsCount=2 Degree=3 IsPeriodic=0
    g74: BSplineCurve PolesCount=4 KnotsCount=2 Degree=3 IsPeriodic=0
    g75: BSplineCurve PolesCount=4 KnotsCount=2 Degree=3 IsPeriodic=0
    g76: BSplineCurve PolesCount=4 KnotsCount=2 Degree=3 IsPeriodic=0
    g77: BSplineCurve PolesCount=4 KnotsCount=2 Degree=3 IsPeriodic=0
    g78: BSplineCurve PolesCount=4 KnotsCount=2 Degree=3 IsPeriodic=0
    g79: BSplineCurve PolesCount=4 KnotsCount=2 Degree=3 IsPeriodic=0
    g80: BSplineCurve PolesCount=4 KnotsCount=2 Degree=3 IsPeriodic=0
    g81: BSplineCurve PolesCount=4 KnotsCount=2 Degree=3 IsPeriodic=0
    g82: BSplineCurve PolesCount=4 KnotsCount=2 Degree=3 IsPeriodic=0
    g83: BSplineCurve PolesCount=4 KnotsCount=2 Degree=3 IsPeriodic=0
    g84: BSplineCurve PolesCount=4 KnotsCount=2 Degree=3 IsPeriodic=0
    g85: BSplineCurve PolesCount=2 KnotsCount=2 Degree=1 IsPeriodic=0
    g86: BSplineCurve PolesCount=2 KnotsCount=2 Degree=1 IsPeriodic=0
    g87: BSplineCurve PolesCount=4 KnotsCount=2 Degree=3 IsPeriodic=0
    g88: BSplineCurve PolesCount=4 KnotsCount=2 Degree=3 IsPeriodic=0
    g89: BSplineCurve PolesCount=4 KnotsCount=2 Degree=3 IsPeriodic=0
    g90: BSplineCurve PolesCount=4 KnotsCount=2 Degree=3 IsPeriodic=0
    g91: BSplineCurve PolesCount=4 KnotsCount=2 Degree=3 IsPeriodic=0
    g92: BSplineCurve PolesCount=4 KnotsCount=2 Degree=3 IsPeriodic=0
    g93: BSplineCurve PolesCount=4 KnotsCount=2 Degree=3 IsPeriodic=0
    g94: BSplineCurve PolesCount=4 KnotsCount=2 Degree=3 IsPeriodic=0
    g95: BSplineCurve PolesCount=4 KnotsCount=2 Degree=3 IsPeriodic=0
    g96: BSplineCurve PolesCount=4 KnotsCount=2 Degree=3 IsPeriodic=0
    g97: BSplineCurve PolesCount=4 KnotsCount=2 Degree=3 IsPeriodic=0
    g98: BSplineCurve PolesCount=4 KnotsCount=2 Degree=3 IsPeriodic=0
    g99: BSplineCurve PolesCount=4 KnotsCount=2 Degree=3 IsPeriodic=0
    g100: BSplineCurve PolesCount=4 KnotsCount=2 Degree=3 IsPeriodic=0
    g101: BSplineCurve PolesCount=4 KnotsCount=2 Degree=3 IsPeriodic=0
    g102: BSplineCurve PolesCount=2 KnotsCount=2 Degree=1 IsPeriodic=0
    g103: BSplineCurve PolesCount=2 KnotsCount=2 Degree=1 IsPeriodic=0
    g104: BSplineCurve PolesCount=4 KnotsCount=2 Degree=3 IsPeriodic=0
    g105: BSplineCurve PolesCount=4 KnotsCount=2 Degree=3 IsPeriodic=0
    g106: BSplineCurve PolesCount=4 KnotsCount=2 Degree=3 IsPeriodic=0
    g107: BSplineCurve PolesCount=2 KnotsCount=2 Degree=1 IsPeriodic=0
    g108: BSplineCurve PolesCount=2 KnotsCount=2 Degree=1 IsPeriodic=0
    g109: BSplineCurve PolesCount=4 KnotsCount=2 Degree=3 IsPeriodic=0
    g110: BSplineCurve PolesCount=4 KnotsCount=2 Degree=3 IsPeriodic=0
    g111: BSplineCurve PolesCount=4 KnotsCount=2 Degree=3 IsPeriodic=0
    g112: BSplineCurve PolesCount=2 KnotsCount=2 Degree=1 IsPeriodic=0
    g113: BSplineCurve PolesCount=2 KnotsCount=2 Degree=1 IsPeriodic=0
    g114: BSplineCurve PolesCount=4 KnotsCount=2 Degree=3 IsPeriodic=0
    g115: BSplineCurve PolesCount=4 KnotsCount=2 Degree=3 IsPeriodic=0
    g116: BSplineCurve PolesCount=4 KnotsCount=2 Degree=3 IsPeriodic=0
    g117: BSplineCurve PolesCount=2 KnotsCount=2 Degree=1 IsPeriodic=0
    g118: BSplineCurve PolesCount=2 KnotsCount=2 Degree=1 IsPeriodic=0
    g119: BSplineCurve PolesCount=4 KnotsCount=2 Degree=3 IsPeriodic=0
    g120: BSplineCurve PolesCount=4 KnotsCount=2 Degree=3 IsPeriodic=0
    g121: BSplineCurve PolesCount=2 KnotsCount=2 Degree=1 IsPeriodic=0
    g122: BSplineCurve PolesCount=2 KnotsCount=2 Degree=1 IsPeriodic=0
    g123: BSplineCurve PolesCount=4 KnotsCount=2 Degree=3 IsPeriodic=0
    g124: BSplineCurve PolesCount=4 KnotsCount=2 Degree=3 IsPeriodic=0
    g125: BSplineCurve PolesCount=4 KnotsCount=2 Degree=3 IsPeriodic=0
    g126: BSplineCurve PolesCount=4 KnotsCount=2 Degree=3 IsPeriodic=0
    g127: BSplineCurve PolesCount=4 KnotsCount=2 Degree=3 IsPeriodic=0
    g128: BSplineCurve PolesCount=4 KnotsCount=2 Degree=3 IsPeriodic=0
    g129: BSplineCurve PolesCount=4 KnotsCount=2 Degree=3 IsPeriodic=0
    g130: BSplineCurve PolesCount=4 KnotsCount=2 Degree=3 IsPeriodic=0
    g131: BSplineCurve PolesCount=4 KnotsCount=2 Degree=3 IsPeriodic=0
    g132: BSplineCurve PolesCount=4 KnotsCount=2 Degree=3 IsPeriodic=0
    g133: BSplineCurve PolesCount=4 KnotsCount=2 Degree=3 IsPeriodic=0
    g134: BSplineCurve PolesCount=4 KnotsCount=2 Degree=3 IsPeriodic=0
    g135: BSplineCurve PolesCount=2 KnotsCount=2 Degree=1 IsPeriodic=0
    g136: BSplineCurve PolesCount=4 KnotsCount=2 Degree=3 IsPeriodic=0
    g137: BSplineCurve PolesCount=4 KnotsCount=2 Degree=3 IsPeriodic=0
    g138: BSplineCurve PolesCount=4 KnotsCount=2 Degree=3 IsPeriodic=0
    g139: BSplineCurve PolesCount=4 KnotsCount=2 Degree=3 IsPeriodic=0
    g140: BSplineCurve PolesCount=4 KnotsCount=2 Degree=3 IsPeriodic=0
    g141: BSplineCurve PolesCount=4 KnotsCount=2 Degree=3 IsPeriodic=0
    g142: BSplineCurve PolesCount=4 KnotsCount=2 Degree=3 IsPeriodic=0
    g143: BSplineCurve PolesCount=4 KnotsCount=2 Degree=3 IsPeriodic=0
    g144: BSplineCurve PolesCount=4 KnotsCount=2 Degree=3 IsPeriodic=0
    g145: BSplineCurve PolesCount=4 KnotsCount=2 Degree=3 IsPeriodic=0
    g146: BSplineCurve PolesCount=4 KnotsCount=2 Degree=3 IsPeriodic=0
    g147: BSplineCurve PolesCount=4 KnotsCount=2 Degree=3 IsPeriodic=0
    g148: BSplineCurve PolesCount=4 KnotsCount=2 Degree=3 IsPeriodic=0
    g149: BSplineCurve PolesCount=4 KnotsCount=2 Degree=3 IsPeriodic=0
    g150: BSplineCurve PolesCount=4 KnotsCount=2 Degree=3 IsPeriodic=0
    g151: BSplineCurve PolesCount=2 KnotsCount=2 Degree=1 IsPeriodic=0
    g152: BSplineCurve PolesCount=2 KnotsCount=2 Degree=1 IsPeriodic=0
    g153: BSplineCurve PolesCount=4 KnotsCount=2 Degree=3 IsPeriodic=0
    g154: BSplineCurve PolesCount=4 KnotsCount=2 Degree=3 IsPeriodic=0
    g155: BSplineCurve PolesCount=4 KnotsCount=2 Degree=3 IsPeriodic=0
    g156: BSplineCurve PolesCount=2 KnotsCount=2 Degree=1 IsPeriodic=0
    g157: BSplineCurve PolesCount=2 KnotsCount=2 Degree=1 IsPeriodic=0
    g158: BSplineCurve PolesCount=4 KnotsCount=2 Degree=3 IsPeriodic=0
    g159: BSplineCurve PolesCount=4 KnotsCount=2 Degree=3 IsPeriodic=0
    g160: BSplineCurve PolesCount=2 KnotsCount=2 Degree=1 IsPeriodic=0
    g161: BSplineCurve PolesCount=2 KnotsCount=2 Degree=1 IsPeriodic=0
    g162: BSplineCurve PolesCount=2 KnotsCount=2 Degree=1 IsPeriodic=0
    g163: BSplineCurve PolesCount=2 KnotsCount=2 Degree=1 IsPeriodic=0
    g164: BSplineCurve PolesCount=2 KnotsCount=2 Degree=1 IsPeriodic=0
    g165: BSplineCurve PolesCount=2 KnotsCount=2 Degree=1 IsPeriodic=0
    g166: BSplineCurve PolesCount=4 KnotsCount=2 Degree=3 IsPeriodic=0
    g167: BSplineCurve PolesCount=4 KnotsCount=2 Degree=3 IsPeriodic=0
    g168: BSplineCurve PolesCount=4 KnotsCount=2 Degree=3 IsPeriodic=0
    g169: BSplineCurve PolesCount=4 KnotsCount=2 Degree=3 IsPeriodic=0
    g170: BSplineCurve PolesCount=2 KnotsCount=2 Degree=1 IsPeriodic=0
    g171: BSplineCurve PolesCount=2 KnotsCount=2 Degree=1 IsPeriodic=0
    g172: BSplineCurve PolesCount=4 KnotsCount=2 Degree=3 IsPeriodic=0
    g173: BSplineCurve PolesCount=4 KnotsCount=2 Degree=3 IsPeriodic=0
    g174: BSplineCurve PolesCount=4 KnotsCount=2 Degree=3 IsPeriodic=0
    g175: BSplineCurve PolesCount=2 KnotsCount=2 Degree=1 IsPeriodic=0
    g176: BSplineCurve PolesCount=2 KnotsCount=2 Degree=1 IsPeriodic=0
    g177: BSplineCurve PolesCount=4 KnotsCount=2 Degree=3 IsPeriodic=0
    g178: BSplineCurve PolesCount=4 KnotsCount=2 Degree=3 IsPeriodic=0
    g179: BSplineCurve PolesCount=2 KnotsCount=2 Degree=1 IsPeriodic=0
    g180: BSplineCurve PolesCount=2 KnotsCount=2 Degree=1 IsPeriodic=0
    g181: BSplineCurve PolesCount=4 KnotsCount=2 Degree=3 IsPeriodic=0
    g182: BSplineCurve PolesCount=4 KnotsCount=2 Degree=3 IsPeriodic=0
    g183: BSplineCurve PolesCount=4 KnotsCount=2 Degree=3 IsPeriodic=0
    g184: BSplineCurve PolesCount=4 KnotsCount=2 Degree=3 IsPeriodic=0
    g185: BSplineCurve PolesCount=4 KnotsCount=2 Degree=3 IsPeriodic=0
    g186: BSplineCurve PolesCount=2 KnotsCount=2 Degree=1 IsPeriodic=0
    g187: BSplineCurve PolesCount=2 KnotsCount=2 Degree=1 IsPeriodic=0
    g188: BSplineCurve PolesCount=2 KnotsCount=2 Degree=1 IsPeriodic=0
    g189: BSplineCurve PolesCount=2 KnotsCount=2 Degree=1 IsPeriodic=0
    g190: BSplineCurve PolesCount=2 KnotsCount=2 Degree=1 IsPeriodic=0
    g191: BSplineCurve PolesCount=2 KnotsCount=2 Degree=1 IsPeriodic=0
    g192: BSplineCurve PolesCount=2 KnotsCount=2 Degree=1 IsPeriodic=0
    g193: BSplineCurve PolesCount=2 KnotsCount=2 Degree=1 IsPeriodic=0
    g194: BSplineCurve PolesCount=4 KnotsCount=2 Degree=3 IsPeriodic=0
    g195: BSplineCurve PolesCount=4 KnotsCount=2 Degree=3 IsPeriodic=0
    g196: BSplineCurve PolesCount=4 KnotsCount=2 Degree=3 IsPeriodic=0
    g197: BSplineCurve PolesCount=4 KnotsCount=2 Degree=3 IsPeriodic=0
    g198: BSplineCurve PolesCount=2 KnotsCount=2 Degree=1 IsPeriodic=0
    g199: BSplineCurve PolesCount=4 KnotsCount=2 Degree=3 IsPeriodic=0
    g200: BSplineCurve PolesCount=4 KnotsCount=2 Degree=3 IsPeriodic=0
    g201: BSplineCurve PolesCount=4 KnotsCount=2 Degree=3 IsPeriodic=0
    g202: BSplineCurve PolesCount=4 KnotsCount=2 Degree=3 IsPeriodic=0
    g203: BSplineCurve PolesCount=4 KnotsCount=2 Degree=3 IsPeriodic=0
    g204: BSplineCurve PolesCount=4 KnotsCount=2 Degree=3 IsPeriodic=0
    g205: BSplineCurve PolesCount=4 KnotsCount=2 Degree=3 IsPeriodic=0
    g206: BSplineCurve PolesCount=4 KnotsCount=2 Degree=3 IsPeriodic=0
    g207: BSplineCurve PolesCount=4 KnotsCount=2 Degree=3 IsPeriodic=0
    g208: BSplineCurve PolesCount=4 KnotsCount=2 Degree=3 IsPeriodic=0
  constraints (213):
    c: Coincident(g0,g1)
    c: Coincident(g1,g2)
    c: Coincident(g2,g0)
    c: Coincident(g3,g4)
    c: Coincident(g4,g5)
    c: Coincident(g5,g3)
    c: Coincident(g6,g7)
    c: Coincident(g7,g8)
    c: Coincident(g8,g9)
    c: Coincident(g9,g6)
    c: Coincident(g10,g11)
    c: Coincident(g11,g12)
    c: Coincident(g12,g13)
    c: Coincident(g13,g14)
    c: Coincident(g14,g15)
    c: Coincident(g15,g16)
    c: Coincident(g16,g17)
    c: Coincident(g17,g18)
    c: Coincident(g18,g19)
    c: Coincident(g19,g20)
    c: Coincident(g20,g21)
    c: Coincident(g21,g22)
    c: Coincident(g22,g10)
    c: Coincident(g23,g24)
    c: Coincident(g24,g25)
    c: Coincident(g25,g26)
    c: Coincident(g26,g27)
    c: Coincident(g27,g23)
    c: Coincident(g28,g29)
    c: Coincident(g29,g30)
    c: Coincident(g30,g31)
    c: Coincident(g31,g32)
    c: Coincident(g32,g33)
    c: Coincident(g33,g34)
    c: Coincident(g34,g35)
    c: Coincident(g35,g36)
    c: Coincident(g36,g37)
    c: Coincident(g37,g28)
    c: Coincident(g38,g39)
    c: Coincident(g39,g40)
    c: Coincident(g40,g38)
    c: Coincident(g41,g42)
    c: Coincident(g42,g43)
    c: Coincident(g43,g44)
    c: Coincident(g44,g45)
    c: Coincident(g45,g46)
    c: Coincident(g46,g47)
    c: Coincident(g47,g48)
    c: Coincident(g48,g49)
    c: Coincident(g49,g50)
    c: Coincident(g50,g51)
    c: Coincident(g51,g52)
    c: Coincident(g52,g53)
    c: Coincident(g53,g54)
    c: Coincident(g54,g55)
    c: Coincident(g55,g56)
    c: Coincident(g56,g57)
    c: Coincident(g57,g58)
    c: Coincident(g58,g59)
    c: Coincident(g59,g60)
    c: Coincident(g60,g61)
    c: Coincident(g61,g62)
    c: Coincident(g62,g63)
    c: Coincident(g63,g64)
    c: Coincident(g64,g65)
    c: Coincident(g65,g66)
    c: Coincident(g66,g67)
    c: Coincident(g67,g68)
    c: Coincident(g68,g69)
    c: Coincident(g69,g70)
    c: Coincident(g70,g71)
    c: Coincident(g71,g72)
    c: Coincident(g72,g73)
    c: Coincident(g73,g74)
    c: Coincident(g74,g75)
    c: Coincident(g75,g76)
    c: Coincident(g76,g77)
    c: Coincident(g77,g78)
    c: Coincident(g78,g79)
    c: Coincident(g79,g80)
    c: Coincident(g80,g81)
    c: Coincident(g81,g82)
    c: Coincident(g82,g83)
    c: Coincident(g83,g84)
    c: Coincident(g84,g85)
    c: Coincident(g85,g86)
    c: Coincident(g86,g41)
    c: Coincident(g87,g88)
    c: Coincident(g88,g89)
    c: Coincident(g89,g87)
    c: Coincident(g90,g91)
    c: Coincident(g91,g92)
    c: Coincident(g92,g90)
    c: Coincident(g93,g94)
    c: Coincident(g94,g95)
    c: Coincident(g95,g96)
    c: Coincident(g96,g97)
    c: Coincident(g97,g98)
    c: Coincident(g98,g99)
    c: Coincident(g99,g100)
    c: Coincident(g100,g101)
    c: Coincident(g101,g102)
    c: Coincident(g102,g103)
    c: Coincident(g103,g104)
    c: Coincident(g104,g105)
    c: Coincident(g105,g106)
    c: Coincident(g106,g107)
    c: Coincident(g107,g108)
    c: Coincident(g108,g109)
    c: Coincident(g109,g110)
    c: Coincident(g110,g111)
    c: Coincident(g111,g112)
    c: Coincident(g112,g113)
    c: Coincident(g113,g114)
    c: Coincident(g114,g115)
    c: Coincident(g115,g116)
    c: Coincident(g116,g117)
    c: Coincident(g117,g118)
    c: Coincident(g118,g119)
    c: Coincident(g119,g120)
    c: Coincident(g120,g121)
    c: Coincident(g121,g122)
    c: Coincident(g122,g123)
    c: Coincident(g123,g124)
    c: Coincident(g124,g93)
    c: Coincident(g125,g126)
    c: Coincident(g126,g127)
    c: Coincident(g127,g128)
    c: Coincident(g128,g129)
    c: Coincident(g129,g130)
    c: Coincident(g130,g131)
    c: Coincident(g131,g125)
    c: Coincident(g132,g133)
    c: Coincident(g133,g134)
    c: Coincident(g134,g132)
    c: Coincident(g135,g136)
    c: Coincident(g136,g137)
    c: Coincident(g137,g138)
    c: Coincident(g138,g135)
    c: Coincident(g139,g140)
    c: Coincident(g140,g141)
    c: Coincident(g141,g139)
    c: Coincident(g142,g143)
    c: Coincident(g143,g144)
    c: Coincident(g144,g145)
    c: Coincident(g145,g146)
    c: Coincident(g146,g147)
    c: Coincident(g147,g148)
    c: Coincident(g148,g149)
    c: Coincident(g149,g150)
    c: Coincident(g150,g151)
    c: Coincident(g151,g152)
    c: Coincident(g152,g153)
    c: Coincident(g153,g154)
    c: Coincident(g154,g155)
    c: Coincident(g155,g156)
    c: Coincident(g156,g157)
    c: Coincident(g157,g158)
    c: Coincident(g158,g159)
    c: Coincident(g159,g160)
    c: Coincident(g160,g161)
    c: Coincident(g161,g162)
    c: Coincident(g162,g163)
    c: Coincident(g163,g164)
    c: Coincident(g164,g165)
    c: Coincident(g165,g166)
    c: Coincident(g166,g167)
    c: Coincident(g167,g168)
    c: Coincident(g168,g169)
    c: Coincident(g169,g170)
    c: Coincident(g170,g171)
    c: Coincident(g171,g172)
    c: Coincident(g172,g173)
    c: Coincident(g173,g174)
    c: Coincident(g174,g175)
    c: Coincident(g175,g176)
    c: Coincident(g176,g177)
    c: Coincident(g177,g178)
    c: Coincident(g178,g179)
    c: Coincident(g179,g180)
    c: Coincident(g180,g181)
    c: Coincident(g181,g182)
    c: Coincident(g182,g183)
    c: Coincident(g183,g184)
    c: Coincident(g184,g185)
    c: Coincident(g185,g186)
    c: Coincident(g186,g187)
    c: Coincident(g187,g188)
    c: Coincident(g188,g189)
    c: Coincident(g189,g190)
    c: Coincident(g190,g191)
    c: Coincident(g191,g192)
    c: Coincident(g192,g193)
    c: Coincident(g193,g194)
    c: Coincident(g194,g195)
    c: Coincident(g195,g196)
    c: Coincident(g196,g197)
    c: Coincident(g197,g198)
    c: Coincident(g198,g142)
    c: Coincident(g199,g200)
    c: Coincident(g200,g201)
    c: Coincident(g201,g202)
    c: Coincident(g202,g199)
    c: Coincident(g203,g204)
    c: Coincident(g204,g205)
    c: Coincident(g205,g203)
    c: Coincident(g206,g207)
    c: Coincident(g207,g208)
    c: Coincident(g208,g206)
    c: Coincident(g8,g6)
    c: Coincident(g197,g142)
    c: Coincident(g28,g28)
    c: Coincident(g135,g135)
FEATURE [Sketcher::SketchObject] Sketch050  label="Vortox-Sketch"
  ArcFitTolerance = 1e-06
  FullyConstrained = false
  MakeInternals = false
  Placement = pos=(-15.6145,11.1904,0) rot=(0,0,1;0rad)
  expr: .Placement.Base.x = -(.Shape.BoundBox.XLength / 2)
  expr: .Placement.Base.y = .Shape.BoundBox.YLength / 2
  sketch-geometry (165):
    g0: BSplineCurve PolesCount=4 KnotsCount=2 Degree=3 IsPeriodic=0
    g1: BSplineCurve PolesCount=4 KnotsCount=2 Degree=3 IsPeriodic=0
    g2: BSplineCurve PolesCount=4 KnotsCount=2 Degree=3 IsPeriodic=0
    g3: BSplineCurve PolesCount=4 KnotsCount=2 Degree=3 IsPeriodic=0
    g4: BSplineCurve PolesCount=4 KnotsCount=2 Degree=3 IsPeriodic=0
    g5: BSplineCurve PolesCount=4 KnotsCount=2 Degree=3 IsPeriodic=0
    g6: BSplineCurve PolesCount=4 KnotsCount=2 Degree=3 IsPeriodic=0
    g7: BSplineCurve PolesCount=4 KnotsCount=2 Degree=3 IsPeriodic=0
    g8: BSplineCurve PolesCount=4 KnotsCount=2 Degree=3 IsPeriodic=0
    g9: BSplineCurve PolesCount=4 KnotsCount=2 Degree=3 IsPeriodic=0
    g10: BSplineCurve PolesCount=4 KnotsCount=2 Degree=3 IsPeriodic=0
    g11: BSplineCurve PolesCount=4 KnotsCount=2 Degree=3 IsPeriodic=0
    g12: BSplineCurve PolesCount=4 KnotsCount=2 Degree=3 IsPeriodic=0
    g13: BSplineCurve PolesCount=4 KnotsCount=2 Degree=3 IsPeriodic=0
    g14: BSplineCurve PolesCount=4 KnotsCount=2 Degree=3 IsPeriodic=0
    g15: BSplineCurve PolesCount=4 KnotsCount=2 Degree=3 IsPeriodic=0
    g16: BSplineCurve PolesCount=4 KnotsCount=2 Degree=3 IsPeriodic=0
    g17: BSplineCurve PolesCount=2 KnotsCount=2 Degree=1 IsPeriodic=0
    g18: BSplineCurve PolesCount=2 KnotsCount=2 Degree=1 IsPeriodic=0
    g19: BSplineCurve PolesCount=2 KnotsCount=2 Degree=1 IsPeriodic=0
    g20: BSplineCurve PolesCount=2 KnotsCount=2 Degree=1 IsPeriodic=0
    g21: BSplineCurve PolesCount=4 KnotsCount=2 Degree=3 IsPeriodic=0
    g22: BSplineCurve PolesCount=4 KnotsCount=2 Degree=3 IsPeriodic=0
    g23: BSplineCurve PolesCount=4 KnotsCount=2 Degree=3 IsPeriodic=0
    g24: BSplineCurve PolesCount=4 KnotsCount=2 Degree=3 IsPeriodic=0
    g25: BSplineCurve PolesCount=4 KnotsCount=2 Degree=3 IsPeriodic=0
    g26: BSplineCurve PolesCount=2 KnotsCount=2 Degree=1 IsPeriodic=0
    g27: BSplineCurve PolesCount=2 KnotsCount=2 Degree=1 IsPeriodic=0
    g28: BSplineCurve PolesCount=4 KnotsCount=2 Degree=3 IsPeriodic=0
    g29: BSplineCurve PolesCount=4 KnotsCount=2 Degree=3 IsPeriodic=0
    g30: BSplineCurve PolesCount=4 KnotsCount=2 Degree=3 IsPeriodic=0
    g31: BSplineCurve PolesCount=4 KnotsCount=2 Degree=3 IsPeriodic=0
    g32: BSplineCurve PolesCount=4 KnotsCount=2 Degree=3 IsPeriodic=0
    g33: BSplineCurve PolesCount=4 KnotsCount=2 Degree=3 IsPeriodic=0
    g34: BSplineCurve PolesCount=4 KnotsCount=2 Degree=3 IsPeriodic=0
    g35: BSplineCurve PolesCount=4 KnotsCount=2 Degree=3 IsPeriodic=0
    g36: BSplineCurve PolesCount=4 KnotsCount=2 Degree=3 IsPeriodic=0
    g37: BSplineCurve PolesCount=4 KnotsCount=2 Degree=3 IsPeriodic=0
    g38: BSplineCurve PolesCount=4 KnotsCount=2 Degree=3 IsPeriodic=0
    g39: BSplineCurve PolesCount=4 KnotsCount=2 Degree=3 IsPeriodic=0
    g40: BSplineCurve PolesCount=4 KnotsCount=2 Degree=3 IsPeriodic=0
    g41: BSplineCurve PolesCount=4 KnotsCount=2 Degree=3 IsPeriodic=0
    g42: BSplineCurve PolesCount=4 KnotsCount=2 Degree=3 IsPeriodic=0
    g43: BSplineCurve PolesCount=4 KnotsCount=2 Degree=3 IsPeriodic=0
    g44: BSplineCurve PolesCount=4 KnotsCount=2 Degree=3 IsPeriodic=0
    g45: BSplineCurve PolesCount=4 KnotsCount=2 Degree=3 IsPeriodic=0
    g46: BSplineCurve PolesCount=4 KnotsCount=2 Degree=3 IsPeriodic=0
    g47: BSplineCurve PolesCount=4 KnotsCount=2 Degree=3 IsPeriodic=0
    g48: BSplineCurve PolesCount=4 KnotsCount=2 Degree=3 IsPeriodic=0
    g49: BSplineCurve PolesCount=4 KnotsCount=2 Degree=3 IsPeriodic=0
    g50: BSplineCurve PolesCount=4 KnotsCount=2 Degree=3 IsPeriodic=0
    g51: BSplineCurve PolesCount=4 KnotsCount=2 Degree=3 IsPeriodic=0
    g52: BSplineCurve PolesCount=4 KnotsCount=2 Degree=3 IsPeriodic=0
    g53: BSplineCurve PolesCount=4 KnotsCount=2 Degree=3 IsPeriodic=0
    g54: BSplineCurve PolesCount=4 KnotsCount=2 Degree=3 IsPeriodic=0
    g55: BSplineCurve PolesCount=4 KnotsCount=2 Degree=3 IsPeriodic=0
    g56: BSplineCurve PolesCount=4 KnotsCount=2 Degree=3 IsPeriodic=0
    g57: BSplineCurve PolesCount=4 KnotsCount=2 Degree=3 IsPeriodic=0
    g58: BSplineCurve PolesCount=4 KnotsCount=2 Degree=3 IsPeriodic=0
    g59: BSplineCurve PolesCount=4 KnotsCount=2 Degree=3 IsPeriodic=0
    g60: BSplineCurve PolesCount=4 KnotsCount=2 Degree=3 IsPeriodic=0
    g61: BSplineCurve PolesCount=4 KnotsCount=2 Degree=3 IsPeriodic=0
    g62: BSplineCurve PolesCount=2 KnotsCount=2 Degree=1 IsPeriodic=0
    g63: BSplineCurve PolesCount=2 KnotsCount=2 Degree=1 IsPeriodic=0
    g64: BSplineCurve PolesCount=4 KnotsCount=2 Degree=3 IsPeriodic=0
    g65: BSplineCurve PolesCount=4 KnotsCount=2 Degree=3 IsPeriodic=0
    g66: BSplineCurve PolesCount=4 KnotsCount=2 Degree=3 IsPeriodic=0
    g67: BSplineCurve PolesCount=4 KnotsCount=2 Degree=3 IsPeriodic=0
    g68: BSplineCurve PolesCount=4 KnotsCount=2 Degree=3 IsPeriodic=0
    g69: BSplineCurve PolesCount=4 KnotsCount=2 Degree=3 IsPeriodic=0
    g70: BSplineCurve PolesCount=4 KnotsCount=2 Degree=3 IsPeriodic=0
    g71: BSplineCurve PolesCount=4 KnotsCount=2 Degree=3 IsPeriodic=0
    g72: BSplineCurve PolesCount=4 KnotsCount=2 Degree=3 IsPeriodic=0
    g73: BSplineCurve PolesCount=2 KnotsCount=2 Degree=1 IsPeriodic=0
    g74: BSplineCurve PolesCount=2 KnotsCount=2 Degree=1 IsPeriodic=0
    g75: BSplineCurve PolesCount=4 KnotsCount=2 Degree=3 IsPeriodic=0
    g76: BSplineCurve PolesCount=4 KnotsCount=2 Degree=3 IsPeriodic=0
    g77: BSplineCurve PolesCount=2 KnotsCount=2 Degree=1 IsPeriodic=0
    g78: BSplineCurve PolesCount=2 KnotsCount=2 Degree=1 IsPeriodic=0
    g79: BSplineCurve PolesCount=4 KnotsCount=2 Degree=3 IsPeriodic=0
    g80: BSplineCurve PolesCount=4 KnotsCount=2 Degree=3 IsPeriodic=0
    g81: BSplineCurve PolesCount=4 KnotsCount=2 Degree=3 IsPeriodic=0
    g82: BSplineCurve PolesCount=4 KnotsCount=2 Degree=3 IsPeriodic=0
    g83: BSplineCurve PolesCount=4 KnotsCount=2 Degree=3 IsPeriodic=0
    g84: BSplineCurve PolesCount=4 KnotsCount=2 Degree=3 IsPeriodic=0
    g85: BSplineCurve PolesCount=4 KnotsCount=2 Degree=3 IsPeriodic=0
    g86: BSplineCurve PolesCount=4 KnotsCount=2 Degree=3 IsPeriodic=0
    g87: BSplineCurve PolesCount=2 KnotsCount=2 Degree=1 IsPeriodic=0
    g88: BSplineCurve PolesCount=2 KnotsCount=2 Degree=1 IsPeriodic=0
    g89: BSplineCurve PolesCount=4 KnotsCount=2 Degree=3 IsPeriodic=0
    g90: BSplineCurve PolesCount=4 KnotsCount=2 Degree=3 IsPeriodic=0
    g91: BSplineCurve PolesCount=2 KnotsCount=2 Degree=1 IsPeriodic=0
    g92: BSplineCurve PolesCount=2 KnotsCount=2 Degree=1 IsPeriodic=0
    g93: BSplineCurve PolesCount=4 KnotsCount=2 Degree=3 IsPeriodic=0
    g94: BSplineCurve PolesCount=4 KnotsCount=2 Degree=3 IsPeriodic=0
    g95: BSplineCurve PolesCount=4 KnotsCount=2 Degree=3 IsPeriodic=0
    g96: BSplineCurve PolesCount=4 KnotsCount=2 Degree=3 IsPeriodic=0
    g97: BSplineCurve PolesCount=4 KnotsCount=2 Degree=3 IsPeriodic=0
    g98: BSplineCurve PolesCount=4 KnotsCount=2 Degree=3 IsPeriodic=0
    g99: BSplineCurve PolesCount=2 KnotsCount=2 Degree=1 IsPeriodic=0
    g100: BSplineCurve PolesCount=2 KnotsCount=2 Degree=1 IsPeriodic=0
    g101: BSplineCurve PolesCount=4 KnotsCount=2 Degree=3 IsPeriodic=0
    g102: BSplineCurve PolesCount=4 KnotsCount=2 Degree=3 IsPeriodic=0
    g103: BSplineCurve PolesCount=4 KnotsCount=2 Degree=3 IsPeriodic=0
    g104: BSplineCurve PolesCount=4 KnotsCount=2 Degree=3 IsPeriodic=0
    g105: BSplineCurve PolesCount=4 KnotsCount=2 Degree=3 IsPeriodic=0
    g106: BSplineCurve PolesCount=4 KnotsCount=2 Degree=3 IsPeriodic=0
    g107: BSplineCurve PolesCount=4 KnotsCount=2 Degree=3 IsPeriodic=0
    g108: BSplineCurve PolesCount=2 KnotsCount=2 Degree=1 IsPeriodic=0
    g109: BSplineCurve PolesCount=4 KnotsCount=2 Degree=3 IsPeriodic=0
    g110: BSplineCurve PolesCount=2 KnotsCount=2 Degree=1 IsPeriodic=0
    g111: BSplineCurve PolesCount=2 KnotsCount=2 Degree=1 IsPeriodic=0
    g112: BSplineCurve PolesCount=4 KnotsCount=2 Degree=3 IsPeriodic=0
    g113: BSplineCurve PolesCount=4 KnotsCount=2 Degree=3 IsPeriodic=0
    g114: BSplineCurve PolesCount=4 KnotsCount=2 Degree=3 IsPeriodic=0
    g115: BSplineCurve PolesCount=4 KnotsCount=2 Degree=3 IsPeriodic=0
    g116: BSplineCurve PolesCount=4 KnotsCount=2 Degree=3 IsPeriodic=0
    g117: BSplineCurve PolesCount=4 KnotsCount=2 Degree=3 IsPeriodic=0
    g118: BSplineCurve PolesCount=4 KnotsCount=2 Degree=3 IsPeriodic=0
    g119: BSplineCurve PolesCount=4 KnotsCount=2 Degree=3 IsPeriodic=0
    g120: BSplineCurve PolesCount=4 KnotsCount=2 Degree=3 IsPeriodic=0
    g121: BSplineCurve PolesCount=4 KnotsCount=2 Degree=3 IsPeriodic=0
    g122: BSplineCurve PolesCount=4 KnotsCount=2 Degree=3 IsPeriodic=0
    g123: BSplineCurve PolesCount=4 KnotsCount=2 Degree=3 IsPeriodic=0
    g124: BSplineCurve PolesCount=4 KnotsCount=2 Degree=3 IsPeriodic=0
    g125: BSplineCurve PolesCount=4 KnotsCount=2 Degree=3 IsPeriodic=0
    g126: BSplineCurve PolesCount=4 KnotsCount=2 Degree=3 IsPeriodic=0
    g127: BSplineCurve PolesCount=4 KnotsCount=2 Degree=3 IsPeriodic=0
    g128: BSplineCurve PolesCount=4 KnotsCount=2 Degree=3 IsPeriodic=0
    g129: BSplineCurve PolesCount=4 KnotsCount=2 Degree=3 IsPeriodic=0
    g130: BSplineCurve PolesCount=4 KnotsCount=2 Degree=3 IsPeriodic=0
    g131: BSplineCurve PolesCount=4 KnotsCount=2 Degree=3 IsPeriodic=0
    g132: BSplineCurve PolesCount=4 KnotsCount=2 Degree=3 IsPeriodic=0
    g133: BSplineCurve PolesCount=4 KnotsCount=2 Degree=3 IsPeriodic=0
    g134: BSplineCurve PolesCount=4 KnotsCount=2 Degree=3 IsPeriodic=0
    g135: BSplineCurve PolesCount=4 KnotsCount=2 Degree=3 IsPeriodic=0
    g136: BSplineCurve PolesCount=4 KnotsCount=2 Degree=3 IsPeriodic=0
    g137: BSplineCurve PolesCount=4 KnotsCount=2 Degree=3 IsPeriodic=0
    g138: BSplineCurve PolesCount=4 KnotsCount=2 Degree=3 IsPeriodic=0
    g139: BSplineCurve PolesCount=4 KnotsCount=2 Degree=3 IsPeriodic=0
    g140: BSplineCurve PolesCount=4 KnotsCount=2 Degree=3 IsPeriodic=0
    g141: BSplineCurve PolesCount=4 KnotsCount=2 Degree=3 IsPeriodic=0
    g142: BSplineCurve PolesCount=4 KnotsCount=2 Degree=3 IsPeriodic=0
    g143: BSplineCurve PolesCount=4 KnotsCount=2 Degree=3 IsPeriodic=0
    g144: BSplineCurve PolesCount=4 KnotsCount=2 Degree=3 IsPeriodic=0
    g145: BSplineCurve PolesCount=4 KnotsCount=2 Degree=3 IsPeriodic=0
    g146: BSplineCurve PolesCount=4 KnotsCount=2 Degree=3 IsPeriodic=0
    g147: BSplineCurve PolesCount=4 KnotsCount=2 Degree=3 IsPeriodic=0
    g148: BSplineCurve PolesCount=4 KnotsCount=2 Degree=3 IsPeriodic=0
    g149: BSplineCurve PolesCount=2 KnotsCount=2 Degree=1 IsPeriodic=0
    g150: BSplineCurve PolesCount=2 KnotsCount=2 Degree=1 IsPeriodic=0
    g151: BSplineCurve PolesCount=4 KnotsCount=2 Degree=3 IsPeriodic=0
    g152: BSplineCurve PolesCount=4 KnotsCount=2 Degree=3 IsPeriodic=0
    g153: BSplineCurve PolesCount=4 KnotsCount=2 Degree=3 IsPeriodic=0
    g154: BSplineCurve PolesCount=4 KnotsCount=2 Degree=3 IsPeriodic=0
    g155: BSplineCurve PolesCount=4 KnotsCount=2 Degree=3 IsPeriodic=0
    g156: BSplineCurve PolesCount=4 KnotsCount=2 Degree=3 IsPeriodic=0
    g157: BSplineCurve PolesCount=4 KnotsCount=2 Degree=3 IsPeriodic=0
    g158: BSplineCurve PolesCount=4 KnotsCount=2 Degree=3 IsPeriodic=0
    g159: BSplineCurve PolesCount=4 KnotsCount=2 Degree=3 IsPeriodic=0
    g160: BSplineCurve PolesCount=4 KnotsCount=2 Degree=3 IsPeriodic=0
    g161: BSplineCurve PolesCount=4 KnotsCount=2 Degree=3 IsPeriodic=0
    g162: BSplineCurve PolesCount=4 KnotsCount=2 Degree=3 IsPeriodic=0
    g163: BSplineCurve PolesCount=4 KnotsCount=2 Degree=3 IsPeriodic=0
    g164: BSplineCurve PolesCount=4 KnotsCount=2 Degree=3 IsPeriodic=0
  constraints (165):
    c: Coincident(g0,g1)
    c: Coincident(g1,g2)
    c: Coincident(g2,g3)
    c: Coincident(g3,g4)
    c: Coincident(g4,g5)
    c: Coincident(g5,g6)
    c: Coincident(g6,g7)
    c: Coincident(g7,g8)
    c: Coincident(g8,g9)
    c: Coincident(g9,g10)
    c: Coincident(g10,g11)
    c: Coincident(g11,g12)
    c: Coincident(g12,g13)
    c: Coincident(g13,g14)
    c: Coincident(g14,g15)
    c: Coincident(g15,g16)
    c: Coincident(g16,g17)
    c: Coincident(g17,g18)
    c: Coincident(g18,g19)
    c: Coincident(g19,g20)
    c: Coincident(g20,g21)
    c: Coincident(g21,g22)
    c: Coincident(g22,g23)
    c: Coincident(g23,g0)
    c: Coincident(g24,g25)
    c: Coincident(g25,g26)
    c: Coincident(g26,g27)
    c: Coincident(g27,g28)
    c: Coincident(g28,g29)
    c: Coincident(g29,g30)
    c: Coincident(g30,g31)
    c: Coincident(g31,g24)
    c: Coincident(g32,g33)
    c: Coincident(g33,g34)
    c: Coincident(g34,g35)
    c: Coincident(g35,g36)
    c: Coincident(g36,g37)
    c: Coincident(g37,g38)
    c: Coincident(g38,g39)
    c: Coincident(g39,g40)
    c: Coincident(g40,g32)
    c: Coincident(g41,g42)
    c: Coincident(g42,g43)
    c: Coincident(g43,g44)
    c: Coincident(g44,g45)
    c: Coincident(g45,g46)
    c: Coincident(g46,g47)
    c: Coincident(g47,g48)
    c: Coincident(g48,g49)
    c: Coincident(g49,g50)
    c: Coincident(g50,g51)
    c: Coincident(g51,g52)
    c: Coincident(g52,g53)
    c: Coincident(g53,g41)
    c: Coincident(g54,g55)
    c: Coincident(g55,g56)
    c: Coincident(g56,g57)
    c: Coincident(g57,g58)
    c: Coincident(g58,g59)
    c: Coincident(g59,g60)
    c: Coincident(g60,g61)
    c: Coincident(g61,g62)
    c: Coincident(g62,g63)
    c: Coincident(g63,g64)
    c: Coincident(g65,g66)
    c: Coincident(g66,g67)
    c: Coincident(g67,g68)
    c: Coincident(g68,g69)
    c: Coincident(g69,g70)
    c: Coincident(g70,g71)
    c: Coincident(g71,g72)
    c: Coincident(g72,g73)
    c: Coincident(g73,g74)
    c: Coincident(g74,g75)
    c: Coincident(g75,g76)
    c: Coincident(g76,g77)
    c: Coincident(g77,g78)
    c: Coincident(g78,g79)
    c: Coincident(g79,g80)
    c: Coincident(g80,g81)
    c: Coincident(g81,g82)
    c: Coincident(g82,g83)
    c: Coincident(g83,g84)
    c: Coincident(g84,g85)
    c: Coincident(g85,g86)
    c: Coincident(g86,g87)
    c: Coincident(g87,g88)
    c: Coincident(g88,g89)
    c: Coincident(g89,g65)
    c: Coincident(g90,g91)
    c: Coincident(g91,g92)
    c: Coincident(g92,g93)
    c: Coincident(g93,g94)
    c: Coincident(g94,g95)
    c: Coincident(g95,g96)
    c: Coincident(g97,g98)
    c: Coincident(g98,g99)
    c: Coincident(g99,g100)
    c: Coincident(g100,g101)
    c: Coincident(g101,g102)
    c: Coincident(g102,g103)
    c: Coincident(g103,g97)
    c: Coincident(g104,g105)
    c: Coincident(g105,g106)
    c: Coincident(g106,g107)
    c: Coincident(g107,g108)
    c: Coincident(g108,g104)
    c: Coincident(g109,g110)
    c: Coincident(g110,g111)
    c: Coincident(g111,g112)
    c: Coincident(g112,g113)
    c: Coincident(g113,g114)
    c: Coincident(g114,g115)
    c: Coincident(g116,g117)
    c: Coincident(g117,g118)
    c: Coincident(g118,g119)
    c: Coincident(g119,g120)
    c: Coincident(g120,g121)
    c: Coincident(g121,g122)
    c: Coincident(g122,g123)
    c: Coincident(g123,g124)
    c: Coincident(g124,g125)
    c: Coincident(g125,g126)
    c: Coincident(g126,g127)
    c: Coincident(g127,g128)
    c: Coincident(g128,g129)
    c: Coincident(g129,g130)
    c: Coincident(g130,g131)
    c: Coincident(g131,g132)
    c: Coincident(g132,g133)
    c: Coincident(g133,g134)
    c: Coincident(g134,g135)
    c: Coincident(g135,g136)
    c: Coincident(g136,g137)
    c: Coincident(g137,g138)
    c: Coincident(g138,g139)
    c: Coincident(g139,g140)
    c: Coincident(g140,g141)
    c: Coincident(g141,g142)
    c: Coincident(g142,g143)
    c: Coincident(g143,g144)
    c: Coincident(g144,g145)
    c: Coincident(g145,g146)
    c: Coincident(g146,g147)
    c: Coincident(g147,g148)
    c: Coincident(g148,g149)
    c: Coincident(g149,g150)
    c: Coincident(g150,g151)
    c: Coincident(g151,g152)
    c: Coincident(g152,g153)
    c: Coincident(g153,g154)
    c: Coincident(g154,g155)
    c: Coincident(g155,g156)
    c: Coincident(g156,g157)
    c: Coincident(g157,g158)
    c: Coincident(g158,g159)
    c: Coincident(g159,g160)
    c: Coincident(g161,g162)
    c: Coincident(g162,g163)
    c: Coincident(g163,g164)
    c: Coincident(g164,g161)
    c: Coincident(g64,g54)
    c: Coincident(g115,g109)
    c: Coincident(g160,g116)
    c: Coincident(g90,g96)
FEATURE [Sketcher::SketchObject] Sketch051  label="Witch-Sketch"
  ArcFitTolerance = 1e-06
  FullyConstrained = false
  MakeInternals = false
  Placement = pos=(-14.8947,9.87372,0) rot=(0,0,1;0rad)
  expr: .Placement.Base.x = -(.Shape.BoundBox.XLength / 2)
  expr: .Placement.Base.y = .Shape.BoundBox.YLength / 2
  sketch-geometry (342):
    g0: BSplineCurve PolesCount=4 KnotsCount=2 Degree=3 IsPeriodic=0
    g1: BSplineCurve PolesCount=4 KnotsCount=2 Degree=3 IsPeriodic=0
    g2: BSplineCurve PolesCount=4 KnotsCount=2 Degree=3 IsPeriodic=0
    g3: BSplineCurve PolesCount=4 KnotsCount=2 Degree=3 IsPeriodic=0
    g4: BSplineCurve PolesCount=4 KnotsCount=2 Degree=3 IsPeriodic=0
    g5: BSplineCurve PolesCount=4 KnotsCount=2 Degree=3 IsPeriodic=0
    g6: BSplineCurve PolesCount=4 KnotsCount=2 Degree=3 IsPeriodic=0
    g7: BSplineCurve PolesCount=4 KnotsCount=2 Degree=3 IsPeriodic=0
    g8: BSplineCurve PolesCount=4 KnotsCount=2 Degree=3 IsPeriodic=0
    g9: BSplineCurve PolesCount=4 KnotsCount=2 Degree=3 IsPeriodic=0
    g10: BSplineCurve PolesCount=4 KnotsCount=2 Degree=3 IsPeriodic=0
    g11: BSplineCurve PolesCount=4 KnotsCount=2 Degree=3 IsPeriodic=0
    g12: BSplineCurve PolesCount=4 KnotsCount=2 Degree=3 IsPeriodic=0
    g13: BSplineCurve PolesCount=4 KnotsCount=2 Degree=3 IsPeriodic=0
    g14: BSplineCurve PolesCount=4 KnotsCount=2 Degree=3 IsPeriodic=0
    g15: BSplineCurve PolesCount=4 KnotsCount=2 Degree=3 IsPeriodic=0
    g16: BSplineCurve PolesCount=4 KnotsCount=2 Degree=3 IsPeriodic=0
    g17: BSplineCurve PolesCount=4 KnotsCount=2 Degree=3 IsPeriodic=0
    g18: BSplineCurve PolesCount=2 KnotsCount=2 Degree=1 IsPeriodic=0
    g19: BSplineCurve PolesCount=2 KnotsCount=2 Degree=1 IsPeriodic=0
    g20: BSplineCurve PolesCount=2 KnotsCount=2 Degree=1 IsPeriodic=0
    g21: BSplineCurve PolesCount=2 KnotsCount=2 Degree=1 IsPeriodic=0
    g22: BSplineCurve PolesCount=4 KnotsCount=2 Degree=3 IsPeriodic=0
    g23: BSplineCurve PolesCount=4 KnotsCount=2 Degree=3 IsPeriodic=0
    g24: BSplineCurve PolesCount=4 KnotsCount=2 Degree=3 IsPeriodic=0
    g25: BSplineCurve PolesCount=4 KnotsCount=2 Degree=3 IsPeriodic=0
    g26: BSplineCurve PolesCount=4 KnotsCount=2 Degree=3 IsPeriodic=0
    g27: BSplineCurve PolesCount=4 KnotsCount=2 Degree=3 IsPeriodic=0
    g28: BSplineCurve PolesCount=2 KnotsCount=2 Degree=1 IsPeriodic=0
    g29: BSplineCurve PolesCount=2 KnotsCount=2 Degree=1 IsPeriodic=0
    g30: BSplineCurve PolesCount=2 KnotsCount=2 Degree=1 IsPeriodic=0
    g31: BSplineCurve PolesCount=2 KnotsCount=2 Degree=1 IsPeriodic=0
    g32: BSplineCurve PolesCount=4 KnotsCount=2 Degree=3 IsPeriodic=0
    g33: BSplineCurve PolesCount=4 KnotsCount=2 Degree=3 IsPeriodic=0
    g34: BSplineCurve PolesCount=4 KnotsCount=2 Degree=3 IsPeriodic=0
    g35: BSplineCurve PolesCount=4 KnotsCount=2 Degree=3 IsPeriodic=0
    g36: BSplineCurve PolesCount=4 KnotsCount=2 Degree=3 IsPeriodic=0
    g37: BSplineCurve PolesCount=4 KnotsCount=2 Degree=3 IsPeriodic=0
    g38: BSplineCurve PolesCount=4 KnotsCount=2 Degree=3 IsPeriodic=0
    g39: BSplineCurve PolesCount=4 KnotsCount=2 Degree=3 IsPeriodic=0
    g40: BSplineCurve PolesCount=4 KnotsCount=2 Degree=3 IsPeriodic=0
    g41: BSplineCurve PolesCount=4 KnotsCount=2 Degree=3 IsPeriodic=0
    g42: BSplineCurve PolesCount=4 KnotsCount=2 Degree=3 IsPeriodic=0
    g43: BSplineCurve PolesCount=4 KnotsCount=2 Degree=3 IsPeriodic=0
    g44: BSplineCurve PolesCount=4 KnotsCount=2 Degree=3 IsPeriodic=0
    g45: BSplineCurve PolesCount=4 KnotsCount=2 Degree=3 IsPeriodic=0
    g46: BSplineCurve PolesCount=4 KnotsCount=2 Degree=3 IsPeriodic=0
    g47: BSplineCurve PolesCount=4 KnotsCount=2 Degree=3 IsPeriodic=0
    g48: BSplineCurve PolesCount=4 KnotsCount=2 Degree=3 IsPeriodic=0
    g49: BSplineCurve PolesCount=4 KnotsCount=2 Degree=3 IsPeriodic=0
    g50: BSplineCurve PolesCount=2 KnotsCount=2 Degree=1 IsPeriodic=0
    g51: BSplineCurve PolesCount=2 KnotsCount=2 Degree=1 IsPeriodic=0
    g52: BSplineCurve PolesCount=4 KnotsCount=2 Degree=3 IsPeriodic=0
    g53: BSplineCurve PolesCount=4 KnotsCount=2 Degree=3 IsPeriodic=0
    g54: BSplineCurve PolesCount=2 KnotsCount=2 Degree=1 IsPeriodic=0
    g55: BSplineCurve PolesCount=2 KnotsCount=2 Degree=1 IsPeriodic=0
    g56: BSplineCurve PolesCount=2 KnotsCount=2 Degree=1 IsPeriodic=0
    g57: BSplineCurve PolesCount=2 KnotsCount=2 Degree=1 IsPeriodic=0
    g58: BSplineCurve PolesCount=4 KnotsCount=2 Degree=3 IsPeriodic=0
    g59: BSplineCurve PolesCount=4 KnotsCount=2 Degree=3 IsPeriodic=0
    g60: BSplineCurve PolesCount=4 KnotsCount=2 Degree=3 IsPeriodic=0
    g61: BSplineCurve PolesCount=4 KnotsCount=2 Degree=3 IsPeriodic=0
    g62: BSplineCurve PolesCount=4 KnotsCount=2 Degree=3 IsPeriodic=0
    g63: BSplineCurve PolesCount=4 KnotsCount=2 Degree=3 IsPeriodic=0
    g64: BSplineCurve PolesCount=4 KnotsCount=2 Degree=3 IsPeriodic=0
    g65: BSplineCurve PolesCount=4 KnotsCount=2 Degree=3 IsPeriodic=0
    g66: BSplineCurve PolesCount=4 KnotsCount=2 Degree=3 IsPeriodic=0
    g67: BSplineCurve PolesCount=4 KnotsCount=2 Degree=3 IsPeriodic=0
    g68: BSplineCurve PolesCount=4 KnotsCount=2 Degree=3 IsPeriodic=0
    g69: BSplineCurve PolesCount=4 KnotsCount=2 Degree=3 IsPeriodic=0
    g70: BSplineCurve PolesCount=4 KnotsCount=2 Degree=3 IsPeriodic=0
    g71: BSplineCurve PolesCount=4 KnotsCount=2 Degree=3 IsPeriodic=0
    g72: BSplineCurve PolesCount=4 KnotsCount=2 Degree=3 IsPeriodic=0
    g73: BSplineCurve PolesCount=4 KnotsCount=2 Degree=3 IsPeriodic=0
    g74: BSplineCurve PolesCount=4 KnotsCount=2 Degree=3 IsPeriodic=0
    g75: BSplineCurve PolesCount=4 KnotsCount=2 Degree=3 IsPeriodic=0
    g76: BSplineCurve PolesCount=4 KnotsCount=2 Degree=3 IsPeriodic=0
    g77: BSplineCurve PolesCount=4 KnotsCount=2 Degree=3 IsPeriodic=0
    g78: BSplineCurve PolesCount=2 KnotsCount=2 Degree=1 IsPeriodic=0
    g79: BSplineCurve PolesCount=2 KnotsCount=2 Degree=1 IsPeriodic=0
    g80: BSplineCurve PolesCount=4 KnotsCount=2 Degree=3 IsPeriodic=0
    g81: BSplineCurve PolesCount=4 KnotsCount=2 Degree=3 IsPeriodic=0
    g82: BSplineCurve PolesCount=4 KnotsCount=2 Degree=3 IsPeriodic=0
    g83: BSplineCurve PolesCount=4 KnotsCount=2 Degree=3 IsPeriodic=0
    g84: BSplineCurve PolesCount=4 KnotsCount=2 Degree=3 IsPeriodic=0
    g85: BSplineCurve PolesCount=4 KnotsCount=2 Degree=3 IsPeriodic=0
    g86: BSplineCurve PolesCount=4 KnotsCount=2 Degree=3 IsPeriodic=0
    g87: BSplineCurve PolesCount=4 KnotsCount=2 Degree=3 IsPeriodic=0
    g88: BSplineCurve PolesCount=4 KnotsCount=2 Degree=3 IsPeriodic=0
    g89: BSplineCurve PolesCount=4 KnotsCount=2 Degree=3 IsPeriodic=0
    g90: BSplineCurve PolesCount=4 KnotsCount=2 Degree=3 IsPeriodic=0
    g91: BSplineCurve PolesCount=4 KnotsCount=2 Degree=3 IsPeriodic=0
    g92: BSplineCurve PolesCount=4 KnotsCount=2 Degree=3 IsPeriodic=0
    g93: BSplineCurve PolesCount=4 KnotsCount=2 Degree=3 IsPeriodic=0
    g94: BSplineCurve PolesCount=4 KnotsCount=2 Degree=3 IsPeriodic=0
    g95: BSplineCurve PolesCount=4 KnotsCount=2 Degree=3 IsPeriodic=0
    g96: BSplineCurve PolesCount=4 KnotsCount=2 Degree=3 IsPeriodic=0
    g97: BSplineCurve PolesCount=4 KnotsCount=2 Degree=3 IsPeriodic=0
    g98: BSplineCurve PolesCount=4 KnotsCount=2 Degree=3 IsPeriodic=0
    g99: BSplineCurve PolesCount=4 KnotsCount=2 Degree=3 IsPeriodic=0
    g100: BSplineCurve PolesCount=4 KnotsCount=2 Degree=3 IsPeriodic=0
    g101: BSplineCurve PolesCount=4 KnotsCount=2 Degree=3 IsPeriodic=0
    g102: BSplineCurve PolesCount=4 KnotsCount=2 Degree=3 IsPeriodic=0
    g103: BSplineCurve PolesCount=4 KnotsCount=2 Degree=3 IsPeriodic=0
    g104: BSplineCurve PolesCount=4 KnotsCount=2 Degree=3 IsPeriodic=0
    g105: BSplineCurve PolesCount=2 KnotsCount=2 Degree=1 IsPeriodic=0
    g106: BSplineCurve PolesCount=2 KnotsCount=2 Degree=1 IsPeriodic=0
    g107: BSplineCurve PolesCount=4 KnotsCount=2 Degree=3 IsPeriodic=0
    g108: BSplineCurve PolesCount=4 KnotsCount=2 Degree=3 IsPeriodic=0
    g109: BSplineCurve PolesCount=4 KnotsCount=2 Degree=3 IsPeriodic=0
    g110: BSplineCurve PolesCount=4 KnotsCount=2 Degree=3 IsPeriodic=0
    g111: BSplineCurve PolesCount=4 KnotsCount=2 Degree=3 IsPeriodic=0
    g112: BSplineCurve PolesCount=4 KnotsCount=2 Degree=3 IsPeriodic=0
    g113: BSplineCurve PolesCount=4 KnotsCount=2 Degree=3 IsPeriodic=0
    g114: BSplineCurve PolesCount=4 KnotsCount=2 Degree=3 IsPeriodic=0
    g115: BSplineCurve PolesCount=4 KnotsCount=2 Degree=3 IsPeriodic=0
    g116: BSplineCurve PolesCount=4 KnotsCount=2 Degree=3 IsPeriodic=0
    g117: BSplineCurve PolesCount=4 KnotsCount=2 Degree=3 IsPeriodic=0
    g118: BSplineCurve PolesCount=4 KnotsCount=2 Degree=3 IsPeriodic=0
    g119: BSplineCurve PolesCount=4 KnotsCount=2 Degree=3 IsPeriodic=0
    g120: BSplineCurve PolesCount=4 KnotsCount=2 Degree=3 IsPeriodic=0
    g121: BSplineCurve PolesCount=4 KnotsCount=2 Degree=3 IsPeriodic=0
    g122: BSplineCurve PolesCount=4 KnotsCount=2 Degree=3 IsPeriodic=0
    g123: BSplineCurve PolesCount=4 KnotsCount=2 Degree=3 IsPeriodic=0
    g124: BSplineCurve PolesCount=4 KnotsCount=2 Degree=3 IsPeriodic=0
    g125: BSplineCurve PolesCount=4 KnotsCount=2 Degree=3 IsPeriodic=0
    g126: BSplineCurve PolesCount=4 KnotsCount=2 Degree=3 IsPeriodic=0
    g127: BSplineCurve PolesCount=4 KnotsCount=2 Degree=3 IsPeriodic=0
    g128: BSplineCurve PolesCount=2 KnotsCount=2 Degree=1 IsPeriodic=0
    g129: BSplineCurve PolesCount=4 KnotsCount=2 Degree=3 IsPeriodic=0
    g130: BSplineCurve PolesCount=4 KnotsCount=2 Degree=3 IsPeriodic=0
    g131: BSplineCurve PolesCount=4 KnotsCount=2 Degree=3 IsPeriodic=0
    g132: BSplineCurve PolesCount=4 KnotsCount=2 Degree=3 IsPeriodic=0
    g133: BSplineCurve PolesCount=4 KnotsCount=2 Degree=3 IsPeriodic=0
    g134: BSplineCurve PolesCount=4 KnotsCount=2 Degree=3 IsPeriodic=0
    g135: BSplineCurve PolesCount=4 KnotsCount=2 Degree=3 IsPeriodic=0
    g136: BSplineCurve PolesCount=4 KnotsCount=2 Degree=3 IsPeriodic=0
    g137: BSplineCurve PolesCount=4 KnotsCount=2 Degree=3 IsPeriodic=0
    g138: BSplineCurve PolesCount=4 KnotsCount=2 Degree=3 IsPeriodic=0
    g139: BSplineCurve PolesCount=4 KnotsCount=2 Degree=3 IsPeriodic=0
    g140: BSplineCurve PolesCount=4 KnotsCount=2 Degree=3 IsPeriodic=0
    g141: BSplineCurve PolesCount=4 KnotsCount=2 Degree=3 IsPeriodic=0
    g142: BSplineCurve PolesCount=4 KnotsCount=2 Degree=3 IsPeriodic=0
    g143: BSplineCurve PolesCount=4 KnotsCount=2 Degree=3 IsPeriodic=0
    g144: BSplineCurve PolesCount=4 KnotsCount=2 Degree=3 IsPeriodic=0
    g145: BSplineCurve PolesCount=4 KnotsCount=2 Degree=3 IsPeriodic=0
    g146: BSplineCurve PolesCount=4 KnotsCount=2 Degree=3 IsPeriodic=0
    g147: BSplineCurve PolesCount=2 KnotsCount=2 Degree=1 IsPeriodic=0
    g148: BSplineCurve PolesCount=2 KnotsCount=2 Degree=1 IsPeriodic=0
    g149: BSplineCurve PolesCount=4 KnotsCount=2 Degree=3 IsPeriodic=0
    g150: BSplineCurve PolesCount=4 KnotsCount=2 Degree=3 IsPeriodic=0
    g151: BSplineCurve PolesCount=4 KnotsCount=2 Degree=3 IsPeriodic=0
    g152: BSplineCurve PolesCount=2 KnotsCount=2 Degree=1 IsPeriodic=0
    g153: BSplineCurve PolesCount=2 KnotsCount=2 Degree=1 IsPeriodic=0
    g154: BSplineCurve PolesCount=4 KnotsCount=2 Degree=3 IsPeriodic=0
    g155: BSplineCurve PolesCount=4 KnotsCount=2 Degree=3 IsPeriodic=0
    g156: BSplineCurve PolesCount=4 KnotsCount=2 Degree=3 IsPeriodic=0
    g157: BSplineCurve PolesCount=4 KnotsCount=2 Degree=3 IsPeriodic=0
    g158: BSplineCurve PolesCount=4 KnotsCount=2 Degree=3 IsPeriodic=0
    g159: BSplineCurve PolesCount=4 KnotsCount=2 Degree=3 IsPeriodic=0
    g160: BSplineCurve PolesCount=4 KnotsCount=2 Degree=3 IsPeriodic=0
    g161: BSplineCurve PolesCount=4 KnotsCount=2 Degree=3 IsPeriodic=0
    g162: BSplineCurve PolesCount=4 KnotsCount=2 Degree=3 IsPeriodic=0
    g163: BSplineCurve PolesCount=4 KnotsCount=2 Degree=3 IsPeriodic=0
    g164: BSplineCurve PolesCount=4 KnotsCount=2 Degree=3 IsPeriodic=0
    g165: BSplineCurve PolesCount=4 KnotsCount=2 Degree=3 IsPeriodic=0
    g166: BSplineCurve PolesCount=4 KnotsCount=2 Degree=3 IsPeriodic=0
    g167: BSplineCurve PolesCount=4 KnotsCount=2 Degree=3 IsPeriodic=0
    g168: BSplineCurve PolesCount=4 KnotsCount=2 Degree=3 IsPeriodic=0
    g169: BSplineCurve PolesCount=4 KnotsCount=2 Degree=3 IsPeriodic=0
    g170: BSplineCurve PolesCount=4 KnotsCount=2 Degree=3 IsPeriodic=0
    g171: BSplineCurve PolesCount=4 KnotsCount=2 Degree=3 IsPeriodic=0
    g172: BSplineCurve PolesCount=4 KnotsCount=2 Degree=3 IsPeriodic=0
    g173: BSplineCurve PolesCount=4 KnotsCount=2 Degree=3 IsPeriodic=0
    g174: BSplineCurve PolesCount=4 KnotsCount=2 Degree=3 IsPeriodic=0
    g175: BSplineCurve PolesCount=2 KnotsCount=2 Degree=1 IsPeriodic=0
    g176: BSplineCurve PolesCount=2 KnotsCount=2 Degree=1 IsPeriodic=0
    g177: BSplineCurve PolesCount=2 KnotsCount=2 Degree=1 IsPeriodic=0
    g178: BSplineCurve PolesCount=2 KnotsCount=2 Degree=1 IsPeriodic=0
    g179: BSplineCurve PolesCount=2 KnotsCount=2 Degree=1 IsPeriodic=0
    g180: BSplineCurve PolesCount=2 KnotsCount=2 Degree=1 IsPeriodic=0
    g181: BSplineCurve PolesCount=4 KnotsCount=2 Degree=3 IsPeriodic=0
    g182: BSplineCurve PolesCount=4 KnotsCount=2 Degree=3 IsPeriodic=0
    g183: BSplineCurve PolesCount=4 KnotsCount=2 Degree=3 IsPeriodic=0
    g184: BSplineCurve PolesCount=4 KnotsCount=2 Degree=3 IsPeriodic=0
    g185: BSplineCurve PolesCount=4 KnotsCount=2 Degree=3 IsPeriodic=0
    g186: BSplineCurve PolesCount=4 KnotsCount=2 Degree=3 IsPeriodic=0
    g187: BSplineCurve PolesCount=4 KnotsCount=2 Degree=3 IsPeriodic=0
    g188: BSplineCurve PolesCount=4 KnotsCount=2 Degree=3 IsPeriodic=0
    g189: BSplineCurve PolesCount=4 KnotsCount=2 Degree=3 IsPeriodic=0
    g190: BSplineCurve PolesCount=4 KnotsCount=2 Degree=3 IsPeriodic=0
    g191: BSplineCurve PolesCount=4 KnotsCount=2 Degree=3 IsPeriodic=0
    g192: BSplineCurve PolesCount=4 KnotsCount=2 Degree=3 IsPeriodic=0
    g193: BSplineCurve PolesCount=4 KnotsCount=2 Degree=3 IsPeriodic=0
    g194: BSplineCurve PolesCount=4 KnotsCount=2 Degree=3 IsPeriodic=0
    g195: BSplineCurve PolesCount=4 KnotsCount=2 Degree=3 IsPeriodic=0
    g196: BSplineCurve PolesCount=4 KnotsCount=2 Degree=3 IsPeriodic=0
    g197: BSplineCurve PolesCount=4 KnotsCount=2 Degree=3 IsPeriodic=0
    g198: BSplineCurve PolesCount=2 KnotsCount=2 Degree=1 IsPeriodic=0
    g199: BSplineCurve PolesCount=2 KnotsCount=2 Degree=1 IsPeriodic=0
    g200: BSplineCurve PolesCount=4 KnotsCount=2 Degree=3 IsPeriodic=0
    g201: BSplineCurve PolesCount=4 KnotsCount=2 Degree=3 IsPeriodic=0
    g202: BSplineCurve PolesCount=4 KnotsCount=2 Degree=3 IsPeriodic=0
    g203: BSplineCurve PolesCount=4 KnotsCount=2 Degree=3 IsPeriodic=0
    g204: BSplineCurve PolesCount=2 KnotsCount=2 Degree=1 IsPeriodic=0
    g205: BSplineCurve PolesCount=2 KnotsCount=2 Degree=1 IsPeriodic=0
    g206: BSplineCurve PolesCount=4 KnotsCount=2 Degree=3 IsPeriodic=0
    g207: BSplineCurve PolesCount=4 KnotsCount=2 Degree=3 IsPeriodic=0
    g208: BSplineCurve PolesCount=4 KnotsCount=2 Degree=3 IsPeriodic=0
    g209: BSplineCurve PolesCount=4 KnotsCount=2 Degree=3 IsPeriodic=0
    g210: BSplineCurve PolesCount=2 KnotsCount=2 Degree=1 IsPeriodic=0
    g211: BSplineCurve PolesCount=2 KnotsCount=2 Degree=1 IsPeriodic=0
    g212: BSplineCurve PolesCount=4 KnotsCount=2 Degree=3 IsPeriodic=0
    g213: BSplineCurve PolesCount=2 KnotsCount=2 Degree=1 IsPeriodic=0
    g214: BSplineCurve PolesCount=2 KnotsCount=2 Degree=1 IsPeriodic=0
    g215: BSplineCurve PolesCount=4 KnotsCount=2 Degree=3 IsPeriodic=0
    g216: BSplineCurve PolesCount=4 KnotsCount=2 Degree=3 IsPeriodic=0
    g217: BSplineCurve PolesCount=4 KnotsCount=2 Degree=3 IsPeriodic=0
    g218: BSplineCurve PolesCount=4 KnotsCount=2 Degree=3 IsPeriodic=0
    g219: BSplineCurve PolesCount=4 KnotsCount=2 Degree=3 IsPeriodic=0
    g220: BSplineCurve PolesCount=4 KnotsCount=2 Degree=3 IsPeriodic=0
    g221: BSplineCurve PolesCount=4 KnotsCount=2 Degree=3 IsPeriodic=0
    g222: BSplineCurve PolesCount=2 KnotsCount=2 Degree=1 IsPeriodic=0
    g223: BSplineCurve PolesCount=2 KnotsCount=2 Degree=1 IsPeriodic=0
    g224: BSplineCurve PolesCount=4 KnotsCount=2 Degree=3 IsPeriodic=0
    g225: BSplineCurve PolesCount=4 KnotsCount=2 Degree=3 IsPeriodic=0
    g226: BSplineCurve PolesCount=4 KnotsCount=2 Degree=3 IsPeriodic=0
    g227: BSplineCurve PolesCount=4 KnotsCount=2 Degree=3 IsPeriodic=0
    g228: BSplineCurve PolesCount=4 KnotsCount=2 Degree=3 IsPeriodic=0
    g229: BSplineCurve PolesCount=4 KnotsCount=2 Degree=3 IsPeriodic=0
    g230: BSplineCurve PolesCount=4 KnotsCount=2 Degree=3 IsPeriodic=0
    g231: BSplineCurve PolesCount=4 KnotsCount=2 Degree=3 IsPeriodic=0
    g232: BSplineCurve PolesCount=4 KnotsCount=2 Degree=3 IsPeriodic=0
    g233: BSplineCurve PolesCount=4 KnotsCount=2 Degree=3 IsPeriodic=0
    g234: BSplineCurve PolesCount=4 KnotsCount=2 Degree=3 IsPeriodic=0
    g235: BSplineCurve PolesCount=2 KnotsCount=2 Degree=1 IsPeriodic=0
    g236: BSplineCurve PolesCount=2 KnotsCount=2 Degree=1 IsPeriodic=0
    g237: BSplineCurve PolesCount=2 KnotsCount=2 Degree=1 IsPeriodic=0
    g238: BSplineCurve PolesCount=2 KnotsCount=2 Degree=1 IsPeriodic=0
    g239: BSplineCurve PolesCount=4 KnotsCount=2 Degree=3 IsPeriodic=0
    g240: BSplineCurve PolesCount=4 KnotsCount=2 Degree=3 IsPeriodic=0
    g241: BSplineCurve PolesCount=4 KnotsCount=2 Degree=3 IsPeriodic=0
    g242: BSplineCurve PolesCount=4 KnotsCount=2 Degree=3 IsPeriodic=0
    g243: BSplineCurve PolesCount=4 KnotsCount=2 Degree=3 IsPeriodic=0
    g244: BSplineCurve PolesCount=4 KnotsCount=2 Degree=3 IsPeriodic=0
    g245: BSplineCurve PolesCount=4 KnotsCount=2 Degree=3 IsPeriodic=0
    g246: BSplineCurve PolesCount=4 KnotsCount=2 Degree=3 IsPeriodic=0
    g247: BSplineCurve PolesCount=4 KnotsCount=2 Degree=3 IsPeriodic=0
    g248: BSplineCurve PolesCount=4 KnotsCount=2 Degree=3 IsPeriodic=0
    g249: BSplineCurve PolesCount=4 KnotsCount=2 Degree=3 IsPeriodic=0
    g250: BSplineCurve PolesCount=4 KnotsCount=2 Degree=3 IsPeriodic=0
    g251: BSplineCurve PolesCount=2 KnotsCount=2 Degree=1 IsPeriodic=0
    g252: BSplineCurve PolesCount=2 KnotsCount=2 Degree=1 IsPeriodic=0
    g253: BSplineCurve PolesCount=4 KnotsCount=2 Degree=3 IsPeriodic=0
    g254: BSplineCurve PolesCount=4 KnotsCount=2 Degree=3 IsPeriodic=0
    g255: BSplineCurve PolesCount=4 KnotsCount=2 Degree=3 IsPeriodic=0
    g256: BSplineCurve PolesCount=4 KnotsCount=2 Degree=3 IsPeriodic=0
    g257: BSplineCurve PolesCount=4 KnotsCount=2 Degree=3 IsPeriodic=0
    g258: BSplineCurve PolesCount=4 KnotsCount=2 Degree=3 IsPeriodic=0
    g259: BSplineCurve PolesCount=4 KnotsCount=2 Degree=3 IsPeriodic=0
    g260: BSplineCurve PolesCount=4 KnotsCount=2 Degree=3 IsPeriodic=0
    g261: BSplineCurve PolesCount=4 KnotsCount=2 Degree=3 IsPeriodic=0
    g262: BSplineCurve PolesCount=2 KnotsCount=2 Degree=1 IsPeriodic=0
    g263: BSplineCurve PolesCount=2 KnotsCount=2 Degree=1 IsPeriodic=0
    g264: BSplineCurve PolesCount=4 KnotsCount=2 Degree=3 IsPeriodic=0
    g265: BSplineCurve PolesCount=4 KnotsCount=2 Degree=3 IsPeriodic=0
    g266: BSplineCurve PolesCount=4 KnotsCount=2 Degree=3 IsPeriodic=0
    g267: BSplineCurve PolesCount=4 KnotsCount=2 Degree=3 IsPeriodic=0
    g268: BSplineCurve PolesCount=4 KnotsCount=2 Degree=3 IsPeriodic=0
    g269: BSplineCurve PolesCount=4 KnotsCount=2 Degree=3 IsPeriodic=0
    g270: BSplineCurve PolesCount=4 KnotsCount=2 Degree=3 IsPeriodic=0
    g271: BSplineCurve PolesCount=4 KnotsCount=2 Degree=3 IsPeriodic=0
    g272: BSplineCurve PolesCount=4 KnotsCount=2 Degree=3 IsPeriodic=0
    g273: BSplineCurve PolesCount=4 KnotsCount=2 Degree=3 IsPeriodic=0
    g274: BSplineCurve PolesCount=4 KnotsCount=2 Degree=3 IsPeriodic=0
    g275: BSplineCurve PolesCount=4 KnotsCount=2 Degree=3 IsPeriodic=0
    g276: BSplineCurve PolesCount=4 KnotsCount=2 Degree=3 IsPeriodic=0
    g277: BSplineCurve PolesCount=4 KnotsCount=2 Degree=3 IsPeriodic=0
    g278: BSplineCurve PolesCount=4 KnotsCount=2 Degree=3 IsPeriodic=0
    g279: BSplineCurve PolesCount=4 KnotsCount=2 Degree=3 IsPeriodic=0
    g280: BSplineCurve PolesCount=4 KnotsCount=2 Degree=3 IsPeriodic=0
    g281: BSplineCurve PolesCount=4 KnotsCount=2 Degree=3 IsPeriodic=0
    g282: BSplineCurve PolesCount=4 KnotsCount=2 Degree=3 IsPeriodic=0
    g283: BSplineCurve PolesCount=4 KnotsCount=2 Degree=3 IsPeriodic=0
    g284: BSplineCurve PolesCount=4 KnotsCount=2 Degree=3 IsPeriodic=0
    g285: BSplineCurve PolesCount=4 KnotsCount=2 Degree=3 IsPeriodic=0
    g286: BSplineCurve PolesCount=4 KnotsCount=2 Degree=3 IsPeriodic=0
    g287: BSplineCurve PolesCount=4 KnotsCount=2 Degree=3 IsPeriodic=0
    g288: BSplineCurve PolesCount=4 KnotsCount=2 Degree=3 IsPeriodic=0
    g289: BSplineCurve PolesCount=4 KnotsCount=2 Degree=3 IsPeriodic=0
    g290: BSplineCurve PolesCount=4 KnotsCount=2 Degree=3 IsPeriodic=0
    g291: BSplineCurve PolesCount=4 KnotsCount=2 Degree=3 IsPeriodic=0
    g292: BSplineCurve PolesCount=4 KnotsCount=2 Degree=3 IsPeriodic=0
    g293: BSplineCurve PolesCount=4 KnotsCount=2 Degree=3 IsPeriodic=0
    g294: BSplineCurve PolesCount=4 KnotsCount=2 Degree=3 IsPeriodic=0
    g295: BSplineCurve PolesCount=4 KnotsCount=2 Degree=3 IsPeriodic=0
    g296: BSplineCurve PolesCount=4 KnotsCount=2 Degree=3 IsPeriodic=0
    g297: BSplineCurve PolesCount=4 KnotsCount=2 Degree=3 IsPeriodic=0
    g298: BSplineCurve PolesCount=4 KnotsCount=2 Degree=3 IsPeriodic=0
    g299: BSplineCurve PolesCount=4 KnotsCount=2 Degree=3 IsPeriodic=0
    g300: BSplineCurve PolesCount=4 KnotsCount=2 Degree=3 IsPeriodic=0
    g301: BSplineCurve PolesCount=4 KnotsCount=2 Degree=3 IsPeriodic=0
    g302: BSplineCurve PolesCount=4 KnotsCount=2 Degree=3 IsPeriodic=0
    g303: BSplineCurve PolesCount=4 KnotsCount=2 Degree=3 IsPeriodic=0
    g304: BSplineCurve PolesCount=4 KnotsCount=2 Degree=3 IsPeriodic=0
    g305: BSplineCurve PolesCount=4 KnotsCount=2 Degree=3 IsPeriodic=0
    g306: BSplineCurve PolesCount=4 KnotsCount=2 Degree=3 IsPeriodic=0
    g307: BSplineCurve PolesCount=4 KnotsCount=2 Degree=3 IsPeriodic=0
    g308: BSplineCurve PolesCount=4 KnotsCount=2 Degree=3 IsPeriodic=0
    g309: BSplineCurve PolesCount=4 KnotsCount=2 Degree=3 IsPeriodic=0
    g310: BSplineCurve PolesCount=4 KnotsCount=2 Degree=3 IsPeriodic=0
    g311: BSplineCurve PolesCount=2 KnotsCount=2 Degree=1 IsPeriodic=0
    g312: BSplineCurve PolesCount=4 KnotsCount=2 Degree=3 IsPeriodic=0
    g313: BSplineCurve PolesCount=4 KnotsCount=2 Degree=3 IsPeriodic=0
    g314: BSplineCurve PolesCount=4 KnotsCount=2 Degree=3 IsPeriodic=0
    g315: BSplineCurve PolesCount=4 KnotsCount=2 Degree=3 IsPeriodic=0
    g316: BSplineCurve PolesCount=4 KnotsCount=2 Degree=3 IsPeriodic=0
    g317: BSplineCurve PolesCount=4 KnotsCount=2 Degree=3 IsPeriodic=0
    g318: BSplineCurve PolesCount=4 KnotsCount=2 Degree=3 IsPeriodic=0
    g319: BSplineCurve PolesCount=4 KnotsCount=2 Degree=3 IsPeriodic=0
    g320: BSplineCurve PolesCount=2 KnotsCount=2 Degree=1 IsPeriodic=0
    g321: BSplineCurve PolesCount=4 KnotsCount=2 Degree=3 IsPeriodic=0
    g322: BSplineCurve PolesCount=4 KnotsCount=2 Degree=3 IsPeriodic=0
    g323: BSplineCurve PolesCount=4 KnotsCount=2 Degree=3 IsPeriodic=0
    g324: BSplineCurve PolesCount=2 KnotsCount=2 Degree=1 IsPeriodic=0
    g325: BSplineCurve PolesCount=2 KnotsCount=2 Degree=1 IsPeriodic=0
    g326: BSplineCurve PolesCount=4 KnotsCount=2 Degree=3 IsPeriodic=0
    g327: BSplineCurve PolesCount=4 KnotsCount=2 Degree=3 IsPeriodic=0
    g328: BSplineCurve PolesCount=4 KnotsCount=2 Degree=3 IsPeriodic=0
    g329: BSplineCurve PolesCount=4 KnotsCount=2 Degree=3 IsPeriodic=0
    g330: BSplineCurve PolesCount=4 KnotsCount=2 Degree=3 IsPeriodic=0
    g331: BSplineCurve PolesCount=4 KnotsCount=2 Degree=3 IsPeriodic=0
    g332: BSplineCurve PolesCount=4 KnotsCount=2 Degree=3 IsPeriodic=0
    g333: BSplineCurve PolesCount=4 KnotsCount=2 Degree=3 IsPeriodic=0
    g334: BSplineCurve PolesCount=4 KnotsCount=2 Degree=3 IsPeriodic=0
    g335: BSplineCurve PolesCount=4 KnotsCount=2 Degree=3 IsPeriodic=0
    g336: BSplineCurve PolesCount=4 KnotsCount=2 Degree=3 IsPeriodic=0
    g337: BSplineCurve PolesCount=4 KnotsCount=2 Degree=3 IsPeriodic=0
    g338: BSplineCurve PolesCount=4 KnotsCount=2 Degree=3 IsPeriodic=0
    g339: BSplineCurve PolesCount=2 KnotsCount=2 Degree=1 IsPeriodic=0
    g340: BSplineCurve PolesCount=2 KnotsCount=2 Degree=1 IsPeriodic=0
    g341: BSplineCurve PolesCount=4 KnotsCount=2 Degree=3 IsPeriodic=0
  constraints (342):
    c: Coincident(g0,g1)
    c: Coincident(g1,g2)
    c: Coincident(g2,g3)
    c: Coincident(g3,g4)
    c: Coincident(g4,g5)
    c: Coincident(g5,g6)
    c: Coincident(g6,g7)
    c: Coincident(g7,g8)
    c: Coincident(g8,g9)
    c: Coincident(g9,g10)
    c: Coincident(g10,g11)
    c: Coincident(g11,g12)
    c: Coincident(g12,g13)
    c: Coincident(g13,g14)
    c: Coincident(g14,g15)
    c: Coincident(g15,g16)
    c: Coincident(g16,g17)
    c: Coincident(g17,g18)
    c: Coincident(g18,g19)
    c: Coincident(g19,g20)
    c: Coincident(g20,g21)
    c: Coincident(g21,g22)
    c: Coincident(g22,g23)
    c: Coincident(g23,g24)
    c: Coincident(g24,g25)
    c: Coincident(g25,g26)
    c: Coincident(g26,g27)
    c: Coincident(g27,g28)
    c: Coincident(g28,g29)
    c: Coincident(g29,g30)
    c: Coincident(g30,g31)
    c: Coincident(g31,g32)
    c: Coincident(g32,g0)
    c: Coincident(g33,g34)
    c: Coincident(g34,g35)
    c: Coincident(g35,g36)
    c: Coincident(g36,g37)
    c: Coincident(g37,g38)
    c: Coincident(g38,g33)
    c: Coincident(g39,g40)
    c: Coincident(g40,g41)
    c: Coincident(g41,g39)
    c: Coincident(g42,g43)
    c: Coincident(g43,g44)
    c: Coincident(g44,g45)
    c: Coincident(g45,g42)
    c: Coincident(g46,g47)
    c: Coincident(g47,g48)
    c: Coincident(g48,g49)
    c: Coincident(g49,g50)
    c: Coincident(g50,g51)
    c: Coincident(g51,g52)
    c: Coincident(g52,g53)
    c: Coincident(g53,g54)
    c: Coincident(g54,g55)
    c: Coincident(g55,g56)
    c: Coincident(g56,g57)
    c: Coincident(g57,g58)
    c: Coincident(g58,g59)
    c: Coincident(g59,g60)
    c: Coincident(g60,g61)
    c: Coincident(g61,g62)
    c: Coincident(g62,g63)
    c: Coincident(g63,g64)
    c: Coincident(g65,g66)
    c: Coincident(g66,g67)
    c: Coincident(g67,g68)
    c: Coincident(g68,g69)
    c: Coincident(g69,g70)
    c: Coincident(g70,g71)
    c: Coincident(g71,g72)
    c: Coincident(g72,g73)
    c: Coincident(g73,g74)
    c: Coincident(g74,g75)
    c: Coincident(g75,g76)
    c: Coincident(g76,g77)
    c: Coincident(g77,g78)
    c: Coincident(g78,g79)
    c: Coincident(g79,g80)
    c: Coincident(g80,g81)
    c: Coincident(g81,g82)
    c: Coincident(g82,g83)
    c: Coincident(g83,g84)
    c: Coincident(g84,g85)
    c: Coincident(g85,g86)
    c: Coincident(g86,g87)
    c: Coincident(g87,g88)
    c: Coincident(g88,g89)
    c: Coincident(g89,g90)
    c: Coincident(g90,g91)
    c: Coincident(g91,g92)
    c: Coincident(g92,g93)
    c: Coincident(g93,g94)
    c: Coincident(g94,g95)
    c: Coincident(g95,g96)
    c: Coincident(g96,g97)
    c: Coincident(g97,g98)
    c: Coincident(g98,g99)
    c: Coincident(g99,g100)
    c: Coincident(g100,g101)
    c: Coincident(g101,g102)
    c: Coincident(g102,g103)
    c: Coincident(g103,g104)
    c: Coincident(g104,g105)
    c: Coincident(g105,g106)
    c: Coincident(g106,g107)
    c: Coincident(g107,g108)
    c: Coincident(g108,g109)
    c: Coincident(g109,g110)
    c: Coincident(g110,g111)
    c: Coincident(g111,g112)
    c: Coincident(g112,g113)
    c: Coincident(g113,g114)
    c: Coincident(g114,g115)
    c: Coincident(g115,g116)
    c: Coincident(g116,g117)
    c: Coincident(g117,g118)
    c: Coincident(g118,g119)
    c: Coincident(g119,g120)
    c: Coincident(g120,g121)
    c: Coincident(g121,g122)
    c: Coincident(g122,g123)
    c: Coincident(g123,g124)
    c: Coincident(g125,g126)
    c: Coincident(g126,g127)
    c: Coincident(g127,g125)
    c: Coincident(g128,g129)
    c: Coincident(g129,g130)
    c: Coincident(g130,g131)
    c: Coincident(g131,g128)
    c: Coincident(g132,g133)
    c: Coincident(g133,g134)
    c: Coincident(g134,g132)
    c: Coincident(g135,g136)
    c: Coincident(g136,g137)
    c: Coincident(g137,g135)
    c: Coincident(g138,g139)
    c: Coincident(g139,g140)
    c: Coincident(g140,g138)
    c: Coincident(g141,g142)
    c: Coincident(g142,g143)
    c: Coincident(g143,g144)
    c: Coincident(g144,g145)
    c: Coincident(g145,g146)
    c: Coincident(g146,g147)
    c: Coincident(g147,g148)
    c: Coincident(g148,g149)
    c: Coincident(g149,g141)
    c: Coincident(g150,g151)
    c: Coincident(g151,g152)
    c: Coincident(g152,g153)
    c: Coincident(g153,g154)
    c: Coincident(g155,g156)
    c: Coincident(g156,g157)
    c: Coincident(g157,g155)
    c: Coincident(g158,g159)
    c: Coincident(g159,g160)
    c: Coincident(g160,g161)
    c: Coincident(g161,g162)
    c: Coincident(g162,g163)
    c: Coincident(g163,g164)
    c: Coincident(g164,g165)
    c: Coincident(g165,g166)
    c: Coincident(g166,g167)
    c: Coincident(g167,g168)
    c: Coincident(g168,g169)
    c: Coincident(g169,g170)
    c: Coincident(g170,g171)
    c: Coincident(g171,g172)
    c: Coincident(g172,g173)
    c: Coincident(g173,g174)
    c: Coincident(g174,g175)
    c: Coincident(g175,g176)
    c: Coincident(g176,g177)
    c: Coincident(g177,g178)
    c: Coincident(g178,g179)
    c: Coincident(g179,g180)
    c: Coincident(g180,g181)
    c: Coincident(g181,g182)
    c: Coincident(g182,g183)
    c: Coincident(g183,g184)
    c: Coincident(g184,g185)
    c: Coincident(g185,g186)
    c: Coincident(g186,g187)
    c: Coincident(g187,g188)
    c: Coincident(g188,g189)
    c: Coincident(g189,g190)
    c: Coincident(g190,g191)
    c: Coincident(g191,g192)
    c: Coincident(g192,g193)
    c: Coincident(g193,g194)
    c: Coincident(g194,g195)
    c: Coincident(g195,g196)
    c: Coincident(g196,g197)
    c: Coincident(g197,g198)
    c: Coincident(g198,g199)
    c: Coincident(g199,g200)
    c: Coincident(g200,g201)
    c: Coincident(g201,g202)
    c: Coincident(g202,g203)
    c: Coincident(g203,g204)
    c: Coincident(g204,g205)
    c: Coincident(g205,g206)
    c: Coincident(g206,g207)
    c: Coincident(g207,g208)
    c: Coincident(g208,g209)
    c: Coincident(g209,g210)
    c: Coincident(g210,g211)
    c: Coincident(g211,g212)
    c: Coincident(g212,g213)
    c: Coincident(g213,g214)
    c: Coincident(g214,g215)
    c: Coincident(g215,g216)
    c: Coincident(g216,g217)
    c: Coincident(g217,g218)
    c: Coincident(g218,g219)
    c: Coincident(g219,g220)
    c: Coincident(g220,g221)
    c: Coincident(g221,g222)
    c: Coincident(g222,g223)
    c: Coincident(g223,g224)
    c: Coincident(g224,g225)
    c: Coincident(g225,g226)
    c: Coincident(g226,g227)
    c: Coincident(g227,g228)
    c: Coincident(g228,g229)
    c: Coincident(g229,g230)
    c: Coincident(g230,g231)
    c: Coincident(g231,g232)
    c: Coincident(g232,g233)
    c: Coincident(g233,g234)
    c: Coincident(g234,g235)
    c: Coincident(g235,g236)
    c: Coincident(g236,g237)
    c: Coincident(g237,g238)
    c: Coincident(g238,g239)
    c: Coincident(g239,g240)
    c: Coincident(g240,g241)
    c: Coincident(g241,g242)
    c: Coincident(g242,g243)
    c: Coincident(g243,g244)
    c: Coincident(g244,g245)
    c: Coincident(g245,g246)
    c: Coincident(g246,g247)
    c: Coincident(g247,g248)
    c: Coincident(g248,g249)
    c: Coincident(g249,g250)
    c: Coincident(g250,g251)
    c: Coincident(g251,g252)
    c: Coincident(g252,g253)
    c: Coincident(g253,g254)
    c: Coincident(g254,g255)
    c: Coincident(g255,g256)
    c: Coincident(g256,g257)
    c: Coincident(g257,g258)
    c: Coincident(g258,g259)
    c: Coincident(g259,g260)
    c: Coincident(g260,g261)
    c: Coincident(g261,g262)
    c: Coincident(g262,g263)
    c: Coincident(g263,g264)
    c: Coincident(g264,g265)
    c: Coincident(g265,g266)
    c: Coincident(g266,g267)
    c: Coincident(g267,g268)
    c: Coincident(g268,g269)
    c: Coincident(g269,g270)
    c: Coincident(g271,g272)
    c: Coincident(g272,g273)
    c: Coincident(g273,g274)
    c: Coincident(g274,g275)
    c: Coincident(g275,g276)
    c: Coincident(g276,g277)
    c: Coincident(g277,g278)
    c: Coincident(g279,g280)
    c: Coincident(g280,g281)
    c: Coincident(g281,g279)
    c: Coincident(g282,g283)
    c: Coincident(g283,g284)
    c: Coincident(g285,g286)
    c: Coincident(g286,g287)
    c: Coincident(g287,g285)
    c: Coincident(g288,g289)
    c: Coincident(g289,g290)
    c: Coincident(g290,g291)
    c: Coincident(g291,g292)
    c: Coincident(g292,g288)
    c: Coincident(g293,g294)
    c: Coincident(g294,g295)
    c: Coincident(g295,g293)
    c: Coincident(g296,g297)
    c: Coincident(g297,g298)
    c: Coincident(g298,g296)
    c: Coincident(g299,g300)
    c: Coincident(g300,g301)
    c: Coincident(g301,g299)
    c: Coincident(g302,g303)
    c: Coincident(g303,g304)
    c: Coincident(g304,g302)
    c: Coincident(g305,g306)
    c: Coincident(g306,g307)
    c: Coincident(g307,g305)
    c: Coincident(g309,g310)
    c: Coincident(g310,g308)
    c: Coincident(g311,g312)
    c: Coincident(g312,g313)
    c: Coincident(g313,g314)
    c: Coincident(g314,g315)
    c: Coincident(g315,g316)
    c: Coincident(g316,g317)
    c: Coincident(g317,g318)
    c: Coincident(g318,g319)
    c: Coincident(g319,g320)
    c: Coincident(g320,g311)
    c: Coincident(g321,g322)
    c: Coincident(g322,g323)
    c: Coincident(g323,g324)
    c: Coincident(g324,g325)
    c: Coincident(g325,g326)
    c: Coincident(g326,g327)
    c: Coincident(g327,g321)
    c: Coincident(g328,g329)
    c: Coincident(g330,g331)
    c: Coincident(g331,g332)
    c: Coincident(g332,g333)
    c: Coincident(g333,g334)
    c: Coincident(g334,g335)
    c: Coincident(g335,g336)
    c: Coincident(g336,g337)
    c: Coincident(g337,g338)
    c: Coincident(g338,g339)
    c: Coincident(g339,g340)
    c: Coincident(g340,g341)
    c: Coincident(g341,g328)
    c: Coincident(g65,g124)
    c: Coincident(g308,g309)
    c: Coincident(g150,g154)
    c: Coincident(g158,g270)
    c: Coincident(g329,g330)
    c: Coincident(g46,g64)
    c: Coincident(g282,g284)
    c: Coincident(g271,g278)
FEATURE [Part::Extrusion] Extrude  label="Artist-Extrude"
  Base = -> Sketch026
  Dir = (0,0,1)
  DirMode = 0
  FaceMakerClass = Part::FaceMakerBullseye
  FaceMakerMode = 3
  LengthFwd = 0
  LengthRev = 3
  Solid = true
  Symmetric = false
  expr: LengthRev = <<Icon_Params>>.IconDepth
FEATURE [Part::Extrusion] Extrude001  label="Barber-Extrude"
  Base = -> Sketch028
  Dir = (0,0,1)
  DirMode = 0
  FaceMakerClass = Part::FaceMakerBullseye
  FaceMakerMode = 3
  LengthFwd = 0
  LengthRev = 3
  Solid = true
  Symmetric = false
  expr: LengthRev = <<Icon_Params>>.IconDepth
FEATURE [Part::Extrusion] Extrude002  label="Cerenovus-Extrude"
  Base = -> Sketch029
  Dir = (0,0,1)
  DirMode = 0
  FaceMakerClass = Part::FaceMakerBullseye
  FaceMakerMode = 3
  LengthFwd = 0
  LengthRev = 3
  Solid = true
  Symmetric = false
  expr: LengthRev = <<Icon_Params>>.IconDepth
FEATURE [Part::Extrusion] Extrude003  label="Clockmaker-Extrude"
  Base = -> Sketch030
  Dir = (0,0,1)
  DirMode = 0
  FaceMakerClass = Part::FaceMakerBullseye
  FaceMakerMode = 3
  LengthFwd = 0
  LengthRev = 3
  Solid = true
  Symmetric = false
  expr: LengthRev = <<Icon_Params>>.IconDepth
FEATURE [Part::Extrusion] Extrude004  label="Dreamer-Extrude"
  Base = -> Sketch031
  Dir = (0,0,1)
  DirMode = 0
  FaceMakerClass = Part::FaceMakerBullseye
  FaceMakerMode = 3
  LengthFwd = 0
  LengthRev = 3
  Solid = true
  Symmetric = false
  expr: LengthRev = <<Icon_Params>>.IconDepth
FEATURE [Part::Extrusion] Extrude005  label="Evil_Twin-Extrude"
  Base = -> Sketch032
  Dir = (0,0,1)
  DirMode = 0
  FaceMakerClass = Part::FaceMakerBullseye
  FaceMakerMode = 3
  LengthFwd = 0
  LengthRev = 3
  Solid = true
  Symmetric = false
  expr: LengthRev = <<Icon_Params>>.IconDepth
FEATURE [Part::Extrusion] Extrude006  label="Fang_Gu-Extrude"
  Base = -> Sketch033
  Dir = (0,0,1)
  DirMode = 0
  FaceMakerClass = Part::FaceMakerBullseye
  FaceMakerMode = 3
  LengthFwd = 0
  LengthRev = 3
  Solid = true
  Symmetric = false
  expr: LengthRev = <<Icon_Params>>.IconDepth
FEATURE [Part::Extrusion] Extrude007  label="Flower_Girl-Extrude"
  Base = -> Sketch034
  Dir = (0,0,1)
  DirMode = 0
  FaceMakerClass = Part::FaceMakerBullseye
  FaceMakerMode = 3
  LengthFwd = 0
  LengthRev = 3
  Solid = true
  Symmetric = false
  expr: LengthRev = <<Icon_Params>>.IconDepth
FEATURE [Part::Extrusion] Extrude008  label="Juggler-Extrude"
  Base = -> Sketch035
  Dir = (0,0,1)
  DirMode = 0
  FaceMakerClass = Part::FaceMakerBullseye
  FaceMakerMode = 3
  LengthFwd = 0
  LengthRev = 3
  Solid = true
  Symmetric = false
  expr: LengthRev = <<Icon_Params>>.IconDepth
FEATURE [Part::Extrusion] Extrude009  label="Klutz-Extrude"
  Base = -> Sketch036
  Dir = (0,0,1)
  DirMode = 0
  FaceMakerClass = Part::FaceMakerBullseye
  FaceMakerMode = 3
  LengthFwd = 0
  LengthRev = 3
  Solid = true
  Symmetric = false
  expr: LengthRev = <<Icon_Params>>.IconDepth
FEATURE [Part::Extrusion] Extrude025  label="Mutant-Extrude"
  Base = -> Sketch038
  Dir = (0,0,1)
  DirMode = 0
  FaceMakerClass = Part::FaceMakerBullseye
  FaceMakerMode = 3
  LengthFwd = 0
  LengthRev = 3
  Solid = true
  Symmetric = false
  expr: LengthRev = <<Icon_Params>>.IconDepth
FEATURE [Part::Extrusion] Extrude024  label="Witch-Extrude"
  Base = -> Sketch051
  Dir = (0,0,1)
  DirMode = 0
  FaceMakerClass = Part::FaceMakerBullseye
  FaceMakerMode = 3
  LengthFwd = 0
  LengthRev = 3
  Solid = true
  Symmetric = false
  expr: LengthRev = <<Icon_Params>>.IconDepth
FEATURE [Part::Extrusion] Extrude010  label="Mathematician-Extrude"
  Base = -> Sketch037
  Dir = (0,0,1)
  DirMode = 0
  FaceMakerClass = Part::FaceMakerBullseye
  FaceMakerMode = 3
  LengthFwd = 0
  LengthRev = 3
  Solid = true
  Symmetric = false
  expr: LengthRev = <<Icon_Params>>.IconDepth
FEATURE [Part::Extrusion] Extrude012  label="No_Dashii-Extrude"
  Base = -> Sketch039
  Dir = (0,0,1)
  DirMode = 0
  FaceMakerClass = Part::FaceMakerBullseye
  FaceMakerMode = 3
  LengthFwd = 0
  LengthRev = 3
  Solid = true
  Symmetric = false
  expr: LengthRev = <<Icon_Params>>.IconDepth
FEATURE [Part::Extrusion] Extrude013  label="Oracle-Extrude"
  Base = -> Sketch040
  Dir = (0,0,1)
  DirMode = 0
  FaceMakerClass = Part::FaceMakerBullseye
  FaceMakerMode = 3
  LengthFwd = 0
  LengthRev = 3
  Solid = true
  Symmetric = false
  expr: LengthRev = <<Icon_Params>>.IconDepth
FEATURE [Part::Extrusion] Extrude014  label="Philosopher-Extrude"
  Base = -> Sketch041
  Dir = (0,0,1)
  DirMode = 0
  FaceMakerClass = Part::FaceMakerBullseye
  FaceMakerMode = 3
  LengthFwd = 0
  LengthRev = 3
  Solid = true
  Symmetric = false
  expr: LengthRev = <<Icon_Params>>.IconDepth
FEATURE [Part::Extrusion] Extrude015  label="Pit_Hag-Extrude"
  Base = -> Sketch042
  Dir = (0,0,1)
  DirMode = 0
  FaceMakerClass = Part::FaceMakerBullseye
  FaceMakerMode = 3
  LengthFwd = 0
  LengthRev = 3
  Solid = true
  Symmetric = false
  expr: LengthRev = <<Icon_Params>>.IconDepth
FEATURE [Part::Extrusion] Extrude016  label="Sage-Extrude"
  Base = -> Sketch043
  Dir = (0,0,1)
  DirMode = 0
  FaceMakerClass = Part::FaceMakerBullseye
  FaceMakerMode = 3
  LengthFwd = 0
  LengthRev = 3
  Solid = true
  Symmetric = false
  expr: LengthRev = <<Icon_Params>>.IconDepth
FEATURE [Part::Extrusion] Extrude017  label="Savant-Extrude"
  Base = -> Sketch044
  Dir = (0,0,1)
  DirMode = 0
  FaceMakerClass = Part::FaceMakerBullseye
  FaceMakerMode = 3
  LengthFwd = 0
  LengthRev = 3
  Solid = true
  Symmetric = false
  expr: LengthRev = <<Icon_Params>>.IconDepth
FEATURE [Part::Extrusion] Extrude018  label="Seamstress-Extrude"
  Base = -> Sketch045
  Dir = (0,0,1)
  DirMode = 0
  FaceMakerClass = Part::FaceMakerBullseye
  FaceMakerMode = 3
  LengthFwd = 0
  LengthRev = 3
  Solid = true
  Symmetric = false
  expr: LengthRev = <<Icon_Params>>.IconDepth
FEATURE [Part::Extrusion] Extrude019  label="Snake_Charmer-Extrude"
  Base = -> Sketch046
  Dir = (0,0,1)
  DirMode = 0
  FaceMakerClass = Part::FaceMakerBullseye
  FaceMakerMode = 3
  LengthFwd = 0
  LengthRev = 3
  Solid = true
  Symmetric = false
  expr: LengthRev = <<Icon_Params>>.IconDepth
FEATURE [Part::Extrusion] Extrude020  label="Sweetheart-Extrude"
  Base = -> Sketch047
  Dir = (0,0,1)
  DirMode = 0
  FaceMakerClass = Part::FaceMakerBullseye
  FaceMakerMode = 3
  LengthFwd = 0
  LengthRev = 3
  Solid = true
  Symmetric = false
  expr: LengthRev = <<Icon_Params>>.IconDepth
FEATURE [Part::Extrusion] Extrude021  label="Town_Crier-Extrude"
  Base = -> Sketch048
  Dir = (0,0,1)
  DirMode = 0
  FaceMakerClass = Part::FaceMakerBullseye
  FaceMakerMode = 3
  LengthFwd = 0
  LengthRev = 3
  Solid = true
  Symmetric = false
  expr: LengthRev = <<Icon_Params>>.IconDepth
FEATURE [Part::Extrusion] Extrude022  label="Vigormortis-Extrude"
  Base = -> Sketch049
  Dir = (0,0,1)
  DirMode = 0
  FaceMakerClass = Part::FaceMakerBullseye
  FaceMakerMode = 3
  LengthFwd = 0
  LengthRev = 3
  Solid = true
  Symmetric = false
  expr: LengthRev = <<Icon_Params>>.IconDepth
FEATURE [Part::Extrusion] Extrude023  label="Vortox-Extrude"
  Base = -> Sketch050
  Dir = (0,0,1)
  DirMode = 0
  FaceMakerClass = Part::FaceMakerBullseye
  FaceMakerMode = 3
  LengthFwd = 0
  LengthRev = 3
  Solid = true
  Symmetric = false
  expr: LengthRev = <<Icon_Params>>.IconDepth
FEATURE [Spreadsheet::Sheet] Spreadsheet  label="Icon_Params"
  cells = A1='IconDepth; B1='IconScale; A2(IconDepth)=3; B2(IconScale)=1.5
FEATURE [Part::Scale] Scale  label="Artist-Scale"
  Base = -> Extrude
  Uniform = true
  UniformScale = 1.5
  XScale = 1
  YScale = 1
  ZScale = 1
  expr: UniformScale = <<Icon_Params>>.IconScale
FEATURE [Part::Scale] Scale001  label="Barber-Scale"
  Base = -> Extrude001
  Uniform = true
  UniformScale = 1.5
  XScale = 1
  YScale = 1
  ZScale = 1
  expr: UniformScale = <<Icon_Params>>.IconScale
FEATURE [Part::Scale] Scale002  label="Cerenovus-Scale"
  Base = -> Extrude002
  Uniform = true
  UniformScale = 1.5
  XScale = 1
  YScale = 1
  ZScale = 1
  expr: UniformScale = <<Icon_Params>>.IconScale
FEATURE [Part::Scale] Scale003  label="Clockmaker-Scale"
  Base = -> Extrude003
  Uniform = true
  UniformScale = 1.5
  XScale = 1
  YScale = 1
  ZScale = 1
  expr: UniformScale = <<Icon_Params>>.IconScale
FEATURE [Part::Scale] Scale004  label="Dreamer-Scale"
  Base = -> Extrude004
  Uniform = true
  UniformScale = 1.5
  XScale = 1
  YScale = 1
  ZScale = 1
  expr: UniformScale = <<Icon_Params>>.IconScale
FEATURE [Part::Scale] Scale005  label="Evil_Twin-Scale"
  Base = -> Extrude005
  Uniform = true
  UniformScale = 1.5
  XScale = 1
  YScale = 1
  ZScale = 1
  expr: UniformScale = <<Icon_Params>>.IconScale
FEATURE [Part::Scale] Scale006  label="Fang_Gu-Scale"
  Base = -> Extrude006
  Uniform = true
  UniformScale = 1.5
  XScale = 1
  YScale = 1
  ZScale = 1
  expr: UniformScale = <<Icon_Params>>.IconScale
FEATURE [Part::Scale] Scale007  label="Flower_Girl-Scale"
  Base = -> Extrude007
  Uniform = true
  UniformScale = 1.5
  XScale = 1
  YScale = 1
  ZScale = 1
  expr: UniformScale = <<Icon_Params>>.IconScale
FEATURE [Part::Scale] Scale008  label="Juggler-Scale"
  Base = -> Extrude008
  Uniform = true
  UniformScale = 1.5
  XScale = 1
  YScale = 1
  ZScale = 1
  expr: UniformScale = <<Icon_Params>>.IconScale
FEATURE [Part::Scale] Scale009  label="Klutz-Scale"
  Base = -> Extrude009
  Uniform = true
  UniformScale = 1.5
  XScale = 1
  YScale = 1
  ZScale = 1
  expr: UniformScale = <<Icon_Params>>.IconScale
FEATURE [Part::Scale] Scale010  label="Mutant-Scale"
  Base = -> Extrude025
  Uniform = true
  UniformScale = 1.5
  XScale = 1
  YScale = 1
  ZScale = 1
  expr: UniformScale = <<Icon_Params>>.IconScale
FEATURE [Part::Scale] Scale011  label="Mathematician-Scale"
  Base = -> Extrude010
  Uniform = true
  UniformScale = 1.5
  XScale = 1
  YScale = 1
  ZScale = 1
  expr: UniformScale = <<Icon_Params>>.IconScale
FEATURE [Part::Scale] Scale012  label="No_Dashii-Scale"
  Base = -> Extrude012
  Uniform = true
  UniformScale = 1.5
  XScale = 1
  YScale = 1
  ZScale = 1
  expr: UniformScale = <<Icon_Params>>.IconScale
FEATURE [Part::Scale] Scale013  label="Oracle-Scale"
  Base = -> Extrude013
  Uniform = true
  UniformScale = 1.5
  XScale = 1
  YScale = 1
  ZScale = 1
  expr: UniformScale = <<Icon_Params>>.IconScale
FEATURE [Part::Scale] Scale014  label="Philosopher-Scale"
  Base = -> Extrude014
  Uniform = true
  UniformScale = 1.5
  XScale = 1
  YScale = 1
  ZScale = 1
  expr: UniformScale = <<Icon_Params>>.IconScale
FEATURE [Part::Scale] Scale015  label="Pit_Hag-Scale"
  Base = -> Extrude015
  Uniform = true
  UniformScale = 1.5
  XScale = 1
  YScale = 1
  ZScale = 1
  expr: UniformScale = <<Icon_Params>>.IconScale
FEATURE [Part::Scale] Scale016  label="Sage-Scale"
  Base = -> Extrude016
  Uniform = true
  UniformScale = 1.5
  XScale = 1
  YScale = 1
  ZScale = 1
  expr: UniformScale = <<Icon_Params>>.IconScale
FEATURE [Part::Scale] Scale017  label="Savant-Scale"
  Base = -> Extrude017
  Uniform = true
  UniformScale = 1.5
  XScale = 1
  YScale = 1
  ZScale = 1
  expr: UniformScale = <<Icon_Params>>.IconScale
FEATURE [Part::Scale] Scale018  label="Seamstress-Scale"
  Base = -> Extrude018
  Uniform = true
  UniformScale = 1.5
  XScale = 1
  YScale = 1
  ZScale = 1
  expr: UniformScale = <<Icon_Params>>.IconScale
FEATURE [Part::Scale] Scale019  label="Snake_Charmer-Scale"
  Base = -> Extrude019
  Uniform = true
  UniformScale = 1.5
  XScale = 1
  YScale = 1
  ZScale = 1
  expr: UniformScale = <<Icon_Params>>.IconScale
FEATURE [Part::Scale] Scale020  label="Sweetheart-Scale"
  Base = -> Extrude020
  Uniform = true
  UniformScale = 1.5
  XScale = 1
  YScale = 1
  ZScale = 1
  expr: UniformScale = <<Icon_Params>>.IconScale
FEATURE [Part::Scale] Scale021  label="Town_Crier-Scale"
  Base = -> Extrude021
  Uniform = true
  UniformScale = 1.5
  XScale = 1
  YScale = 1
  ZScale = 1
  expr: UniformScale = <<Icon_Params>>.IconScale
FEATURE [Part::Scale] Scale022  label="Vigormortis-Scale"
  Base = -> Extrude022
  Uniform = true
  UniformScale = 1.5
  XScale = 1
  YScale = 1
  ZScale = 1
  expr: UniformScale = <<Icon_Params>>.IconScale
FEATURE [Part::Scale] Scale023  label="Vortox-Scale"
  Base = -> Extrude023
  Uniform = true
  UniformScale = 1.5
  XScale = 1
  YScale = 1
  ZScale = 1
  expr: UniformScale = <<Icon_Params>>.IconScale
FEATURE [Part::Scale] Scale024  label="Witch-Scale"
  Base = -> Extrude024
  Uniform = true
  UniformScale = 1.5
  XScale = 1
  YScale = 1
  ZScale = 1
  expr: UniformScale = <<Icon_Params>>.IconScale
